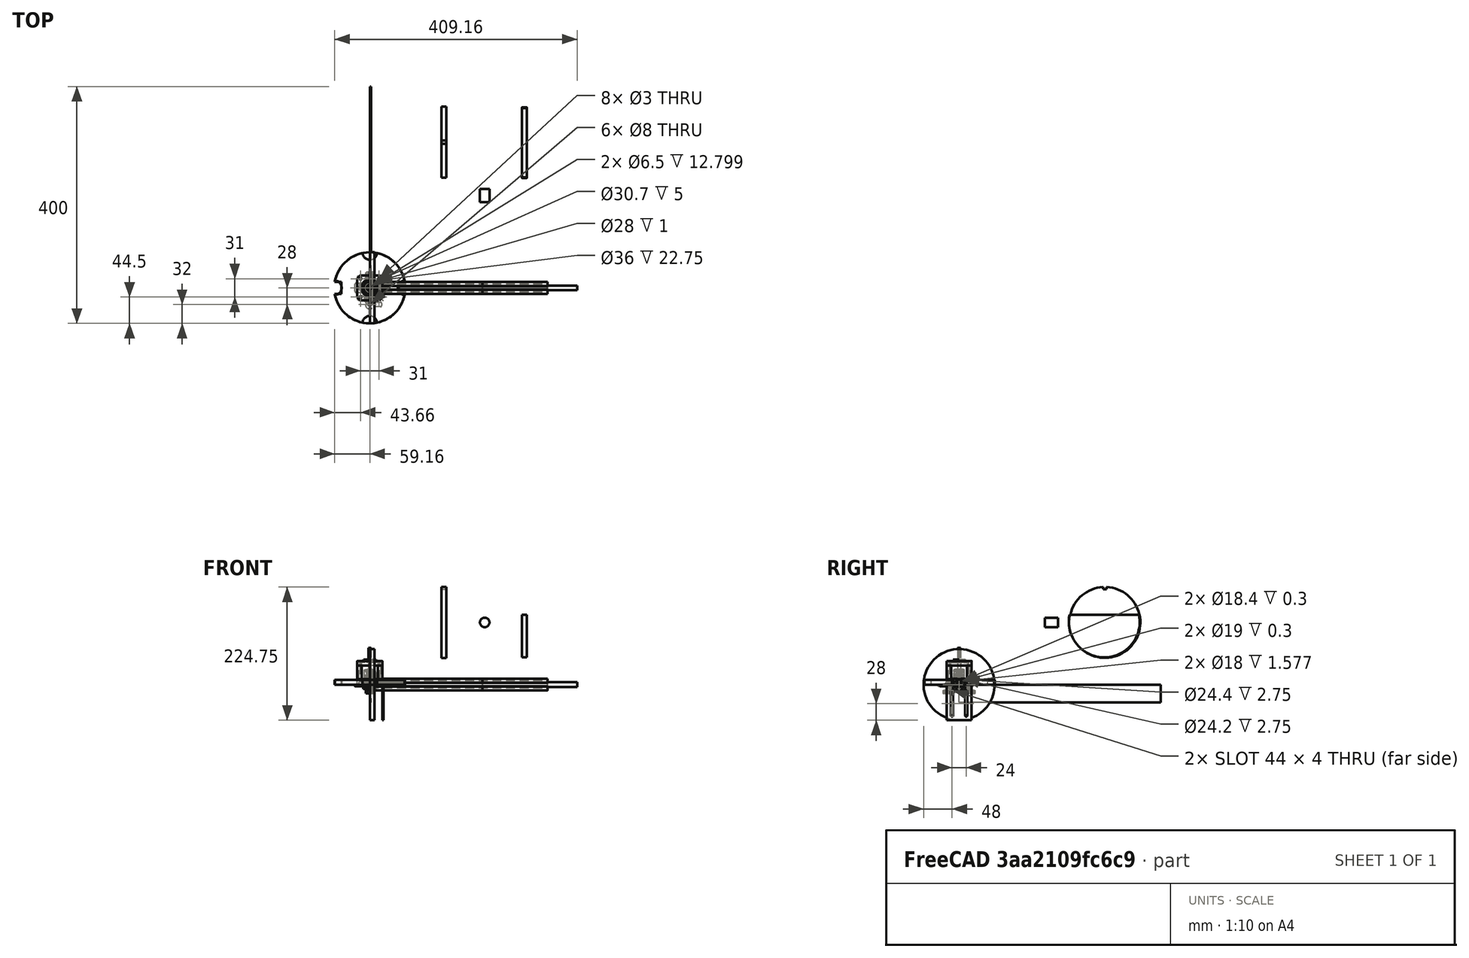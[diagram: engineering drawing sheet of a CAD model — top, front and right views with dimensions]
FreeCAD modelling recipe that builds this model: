
FCSTD DOCUMENT  (FreeCAD 0.19R)
Label: proyectoFinal
License: All rights reserved
LicenseURL: http://en.wikipedia.org/wiki/All_rights_reserved
objects: Sketcher::SketchObject×364, PartDesign::Body×273, PartDesign::Pad×225, PartDesign::Fillet×183, App::Part×132, PartDesign::Pocket×123, PartDesign::FeatureBase×92, PartDesign::Revolution×52, App::DocumentObjectGroup×42, App::LinkGroup×32, PartDesign::PolarPattern×29, PartDesign::Chamfer×21, PartDesign::Groove×8, Part::FeaturePython×8, PartDesign::Mirrored×6, PartDesign::ShapeBinder×5, PartDesign::Hole×2, PartDesign::Draft×2, PartDesign::LinearPattern×2, PartDesign::Plane×2, +5 more types
note: 2026 computed .brp shape members not serialized (recipe doc carries the construction recipe); baked Part::Feature solids carry a one-line shape summary decoded from their .brp

FEATURE [Sketcher::SketchObject] Sketch001
  FullyConstrained = false
  MapMode = 5
  Support = -> [XY_Plane003]
  sketch-geometry (46):
    g0: LineSegment StartX=3.4 StartY=2.65 StartZ=0 EndX=3.4 EndY=-2.6657 EndZ=0
    g1: LineSegment StartX=2.63162 StartY=-3.4 StartZ=0 EndX=-2.65 EndY=-3.4 EndZ=0
    g2: LineSegment StartX=-3.4 StartY=-2.63136 StartZ=0 EndX=-3.4 EndY=2.61487 EndZ=0
    g3: LineSegment StartX=-10 StartY=10 StartZ=0 EndX=-3.125 EndY=10 EndZ=0
    g4: LineSegment StartX=10 StartY=10 StartZ=0 EndX=10 EndY=3.125 EndZ=0
    g5: LineSegment StartX=10 StartY=-10 StartZ=0 EndX=3.125 EndY=-10 EndZ=0
    g6: LineSegment StartX=-10 StartY=-10 StartZ=0 EndX=-10 EndY=-3.125 EndZ=0
    g7: GeomPoint X=3e-16 Y=0 Z=0
    g8: Circle CenterX=3e-16 CenterY=0 CenterZ=0 NormalX=0 NormalY=0 NormalZ=1 AngleXU=0 Radius=2.1
    g9: LineSegment StartX=-4.76483 StartY=8.08721 StartZ=0 EndX=-3.55 EndY=8.08721 EndZ=0
    g10: LineSegment StartX=8.24722 StartY=4.75 StartZ=0 EndX=8.24722 EndY=3.55 EndZ=0
    g11: LineSegment StartX=-8.2 StartY=-4.73729 StartZ=0 EndX=-8.2 EndY=-3.55 EndZ=0
    g12: LineSegment StartX=5.5 StartY=4.75 StartZ=0 EndX=8.24722 EndY=4.75 EndZ=0
    g13: LineSegment StartX=4.75 StartY=5.50457 StartZ=0 EndX=2.65 EndY=3.4 EndZ=0
    g14: LineSegment StartX=4.75 StartY=5.50457 StartZ=0 EndX=4.75 EndY=8.08721 EndZ=0
    g15: LineSegment StartX=3.4 StartY=2.65 StartZ=0 EndX=5.5 EndY=4.75 EndZ=0
    g16: LineSegment StartX=-4.76483 StartY=5.50457 StartZ=0 EndX=-2.66166 EndY=3.4 EndZ=0
    g17: LineSegment StartX=-5.5 StartY=4.70904 StartZ=0 EndX=-3.4 EndY=2.61487 EndZ=0
    g18: LineSegment StartX=-4.76483 StartY=5.50457 StartZ=0 EndX=-4.76483 EndY=8.08721 EndZ=0
    g19: LineSegment StartX=-5.5 StartY=4.70904 StartZ=0 EndX=-8.2 EndY=4.70904 EndZ=0
    g20: LineSegment StartX=-10 StartY=3.125 StartZ=0 EndX=-10 EndY=10 EndZ=0
    g21: LineSegment StartX=-8.2 StartY=3.55 StartZ=0 EndX=-8.2 EndY=4.70904 EndZ=0
    g22: LineSegment StartX=3.55 StartY=8.08721 StartZ=0 EndX=4.75 EndY=8.08721 EndZ=0
    g23: LineSegment StartX=3.125 StartY=10 StartZ=0 EndX=10 EndY=10 EndZ=0
    g24: LineSegment StartX=-5.5 StartY=-4.73729 StartZ=0 EndX=-8.2 EndY=-4.73729 EndZ=0
    g25: LineSegment StartX=-4.75 StartY=-5.5 StartZ=0 EndX=-2.65 EndY=-3.4 EndZ=0
    g26: LineSegment StartX=-4.75 StartY=-5.5 StartZ=0 EndX=-4.75 EndY=-8.2 EndZ=0
    g27: LineSegment StartX=4.73747 StartY=-5.5 StartZ=0 EndX=4.73747 EndY=-8.2 EndZ=0
    g28: LineSegment StartX=5.5 StartY=-4.7671 StartZ=0 EndX=8.24722 EndY=-4.7671 EndZ=0
    g29: LineSegment StartX=-3.125 StartY=-10 StartZ=0 EndX=-10 EndY=-10 EndZ=0
    g30: LineSegment StartX=-3.55 StartY=-8.2 StartZ=0 EndX=-4.75 EndY=-8.2 EndZ=0
    g31: LineSegment StartX=4.73747 StartY=-8.2 StartZ=0 EndX=3.55 EndY=-8.2 EndZ=0
    g32: LineSegment StartX=10 StartY=-3.125 StartZ=0 EndX=10 EndY=-10 EndZ=0
    g33: LineSegment StartX=8.24722 StartY=-3.55 StartZ=0 EndX=8.24722 EndY=-4.7671 EndZ=0
    g34: LineSegment StartX=-2.66166 StartY=3.4 StartZ=0 EndX=2.65 EndY=3.4 EndZ=0
    g35: LineSegment StartX=-3.4 StartY=-2.63136 StartZ=0 EndX=-5.5 EndY=-4.73729 EndZ=0
    g36: LineSegment StartX=3.4 StartY=-2.6657 StartZ=0 EndX=5.5 EndY=-4.7671 EndZ=0
    g37: LineSegment StartX=2.63162 StartY=-3.4 StartZ=0 EndX=4.73747 EndY=-5.5 EndZ=0
    g38: LineSegment StartX=-3.55 StartY=-8.2 StartZ=0 EndX=-3.125 EndY=-10 EndZ=0
    g39: LineSegment StartX=3.55 StartY=-8.2 StartZ=0 EndX=3.125 EndY=-10 EndZ=0
    g40: LineSegment StartX=-3.125 StartY=10 StartZ=0 EndX=-3.55 EndY=8.08721 EndZ=0
    g41: LineSegment StartX=3.125 StartY=10 StartZ=0 EndX=3.55 EndY=8.08721 EndZ=0
    g42: LineSegment StartX=8.24722 StartY=3.55 StartZ=0 EndX=10 EndY=3.125 EndZ=0
    g43: LineSegment StartX=10 StartY=-3.125 StartZ=0 EndX=8.24722 EndY=-3.55 EndZ=0
    g44: LineSegment StartX=-10 StartY=-3.125 StartZ=0 EndX=-8.2 EndY=-3.55 EndZ=0
    g45: LineSegment StartX=-10 StartY=3.125 StartZ=0 EndX=-8.2 EndY=3.55 EndZ=0
  constraints (61):
    c: Horizontal(g1)
    c: Vertical(g0)
    c: Vertical(g2)
    c: Coincident(g23,g4)
    c: Coincident(g32,g5)
    c: Coincident(g29,g6)
    c: Coincident(g20,g3)
    c: Horizontal(g3)
    c: Horizontal(g5)
    c: Vertical(g4)
    c: Vertical(g6)
    c: PointOnObject(g7,g-1)
    c: DistanceX(g3,g7) = 10
    c: DistanceX(g-1,g23) = 10
    c: DistanceY(g7,g3) = 10
    c: DistanceX(g3,g-1) = 10
    c: DistanceY(g32,g7) = 10
    c: Coincident(g8,g7)
    c: Radius(g8) = 2.1
    c: Horizontal(g9)
    c: Vertical(g10)
    c: Vertical(g11)
    c: Coincident(g12,g15)
    c: Horizontal(g12)
    c: Coincident(g14,g13)
    c: Vertical(g14)
    c: Coincident(g15,g0)
    c: Coincident(g13,g34)
    c: Coincident(g14,g22)
    c: Coincident(g18,g16)
    c: Vertical(g18)
    c: Coincident(g19,g17)
    c: Horizontal(g19)
    c: Coincident(g9,g18)
    c: Coincident(g21,g19)
    c: Coincident(g24,g35)
    c: Horizontal(g24)
    c: Coincident(g26,g25)
    c: Vertical(g26)
    c: Coincident(g27,g37)
    c: Vertical(g27)
    c: Coincident(g28,g36)
    c: Horizontal(g28)
    c: Coincident(g11,g24)
    c: Coincident(g26,g30)
    c: Coincident(g31,g27)
    c: Coincident(g12,g10)
    c: Coincident(g28,g33)
    c: Coincident(g25,g1)
    c: Coincident(g35,g2)
    c: Coincident(g17,g2)
    c: Coincident(g16,g34)
    c: Coincident(g1,g37)
    c: Coincident(g0,g36)
    c: Coincident(g39,g5)
    c: Coincident(g40,g3)
    c: Coincident(g42,g4)
    c: Coincident(g44,g6)
    c: Coincident(g21,g45)
    c: Coincident(g33,g43)
    c: Coincident(g10,g42)
FEATURE [PartDesign::Pad] Pad001
  Direction = (0,0,1)
  Length = 300
  Length2 = 10
  Profile = -> Sketch001
  Type = 0
FEATURE [PartDesign::Fillet] Fillet011
  Base = -> Pad001 [Edge53]
  BaseFeature = -> Pad001
  Radius = 1
  SupportTransform = false
FEATURE [PartDesign::Fillet] Fillet012
  Base = -> Fillet011 [Edge114]
  BaseFeature = -> Fillet011
  Radius = 1
  SupportTransform = false
FEATURE [PartDesign::Fillet] Fillet013
  Base = -> Fillet012 [Edge137,Edge95]
  BaseFeature = -> Fillet012
  Radius = 0.5
  SupportTransform = false
FEATURE [PartDesign::Fillet] Fillet014
  Base = -> Fillet013 [Edge103]
  BaseFeature = -> Fillet013
  Radius = 0.5
  SupportTransform = false
FEATURE [PartDesign::Fillet] Fillet015
  Base = -> Fillet014 [Edge96]
  BaseFeature = -> Fillet014
  Radius = 0.5
  SupportTransform = false
FEATURE [PartDesign::Fillet] Fillet016
  Base = -> Fillet015 [Edge77]
  BaseFeature = -> Fillet015
  Radius = 0.5
  SupportTransform = false
FEATURE [PartDesign::Fillet] Fillet017
  Base = -> Fillet016 [Edge102]
  BaseFeature = -> Fillet016
  Radius = 0.5
  SupportTransform = false
FEATURE [PartDesign::Fillet] Fillet018
  Base = -> Fillet017 [Edge85]
  BaseFeature = -> Fillet017
  Radius = 0.5
  SupportTransform = false
FEATURE [PartDesign::Fillet] Fillet019
  Base = -> Fillet018 [Edge78]
  BaseFeature = -> Fillet018
  Radius = 0.5
  SupportTransform = false
FEATURE [PartDesign::Fillet] Fillet020
  Base = -> Fillet019 [Edge107]
  BaseFeature = -> Fillet019
  Radius = 0.5
  SupportTransform = false
FEATURE [PartDesign::Fillet] Fillet021
  Base = -> Fillet020 [Edge74]
  BaseFeature = -> Fillet020
  Radius = 0.5
  SupportTransform = false
FEATURE [PartDesign::Body] Body001
  Group = -> [Sketch001,Pad001,Fillet011,Fillet012,Fillet013,Fillet014,Fillet015,Fillet016,Fillet017,Fillet018,Fillet019,Fillet020,Fillet021]
  Origin = -> Origin003
  Placement = pos=(0,0,0) rot=(0,1,0;1.5708rad)
  Tip = -> Fillet021
FEATURE [App::Part] Part001  label="2020-300-002"
  Group = -> [Body001]
  Origin = -> Origin002
  Placement = pos=(20,330,10) rot=(0,0,1;0rad)
FEATURE [Sketcher::SketchObject] Sketch002
  FullyConstrained = false
  MapMode = 5
  Support = -> [XY_Plane005]
  sketch-geometry (46):
    g0: LineSegment StartX=3.4 StartY=2.65 StartZ=0 EndX=3.4 EndY=-2.6657 EndZ=0
    g1: LineSegment StartX=2.63162 StartY=-3.4 StartZ=0 EndX=-2.65 EndY=-3.4 EndZ=0
    g2: LineSegment StartX=-3.4 StartY=-2.63136 StartZ=0 EndX=-3.4 EndY=2.61487 EndZ=0
    g3: LineSegment StartX=-10 StartY=10 StartZ=0 EndX=-3.125 EndY=10 EndZ=0
    g4: LineSegment StartX=10 StartY=10 StartZ=0 EndX=10 EndY=3.125 EndZ=0
    g5: LineSegment StartX=10 StartY=-10 StartZ=0 EndX=3.125 EndY=-10 EndZ=0
    g6: LineSegment StartX=-10 StartY=-10 StartZ=0 EndX=-10 EndY=-3.125 EndZ=0
    g7: GeomPoint X=3e-16 Y=0 Z=0
    g8: Circle CenterX=3e-16 CenterY=0 CenterZ=0 NormalX=0 NormalY=0 NormalZ=1 AngleXU=0 Radius=2.1
    g9: LineSegment StartX=-4.76483 StartY=8.08721 StartZ=0 EndX=-3.55 EndY=8.08721 EndZ=0
    g10: LineSegment StartX=8.24722 StartY=4.75 StartZ=0 EndX=8.24722 EndY=3.55 EndZ=0
    g11: LineSegment StartX=-8.2 StartY=-4.73729 StartZ=0 EndX=-8.2 EndY=-3.55 EndZ=0
    g12: LineSegment StartX=5.5 StartY=4.75 StartZ=0 EndX=8.24722 EndY=4.75 EndZ=0
    g13: LineSegment StartX=4.75 StartY=5.50457 StartZ=0 EndX=2.65 EndY=3.4 EndZ=0
    g14: LineSegment StartX=4.75 StartY=5.50457 StartZ=0 EndX=4.75 EndY=8.08721 EndZ=0
    g15: LineSegment StartX=3.4 StartY=2.65 StartZ=0 EndX=5.5 EndY=4.75 EndZ=0
    g16: LineSegment StartX=-4.76483 StartY=5.50457 StartZ=0 EndX=-2.66166 EndY=3.4 EndZ=0
    g17: LineSegment StartX=-5.5 StartY=4.70904 StartZ=0 EndX=-3.4 EndY=2.61487 EndZ=0
    g18: LineSegment StartX=-4.76483 StartY=5.50457 StartZ=0 EndX=-4.76483 EndY=8.08721 EndZ=0
    g19: LineSegment StartX=-5.5 StartY=4.70904 StartZ=0 EndX=-8.2 EndY=4.70904 EndZ=0
    g20: LineSegment StartX=-10 StartY=3.125 StartZ=0 EndX=-10 EndY=10 EndZ=0
    g21: LineSegment StartX=-8.2 StartY=3.55 StartZ=0 EndX=-8.2 EndY=4.70904 EndZ=0
    g22: LineSegment StartX=3.55 StartY=8.08721 StartZ=0 EndX=4.75 EndY=8.08721 EndZ=0
    g23: LineSegment StartX=3.125 StartY=10 StartZ=0 EndX=10 EndY=10 EndZ=0
    g24: LineSegment StartX=-5.5 StartY=-4.73729 StartZ=0 EndX=-8.2 EndY=-4.73729 EndZ=0
    g25: LineSegment StartX=-4.75 StartY=-5.5 StartZ=0 EndX=-2.65 EndY=-3.4 EndZ=0
    g26: LineSegment StartX=-4.75 StartY=-5.5 StartZ=0 EndX=-4.75 EndY=-8.2 EndZ=0
    g27: LineSegment StartX=4.73747 StartY=-5.5 StartZ=0 EndX=4.73747 EndY=-8.2 EndZ=0
    g28: LineSegment StartX=5.5 StartY=-4.7671 StartZ=0 EndX=8.24722 EndY=-4.7671 EndZ=0
    g29: LineSegment StartX=-3.125 StartY=-10 StartZ=0 EndX=-10 EndY=-10 EndZ=0
    g30: LineSegment StartX=-3.55 StartY=-8.2 StartZ=0 EndX=-4.75 EndY=-8.2 EndZ=0
    g31: LineSegment StartX=4.73747 StartY=-8.2 StartZ=0 EndX=3.55 EndY=-8.2 EndZ=0
    g32: LineSegment StartX=10 StartY=-3.125 StartZ=0 EndX=10 EndY=-10 EndZ=0
    g33: LineSegment StartX=8.24722 StartY=-3.55 StartZ=0 EndX=8.24722 EndY=-4.7671 EndZ=0
    g34: LineSegment StartX=-2.66166 StartY=3.4 StartZ=0 EndX=2.65 EndY=3.4 EndZ=0
    g35: LineSegment StartX=-3.4 StartY=-2.63136 StartZ=0 EndX=-5.5 EndY=-4.73729 EndZ=0
    g36: LineSegment StartX=3.4 StartY=-2.6657 StartZ=0 EndX=5.5 EndY=-4.7671 EndZ=0
    g37: LineSegment StartX=2.63162 StartY=-3.4 StartZ=0 EndX=4.73747 EndY=-5.5 EndZ=0
    g38: LineSegment StartX=-3.55 StartY=-8.2 StartZ=0 EndX=-3.125 EndY=-10 EndZ=0
    g39: LineSegment StartX=3.55 StartY=-8.2 StartZ=0 EndX=3.125 EndY=-10 EndZ=0
    g40: LineSegment StartX=-3.125 StartY=10 StartZ=0 EndX=-3.55 EndY=8.08721 EndZ=0
    g41: LineSegment StartX=3.125 StartY=10 StartZ=0 EndX=3.55 EndY=8.08721 EndZ=0
    g42: LineSegment StartX=8.24722 StartY=3.55 StartZ=0 EndX=10 EndY=3.125 EndZ=0
    g43: LineSegment StartX=10 StartY=-3.125 StartZ=0 EndX=8.24722 EndY=-3.55 EndZ=0
    g44: LineSegment StartX=-10 StartY=-3.125 StartZ=0 EndX=-8.2 EndY=-3.55 EndZ=0
    g45: LineSegment StartX=-10 StartY=3.125 StartZ=0 EndX=-8.2 EndY=3.55 EndZ=0
  constraints (61):
    c: Horizontal(g1)
    c: Vertical(g0)
    c: Vertical(g2)
    c: Coincident(g23,g4)
    c: Coincident(g32,g5)
    c: Coincident(g29,g6)
    c: Coincident(g20,g3)
    c: Horizontal(g3)
    c: Horizontal(g5)
    c: Vertical(g4)
    c: Vertical(g6)
    c: PointOnObject(g7,g-1)
    c: DistanceX(g3,g7) = 10
    c: DistanceX(g-1,g23) = 10
    c: DistanceY(g7,g3) = 10
    c: DistanceX(g3,g-1) = 10
    c: DistanceY(g32,g7) = 10
    c: Coincident(g8,g7)
    c: Radius(g8) = 2.1
    c: Horizontal(g9)
    c: Vertical(g10)
    c: Vertical(g11)
    c: Coincident(g12,g15)
    c: Horizontal(g12)
    c: Coincident(g14,g13)
    c: Vertical(g14)
    c: Coincident(g15,g0)
    c: Coincident(g13,g34)
    c: Coincident(g14,g22)
    c: Coincident(g18,g16)
    c: Vertical(g18)
    c: Coincident(g19,g17)
    c: Horizontal(g19)
    c: Coincident(g9,g18)
    c: Coincident(g21,g19)
    c: Coincident(g24,g35)
    c: Horizontal(g24)
    c: Coincident(g26,g25)
    c: Vertical(g26)
    c: Coincident(g27,g37)
    c: Vertical(g27)
    c: Coincident(g28,g36)
    c: Horizontal(g28)
    c: Coincident(g11,g24)
    c: Coincident(g26,g30)
    c: Coincident(g31,g27)
    c: Coincident(g12,g10)
    c: Coincident(g28,g33)
    c: Coincident(g25,g1)
    c: Coincident(g35,g2)
    c: Coincident(g17,g2)
    c: Coincident(g16,g34)
    c: Coincident(g1,g37)
    c: Coincident(g0,g36)
    c: Coincident(g39,g5)
    c: Coincident(g40,g3)
    c: Coincident(g42,g4)
    c: Coincident(g44,g6)
    c: Coincident(g21,g45)
    c: Coincident(g33,g43)
    c: Coincident(g10,g42)
FEATURE [PartDesign::Pad] Pad002
  Direction = (0,0,1)
  Length = 300
  Length2 = 10
  Profile = -> Sketch002
  Type = 0
FEATURE [PartDesign::Fillet] Fillet022
  Base = -> Pad002 [Edge53]
  BaseFeature = -> Pad002
  Radius = 1
  SupportTransform = false
FEATURE [PartDesign::Fillet] Fillet023
  Base = -> Fillet022 [Edge114]
  BaseFeature = -> Fillet022
  Radius = 1
  SupportTransform = false
FEATURE [PartDesign::Fillet] Fillet024
  Base = -> Fillet023 [Edge137,Edge95]
  BaseFeature = -> Fillet023
  Radius = 0.5
  SupportTransform = false
FEATURE [PartDesign::Fillet] Fillet025
  Base = -> Fillet024 [Edge103]
  BaseFeature = -> Fillet024
  Radius = 0.5
  SupportTransform = false
FEATURE [PartDesign::Fillet] Fillet026
  Base = -> Fillet025 [Edge96]
  BaseFeature = -> Fillet025
  Radius = 0.5
  SupportTransform = false
FEATURE [PartDesign::Fillet] Fillet027
  Base = -> Fillet026 [Edge77]
  BaseFeature = -> Fillet026
  Radius = 0.5
  SupportTransform = false
FEATURE [PartDesign::Fillet] Fillet028
  Base = -> Fillet027 [Edge102]
  BaseFeature = -> Fillet027
  Radius = 0.5
  SupportTransform = false
FEATURE [PartDesign::Fillet] Fillet029
  Base = -> Fillet028 [Edge85]
  BaseFeature = -> Fillet028
  Radius = 0.5
  SupportTransform = false
FEATURE [PartDesign::Fillet] Fillet030
  Base = -> Fillet029 [Edge78]
  BaseFeature = -> Fillet029
  Radius = 0.5
  SupportTransform = false
FEATURE [PartDesign::Fillet] Fillet031
  Base = -> Fillet030 [Edge107]
  BaseFeature = -> Fillet030
  Radius = 0.5
  SupportTransform = false
FEATURE [PartDesign::Fillet] Fillet032
  Base = -> Fillet031 [Edge74]
  BaseFeature = -> Fillet031
  Radius = 0.5
  SupportTransform = false
FEATURE [PartDesign::Body] Body002
  Group = -> [Sketch002,Pad002,Fillet022,Fillet023,Fillet024,Fillet025,Fillet026,Fillet027,Fillet028,Fillet029,Fillet030,Fillet031,Fillet032]
  Origin = -> Origin005
  Placement = pos=(0,0,0) rot=(0,1,0;1.5708rad)
  Tip = -> Fillet032
FEATURE [App::Part] Part002  label="2020-300-003"
  Group = -> [Body002]
  Origin = -> Origin004
  Placement = pos=(10,20,10) rot=(0,0,1;1.5708rad)
FEATURE [Sketcher::SketchObject] Sketch003
  FullyConstrained = false
  MapMode = 5
  Support = -> [XY_Plane007]
  sketch-geometry (46):
    g0: LineSegment StartX=3.4 StartY=2.65 StartZ=0 EndX=3.4 EndY=-2.6657 EndZ=0
    g1: LineSegment StartX=2.63162 StartY=-3.4 StartZ=0 EndX=-2.65 EndY=-3.4 EndZ=0
    g2: LineSegment StartX=-3.4 StartY=-2.63136 StartZ=0 EndX=-3.4 EndY=2.61487 EndZ=0
    g3: LineSegment StartX=-10 StartY=10 StartZ=0 EndX=-3.125 EndY=10 EndZ=0
    g4: LineSegment StartX=10 StartY=10 StartZ=0 EndX=10 EndY=3.125 EndZ=0
    g5: LineSegment StartX=10 StartY=-10 StartZ=0 EndX=3.125 EndY=-10 EndZ=0
    g6: LineSegment StartX=-10 StartY=-10 StartZ=0 EndX=-10 EndY=-3.125 EndZ=0
    g7: GeomPoint X=3e-16 Y=0 Z=0
    g8: Circle CenterX=3e-16 CenterY=0 CenterZ=0 NormalX=0 NormalY=0 NormalZ=1 AngleXU=0 Radius=2.1
    g9: LineSegment StartX=-4.76483 StartY=8.08721 StartZ=0 EndX=-3.55 EndY=8.08721 EndZ=0
    g10: LineSegment StartX=8.24722 StartY=4.75 StartZ=0 EndX=8.24722 EndY=3.55 EndZ=0
    g11: LineSegment StartX=-8.2 StartY=-4.73729 StartZ=0 EndX=-8.2 EndY=-3.55 EndZ=0
    g12: LineSegment StartX=5.5 StartY=4.75 StartZ=0 EndX=8.24722 EndY=4.75 EndZ=0
    g13: LineSegment StartX=4.75 StartY=5.50457 StartZ=0 EndX=2.65 EndY=3.4 EndZ=0
    g14: LineSegment StartX=4.75 StartY=5.50457 StartZ=0 EndX=4.75 EndY=8.08721 EndZ=0
    g15: LineSegment StartX=3.4 StartY=2.65 StartZ=0 EndX=5.5 EndY=4.75 EndZ=0
    g16: LineSegment StartX=-4.76483 StartY=5.50457 StartZ=0 EndX=-2.66166 EndY=3.4 EndZ=0
    g17: LineSegment StartX=-5.5 StartY=4.70904 StartZ=0 EndX=-3.4 EndY=2.61487 EndZ=0
    g18: LineSegment StartX=-4.76483 StartY=5.50457 StartZ=0 EndX=-4.76483 EndY=8.08721 EndZ=0
    g19: LineSegment StartX=-5.5 StartY=4.70904 StartZ=0 EndX=-8.2 EndY=4.70904 EndZ=0
    g20: LineSegment StartX=-10 StartY=3.125 StartZ=0 EndX=-10 EndY=10 EndZ=0
    g21: LineSegment StartX=-8.2 StartY=3.55 StartZ=0 EndX=-8.2 EndY=4.70904 EndZ=0
    g22: LineSegment StartX=3.55 StartY=8.08721 StartZ=0 EndX=4.75 EndY=8.08721 EndZ=0
    g23: LineSegment StartX=3.125 StartY=10 StartZ=0 EndX=10 EndY=10 EndZ=0
    g24: LineSegment StartX=-5.5 StartY=-4.73729 StartZ=0 EndX=-8.2 EndY=-4.73729 EndZ=0
    g25: LineSegment StartX=-4.75 StartY=-5.5 StartZ=0 EndX=-2.65 EndY=-3.4 EndZ=0
    g26: LineSegment StartX=-4.75 StartY=-5.5 StartZ=0 EndX=-4.75 EndY=-8.2 EndZ=0
    g27: LineSegment StartX=4.73747 StartY=-5.5 StartZ=0 EndX=4.73747 EndY=-8.2 EndZ=0
    g28: LineSegment StartX=5.5 StartY=-4.7671 StartZ=0 EndX=8.24722 EndY=-4.7671 EndZ=0
    g29: LineSegment StartX=-3.125 StartY=-10 StartZ=0 EndX=-10 EndY=-10 EndZ=0
    g30: LineSegment StartX=-3.55 StartY=-8.2 StartZ=0 EndX=-4.75 EndY=-8.2 EndZ=0
    g31: LineSegment StartX=4.73747 StartY=-8.2 StartZ=0 EndX=3.55 EndY=-8.2 EndZ=0
    g32: LineSegment StartX=10 StartY=-3.125 StartZ=0 EndX=10 EndY=-10 EndZ=0
    g33: LineSegment StartX=8.24722 StartY=-3.55 StartZ=0 EndX=8.24722 EndY=-4.7671 EndZ=0
    g34: LineSegment StartX=-2.66166 StartY=3.4 StartZ=0 EndX=2.65 EndY=3.4 EndZ=0
    g35: LineSegment StartX=-3.4 StartY=-2.63136 StartZ=0 EndX=-5.5 EndY=-4.73729 EndZ=0
    g36: LineSegment StartX=3.4 StartY=-2.6657 StartZ=0 EndX=5.5 EndY=-4.7671 EndZ=0
    g37: LineSegment StartX=2.63162 StartY=-3.4 StartZ=0 EndX=4.73747 EndY=-5.5 EndZ=0
    g38: LineSegment StartX=-3.55 StartY=-8.2 StartZ=0 EndX=-3.125 EndY=-10 EndZ=0
    g39: LineSegment StartX=3.55 StartY=-8.2 StartZ=0 EndX=3.125 EndY=-10 EndZ=0
    g40: LineSegment StartX=-3.125 StartY=10 StartZ=0 EndX=-3.55 EndY=8.08721 EndZ=0
    g41: LineSegment StartX=3.125 StartY=10 StartZ=0 EndX=3.55 EndY=8.08721 EndZ=0
    g42: LineSegment StartX=8.24722 StartY=3.55 StartZ=0 EndX=10 EndY=3.125 EndZ=0
    g43: LineSegment StartX=10 StartY=-3.125 StartZ=0 EndX=8.24722 EndY=-3.55 EndZ=0
    g44: LineSegment StartX=-10 StartY=-3.125 StartZ=0 EndX=-8.2 EndY=-3.55 EndZ=0
    g45: LineSegment StartX=-10 StartY=3.125 StartZ=0 EndX=-8.2 EndY=3.55 EndZ=0
  constraints (61):
    c: Horizontal(g1)
    c: Vertical(g0)
    c: Vertical(g2)
    c: Coincident(g23,g4)
    c: Coincident(g32,g5)
    c: Coincident(g29,g6)
    c: Coincident(g20,g3)
    c: Horizontal(g3)
    c: Horizontal(g5)
    c: Vertical(g4)
    c: Vertical(g6)
    c: PointOnObject(g7,g-1)
    c: DistanceX(g3,g7) = 10
    c: DistanceX(g-1,g23) = 10
    c: DistanceY(g7,g3) = 10
    c: DistanceX(g3,g-1) = 10
    c: DistanceY(g32,g7) = 10
    c: Coincident(g8,g7)
    c: Radius(g8) = 2.1
    c: Horizontal(g9)
    c: Vertical(g10)
    c: Vertical(g11)
    c: Coincident(g12,g15)
    c: Horizontal(g12)
    c: Coincident(g14,g13)
    c: Vertical(g14)
    c: Coincident(g15,g0)
    c: Coincident(g13,g34)
    c: Coincident(g14,g22)
    c: Coincident(g18,g16)
    c: Vertical(g18)
    c: Coincident(g19,g17)
    c: Horizontal(g19)
    c: Coincident(g9,g18)
    c: Coincident(g21,g19)
    c: Coincident(g24,g35)
    c: Horizontal(g24)
    c: Coincident(g26,g25)
    c: Vertical(g26)
    c: Coincident(g27,g37)
    c: Vertical(g27)
    c: Coincident(g28,g36)
    c: Horizontal(g28)
    c: Coincident(g11,g24)
    c: Coincident(g26,g30)
    c: Coincident(g31,g27)
    c: Coincident(g12,g10)
    c: Coincident(g28,g33)
    c: Coincident(g25,g1)
    c: Coincident(g35,g2)
    c: Coincident(g17,g2)
    c: Coincident(g16,g34)
    c: Coincident(g1,g37)
    c: Coincident(g0,g36)
    c: Coincident(g39,g5)
    c: Coincident(g40,g3)
    c: Coincident(g42,g4)
    c: Coincident(g44,g6)
    c: Coincident(g21,g45)
    c: Coincident(g33,g43)
    c: Coincident(g10,g42)
FEATURE [PartDesign::Pad] Pad003
  Direction = (0,0,1)
  Length = 300
  Length2 = 10
  Profile = -> Sketch003
  Type = 0
FEATURE [PartDesign::Fillet] Fillet033
  Base = -> Pad003 [Edge53]
  BaseFeature = -> Pad003
  Radius = 1
  SupportTransform = false
FEATURE [PartDesign::Fillet] Fillet034
  Base = -> Fillet033 [Edge114]
  BaseFeature = -> Fillet033
  Radius = 1
  SupportTransform = false
FEATURE [PartDesign::Fillet] Fillet035
  Base = -> Fillet034 [Edge137,Edge95]
  BaseFeature = -> Fillet034
  Radius = 0.5
  SupportTransform = false
FEATURE [PartDesign::Fillet] Fillet036
  Base = -> Fillet035 [Edge103]
  BaseFeature = -> Fillet035
  Radius = 0.5
  SupportTransform = false
FEATURE [PartDesign::Fillet] Fillet037
  Base = -> Fillet036 [Edge96]
  BaseFeature = -> Fillet036
  Radius = 0.5
  SupportTransform = false
FEATURE [PartDesign::Fillet] Fillet038
  Base = -> Fillet037 [Edge77]
  BaseFeature = -> Fillet037
  Radius = 0.5
  SupportTransform = false
FEATURE [PartDesign::Fillet] Fillet039
  Base = -> Fillet038 [Edge102]
  BaseFeature = -> Fillet038
  Radius = 0.5
  SupportTransform = false
FEATURE [PartDesign::Fillet] Fillet040
  Base = -> Fillet039 [Edge85]
  BaseFeature = -> Fillet039
  Radius = 0.5
  SupportTransform = false
FEATURE [PartDesign::Fillet] Fillet041
  Base = -> Fillet040 [Edge78]
  BaseFeature = -> Fillet040
  Radius = 0.5
  SupportTransform = false
FEATURE [PartDesign::Fillet] Fillet042
  Base = -> Fillet041 [Edge107]
  BaseFeature = -> Fillet041
  Radius = 0.5
  SupportTransform = false
FEATURE [PartDesign::Fillet] Fillet043
  Base = -> Fillet042 [Edge74]
  BaseFeature = -> Fillet042
  Radius = 0.5
  SupportTransform = false
FEATURE [PartDesign::Body] Body003
  Group = -> [Sketch003,Pad003,Fillet033,Fillet034,Fillet035,Fillet036,Fillet037,Fillet038,Fillet039,Fillet040,Fillet041,Fillet042,Fillet043]
  Origin = -> Origin007
  Placement = pos=(0,0,0) rot=(0,1,0;1.5708rad)
  Tip = -> Fillet043
FEATURE [App::Part] Part003  label="2020-300-004"
  Group = -> [Body003]
  Origin = -> Origin006
  Placement = pos=(330,20,10) rot=(0,0,1;1.5708rad)
FEATURE [Sketcher::SketchObject] Sketch004
  FullyConstrained = false
  MapMode = 5
  Support = -> [XY_Plane009]
  sketch-geometry (46):
    g0: LineSegment StartX=3.4 StartY=2.65 StartZ=0 EndX=3.4 EndY=-2.6657 EndZ=0
    g1: LineSegment StartX=2.63162 StartY=-3.4 StartZ=0 EndX=-2.65 EndY=-3.4 EndZ=0
    g2: LineSegment StartX=-3.4 StartY=-2.63136 StartZ=0 EndX=-3.4 EndY=2.61487 EndZ=0
    g3: LineSegment StartX=-10 StartY=10 StartZ=0 EndX=-3.125 EndY=10 EndZ=0
    g4: LineSegment StartX=10 StartY=10 StartZ=0 EndX=10 EndY=3.125 EndZ=0
    g5: LineSegment StartX=10 StartY=-10 StartZ=0 EndX=3.125 EndY=-10 EndZ=0
    g6: LineSegment StartX=-10 StartY=-10 StartZ=0 EndX=-10 EndY=-3.125 EndZ=0
    g7: GeomPoint X=3e-16 Y=0 Z=0
    g8: Circle CenterX=3e-16 CenterY=0 CenterZ=0 NormalX=0 NormalY=0 NormalZ=1 AngleXU=0 Radius=2.1
    g9: LineSegment StartX=-4.76483 StartY=8.08721 StartZ=0 EndX=-3.55 EndY=8.08721 EndZ=0
    g10: LineSegment StartX=8.24722 StartY=4.75 StartZ=0 EndX=8.24722 EndY=3.55 EndZ=0
    g11: LineSegment StartX=-8.2 StartY=-4.73729 StartZ=0 EndX=-8.2 EndY=-3.55 EndZ=0
    g12: LineSegment StartX=5.5 StartY=4.75 StartZ=0 EndX=8.24722 EndY=4.75 EndZ=0
    g13: LineSegment StartX=4.75 StartY=5.50457 StartZ=0 EndX=2.65 EndY=3.4 EndZ=0
    g14: LineSegment StartX=4.75 StartY=5.50457 StartZ=0 EndX=4.75 EndY=8.08721 EndZ=0
    g15: LineSegment StartX=3.4 StartY=2.65 StartZ=0 EndX=5.5 EndY=4.75 EndZ=0
    g16: LineSegment StartX=-4.76483 StartY=5.50457 StartZ=0 EndX=-2.66166 EndY=3.4 EndZ=0
    g17: LineSegment StartX=-5.5 StartY=4.70904 StartZ=0 EndX=-3.4 EndY=2.61487 EndZ=0
    g18: LineSegment StartX=-4.76483 StartY=5.50457 StartZ=0 EndX=-4.76483 EndY=8.08721 EndZ=0
    g19: LineSegment StartX=-5.5 StartY=4.70904 StartZ=0 EndX=-8.2 EndY=4.70904 EndZ=0
    g20: LineSegment StartX=-10 StartY=3.125 StartZ=0 EndX=-10 EndY=10 EndZ=0
    g21: LineSegment StartX=-8.2 StartY=3.55 StartZ=0 EndX=-8.2 EndY=4.70904 EndZ=0
    g22: LineSegment StartX=3.55 StartY=8.08721 StartZ=0 EndX=4.75 EndY=8.08721 EndZ=0
    g23: LineSegment StartX=3.125 StartY=10 StartZ=0 EndX=10 EndY=10 EndZ=0
    g24: LineSegment StartX=-5.5 StartY=-4.73729 StartZ=0 EndX=-8.2 EndY=-4.73729 EndZ=0
    g25: LineSegment StartX=-4.75 StartY=-5.5 StartZ=0 EndX=-2.65 EndY=-3.4 EndZ=0
    g26: LineSegment StartX=-4.75 StartY=-5.5 StartZ=0 EndX=-4.75 EndY=-8.2 EndZ=0
    g27: LineSegment StartX=4.73747 StartY=-5.5 StartZ=0 EndX=4.73747 EndY=-8.2 EndZ=0
    g28: LineSegment StartX=5.5 StartY=-4.7671 StartZ=0 EndX=8.24722 EndY=-4.7671 EndZ=0
    g29: LineSegment StartX=-3.125 StartY=-10 StartZ=0 EndX=-10 EndY=-10 EndZ=0
    g30: LineSegment StartX=-3.55 StartY=-8.2 StartZ=0 EndX=-4.75 EndY=-8.2 EndZ=0
    g31: LineSegment StartX=4.73747 StartY=-8.2 StartZ=0 EndX=3.55 EndY=-8.2 EndZ=0
    g32: LineSegment StartX=10 StartY=-3.125 StartZ=0 EndX=10 EndY=-10 EndZ=0
    g33: LineSegment StartX=8.24722 StartY=-3.55 StartZ=0 EndX=8.24722 EndY=-4.7671 EndZ=0
    g34: LineSegment StartX=-2.66166 StartY=3.4 StartZ=0 EndX=2.65 EndY=3.4 EndZ=0
    g35: LineSegment StartX=-3.4 StartY=-2.63136 StartZ=0 EndX=-5.5 EndY=-4.73729 EndZ=0
    g36: LineSegment StartX=3.4 StartY=-2.6657 StartZ=0 EndX=5.5 EndY=-4.7671 EndZ=0
    g37: LineSegment StartX=2.63162 StartY=-3.4 StartZ=0 EndX=4.73747 EndY=-5.5 EndZ=0
    g38: LineSegment StartX=-3.55 StartY=-8.2 StartZ=0 EndX=-3.125 EndY=-10 EndZ=0
    g39: LineSegment StartX=3.55 StartY=-8.2 StartZ=0 EndX=3.125 EndY=-10 EndZ=0
    g40: LineSegment StartX=-3.125 StartY=10 StartZ=0 EndX=-3.55 EndY=8.08721 EndZ=0
    g41: LineSegment StartX=3.125 StartY=10 StartZ=0 EndX=3.55 EndY=8.08721 EndZ=0
    g42: LineSegment StartX=8.24722 StartY=3.55 StartZ=0 EndX=10 EndY=3.125 EndZ=0
    g43: LineSegment StartX=10 StartY=-3.125 StartZ=0 EndX=8.24722 EndY=-3.55 EndZ=0
    g44: LineSegment StartX=-10 StartY=-3.125 StartZ=0 EndX=-8.2 EndY=-3.55 EndZ=0
    g45: LineSegment StartX=-10 StartY=3.125 StartZ=0 EndX=-8.2 EndY=3.55 EndZ=0
  constraints (61):
    c: Horizontal(g1)
    c: Vertical(g0)
    c: Vertical(g2)
    c: Coincident(g23,g4)
    c: Coincident(g32,g5)
    c: Coincident(g29,g6)
    c: Coincident(g20,g3)
    c: Horizontal(g3)
    c: Horizontal(g5)
    c: Vertical(g4)
    c: Vertical(g6)
    c: PointOnObject(g7,g-1)
    c: DistanceX(g3,g7) = 10
    c: DistanceX(g-1,g23) = 10
    c: DistanceY(g7,g3) = 10
    c: DistanceX(g3,g-1) = 10
    c: DistanceY(g32,g7) = 10
    c: Coincident(g8,g7)
    c: Radius(g8) = 2.1
    c: Horizontal(g9)
    c: Vertical(g10)
    c: Vertical(g11)
    c: Coincident(g12,g15)
    c: Horizontal(g12)
    c: Coincident(g14,g13)
    c: Vertical(g14)
    c: Coincident(g15,g0)
    c: Coincident(g13,g34)
    c: Coincident(g14,g22)
    c: Coincident(g18,g16)
    c: Vertical(g18)
    c: Coincident(g19,g17)
    c: Horizontal(g19)
    c: Coincident(g9,g18)
    c: Coincident(g21,g19)
    c: Coincident(g24,g35)
    c: Horizontal(g24)
    c: Coincident(g26,g25)
    c: Vertical(g26)
    c: Coincident(g27,g37)
    c: Vertical(g27)
    c: Coincident(g28,g36)
    c: Horizontal(g28)
    c: Coincident(g11,g24)
    c: Coincident(g26,g30)
    c: Coincident(g31,g27)
    c: Coincident(g12,g10)
    c: Coincident(g28,g33)
    c: Coincident(g25,g1)
    c: Coincident(g35,g2)
    c: Coincident(g17,g2)
    c: Coincident(g16,g34)
    c: Coincident(g1,g37)
    c: Coincident(g0,g36)
    c: Coincident(g39,g5)
    c: Coincident(g40,g3)
    c: Coincident(g42,g4)
    c: Coincident(g44,g6)
    c: Coincident(g21,g45)
    c: Coincident(g33,g43)
    c: Coincident(g10,g42)
FEATURE [PartDesign::Pad] Pad004
  Direction = (0,0,1)
  Length = 190
  Length2 = 10
  Profile = -> Sketch004
  Type = 0
FEATURE [PartDesign::Fillet] Fillet044
  Base = -> Pad004 [Edge53]
  BaseFeature = -> Pad004
  Radius = 1
  SupportTransform = false
FEATURE [PartDesign::Fillet] Fillet045
  Base = -> Fillet044 [Edge114]
  BaseFeature = -> Fillet044
  Radius = 1
  SupportTransform = false
FEATURE [PartDesign::Fillet] Fillet046
  Base = -> Fillet045 [Edge137,Edge95]
  BaseFeature = -> Fillet045
  Radius = 0.5
  SupportTransform = false
FEATURE [PartDesign::Fillet] Fillet047
  Base = -> Fillet046 [Edge103]
  BaseFeature = -> Fillet046
  Radius = 0.5
  SupportTransform = false
FEATURE [PartDesign::Fillet] Fillet048
  Base = -> Fillet047 [Edge96]
  BaseFeature = -> Fillet047
  Radius = 0.5
  SupportTransform = false
FEATURE [PartDesign::Fillet] Fillet049
  Base = -> Fillet048 [Edge77]
  BaseFeature = -> Fillet048
  Radius = 0.5
  SupportTransform = false
FEATURE [PartDesign::Fillet] Fillet050
  Base = -> Fillet049 [Edge102]
  BaseFeature = -> Fillet049
  Radius = 0.5
  SupportTransform = false
FEATURE [PartDesign::Fillet] Fillet051
  Base = -> Fillet050 [Edge85]
  BaseFeature = -> Fillet050
  Radius = 0.5
  SupportTransform = false
FEATURE [PartDesign::Fillet] Fillet052
  Base = -> Fillet051 [Edge78]
  BaseFeature = -> Fillet051
  Radius = 0.5
  SupportTransform = false
FEATURE [PartDesign::Fillet] Fillet053
  Base = -> Fillet052 [Edge107]
  BaseFeature = -> Fillet052
  Radius = 0.5
  SupportTransform = false
FEATURE [PartDesign::Fillet] Fillet054
  Base = -> Fillet053 [Edge74]
  BaseFeature = -> Fillet053
  Radius = 0.5
  SupportTransform = false
FEATURE [PartDesign::Body] Body004
  Group = -> [Sketch004,Pad004,Fillet044,Fillet045,Fillet046,Fillet047,Fillet048,Fillet049,Fillet050,Fillet051,Fillet052,Fillet053,Fillet054]
  Origin = -> Origin009
  Placement = pos=(0,0,0) rot=(0,1,0;1.5708rad)
  Tip = -> Fillet054
FEATURE [Sketcher::SketchObject] Sketch
  FullyConstrained = false
  MapMode = 4
  Placement = pos=(0,0,0) rot=(0.707107,0.707107,0;3.14159rad)
  Support = -> [Body004]
  sketch-geometry (46):
    g0: LineSegment StartX=3.4 StartY=2.65 StartZ=0 EndX=3.4 EndY=-2.6657 EndZ=0
    g1: LineSegment StartX=2.63162 StartY=-3.4 StartZ=0 EndX=-2.65 EndY=-3.4 EndZ=0
    g2: LineSegment StartX=-3.4 StartY=-2.63136 StartZ=0 EndX=-3.4 EndY=2.61487 EndZ=0
    g3: LineSegment StartX=-10 StartY=10 StartZ=0 EndX=-3.125 EndY=10 EndZ=0
    g4: LineSegment StartX=10 StartY=10 StartZ=0 EndX=10 EndY=3.125 EndZ=0
    g5: LineSegment StartX=10 StartY=-10 StartZ=0 EndX=3.125 EndY=-10 EndZ=0
    g6: LineSegment StartX=-10 StartY=-10 StartZ=0 EndX=-10 EndY=-3.125 EndZ=0
    g7: GeomPoint X=3e-16 Y=0 Z=0
    g8: Circle CenterX=3e-16 CenterY=0 CenterZ=0 NormalX=0 NormalY=0 NormalZ=1 AngleXU=0 Radius=2.1
    g9: LineSegment StartX=-4.76483 StartY=8.08721 StartZ=0 EndX=-3.55 EndY=8.08721 EndZ=0
    g10: LineSegment StartX=8.24722 StartY=4.75 StartZ=0 EndX=8.24722 EndY=3.55 EndZ=0
    g11: LineSegment StartX=-8.2 StartY=-4.73729 StartZ=0 EndX=-8.2 EndY=-3.55 EndZ=0
    g12: LineSegment StartX=5.5 StartY=4.75 StartZ=0 EndX=8.24722 EndY=4.75 EndZ=0
    g13: LineSegment StartX=4.75 StartY=5.50457 StartZ=0 EndX=2.65 EndY=3.4 EndZ=0
    g14: LineSegment StartX=4.75 StartY=5.50457 StartZ=0 EndX=4.75 EndY=8.08721 EndZ=0
    g15: LineSegment StartX=3.4 StartY=2.65 StartZ=0 EndX=5.5 EndY=4.75 EndZ=0
    g16: LineSegment StartX=-4.76483 StartY=5.50457 StartZ=0 EndX=-2.66166 EndY=3.4 EndZ=0
    g17: LineSegment StartX=-5.5 StartY=4.70904 StartZ=0 EndX=-3.4 EndY=2.61487 EndZ=0
    g18: LineSegment StartX=-4.76483 StartY=5.50457 StartZ=0 EndX=-4.76483 EndY=8.08721 EndZ=0
    g19: LineSegment StartX=-5.5 StartY=4.70904 StartZ=0 EndX=-8.2 EndY=4.70904 EndZ=0
    g20: LineSegment StartX=-10 StartY=3.125 StartZ=0 EndX=-10 EndY=10 EndZ=0
    g21: LineSegment StartX=-8.2 StartY=3.55 StartZ=0 EndX=-8.2 EndY=4.70904 EndZ=0
    g22: LineSegment StartX=3.55 StartY=8.08721 StartZ=0 EndX=4.75 EndY=8.08721 EndZ=0
    g23: LineSegment StartX=3.125 StartY=10 StartZ=0 EndX=10 EndY=10 EndZ=0
    g24: LineSegment StartX=-5.5 StartY=-4.73729 StartZ=0 EndX=-8.2 EndY=-4.73729 EndZ=0
    g25: LineSegment StartX=-4.75 StartY=-5.5 StartZ=0 EndX=-2.65 EndY=-3.4 EndZ=0
    g26: LineSegment StartX=-4.75 StartY=-5.5 StartZ=0 EndX=-4.75 EndY=-8.2 EndZ=0
    g27: LineSegment StartX=4.73747 StartY=-5.5 StartZ=0 EndX=4.73747 EndY=-8.2 EndZ=0
    g28: LineSegment StartX=5.5 StartY=-4.7671 StartZ=0 EndX=8.24722 EndY=-4.7671 EndZ=0
    g29: LineSegment StartX=-3.125 StartY=-10 StartZ=0 EndX=-10 EndY=-10 EndZ=0
    g30: LineSegment StartX=-3.55 StartY=-8.2 StartZ=0 EndX=-4.75 EndY=-8.2 EndZ=0
    g31: LineSegment StartX=4.73747 StartY=-8.2 StartZ=0 EndX=3.55 EndY=-8.2 EndZ=0
    g32: LineSegment StartX=10 StartY=-3.125 StartZ=0 EndX=10 EndY=-10 EndZ=0
    g33: LineSegment StartX=8.24722 StartY=-3.55 StartZ=0 EndX=8.24722 EndY=-4.7671 EndZ=0
    g34: LineSegment StartX=-2.66166 StartY=3.4 StartZ=0 EndX=2.65 EndY=3.4 EndZ=0
    g35: LineSegment StartX=-3.4 StartY=-2.63136 StartZ=0 EndX=-5.5 EndY=-4.73729 EndZ=0
    g36: LineSegment StartX=3.4 StartY=-2.6657 StartZ=0 EndX=5.5 EndY=-4.7671 EndZ=0
    g37: LineSegment StartX=2.63162 StartY=-3.4 StartZ=0 EndX=4.73747 EndY=-5.5 EndZ=0
    g38: LineSegment StartX=-3.55 StartY=-8.2 StartZ=0 EndX=-3.125 EndY=-10 EndZ=0
    g39: LineSegment StartX=3.55 StartY=-8.2 StartZ=0 EndX=3.125 EndY=-10 EndZ=0
    g40: LineSegment StartX=-3.125 StartY=10 StartZ=0 EndX=-3.55 EndY=8.08721 EndZ=0
    g41: LineSegment StartX=3.125 StartY=10 StartZ=0 EndX=3.55 EndY=8.08721 EndZ=0
    g42: LineSegment StartX=8.24722 StartY=3.55 StartZ=0 EndX=10 EndY=3.125 EndZ=0
    g43: LineSegment StartX=10 StartY=-3.125 StartZ=0 EndX=8.24722 EndY=-3.55 EndZ=0
    g44: LineSegment StartX=-10 StartY=-3.125 StartZ=0 EndX=-8.2 EndY=-3.55 EndZ=0
    g45: LineSegment StartX=-10 StartY=3.125 StartZ=0 EndX=-8.2 EndY=3.55 EndZ=0
  constraints (61):
    c: Horizontal(g1)
    c: Vertical(g0)
    c: Vertical(g2)
    c: Coincident(g23,g4)
    c: Coincident(g32,g5)
    c: Coincident(g29,g6)
    c: Coincident(g20,g3)
    c: Horizontal(g3)
    c: Horizontal(g5)
    c: Vertical(g4)
    c: Vertical(g6)
    c: PointOnObject(g7,g-1)
    c: DistanceX(g3,g7) = 10
    c: DistanceX(g-1,g23) = 10
    c: DistanceY(g7,g3) = 10
    c: DistanceX(g3,g-1) = 10
    c: DistanceY(g32,g7) = 10
    c: Coincident(g8,g7)
    c: Radius(g8) = 2.1
    c: Horizontal(g9)
    c: Vertical(g10)
    c: Vertical(g11)
    c: Coincident(g12,g15)
    c: Horizontal(g12)
    c: Coincident(g14,g13)
    c: Vertical(g14)
    c: Coincident(g15,g0)
    c: Coincident(g13,g34)
    c: Coincident(g14,g22)
    c: Coincident(g18,g16)
    c: Vertical(g18)
    c: Coincident(g19,g17)
    c: Horizontal(g19)
    c: Coincident(g9,g18)
    c: Coincident(g21,g19)
    c: Coincident(g24,g35)
    c: Horizontal(g24)
    c: Coincident(g26,g25)
    c: Vertical(g26)
    c: Coincident(g27,g37)
    c: Vertical(g27)
    c: Coincident(g28,g36)
    c: Horizontal(g28)
    c: Coincident(g11,g24)
    c: Coincident(g26,g30)
    c: Coincident(g31,g27)
    c: Coincident(g12,g10)
    c: Coincident(g28,g33)
    c: Coincident(g25,g1)
    c: Coincident(g35,g2)
    c: Coincident(g17,g2)
    c: Coincident(g16,g34)
    c: Coincident(g1,g37)
    c: Coincident(g0,g36)
    c: Coincident(g39,g5)
    c: Coincident(g40,g3)
    c: Coincident(g42,g4)
    c: Coincident(g44,g6)
    c: Coincident(g21,g45)
    c: Coincident(g33,g43)
    c: Coincident(g10,g42)
FEATURE [PartDesign::Pad] Pad
  Direction = (2e-16,0,-1)
  Length = 300
  Length2 = 10
  Placement = pos=(0,0,0) rot=(0,1,0;1.5708rad)
  Profile = -> Sketch
  Type = 0
FEATURE [PartDesign::Fillet] Fillet
  Base = -> Pad [Edge53]
  BaseFeature = -> Pad
  Placement = pos=(0,0,0) rot=(0,1,0;1.5708rad)
  Radius = 1
  SupportTransform = false
FEATURE [PartDesign::Fillet] Fillet001
  Base = -> Fillet [Edge114]
  BaseFeature = -> Fillet
  Placement = pos=(0,0,0) rot=(0,1,0;1.5708rad)
  Radius = 1
  SupportTransform = false
FEATURE [PartDesign::Fillet] Fillet002
  Base = -> Fillet001 [Edge137,Edge95]
  BaseFeature = -> Fillet001
  Placement = pos=(0,0,0) rot=(0,1,0;1.5708rad)
  Radius = 0.5
  SupportTransform = false
FEATURE [PartDesign::Fillet] Fillet003
  Base = -> Fillet002 [Edge103]
  BaseFeature = -> Fillet002
  Placement = pos=(0,0,0) rot=(0.57735,0.57735,0.57735;2.0944rad)
  Radius = 0.5
  SupportTransform = false
FEATURE [PartDesign::Fillet] Fillet004
  Base = -> Fillet003 [Edge96]
  BaseFeature = -> Fillet003
  Placement = pos=(0,0,0) rot=(0.57735,0.57735,0.57735;2.0944rad)
  Radius = 0.5
  SupportTransform = false
FEATURE [PartDesign::Fillet] Fillet005
  Base = -> Fillet004 [Edge77]
  BaseFeature = -> Fillet004
  Placement = pos=(0,0,0) rot=(0.57735,0.57735,0.57735;2.0944rad)
  Radius = 0.5
  SupportTransform = false
FEATURE [PartDesign::Fillet] Fillet006
  Base = -> Fillet005 [Edge102]
  BaseFeature = -> Fillet005
  Placement = pos=(0,0,0) rot=(0.57735,0.57735,0.57735;2.0944rad)
  Radius = 0.5
  SupportTransform = false
FEATURE [PartDesign::Fillet] Fillet007
  Base = -> Fillet006 [Edge85]
  BaseFeature = -> Fillet006
  Placement = pos=(0,0,0) rot=(0.57735,0.57735,0.57735;2.0944rad)
  Radius = 0.5
  SupportTransform = false
FEATURE [PartDesign::Fillet] Fillet008
  Base = -> Fillet007 [Edge78]
  BaseFeature = -> Fillet007
  Placement = pos=(0,0,0) rot=(0.57735,0.57735,0.57735;2.0944rad)
  Radius = 0.5
  SupportTransform = false
FEATURE [PartDesign::Fillet] Fillet009
  Base = -> Fillet008 [Edge107]
  BaseFeature = -> Fillet008
  Placement = pos=(0,0,0) rot=(0.57735,0.57735,0.57735;2.0944rad)
  Radius = 0.5
  SupportTransform = false
FEATURE [PartDesign::Fillet] Fillet010
  Base = -> Fillet009 [Edge74]
  BaseFeature = -> Fillet009
  Radius = 0.5
  SupportTransform = false
FEATURE [PartDesign::Body] Body
  Group = -> [Sketch,Pad,Fillet,Fillet001,Fillet002,Fillet003,Fillet004,Fillet005,Fillet006,Fillet007,Fillet008,Fillet009,Fillet010]
  Origin = -> Origin001
  Placement = pos=(0,0,0) rot=(0,1,0;1.5708rad)
  Tip = -> Fillet010
FEATURE [App::Part] Part  label="2020-300-001"
  Group = -> [Body]
  Origin = -> Origin
  Placement = pos=(20,10,10) rot=(0,0,1;0rad)
FEATURE [App::Part] Part004  label="2020-300-005"
  Group = -> [Body004]
  Origin = -> Origin008
  Placement = pos=(10,10,0) rot=(0,1,0;4.71239rad)
FEATURE [Sketcher::SketchObject] Sketch005
  FullyConstrained = false
  MapMode = 5
  Support = -> [XY_Plane011]
  sketch-geometry (46):
    g0: LineSegment StartX=3.4 StartY=2.65 StartZ=0 EndX=3.4 EndY=-2.6657 EndZ=0
    g1: LineSegment StartX=2.63162 StartY=-3.4 StartZ=0 EndX=-2.65 EndY=-3.4 EndZ=0
    g2: LineSegment StartX=-3.4 StartY=-2.63136 StartZ=0 EndX=-3.4 EndY=2.61487 EndZ=0
    g3: LineSegment StartX=-10 StartY=10 StartZ=0 EndX=-3.125 EndY=10 EndZ=0
    g4: LineSegment StartX=10 StartY=10 StartZ=0 EndX=10 EndY=3.125 EndZ=0
    g5: LineSegment StartX=10 StartY=-10 StartZ=0 EndX=3.125 EndY=-10 EndZ=0
    g6: LineSegment StartX=-10 StartY=-10 StartZ=0 EndX=-10 EndY=-3.125 EndZ=0
    g7: GeomPoint X=3e-16 Y=0 Z=0
    g8: Circle CenterX=3e-16 CenterY=0 CenterZ=0 NormalX=0 NormalY=0 NormalZ=1 AngleXU=0 Radius=2.1
    g9: LineSegment StartX=-4.76483 StartY=8.08721 StartZ=0 EndX=-3.55 EndY=8.08721 EndZ=0
    g10: LineSegment StartX=8.24722 StartY=4.75 StartZ=0 EndX=8.24722 EndY=3.55 EndZ=0
    g11: LineSegment StartX=-8.2 StartY=-4.73729 StartZ=0 EndX=-8.2 EndY=-3.55 EndZ=0
    g12: LineSegment StartX=5.5 StartY=4.75 StartZ=0 EndX=8.24722 EndY=4.75 EndZ=0
    g13: LineSegment StartX=4.75 StartY=5.50457 StartZ=0 EndX=2.65 EndY=3.4 EndZ=0
    g14: LineSegment StartX=4.75 StartY=5.50457 StartZ=0 EndX=4.75 EndY=8.08721 EndZ=0
    g15: LineSegment StartX=3.4 StartY=2.65 StartZ=0 EndX=5.5 EndY=4.75 EndZ=0
    g16: LineSegment StartX=-4.76483 StartY=5.50457 StartZ=0 EndX=-2.66166 EndY=3.4 EndZ=0
    g17: LineSegment StartX=-5.5 StartY=4.70904 StartZ=0 EndX=-3.4 EndY=2.61487 EndZ=0
    g18: LineSegment StartX=-4.76483 StartY=5.50457 StartZ=0 EndX=-4.76483 EndY=8.08721 EndZ=0
    g19: LineSegment StartX=-5.5 StartY=4.70904 StartZ=0 EndX=-8.2 EndY=4.70904 EndZ=0
    g20: LineSegment StartX=-10 StartY=3.125 StartZ=0 EndX=-10 EndY=10 EndZ=0
    g21: LineSegment StartX=-8.2 StartY=3.55 StartZ=0 EndX=-8.2 EndY=4.70904 EndZ=0
    g22: LineSegment StartX=3.55 StartY=8.08721 StartZ=0 EndX=4.75 EndY=8.08721 EndZ=0
    g23: LineSegment StartX=3.125 StartY=10 StartZ=0 EndX=10 EndY=10 EndZ=0
    g24: LineSegment StartX=-5.5 StartY=-4.73729 StartZ=0 EndX=-8.2 EndY=-4.73729 EndZ=0
    g25: LineSegment StartX=-4.75 StartY=-5.5 StartZ=0 EndX=-2.65 EndY=-3.4 EndZ=0
    g26: LineSegment StartX=-4.75 StartY=-5.5 StartZ=0 EndX=-4.75 EndY=-8.2 EndZ=0
    g27: LineSegment StartX=4.73747 StartY=-5.5 StartZ=0 EndX=4.73747 EndY=-8.2 EndZ=0
    g28: LineSegment StartX=5.5 StartY=-4.7671 StartZ=0 EndX=8.24722 EndY=-4.7671 EndZ=0
    g29: LineSegment StartX=-3.125 StartY=-10 StartZ=0 EndX=-10 EndY=-10 EndZ=0
    g30: LineSegment StartX=-3.55 StartY=-8.2 StartZ=0 EndX=-4.75 EndY=-8.2 EndZ=0
    g31: LineSegment StartX=4.73747 StartY=-8.2 StartZ=0 EndX=3.55 EndY=-8.2 EndZ=0
    g32: LineSegment StartX=10 StartY=-3.125 StartZ=0 EndX=10 EndY=-10 EndZ=0
    g33: LineSegment StartX=8.24722 StartY=-3.55 StartZ=0 EndX=8.24722 EndY=-4.7671 EndZ=0
    g34: LineSegment StartX=-2.66166 StartY=3.4 StartZ=0 EndX=2.65 EndY=3.4 EndZ=0
    g35: LineSegment StartX=-3.4 StartY=-2.63136 StartZ=0 EndX=-5.5 EndY=-4.73729 EndZ=0
    g36: LineSegment StartX=3.4 StartY=-2.6657 StartZ=0 EndX=5.5 EndY=-4.7671 EndZ=0
    g37: LineSegment StartX=2.63162 StartY=-3.4 StartZ=0 EndX=4.73747 EndY=-5.5 EndZ=0
    g38: LineSegment StartX=-3.55 StartY=-8.2 StartZ=0 EndX=-3.125 EndY=-10 EndZ=0
    g39: LineSegment StartX=3.55 StartY=-8.2 StartZ=0 EndX=3.125 EndY=-10 EndZ=0
    g40: LineSegment StartX=-3.125 StartY=10 StartZ=0 EndX=-3.55 EndY=8.08721 EndZ=0
    g41: LineSegment StartX=3.125 StartY=10 StartZ=0 EndX=3.55 EndY=8.08721 EndZ=0
    g42: LineSegment StartX=8.24722 StartY=3.55 StartZ=0 EndX=10 EndY=3.125 EndZ=0
    g43: LineSegment StartX=10 StartY=-3.125 StartZ=0 EndX=8.24722 EndY=-3.55 EndZ=0
    g44: LineSegment StartX=-10 StartY=-3.125 StartZ=0 EndX=-8.2 EndY=-3.55 EndZ=0
    g45: LineSegment StartX=-10 StartY=3.125 StartZ=0 EndX=-8.2 EndY=3.55 EndZ=0
  constraints (61):
    c: Horizontal(g1)
    c: Vertical(g0)
    c: Vertical(g2)
    c: Coincident(g23,g4)
    c: Coincident(g32,g5)
    c: Coincident(g29,g6)
    c: Coincident(g20,g3)
    c: Horizontal(g3)
    c: Horizontal(g5)
    c: Vertical(g4)
    c: Vertical(g6)
    c: PointOnObject(g7,g-1)
    c: DistanceX(g3,g7) = 10
    c: DistanceX(g-1,g23) = 10
    c: DistanceY(g7,g3) = 10
    c: DistanceX(g3,g-1) = 10
    c: DistanceY(g32,g7) = 10
    c: Coincident(g8,g7)
    c: Radius(g8) = 2.1
    c: Horizontal(g9)
    c: Vertical(g10)
    c: Vertical(g11)
    c: Coincident(g12,g15)
    c: Horizontal(g12)
    c: Coincident(g14,g13)
    c: Vertical(g14)
    c: Coincident(g15,g0)
    c: Coincident(g13,g34)
    c: Coincident(g14,g22)
    c: Coincident(g18,g16)
    c: Vertical(g18)
    c: Coincident(g19,g17)
    c: Horizontal(g19)
    c: Coincident(g9,g18)
    c: Coincident(g21,g19)
    c: Coincident(g24,g35)
    c: Horizontal(g24)
    c: Coincident(g26,g25)
    c: Vertical(g26)
    c: Coincident(g27,g37)
    c: Vertical(g27)
    c: Coincident(g28,g36)
    c: Horizontal(g28)
    c: Coincident(g11,g24)
    c: Coincident(g26,g30)
    c: Coincident(g31,g27)
    c: Coincident(g12,g10)
    c: Coincident(g28,g33)
    c: Coincident(g25,g1)
    c: Coincident(g35,g2)
    c: Coincident(g17,g2)
    c: Coincident(g16,g34)
    c: Coincident(g1,g37)
    c: Coincident(g0,g36)
    c: Coincident(g39,g5)
    c: Coincident(g40,g3)
    c: Coincident(g42,g4)
    c: Coincident(g44,g6)
    c: Coincident(g21,g45)
    c: Coincident(g33,g43)
    c: Coincident(g10,g42)
FEATURE [PartDesign::Pad] Pad005
  Direction = (0,0,1)
  Length = 190
  Length2 = 10
  Profile = -> Sketch005
  Type = 0
FEATURE [PartDesign::Fillet] Fillet055
  Base = -> Pad005 [Edge53]
  BaseFeature = -> Pad005
  Radius = 1
  SupportTransform = false
FEATURE [PartDesign::Fillet] Fillet056
  Base = -> Fillet055 [Edge114]
  BaseFeature = -> Fillet055
  Radius = 1
  SupportTransform = false
FEATURE [PartDesign::Fillet] Fillet057
  Base = -> Fillet056 [Edge137,Edge95]
  BaseFeature = -> Fillet056
  Radius = 0.5
  SupportTransform = false
FEATURE [PartDesign::Fillet] Fillet058
  Base = -> Fillet057 [Edge103]
  BaseFeature = -> Fillet057
  Radius = 0.5
  SupportTransform = false
FEATURE [PartDesign::Fillet] Fillet059
  Base = -> Fillet058 [Edge96]
  BaseFeature = -> Fillet058
  Radius = 0.5
  SupportTransform = false
FEATURE [PartDesign::Fillet] Fillet060
  Base = -> Fillet059 [Edge77]
  BaseFeature = -> Fillet059
  Radius = 0.5
  SupportTransform = false
FEATURE [PartDesign::Fillet] Fillet061
  Base = -> Fillet060 [Edge102]
  BaseFeature = -> Fillet060
  Radius = 0.5
  SupportTransform = false
FEATURE [PartDesign::Fillet] Fillet062
  Base = -> Fillet061 [Edge85]
  BaseFeature = -> Fillet061
  Radius = 0.5
  SupportTransform = false
FEATURE [PartDesign::Fillet] Fillet063
  Base = -> Fillet062 [Edge78]
  BaseFeature = -> Fillet062
  Radius = 0.5
  SupportTransform = false
FEATURE [PartDesign::Fillet] Fillet064
  Base = -> Fillet063 [Edge107]
  BaseFeature = -> Fillet063
  Radius = 0.5
  SupportTransform = false
FEATURE [PartDesign::Fillet] Fillet065
  Base = -> Fillet064 [Edge74]
  BaseFeature = -> Fillet064
  Radius = 0.5
  SupportTransform = false
FEATURE [PartDesign::Body] Body005
  Group = -> [Sketch005,Pad005,Fillet055,Fillet056,Fillet057,Fillet058,Fillet059,Fillet060,Fillet061,Fillet062,Fillet063,Fillet064,Fillet065]
  Origin = -> Origin011
  Placement = pos=(0,0,0) rot=(0,1,0;1.5708rad)
  Tip = -> Fillet065
FEATURE [App::Part] Part005  label="2020-300-006"
  Group = -> [Body005]
  Origin = -> Origin010
  Placement = pos=(10,330,0) rot=(0,1,0;4.71239rad)
FEATURE [Sketcher::SketchObject] Sketch006
  FullyConstrained = false
  MapMode = 5
  Support = -> [XY_Plane013]
  sketch-geometry (46):
    g0: LineSegment StartX=3.4 StartY=2.65 StartZ=0 EndX=3.4 EndY=-2.6657 EndZ=0
    g1: LineSegment StartX=2.63162 StartY=-3.4 StartZ=0 EndX=-2.65 EndY=-3.4 EndZ=0
    g2: LineSegment StartX=-3.4 StartY=-2.63136 StartZ=0 EndX=-3.4 EndY=2.61487 EndZ=0
    g3: LineSegment StartX=-10 StartY=10 StartZ=0 EndX=-3.125 EndY=10 EndZ=0
    g4: LineSegment StartX=10 StartY=10 StartZ=0 EndX=10 EndY=3.125 EndZ=0
    g5: LineSegment StartX=10 StartY=-10 StartZ=0 EndX=3.125 EndY=-10 EndZ=0
    g6: LineSegment StartX=-10 StartY=-10 StartZ=0 EndX=-10 EndY=-3.125 EndZ=0
    g7: GeomPoint X=3e-16 Y=0 Z=0
    g8: Circle CenterX=3e-16 CenterY=0 CenterZ=0 NormalX=0 NormalY=0 NormalZ=1 AngleXU=0 Radius=2.1
    g9: LineSegment StartX=-4.76483 StartY=8.08721 StartZ=0 EndX=-3.55 EndY=8.08721 EndZ=0
    g10: LineSegment StartX=8.24722 StartY=4.75 StartZ=0 EndX=8.24722 EndY=3.55 EndZ=0
    g11: LineSegment StartX=-8.2 StartY=-4.73729 StartZ=0 EndX=-8.2 EndY=-3.55 EndZ=0
    g12: LineSegment StartX=5.5 StartY=4.75 StartZ=0 EndX=8.24722 EndY=4.75 EndZ=0
    g13: LineSegment StartX=4.75 StartY=5.50457 StartZ=0 EndX=2.65 EndY=3.4 EndZ=0
    g14: LineSegment StartX=4.75 StartY=5.50457 StartZ=0 EndX=4.75 EndY=8.08721 EndZ=0
    g15: LineSegment StartX=3.4 StartY=2.65 StartZ=0 EndX=5.5 EndY=4.75 EndZ=0
    g16: LineSegment StartX=-4.76483 StartY=5.50457 StartZ=0 EndX=-2.66166 EndY=3.4 EndZ=0
    g17: LineSegment StartX=-5.5 StartY=4.70904 StartZ=0 EndX=-3.4 EndY=2.61487 EndZ=0
    g18: LineSegment StartX=-4.76483 StartY=5.50457 StartZ=0 EndX=-4.76483 EndY=8.08721 EndZ=0
    g19: LineSegment StartX=-5.5 StartY=4.70904 StartZ=0 EndX=-8.2 EndY=4.70904 EndZ=0
    g20: LineSegment StartX=-10 StartY=3.125 StartZ=0 EndX=-10 EndY=10 EndZ=0
    g21: LineSegment StartX=-8.2 StartY=3.55 StartZ=0 EndX=-8.2 EndY=4.70904 EndZ=0
    g22: LineSegment StartX=3.55 StartY=8.08721 StartZ=0 EndX=4.75 EndY=8.08721 EndZ=0
    g23: LineSegment StartX=3.125 StartY=10 StartZ=0 EndX=10 EndY=10 EndZ=0
    g24: LineSegment StartX=-5.5 StartY=-4.73729 StartZ=0 EndX=-8.2 EndY=-4.73729 EndZ=0
    g25: LineSegment StartX=-4.75 StartY=-5.5 StartZ=0 EndX=-2.65 EndY=-3.4 EndZ=0
    g26: LineSegment StartX=-4.75 StartY=-5.5 StartZ=0 EndX=-4.75 EndY=-8.2 EndZ=0
    g27: LineSegment StartX=4.73747 StartY=-5.5 StartZ=0 EndX=4.73747 EndY=-8.2 EndZ=0
    g28: LineSegment StartX=5.5 StartY=-4.7671 StartZ=0 EndX=8.24722 EndY=-4.7671 EndZ=0
    g29: LineSegment StartX=-3.125 StartY=-10 StartZ=0 EndX=-10 EndY=-10 EndZ=0
    g30: LineSegment StartX=-3.55 StartY=-8.2 StartZ=0 EndX=-4.75 EndY=-8.2 EndZ=0
    g31: LineSegment StartX=4.73747 StartY=-8.2 StartZ=0 EndX=3.55 EndY=-8.2 EndZ=0
    g32: LineSegment StartX=10 StartY=-3.125 StartZ=0 EndX=10 EndY=-10 EndZ=0
    g33: LineSegment StartX=8.24722 StartY=-3.55 StartZ=0 EndX=8.24722 EndY=-4.7671 EndZ=0
    g34: LineSegment StartX=-2.66166 StartY=3.4 StartZ=0 EndX=2.65 EndY=3.4 EndZ=0
    g35: LineSegment StartX=-3.4 StartY=-2.63136 StartZ=0 EndX=-5.5 EndY=-4.73729 EndZ=0
    g36: LineSegment StartX=3.4 StartY=-2.6657 StartZ=0 EndX=5.5 EndY=-4.7671 EndZ=0
    g37: LineSegment StartX=2.63162 StartY=-3.4 StartZ=0 EndX=4.73747 EndY=-5.5 EndZ=0
    g38: LineSegment StartX=-3.55 StartY=-8.2 StartZ=0 EndX=-3.125 EndY=-10 EndZ=0
    g39: LineSegment StartX=3.55 StartY=-8.2 StartZ=0 EndX=3.125 EndY=-10 EndZ=0
    g40: LineSegment StartX=-3.125 StartY=10 StartZ=0 EndX=-3.55 EndY=8.08721 EndZ=0
    g41: LineSegment StartX=3.125 StartY=10 StartZ=0 EndX=3.55 EndY=8.08721 EndZ=0
    g42: LineSegment StartX=8.24722 StartY=3.55 StartZ=0 EndX=10 EndY=3.125 EndZ=0
    g43: LineSegment StartX=10 StartY=-3.125 StartZ=0 EndX=8.24722 EndY=-3.55 EndZ=0
    g44: LineSegment StartX=-10 StartY=-3.125 StartZ=0 EndX=-8.2 EndY=-3.55 EndZ=0
    g45: LineSegment StartX=-10 StartY=3.125 StartZ=0 EndX=-8.2 EndY=3.55 EndZ=0
  constraints (61):
    c: Horizontal(g1)
    c: Vertical(g0)
    c: Vertical(g2)
    c: Coincident(g23,g4)
    c: Coincident(g32,g5)
    c: Coincident(g29,g6)
    c: Coincident(g20,g3)
    c: Horizontal(g3)
    c: Horizontal(g5)
    c: Vertical(g4)
    c: Vertical(g6)
    c: PointOnObject(g7,g-1)
    c: DistanceX(g3,g7) = 10
    c: DistanceX(g-1,g23) = 10
    c: DistanceY(g7,g3) = 10
    c: DistanceX(g3,g-1) = 10
    c: DistanceY(g32,g7) = 10
    c: Coincident(g8,g7)
    c: Radius(g8) = 2.1
    c: Horizontal(g9)
    c: Vertical(g10)
    c: Vertical(g11)
    c: Coincident(g12,g15)
    c: Horizontal(g12)
    c: Coincident(g14,g13)
    c: Vertical(g14)
    c: Coincident(g15,g0)
    c: Coincident(g13,g34)
    c: Coincident(g14,g22)
    c: Coincident(g18,g16)
    c: Vertical(g18)
    c: Coincident(g19,g17)
    c: Horizontal(g19)
    c: Coincident(g9,g18)
    c: Coincident(g21,g19)
    c: Coincident(g24,g35)
    c: Horizontal(g24)
    c: Coincident(g26,g25)
    c: Vertical(g26)
    c: Coincident(g27,g37)
    c: Vertical(g27)
    c: Coincident(g28,g36)
    c: Horizontal(g28)
    c: Coincident(g11,g24)
    c: Coincident(g26,g30)
    c: Coincident(g31,g27)
    c: Coincident(g12,g10)
    c: Coincident(g28,g33)
    c: Coincident(g25,g1)
    c: Coincident(g35,g2)
    c: Coincident(g17,g2)
    c: Coincident(g16,g34)
    c: Coincident(g1,g37)
    c: Coincident(g0,g36)
    c: Coincident(g39,g5)
    c: Coincident(g40,g3)
    c: Coincident(g42,g4)
    c: Coincident(g44,g6)
    c: Coincident(g21,g45)
    c: Coincident(g33,g43)
    c: Coincident(g10,g42)
FEATURE [PartDesign::Pad] Pad006
  Direction = (0,0,1)
  Length = 190
  Length2 = 10
  Profile = -> Sketch006
  Type = 0
FEATURE [PartDesign::Fillet] Fillet066
  Base = -> Pad006 [Edge53]
  BaseFeature = -> Pad006
  Radius = 1
  SupportTransform = false
FEATURE [PartDesign::Fillet] Fillet067
  Base = -> Fillet066 [Edge114]
  BaseFeature = -> Fillet066
  Radius = 1
  SupportTransform = false
FEATURE [PartDesign::Fillet] Fillet068
  Base = -> Fillet067 [Edge137,Edge95]
  BaseFeature = -> Fillet067
  Radius = 0.5
  SupportTransform = false
FEATURE [PartDesign::Fillet] Fillet069
  Base = -> Fillet068 [Edge103]
  BaseFeature = -> Fillet068
  Radius = 0.5
  SupportTransform = false
FEATURE [PartDesign::Fillet] Fillet070
  Base = -> Fillet069 [Edge96]
  BaseFeature = -> Fillet069
  Radius = 0.5
  SupportTransform = false
FEATURE [PartDesign::Fillet] Fillet071
  Base = -> Fillet070 [Edge77]
  BaseFeature = -> Fillet070
  Radius = 0.5
  SupportTransform = false
FEATURE [PartDesign::Fillet] Fillet072
  Base = -> Fillet071 [Edge102]
  BaseFeature = -> Fillet071
  Radius = 0.5
  SupportTransform = false
FEATURE [PartDesign::Fillet] Fillet073
  Base = -> Fillet072 [Edge85]
  BaseFeature = -> Fillet072
  Radius = 0.5
  SupportTransform = false
FEATURE [PartDesign::Fillet] Fillet074
  Base = -> Fillet073 [Edge78]
  BaseFeature = -> Fillet073
  Radius = 0.5
  SupportTransform = false
FEATURE [PartDesign::Fillet] Fillet075
  Base = -> Fillet074 [Edge107]
  BaseFeature = -> Fillet074
  Radius = 0.5
  SupportTransform = false
FEATURE [PartDesign::Fillet] Fillet076
  Base = -> Fillet075 [Edge74]
  BaseFeature = -> Fillet075
  Radius = 0.5
  SupportTransform = false
FEATURE [PartDesign::Body] Body006
  Group = -> [Sketch006,Pad006,Fillet066,Fillet067,Fillet068,Fillet069,Fillet070,Fillet071,Fillet072,Fillet073,Fillet074,Fillet075,Fillet076]
  Origin = -> Origin013
  Placement = pos=(0,0,0) rot=(0,1,0;1.5708rad)
  Tip = -> Fillet076
FEATURE [App::Part] Part006  label="2020-300-007"
  Group = -> [Body006]
  Origin = -> Origin012
  Placement = pos=(330,10,0) rot=(0,1,0;4.71239rad)
FEATURE [Sketcher::SketchObject] Sketch007
  FullyConstrained = false
  MapMode = 5
  Support = -> [XY_Plane015]
  sketch-geometry (46):
    g0: LineSegment StartX=3.4 StartY=2.65 StartZ=0 EndX=3.4 EndY=-2.6657 EndZ=0
    g1: LineSegment StartX=2.63162 StartY=-3.4 StartZ=0 EndX=-2.65 EndY=-3.4 EndZ=0
    g2: LineSegment StartX=-3.4 StartY=-2.63136 StartZ=0 EndX=-3.4 EndY=2.61487 EndZ=0
    g3: LineSegment StartX=-10 StartY=10 StartZ=0 EndX=-3.125 EndY=10 EndZ=0
    g4: LineSegment StartX=10 StartY=10 StartZ=0 EndX=10 EndY=3.125 EndZ=0
    g5: LineSegment StartX=10 StartY=-10 StartZ=0 EndX=3.125 EndY=-10 EndZ=0
    g6: LineSegment StartX=-10 StartY=-10 StartZ=0 EndX=-10 EndY=-3.125 EndZ=0
    g7: GeomPoint X=3e-16 Y=0 Z=0
    g8: Circle CenterX=3e-16 CenterY=0 CenterZ=0 NormalX=0 NormalY=0 NormalZ=1 AngleXU=0 Radius=2.1
    g9: LineSegment StartX=-4.76483 StartY=8.08721 StartZ=0 EndX=-3.55 EndY=8.08721 EndZ=0
    g10: LineSegment StartX=8.24722 StartY=4.75 StartZ=0 EndX=8.24722 EndY=3.55 EndZ=0
    g11: LineSegment StartX=-8.2 StartY=-4.73729 StartZ=0 EndX=-8.2 EndY=-3.55 EndZ=0
    g12: LineSegment StartX=5.5 StartY=4.75 StartZ=0 EndX=8.24722 EndY=4.75 EndZ=0
    g13: LineSegment StartX=4.75 StartY=5.50457 StartZ=0 EndX=2.65 EndY=3.4 EndZ=0
    g14: LineSegment StartX=4.75 StartY=5.50457 StartZ=0 EndX=4.75 EndY=8.08721 EndZ=0
    g15: LineSegment StartX=3.4 StartY=2.65 StartZ=0 EndX=5.5 EndY=4.75 EndZ=0
    g16: LineSegment StartX=-4.76483 StartY=5.50457 StartZ=0 EndX=-2.66166 EndY=3.4 EndZ=0
    g17: LineSegment StartX=-5.5 StartY=4.70904 StartZ=0 EndX=-3.4 EndY=2.61487 EndZ=0
    g18: LineSegment StartX=-4.76483 StartY=5.50457 StartZ=0 EndX=-4.76483 EndY=8.08721 EndZ=0
    g19: LineSegment StartX=-5.5 StartY=4.70904 StartZ=0 EndX=-8.2 EndY=4.70904 EndZ=0
    g20: LineSegment StartX=-10 StartY=3.125 StartZ=0 EndX=-10 EndY=10 EndZ=0
    g21: LineSegment StartX=-8.2 StartY=3.55 StartZ=0 EndX=-8.2 EndY=4.70904 EndZ=0
    g22: LineSegment StartX=3.55 StartY=8.08721 StartZ=0 EndX=4.75 EndY=8.08721 EndZ=0
    g23: LineSegment StartX=3.125 StartY=10 StartZ=0 EndX=10 EndY=10 EndZ=0
    g24: LineSegment StartX=-5.5 StartY=-4.73729 StartZ=0 EndX=-8.2 EndY=-4.73729 EndZ=0
    g25: LineSegment StartX=-4.75 StartY=-5.5 StartZ=0 EndX=-2.65 EndY=-3.4 EndZ=0
    g26: LineSegment StartX=-4.75 StartY=-5.5 StartZ=0 EndX=-4.75 EndY=-8.2 EndZ=0
    g27: LineSegment StartX=4.73747 StartY=-5.5 StartZ=0 EndX=4.73747 EndY=-8.2 EndZ=0
    g28: LineSegment StartX=5.5 StartY=-4.7671 StartZ=0 EndX=8.24722 EndY=-4.7671 EndZ=0
    g29: LineSegment StartX=-3.125 StartY=-10 StartZ=0 EndX=-10 EndY=-10 EndZ=0
    g30: LineSegment StartX=-3.55 StartY=-8.2 StartZ=0 EndX=-4.75 EndY=-8.2 EndZ=0
    g31: LineSegment StartX=4.73747 StartY=-8.2 StartZ=0 EndX=3.55 EndY=-8.2 EndZ=0
    g32: LineSegment StartX=10 StartY=-3.125 StartZ=0 EndX=10 EndY=-10 EndZ=0
    g33: LineSegment StartX=8.24722 StartY=-3.55 StartZ=0 EndX=8.24722 EndY=-4.7671 EndZ=0
    g34: LineSegment StartX=-2.66166 StartY=3.4 StartZ=0 EndX=2.65 EndY=3.4 EndZ=0
    g35: LineSegment StartX=-3.4 StartY=-2.63136 StartZ=0 EndX=-5.5 EndY=-4.73729 EndZ=0
    g36: LineSegment StartX=3.4 StartY=-2.6657 StartZ=0 EndX=5.5 EndY=-4.7671 EndZ=0
    g37: LineSegment StartX=2.63162 StartY=-3.4 StartZ=0 EndX=4.73747 EndY=-5.5 EndZ=0
    g38: LineSegment StartX=-3.55 StartY=-8.2 StartZ=0 EndX=-3.125 EndY=-10 EndZ=0
    g39: LineSegment StartX=3.55 StartY=-8.2 StartZ=0 EndX=3.125 EndY=-10 EndZ=0
    g40: LineSegment StartX=-3.125 StartY=10 StartZ=0 EndX=-3.55 EndY=8.08721 EndZ=0
    g41: LineSegment StartX=3.125 StartY=10 StartZ=0 EndX=3.55 EndY=8.08721 EndZ=0
    g42: LineSegment StartX=8.24722 StartY=3.55 StartZ=0 EndX=10 EndY=3.125 EndZ=0
    g43: LineSegment StartX=10 StartY=-3.125 StartZ=0 EndX=8.24722 EndY=-3.55 EndZ=0
    g44: LineSegment StartX=-10 StartY=-3.125 StartZ=0 EndX=-8.2 EndY=-3.55 EndZ=0
    g45: LineSegment StartX=-10 StartY=3.125 StartZ=0 EndX=-8.2 EndY=3.55 EndZ=0
  constraints (61):
    c: Horizontal(g1)
    c: Vertical(g0)
    c: Vertical(g2)
    c: Coincident(g23,g4)
    c: Coincident(g32,g5)
    c: Coincident(g29,g6)
    c: Coincident(g20,g3)
    c: Horizontal(g3)
    c: Horizontal(g5)
    c: Vertical(g4)
    c: Vertical(g6)
    c: PointOnObject(g7,g-1)
    c: DistanceX(g3,g7) = 10
    c: DistanceX(g-1,g23) = 10
    c: DistanceY(g7,g3) = 10
    c: DistanceX(g3,g-1) = 10
    c: DistanceY(g32,g7) = 10
    c: Coincident(g8,g7)
    c: Radius(g8) = 2.1
    c: Horizontal(g9)
    c: Vertical(g10)
    c: Vertical(g11)
    c: Coincident(g12,g15)
    c: Horizontal(g12)
    c: Coincident(g14,g13)
    c: Vertical(g14)
    c: Coincident(g15,g0)
    c: Coincident(g13,g34)
    c: Coincident(g14,g22)
    c: Coincident(g18,g16)
    c: Vertical(g18)
    c: Coincident(g19,g17)
    c: Horizontal(g19)
    c: Coincident(g9,g18)
    c: Coincident(g21,g19)
    c: Coincident(g24,g35)
    c: Horizontal(g24)
    c: Coincident(g26,g25)
    c: Vertical(g26)
    c: Coincident(g27,g37)
    c: Vertical(g27)
    c: Coincident(g28,g36)
    c: Horizontal(g28)
    c: Coincident(g11,g24)
    c: Coincident(g26,g30)
    c: Coincident(g31,g27)
    c: Coincident(g12,g10)
    c: Coincident(g28,g33)
    c: Coincident(g25,g1)
    c: Coincident(g35,g2)
    c: Coincident(g17,g2)
    c: Coincident(g16,g34)
    c: Coincident(g1,g37)
    c: Coincident(g0,g36)
    c: Coincident(g39,g5)
    c: Coincident(g40,g3)
    c: Coincident(g42,g4)
    c: Coincident(g44,g6)
    c: Coincident(g21,g45)
    c: Coincident(g33,g43)
    c: Coincident(g10,g42)
FEATURE [PartDesign::Pad] Pad007
  Direction = (0,0,1)
  Length = 190
  Length2 = 10
  Profile = -> Sketch007
  Type = 0
FEATURE [PartDesign::Fillet] Fillet077
  Base = -> Pad007 [Edge53]
  BaseFeature = -> Pad007
  Radius = 1
  SupportTransform = false
FEATURE [PartDesign::Fillet] Fillet078
  Base = -> Fillet077 [Edge114]
  BaseFeature = -> Fillet077
  Radius = 1
  SupportTransform = false
FEATURE [PartDesign::Fillet] Fillet079
  Base = -> Fillet078 [Edge137,Edge95]
  BaseFeature = -> Fillet078
  Radius = 0.5
  SupportTransform = false
FEATURE [PartDesign::Fillet] Fillet080
  Base = -> Fillet079 [Edge103]
  BaseFeature = -> Fillet079
  Radius = 0.5
  SupportTransform = false
FEATURE [PartDesign::Fillet] Fillet081
  Base = -> Fillet080 [Edge96]
  BaseFeature = -> Fillet080
  Radius = 0.5
  SupportTransform = false
FEATURE [PartDesign::Fillet] Fillet082
  Base = -> Fillet081 [Edge77]
  BaseFeature = -> Fillet081
  Radius = 0.5
  SupportTransform = false
FEATURE [PartDesign::Fillet] Fillet083
  Base = -> Fillet082 [Edge102]
  BaseFeature = -> Fillet082
  Radius = 0.5
  SupportTransform = false
FEATURE [PartDesign::Fillet] Fillet084
  Base = -> Fillet083 [Edge85]
  BaseFeature = -> Fillet083
  Radius = 0.5
  SupportTransform = false
FEATURE [PartDesign::Fillet] Fillet085
  Base = -> Fillet084 [Edge78]
  BaseFeature = -> Fillet084
  Radius = 0.5
  SupportTransform = false
FEATURE [PartDesign::Fillet] Fillet086
  Base = -> Fillet085 [Edge107]
  BaseFeature = -> Fillet085
  Radius = 0.5
  SupportTransform = false
FEATURE [PartDesign::Fillet] Fillet087
  Base = -> Fillet086 [Edge74]
  BaseFeature = -> Fillet086
  Radius = 0.5
  SupportTransform = false
FEATURE [PartDesign::Body] Body007
  Group = -> [Sketch007,Pad007,Fillet077,Fillet078,Fillet079,Fillet080,Fillet081,Fillet082,Fillet083,Fillet084,Fillet085,Fillet086,Fillet087]
  Origin = -> Origin015
  Placement = pos=(0,0,0) rot=(0,1,0;1.5708rad)
  Tip = -> Fillet087
FEATURE [App::Part] Part007  label="2020-300-008"
  Group = -> [Body007]
  Origin = -> Origin014
  Placement = pos=(330,330,0) rot=(0,1,0;4.71239rad)
FEATURE [Sketcher::SketchObject] Sketch008
  FullyConstrained = false
  MapMode = 5
  Support = -> [XY_Plane017]
  sketch-geometry (46):
    g0: LineSegment StartX=3.4 StartY=2.65 StartZ=0 EndX=3.4 EndY=-2.6657 EndZ=0
    g1: LineSegment StartX=2.63162 StartY=-3.4 StartZ=0 EndX=-2.65 EndY=-3.4 EndZ=0
    g2: LineSegment StartX=-3.4 StartY=-2.63136 StartZ=0 EndX=-3.4 EndY=2.61487 EndZ=0
    g3: LineSegment StartX=-10 StartY=10 StartZ=0 EndX=-3.125 EndY=10 EndZ=0
    g4: LineSegment StartX=10 StartY=10 StartZ=0 EndX=10 EndY=3.125 EndZ=0
    g5: LineSegment StartX=10 StartY=-10 StartZ=0 EndX=3.125 EndY=-10 EndZ=0
    g6: LineSegment StartX=-10 StartY=-10 StartZ=0 EndX=-10 EndY=-3.125 EndZ=0
    g7: GeomPoint X=3e-16 Y=0 Z=0
    g8: Circle CenterX=3e-16 CenterY=0 CenterZ=0 NormalX=0 NormalY=0 NormalZ=1 AngleXU=0 Radius=2.1
    g9: LineSegment StartX=-4.76483 StartY=8.08721 StartZ=0 EndX=-3.55 EndY=8.08721 EndZ=0
    g10: LineSegment StartX=8.24722 StartY=4.75 StartZ=0 EndX=8.24722 EndY=3.55 EndZ=0
    g11: LineSegment StartX=-8.2 StartY=-4.73729 StartZ=0 EndX=-8.2 EndY=-3.55 EndZ=0
    g12: LineSegment StartX=5.5 StartY=4.75 StartZ=0 EndX=8.24722 EndY=4.75 EndZ=0
    g13: LineSegment StartX=4.75 StartY=5.50457 StartZ=0 EndX=2.65 EndY=3.4 EndZ=0
    g14: LineSegment StartX=4.75 StartY=5.50457 StartZ=0 EndX=4.75 EndY=8.08721 EndZ=0
    g15: LineSegment StartX=3.4 StartY=2.65 StartZ=0 EndX=5.5 EndY=4.75 EndZ=0
    g16: LineSegment StartX=-4.76483 StartY=5.50457 StartZ=0 EndX=-2.66166 EndY=3.4 EndZ=0
    g17: LineSegment StartX=-5.5 StartY=4.70904 StartZ=0 EndX=-3.4 EndY=2.61487 EndZ=0
    g18: LineSegment StartX=-4.76483 StartY=5.50457 StartZ=0 EndX=-4.76483 EndY=8.08721 EndZ=0
    g19: LineSegment StartX=-5.5 StartY=4.70904 StartZ=0 EndX=-8.2 EndY=4.70904 EndZ=0
    g20: LineSegment StartX=-10 StartY=3.125 StartZ=0 EndX=-10 EndY=10 EndZ=0
    g21: LineSegment StartX=-8.2 StartY=3.55 StartZ=0 EndX=-8.2 EndY=4.70904 EndZ=0
    g22: LineSegment StartX=3.55 StartY=8.08721 StartZ=0 EndX=4.75 EndY=8.08721 EndZ=0
    g23: LineSegment StartX=3.125 StartY=10 StartZ=0 EndX=10 EndY=10 EndZ=0
    g24: LineSegment StartX=-5.5 StartY=-4.73729 StartZ=0 EndX=-8.2 EndY=-4.73729 EndZ=0
    g25: LineSegment StartX=-4.75 StartY=-5.5 StartZ=0 EndX=-2.65 EndY=-3.4 EndZ=0
    g26: LineSegment StartX=-4.75 StartY=-5.5 StartZ=0 EndX=-4.75 EndY=-8.2 EndZ=0
    g27: LineSegment StartX=4.73747 StartY=-5.5 StartZ=0 EndX=4.73747 EndY=-8.2 EndZ=0
    g28: LineSegment StartX=5.5 StartY=-4.7671 StartZ=0 EndX=8.24722 EndY=-4.7671 EndZ=0
    g29: LineSegment StartX=-3.125 StartY=-10 StartZ=0 EndX=-10 EndY=-10 EndZ=0
    g30: LineSegment StartX=-3.55 StartY=-8.2 StartZ=0 EndX=-4.75 EndY=-8.2 EndZ=0
    g31: LineSegment StartX=4.73747 StartY=-8.2 StartZ=0 EndX=3.55 EndY=-8.2 EndZ=0
    g32: LineSegment StartX=10 StartY=-3.125 StartZ=0 EndX=10 EndY=-10 EndZ=0
    g33: LineSegment StartX=8.24722 StartY=-3.55 StartZ=0 EndX=8.24722 EndY=-4.7671 EndZ=0
    g34: LineSegment StartX=-2.66166 StartY=3.4 StartZ=0 EndX=2.65 EndY=3.4 EndZ=0
    g35: LineSegment StartX=-3.4 StartY=-2.63136 StartZ=0 EndX=-5.5 EndY=-4.73729 EndZ=0
    g36: LineSegment StartX=3.4 StartY=-2.6657 StartZ=0 EndX=5.5 EndY=-4.7671 EndZ=0
    g37: LineSegment StartX=2.63162 StartY=-3.4 StartZ=0 EndX=4.73747 EndY=-5.5 EndZ=0
    g38: LineSegment StartX=-3.55 StartY=-8.2 StartZ=0 EndX=-3.125 EndY=-10 EndZ=0
    g39: LineSegment StartX=3.55 StartY=-8.2 StartZ=0 EndX=3.125 EndY=-10 EndZ=0
    g40: LineSegment StartX=-3.125 StartY=10 StartZ=0 EndX=-3.55 EndY=8.08721 EndZ=0
    g41: LineSegment StartX=3.125 StartY=10 StartZ=0 EndX=3.55 EndY=8.08721 EndZ=0
    g42: LineSegment StartX=8.24722 StartY=3.55 StartZ=0 EndX=10 EndY=3.125 EndZ=0
    g43: LineSegment StartX=10 StartY=-3.125 StartZ=0 EndX=8.24722 EndY=-3.55 EndZ=0
    g44: LineSegment StartX=-10 StartY=-3.125 StartZ=0 EndX=-8.2 EndY=-3.55 EndZ=0
    g45: LineSegment StartX=-10 StartY=3.125 StartZ=0 EndX=-8.2 EndY=3.55 EndZ=0
  constraints (61):
    c: Horizontal(g1)
    c: Vertical(g0)
    c: Vertical(g2)
    c: Coincident(g23,g4)
    c: Coincident(g32,g5)
    c: Coincident(g29,g6)
    c: Coincident(g20,g3)
    c: Horizontal(g3)
    c: Horizontal(g5)
    c: Vertical(g4)
    c: Vertical(g6)
    c: PointOnObject(g7,g-1)
    c: DistanceX(g3,g7) = 10
    c: DistanceX(g-1,g23) = 10
    c: DistanceY(g7,g3) = 10
    c: DistanceX(g3,g-1) = 10
    c: DistanceY(g32,g7) = 10
    c: Coincident(g8,g7)
    c: Radius(g8) = 2.1
    c: Horizontal(g9)
    c: Vertical(g10)
    c: Vertical(g11)
    c: Coincident(g12,g15)
    c: Horizontal(g12)
    c: Coincident(g14,g13)
    c: Vertical(g14)
    c: Coincident(g15,g0)
    c: Coincident(g13,g34)
    c: Coincident(g14,g22)
    c: Coincident(g18,g16)
    c: Vertical(g18)
    c: Coincident(g19,g17)
    c: Horizontal(g19)
    c: Coincident(g9,g18)
    c: Coincident(g21,g19)
    c: Coincident(g24,g35)
    c: Horizontal(g24)
    c: Coincident(g26,g25)
    c: Vertical(g26)
    c: Coincident(g27,g37)
    c: Vertical(g27)
    c: Coincident(g28,g36)
    c: Horizontal(g28)
    c: Coincident(g11,g24)
    c: Coincident(g26,g30)
    c: Coincident(g31,g27)
    c: Coincident(g12,g10)
    c: Coincident(g28,g33)
    c: Coincident(g25,g1)
    c: Coincident(g35,g2)
    c: Coincident(g17,g2)
    c: Coincident(g16,g34)
    c: Coincident(g1,g37)
    c: Coincident(g0,g36)
    c: Coincident(g39,g5)
    c: Coincident(g40,g3)
    c: Coincident(g42,g4)
    c: Coincident(g44,g6)
    c: Coincident(g21,g45)
    c: Coincident(g33,g43)
    c: Coincident(g10,g42)
FEATURE [PartDesign::Pad] Pad008
  Direction = (0,0,1)
  Length = 300
  Length2 = 10
  Profile = -> Sketch008
  Type = 0
FEATURE [PartDesign::Fillet] Fillet088
  Base = -> Pad008 [Edge53]
  BaseFeature = -> Pad008
  Radius = 1
  SupportTransform = false
FEATURE [PartDesign::Fillet] Fillet089
  Base = -> Fillet088 [Edge114]
  BaseFeature = -> Fillet088
  Radius = 1
  SupportTransform = false
FEATURE [PartDesign::Fillet] Fillet090
  Base = -> Fillet089 [Edge137,Edge95]
  BaseFeature = -> Fillet089
  Radius = 0.5
  SupportTransform = false
FEATURE [PartDesign::Fillet] Fillet091
  Base = -> Fillet090 [Edge103]
  BaseFeature = -> Fillet090
  Radius = 0.5
  SupportTransform = false
FEATURE [PartDesign::Fillet] Fillet092
  Base = -> Fillet091 [Edge96]
  BaseFeature = -> Fillet091
  Radius = 0.5
  SupportTransform = false
FEATURE [PartDesign::Fillet] Fillet093
  Base = -> Fillet092 [Edge77]
  BaseFeature = -> Fillet092
  Radius = 0.5
  SupportTransform = false
FEATURE [PartDesign::Fillet] Fillet094
  Base = -> Fillet093 [Edge102]
  BaseFeature = -> Fillet093
  Radius = 0.5
  SupportTransform = false
FEATURE [PartDesign::Fillet] Fillet095
  Base = -> Fillet094 [Edge85]
  BaseFeature = -> Fillet094
  Radius = 0.5
  SupportTransform = false
FEATURE [PartDesign::Fillet] Fillet096
  Base = -> Fillet095 [Edge78]
  BaseFeature = -> Fillet095
  Radius = 0.5
  SupportTransform = false
FEATURE [PartDesign::Fillet] Fillet097
  Base = -> Fillet096 [Edge107]
  BaseFeature = -> Fillet096
  Radius = 0.5
  SupportTransform = false
FEATURE [PartDesign::Fillet] Fillet098
  Base = -> Fillet097 [Edge74]
  BaseFeature = -> Fillet097
  Radius = 0.5
  SupportTransform = false
FEATURE [PartDesign::Body] Body008
  Group = -> [Sketch008,Pad008,Fillet088,Fillet089,Fillet090,Fillet091,Fillet092,Fillet093,Fillet094,Fillet095,Fillet096,Fillet097,Fillet098]
  Origin = -> Origin017
  Placement = pos=(0,0,0) rot=(0,1,0;1.5708rad)
  Tip = -> Fillet098
FEATURE [App::Part] Part008  label="2020-300-009"
  Group = -> [Body008]
  Origin = -> Origin016
  Placement = pos=(20,330,180) rot=(0,0,1;0rad)
FEATURE [Sketcher::SketchObject] Sketch009
  FullyConstrained = false
  MapMode = 5
  Support = -> [XY_Plane019]
  sketch-geometry (46):
    g0: LineSegment StartX=3.4 StartY=2.65 StartZ=0 EndX=3.4 EndY=-2.6657 EndZ=0
    g1: LineSegment StartX=2.63162 StartY=-3.4 StartZ=0 EndX=-2.65 EndY=-3.4 EndZ=0
    g2: LineSegment StartX=-3.4 StartY=-2.63136 StartZ=0 EndX=-3.4 EndY=2.61487 EndZ=0
    g3: LineSegment StartX=-10 StartY=10 StartZ=0 EndX=-3.125 EndY=10 EndZ=0
    g4: LineSegment StartX=10 StartY=10 StartZ=0 EndX=10 EndY=3.125 EndZ=0
    g5: LineSegment StartX=10 StartY=-10 StartZ=0 EndX=3.125 EndY=-10 EndZ=0
    g6: LineSegment StartX=-10 StartY=-10 StartZ=0 EndX=-10 EndY=-3.125 EndZ=0
    g7: GeomPoint X=3e-16 Y=0 Z=0
    g8: Circle CenterX=3e-16 CenterY=0 CenterZ=0 NormalX=0 NormalY=0 NormalZ=1 AngleXU=0 Radius=2.1
    g9: LineSegment StartX=-4.76483 StartY=8.08721 StartZ=0 EndX=-3.55 EndY=8.08721 EndZ=0
    g10: LineSegment StartX=8.24722 StartY=4.75 StartZ=0 EndX=8.24722 EndY=3.55 EndZ=0
    g11: LineSegment StartX=-8.2 StartY=-4.73729 StartZ=0 EndX=-8.2 EndY=-3.55 EndZ=0
    g12: LineSegment StartX=5.5 StartY=4.75 StartZ=0 EndX=8.24722 EndY=4.75 EndZ=0
    g13: LineSegment StartX=4.75 StartY=5.50457 StartZ=0 EndX=2.65 EndY=3.4 EndZ=0
    g14: LineSegment StartX=4.75 StartY=5.50457 StartZ=0 EndX=4.75 EndY=8.08721 EndZ=0
    g15: LineSegment StartX=3.4 StartY=2.65 StartZ=0 EndX=5.5 EndY=4.75 EndZ=0
    g16: LineSegment StartX=-4.76483 StartY=5.50457 StartZ=0 EndX=-2.66166 EndY=3.4 EndZ=0
    g17: LineSegment StartX=-5.5 StartY=4.70904 StartZ=0 EndX=-3.4 EndY=2.61487 EndZ=0
    g18: LineSegment StartX=-4.76483 StartY=5.50457 StartZ=0 EndX=-4.76483 EndY=8.08721 EndZ=0
    g19: LineSegment StartX=-5.5 StartY=4.70904 StartZ=0 EndX=-8.2 EndY=4.70904 EndZ=0
    g20: LineSegment StartX=-10 StartY=3.125 StartZ=0 EndX=-10 EndY=10 EndZ=0
    g21: LineSegment StartX=-8.2 StartY=3.55 StartZ=0 EndX=-8.2 EndY=4.70904 EndZ=0
    g22: LineSegment StartX=3.55 StartY=8.08721 StartZ=0 EndX=4.75 EndY=8.08721 EndZ=0
    g23: LineSegment StartX=3.125 StartY=10 StartZ=0 EndX=10 EndY=10 EndZ=0
    g24: LineSegment StartX=-5.5 StartY=-4.73729 StartZ=0 EndX=-8.2 EndY=-4.73729 EndZ=0
    g25: LineSegment StartX=-4.75 StartY=-5.5 StartZ=0 EndX=-2.65 EndY=-3.4 EndZ=0
    g26: LineSegment StartX=-4.75 StartY=-5.5 StartZ=0 EndX=-4.75 EndY=-8.2 EndZ=0
    g27: LineSegment StartX=4.73747 StartY=-5.5 StartZ=0 EndX=4.73747 EndY=-8.2 EndZ=0
    g28: LineSegment StartX=5.5 StartY=-4.7671 StartZ=0 EndX=8.24722 EndY=-4.7671 EndZ=0
    g29: LineSegment StartX=-3.125 StartY=-10 StartZ=0 EndX=-10 EndY=-10 EndZ=0
    g30: LineSegment StartX=-3.55 StartY=-8.2 StartZ=0 EndX=-4.75 EndY=-8.2 EndZ=0
    g31: LineSegment StartX=4.73747 StartY=-8.2 StartZ=0 EndX=3.55 EndY=-8.2 EndZ=0
    g32: LineSegment StartX=10 StartY=-3.125 StartZ=0 EndX=10 EndY=-10 EndZ=0
    g33: LineSegment StartX=8.24722 StartY=-3.55 StartZ=0 EndX=8.24722 EndY=-4.7671 EndZ=0
    g34: LineSegment StartX=-2.66166 StartY=3.4 StartZ=0 EndX=2.65 EndY=3.4 EndZ=0
    g35: LineSegment StartX=-3.4 StartY=-2.63136 StartZ=0 EndX=-5.5 EndY=-4.73729 EndZ=0
    g36: LineSegment StartX=3.4 StartY=-2.6657 StartZ=0 EndX=5.5 EndY=-4.7671 EndZ=0
    g37: LineSegment StartX=2.63162 StartY=-3.4 StartZ=0 EndX=4.73747 EndY=-5.5 EndZ=0
    g38: LineSegment StartX=-3.55 StartY=-8.2 StartZ=0 EndX=-3.125 EndY=-10 EndZ=0
    g39: LineSegment StartX=3.55 StartY=-8.2 StartZ=0 EndX=3.125 EndY=-10 EndZ=0
    g40: LineSegment StartX=-3.125 StartY=10 StartZ=0 EndX=-3.55 EndY=8.08721 EndZ=0
    g41: LineSegment StartX=3.125 StartY=10 StartZ=0 EndX=3.55 EndY=8.08721 EndZ=0
    g42: LineSegment StartX=8.24722 StartY=3.55 StartZ=0 EndX=10 EndY=3.125 EndZ=0
    g43: LineSegment StartX=10 StartY=-3.125 StartZ=0 EndX=8.24722 EndY=-3.55 EndZ=0
    g44: LineSegment StartX=-10 StartY=-3.125 StartZ=0 EndX=-8.2 EndY=-3.55 EndZ=0
    g45: LineSegment StartX=-10 StartY=3.125 StartZ=0 EndX=-8.2 EndY=3.55 EndZ=0
  constraints (61):
    c: Horizontal(g1)
    c: Vertical(g0)
    c: Vertical(g2)
    c: Coincident(g23,g4)
    c: Coincident(g32,g5)
    c: Coincident(g29,g6)
    c: Coincident(g20,g3)
    c: Horizontal(g3)
    c: Horizontal(g5)
    c: Vertical(g4)
    c: Vertical(g6)
    c: PointOnObject(g7,g-1)
    c: DistanceX(g3,g7) = 10
    c: DistanceX(g-1,g23) = 10
    c: DistanceY(g7,g3) = 10
    c: DistanceX(g3,g-1) = 10
    c: DistanceY(g32,g7) = 10
    c: Coincident(g8,g7)
    c: Radius(g8) = 2.1
    c: Horizontal(g9)
    c: Vertical(g10)
    c: Vertical(g11)
    c: Coincident(g12,g15)
    c: Horizontal(g12)
    c: Coincident(g14,g13)
    c: Vertical(g14)
    c: Coincident(g15,g0)
    c: Coincident(g13,g34)
    c: Coincident(g14,g22)
    c: Coincident(g18,g16)
    c: Vertical(g18)
    c: Coincident(g19,g17)
    c: Horizontal(g19)
    c: Coincident(g9,g18)
    c: Coincident(g21,g19)
    c: Coincident(g24,g35)
    c: Horizontal(g24)
    c: Coincident(g26,g25)
    c: Vertical(g26)
    c: Coincident(g27,g37)
    c: Vertical(g27)
    c: Coincident(g28,g36)
    c: Horizontal(g28)
    c: Coincident(g11,g24)
    c: Coincident(g26,g30)
    c: Coincident(g31,g27)
    c: Coincident(g12,g10)
    c: Coincident(g28,g33)
    c: Coincident(g25,g1)
    c: Coincident(g35,g2)
    c: Coincident(g17,g2)
    c: Coincident(g16,g34)
    c: Coincident(g1,g37)
    c: Coincident(g0,g36)
    c: Coincident(g39,g5)
    c: Coincident(g40,g3)
    c: Coincident(g42,g4)
    c: Coincident(g44,g6)
    c: Coincident(g21,g45)
    c: Coincident(g33,g43)
    c: Coincident(g10,g42)
FEATURE [PartDesign::Pad] Pad009
  Direction = (0,0,1)
  Length = 300
  Length2 = 10
  Profile = -> Sketch009
  Type = 0
FEATURE [PartDesign::Fillet] Fillet099
  Base = -> Pad009 [Edge53]
  BaseFeature = -> Pad009
  Radius = 1
  SupportTransform = false
FEATURE [PartDesign::Fillet] Fillet100
  Base = -> Fillet099 [Edge114]
  BaseFeature = -> Fillet099
  Radius = 1
  SupportTransform = false
FEATURE [PartDesign::Fillet] Fillet101
  Base = -> Fillet100 [Edge137,Edge95]
  BaseFeature = -> Fillet100
  Radius = 0.5
  SupportTransform = false
FEATURE [PartDesign::Fillet] Fillet102
  Base = -> Fillet101 [Edge103]
  BaseFeature = -> Fillet101
  Radius = 0.5
  SupportTransform = false
FEATURE [PartDesign::Fillet] Fillet103
  Base = -> Fillet102 [Edge96]
  BaseFeature = -> Fillet102
  Radius = 0.5
  SupportTransform = false
FEATURE [PartDesign::Fillet] Fillet104
  Base = -> Fillet103 [Edge77]
  BaseFeature = -> Fillet103
  Radius = 0.5
  SupportTransform = false
FEATURE [PartDesign::Fillet] Fillet105
  Base = -> Fillet104 [Edge102]
  BaseFeature = -> Fillet104
  Radius = 0.5
  SupportTransform = false
FEATURE [PartDesign::Fillet] Fillet106
  Base = -> Fillet105 [Edge85]
  BaseFeature = -> Fillet105
  Radius = 0.5
  SupportTransform = false
FEATURE [PartDesign::Fillet] Fillet107
  Base = -> Fillet106 [Edge78]
  BaseFeature = -> Fillet106
  Radius = 0.5
  SupportTransform = false
FEATURE [PartDesign::Fillet] Fillet108
  Base = -> Fillet107 [Edge107]
  BaseFeature = -> Fillet107
  Radius = 0.5
  SupportTransform = false
FEATURE [PartDesign::Fillet] Fillet109
  Base = -> Fillet108 [Edge74]
  BaseFeature = -> Fillet108
  Radius = 0.5
  SupportTransform = false
FEATURE [PartDesign::Body] Body009
  Group = -> [Sketch009,Pad009,Fillet099,Fillet100,Fillet101,Fillet102,Fillet103,Fillet104,Fillet105,Fillet106,Fillet107,Fillet108,Fillet109]
  Origin = -> Origin019
  Placement = pos=(0,0,0) rot=(0,1,0;1.5708rad)
  Tip = -> Fillet109
FEATURE [App::Part] Part009  label="2020-300-010"
  Group = -> [Body009]
  Origin = -> Origin018
  Placement = pos=(20,10,180) rot=(0,0,1;0rad)
FEATURE [Sketcher::SketchObject] Sketch010
  FullyConstrained = false
  MapMode = 5
  Support = -> [XY_Plane021]
  sketch-geometry (46):
    g0: LineSegment StartX=3.4 StartY=2.65 StartZ=0 EndX=3.4 EndY=-2.6657 EndZ=0
    g1: LineSegment StartX=2.63162 StartY=-3.4 StartZ=0 EndX=-2.65 EndY=-3.4 EndZ=0
    g2: LineSegment StartX=-3.4 StartY=-2.63136 StartZ=0 EndX=-3.4 EndY=2.61487 EndZ=0
    g3: LineSegment StartX=-10 StartY=10 StartZ=0 EndX=-3.125 EndY=10 EndZ=0
    g4: LineSegment StartX=10 StartY=10 StartZ=0 EndX=10 EndY=3.125 EndZ=0
    g5: LineSegment StartX=10 StartY=-10 StartZ=0 EndX=3.125 EndY=-10 EndZ=0
    g6: LineSegment StartX=-10 StartY=-10 StartZ=0 EndX=-10 EndY=-3.125 EndZ=0
    g7: GeomPoint X=3e-16 Y=0 Z=0
    g8: Circle CenterX=3e-16 CenterY=0 CenterZ=0 NormalX=0 NormalY=0 NormalZ=1 AngleXU=0 Radius=2.1
    g9: LineSegment StartX=-4.76483 StartY=8.08721 StartZ=0 EndX=-3.55 EndY=8.08721 EndZ=0
    g10: LineSegment StartX=8.24722 StartY=4.75 StartZ=0 EndX=8.24722 EndY=3.55 EndZ=0
    g11: LineSegment StartX=-8.2 StartY=-4.73729 StartZ=0 EndX=-8.2 EndY=-3.55 EndZ=0
    g12: LineSegment StartX=5.5 StartY=4.75 StartZ=0 EndX=8.24722 EndY=4.75 EndZ=0
    g13: LineSegment StartX=4.75 StartY=5.50457 StartZ=0 EndX=2.65 EndY=3.4 EndZ=0
    g14: LineSegment StartX=4.75 StartY=5.50457 StartZ=0 EndX=4.75 EndY=8.08721 EndZ=0
    g15: LineSegment StartX=3.4 StartY=2.65 StartZ=0 EndX=5.5 EndY=4.75 EndZ=0
    g16: LineSegment StartX=-4.76483 StartY=5.50457 StartZ=0 EndX=-2.66166 EndY=3.4 EndZ=0
    g17: LineSegment StartX=-5.5 StartY=4.70904 StartZ=0 EndX=-3.4 EndY=2.61487 EndZ=0
    g18: LineSegment StartX=-4.76483 StartY=5.50457 StartZ=0 EndX=-4.76483 EndY=8.08721 EndZ=0
    g19: LineSegment StartX=-5.5 StartY=4.70904 StartZ=0 EndX=-8.2 EndY=4.70904 EndZ=0
    g20: LineSegment StartX=-10 StartY=3.125 StartZ=0 EndX=-10 EndY=10 EndZ=0
    g21: LineSegment StartX=-8.2 StartY=3.55 StartZ=0 EndX=-8.2 EndY=4.70904 EndZ=0
    g22: LineSegment StartX=3.55 StartY=8.08721 StartZ=0 EndX=4.75 EndY=8.08721 EndZ=0
    g23: LineSegment StartX=3.125 StartY=10 StartZ=0 EndX=10 EndY=10 EndZ=0
    g24: LineSegment StartX=-5.5 StartY=-4.73729 StartZ=0 EndX=-8.2 EndY=-4.73729 EndZ=0
    g25: LineSegment StartX=-4.75 StartY=-5.5 StartZ=0 EndX=-2.65 EndY=-3.4 EndZ=0
    g26: LineSegment StartX=-4.75 StartY=-5.5 StartZ=0 EndX=-4.75 EndY=-8.2 EndZ=0
    g27: LineSegment StartX=4.73747 StartY=-5.5 StartZ=0 EndX=4.73747 EndY=-8.2 EndZ=0
    g28: LineSegment StartX=5.5 StartY=-4.7671 StartZ=0 EndX=8.24722 EndY=-4.7671 EndZ=0
    g29: LineSegment StartX=-3.125 StartY=-10 StartZ=0 EndX=-10 EndY=-10 EndZ=0
    g30: LineSegment StartX=-3.55 StartY=-8.2 StartZ=0 EndX=-4.75 EndY=-8.2 EndZ=0
    g31: LineSegment StartX=4.73747 StartY=-8.2 StartZ=0 EndX=3.55 EndY=-8.2 EndZ=0
    g32: LineSegment StartX=10 StartY=-3.125 StartZ=0 EndX=10 EndY=-10 EndZ=0
    g33: LineSegment StartX=8.24722 StartY=-3.55 StartZ=0 EndX=8.24722 EndY=-4.7671 EndZ=0
    g34: LineSegment StartX=-2.66166 StartY=3.4 StartZ=0 EndX=2.65 EndY=3.4 EndZ=0
    g35: LineSegment StartX=-3.4 StartY=-2.63136 StartZ=0 EndX=-5.5 EndY=-4.73729 EndZ=0
    g36: LineSegment StartX=3.4 StartY=-2.6657 StartZ=0 EndX=5.5 EndY=-4.7671 EndZ=0
    g37: LineSegment StartX=2.63162 StartY=-3.4 StartZ=0 EndX=4.73747 EndY=-5.5 EndZ=0
    g38: LineSegment StartX=-3.55 StartY=-8.2 StartZ=0 EndX=-3.125 EndY=-10 EndZ=0
    g39: LineSegment StartX=3.55 StartY=-8.2 StartZ=0 EndX=3.125 EndY=-10 EndZ=0
    g40: LineSegment StartX=-3.125 StartY=10 StartZ=0 EndX=-3.55 EndY=8.08721 EndZ=0
    g41: LineSegment StartX=3.125 StartY=10 StartZ=0 EndX=3.55 EndY=8.08721 EndZ=0
    g42: LineSegment StartX=8.24722 StartY=3.55 StartZ=0 EndX=10 EndY=3.125 EndZ=0
    g43: LineSegment StartX=10 StartY=-3.125 StartZ=0 EndX=8.24722 EndY=-3.55 EndZ=0
    g44: LineSegment StartX=-10 StartY=-3.125 StartZ=0 EndX=-8.2 EndY=-3.55 EndZ=0
    g45: LineSegment StartX=-10 StartY=3.125 StartZ=0 EndX=-8.2 EndY=3.55 EndZ=0
  constraints (61):
    c: Horizontal(g1)
    c: Vertical(g0)
    c: Vertical(g2)
    c: Coincident(g23,g4)
    c: Coincident(g32,g5)
    c: Coincident(g29,g6)
    c: Coincident(g20,g3)
    c: Horizontal(g3)
    c: Horizontal(g5)
    c: Vertical(g4)
    c: Vertical(g6)
    c: PointOnObject(g7,g-1)
    c: DistanceX(g3,g7) = 10
    c: DistanceX(g-1,g23) = 10
    c: DistanceY(g7,g3) = 10
    c: DistanceX(g3,g-1) = 10
    c: DistanceY(g32,g7) = 10
    c: Coincident(g8,g7)
    c: Radius(g8) = 2.1
    c: Horizontal(g9)
    c: Vertical(g10)
    c: Vertical(g11)
    c: Coincident(g12,g15)
    c: Horizontal(g12)
    c: Coincident(g14,g13)
    c: Vertical(g14)
    c: Coincident(g15,g0)
    c: Coincident(g13,g34)
    c: Coincident(g14,g22)
    c: Coincident(g18,g16)
    c: Vertical(g18)
    c: Coincident(g19,g17)
    c: Horizontal(g19)
    c: Coincident(g9,g18)
    c: Coincident(g21,g19)
    c: Coincident(g24,g35)
    c: Horizontal(g24)
    c: Coincident(g26,g25)
    c: Vertical(g26)
    c: Coincident(g27,g37)
    c: Vertical(g27)
    c: Coincident(g28,g36)
    c: Horizontal(g28)
    c: Coincident(g11,g24)
    c: Coincident(g26,g30)
    c: Coincident(g31,g27)
    c: Coincident(g12,g10)
    c: Coincident(g28,g33)
    c: Coincident(g25,g1)
    c: Coincident(g35,g2)
    c: Coincident(g17,g2)
    c: Coincident(g16,g34)
    c: Coincident(g1,g37)
    c: Coincident(g0,g36)
    c: Coincident(g39,g5)
    c: Coincident(g40,g3)
    c: Coincident(g42,g4)
    c: Coincident(g44,g6)
    c: Coincident(g21,g45)
    c: Coincident(g33,g43)
    c: Coincident(g10,g42)
FEATURE [PartDesign::Pad] Pad010
  Direction = (0,0,1)
  Length = 300
  Length2 = 10
  Profile = -> Sketch010
  Type = 0
FEATURE [PartDesign::Fillet] Fillet110
  Base = -> Pad010 [Edge53]
  BaseFeature = -> Pad010
  Radius = 1
  SupportTransform = false
FEATURE [PartDesign::Fillet] Fillet111
  Base = -> Fillet110 [Edge114]
  BaseFeature = -> Fillet110
  Radius = 1
  SupportTransform = false
FEATURE [PartDesign::Fillet] Fillet112
  Base = -> Fillet111 [Edge137,Edge95]
  BaseFeature = -> Fillet111
  Radius = 0.5
  SupportTransform = false
FEATURE [PartDesign::Fillet] Fillet113
  Base = -> Fillet112 [Edge103]
  BaseFeature = -> Fillet112
  Radius = 0.5
  SupportTransform = false
FEATURE [PartDesign::Fillet] Fillet114
  Base = -> Fillet113 [Edge96]
  BaseFeature = -> Fillet113
  Radius = 0.5
  SupportTransform = false
FEATURE [PartDesign::Fillet] Fillet115
  Base = -> Fillet114 [Edge77]
  BaseFeature = -> Fillet114
  Radius = 0.5
  SupportTransform = false
FEATURE [PartDesign::Fillet] Fillet116
  Base = -> Fillet115 [Edge102]
  BaseFeature = -> Fillet115
  Radius = 0.5
  SupportTransform = false
FEATURE [PartDesign::Fillet] Fillet117
  Base = -> Fillet116 [Edge85]
  BaseFeature = -> Fillet116
  Radius = 0.5
  SupportTransform = false
FEATURE [PartDesign::Fillet] Fillet118
  Base = -> Fillet117 [Edge78]
  BaseFeature = -> Fillet117
  Radius = 0.5
  SupportTransform = false
FEATURE [PartDesign::Fillet] Fillet119
  Base = -> Fillet118 [Edge107]
  BaseFeature = -> Fillet118
  Radius = 0.5
  SupportTransform = false
FEATURE [PartDesign::Fillet] Fillet120
  Base = -> Fillet119 [Edge74]
  BaseFeature = -> Fillet119
  Radius = 0.5
  SupportTransform = false
FEATURE [PartDesign::Body] Body010
  Group = -> [Sketch010,Pad010,Fillet110,Fillet111,Fillet112,Fillet113,Fillet114,Fillet115,Fillet116,Fillet117,Fillet118,Fillet119,Fillet120]
  Origin = -> Origin021
  Placement = pos=(0,0,0) rot=(0,1,0;1.5708rad)
  Tip = -> Fillet120
FEATURE [App::Part] Part010  label="2020-300-011"
  Group = -> [Body010]
  Origin = -> Origin020
  Placement = pos=(10,20,179) rot=(0,0,1;1.5708rad)
FEATURE [Sketcher::SketchObject] Sketch011
  FullyConstrained = false
  MapMode = 5
  Support = -> [XY_Plane023]
  sketch-geometry (46):
    g0: LineSegment StartX=3.4 StartY=2.65 StartZ=0 EndX=3.4 EndY=-2.6657 EndZ=0
    g1: LineSegment StartX=2.63162 StartY=-3.4 StartZ=0 EndX=-2.65 EndY=-3.4 EndZ=0
    g2: LineSegment StartX=-3.4 StartY=-2.63136 StartZ=0 EndX=-3.4 EndY=2.61487 EndZ=0
    g3: LineSegment StartX=-10 StartY=10 StartZ=0 EndX=-3.125 EndY=10 EndZ=0
    g4: LineSegment StartX=10 StartY=10 StartZ=0 EndX=10 EndY=3.125 EndZ=0
    g5: LineSegment StartX=10 StartY=-10 StartZ=0 EndX=3.125 EndY=-10 EndZ=0
    g6: LineSegment StartX=-10 StartY=-10 StartZ=0 EndX=-10 EndY=-3.125 EndZ=0
    g7: GeomPoint X=3e-16 Y=0 Z=0
    g8: Circle CenterX=3e-16 CenterY=0 CenterZ=0 NormalX=0 NormalY=0 NormalZ=1 AngleXU=0 Radius=2.1
    g9: LineSegment StartX=-4.76483 StartY=8.08721 StartZ=0 EndX=-3.55 EndY=8.08721 EndZ=0
    g10: LineSegment StartX=8.24722 StartY=4.75 StartZ=0 EndX=8.24722 EndY=3.55 EndZ=0
    g11: LineSegment StartX=-8.2 StartY=-4.73729 StartZ=0 EndX=-8.2 EndY=-3.55 EndZ=0
    g12: LineSegment StartX=5.5 StartY=4.75 StartZ=0 EndX=8.24722 EndY=4.75 EndZ=0
    g13: LineSegment StartX=4.75 StartY=5.50457 StartZ=0 EndX=2.65 EndY=3.4 EndZ=0
    g14: LineSegment StartX=4.75 StartY=5.50457 StartZ=0 EndX=4.75 EndY=8.08721 EndZ=0
    g15: LineSegment StartX=3.4 StartY=2.65 StartZ=0 EndX=5.5 EndY=4.75 EndZ=0
    g16: LineSegment StartX=-4.76483 StartY=5.50457 StartZ=0 EndX=-2.66166 EndY=3.4 EndZ=0
    g17: LineSegment StartX=-5.5 StartY=4.70904 StartZ=0 EndX=-3.4 EndY=2.61487 EndZ=0
    g18: LineSegment StartX=-4.76483 StartY=5.50457 StartZ=0 EndX=-4.76483 EndY=8.08721 EndZ=0
    g19: LineSegment StartX=-5.5 StartY=4.70904 StartZ=0 EndX=-8.2 EndY=4.70904 EndZ=0
    g20: LineSegment StartX=-10 StartY=3.125 StartZ=0 EndX=-10 EndY=10 EndZ=0
    g21: LineSegment StartX=-8.2 StartY=3.55 StartZ=0 EndX=-8.2 EndY=4.70904 EndZ=0
    g22: LineSegment StartX=3.55 StartY=8.08721 StartZ=0 EndX=4.75 EndY=8.08721 EndZ=0
    g23: LineSegment StartX=3.125 StartY=10 StartZ=0 EndX=10 EndY=10 EndZ=0
    g24: LineSegment StartX=-5.5 StartY=-4.73729 StartZ=0 EndX=-8.2 EndY=-4.73729 EndZ=0
    g25: LineSegment StartX=-4.75 StartY=-5.5 StartZ=0 EndX=-2.65 EndY=-3.4 EndZ=0
    g26: LineSegment StartX=-4.75 StartY=-5.5 StartZ=0 EndX=-4.75 EndY=-8.2 EndZ=0
    g27: LineSegment StartX=4.73747 StartY=-5.5 StartZ=0 EndX=4.73747 EndY=-8.2 EndZ=0
    g28: LineSegment StartX=5.5 StartY=-4.7671 StartZ=0 EndX=8.24722 EndY=-4.7671 EndZ=0
    g29: LineSegment StartX=-3.125 StartY=-10 StartZ=0 EndX=-10 EndY=-10 EndZ=0
    g30: LineSegment StartX=-3.55 StartY=-8.2 StartZ=0 EndX=-4.75 EndY=-8.2 EndZ=0
    g31: LineSegment StartX=4.73747 StartY=-8.2 StartZ=0 EndX=3.55 EndY=-8.2 EndZ=0
    g32: LineSegment StartX=10 StartY=-3.125 StartZ=0 EndX=10 EndY=-10 EndZ=0
    g33: LineSegment StartX=8.24722 StartY=-3.55 StartZ=0 EndX=8.24722 EndY=-4.7671 EndZ=0
    g34: LineSegment StartX=-2.66166 StartY=3.4 StartZ=0 EndX=2.65 EndY=3.4 EndZ=0
    g35: LineSegment StartX=-3.4 StartY=-2.63136 StartZ=0 EndX=-5.5 EndY=-4.73729 EndZ=0
    g36: LineSegment StartX=3.4 StartY=-2.6657 StartZ=0 EndX=5.5 EndY=-4.7671 EndZ=0
    g37: LineSegment StartX=2.63162 StartY=-3.4 StartZ=0 EndX=4.73747 EndY=-5.5 EndZ=0
    g38: LineSegment StartX=-3.55 StartY=-8.2 StartZ=0 EndX=-3.125 EndY=-10 EndZ=0
    g39: LineSegment StartX=3.55 StartY=-8.2 StartZ=0 EndX=3.125 EndY=-10 EndZ=0
    g40: LineSegment StartX=-3.125 StartY=10 StartZ=0 EndX=-3.55 EndY=8.08721 EndZ=0
    g41: LineSegment StartX=3.125 StartY=10 StartZ=0 EndX=3.55 EndY=8.08721 EndZ=0
    g42: LineSegment StartX=8.24722 StartY=3.55 StartZ=0 EndX=10 EndY=3.125 EndZ=0
    g43: LineSegment StartX=10 StartY=-3.125 StartZ=0 EndX=8.24722 EndY=-3.55 EndZ=0
    g44: LineSegment StartX=-10 StartY=-3.125 StartZ=0 EndX=-8.2 EndY=-3.55 EndZ=0
    g45: LineSegment StartX=-10 StartY=3.125 StartZ=0 EndX=-8.2 EndY=3.55 EndZ=0
  constraints (61):
    c: Horizontal(g1)
    c: Vertical(g0)
    c: Vertical(g2)
    c: Coincident(g23,g4)
    c: Coincident(g32,g5)
    c: Coincident(g29,g6)
    c: Coincident(g20,g3)
    c: Horizontal(g3)
    c: Horizontal(g5)
    c: Vertical(g4)
    c: Vertical(g6)
    c: PointOnObject(g7,g-1)
    c: DistanceX(g3,g7) = 10
    c: DistanceX(g-1,g23) = 10
    c: DistanceY(g7,g3) = 10
    c: DistanceX(g3,g-1) = 10
    c: DistanceY(g32,g7) = 10
    c: Coincident(g8,g7)
    c: Radius(g8) = 2.1
    c: Horizontal(g9)
    c: Vertical(g10)
    c: Vertical(g11)
    c: Coincident(g12,g15)
    c: Horizontal(g12)
    c: Coincident(g14,g13)
    c: Vertical(g14)
    c: Coincident(g15,g0)
    c: Coincident(g13,g34)
    c: Coincident(g14,g22)
    c: Coincident(g18,g16)
    c: Vertical(g18)
    c: Coincident(g19,g17)
    c: Horizontal(g19)
    c: Coincident(g9,g18)
    c: Coincident(g21,g19)
    c: Coincident(g24,g35)
    c: Horizontal(g24)
    c: Coincident(g26,g25)
    c: Vertical(g26)
    c: Coincident(g27,g37)
    c: Vertical(g27)
    c: Coincident(g28,g36)
    c: Horizontal(g28)
    c: Coincident(g11,g24)
    c: Coincident(g26,g30)
    c: Coincident(g31,g27)
    c: Coincident(g12,g10)
    c: Coincident(g28,g33)
    c: Coincident(g25,g1)
    c: Coincident(g35,g2)
    c: Coincident(g17,g2)
    c: Coincident(g16,g34)
    c: Coincident(g1,g37)
    c: Coincident(g0,g36)
    c: Coincident(g39,g5)
    c: Coincident(g40,g3)
    c: Coincident(g42,g4)
    c: Coincident(g44,g6)
    c: Coincident(g21,g45)
    c: Coincident(g33,g43)
    c: Coincident(g10,g42)
FEATURE [PartDesign::Pad] Pad011
  Direction = (0,0,1)
  Length = 300
  Length2 = 10
  Profile = -> Sketch011
  Type = 0
FEATURE [PartDesign::Fillet] Fillet121
  Base = -> Pad011 [Edge53]
  BaseFeature = -> Pad011
  Radius = 1
  SupportTransform = false
FEATURE [PartDesign::Fillet] Fillet122
  Base = -> Fillet121 [Edge114]
  BaseFeature = -> Fillet121
  Radius = 1
  SupportTransform = false
FEATURE [PartDesign::Fillet] Fillet123
  Base = -> Fillet122 [Edge137,Edge95]
  BaseFeature = -> Fillet122
  Radius = 0.5
  SupportTransform = false
FEATURE [PartDesign::Fillet] Fillet124
  Base = -> Fillet123 [Edge103]
  BaseFeature = -> Fillet123
  Radius = 0.5
  SupportTransform = false
FEATURE [PartDesign::Fillet] Fillet125
  Base = -> Fillet124 [Edge96]
  BaseFeature = -> Fillet124
  Radius = 0.5
  SupportTransform = false
FEATURE [PartDesign::Fillet] Fillet126
  Base = -> Fillet125 [Edge77]
  BaseFeature = -> Fillet125
  Radius = 0.5
  SupportTransform = false
FEATURE [PartDesign::Fillet] Fillet127
  Base = -> Fillet126 [Edge102]
  BaseFeature = -> Fillet126
  Radius = 0.5
  SupportTransform = false
FEATURE [PartDesign::Fillet] Fillet128
  Base = -> Fillet127 [Edge85]
  BaseFeature = -> Fillet127
  Radius = 0.5
  SupportTransform = false
FEATURE [PartDesign::Fillet] Fillet129
  Base = -> Fillet128 [Edge78]
  BaseFeature = -> Fillet128
  Radius = 0.5
  SupportTransform = false
FEATURE [PartDesign::Fillet] Fillet130
  Base = -> Fillet129 [Edge107]
  BaseFeature = -> Fillet129
  Radius = 0.5
  SupportTransform = false
FEATURE [PartDesign::Fillet] Fillet131
  Base = -> Fillet130 [Edge74]
  BaseFeature = -> Fillet130
  Radius = 0.5
  SupportTransform = false
FEATURE [PartDesign::Body] Body011
  Group = -> [Sketch011,Pad011,Fillet121,Fillet122,Fillet123,Fillet124,Fillet125,Fillet126,Fillet127,Fillet128,Fillet129,Fillet130,Fillet131]
  Origin = -> Origin023
  Placement = pos=(0,0,0) rot=(0,1,0;1.5708rad)
  Tip = -> Fillet131
FEATURE [App::Part] Part011  label="2020-300-012"
  Group = -> [Body011]
  Origin = -> Origin022
  Placement = pos=(330,20,180) rot=(0,0,1;1.5708rad)
FEATURE [Sketcher::SketchObject] Sketch012
  FullyConstrained = false
  MapMode = 5
  Support = -> [XY_Plane025]
  sketch-geometry (46):
    g0: LineSegment StartX=3.4 StartY=2.65 StartZ=0 EndX=3.4 EndY=-2.6657 EndZ=0
    g1: LineSegment StartX=2.63162 StartY=-3.4 StartZ=0 EndX=-2.65 EndY=-3.4 EndZ=0
    g2: LineSegment StartX=-3.4 StartY=-2.63136 StartZ=0 EndX=-3.4 EndY=2.61487 EndZ=0
    g3: LineSegment StartX=-10 StartY=10 StartZ=0 EndX=-3.125 EndY=10 EndZ=0
    g4: LineSegment StartX=10 StartY=10 StartZ=0 EndX=10 EndY=3.125 EndZ=0
    g5: LineSegment StartX=10 StartY=-10 StartZ=0 EndX=3.125 EndY=-10 EndZ=0
    g6: LineSegment StartX=-10 StartY=-10 StartZ=0 EndX=-10 EndY=-3.125 EndZ=0
    g7: GeomPoint X=3e-16 Y=0 Z=0
    g8: Circle CenterX=3e-16 CenterY=0 CenterZ=0 NormalX=0 NormalY=0 NormalZ=1 AngleXU=0 Radius=2.1
    g9: LineSegment StartX=-4.76483 StartY=8.08721 StartZ=0 EndX=-3.55 EndY=8.08721 EndZ=0
    g10: LineSegment StartX=8.24722 StartY=4.75 StartZ=0 EndX=8.24722 EndY=3.55 EndZ=0
    g11: LineSegment StartX=-8.2 StartY=-4.73729 StartZ=0 EndX=-8.2 EndY=-3.55 EndZ=0
    g12: LineSegment StartX=5.5 StartY=4.75 StartZ=0 EndX=8.24722 EndY=4.75 EndZ=0
    g13: LineSegment StartX=4.75 StartY=5.50457 StartZ=0 EndX=2.65 EndY=3.4 EndZ=0
    g14: LineSegment StartX=4.75 StartY=5.50457 StartZ=0 EndX=4.75 EndY=8.08721 EndZ=0
    g15: LineSegment StartX=3.4 StartY=2.65 StartZ=0 EndX=5.5 EndY=4.75 EndZ=0
    g16: LineSegment StartX=-4.76483 StartY=5.50457 StartZ=0 EndX=-2.66166 EndY=3.4 EndZ=0
    g17: LineSegment StartX=-5.5 StartY=4.70904 StartZ=0 EndX=-3.4 EndY=2.61487 EndZ=0
    g18: LineSegment StartX=-4.76483 StartY=5.50457 StartZ=0 EndX=-4.76483 EndY=8.08721 EndZ=0
    g19: LineSegment StartX=-5.5 StartY=4.70904 StartZ=0 EndX=-8.2 EndY=4.70904 EndZ=0
    g20: LineSegment StartX=-10 StartY=3.125 StartZ=0 EndX=-10 EndY=10 EndZ=0
    g21: LineSegment StartX=-8.2 StartY=3.55 StartZ=0 EndX=-8.2 EndY=4.70904 EndZ=0
    g22: LineSegment StartX=3.55 StartY=8.08721 StartZ=0 EndX=4.75 EndY=8.08721 EndZ=0
    g23: LineSegment StartX=3.125 StartY=10 StartZ=0 EndX=10 EndY=10 EndZ=0
    g24: LineSegment StartX=-5.5 StartY=-4.73729 StartZ=0 EndX=-8.2 EndY=-4.73729 EndZ=0
    g25: LineSegment StartX=-4.75 StartY=-5.5 StartZ=0 EndX=-2.65 EndY=-3.4 EndZ=0
    g26: LineSegment StartX=-4.75 StartY=-5.5 StartZ=0 EndX=-4.75 EndY=-8.2 EndZ=0
    g27: LineSegment StartX=4.73747 StartY=-5.5 StartZ=0 EndX=4.73747 EndY=-8.2 EndZ=0
    g28: LineSegment StartX=5.5 StartY=-4.7671 StartZ=0 EndX=8.24722 EndY=-4.7671 EndZ=0
    g29: LineSegment StartX=-3.125 StartY=-10 StartZ=0 EndX=-10 EndY=-10 EndZ=0
    g30: LineSegment StartX=-3.55 StartY=-8.2 StartZ=0 EndX=-4.75 EndY=-8.2 EndZ=0
    g31: LineSegment StartX=4.73747 StartY=-8.2 StartZ=0 EndX=3.55 EndY=-8.2 EndZ=0
    g32: LineSegment StartX=10 StartY=-3.125 StartZ=0 EndX=10 EndY=-10 EndZ=0
    g33: LineSegment StartX=8.24722 StartY=-3.55 StartZ=0 EndX=8.24722 EndY=-4.7671 EndZ=0
    g34: LineSegment StartX=-2.66166 StartY=3.4 StartZ=0 EndX=2.65 EndY=3.4 EndZ=0
    g35: LineSegment StartX=-3.4 StartY=-2.63136 StartZ=0 EndX=-5.5 EndY=-4.73729 EndZ=0
    g36: LineSegment StartX=3.4 StartY=-2.6657 StartZ=0 EndX=5.5 EndY=-4.7671 EndZ=0
    g37: LineSegment StartX=2.63162 StartY=-3.4 StartZ=0 EndX=4.73747 EndY=-5.5 EndZ=0
    g38: LineSegment StartX=-3.55 StartY=-8.2 StartZ=0 EndX=-3.125 EndY=-10 EndZ=0
    g39: LineSegment StartX=3.55 StartY=-8.2 StartZ=0 EndX=3.125 EndY=-10 EndZ=0
    g40: LineSegment StartX=-3.125 StartY=10 StartZ=0 EndX=-3.55 EndY=8.08721 EndZ=0
    g41: LineSegment StartX=3.125 StartY=10 StartZ=0 EndX=3.55 EndY=8.08721 EndZ=0
    g42: LineSegment StartX=8.24722 StartY=3.55 StartZ=0 EndX=10 EndY=3.125 EndZ=0
    g43: LineSegment StartX=10 StartY=-3.125 StartZ=0 EndX=8.24722 EndY=-3.55 EndZ=0
    g44: LineSegment StartX=-10 StartY=-3.125 StartZ=0 EndX=-8.2 EndY=-3.55 EndZ=0
    g45: LineSegment StartX=-10 StartY=3.125 StartZ=0 EndX=-8.2 EndY=3.55 EndZ=0
  constraints (61):
    c: Horizontal(g1)
    c: Vertical(g0)
    c: Vertical(g2)
    c: Coincident(g23,g4)
    c: Coincident(g32,g5)
    c: Coincident(g29,g6)
    c: Coincident(g20,g3)
    c: Horizontal(g3)
    c: Horizontal(g5)
    c: Vertical(g4)
    c: Vertical(g6)
    c: PointOnObject(g7,g-1)
    c: DistanceX(g3,g7) = 10
    c: DistanceX(g-1,g23) = 10
    c: DistanceY(g7,g3) = 10
    c: DistanceX(g3,g-1) = 10
    c: DistanceY(g32,g7) = 10
    c: Coincident(g8,g7)
    c: Radius(g8) = 2.1
    c: Horizontal(g9)
    c: Vertical(g10)
    c: Vertical(g11)
    c: Coincident(g12,g15)
    c: Horizontal(g12)
    c: Coincident(g14,g13)
    c: Vertical(g14)
    c: Coincident(g15,g0)
    c: Coincident(g13,g34)
    c: Coincident(g14,g22)
    c: Coincident(g18,g16)
    c: Vertical(g18)
    c: Coincident(g19,g17)
    c: Horizontal(g19)
    c: Coincident(g9,g18)
    c: Coincident(g21,g19)
    c: Coincident(g24,g35)
    c: Horizontal(g24)
    c: Coincident(g26,g25)
    c: Vertical(g26)
    c: Coincident(g27,g37)
    c: Vertical(g27)
    c: Coincident(g28,g36)
    c: Horizontal(g28)
    c: Coincident(g11,g24)
    c: Coincident(g26,g30)
    c: Coincident(g31,g27)
    c: Coincident(g12,g10)
    c: Coincident(g28,g33)
    c: Coincident(g25,g1)
    c: Coincident(g35,g2)
    c: Coincident(g17,g2)
    c: Coincident(g16,g34)
    c: Coincident(g1,g37)
    c: Coincident(g0,g36)
    c: Coincident(g39,g5)
    c: Coincident(g40,g3)
    c: Coincident(g42,g4)
    c: Coincident(g44,g6)
    c: Coincident(g21,g45)
    c: Coincident(g33,g43)
    c: Coincident(g10,g42)
FEATURE [PartDesign::Pad] Pad012
  Direction = (0,0,1)
  Length = 300
  Length2 = 10
  Profile = -> Sketch012
  Type = 0
FEATURE [PartDesign::Fillet] Fillet132
  Base = -> Pad012 [Edge53]
  BaseFeature = -> Pad012
  Radius = 1
  SupportTransform = false
FEATURE [PartDesign::Fillet] Fillet133
  Base = -> Fillet132 [Edge114]
  BaseFeature = -> Fillet132
  Radius = 1
  SupportTransform = false
FEATURE [PartDesign::Fillet] Fillet134
  Base = -> Fillet133 [Edge137,Edge95]
  BaseFeature = -> Fillet133
  Radius = 0.5
  SupportTransform = false
FEATURE [PartDesign::Fillet] Fillet135
  Base = -> Fillet134 [Edge103]
  BaseFeature = -> Fillet134
  Radius = 0.5
  SupportTransform = false
FEATURE [PartDesign::Fillet] Fillet136
  Base = -> Fillet135 [Edge96]
  BaseFeature = -> Fillet135
  Radius = 0.5
  SupportTransform = false
FEATURE [PartDesign::Fillet] Fillet137
  Base = -> Fillet136 [Edge77]
  BaseFeature = -> Fillet136
  Radius = 0.5
  SupportTransform = false
FEATURE [PartDesign::Fillet] Fillet138
  Base = -> Fillet137 [Edge102]
  BaseFeature = -> Fillet137
  Radius = 0.5
  SupportTransform = false
FEATURE [PartDesign::Fillet] Fillet139
  Base = -> Fillet138 [Edge85]
  BaseFeature = -> Fillet138
  Radius = 0.5
  SupportTransform = false
FEATURE [PartDesign::Fillet] Fillet140
  Base = -> Fillet139 [Edge78]
  BaseFeature = -> Fillet139
  Radius = 0.5
  SupportTransform = false
FEATURE [PartDesign::Fillet] Fillet141
  Base = -> Fillet140 [Edge107]
  BaseFeature = -> Fillet140
  Radius = 0.5
  SupportTransform = false
FEATURE [PartDesign::Fillet] Fillet142
  Base = -> Fillet141 [Edge74]
  BaseFeature = -> Fillet141
  Radius = 0.5
  SupportTransform = false
FEATURE [PartDesign::Body] Body012
  Group = -> [Sketch012,Pad012,Fillet132,Fillet133,Fillet134,Fillet135,Fillet136,Fillet137,Fillet138,Fillet139,Fillet140,Fillet141,Fillet142]
  Origin = -> Origin025
  Placement = pos=(0,0,0) rot=(0,1,0;1.5708rad)
  Tip = -> Fillet142
FEATURE [App::Part] Part012  label="2020-300-013"
  Group = -> [Body012]
  Origin = -> Origin024
  Placement = pos=(10,20,80) rot=(0,0,1;1.5708rad)
FEATURE [Sketcher::SketchObject] Sketch013
  FullyConstrained = false
  MapMode = 5
  Support = -> [XY_Plane027]
  sketch-geometry (46):
    g0: LineSegment StartX=3.4 StartY=2.65 StartZ=0 EndX=3.4 EndY=-2.6657 EndZ=0
    g1: LineSegment StartX=2.63162 StartY=-3.4 StartZ=0 EndX=-2.65 EndY=-3.4 EndZ=0
    g2: LineSegment StartX=-3.4 StartY=-2.63136 StartZ=0 EndX=-3.4 EndY=2.61487 EndZ=0
    g3: LineSegment StartX=-10 StartY=10 StartZ=0 EndX=-3.125 EndY=10 EndZ=0
    g4: LineSegment StartX=10 StartY=10 StartZ=0 EndX=10 EndY=3.125 EndZ=0
    g5: LineSegment StartX=10 StartY=-10 StartZ=0 EndX=3.125 EndY=-10 EndZ=0
    g6: LineSegment StartX=-10 StartY=-10 StartZ=0 EndX=-10 EndY=-3.125 EndZ=0
    g7: GeomPoint X=3e-16 Y=0 Z=0
    g8: Circle CenterX=3e-16 CenterY=0 CenterZ=0 NormalX=0 NormalY=0 NormalZ=1 AngleXU=0 Radius=2.1
    g9: LineSegment StartX=-4.76483 StartY=8.08721 StartZ=0 EndX=-3.55 EndY=8.08721 EndZ=0
    g10: LineSegment StartX=8.24722 StartY=4.75 StartZ=0 EndX=8.24722 EndY=3.55 EndZ=0
    g11: LineSegment StartX=-8.2 StartY=-4.73729 StartZ=0 EndX=-8.2 EndY=-3.55 EndZ=0
    g12: LineSegment StartX=5.5 StartY=4.75 StartZ=0 EndX=8.24722 EndY=4.75 EndZ=0
    g13: LineSegment StartX=4.75 StartY=5.50457 StartZ=0 EndX=2.65 EndY=3.4 EndZ=0
    g14: LineSegment StartX=4.75 StartY=5.50457 StartZ=0 EndX=4.75 EndY=8.08721 EndZ=0
    g15: LineSegment StartX=3.4 StartY=2.65 StartZ=0 EndX=5.5 EndY=4.75 EndZ=0
    g16: LineSegment StartX=-4.76483 StartY=5.50457 StartZ=0 EndX=-2.66166 EndY=3.4 EndZ=0
    g17: LineSegment StartX=-5.5 StartY=4.70904 StartZ=0 EndX=-3.4 EndY=2.61487 EndZ=0
    g18: LineSegment StartX=-4.76483 StartY=5.50457 StartZ=0 EndX=-4.76483 EndY=8.08721 EndZ=0
    g19: LineSegment StartX=-5.5 StartY=4.70904 StartZ=0 EndX=-8.2 EndY=4.70904 EndZ=0
    g20: LineSegment StartX=-10 StartY=3.125 StartZ=0 EndX=-10 EndY=10 EndZ=0
    g21: LineSegment StartX=-8.2 StartY=3.55 StartZ=0 EndX=-8.2 EndY=4.70904 EndZ=0
    g22: LineSegment StartX=3.55 StartY=8.08721 StartZ=0 EndX=4.75 EndY=8.08721 EndZ=0
    g23: LineSegment StartX=3.125 StartY=10 StartZ=0 EndX=10 EndY=10 EndZ=0
    g24: LineSegment StartX=-5.5 StartY=-4.73729 StartZ=0 EndX=-8.2 EndY=-4.73729 EndZ=0
    g25: LineSegment StartX=-4.75 StartY=-5.5 StartZ=0 EndX=-2.65 EndY=-3.4 EndZ=0
    g26: LineSegment StartX=-4.75 StartY=-5.5 StartZ=0 EndX=-4.75 EndY=-8.2 EndZ=0
    g27: LineSegment StartX=4.73747 StartY=-5.5 StartZ=0 EndX=4.73747 EndY=-8.2 EndZ=0
    g28: LineSegment StartX=5.5 StartY=-4.7671 StartZ=0 EndX=8.24722 EndY=-4.7671 EndZ=0
    g29: LineSegment StartX=-3.125 StartY=-10 StartZ=0 EndX=-10 EndY=-10 EndZ=0
    g30: LineSegment StartX=-3.55 StartY=-8.2 StartZ=0 EndX=-4.75 EndY=-8.2 EndZ=0
    g31: LineSegment StartX=4.73747 StartY=-8.2 StartZ=0 EndX=3.55 EndY=-8.2 EndZ=0
    g32: LineSegment StartX=10 StartY=-3.125 StartZ=0 EndX=10 EndY=-10 EndZ=0
    g33: LineSegment StartX=8.24722 StartY=-3.55 StartZ=0 EndX=8.24722 EndY=-4.7671 EndZ=0
    g34: LineSegment StartX=-2.66166 StartY=3.4 StartZ=0 EndX=2.65 EndY=3.4 EndZ=0
    g35: LineSegment StartX=-3.4 StartY=-2.63136 StartZ=0 EndX=-5.5 EndY=-4.73729 EndZ=0
    g36: LineSegment StartX=3.4 StartY=-2.6657 StartZ=0 EndX=5.5 EndY=-4.7671 EndZ=0
    g37: LineSegment StartX=2.63162 StartY=-3.4 StartZ=0 EndX=4.73747 EndY=-5.5 EndZ=0
    g38: LineSegment StartX=-3.55 StartY=-8.2 StartZ=0 EndX=-3.125 EndY=-10 EndZ=0
    g39: LineSegment StartX=3.55 StartY=-8.2 StartZ=0 EndX=3.125 EndY=-10 EndZ=0
    g40: LineSegment StartX=-3.125 StartY=10 StartZ=0 EndX=-3.55 EndY=8.08721 EndZ=0
    g41: LineSegment StartX=3.125 StartY=10 StartZ=0 EndX=3.55 EndY=8.08721 EndZ=0
    g42: LineSegment StartX=8.24722 StartY=3.55 StartZ=0 EndX=10 EndY=3.125 EndZ=0
    g43: LineSegment StartX=10 StartY=-3.125 StartZ=0 EndX=8.24722 EndY=-3.55 EndZ=0
    g44: LineSegment StartX=-10 StartY=-3.125 StartZ=0 EndX=-8.2 EndY=-3.55 EndZ=0
    g45: LineSegment StartX=-10 StartY=3.125 StartZ=0 EndX=-8.2 EndY=3.55 EndZ=0
  constraints (61):
    c: Horizontal(g1)
    c: Vertical(g0)
    c: Vertical(g2)
    c: Coincident(g23,g4)
    c: Coincident(g32,g5)
    c: Coincident(g29,g6)
    c: Coincident(g20,g3)
    c: Horizontal(g3)
    c: Horizontal(g5)
    c: Vertical(g4)
    c: Vertical(g6)
    c: PointOnObject(g7,g-1)
    c: DistanceX(g3,g7) = 10
    c: DistanceX(g-1,g23) = 10
    c: DistanceY(g7,g3) = 10
    c: DistanceX(g3,g-1) = 10
    c: DistanceY(g32,g7) = 10
    c: Coincident(g8,g7)
    c: Radius(g8) = 2.1
    c: Horizontal(g9)
    c: Vertical(g10)
    c: Vertical(g11)
    c: Coincident(g12,g15)
    c: Horizontal(g12)
    c: Coincident(g14,g13)
    c: Vertical(g14)
    c: Coincident(g15,g0)
    c: Coincident(g13,g34)
    c: Coincident(g14,g22)
    c: Coincident(g18,g16)
    c: Vertical(g18)
    c: Coincident(g19,g17)
    c: Horizontal(g19)
    c: Coincident(g9,g18)
    c: Coincident(g21,g19)
    c: Coincident(g24,g35)
    c: Horizontal(g24)
    c: Coincident(g26,g25)
    c: Vertical(g26)
    c: Coincident(g27,g37)
    c: Vertical(g27)
    c: Coincident(g28,g36)
    c: Horizontal(g28)
    c: Coincident(g11,g24)
    c: Coincident(g26,g30)
    c: Coincident(g31,g27)
    c: Coincident(g12,g10)
    c: Coincident(g28,g33)
    c: Coincident(g25,g1)
    c: Coincident(g35,g2)
    c: Coincident(g17,g2)
    c: Coincident(g16,g34)
    c: Coincident(g1,g37)
    c: Coincident(g0,g36)
    c: Coincident(g39,g5)
    c: Coincident(g40,g3)
    c: Coincident(g42,g4)
    c: Coincident(g44,g6)
    c: Coincident(g21,g45)
    c: Coincident(g33,g43)
    c: Coincident(g10,g42)
FEATURE [PartDesign::Pad] Pad013
  Direction = (0,0,1)
  Length = 300
  Length2 = 10
  Profile = -> Sketch013
  Type = 0
FEATURE [PartDesign::Fillet] Fillet143
  Base = -> Pad013 [Edge53]
  BaseFeature = -> Pad013
  Radius = 1
  SupportTransform = false
FEATURE [PartDesign::Fillet] Fillet144
  Base = -> Fillet143 [Edge114]
  BaseFeature = -> Fillet143
  Radius = 1
  SupportTransform = false
FEATURE [PartDesign::Fillet] Fillet145
  Base = -> Fillet144 [Edge137,Edge95]
  BaseFeature = -> Fillet144
  Radius = 0.5
  SupportTransform = false
FEATURE [PartDesign::Fillet] Fillet146
  Base = -> Fillet145 [Edge103]
  BaseFeature = -> Fillet145
  Radius = 0.5
  SupportTransform = false
FEATURE [PartDesign::Fillet] Fillet147
  Base = -> Fillet146 [Edge96]
  BaseFeature = -> Fillet146
  Radius = 0.5
  SupportTransform = false
FEATURE [PartDesign::Fillet] Fillet148
  Base = -> Fillet147 [Edge77]
  BaseFeature = -> Fillet147
  Radius = 0.5
  SupportTransform = false
FEATURE [PartDesign::Fillet] Fillet149
  Base = -> Fillet148 [Edge102]
  BaseFeature = -> Fillet148
  Radius = 0.5
  SupportTransform = false
FEATURE [PartDesign::Fillet] Fillet150
  Base = -> Fillet149 [Edge85]
  BaseFeature = -> Fillet149
  Radius = 0.5
  SupportTransform = false
FEATURE [PartDesign::Fillet] Fillet151
  Base = -> Fillet150 [Edge78]
  BaseFeature = -> Fillet150
  Radius = 0.5
  SupportTransform = false
FEATURE [PartDesign::Fillet] Fillet152
  Base = -> Fillet151 [Edge107]
  BaseFeature = -> Fillet151
  Radius = 0.5
  SupportTransform = false
FEATURE [PartDesign::Fillet] Fillet153
  Base = -> Fillet152 [Edge74]
  BaseFeature = -> Fillet152
  Radius = 0.5
  SupportTransform = false
FEATURE [PartDesign::Body] Body013
  Group = -> [Sketch013,Pad013,Fillet143,Fillet144,Fillet145,Fillet146,Fillet147,Fillet148,Fillet149,Fillet150,Fillet151,Fillet152,Fillet153]
  Origin = -> Origin027
  Placement = pos=(0,0,0) rot=(0,1,0;1.5708rad)
  Tip = -> Fillet153
FEATURE [App::Part] Part013  label="2020-300-014"
  Group = -> [Body013]
  Origin = -> Origin026
  Placement = pos=(330,20,80) rot=(0,0,1;1.5708rad)
FEATURE [Sketcher::SketchObject] Sketch014
  FullyConstrained = true
  MapMode = 5
  Placement = pos=(0,0,0) rot=(-0.57735,0.57735,0.57735;4.18879rad)
  Support = -> [YZ_Plane036]
  sketch-geometry (1):
    g0: Circle CenterX=0 CenterY=-7.5 CenterZ=0 NormalX=0 NormalY=0 NormalZ=1 AngleXU=0 Radius=0.25
  constraints (3):
    c: PointOnObject(g0,g-2)
    c: DistanceY(g0) = -7.5
    c: Diameter(g0) = 0.5
FEATURE [Sketcher::SketchObject] Sketch015
  FullyConstrained = true
  MapMode = 5
  Support = -> [XY_Plane029]
  sketch-geometry (2):
    g0: LineSegment StartX=0 StartY=5.5 StartZ=0 EndX=6e-16 EndY=9.5 EndZ=0
    g1: ArcOfCircle CenterX=0 CenterY=7.5 CenterZ=0 NormalX=0 NormalY=0 NormalZ=1 AngleXU=0 Radius=2 StartAngle=4.71239 EndAngle=7.85398
  constraints (7):
    c: PointOnObject(g0,g-2)
    c: PointOnObject(g0,g-2)
    c: PointOnObject(g1,g0)
    c: Coincident(g1,g0)
    c: Coincident(g1,g0)
    c: Radius(g1) = 2
    c: DistanceY(g1) = 7.5
FEATURE [PartDesign::Revolution] Revolution
  Angle = 360
  Axis = (0,1,0)
  Base = (0,0,0)
  Profile = -> Sketch015
  ReferenceAxis = -> Sketch015 [V_Axis]
  Reversed = true
FEATURE [PartDesign::Body] Body015  label="Ball 001"
  Group = -> [Sketch015,Revolution]
  Origin = -> Origin029
  Tip = -> Revolution
FEATURE [PartDesign::FeatureBase] Clone
  BaseFeature = -> Body015
FEATURE [PartDesign::Body] Body016  label="Ball 002"
  BaseFeature = -> Body015
  Group = -> [Clone]
  Origin = -> Origin030
  Placement = pos=(0,0,0) rot=(-1,0,0;0.897598rad)
  Tip = -> Clone
FEATURE [PartDesign::FeatureBase] Clone001
  BaseFeature = -> Body015
FEATURE [PartDesign::Body] Body017  label="Ball 003"
  BaseFeature = -> Body015
  Group = -> [Clone001]
  Origin = -> Origin031
  Placement = pos=(0,0,0) rot=(-1,0,0;1.7952rad)
  Tip = -> Clone001
FEATURE [PartDesign::FeatureBase] Clone002
  BaseFeature = -> Body015
FEATURE [PartDesign::Body] Body018  label="Ball 004"
  BaseFeature = -> Body015
  Group = -> [Clone002]
  Origin = -> Origin032
  Placement = pos=(0,0,0) rot=(1,0,0;3.59039rad)
  Tip = -> Clone002
FEATURE [PartDesign::FeatureBase] Clone003
  BaseFeature = -> Body015
FEATURE [PartDesign::Body] Body019  label="Ball 005"
  BaseFeature = -> Body015
  Group = -> [Clone003]
  Origin = -> Origin033
  Placement = pos=(0,0,0) rot=(1,0,0;2.69279rad)
  Tip = -> Clone003
FEATURE [PartDesign::FeatureBase] Clone004
  BaseFeature = -> Body015
FEATURE [PartDesign::Body] Body020  label="Ball 006"
  BaseFeature = -> Body015
  Group = -> [Clone004]
  Origin = -> Origin034
  Placement = pos=(0,0,0) rot=(1,0,0;1.7952rad)
  Tip = -> Clone004
FEATURE [PartDesign::FeatureBase] Clone005
  BaseFeature = -> Body015
FEATURE [PartDesign::Body] Body021  label="Ball 007"
  BaseFeature = -> Body015
  Group = -> [Clone005]
  Origin = -> Origin035
  Placement = pos=(0,0,0) rot=(1,0,0;0.897598rad)
  Tip = -> Clone005
FEATURE [App::DocumentObjectGroup] Group  label="Balls"
  Group = -> [Body015,Body016,Body017,Body018,Body019,Body020,Body021]
FEATURE [Sketcher::SketchObject] Sketch019
  FullyConstrained = true
  MapMode = 5
  Support = -> [XY_Plane038]
  sketch-geometry (7):
    g0: LineSegment StartX=-5 StartY=7.5 StartZ=0 EndX=5 EndY=7.5 EndZ=0
    g1: LineSegment StartX=-0.210977 StartY=7.5 StartZ=0 EndX=0.210977 EndY=7.5 EndZ=0
    g2: ArcOfCircle CenterX=0.25 CenterY=7.5 CenterZ=0 NormalX=0 NormalY=0 NormalZ=1 AngleXU=0 Radius=0.460977 StartAngle=2.43297 EndAngle=3.14159
    g3: ArcOfCircle CenterX=-0.25 CenterY=7.5 CenterZ=0 NormalX=0 NormalY=0 NormalZ=1 AngleXU=0 Radius=0.460977 StartAngle=9.792e-13 EndAngle=0.708626
    g4: LineSegment StartX=-0.1 StartY=7.8 StartZ=0 EndX=-0.1 EndY=7.75 EndZ=0
    g5: LineSegment StartX=-0.1 StartY=7.75 StartZ=0 EndX=0.1 EndY=7.75 EndZ=0
    g6: LineSegment StartX=0.1 StartY=7.75 StartZ=0 EndX=0.1 EndY=7.8 EndZ=0
  constraints (22):
    c: DistanceY(g-1,g0) = 7.5
    c: Symmetric(g0,g0,g-2)
    c: DistanceX(g0,g0) = 10
    c: PointOnObject(g1,g0)
    c: PointOnObject(g1,g0)
    c: Coincident(g3,g1)
    c: Coincident(g2,g1)
    c: Coincident(g2,g4)
    c: Coincident(g4,g5)
    c: Horizontal(g5)
    c: Coincident(g5,g6)
    c: Coincident(g6,g3)
    c: Vertical(g6)
    c: Equal(g3,g2)
    c: Vertical(g4)
    c: Symmetric(g2,g3,g-2)
    c: DistanceX(g5,g5) = 0.2
    c: Distance(g5,g1) = 0.25
    c: DistanceX(g3,g-1) = 0.25
    c: PointOnObject(g3,g1)
    c: PointOnObject(g2,g1)
    c: Distance(g3,g1) = 0.3
FEATURE [PartDesign::Revolution] Revolution005
  Angle = 360
  Axis = (10,0,0)
  Base = (-5,7.5,0)
  Profile = -> Sketch019
  ReferenceAxis = -> Sketch019 [Axis]
FEATURE [PartDesign::Body] Body024  label="Rivet 001"
  Group = -> [Sketch019,Revolution005]
  Origin = -> Origin038
  Placement = pos=(0,0,0) rot=(1,0,0;0.448799rad)
  Tip = -> Revolution005
FEATURE [PartDesign::FeatureBase] Clone007
  BaseFeature = -> Body024
  Placement = pos=(0,0,0) rot=(1,0,0;0.448799rad)
FEATURE [PartDesign::Body] Body025  label="Rivet 002"
  BaseFeature = -> Body024
  Group = -> [Clone007]
  Origin = -> Origin039
  Placement = pos=(0,0,0) rot=(1,0,0;0.897598rad)
  Tip = -> Clone007
FEATURE [PartDesign::FeatureBase] Clone008
  BaseFeature = -> Body024
  Placement = pos=(0,0,0) rot=(1,0,0;0.448799rad)
FEATURE [PartDesign::Body] Body026  label="Rivet 003"
  BaseFeature = -> Body024
  Group = -> [Clone008]
  Origin = -> Origin040
  Placement = pos=(0,0,0) rot=(1,0,0;1.7952rad)
  Tip = -> Clone008
FEATURE [PartDesign::FeatureBase] Clone009
  BaseFeature = -> Body024
  Placement = pos=(0,0,0) rot=(1,0,0;0.448799rad)
FEATURE [PartDesign::Body] Body027  label="Rivet 004"
  BaseFeature = -> Body024
  Group = -> [Clone009]
  Origin = -> Origin041
  Placement = pos=(0,0,0) rot=(1,0,0;2.69279rad)
  Tip = -> Clone009
FEATURE [PartDesign::FeatureBase] Clone010
  BaseFeature = -> Body024
  Placement = pos=(0,0,0) rot=(1,0,0;0.448799rad)
FEATURE [PartDesign::Body] Body028  label="Rivet 005"
  BaseFeature = -> Body024
  Group = -> [Clone010]
  Origin = -> Origin042
  Placement = pos=(0,0,0) rot=(1,0,0;3.59039rad)
  Tip = -> Clone010
FEATURE [PartDesign::FeatureBase] Clone011
  BaseFeature = -> Body024
  Placement = pos=(0,0,0) rot=(1,0,0;0.448799rad)
FEATURE [PartDesign::Body] Body029  label="Rivet 006"
  BaseFeature = -> Body024
  Group = -> [Clone011]
  Origin = -> Origin043
  Placement = pos=(0,0,0) rot=(-1,0,0;1.7952rad)
  Tip = -> Clone011
FEATURE [PartDesign::FeatureBase] Clone012
  BaseFeature = -> Body024
  Placement = pos=(0,0,0) rot=(1,0,0;0.448799rad)
FEATURE [PartDesign::Body] Body030  label="Rivet 007"
  BaseFeature = -> Body024
  Group = -> [Clone012]
  Origin = -> Origin044
  Placement = pos=(0,0,0) rot=(-1,0,0;0.897598rad)
  Tip = -> Clone012
FEATURE [App::DocumentObjectGroup] Group002  label="Rivets"
  Group = -> [Body024,Body025,Body026,Body027,Body028,Body029,Body030]
FEATURE [Sketcher::SketchObject] Sketch023
  FullyConstrained = true
  MapMode = 5
  Placement = pos=(0,0,0) rot=(1,0,0;1.5708rad)
  Support = -> [XZ_Plane036]
  sketch-geometry (4):
    g0: LineSegment StartX=0 StartY=8.5 StartZ=0 EndX=0.1 EndY=8.5 EndZ=0
    g1: LineSegment StartX=0.1 StartY=8.5 StartZ=0 EndX=0.1 EndY=6.5 EndZ=0
    g2: LineSegment StartX=0.1 StartY=6.5 StartZ=0 EndX=0 EndY=6.5 EndZ=0
    g3: LineSegment StartX=0 StartY=6.5 StartZ=0 EndX=0 EndY=8.5 EndZ=0
  constraints (12):
    c: Coincident(g0,g1)
    c: Coincident(g1,g2)
    c: Coincident(g2,g3)
    c: Coincident(g3,g0)
    c: Horizontal(g0)
    c: Horizontal(g2)
    c: Vertical(g1)
    c: Vertical(g3)
    c: PointOnObject(g0,g-2)
    c: DistanceX(g0,g0) = 0.1
    c: DistanceY(g0) = 8.5
    c: DistanceY(g1) = 6.5
FEATURE [PartDesign::Revolution] Revolution006
  Angle = 360
  Axis = (1,0,0)
  Base = (0,0,0)
  Placement = pos=(0,0,0) rot=(1,0,0;1.5708rad)
  Profile = -> Sketch023
  ReferenceAxis = -> Sketch023 [H_Axis]
FEATURE [Sketcher::SketchObject] Sketch025
  FullyConstrained = true
  MapMode = 5
  Placement = pos=(0,0,0) rot=(0.57735,0.57735,0.57735;2.0944rad)
  Support = -> [YZ_Plane036]
  sketch-geometry (5):
    g0: ArcOfCircle CenterX=0 CenterY=7.5 CenterZ=0 NormalX=0 NormalY=0 NormalZ=1 AngleXU=0 Radius=2.11 StartAngle=5.66076 EndAngle=6.65667
    g1: LineSegment StartX=5e-16 StartY=8.5 StartZ=0 EndX=0 EndY=6.26986 EndZ=0
    g2: ArcOfCircle CenterX=0 CenterY=0 CenterZ=0 NormalX=0 NormalY=0 NormalZ=1 AngleXU=0 Radius=6.5 StartAngle=1.3039 EndAngle=1.5708
    g3: LineSegment StartX=1.71431 StartY=6.26986 StartZ=0 EndX=0 EndY=6.26986 EndZ=0
    g4: ArcOfCircle CenterX=0 CenterY=0 CenterZ=0 NormalX=0 NormalY=0 NormalZ=1 AngleXU=0 Radius=8.5 StartAngle=1.33757 EndAngle=1.5708
  constraints (16):
    c: PointOnObject(g0,g-2)
    c: DistanceY(g0) = 7.5
    c: Radius(g0) = 2.11
    c: PointOnObject(g2,g1)
    c: DistanceY(g2) = 6.5
    c: Coincident(g2,g-1)
    c: Coincident(g3,g2)
    c: Horizontal(g3)
    c: Coincident(g0,g2)
    c: Coincident(g1,g3)
    c: PointOnObject(g1,g-2)
    c: PointOnObject(g1,g-2)
    c: Coincident(g4,g-1)
    c: Coincident(g4,g1)
    c: DistanceY(g1) = 8.5
    c: Coincident(g0,g4)
FEATURE [PartDesign::Revolution] Revolution007
  Angle = 180
  Axis = (-2e-16,3e-16,1)
  Base = (0,0,0)
  BaseFeature = -> Revolution006
  Placement = pos=(0,0,0) rot=(1,0,0;1.5708rad)
  Profile = -> Sketch025
  ReferenceAxis = -> Sketch025 [V_Axis]
  Reversed = true
FEATURE [PartDesign::PolarPattern] PolarPattern
  Angle = 360
  Axis = -> Sketch025 [N_Axis]
  BaseFeature = -> Revolution007
  Occurrences = 3
  Originals = -> [Revolution007]
  Placement = pos=(0,0,0) rot=(1,0,0;1.5708rad)
  Refine = true
FEATURE [Sketcher::SketchObject] Sketch026
  FullyConstrained = true
  MapMode = 5
  Placement = pos=(0,0,0) rot=(0.57735,0.57735,0.57735;2.0944rad)
  Support = -> [YZ_Plane036]
  sketch-geometry (4):
    g0: ArcOfCircle CenterX=0 CenterY=7.5 CenterZ=0 NormalX=0 NormalY=0 NormalZ=1 AngleXU=0 Radius=2.01 StartAngle=5.57985 EndAngle=6.86228
    g1: LineSegment StartX=0 StartY=6.2 StartZ=0 EndX=1.533 EndY=6.2 EndZ=0
    g2: LineSegment StartX=0 StartY=8.6 StartZ=0 EndX=0 EndY=6.2 EndZ=0
    g3: LineSegment StartX=0 StartY=8.6 StartZ=0 EndX=1.68229 EndY=8.6 EndZ=0
  constraints (13):
    c: PointOnObject(g0,g-2)
    c: DistanceY(g0) = 7.5
    c: Radius(g0) = 2.01
    c: PointOnObject(g1,g-2)
    c: Horizontal(g1)
    c: Coincident(g0,g1)
    c: DistanceY(g1) = 6.2
    c: DistanceY(g2) = 8.6
    c: Coincident(g2,g1)
    c: PointOnObject(g2,g-2)
    c: Coincident(g3,g2)
    c: Horizontal(g3)
    c: Coincident(g0,g3)
FEATURE [PartDesign::Groove] Groove
  Angle = 360
  Axis = (-2e-16,3e-16,1)
  Base = (0,0,0)
  BaseFeature = -> PolarPattern
  Placement = pos=(0,0,0) rot=(1,0,0;1.5708rad)
  Profile = -> Sketch026
  ReferenceAxis = -> Sketch026 [V_Axis]
FEATURE [PartDesign::PolarPattern] PolarPattern001
  Angle = 360
  Axis = -> Sketch026 [N_Axis]
  BaseFeature = -> Groove
  Occurrences = 3
  Originals = -> [Groove]
  Placement = pos=(0,0,0) rot=(1,0,0;1.5708rad)
FEATURE [PartDesign::Pocket] Pocket
  BaseFeature = -> PolarPattern001
  Length = 5
  Length2 = 100
  Placement = pos=(0,0,0) rot=(1,0,0;1.5708rad)
  Profile = -> Sketch014
  Type = 1
FEATURE [PartDesign::PolarPattern] PolarPattern002
  Angle = 360
  Axis = -> Sketch014 [N_Axis]
  BaseFeature = -> Pocket
  Occurrences = 3
  Originals = -> [Pocket]
  Placement = pos=(0,0,0) rot=(1,0,0;1.5708rad)
FEATURE [PartDesign::Body] Body022  label="Cage 001"
  Group = -> [Sketch023,Revolution006,Sketch025,Revolution007,PolarPattern,Sketch026,Groove,PolarPattern001,Sketch014,Pocket,PolarPattern002]
  Origin = -> Origin036
  Placement = pos=(0,0,0) rot=(-1,0,0;1.5708rad)
  Tip = -> PolarPattern002
FEATURE [PartDesign::FeatureBase] Clone006
  BaseFeature = -> Body022
  Placement = pos=(0,0,0) rot=(-1,0,0;1.5708rad)
FEATURE [PartDesign::Body] Body023  label="Cage 002"
  BaseFeature = -> Body022
  Group = -> [Clone006]
  Origin = -> Origin037
  Placement = pos=(0,0,0) rot=(0,1,0;3.14159rad)
  Tip = -> Clone006
FEATURE [App::DocumentObjectGroup] Group001  label="Cages"
  Group = -> [Body022,Body023]
FEATURE [Sketcher::SketchObject] Sketch027
  FullyConstrained = true
  MapMode = 5
  Support = -> [XY_Plane045]
  sketch-geometry (14):
    g0: ArcOfCircle CenterX=-1e-16 CenterY=7.5 CenterZ=0 NormalX=0 NormalY=0 NormalZ=1 AngleXU=0 Radius=2 StartAngle=0.848062 EndAngle=2.29353
    g1: LineSegment StartX=-3.5 StartY=11 StartZ=0 EndX=3.5 EndY=11 EndZ=0
    g2: LineSegment StartX=3.5 StartY=11 StartZ=0 EndX=3.5 EndY=9.2 EndZ=0
    g3: LineSegment StartX=2.9 StartY=9 StartZ=0 EndX=1.32288 EndY=9 EndZ=0
    g4: LineSegment StartX=-3.5 StartY=9.2 StartZ=0 EndX=-3.5 EndY=11 EndZ=0
    g5: LineSegment StartX=-1.32288 StartY=9 StartZ=0 EndX=-2.9 EndY=9 EndZ=0
    g6: LineSegment StartX=2.9 StartY=9 StartZ=0 EndX=2.9 EndY=9.5 EndZ=0
    g7: LineSegment StartX=2.9 StartY=9.5 StartZ=0 EndX=3.2 EndY=9.5 EndZ=0
    g8: LineSegment StartX=3.2 StartY=9.5 StartZ=0 EndX=3.2 EndY=9.2 EndZ=0
    g9: LineSegment StartX=3.2 StartY=9.2 StartZ=0 EndX=3.5 EndY=9.2 EndZ=0
    g10: LineSegment StartX=-3.5 StartY=9.2 StartZ=0 EndX=-3.2 EndY=9.2 EndZ=0
    g11: LineSegment StartX=-3.2 StartY=9.2 StartZ=0 EndX=-3.2 EndY=9.5 EndZ=0
    g12: LineSegment StartX=-3.2 StartY=9.5 StartZ=0 EndX=-2.9 EndY=9.5 EndZ=0
    g13: LineSegment StartX=-2.9 StartY=9.5 StartZ=0 EndX=-2.9 EndY=9 EndZ=0
  constraints (41):
    c: Coincident(g1,g2)
    c: Coincident(g4,g1)
    c: Horizontal(g3)
    c: Vertical(g2)
    c: Vertical(g4)
    c: Coincident(g0,g5)
    c: Coincident(g0,g3)
    c: DistanceY(g-1,g0) = 7.5
    c: Radius(g0) = 2
    c: Symmetric(g1,g1,g-2)
    c: Symmetric(g0,g0,g-2)
    c: DistanceY(g1) = 11
    c: DistanceX(g1,g1) = 7
    c: Vertical(g6)
    c: Coincident(g6,g7)
    c: Horizontal(g7)
    c: Coincident(g7,g8)
    c: Vertical(g8)
    c: Coincident(g8,g9)
    c: Coincident(g3,g6)
    c: Coincident(g2,g9)
    c: Horizontal(g10)
    c: Coincident(g10,g11)
    c: Coincident(g11,g12)
    c: Horizontal(g12)
    c: Coincident(g12,g13)
    c: Vertical(g13)
    c: Vertical(g11)
    c: Coincident(g4,g10)
    c: Coincident(g5,g13)
    c: DistanceY(g13,g13) = 0.5
    c: DistanceX(g12,g12) = 0.3
    c: DistanceY(g5,g10) = 0.2
    c: Symmetric(g5,g3,g-2)
    c: DistanceY(g3) = 9
    c: DistanceY(g6) = 9.5
    c: Equal(g7,g12)
    c: Equal(g13,g6)
    c: Horizontal(g9)
    c: Horizontal(g8,g10)
    c: Equal(g12,g10)
FEATURE [PartDesign::Revolution] Revolution008
  Angle = 360
  Axis = (1,0,0)
  Base = (0,0,0)
  Profile = -> Sketch027
  ReferenceAxis = -> X_Axis045
FEATURE [PartDesign::Fillet] Fillet154
  Base = -> Revolution008 [Edge14,Edge15]
  BaseFeature = -> Revolution008
  Radius = 0.3
  SupportTransform = false
FEATURE [PartDesign::Body] Body031  label="Outer Ring001"
  Group = -> [Sketch027,Revolution008,Fillet154]
  Origin = -> Origin045
  Tip = -> Fillet154
FEATURE [Sketcher::SketchObject] Sketch028
  FullyConstrained = true
  MapMode = 5
  Support = -> [XY_Plane046]
  sketch-geometry (14):
    g0: LineSegment StartX=-2.9 StartY=6 StartZ=0 EndX=-1.32288 EndY=6 EndZ=0
    g1: LineSegment StartX=-3.5 StartY=4 StartZ=0 EndX=-3.5 EndY=5.7 EndZ=0
    g2: ArcOfCircle CenterX=-1e-16 CenterY=7.5 CenterZ=0 NormalX=0 NormalY=0 NormalZ=1 AngleXU=0 Radius=2 StartAngle=3.98965 EndAngle=5.43512
    g3: LineSegment StartX=1.32288 StartY=6 StartZ=0 EndX=2.9 EndY=6 EndZ=0
    g4: LineSegment StartX=-3.5 StartY=5.7 StartZ=0 EndX=-3.2 EndY=5.7 EndZ=0
    g5: LineSegment StartX=-3.2 StartY=5.7 StartZ=0 EndX=-3.2 EndY=5.5 EndZ=0
    g6: LineSegment StartX=-3.2 StartY=5.5 StartZ=0 EndX=-2.9 EndY=5.5 EndZ=0
    g7: LineSegment StartX=-2.9 StartY=5.5 StartZ=0 EndX=-2.9 EndY=6 EndZ=0
    g8: LineSegment StartX=8.5 StartY=6 StartZ=0 EndX=3.2 EndY=6 EndZ=0
    g9: LineSegment StartX=3.2 StartY=6 StartZ=0 EndX=3.2 EndY=5.5 EndZ=0
    g10: LineSegment StartX=3.2 StartY=5.5 StartZ=0 EndX=2.9 EndY=5.5 EndZ=0
    g11: LineSegment StartX=2.9 StartY=5.5 StartZ=0 EndX=2.9 EndY=6 EndZ=0
    g12: LineSegment StartX=8.5 StartY=4 StartZ=0 EndX=8.5 EndY=6 EndZ=0
    g13: LineSegment StartX=-3.5 StartY=4 StartZ=0 EndX=8.5 EndY=4 EndZ=0
  constraints (43):
    c: Horizontal(g0)
    c: Vertical(g1)
    c: DistanceY(g1) = 4
    c: Coincident(g2,g0)
    c: Coincident(g2,g3)
    c: Horizontal(g3)
    c: Radius(g2) = 2
    c: DistanceY(g2) = 7.5
    c: Symmetric(g0,g2,g-2)
    c: Horizontal(g4)
    c: Coincident(g4,g5)
    c: Vertical(g5)
    c: Coincident(g5,g6)
    c: Horizontal(g6)
    c: Coincident(g6,g7)
    c: Vertical(g7)
    c: Horizontal(g8)
    c: Coincident(g8,g9)
    c: Vertical(g9)
    c: Coincident(g9,g10)
    c: Horizontal(g10)
    c: Coincident(g10,g11)
    c: Vertical(g11)
    c: Coincident(g3,g11)
    c: Coincident(g0,g7)
    c: Coincident(g1,g4)
    c: DistanceY(g3) = 6
    c: DistanceY(g6,g0) = 0.5
    c: DistanceX(g4,g4) = 0.3
    c: DistanceX(g6,g6) = 0.3
    c: DistanceY(g5,g4) = 0.2
    c: Vertical(g12)
    c: Equal(g11,g7)
    c: DistanceY(g1,g0) = 2
    c: DistanceX(g8,g8) = 5.3
    c: Coincident(g13,g1)
    c: Coincident(g13,g12)
    c: Horizontal(g13)
    c: DistanceX(g13,g13) = 12
    c: DistanceX(g1,g2) = 3.5
    c: Coincident(g8,g12)
    c: Equal(g7,g9)
    c: Equal(g6,g10)
FEATURE [PartDesign::Revolution] Revolution009
  Angle = 360
  Axis = (1,0,0)
  Base = (0,0,0)
  Profile = -> Sketch028
  ReferenceAxis = -> X_Axis046
FEATURE [PartDesign::Fillet] Fillet155
  Base = -> Revolution009 [Edge13,Edge11]
  BaseFeature = -> Revolution009
  Radius = 0.2
  SupportTransform = false
FEATURE [PartDesign::Body] Body032  label="Inner Ring001"
  Group = -> [Sketch028,Revolution009,Fillet155]
  Origin = -> Origin046
  Tip = -> Fillet155
FEATURE [App::DocumentObjectGroup] Group004  label="Rings"
  Group = -> [Body031,Body032]
FEATURE [Sketcher::SketchObject] Sketch029
  FullyConstrained = true
  MapMode = 5
  Placement = pos=(0,0,0) rot=(1,0,0;1.5708rad)
  Support = -> [XZ_Plane047]
  sketch-geometry (12):
    g0: LineSegment StartX=2.9 StartY=9.5 StartZ=0 EndX=2.9 EndY=8.5 EndZ=0
    g1: LineSegment StartX=2.9 StartY=8.5 StartZ=0 EndX=3.2 EndY=8.5 EndZ=0
    g2: LineSegment StartX=3.2 StartY=8.5 StartZ=0 EndX=3.2 EndY=6.5 EndZ=0
    g3: LineSegment StartX=3.2 StartY=6.5 StartZ=0 EndX=2.9 EndY=6.5 EndZ=0
    g4: LineSegment StartX=2.9 StartY=6.5 StartZ=0 EndX=2.9 EndY=5.5 EndZ=0
    g5: LineSegment StartX=2.9 StartY=5.5 StartZ=0 EndX=3.2 EndY=5.5 EndZ=0
    g6: LineSegment StartX=3.2 StartY=5.5 StartZ=0 EndX=3.2 EndY=6 EndZ=0
    g7: LineSegment StartX=3.2 StartY=6 StartZ=0 EndX=3.5 EndY=6 EndZ=0
    g8: LineSegment StartX=3.5 StartY=6 StartZ=0 EndX=3.5 EndY=9 EndZ=0
    g9: LineSegment StartX=3.5 StartY=9 StartZ=0 EndX=3.2 EndY=9 EndZ=0
    g10: LineSegment StartX=3.2 StartY=9 StartZ=0 EndX=3.2 EndY=9.5 EndZ=0
    g11: LineSegment StartX=3.2 StartY=9.5 StartZ=0 EndX=2.9 EndY=9.5 EndZ=0
  constraints (36):
    c: Vertical(g0)
    c: Coincident(g0,g1)
    c: Horizontal(g1)
    c: Coincident(g1,g2)
    c: Vertical(g2)
    c: Coincident(g2,g3)
    c: Horizontal(g3)
    c: Coincident(g3,g4)
    c: Vertical(g4)
    c: Coincident(g4,g5)
    c: Horizontal(g5)
    c: Coincident(g5,g6)
    c: Vertical(g6)
    c: Coincident(g6,g7)
    c: Horizontal(g7)
    c: Coincident(g7,g8)
    c: Vertical(g8)
    c: Coincident(g8,g9)
    c: Horizontal(g9)
    c: Coincident(g9,g10)
    c: Vertical(g10)
    c: Coincident(g10,g11)
    c: Coincident(g11,g0)
    c: Horizontal(g11)
    c: DistanceY(g4) = 5.5
    c: DistanceX(g4) = 2.9
    c: DistanceY(g5,g6) = 0.5
    c: DistanceY(g6,g2) = 0.5
    c: DistanceX(g5,g5) = 0.3
    c: Equal(g5,g7)
    c: Equal(g7,g3)
    c: Equal(g3,g1)
    c: Equal(g1,g9)
    c: Equal(g4,g0)
    c: Equal(g6,g10)
    c: DistanceY(g4,g0) = 4
FEATURE [PartDesign::Revolution] Revolution010
  Angle = 360
  Axis = (1,0,0)
  Base = (0,0,0)
  Placement = pos=(0,0,0) rot=(1,0,0;1.5708rad)
  Profile = -> Sketch029
  ReferenceAxis = -> Sketch029 [H_Axis]
FEATURE [PartDesign::Fillet] Fillet156
  Base = -> Revolution010 [Edge14,Edge12]
  BaseFeature = -> Revolution010
  Placement = pos=(0,0,0) rot=(1,0,0;1.5708rad)
  Radius = 0.2
  SupportTransform = false
FEATURE [PartDesign::Body] Body033  label="Seal 001"
  Group = -> [Sketch029,Revolution010,Fillet156]
  Origin = -> Origin047
  Tip = -> Fillet156
FEATURE [PartDesign::FeatureBase] Clone013
  BaseFeature = -> Body033
FEATURE [PartDesign::Body] Body034  label="Seal 002"
  BaseFeature = -> Body033
  Group = -> [Clone013]
  Origin = -> Origin048
  Placement = pos=(0,0,0) rot=(0,1,0;3.14159rad)
  Tip = -> Clone013
FEATURE [App::DocumentObjectGroup] Group003  label="Seals"
  Group = -> [Body033,Body034]
FEATURE [Sketcher::SketchObject] Sketch030
  AttachmentOffset = pos=(0,0,4) rot=(0,0,1;0rad)
  FullyConstrained = true
  MapMode = 5
  Placement = pos=(0,0,4) rot=(0,0,1;0rad)
  Support = -> [XY_Plane028]
  sketch-geometry (1):
    g0: Circle CenterX=6 CenterY=0 CenterZ=0 NormalX=0 NormalY=0 NormalZ=1 AngleXU=0 Radius=1.5
  constraints (3):
    c: PointOnObject(g0,g-1)
    c: Diameter(g0) = 3
    c: DistanceX(g-1,g0) = 6
FEATURE [PartDesign::Pad] Pad014
  Direction = (0,0,1)
  Length = 3
  Length2 = 100
  Profile = -> Sketch030
  Type = 0
FEATURE [Sketcher::SketchObject] Sketch031
  ExternalGeometry = -> [Pad014]
  FullyConstrained = true
  MapMode = 5
  Placement = pos=(0,0,7) rot=(0,0,1;0rad)
  Support = -> [Pad014]
  sketch-geometry (7):
    g0: LineSegment StartX=6.43301 StartY=-0.75 StartZ=0 EndX=6.86603 EndY=0 EndZ=0
    g1: LineSegment StartX=6.86603 StartY=0 StartZ=0 EndX=6.43301 EndY=0.75 EndZ=0
    g2: LineSegment StartX=6.43301 StartY=0.75 StartZ=0 EndX=5.56699 EndY=0.75 EndZ=0
    g3: LineSegment StartX=5.56699 StartY=0.75 StartZ=0 EndX=5.13397 EndY=-1e-16 EndZ=0
    g4: LineSegment StartX=5.13397 StartY=-1e-16 StartZ=0 EndX=5.56699 EndY=-0.75 EndZ=0
    g5: LineSegment StartX=5.56699 StartY=-0.75 StartZ=0 EndX=6.43301 EndY=-0.75 EndZ=0
    g6: Circle CenterX=6 CenterY=0 CenterZ=0 NormalX=0 NormalY=0 NormalZ=1 AngleXU=0 Radius=0.866025
  constraints (16):
    c: Coincident(g0,g1)
    c: Coincident(g1,g2)
    c: Coincident(g2,g3)
    c: Coincident(g3,g4)
    c: Coincident(g4,g5)
    c: Coincident(g5,g0)
    c: Equal(g0, g1-g5) x5
    c: PointOnObject(g0,g6)
    c: PointOnObject(g1,g6)
    c: PointOnObject(g2,g6)
    c: PointOnObject(g3,g6)
    c: PointOnObject(g4,g6)
    c: PointOnObject(g5,g6)
    c: Coincident(g6,g-3)
    c: Horizontal(g5)
    c: DistanceY(g4,g2) = 1.5
FEATURE [PartDesign::Pocket] Pocket001
  BaseFeature = -> Pad014
  Length = 0.9
  Length2 = 100
  Profile = -> Sketch031
  Type = 0
FEATURE [PartDesign::PolarPattern] PolarPattern003
  Angle = 120
  Axis = -> X_Axis028
  BaseFeature = -> Pocket001
  Occurrences = 3
  Originals = -> [Pad014,Pocket001]
FEATURE [PartDesign::Body] Body014
  Group = -> [Sketch030,Pad014,Sketch031,Pocket001,PolarPattern003]
  Origin = -> Origin028
  Tip = -> PolarPattern003
FEATURE [App::DocumentObjectGroup] Group005  label="Set screws"
  Group = -> [Body014]
FEATURE [Sketcher::SketchObject] Sketch032
  AttachmentOffset = pos=(0,0,-6.5) rot=(0,0,1;0rad)
  FullyConstrained = true
  MapMode = 5
  Placement = pos=(-6.5,1.4e-15,-1.4e-15) rot=(0.57735,0.57735,0.57735;2.0944rad)
  Support = -> [YZ_Plane049]
  sketch-geometry (14):
    g0: Circle CenterX=0 CenterY=0 CenterZ=0 NormalX=0 NormalY=0 NormalZ=1 AngleXU=0 Radius=11
    g1: ArcOfCircle CenterX=0 CenterY=0 CenterZ=0 NormalX=0 NormalY=0 NormalZ=1 AngleXU=0 Radius=13.5 StartAngle=0.0668757 EndAngle=3.07472
    g2: LineSegment StartX=-13.4698 StartY=0.902148 StartZ=0 EndX=-14.2 EndY=-10 EndZ=0
    g3: LineSegment StartX=-14.2 StartY=-10 StartZ=0 EndX=-27.5 EndY=-10 EndZ=0
    g4: LineSegment StartX=-27.5 StartY=-10 StartZ=0 EndX=-27.5 EndY=-15 EndZ=0
    g5: LineSegment StartX=-27.5 StartY=-15 StartZ=0 EndX=-12.3 EndY=-15 EndZ=0
    g6: LineSegment StartX=27.5 StartY=-15 StartZ=0 EndX=27.5 EndY=-10 EndZ=0
    g7: LineSegment StartX=27.5 StartY=-10 StartZ=0 EndX=14.2 EndY=-10 EndZ=0
    g8: LineSegment StartX=14.2 StartY=-10 StartZ=0 EndX=13.4698 EndY=0.902148 EndZ=0
    g9: LineSegment StartX=12.3 StartY=-15 StartZ=0 EndX=12.1995 EndY=-13.5 EndZ=0
    g10: LineSegment StartX=12.1995 StartY=-13.5 StartZ=0 EndX=-12.1995 EndY=-13.5 EndZ=0
    g11: LineSegment StartX=-12.1995 StartY=-13.5 StartZ=0 EndX=-12.3 EndY=-15 EndZ=0
    g12: LineSegment StartX=12.3 StartY=-15 StartZ=0 EndX=27.5 EndY=-15 EndZ=0
    g13: GeomPoint X=0 Y=13.5 Z=0
  constraints (39):
    c: Coincident(g0,g-1)
    c: Radius(g0) = 11
    c: Coincident(g1,g0)
    c: Coincident(g2,g3)
    c: Coincident(g3,g4)
    c: Coincident(g4,g5)
    c: Horizontal(g5)
    c: Coincident(g12,g6)
    c: Coincident(g6,g7)
    c: Horizontal(g7)
    c: Coincident(g7,g8)
    c: Coincident(g9,g10)
    c: Horizontal(g10)
    c: Coincident(g10,g11)
    c: Coincident(g5,g11)
    c: Coincident(g12,g9)
    c: Horizontal(g3)
    c: Vertical(g6)
    c: Vertical(g4)
    c: Equal(g9,g11)
    c: Horizontal(g12)
    c: Horizontal(g5,g9)
    c: Equal(g6,g4)
    c: Equal(g12,g5)
    c: Equal(g7,g3)
    c: DistanceX(g4,g6) = 55
    c: DistanceY(g6,g0) = 15
    c: Equal(g8,g2)
    c: DistanceY(g6,g6) = 5
    c: Parallel(g9,g8)
    c: DistanceY(g9,g9) = 1.5
    c: DistanceX(g5,g5) = 15.2
    c: Diameter(g1) = 27
    c: PointOnObject(g13,g1)
    c: PointOnObject(g13,g-2)
    c: DistanceY(g6,g13) = 28.5
    c: Tangent(g1,g2) = -1.5708
    c: Tangent(g1,g8) = -1.5708
    c: DistanceX(g3,g3) = 13.3
FEATURE [PartDesign::Pad] Pad015
  Direction = (1,-2e-16,3e-16)
  Length = 13
  Length2 = 100
  Placement = pos=(0,0,0) rot=(0.57735,0.57735,0.57735;2.0944rad)
  Profile = -> Sketch032
  Type = 0
FEATURE [Sketcher::SketchObject] Sketch033
  ExternalGeometry = -> [Pad015]
  FullyConstrained = true
  MapMode = 5
  Placement = pos=(4.2e-15,-6.6e-15,-15) rot=(0.707107,0.707107,0;3.14159rad)
  Support = -> [Pad015]
  sketch-geometry (7):
    g0: LineSegment StartX=-24.9 StartY=4.15 StartZ=0 EndX=-14.9 EndY=4.15 EndZ=0
    g1: LineSegment StartX=-14.9 StartY=4.15 StartZ=0 EndX=-14.9 EndY=-4.15 EndZ=0
    g2: LineSegment StartX=-14.9 StartY=-4.15 StartZ=0 EndX=-24.9 EndY=-4.15 EndZ=0
    g3: LineSegment StartX=-24.9 StartY=-4.15 StartZ=0 EndX=-24.9 EndY=4.15 EndZ=0
    g4: LineSegment StartX=-27.5 StartY=6.5 StartZ=0 EndX=-12.3 EndY=-6.5 EndZ=0
    g5: LineSegment StartX=-27.5 StartY=-6.5 StartZ=0 EndX=-12.3 EndY=6.5 EndZ=0
    g6: GeomPoint X=-19.9 Y=2.6e-15 Z=0
  constraints (17):
    c: Coincident(g0,g1)
    c: Coincident(g1,g2)
    c: Coincident(g2,g3)
    c: Coincident(g3,g0)
    c: Horizontal(g0)
    c: Horizontal(g2)
    c: Vertical(g1)
    c: Vertical(g3)
    c: DistanceX(g0,g0) = 10
    c: DistanceY(g1,g1) = 8.3
    c: Coincident(g4,g-3)
    c: Coincident(g4,g-4)
    c: Coincident(g5,g-4)
    c: Coincident(g5,g-3)
    c: PointOnObject(g6,g4)
    c: PointOnObject(g6,g5)
    c: Symmetric(g0,g1,g6)
FEATURE [PartDesign::Pocket] Pocket002
  BaseFeature = -> Pad015
  Length = 2.3
  Length2 = 100
  Placement = pos=(0,0,0) rot=(0.57735,0.57735,0.57735;2.0944rad)
  Profile = -> Sketch033
  Type = 0
FEATURE [Sketcher::SketchObject] Sketch034
  ExternalGeometry = -> [Pocket002]
  FullyConstrained = true
  MapMode = 5
  Placement = pos=(2.8e-15,-4.4e-15,-10) rot=(0,0,-1;1.5708rad)
  Support = -> [Pocket002]
  sketch-geometry (2):
    g0: Circle CenterX=21.2 CenterY=2.1e-15 CenterZ=0 NormalX=0 NormalY=0 NormalZ=1 AngleXU=0 Radius=2.5
    g1: LineSegment StartX=21.2 StartY=2.1e-15 StartZ=0 EndX=27.5 EndY=2.1e-15 EndZ=0
  constraints (5):
    c: Diameter(g0) = 5
    c: DistanceX(g0,g-3) = 6.3
    c: Coincident(g1,g0)
    c: Horizontal(g1)
    c: Symmetric(g-5,g-5,g1)
FEATURE [PartDesign::Pocket] Pocket003
  BaseFeature = -> Pocket002
  Length = 5
  Length2 = 100
  Placement = pos=(0,0,0) rot=(0.57735,0.57735,0.57735;2.0944rad)
  Profile = -> Sketch034
  Type = 2
FEATURE [Sketcher::SketchObject] Sketch035
  ExternalGeometry = -> [Pocket003]
  FullyConstrained = true
  MapMode = 5
  Placement = pos=(6.5,-1.4e-15,1.5e-15) rot=(0.57735,0.57735,0.57735;2.0944rad)
  Support = -> [Pocket003]
  sketch-geometry (6):
    g0: LineSegment StartX=-24.6 StartY=-13.7 StartZ=0 EndX=-24.6 EndY=-11.3 EndZ=0
    g1: LineSegment StartX=-24.6 StartY=-11.3 StartZ=0 EndX=-14.2 EndY=-11.3 EndZ=0
    g2: LineSegment StartX=-14.2 StartY=-11.3 StartZ=0 EndX=-14.2 EndY=-13.7 EndZ=0
    g3: LineSegment StartX=-14.2 StartY=-13.7 StartZ=0 EndX=-24.6 EndY=-13.7 EndZ=0
    g4: GeomPoint X=-19.4 Y=-12.5 Z=0
    g5: LineSegment StartX=-19.4 StartY=-12.5 StartZ=0 EndX=-27.5 EndY=-12.5 EndZ=0
  constraints (15):
    c: Coincident(g0,g1)
    c: Coincident(g1,g2)
    c: Coincident(g2,g3)
    c: Coincident(g3,g0)
    c: Horizontal(g1)
    c: Horizontal(g3)
    c: Vertical(g0)
    c: Vertical(g2)
    c: Symmetric(g1,g0,g4)
    c: DistanceX(g1,g1) = 10.4
    c: DistanceY(g2,g2) = 2.4
    c: DistanceX(g2,g-4) = 1.9
    c: Coincident(g5,g4)
    c: Horizontal(g5)
    c: Symmetric(g-5,g-5,g5)
FEATURE [PartDesign::Pocket] Pocket004
  BaseFeature = -> Pocket003
  Length = 0.4
  Length2 = 100
  Placement = pos=(0,0,0) rot=(0.57735,0.57735,0.57735;2.0944rad)
  Profile = -> Sketch035
  Type = 0
FEATURE [PartDesign::Mirrored] Mirrored
  BaseFeature = -> Pocket004
  MirrorPlane = -> Sketch033 [V_Axis]
  Originals = -> [Pocket002,Pocket003,Pocket004]
  Placement = pos=(0,0,0) rot=(0.57735,0.57735,0.57735;2.0944rad)
FEATURE [Sketcher::SketchObject] Sketch036
  ExternalGeometry = -> [Mirrored]
  FullyConstrained = true
  MapMode = 5
  Placement = pos=(0,0,0) rot=(1,0,0;1.5708rad)
  Support = -> [XZ_Plane049]
  sketch-geometry (9):
    g0: GeomPoint X=-6.5 Y=13.5 Z=0
    g1: LineSegment StartX=6.5 StartY=-10 StartZ=0 EndX=6.5 EndY=13.5 EndZ=0
    g2: LineSegment StartX=6.5 StartY=13.5 StartZ=0 EndX=4.75 EndY=13.5 EndZ=0
    g3: LineSegment StartX=-6.5 StartY=13.5 StartZ=0 EndX=-4.75 EndY=13.5 EndZ=0
    g4: LineSegment StartX=-6.5 StartY=-10 StartZ=0 EndX=-6.5 EndY=13.5 EndZ=0
    g5: LineSegment StartX=6.5 StartY=-10 StartZ=0 EndX=4.75 EndY=-1 EndZ=0
    g6: LineSegment StartX=4.75 StartY=-1 StartZ=0 EndX=4.75 EndY=13.5 EndZ=0
    g7: LineSegment StartX=-4.75 StartY=13.5 StartZ=0 EndX=-4.75 EndY=-1 EndZ=0
    g8: LineSegment StartX=-4.75 StartY=-1 StartZ=0 EndX=-6.5 EndY=-10 EndZ=0
  constraints (24):
    c: Vertical(g0,g-4)
    c: Horizontal(g-3,g0)
    c: Coincident(g1,g-3)
    c: Coincident(g1,g2)
    c: Horizontal(g2)
    c: Coincident(g3,g0)
    c: Horizontal(g3)
    c: Coincident(g4,g3)
    c: Vertical(g4,g-4)
    c: DistanceX(g3,g2) = 9.5
    c: Equal(g2,g3)
    c: Horizontal(g1,g4)
    c: Coincident(g1,g-5)
    c: Coincident(g1,g5)
    c: Coincident(g5,g6)
    c: Coincident(g6,g2)
    c: Vertical(g6)
    c: DistanceY(g1,g5) = 9
    c: Coincident(g3,g7)
    c: Vertical(g7)
    c: Coincident(g7,g8)
    c: Coincident(g8,g4)
    c: Horizontal(g7,g5)
    c: DistanceX(g2,g2) = 1.75
FEATURE [PartDesign::Pocket] Pocket005
  BaseFeature = -> Mirrored
  Length = 15
  Length2 = 15
  Placement = pos=(0,0,0) rot=(0.57735,0.57735,0.57735;2.0944rad)
  Profile = -> Sketch036
  Type = 4
FEATURE [Sketcher::SketchObject] Sketch037
  FullyConstrained = true
  MapMode = 5
  Placement = pos=(-6.5,1.4e-15,-1.5e-15) rot=(0.57735,0.57735,-0.57735;4.18879rad)
  Support = -> [Pocket005]
  sketch-geometry (1):
    g0: Circle CenterX=0 CenterY=0 CenterZ=0 NormalX=0 NormalY=0 NormalZ=1 AngleXU=0 Radius=12.2
  constraints (2):
    c: Coincident(g0,g-1)
    c: Diameter(g0) = 24.4
FEATURE [PartDesign::Pocket] Pocket006
  BaseFeature = -> Pocket005
  Length = 2.75
  Length2 = 100
  Placement = pos=(0,0,0) rot=(0.57735,0.57735,0.57735;2.0944rad)
  Profile = -> Sketch037
  Type = 0
FEATURE [Sketcher::SketchObject] Sketch038
  FullyConstrained = true
  MapMode = 5
  Placement = pos=(6.5,-1.4e-15,1.5e-15) rot=(0.57735,0.57735,0.57735;2.0944rad)
  Support = -> [Pocket006]
  sketch-geometry (1):
    g0: Circle CenterX=0 CenterY=0 CenterZ=0 NormalX=0 NormalY=0 NormalZ=1 AngleXU=0 Radius=12.1
  constraints (2):
    c: Coincident(g0,g-1)
    c: Diameter(g0) = 24.2
FEATURE [PartDesign::Pocket] Pocket007
  BaseFeature = -> Pocket006
  Length = 2.75
  Length2 = 100
  Placement = pos=(0,0,0) rot=(0.57735,0.57735,0.57735;2.0944rad)
  Profile = -> Sketch038
  Type = 0
FEATURE [Sketcher::SketchObject] Sketch039
  ExternalGeometry = -> [Pocket007]
  FullyConstrained = true
  MapMode = 5
  Placement = pos=(6.5,-1.4e-15,1.5e-15) rot=(0.57735,0.57735,0.57735;2.0944rad)
  Support = -> [Pocket007]
  sketch-geometry (6):
    g0: ArcOfCircle CenterX=0 CenterY=0 CenterZ=0 NormalX=0 NormalY=0 NormalZ=1 AngleXU=0 Radius=13.5 StartAngle=3.79664 EndAngle=5.62814
    g1: LineSegment StartX=-11.8698 StartY=-8.57666 StartZ=0 EndX=-12.3 EndY=-15 EndZ=0
    g2: LineSegment StartX=-12.3 StartY=-15 StartZ=0 EndX=12.3 EndY=-15 EndZ=0
    g3: LineSegment StartX=12.3 StartY=-15 StartZ=0 EndX=11.8698 EndY=-8.57666 EndZ=0
    g4: ArcOfCircle CenterX=11.2212 CenterY=-8.6201 CenterZ=0 NormalX=0 NormalY=0 NormalZ=1 AngleXU=0 Radius=0.65 StartAngle=0.0668757 EndAngle=2.48655
    g5: ArcOfCircle CenterX=-11.2212 CenterY=-8.6201 CenterZ=0 NormalX=0 NormalY=0 NormalZ=1 AngleXU=0 Radius=0.65 StartAngle=0.655044 EndAngle=3.07472
  constraints (14):
    c: Coincident(g0,g-1)
    c: Diameter(g0) = 27
    c: Coincident(g1,g2)
    c: Coincident(g2,g3)
    c: Coincident(g1,g-3)
    c: Coincident(g2,g-4)
    c: Tangent(g3,g4) = -1.5708
    c: Tangent(g0,g4) = 1.5708
    c: Tangent(g0,g5) = 1.5708
    c: Tangent(g1,g5) = -1.5708
    c: Equal(g4,g5)
    c: Horizontal(g4,g5)
    c: Parallel(g-4,g3)
    c: Radius(g4) = 0.65
FEATURE [PartDesign::Pocket] Pocket008
  BaseFeature = -> Pocket007
  Length = 5.25
  Length2 = 100
  Placement = pos=(0,0,0) rot=(0.57735,0.57735,0.57735;2.0944rad)
  Profile = -> Sketch039
  Type = 0
FEATURE [Sketcher::SketchObject] Sketch040
  ExternalGeometry = -> [Pocket008]
  FullyConstrained = true
  MapMode = 5
  Placement = pos=(-6.5,1.4e-15,-1.5e-15) rot=(0.57735,0.57735,-0.57735;4.18879rad)
  Support = -> [Pocket008]
  sketch-geometry (6):
    g0: ArcOfCircle CenterX=0 CenterY=0 CenterZ=0 NormalX=0 NormalY=0 NormalZ=1 AngleXU=0 Radius=13.5 StartAngle=0.655044 EndAngle=2.48655
    g1: LineSegment StartX=11.8698 StartY=8.57666 StartZ=0 EndX=12.3 EndY=15 EndZ=0
    g2: LineSegment StartX=12.3 StartY=15 StartZ=0 EndX=-12.3 EndY=15 EndZ=0
    g3: LineSegment StartX=-12.3 StartY=15 StartZ=0 EndX=-11.8698 EndY=8.57666 EndZ=0
    g4: ArcOfCircle CenterX=-11.2212 CenterY=8.6201 CenterZ=0 NormalX=0 NormalY=0 NormalZ=1 AngleXU=0 Radius=0.65 StartAngle=3.20847 EndAngle=5.62814
    g5: ArcOfCircle CenterX=11.2212 CenterY=8.6201 CenterZ=0 NormalX=0 NormalY=0 NormalZ=1 AngleXU=0 Radius=0.65 StartAngle=3.79664 EndAngle=6.21631
  constraints (14):
    c: Coincident(g0,g-1)
    c: Radius(g0) = 13.5
    c: Coincident(g1,g2)
    c: Coincident(g2,g-3)
    c: Coincident(g2,g3)
    c: Coincident(g-4,g1)
    c: Tangent(g3,g4) = -1.5708
    c: Tangent(g0,g4) = 1.5708
    c: Tangent(g0,g5) = 1.5708
    c: Tangent(g1,g5) = -1.5708
    c: Equal(g4,g5)
    c: Radius(g4) = 0.65
    c: Parallel(g-4,g1)
    c: Parallel(g3,g-3)
FEATURE [PartDesign::Pocket] Pocket009
  BaseFeature = -> Pocket008
  Length = 5.25
  Length2 = 100
  Placement = pos=(0,0,0) rot=(0.57735,0.57735,0.57735;2.0944rad)
  Profile = -> Sketch040
  Type = 0
FEATURE [PartDesign::Chamfer] Chamfer
  Angle = 45
  Base = -> Pocket009 [Edge159,Edge155,Edge22,Edge27]
  BaseFeature = -> Pocket009
  ChamferType = 0
  FlipDirection = false
  Placement = pos=(0,0,0) rot=(0.57735,0.57735,0.57735;2.0944rad)
  Size = 2
  Size2 = 1
  SupportTransform = false
FEATURE [Sketcher::SketchObject] Sketch041
  ExternalGeometry = -> [Chamfer]
  FullyConstrained = true
  MapMode = 5
  Placement = pos=(-3.75,5e-15,-2.7e-15) rot=(-0.57735,-0.57735,0.57735;2.0944rad)
  Support = -> [Chamfer]
  sketch-geometry (13):
    g0: ArcOfCircle CenterX=-6.9e-15 CenterY=-3.7e-15 CenterZ=0 NormalX=0 NormalY=0 NormalZ=1 AngleXU=0 Radius=11 StartAngle=5.75419 EndAngle=6.81218
    g1: ArcOfCircle CenterX=-6.9e-15 CenterY=-3.7e-15 CenterZ=0 NormalX=0 NormalY=0 NormalZ=1 AngleXU=0 Radius=12.2 StartAngle=5.94045 EndAngle=6.62592
    g2: ArcOfCircle CenterX=-6.9e-15 CenterY=-3.7e-15 CenterZ=0 NormalX=0 NormalY=0 NormalZ=1 AngleXU=0 Radius=11 StartAngle=2.6126 EndAngle=3.67059
    g3: ArcOfCircle CenterX=-6.9e-15 CenterY=-3.7e-15 CenterZ=0 NormalX=0 NormalY=0 NormalZ=1 AngleXU=0 Radius=12.2 StartAngle=2.79886 EndAngle=3.48433
    g4: Ellipse CenterX=-6.9e-15 CenterY=-3.7e-15 CenterZ=0 NormalX=0 NormalY=0 NormalZ=1 MajorRadius=13.5 MinorRadius=7.81051 AngleXU=-3e-16
    g5: LineSegment StartX=13.5 StartY=-7.4e-15 StartZ=0 EndX=-13.5 EndY=0 EndZ=0
    g6: LineSegment StartX=-4.8e-15 StartY=7.81051 StartZ=0 EndX=-9.1e-15 EndY=-7.81051 EndZ=0
    g7: GeomPoint X=11.0112 Y=-6.8e-15 Z=0
    g8: GeomPoint X=-11.0112 Y=-7e-16 Z=0
    g9: LineSegment StartX=-11.4904 StartY=4.1 StartZ=0 EndX=-9.49645 EndY=5.55135 EndZ=0
    g10: LineSegment StartX=-11.4904 StartY=-4.1 StartZ=0 EndX=-9.49645 EndY=-5.55135 EndZ=0
    g11: LineSegment StartX=9.49645 StartY=-5.55135 StartZ=0 EndX=11.4904 EndY=-4.1 EndZ=0
    g12: LineSegment StartX=11.4904 StartY=4.1 StartZ=0 EndX=9.49645 EndY=5.55135 EndZ=0
  constraints (29):
    c: Coincident(g0,g-4)
    c: PointOnObject(g0,g-4)
    c: Coincident(g1,g0)
    c: PointOnObject(g1,g-3)
    c: Coincident(g2,g0)
    c: PointOnObject(g2,g-4)
    c: Coincident(g3,g0)
    c: PointOnObject(g3,g-3)
    c: InternalAlignment(g5-g8 -> g4) x4
    c: Coincident(g4,g0)
    c: PointOnObject(g3,g4)
    c: PointOnObject(g2,g4)
    c: PointOnObject(g3,g4)
    c: PointOnObject(g2,g4)
    c: PointOnObject(g0,g4)
    c: PointOnObject(g1,g4)
    c: PointOnObject(g1,g4)
    c: PointOnObject(g0,g4)
    c: PointOnObject(g5,g-1)
    c: DistanceX(g5,g5) = 27
    c: DistanceY(g3,g3) = 8.2
    c: Coincident(g9,g3)
    c: Coincident(g9,g2)
    c: Coincident(g10,g3)
    c: Coincident(g10,g2)
    c: Coincident(g11,g0)
    c: Coincident(g11,g1)
    c: Coincident(g12,g1)
    c: Coincident(g12,g0)
FEATURE [PartDesign::Pocket] Pocket010
  BaseFeature = -> Chamfer
  Length = 5
  Length2 = 100
  Placement = pos=(0,0,0) rot=(0.57735,0.57735,0.57735;2.0944rad)
  Profile = -> Sketch041
  Type = 0
FEATURE [PartDesign::Body] Body035  label="Metal case"
  Group = -> [Sketch032,Pad015,Sketch033,Pocket002,Sketch034,Pocket003,Sketch035,Pocket004,Mirrored,Sketch036,Pocket005,Sketch037,Pocket006,Sketch038,Pocket007,Sketch039,Pocket008,Sketch040,Pocket009,Chamfer,Sketch041,Pocket010]
  Origin = -> Origin049
  Tip = -> Pocket010
FEATURE [App::DocumentObjectGroup] Group006  label="Case"
  Group = -> [Body035]
FEATURE [App::Part] Part014  label="KP08-001"
  Group = -> [Group,Body016,Body015,Body020,Body017,Body021,Body019,Body018,Group001,Body023,Body022,Group002,Body028,Body027,Body030,Body026,Body029,Body025,Body024,Group003,Body034,Body033,Group004,Body031,Body032,Group005,Body014,Group006,Body035]
  Origin = -> Origin050
  Placement = pos=(10,246,105) rot=(0,0,1;0rad)
FEATURE [Sketcher::SketchObject] Sketch042
  FullyConstrained = true
  MapMode = 5
  Placement = pos=(0,0,0) rot=(-0.57735,0.57735,0.57735;4.18879rad)
  Support = -> [YZ_Plane058]
  sketch-geometry (1):
    g0: Circle CenterX=0 CenterY=-7.5 CenterZ=0 NormalX=0 NormalY=0 NormalZ=1 AngleXU=0 Radius=0.25
  constraints (3):
    c: PointOnObject(g0,g-2)
    c: DistanceY(g0) = -7.5
    c: Diameter(g0) = 0.5
FEATURE [Sketcher::SketchObject] Sketch043
  FullyConstrained = true
  MapMode = 5
  Support = -> [XY_Plane051]
  sketch-geometry (2):
    g0: LineSegment StartX=0 StartY=5.5 StartZ=0 EndX=6e-16 EndY=9.5 EndZ=0
    g1: ArcOfCircle CenterX=0 CenterY=7.5 CenterZ=0 NormalX=0 NormalY=0 NormalZ=1 AngleXU=0 Radius=2 StartAngle=4.71239 EndAngle=7.85398
  constraints (7):
    c: PointOnObject(g0,g-2)
    c: PointOnObject(g0,g-2)
    c: PointOnObject(g1,g0)
    c: Coincident(g1,g0)
    c: Coincident(g1,g0)
    c: Radius(g1) = 2
    c: DistanceY(g1) = 7.5
FEATURE [PartDesign::Revolution] Revolution011
  Angle = 360
  Axis = (0,1,0)
  Base = (0,0,0)
  Profile = -> Sketch043
  ReferenceAxis = -> Sketch043 [V_Axis]
  Reversed = true
FEATURE [PartDesign::Body] Body037  label="Ball 008"
  Group = -> [Sketch043,Revolution011]
  Origin = -> Origin052
  Tip = -> Revolution011
FEATURE [PartDesign::FeatureBase] Clone014
  BaseFeature = -> Body037
FEATURE [PartDesign::Body] Body038  label="Ball 009"
  BaseFeature = -> Body037
  Group = -> [Clone014]
  Origin = -> Origin053
  Placement = pos=(0,0,0) rot=(-1,0,0;0.897598rad)
  Tip = -> Clone014
FEATURE [PartDesign::FeatureBase] Clone015
  BaseFeature = -> Body037
FEATURE [PartDesign::Body] Body039  label="Ball 010"
  BaseFeature = -> Body037
  Group = -> [Clone015]
  Origin = -> Origin054
  Placement = pos=(0,0,0) rot=(-1,0,0;1.7952rad)
  Tip = -> Clone015
FEATURE [PartDesign::FeatureBase] Clone016
  BaseFeature = -> Body037
FEATURE [PartDesign::Body] Body040  label="Ball 011"
  BaseFeature = -> Body037
  Group = -> [Clone016]
  Origin = -> Origin055
  Placement = pos=(0,0,0) rot=(1,0,0;3.59039rad)
  Tip = -> Clone016
FEATURE [PartDesign::FeatureBase] Clone017
  BaseFeature = -> Body037
FEATURE [PartDesign::Body] Body041  label="Ball 012"
  BaseFeature = -> Body037
  Group = -> [Clone017]
  Origin = -> Origin056
  Placement = pos=(0,0,0) rot=(1,0,0;2.69279rad)
  Tip = -> Clone017
FEATURE [PartDesign::FeatureBase] Clone018
  BaseFeature = -> Body037
FEATURE [PartDesign::Body] Body042  label="Ball 013"
  BaseFeature = -> Body037
  Group = -> [Clone018]
  Origin = -> Origin057
  Placement = pos=(0,0,0) rot=(1,0,0;1.7952rad)
  Tip = -> Clone018
FEATURE [PartDesign::FeatureBase] Clone019
  BaseFeature = -> Body037
FEATURE [PartDesign::Body] Body043  label="Ball 014"
  BaseFeature = -> Body037
  Group = -> [Clone019]
  Origin = -> Origin058
  Placement = pos=(0,0,0) rot=(1,0,0;0.897598rad)
  Tip = -> Clone019
FEATURE [App::DocumentObjectGroup] Group007  label="Balls001"
  Group = -> [Body037,Body038,Body039,Body040,Body041,Body042,Body043]
FEATURE [Sketcher::SketchObject] Sketch044
  FullyConstrained = true
  MapMode = 5
  Support = -> [XY_Plane060]
  sketch-geometry (7):
    g0: LineSegment StartX=-5 StartY=7.5 StartZ=0 EndX=5 EndY=7.5 EndZ=0
    g1: LineSegment StartX=-0.210977 StartY=7.5 StartZ=0 EndX=0.210977 EndY=7.5 EndZ=0
    g2: ArcOfCircle CenterX=0.25 CenterY=7.5 CenterZ=0 NormalX=0 NormalY=0 NormalZ=1 AngleXU=0 Radius=0.460977 StartAngle=2.43297 EndAngle=3.14159
    g3: ArcOfCircle CenterX=-0.25 CenterY=7.5 CenterZ=0 NormalX=0 NormalY=0 NormalZ=1 AngleXU=0 Radius=0.460977 StartAngle=9.792e-13 EndAngle=0.708626
    g4: LineSegment StartX=-0.1 StartY=7.8 StartZ=0 EndX=-0.1 EndY=7.75 EndZ=0
    g5: LineSegment StartX=-0.1 StartY=7.75 StartZ=0 EndX=0.1 EndY=7.75 EndZ=0
    g6: LineSegment StartX=0.1 StartY=7.75 StartZ=0 EndX=0.1 EndY=7.8 EndZ=0
  constraints (22):
    c: DistanceY(g-1,g0) = 7.5
    c: Symmetric(g0,g0,g-2)
    c: DistanceX(g0,g0) = 10
    c: PointOnObject(g1,g0)
    c: PointOnObject(g1,g0)
    c: Coincident(g3,g1)
    c: Coincident(g2,g1)
    c: Coincident(g2,g4)
    c: Coincident(g4,g5)
    c: Horizontal(g5)
    c: Coincident(g5,g6)
    c: Coincident(g6,g3)
    c: Vertical(g6)
    c: Equal(g3,g2)
    c: Vertical(g4)
    c: Symmetric(g2,g3,g-2)
    c: DistanceX(g5,g5) = 0.2
    c: Distance(g5,g1) = 0.25
    c: DistanceX(g3,g-1) = 0.25
    c: PointOnObject(g3,g1)
    c: PointOnObject(g2,g1)
    c: Distance(g3,g1) = 0.3
FEATURE [PartDesign::Revolution] Revolution012
  Angle = 360
  Axis = (10,0,0)
  Base = (-5,7.5,0)
  Profile = -> Sketch044
  ReferenceAxis = -> Sketch044 [Axis]
FEATURE [PartDesign::Body] Body046  label="Rivet 008"
  Group = -> [Sketch044,Revolution012]
  Origin = -> Origin061
  Placement = pos=(0,0,0) rot=(1,0,0;0.448799rad)
  Tip = -> Revolution012
FEATURE [PartDesign::FeatureBase] Clone021
  BaseFeature = -> Body046
  Placement = pos=(0,0,0) rot=(1,0,0;0.448799rad)
FEATURE [PartDesign::Body] Body047  label="Rivet 009"
  BaseFeature = -> Body046
  Group = -> [Clone021]
  Origin = -> Origin062
  Placement = pos=(0,0,0) rot=(1,0,0;0.897598rad)
  Tip = -> Clone021
FEATURE [PartDesign::FeatureBase] Clone022
  BaseFeature = -> Body046
  Placement = pos=(0,0,0) rot=(1,0,0;0.448799rad)
FEATURE [PartDesign::Body] Body048  label="Rivet 010"
  BaseFeature = -> Body046
  Group = -> [Clone022]
  Origin = -> Origin063
  Placement = pos=(0,0,0) rot=(1,0,0;1.7952rad)
  Tip = -> Clone022
FEATURE [PartDesign::FeatureBase] Clone023
  BaseFeature = -> Body046
  Placement = pos=(0,0,0) rot=(1,0,0;0.448799rad)
FEATURE [PartDesign::Body] Body049  label="Rivet 011"
  BaseFeature = -> Body046
  Group = -> [Clone023]
  Origin = -> Origin064
  Placement = pos=(0,0,0) rot=(1,0,0;2.69279rad)
  Tip = -> Clone023
FEATURE [PartDesign::FeatureBase] Clone024
  BaseFeature = -> Body046
  Placement = pos=(0,0,0) rot=(1,0,0;0.448799rad)
FEATURE [PartDesign::Body] Body050  label="Rivet 012"
  BaseFeature = -> Body046
  Group = -> [Clone024]
  Origin = -> Origin065
  Placement = pos=(0,0,0) rot=(1,0,0;3.59039rad)
  Tip = -> Clone024
FEATURE [PartDesign::FeatureBase] Clone025
  BaseFeature = -> Body046
  Placement = pos=(0,0,0) rot=(1,0,0;0.448799rad)
FEATURE [PartDesign::Body] Body051  label="Rivet 013"
  BaseFeature = -> Body046
  Group = -> [Clone025]
  Origin = -> Origin066
  Placement = pos=(0,0,0) rot=(-1,0,0;1.7952rad)
  Tip = -> Clone025
FEATURE [PartDesign::FeatureBase] Clone026
  BaseFeature = -> Body046
  Placement = pos=(0,0,0) rot=(1,0,0;0.448799rad)
FEATURE [PartDesign::Body] Body052  label="Rivet 014"
  BaseFeature = -> Body046
  Group = -> [Clone026]
  Origin = -> Origin067
  Placement = pos=(0,0,0) rot=(-1,0,0;0.897598rad)
  Tip = -> Clone026
FEATURE [App::DocumentObjectGroup] Group009  label="Rivets001"
  Group = -> [Body046,Body047,Body048,Body049,Body050,Body051,Body052]
FEATURE [Sketcher::SketchObject] Sketch045
  FullyConstrained = true
  MapMode = 5
  Placement = pos=(0,0,0) rot=(1,0,0;1.5708rad)
  Support = -> [XZ_Plane058]
  sketch-geometry (4):
    g0: LineSegment StartX=0 StartY=8.5 StartZ=0 EndX=0.1 EndY=8.5 EndZ=0
    g1: LineSegment StartX=0.1 StartY=8.5 StartZ=0 EndX=0.1 EndY=6.5 EndZ=0
    g2: LineSegment StartX=0.1 StartY=6.5 StartZ=0 EndX=0 EndY=6.5 EndZ=0
    g3: LineSegment StartX=0 StartY=6.5 StartZ=0 EndX=0 EndY=8.5 EndZ=0
  constraints (12):
    c: Coincident(g0,g1)
    c: Coincident(g1,g2)
    c: Coincident(g2,g3)
    c: Coincident(g3,g0)
    c: Horizontal(g0)
    c: Horizontal(g2)
    c: Vertical(g1)
    c: Vertical(g3)
    c: PointOnObject(g0,g-2)
    c: DistanceX(g0,g0) = 0.1
    c: DistanceY(g0) = 8.5
    c: DistanceY(g1) = 6.5
FEATURE [PartDesign::Revolution] Revolution013
  Angle = 360
  Axis = (1,0,0)
  Base = (0,0,0)
  Placement = pos=(0,0,0) rot=(1,0,0;1.5708rad)
  Profile = -> Sketch045
  ReferenceAxis = -> Sketch045 [H_Axis]
FEATURE [Sketcher::SketchObject] Sketch046
  FullyConstrained = true
  MapMode = 5
  Placement = pos=(0,0,0) rot=(0.57735,0.57735,0.57735;2.0944rad)
  Support = -> [YZ_Plane058]
  sketch-geometry (5):
    g0: ArcOfCircle CenterX=0 CenterY=7.5 CenterZ=0 NormalX=0 NormalY=0 NormalZ=1 AngleXU=0 Radius=2.11 StartAngle=5.66076 EndAngle=6.65667
    g1: LineSegment StartX=5e-16 StartY=8.5 StartZ=0 EndX=0 EndY=6.26986 EndZ=0
    g2: ArcOfCircle CenterX=0 CenterY=0 CenterZ=0 NormalX=0 NormalY=0 NormalZ=1 AngleXU=0 Radius=6.5 StartAngle=1.3039 EndAngle=1.5708
    g3: LineSegment StartX=1.71431 StartY=6.26986 StartZ=0 EndX=0 EndY=6.26986 EndZ=0
    g4: ArcOfCircle CenterX=0 CenterY=0 CenterZ=0 NormalX=0 NormalY=0 NormalZ=1 AngleXU=0 Radius=8.5 StartAngle=1.33757 EndAngle=1.5708
  constraints (16):
    c: PointOnObject(g0,g-2)
    c: DistanceY(g0) = 7.5
    c: Radius(g0) = 2.11
    c: PointOnObject(g2,g1)
    c: DistanceY(g2) = 6.5
    c: Coincident(g2,g-1)
    c: Coincident(g3,g2)
    c: Horizontal(g3)
    c: Coincident(g0,g2)
    c: Coincident(g1,g3)
    c: PointOnObject(g1,g-2)
    c: PointOnObject(g1,g-2)
    c: Coincident(g4,g-1)
    c: Coincident(g4,g1)
    c: DistanceY(g1) = 8.5
    c: Coincident(g0,g4)
FEATURE [PartDesign::Revolution] Revolution014
  Angle = 180
  Axis = (-2e-16,3e-16,1)
  Base = (0,0,0)
  BaseFeature = -> Revolution013
  Placement = pos=(0,0,0) rot=(1,0,0;1.5708rad)
  Profile = -> Sketch046
  ReferenceAxis = -> Sketch046 [V_Axis]
  Reversed = true
FEATURE [PartDesign::PolarPattern] PolarPattern004
  Angle = 360
  Axis = -> Sketch046 [N_Axis]
  BaseFeature = -> Revolution014
  Occurrences = 3
  Originals = -> [Revolution014]
  Placement = pos=(0,0,0) rot=(1,0,0;1.5708rad)
  Refine = true
FEATURE [Sketcher::SketchObject] Sketch047
  FullyConstrained = true
  MapMode = 5
  Placement = pos=(0,0,0) rot=(0.57735,0.57735,0.57735;2.0944rad)
  Support = -> [YZ_Plane058]
  sketch-geometry (4):
    g0: ArcOfCircle CenterX=0 CenterY=7.5 CenterZ=0 NormalX=0 NormalY=0 NormalZ=1 AngleXU=0 Radius=2.01 StartAngle=5.57985 EndAngle=6.86228
    g1: LineSegment StartX=0 StartY=6.2 StartZ=0 EndX=1.533 EndY=6.2 EndZ=0
    g2: LineSegment StartX=0 StartY=8.6 StartZ=0 EndX=0 EndY=6.2 EndZ=0
    g3: LineSegment StartX=0 StartY=8.6 StartZ=0 EndX=1.68229 EndY=8.6 EndZ=0
  constraints (13):
    c: PointOnObject(g0,g-2)
    c: DistanceY(g0) = 7.5
    c: Radius(g0) = 2.01
    c: PointOnObject(g1,g-2)
    c: Horizontal(g1)
    c: Coincident(g0,g1)
    c: DistanceY(g1) = 6.2
    c: DistanceY(g2) = 8.6
    c: Coincident(g2,g1)
    c: PointOnObject(g2,g-2)
    c: Coincident(g3,g2)
    c: Horizontal(g3)
    c: Coincident(g0,g3)
FEATURE [PartDesign::Groove] Groove001
  Angle = 360
  Axis = (-2e-16,3e-16,1)
  Base = (0,0,0)
  BaseFeature = -> PolarPattern004
  Placement = pos=(0,0,0) rot=(1,0,0;1.5708rad)
  Profile = -> Sketch047
  ReferenceAxis = -> Sketch047 [V_Axis]
FEATURE [PartDesign::PolarPattern] PolarPattern005
  Angle = 360
  Axis = -> Sketch047 [N_Axis]
  BaseFeature = -> Groove001
  Occurrences = 3
  Originals = -> [Groove001]
  Placement = pos=(0,0,0) rot=(1,0,0;1.5708rad)
FEATURE [PartDesign::Pocket] Pocket011
  BaseFeature = -> PolarPattern005
  Length = 5
  Length2 = 100
  Placement = pos=(0,0,0) rot=(1,0,0;1.5708rad)
  Profile = -> Sketch042
  Type = 1
FEATURE [PartDesign::PolarPattern] PolarPattern006
  Angle = 360
  Axis = -> Sketch042 [N_Axis]
  BaseFeature = -> Pocket011
  Occurrences = 3
  Originals = -> [Pocket011]
  Placement = pos=(0,0,0) rot=(1,0,0;1.5708rad)
FEATURE [PartDesign::Body] Body044  label="Cage 003"
  Group = -> [Sketch045,Revolution013,Sketch046,Revolution014,PolarPattern004,Sketch047,Groove001,PolarPattern005,Sketch042,Pocket011,PolarPattern006]
  Origin = -> Origin059
  Placement = pos=(0,0,0) rot=(-1,0,0;1.5708rad)
  Tip = -> PolarPattern006
FEATURE [PartDesign::FeatureBase] Clone020
  BaseFeature = -> Body044
  Placement = pos=(0,0,0) rot=(-1,0,0;1.5708rad)
FEATURE [PartDesign::Body] Body045  label="Cage 004"
  BaseFeature = -> Body044
  Group = -> [Clone020]
  Origin = -> Origin060
  Placement = pos=(0,0,0) rot=(0,1,0;3.14159rad)
  Tip = -> Clone020
FEATURE [App::DocumentObjectGroup] Group008  label="Cages001"
  Group = -> [Body044,Body045]
FEATURE [Sketcher::SketchObject] Sketch048
  FullyConstrained = true
  MapMode = 5
  Support = -> [XY_Plane067]
  sketch-geometry (14):
    g0: ArcOfCircle CenterX=-1e-16 CenterY=7.5 CenterZ=0 NormalX=0 NormalY=0 NormalZ=1 AngleXU=0 Radius=2 StartAngle=0.848062 EndAngle=2.29353
    g1: LineSegment StartX=-3.5 StartY=11 StartZ=0 EndX=3.5 EndY=11 EndZ=0
    g2: LineSegment StartX=3.5 StartY=11 StartZ=0 EndX=3.5 EndY=9.2 EndZ=0
    g3: LineSegment StartX=2.9 StartY=9 StartZ=0 EndX=1.32288 EndY=9 EndZ=0
    g4: LineSegment StartX=-3.5 StartY=9.2 StartZ=0 EndX=-3.5 EndY=11 EndZ=0
    g5: LineSegment StartX=-1.32288 StartY=9 StartZ=0 EndX=-2.9 EndY=9 EndZ=0
    g6: LineSegment StartX=2.9 StartY=9 StartZ=0 EndX=2.9 EndY=9.5 EndZ=0
    g7: LineSegment StartX=2.9 StartY=9.5 StartZ=0 EndX=3.2 EndY=9.5 EndZ=0
    g8: LineSegment StartX=3.2 StartY=9.5 StartZ=0 EndX=3.2 EndY=9.2 EndZ=0
    g9: LineSegment StartX=3.2 StartY=9.2 StartZ=0 EndX=3.5 EndY=9.2 EndZ=0
    g10: LineSegment StartX=-3.5 StartY=9.2 StartZ=0 EndX=-3.2 EndY=9.2 EndZ=0
    g11: LineSegment StartX=-3.2 StartY=9.2 StartZ=0 EndX=-3.2 EndY=9.5 EndZ=0
    g12: LineSegment StartX=-3.2 StartY=9.5 StartZ=0 EndX=-2.9 EndY=9.5 EndZ=0
    g13: LineSegment StartX=-2.9 StartY=9.5 StartZ=0 EndX=-2.9 EndY=9 EndZ=0
  constraints (41):
    c: Coincident(g1,g2)
    c: Coincident(g4,g1)
    c: Horizontal(g3)
    c: Vertical(g2)
    c: Vertical(g4)
    c: Coincident(g0,g5)
    c: Coincident(g0,g3)
    c: DistanceY(g-1,g0) = 7.5
    c: Radius(g0) = 2
    c: Symmetric(g1,g1,g-2)
    c: Symmetric(g0,g0,g-2)
    c: DistanceY(g1) = 11
    c: DistanceX(g1,g1) = 7
    c: Vertical(g6)
    c: Coincident(g6,g7)
    c: Horizontal(g7)
    c: Coincident(g7,g8)
    c: Vertical(g8)
    c: Coincident(g8,g9)
    c: Coincident(g3,g6)
    c: Coincident(g2,g9)
    c: Horizontal(g10)
    c: Coincident(g10,g11)
    c: Coincident(g11,g12)
    c: Horizontal(g12)
    c: Coincident(g12,g13)
    c: Vertical(g13)
    c: Vertical(g11)
    c: Coincident(g4,g10)
    c: Coincident(g5,g13)
    c: DistanceY(g13,g13) = 0.5
    c: DistanceX(g12,g12) = 0.3
    c: DistanceY(g5,g10) = 0.2
    c: Symmetric(g5,g3,g-2)
    c: DistanceY(g3) = 9
    c: DistanceY(g6) = 9.5
    c: Equal(g7,g12)
    c: Equal(g13,g6)
    c: Horizontal(g9)
    c: Horizontal(g8,g10)
    c: Equal(g12,g10)
FEATURE [PartDesign::Revolution] Revolution015
  Angle = 360
  Axis = (1,0,0)
  Base = (0,0,0)
  Profile = -> Sketch048
  ReferenceAxis = -> X_Axis067
FEATURE [PartDesign::Fillet] Fillet157
  Base = -> Revolution015 [Edge14,Edge15]
  BaseFeature = -> Revolution015
  Radius = 0.3
  SupportTransform = false
FEATURE [PartDesign::Body] Body053  label="Outer Ring002"
  Group = -> [Sketch048,Revolution015,Fillet157]
  Origin = -> Origin068
  Tip = -> Fillet157
FEATURE [Sketcher::SketchObject] Sketch049
  FullyConstrained = true
  MapMode = 5
  Support = -> [XY_Plane068]
  sketch-geometry (14):
    g0: LineSegment StartX=-2.9 StartY=6 StartZ=0 EndX=-1.32288 EndY=6 EndZ=0
    g1: LineSegment StartX=-3.5 StartY=4 StartZ=0 EndX=-3.5 EndY=5.7 EndZ=0
    g2: ArcOfCircle CenterX=-1e-16 CenterY=7.5 CenterZ=0 NormalX=0 NormalY=0 NormalZ=1 AngleXU=0 Radius=2 StartAngle=3.98965 EndAngle=5.43512
    g3: LineSegment StartX=1.32288 StartY=6 StartZ=0 EndX=2.9 EndY=6 EndZ=0
    g4: LineSegment StartX=-3.5 StartY=5.7 StartZ=0 EndX=-3.2 EndY=5.7 EndZ=0
    g5: LineSegment StartX=-3.2 StartY=5.7 StartZ=0 EndX=-3.2 EndY=5.5 EndZ=0
    g6: LineSegment StartX=-3.2 StartY=5.5 StartZ=0 EndX=-2.9 EndY=5.5 EndZ=0
    g7: LineSegment StartX=-2.9 StartY=5.5 StartZ=0 EndX=-2.9 EndY=6 EndZ=0
    g8: LineSegment StartX=8.5 StartY=6 StartZ=0 EndX=3.2 EndY=6 EndZ=0
    g9: LineSegment StartX=3.2 StartY=6 StartZ=0 EndX=3.2 EndY=5.5 EndZ=0
    g10: LineSegment StartX=3.2 StartY=5.5 StartZ=0 EndX=2.9 EndY=5.5 EndZ=0
    g11: LineSegment StartX=2.9 StartY=5.5 StartZ=0 EndX=2.9 EndY=6 EndZ=0
    g12: LineSegment StartX=8.5 StartY=4 StartZ=0 EndX=8.5 EndY=6 EndZ=0
    g13: LineSegment StartX=-3.5 StartY=4 StartZ=0 EndX=8.5 EndY=4 EndZ=0
  constraints (43):
    c: Horizontal(g0)
    c: Vertical(g1)
    c: DistanceY(g1) = 4
    c: Coincident(g2,g0)
    c: Coincident(g2,g3)
    c: Horizontal(g3)
    c: Radius(g2) = 2
    c: DistanceY(g2) = 7.5
    c: Symmetric(g0,g2,g-2)
    c: Horizontal(g4)
    c: Coincident(g4,g5)
    c: Vertical(g5)
    c: Coincident(g5,g6)
    c: Horizontal(g6)
    c: Coincident(g6,g7)
    c: Vertical(g7)
    c: Horizontal(g8)
    c: Coincident(g8,g9)
    c: Vertical(g9)
    c: Coincident(g9,g10)
    c: Horizontal(g10)
    c: Coincident(g10,g11)
    c: Vertical(g11)
    c: Coincident(g3,g11)
    c: Coincident(g0,g7)
    c: Coincident(g1,g4)
    c: DistanceY(g3) = 6
    c: DistanceY(g6,g0) = 0.5
    c: DistanceX(g4,g4) = 0.3
    c: DistanceX(g6,g6) = 0.3
    c: DistanceY(g5,g4) = 0.2
    c: Vertical(g12)
    c: Equal(g11,g7)
    c: DistanceY(g1,g0) = 2
    c: DistanceX(g8,g8) = 5.3
    c: Coincident(g13,g1)
    c: Coincident(g13,g12)
    c: Horizontal(g13)
    c: DistanceX(g13,g13) = 12
    c: DistanceX(g1,g2) = 3.5
    c: Coincident(g8,g12)
    c: Equal(g7,g9)
    c: Equal(g6,g10)
FEATURE [PartDesign::Revolution] Revolution016
  Angle = 360
  Axis = (1,0,0)
  Base = (0,0,0)
  Profile = -> Sketch049
  ReferenceAxis = -> X_Axis068
FEATURE [PartDesign::Fillet] Fillet158
  Base = -> Revolution016 [Edge13,Edge11]
  BaseFeature = -> Revolution016
  Radius = 0.2
  SupportTransform = false
FEATURE [PartDesign::Body] Body054  label="Inner Ring002"
  Group = -> [Sketch049,Revolution016,Fillet158]
  Origin = -> Origin069
  Tip = -> Fillet158
FEATURE [App::DocumentObjectGroup] Group011  label="Rings001"
  Group = -> [Body053,Body054]
FEATURE [Sketcher::SketchObject] Sketch050
  FullyConstrained = true
  MapMode = 5
  Placement = pos=(0,0,0) rot=(1,0,0;1.5708rad)
  Support = -> [XZ_Plane069]
  sketch-geometry (12):
    g0: LineSegment StartX=2.9 StartY=9.5 StartZ=0 EndX=2.9 EndY=8.5 EndZ=0
    g1: LineSegment StartX=2.9 StartY=8.5 StartZ=0 EndX=3.2 EndY=8.5 EndZ=0
    g2: LineSegment StartX=3.2 StartY=8.5 StartZ=0 EndX=3.2 EndY=6.5 EndZ=0
    g3: LineSegment StartX=3.2 StartY=6.5 StartZ=0 EndX=2.9 EndY=6.5 EndZ=0
    g4: LineSegment StartX=2.9 StartY=6.5 StartZ=0 EndX=2.9 EndY=5.5 EndZ=0
    g5: LineSegment StartX=2.9 StartY=5.5 StartZ=0 EndX=3.2 EndY=5.5 EndZ=0
    g6: LineSegment StartX=3.2 StartY=5.5 StartZ=0 EndX=3.2 EndY=6 EndZ=0
    g7: LineSegment StartX=3.2 StartY=6 StartZ=0 EndX=3.5 EndY=6 EndZ=0
    g8: LineSegment StartX=3.5 StartY=6 StartZ=0 EndX=3.5 EndY=9 EndZ=0
    g9: LineSegment StartX=3.5 StartY=9 StartZ=0 EndX=3.2 EndY=9 EndZ=0
    g10: LineSegment StartX=3.2 StartY=9 StartZ=0 EndX=3.2 EndY=9.5 EndZ=0
    g11: LineSegment StartX=3.2 StartY=9.5 StartZ=0 EndX=2.9 EndY=9.5 EndZ=0
  constraints (36):
    c: Vertical(g0)
    c: Coincident(g0,g1)
    c: Horizontal(g1)
    c: Coincident(g1,g2)
    c: Vertical(g2)
    c: Coincident(g2,g3)
    c: Horizontal(g3)
    c: Coincident(g3,g4)
    c: Vertical(g4)
    c: Coincident(g4,g5)
    c: Horizontal(g5)
    c: Coincident(g5,g6)
    c: Vertical(g6)
    c: Coincident(g6,g7)
    c: Horizontal(g7)
    c: Coincident(g7,g8)
    c: Vertical(g8)
    c: Coincident(g8,g9)
    c: Horizontal(g9)
    c: Coincident(g9,g10)
    c: Vertical(g10)
    c: Coincident(g10,g11)
    c: Coincident(g11,g0)
    c: Horizontal(g11)
    c: DistanceY(g4) = 5.5
    c: DistanceX(g4) = 2.9
    c: DistanceY(g5,g6) = 0.5
    c: DistanceY(g6,g2) = 0.5
    c: DistanceX(g5,g5) = 0.3
    c: Equal(g5,g7)
    c: Equal(g7,g3)
    c: Equal(g3,g1)
    c: Equal(g1,g9)
    c: Equal(g4,g0)
    c: Equal(g6,g10)
    c: DistanceY(g4,g0) = 4
FEATURE [PartDesign::Revolution] Revolution017
  Angle = 360
  Axis = (1,0,0)
  Base = (0,0,0)
  Placement = pos=(0,0,0) rot=(1,0,0;1.5708rad)
  Profile = -> Sketch050
  ReferenceAxis = -> Sketch050 [H_Axis]
FEATURE [PartDesign::Fillet] Fillet159
  Base = -> Revolution017 [Edge14,Edge12]
  BaseFeature = -> Revolution017
  Placement = pos=(0,0,0) rot=(1,0,0;1.5708rad)
  Radius = 0.2
  SupportTransform = false
FEATURE [PartDesign::Body] Body055  label="Seal 003"
  Group = -> [Sketch050,Revolution017,Fillet159]
  Origin = -> Origin070
  Tip = -> Fillet159
FEATURE [PartDesign::FeatureBase] Clone027
  BaseFeature = -> Body055
FEATURE [PartDesign::Body] Body056  label="Seal 004"
  BaseFeature = -> Body055
  Group = -> [Clone027]
  Origin = -> Origin071
  Placement = pos=(0,0,0) rot=(0,1,0;3.14159rad)
  Tip = -> Clone027
FEATURE [App::DocumentObjectGroup] Group010  label="Seals001"
  Group = -> [Body055,Body056]
FEATURE [Sketcher::SketchObject] Sketch051
  AttachmentOffset = pos=(0,0,4) rot=(0,0,1;0rad)
  FullyConstrained = true
  MapMode = 5
  Placement = pos=(0,0,4) rot=(0,0,1;0rad)
  Support = -> [XY_Plane050]
  sketch-geometry (1):
    g0: Circle CenterX=6 CenterY=0 CenterZ=0 NormalX=0 NormalY=0 NormalZ=1 AngleXU=0 Radius=1.5
  constraints (3):
    c: PointOnObject(g0,g-1)
    c: Diameter(g0) = 3
    c: DistanceX(g-1,g0) = 6
FEATURE [PartDesign::Pad] Pad016
  Direction = (0,0,1)
  Length = 3
  Length2 = 100
  Profile = -> Sketch051
  Type = 0
FEATURE [Sketcher::SketchObject] Sketch052
  ExternalGeometry = -> [Pad016]
  FullyConstrained = true
  MapMode = 5
  Placement = pos=(0,0,7) rot=(0,0,1;0rad)
  Support = -> [Pad016]
  sketch-geometry (7):
    g0: LineSegment StartX=6.43301 StartY=-0.75 StartZ=0 EndX=6.86603 EndY=0 EndZ=0
    g1: LineSegment StartX=6.86603 StartY=0 StartZ=0 EndX=6.43301 EndY=0.75 EndZ=0
    g2: LineSegment StartX=6.43301 StartY=0.75 StartZ=0 EndX=5.56699 EndY=0.75 EndZ=0
    g3: LineSegment StartX=5.56699 StartY=0.75 StartZ=0 EndX=5.13397 EndY=-1e-16 EndZ=0
    g4: LineSegment StartX=5.13397 StartY=-1e-16 StartZ=0 EndX=5.56699 EndY=-0.75 EndZ=0
    g5: LineSegment StartX=5.56699 StartY=-0.75 StartZ=0 EndX=6.43301 EndY=-0.75 EndZ=0
    g6: Circle CenterX=6 CenterY=0 CenterZ=0 NormalX=0 NormalY=0 NormalZ=1 AngleXU=0 Radius=0.866025
  constraints (16):
    c: Coincident(g0,g1)
    c: Coincident(g1,g2)
    c: Coincident(g2,g3)
    c: Coincident(g3,g4)
    c: Coincident(g4,g5)
    c: Coincident(g5,g0)
    c: Equal(g0, g1-g5) x5
    c: PointOnObject(g0,g6)
    c: PointOnObject(g1,g6)
    c: PointOnObject(g2,g6)
    c: PointOnObject(g3,g6)
    c: PointOnObject(g4,g6)
    c: PointOnObject(g5,g6)
    c: Coincident(g6,g-3)
    c: Horizontal(g5)
    c: DistanceY(g4,g2) = 1.5
FEATURE [PartDesign::Pocket] Pocket012
  BaseFeature = -> Pad016
  Length = 0.9
  Length2 = 100
  Profile = -> Sketch052
  Type = 0
FEATURE [PartDesign::PolarPattern] PolarPattern007
  Angle = 120
  Axis = -> X_Axis050
  BaseFeature = -> Pocket012
  Occurrences = 3
  Originals = -> [Pad016,Pocket012]
FEATURE [PartDesign::Body] Body036
  Group = -> [Sketch051,Pad016,Sketch052,Pocket012,PolarPattern007]
  Origin = -> Origin051
  Tip = -> PolarPattern007
FEATURE [App::DocumentObjectGroup] Group012  label="Set screws001"
  Group = -> [Body036]
FEATURE [Sketcher::SketchObject] Sketch053
  AttachmentOffset = pos=(0,0,-6.5) rot=(0,0,1;0rad)
  FullyConstrained = true
  MapMode = 5
  Placement = pos=(-6.5,1.4e-15,-1.4e-15) rot=(0.57735,0.57735,0.57735;2.0944rad)
  Support = -> [YZ_Plane071]
  sketch-geometry (14):
    g0: Circle CenterX=0 CenterY=0 CenterZ=0 NormalX=0 NormalY=0 NormalZ=1 AngleXU=0 Radius=11
    g1: ArcOfCircle CenterX=0 CenterY=0 CenterZ=0 NormalX=0 NormalY=0 NormalZ=1 AngleXU=0 Radius=13.5 StartAngle=0.0668757 EndAngle=3.07472
    g2: LineSegment StartX=-13.4698 StartY=0.902148 StartZ=0 EndX=-14.2 EndY=-10 EndZ=0
    g3: LineSegment StartX=-14.2 StartY=-10 StartZ=0 EndX=-27.5 EndY=-10 EndZ=0
    g4: LineSegment StartX=-27.5 StartY=-10 StartZ=0 EndX=-27.5 EndY=-15 EndZ=0
    g5: LineSegment StartX=-27.5 StartY=-15 StartZ=0 EndX=-12.3 EndY=-15 EndZ=0
    g6: LineSegment StartX=27.5 StartY=-15 StartZ=0 EndX=27.5 EndY=-10 EndZ=0
    g7: LineSegment StartX=27.5 StartY=-10 StartZ=0 EndX=14.2 EndY=-10 EndZ=0
    g8: LineSegment StartX=14.2 StartY=-10 StartZ=0 EndX=13.4698 EndY=0.902148 EndZ=0
    g9: LineSegment StartX=12.3 StartY=-15 StartZ=0 EndX=12.1995 EndY=-13.5 EndZ=0
    g10: LineSegment StartX=12.1995 StartY=-13.5 StartZ=0 EndX=-12.1995 EndY=-13.5 EndZ=0
    g11: LineSegment StartX=-12.1995 StartY=-13.5 StartZ=0 EndX=-12.3 EndY=-15 EndZ=0
    g12: LineSegment StartX=12.3 StartY=-15 StartZ=0 EndX=27.5 EndY=-15 EndZ=0
    g13: GeomPoint X=0 Y=13.5 Z=0
  constraints (39):
    c: Coincident(g0,g-1)
    c: Radius(g0) = 11
    c: Coincident(g1,g0)
    c: Coincident(g2,g3)
    c: Coincident(g3,g4)
    c: Coincident(g4,g5)
    c: Horizontal(g5)
    c: Coincident(g12,g6)
    c: Coincident(g6,g7)
    c: Horizontal(g7)
    c: Coincident(g7,g8)
    c: Coincident(g9,g10)
    c: Horizontal(g10)
    c: Coincident(g10,g11)
    c: Coincident(g5,g11)
    c: Coincident(g12,g9)
    c: Horizontal(g3)
    c: Vertical(g6)
    c: Vertical(g4)
    c: Equal(g9,g11)
    c: Horizontal(g12)
    c: Horizontal(g5,g9)
    c: Equal(g6,g4)
    c: Equal(g12,g5)
    c: Equal(g7,g3)
    c: DistanceX(g4,g6) = 55
    c: DistanceY(g6,g0) = 15
    c: Equal(g8,g2)
    c: DistanceY(g6,g6) = 5
    c: Parallel(g9,g8)
    c: DistanceY(g9,g9) = 1.5
    c: DistanceX(g5,g5) = 15.2
    c: Diameter(g1) = 27
    c: PointOnObject(g13,g1)
    c: PointOnObject(g13,g-2)
    c: DistanceY(g6,g13) = 28.5
    c: Tangent(g1,g2) = -1.5708
    c: Tangent(g1,g8) = -1.5708
    c: DistanceX(g3,g3) = 13.3
FEATURE [PartDesign::Pad] Pad017
  Direction = (1,-2e-16,3e-16)
  Length = 13
  Length2 = 100
  Placement = pos=(0,0,0) rot=(0.57735,0.57735,0.57735;2.0944rad)
  Profile = -> Sketch053
  Type = 0
FEATURE [Sketcher::SketchObject] Sketch054
  ExternalGeometry = -> [Pad017]
  FullyConstrained = true
  MapMode = 5
  Placement = pos=(4.2e-15,-6.6e-15,-15) rot=(0.707107,0.707107,0;3.14159rad)
  Support = -> [Pad017]
  sketch-geometry (7):
    g0: LineSegment StartX=-24.9 StartY=4.15 StartZ=0 EndX=-14.9 EndY=4.15 EndZ=0
    g1: LineSegment StartX=-14.9 StartY=4.15 StartZ=0 EndX=-14.9 EndY=-4.15 EndZ=0
    g2: LineSegment StartX=-14.9 StartY=-4.15 StartZ=0 EndX=-24.9 EndY=-4.15 EndZ=0
    g3: LineSegment StartX=-24.9 StartY=-4.15 StartZ=0 EndX=-24.9 EndY=4.15 EndZ=0
    g4: LineSegment StartX=-27.5 StartY=6.5 StartZ=0 EndX=-12.3 EndY=-6.5 EndZ=0
    g5: LineSegment StartX=-27.5 StartY=-6.5 StartZ=0 EndX=-12.3 EndY=6.5 EndZ=0
    g6: GeomPoint X=-19.9 Y=2.6e-15 Z=0
  constraints (17):
    c: Coincident(g0,g1)
    c: Coincident(g1,g2)
    c: Coincident(g2,g3)
    c: Coincident(g3,g0)
    c: Horizontal(g0)
    c: Horizontal(g2)
    c: Vertical(g1)
    c: Vertical(g3)
    c: DistanceX(g0,g0) = 10
    c: DistanceY(g1,g1) = 8.3
    c: Coincident(g4,g-3)
    c: Coincident(g4,g-4)
    c: Coincident(g5,g-4)
    c: Coincident(g5,g-3)
    c: PointOnObject(g6,g4)
    c: PointOnObject(g6,g5)
    c: Symmetric(g0,g1,g6)
FEATURE [PartDesign::Pocket] Pocket013
  BaseFeature = -> Pad017
  Length = 2.3
  Length2 = 100
  Placement = pos=(0,0,0) rot=(0.57735,0.57735,0.57735;2.0944rad)
  Profile = -> Sketch054
  Type = 0
FEATURE [Sketcher::SketchObject] Sketch055
  ExternalGeometry = -> [Pocket013]
  FullyConstrained = true
  MapMode = 5
  Placement = pos=(2.8e-15,-4.4e-15,-10) rot=(0,0,-1;1.5708rad)
  Support = -> [Pocket013]
  sketch-geometry (2):
    g0: Circle CenterX=21.2 CenterY=2.1e-15 CenterZ=0 NormalX=0 NormalY=0 NormalZ=1 AngleXU=0 Radius=2.5
    g1: LineSegment StartX=21.2 StartY=2.1e-15 StartZ=0 EndX=27.5 EndY=2.1e-15 EndZ=0
  constraints (5):
    c: Diameter(g0) = 5
    c: DistanceX(g0,g-3) = 6.3
    c: Coincident(g1,g0)
    c: Horizontal(g1)
    c: Symmetric(g-5,g-5,g1)
FEATURE [PartDesign::Pocket] Pocket014
  BaseFeature = -> Pocket013
  Length = 5
  Length2 = 100
  Placement = pos=(0,0,0) rot=(0.57735,0.57735,0.57735;2.0944rad)
  Profile = -> Sketch055
  Type = 2
FEATURE [Sketcher::SketchObject] Sketch056
  ExternalGeometry = -> [Pocket014]
  FullyConstrained = true
  MapMode = 5
  Placement = pos=(6.5,-1.4e-15,1.5e-15) rot=(0.57735,0.57735,0.57735;2.0944rad)
  Support = -> [Pocket014]
  sketch-geometry (6):
    g0: LineSegment StartX=-24.6 StartY=-13.7 StartZ=0 EndX=-24.6 EndY=-11.3 EndZ=0
    g1: LineSegment StartX=-24.6 StartY=-11.3 StartZ=0 EndX=-14.2 EndY=-11.3 EndZ=0
    g2: LineSegment StartX=-14.2 StartY=-11.3 StartZ=0 EndX=-14.2 EndY=-13.7 EndZ=0
    g3: LineSegment StartX=-14.2 StartY=-13.7 StartZ=0 EndX=-24.6 EndY=-13.7 EndZ=0
    g4: GeomPoint X=-19.4 Y=-12.5 Z=0
    g5: LineSegment StartX=-19.4 StartY=-12.5 StartZ=0 EndX=-27.5 EndY=-12.5 EndZ=0
  constraints (15):
    c: Coincident(g0,g1)
    c: Coincident(g1,g2)
    c: Coincident(g2,g3)
    c: Coincident(g3,g0)
    c: Horizontal(g1)
    c: Horizontal(g3)
    c: Vertical(g0)
    c: Vertical(g2)
    c: Symmetric(g1,g0,g4)
    c: DistanceX(g1,g1) = 10.4
    c: DistanceY(g2,g2) = 2.4
    c: DistanceX(g2,g-4) = 1.9
    c: Coincident(g5,g4)
    c: Horizontal(g5)
    c: Symmetric(g-5,g-5,g5)
FEATURE [PartDesign::Pocket] Pocket015
  BaseFeature = -> Pocket014
  Length = 0.4
  Length2 = 100
  Placement = pos=(0,0,0) rot=(0.57735,0.57735,0.57735;2.0944rad)
  Profile = -> Sketch056
  Type = 0
FEATURE [PartDesign::Mirrored] Mirrored001
  BaseFeature = -> Pocket015
  MirrorPlane = -> Sketch054 [V_Axis]
  Originals = -> [Pocket013,Pocket014,Pocket015]
  Placement = pos=(0,0,0) rot=(0.57735,0.57735,0.57735;2.0944rad)
FEATURE [Sketcher::SketchObject] Sketch057
  ExternalGeometry = -> [Mirrored001]
  FullyConstrained = true
  MapMode = 5
  Placement = pos=(0,0,0) rot=(1,0,0;1.5708rad)
  Support = -> [XZ_Plane071]
  sketch-geometry (9):
    g0: GeomPoint X=-6.5 Y=13.5 Z=0
    g1: LineSegment StartX=6.5 StartY=-10 StartZ=0 EndX=6.5 EndY=13.5 EndZ=0
    g2: LineSegment StartX=6.5 StartY=13.5 StartZ=0 EndX=4.75 EndY=13.5 EndZ=0
    g3: LineSegment StartX=-6.5 StartY=13.5 StartZ=0 EndX=-4.75 EndY=13.5 EndZ=0
    g4: LineSegment StartX=-6.5 StartY=-10 StartZ=0 EndX=-6.5 EndY=13.5 EndZ=0
    g5: LineSegment StartX=6.5 StartY=-10 StartZ=0 EndX=4.75 EndY=-1 EndZ=0
    g6: LineSegment StartX=4.75 StartY=-1 StartZ=0 EndX=4.75 EndY=13.5 EndZ=0
    g7: LineSegment StartX=-4.75 StartY=13.5 StartZ=0 EndX=-4.75 EndY=-1 EndZ=0
    g8: LineSegment StartX=-4.75 StartY=-1 StartZ=0 EndX=-6.5 EndY=-10 EndZ=0
  constraints (24):
    c: Vertical(g0,g-4)
    c: Horizontal(g-3,g0)
    c: Coincident(g1,g-3)
    c: Coincident(g1,g2)
    c: Horizontal(g2)
    c: Coincident(g3,g0)
    c: Horizontal(g3)
    c: Coincident(g4,g3)
    c: Vertical(g4,g-4)
    c: DistanceX(g3,g2) = 9.5
    c: Equal(g2,g3)
    c: Horizontal(g1,g4)
    c: Coincident(g1,g-5)
    c: Coincident(g1,g5)
    c: Coincident(g5,g6)
    c: Coincident(g6,g2)
    c: Vertical(g6)
    c: DistanceY(g1,g5) = 9
    c: Coincident(g3,g7)
    c: Vertical(g7)
    c: Coincident(g7,g8)
    c: Coincident(g8,g4)
    c: Horizontal(g7,g5)
    c: DistanceX(g2,g2) = 1.75
FEATURE [PartDesign::Pocket] Pocket016
  BaseFeature = -> Mirrored001
  Length = 15
  Length2 = 15
  Placement = pos=(0,0,0) rot=(0.57735,0.57735,0.57735;2.0944rad)
  Profile = -> Sketch057
  Type = 4
FEATURE [Sketcher::SketchObject] Sketch058
  FullyConstrained = true
  MapMode = 5
  Placement = pos=(-6.5,1.4e-15,-1.5e-15) rot=(0.57735,0.57735,-0.57735;4.18879rad)
  Support = -> [Pocket016]
  sketch-geometry (1):
    g0: Circle CenterX=0 CenterY=0 CenterZ=0 NormalX=0 NormalY=0 NormalZ=1 AngleXU=0 Radius=12.2
  constraints (2):
    c: Coincident(g0,g-1)
    c: Diameter(g0) = 24.4
FEATURE [PartDesign::Pocket] Pocket017
  BaseFeature = -> Pocket016
  Length = 2.75
  Length2 = 100
  Placement = pos=(0,0,0) rot=(0.57735,0.57735,0.57735;2.0944rad)
  Profile = -> Sketch058
  Type = 0
FEATURE [Sketcher::SketchObject] Sketch059
  FullyConstrained = true
  MapMode = 5
  Placement = pos=(6.5,-1.4e-15,1.5e-15) rot=(0.57735,0.57735,0.57735;2.0944rad)
  Support = -> [Pocket017]
  sketch-geometry (1):
    g0: Circle CenterX=0 CenterY=0 CenterZ=0 NormalX=0 NormalY=0 NormalZ=1 AngleXU=0 Radius=12.1
  constraints (2):
    c: Coincident(g0,g-1)
    c: Diameter(g0) = 24.2
FEATURE [PartDesign::Pocket] Pocket018
  BaseFeature = -> Pocket017
  Length = 2.75
  Length2 = 100
  Placement = pos=(0,0,0) rot=(0.57735,0.57735,0.57735;2.0944rad)
  Profile = -> Sketch059
  Type = 0
FEATURE [Sketcher::SketchObject] Sketch060
  ExternalGeometry = -> [Pocket018]
  FullyConstrained = true
  MapMode = 5
  Placement = pos=(6.5,-1.4e-15,1.5e-15) rot=(0.57735,0.57735,0.57735;2.0944rad)
  Support = -> [Pocket018]
  sketch-geometry (6):
    g0: ArcOfCircle CenterX=0 CenterY=0 CenterZ=0 NormalX=0 NormalY=0 NormalZ=1 AngleXU=0 Radius=13.5 StartAngle=3.79664 EndAngle=5.62814
    g1: LineSegment StartX=-11.8698 StartY=-8.57666 StartZ=0 EndX=-12.3 EndY=-15 EndZ=0
    g2: LineSegment StartX=-12.3 StartY=-15 StartZ=0 EndX=12.3 EndY=-15 EndZ=0
    g3: LineSegment StartX=12.3 StartY=-15 StartZ=0 EndX=11.8698 EndY=-8.57666 EndZ=0
    g4: ArcOfCircle CenterX=11.2212 CenterY=-8.6201 CenterZ=0 NormalX=0 NormalY=0 NormalZ=1 AngleXU=0 Radius=0.65 StartAngle=0.0668757 EndAngle=2.48655
    g5: ArcOfCircle CenterX=-11.2212 CenterY=-8.6201 CenterZ=0 NormalX=0 NormalY=0 NormalZ=1 AngleXU=0 Radius=0.65 StartAngle=0.655044 EndAngle=3.07472
  constraints (14):
    c: Coincident(g0,g-1)
    c: Diameter(g0) = 27
    c: Coincident(g1,g2)
    c: Coincident(g2,g3)
    c: Coincident(g1,g-3)
    c: Coincident(g2,g-4)
    c: Tangent(g3,g4) = -1.5708
    c: Tangent(g0,g4) = 1.5708
    c: Tangent(g0,g5) = 1.5708
    c: Tangent(g1,g5) = -1.5708
    c: Equal(g4,g5)
    c: Horizontal(g4,g5)
    c: Parallel(g-4,g3)
    c: Radius(g4) = 0.65
FEATURE [PartDesign::Pocket] Pocket019
  BaseFeature = -> Pocket018
  Length = 5.25
  Length2 = 100
  Placement = pos=(0,0,0) rot=(0.57735,0.57735,0.57735;2.0944rad)
  Profile = -> Sketch060
  Type = 0
FEATURE [Sketcher::SketchObject] Sketch061
  ExternalGeometry = -> [Pocket019]
  FullyConstrained = true
  MapMode = 5
  Placement = pos=(-6.5,1.4e-15,-1.5e-15) rot=(0.57735,0.57735,-0.57735;4.18879rad)
  Support = -> [Pocket019]
  sketch-geometry (6):
    g0: ArcOfCircle CenterX=0 CenterY=0 CenterZ=0 NormalX=0 NormalY=0 NormalZ=1 AngleXU=0 Radius=13.5 StartAngle=0.655044 EndAngle=2.48655
    g1: LineSegment StartX=11.8698 StartY=8.57666 StartZ=0 EndX=12.3 EndY=15 EndZ=0
    g2: LineSegment StartX=12.3 StartY=15 StartZ=0 EndX=-12.3 EndY=15 EndZ=0
    g3: LineSegment StartX=-12.3 StartY=15 StartZ=0 EndX=-11.8698 EndY=8.57666 EndZ=0
    g4: ArcOfCircle CenterX=-11.2212 CenterY=8.6201 CenterZ=0 NormalX=0 NormalY=0 NormalZ=1 AngleXU=0 Radius=0.65 StartAngle=3.20847 EndAngle=5.62814
    g5: ArcOfCircle CenterX=11.2212 CenterY=8.6201 CenterZ=0 NormalX=0 NormalY=0 NormalZ=1 AngleXU=0 Radius=0.65 StartAngle=3.79664 EndAngle=6.21631
  constraints (14):
    c: Coincident(g0,g-1)
    c: Radius(g0) = 13.5
    c: Coincident(g1,g2)
    c: Coincident(g2,g-3)
    c: Coincident(g2,g3)
    c: Coincident(g-4,g1)
    c: Tangent(g3,g4) = -1.5708
    c: Tangent(g0,g4) = 1.5708
    c: Tangent(g0,g5) = 1.5708
    c: Tangent(g1,g5) = -1.5708
    c: Equal(g4,g5)
    c: Radius(g4) = 0.65
    c: Parallel(g-4,g1)
    c: Parallel(g3,g-3)
FEATURE [PartDesign::Pocket] Pocket020
  BaseFeature = -> Pocket019
  Length = 5.25
  Length2 = 100
  Placement = pos=(0,0,0) rot=(0.57735,0.57735,0.57735;2.0944rad)
  Profile = -> Sketch061
  Type = 0
FEATURE [PartDesign::Chamfer] Chamfer001
  Angle = 45
  Base = -> Pocket020 [Edge159,Edge155,Edge22,Edge27]
  BaseFeature = -> Pocket020
  ChamferType = 0
  FlipDirection = false
  Placement = pos=(0,0,0) rot=(0.57735,0.57735,0.57735;2.0944rad)
  Size = 2
  Size2 = 1
  SupportTransform = false
FEATURE [Sketcher::SketchObject] Sketch062
  ExternalGeometry = -> [Chamfer001]
  FullyConstrained = true
  MapMode = 5
  Placement = pos=(-3.75,5e-15,-2.7e-15) rot=(-0.57735,-0.57735,0.57735;2.0944rad)
  Support = -> [Chamfer001]
  sketch-geometry (13):
    g0: ArcOfCircle CenterX=-6.9e-15 CenterY=-3.7e-15 CenterZ=0 NormalX=0 NormalY=0 NormalZ=1 AngleXU=0 Radius=11 StartAngle=5.75419 EndAngle=6.81218
    g1: ArcOfCircle CenterX=-6.9e-15 CenterY=-3.7e-15 CenterZ=0 NormalX=0 NormalY=0 NormalZ=1 AngleXU=0 Radius=12.2 StartAngle=5.94045 EndAngle=6.62592
    g2: ArcOfCircle CenterX=-6.9e-15 CenterY=-3.7e-15 CenterZ=0 NormalX=0 NormalY=0 NormalZ=1 AngleXU=0 Radius=11 StartAngle=2.6126 EndAngle=3.67059
    g3: ArcOfCircle CenterX=-6.9e-15 CenterY=-3.7e-15 CenterZ=0 NormalX=0 NormalY=0 NormalZ=1 AngleXU=0 Radius=12.2 StartAngle=2.79886 EndAngle=3.48433
    g4: Ellipse CenterX=-6.9e-15 CenterY=-3.7e-15 CenterZ=0 NormalX=0 NormalY=0 NormalZ=1 MajorRadius=13.5 MinorRadius=7.81051 AngleXU=-3e-16
    g5: LineSegment StartX=13.5 StartY=-7.4e-15 StartZ=0 EndX=-13.5 EndY=0 EndZ=0
    g6: LineSegment StartX=-4.8e-15 StartY=7.81051 StartZ=0 EndX=-9.1e-15 EndY=-7.81051 EndZ=0
    g7: GeomPoint X=11.0112 Y=-6.8e-15 Z=0
    g8: GeomPoint X=-11.0112 Y=-7e-16 Z=0
    g9: LineSegment StartX=-11.4904 StartY=4.1 StartZ=0 EndX=-9.49645 EndY=5.55135 EndZ=0
    g10: LineSegment StartX=-11.4904 StartY=-4.1 StartZ=0 EndX=-9.49645 EndY=-5.55135 EndZ=0
    g11: LineSegment StartX=9.49645 StartY=-5.55135 StartZ=0 EndX=11.4904 EndY=-4.1 EndZ=0
    g12: LineSegment StartX=11.4904 StartY=4.1 StartZ=0 EndX=9.49645 EndY=5.55135 EndZ=0
  constraints (29):
    c: Coincident(g0,g-4)
    c: PointOnObject(g0,g-4)
    c: Coincident(g1,g0)
    c: PointOnObject(g1,g-3)
    c: Coincident(g2,g0)
    c: PointOnObject(g2,g-4)
    c: Coincident(g3,g0)
    c: PointOnObject(g3,g-3)
    c: InternalAlignment(g5-g8 -> g4) x4
    c: Coincident(g4,g0)
    c: PointOnObject(g3,g4)
    c: PointOnObject(g2,g4)
    c: PointOnObject(g3,g4)
    c: PointOnObject(g2,g4)
    c: PointOnObject(g0,g4)
    c: PointOnObject(g1,g4)
    c: PointOnObject(g1,g4)
    c: PointOnObject(g0,g4)
    c: PointOnObject(g5,g-1)
    c: DistanceX(g5,g5) = 27
    c: DistanceY(g3,g3) = 8.2
    c: Coincident(g9,g3)
    c: Coincident(g9,g2)
    c: Coincident(g10,g3)
    c: Coincident(g10,g2)
    c: Coincident(g11,g0)
    c: Coincident(g11,g1)
    c: Coincident(g12,g1)
    c: Coincident(g12,g0)
FEATURE [PartDesign::Pocket] Pocket021
  BaseFeature = -> Chamfer001
  Length = 5
  Length2 = 100
  Placement = pos=(0,0,0) rot=(0.57735,0.57735,0.57735;2.0944rad)
  Profile = -> Sketch062
  Type = 0
FEATURE [PartDesign::Body] Body057  label="Metal case001"
  Group = -> [Sketch053,Pad017,Sketch054,Pocket013,Sketch055,Pocket014,Sketch056,Pocket015,Mirrored001,Sketch057,Pocket016,Sketch058,Pocket017,Sketch059,Pocket018,Sketch060,Pocket019,Sketch061,Pocket020,Chamfer001,Sketch062,Pocket021]
  Origin = -> Origin072
  Tip = -> Pocket021
FEATURE [App::DocumentObjectGroup] Group013  label="Case001"
  Group = -> [Body057]
FEATURE [App::Part] Part015  label="KP08-002"
  Group = -> [Group007,Body038,Body037,Body042,Body039,Body043,Body041,Body040,Group008,Body045,Body044,Group009,Body050,Body049,Body052,Body048,Body051,Body047,Body046,Group010,Body056,Body055,Group011,Body053,Body054,Group012,Body036,Group013,Body057]
  Origin = -> Origin073
  Placement = pos=(10,120,105) rot=(0,0,1;0rad)
FEATURE [Sketcher::SketchObject] Sketch063
  FullyConstrained = true
  MapMode = 5
  Placement = pos=(0,0,0) rot=(-0.57735,0.57735,0.57735;4.18879rad)
  Support = -> [YZ_Plane080]
  sketch-geometry (1):
    g0: Circle CenterX=0 CenterY=-7.5 CenterZ=0 NormalX=0 NormalY=0 NormalZ=1 AngleXU=0 Radius=0.25
  constraints (3):
    c: PointOnObject(g0,g-2)
    c: DistanceY(g0) = -7.5
    c: Diameter(g0) = 0.5
FEATURE [Sketcher::SketchObject] Sketch064
  FullyConstrained = true
  MapMode = 5
  Support = -> [XY_Plane073]
  sketch-geometry (2):
    g0: LineSegment StartX=0 StartY=5.5 StartZ=0 EndX=6e-16 EndY=9.5 EndZ=0
    g1: ArcOfCircle CenterX=0 CenterY=7.5 CenterZ=0 NormalX=0 NormalY=0 NormalZ=1 AngleXU=0 Radius=2 StartAngle=4.71239 EndAngle=7.85398
  constraints (7):
    c: PointOnObject(g0,g-2)
    c: PointOnObject(g0,g-2)
    c: PointOnObject(g1,g0)
    c: Coincident(g1,g0)
    c: Coincident(g1,g0)
    c: Radius(g1) = 2
    c: DistanceY(g1) = 7.5
FEATURE [PartDesign::Revolution] Revolution018
  Angle = 360
  Axis = (0,1,0)
  Base = (0,0,0)
  Profile = -> Sketch064
  ReferenceAxis = -> Sketch064 [V_Axis]
  Reversed = true
FEATURE [PartDesign::Body] Body059  label="Ball 015"
  Group = -> [Sketch064,Revolution018]
  Origin = -> Origin075
  Tip = -> Revolution018
FEATURE [PartDesign::FeatureBase] Clone028
  BaseFeature = -> Body059
FEATURE [PartDesign::Body] Body060  label="Ball 016"
  BaseFeature = -> Body059
  Group = -> [Clone028]
  Origin = -> Origin076
  Placement = pos=(0,0,0) rot=(-1,0,0;0.897598rad)
  Tip = -> Clone028
FEATURE [PartDesign::FeatureBase] Clone029
  BaseFeature = -> Body059
FEATURE [PartDesign::Body] Body061  label="Ball 017"
  BaseFeature = -> Body059
  Group = -> [Clone029]
  Origin = -> Origin077
  Placement = pos=(0,0,0) rot=(-1,0,0;1.7952rad)
  Tip = -> Clone029
FEATURE [PartDesign::FeatureBase] Clone030
  BaseFeature = -> Body059
FEATURE [PartDesign::Body] Body062  label="Ball 018"
  BaseFeature = -> Body059
  Group = -> [Clone030]
  Origin = -> Origin078
  Placement = pos=(0,0,0) rot=(1,0,0;3.59039rad)
  Tip = -> Clone030
FEATURE [PartDesign::FeatureBase] Clone031
  BaseFeature = -> Body059
FEATURE [PartDesign::Body] Body063  label="Ball 019"
  BaseFeature = -> Body059
  Group = -> [Clone031]
  Origin = -> Origin079
  Placement = pos=(0,0,0) rot=(1,0,0;2.69279rad)
  Tip = -> Clone031
FEATURE [PartDesign::FeatureBase] Clone032
  BaseFeature = -> Body059
FEATURE [PartDesign::Body] Body064  label="Ball 020"
  BaseFeature = -> Body059
  Group = -> [Clone032]
  Origin = -> Origin080
  Placement = pos=(0,0,0) rot=(1,0,0;1.7952rad)
  Tip = -> Clone032
FEATURE [PartDesign::FeatureBase] Clone033
  BaseFeature = -> Body059
FEATURE [PartDesign::Body] Body065  label="Ball 021"
  BaseFeature = -> Body059
  Group = -> [Clone033]
  Origin = -> Origin081
  Placement = pos=(0,0,0) rot=(1,0,0;0.897598rad)
  Tip = -> Clone033
FEATURE [App::DocumentObjectGroup] Group014  label="Balls002"
  Group = -> [Body059,Body060,Body061,Body062,Body063,Body064,Body065]
FEATURE [Sketcher::SketchObject] Sketch065
  FullyConstrained = true
  MapMode = 5
  Support = -> [XY_Plane082]
  sketch-geometry (7):
    g0: LineSegment StartX=-5 StartY=7.5 StartZ=0 EndX=5 EndY=7.5 EndZ=0
    g1: LineSegment StartX=-0.210977 StartY=7.5 StartZ=0 EndX=0.210977 EndY=7.5 EndZ=0
    g2: ArcOfCircle CenterX=0.25 CenterY=7.5 CenterZ=0 NormalX=0 NormalY=0 NormalZ=1 AngleXU=0 Radius=0.460977 StartAngle=2.43297 EndAngle=3.14159
    g3: ArcOfCircle CenterX=-0.25 CenterY=7.5 CenterZ=0 NormalX=0 NormalY=0 NormalZ=1 AngleXU=0 Radius=0.460977 StartAngle=9.792e-13 EndAngle=0.708626
    g4: LineSegment StartX=-0.1 StartY=7.8 StartZ=0 EndX=-0.1 EndY=7.75 EndZ=0
    g5: LineSegment StartX=-0.1 StartY=7.75 StartZ=0 EndX=0.1 EndY=7.75 EndZ=0
    g6: LineSegment StartX=0.1 StartY=7.75 StartZ=0 EndX=0.1 EndY=7.8 EndZ=0
  constraints (22):
    c: DistanceY(g-1,g0) = 7.5
    c: Symmetric(g0,g0,g-2)
    c: DistanceX(g0,g0) = 10
    c: PointOnObject(g1,g0)
    c: PointOnObject(g1,g0)
    c: Coincident(g3,g1)
    c: Coincident(g2,g1)
    c: Coincident(g2,g4)
    c: Coincident(g4,g5)
    c: Horizontal(g5)
    c: Coincident(g5,g6)
    c: Coincident(g6,g3)
    c: Vertical(g6)
    c: Equal(g3,g2)
    c: Vertical(g4)
    c: Symmetric(g2,g3,g-2)
    c: DistanceX(g5,g5) = 0.2
    c: Distance(g5,g1) = 0.25
    c: DistanceX(g3,g-1) = 0.25
    c: PointOnObject(g3,g1)
    c: PointOnObject(g2,g1)
    c: Distance(g3,g1) = 0.3
FEATURE [PartDesign::Revolution] Revolution019
  Angle = 360
  Axis = (10,0,0)
  Base = (-5,7.5,0)
  Profile = -> Sketch065
  ReferenceAxis = -> Sketch065 [Axis]
FEATURE [PartDesign::Body] Body068  label="Rivet 015"
  Group = -> [Sketch065,Revolution019]
  Origin = -> Origin084
  Placement = pos=(0,0,0) rot=(1,0,0;0.448799rad)
  Tip = -> Revolution019
FEATURE [PartDesign::FeatureBase] Clone035
  BaseFeature = -> Body068
  Placement = pos=(0,0,0) rot=(1,0,0;0.448799rad)
FEATURE [PartDesign::Body] Body069  label="Rivet 016"
  BaseFeature = -> Body068
  Group = -> [Clone035]
  Origin = -> Origin085
  Placement = pos=(0,0,0) rot=(1,0,0;0.897598rad)
  Tip = -> Clone035
FEATURE [PartDesign::FeatureBase] Clone036
  BaseFeature = -> Body068
  Placement = pos=(0,0,0) rot=(1,0,0;0.448799rad)
FEATURE [PartDesign::Body] Body070  label="Rivet 017"
  BaseFeature = -> Body068
  Group = -> [Clone036]
  Origin = -> Origin086
  Placement = pos=(0,0,0) rot=(1,0,0;1.7952rad)
  Tip = -> Clone036
FEATURE [PartDesign::FeatureBase] Clone037
  BaseFeature = -> Body068
  Placement = pos=(0,0,0) rot=(1,0,0;0.448799rad)
FEATURE [PartDesign::Body] Body071  label="Rivet 018"
  BaseFeature = -> Body068
  Group = -> [Clone037]
  Origin = -> Origin087
  Placement = pos=(0,0,0) rot=(1,0,0;2.69279rad)
  Tip = -> Clone037
FEATURE [PartDesign::FeatureBase] Clone038
  BaseFeature = -> Body068
  Placement = pos=(0,0,0) rot=(1,0,0;0.448799rad)
FEATURE [PartDesign::Body] Body072  label="Rivet 019"
  BaseFeature = -> Body068
  Group = -> [Clone038]
  Origin = -> Origin088
  Placement = pos=(0,0,0) rot=(1,0,0;3.59039rad)
  Tip = -> Clone038
FEATURE [PartDesign::FeatureBase] Clone039
  BaseFeature = -> Body068
  Placement = pos=(0,0,0) rot=(1,0,0;0.448799rad)
FEATURE [PartDesign::Body] Body073  label="Rivet 020"
  BaseFeature = -> Body068
  Group = -> [Clone039]
  Origin = -> Origin089
  Placement = pos=(0,0,0) rot=(-1,0,0;1.7952rad)
  Tip = -> Clone039
FEATURE [PartDesign::FeatureBase] Clone040
  BaseFeature = -> Body068
  Placement = pos=(0,0,0) rot=(1,0,0;0.448799rad)
FEATURE [PartDesign::Body] Body074  label="Rivet 021"
  BaseFeature = -> Body068
  Group = -> [Clone040]
  Origin = -> Origin090
  Placement = pos=(0,0,0) rot=(-1,0,0;0.897598rad)
  Tip = -> Clone040
FEATURE [App::DocumentObjectGroup] Group016  label="Rivets002"
  Group = -> [Body068,Body069,Body070,Body071,Body072,Body073,Body074]
FEATURE [Sketcher::SketchObject] Sketch066
  FullyConstrained = true
  MapMode = 5
  Placement = pos=(0,0,0) rot=(1,0,0;1.5708rad)
  Support = -> [XZ_Plane080]
  sketch-geometry (4):
    g0: LineSegment StartX=0 StartY=8.5 StartZ=0 EndX=0.1 EndY=8.5 EndZ=0
    g1: LineSegment StartX=0.1 StartY=8.5 StartZ=0 EndX=0.1 EndY=6.5 EndZ=0
    g2: LineSegment StartX=0.1 StartY=6.5 StartZ=0 EndX=0 EndY=6.5 EndZ=0
    g3: LineSegment StartX=0 StartY=6.5 StartZ=0 EndX=0 EndY=8.5 EndZ=0
  constraints (12):
    c: Coincident(g0,g1)
    c: Coincident(g1,g2)
    c: Coincident(g2,g3)
    c: Coincident(g3,g0)
    c: Horizontal(g0)
    c: Horizontal(g2)
    c: Vertical(g1)
    c: Vertical(g3)
    c: PointOnObject(g0,g-2)
    c: DistanceX(g0,g0) = 0.1
    c: DistanceY(g0) = 8.5
    c: DistanceY(g1) = 6.5
FEATURE [PartDesign::Revolution] Revolution020
  Angle = 360
  Axis = (1,0,0)
  Base = (0,0,0)
  Placement = pos=(0,0,0) rot=(1,0,0;1.5708rad)
  Profile = -> Sketch066
  ReferenceAxis = -> Sketch066 [H_Axis]
FEATURE [Sketcher::SketchObject] Sketch067
  FullyConstrained = true
  MapMode = 5
  Placement = pos=(0,0,0) rot=(0.57735,0.57735,0.57735;2.0944rad)
  Support = -> [YZ_Plane080]
  sketch-geometry (5):
    g0: ArcOfCircle CenterX=0 CenterY=7.5 CenterZ=0 NormalX=0 NormalY=0 NormalZ=1 AngleXU=0 Radius=2.11 StartAngle=5.66076 EndAngle=6.65667
    g1: LineSegment StartX=5e-16 StartY=8.5 StartZ=0 EndX=0 EndY=6.26986 EndZ=0
    g2: ArcOfCircle CenterX=0 CenterY=0 CenterZ=0 NormalX=0 NormalY=0 NormalZ=1 AngleXU=0 Radius=6.5 StartAngle=1.3039 EndAngle=1.5708
    g3: LineSegment StartX=1.71431 StartY=6.26986 StartZ=0 EndX=0 EndY=6.26986 EndZ=0
    g4: ArcOfCircle CenterX=0 CenterY=0 CenterZ=0 NormalX=0 NormalY=0 NormalZ=1 AngleXU=0 Radius=8.5 StartAngle=1.33757 EndAngle=1.5708
  constraints (16):
    c: PointOnObject(g0,g-2)
    c: DistanceY(g0) = 7.5
    c: Radius(g0) = 2.11
    c: PointOnObject(g2,g1)
    c: DistanceY(g2) = 6.5
    c: Coincident(g2,g-1)
    c: Coincident(g3,g2)
    c: Horizontal(g3)
    c: Coincident(g0,g2)
    c: Coincident(g1,g3)
    c: PointOnObject(g1,g-2)
    c: PointOnObject(g1,g-2)
    c: Coincident(g4,g-1)
    c: Coincident(g4,g1)
    c: DistanceY(g1) = 8.5
    c: Coincident(g0,g4)
FEATURE [PartDesign::Revolution] Revolution021
  Angle = 180
  Axis = (-2e-16,3e-16,1)
  Base = (0,0,0)
  BaseFeature = -> Revolution020
  Placement = pos=(0,0,0) rot=(1,0,0;1.5708rad)
  Profile = -> Sketch067
  ReferenceAxis = -> Sketch067 [V_Axis]
  Reversed = true
FEATURE [PartDesign::PolarPattern] PolarPattern008
  Angle = 360
  Axis = -> Sketch067 [N_Axis]
  BaseFeature = -> Revolution021
  Occurrences = 3
  Originals = -> [Revolution021]
  Placement = pos=(0,0,0) rot=(1,0,0;1.5708rad)
  Refine = true
FEATURE [Sketcher::SketchObject] Sketch068
  FullyConstrained = true
  MapMode = 5
  Placement = pos=(0,0,0) rot=(0.57735,0.57735,0.57735;2.0944rad)
  Support = -> [YZ_Plane080]
  sketch-geometry (4):
    g0: ArcOfCircle CenterX=0 CenterY=7.5 CenterZ=0 NormalX=0 NormalY=0 NormalZ=1 AngleXU=0 Radius=2.01 StartAngle=5.57985 EndAngle=6.86228
    g1: LineSegment StartX=0 StartY=6.2 StartZ=0 EndX=1.533 EndY=6.2 EndZ=0
    g2: LineSegment StartX=0 StartY=8.6 StartZ=0 EndX=0 EndY=6.2 EndZ=0
    g3: LineSegment StartX=0 StartY=8.6 StartZ=0 EndX=1.68229 EndY=8.6 EndZ=0
  constraints (13):
    c: PointOnObject(g0,g-2)
    c: DistanceY(g0) = 7.5
    c: Radius(g0) = 2.01
    c: PointOnObject(g1,g-2)
    c: Horizontal(g1)
    c: Coincident(g0,g1)
    c: DistanceY(g1) = 6.2
    c: DistanceY(g2) = 8.6
    c: Coincident(g2,g1)
    c: PointOnObject(g2,g-2)
    c: Coincident(g3,g2)
    c: Horizontal(g3)
    c: Coincident(g0,g3)
FEATURE [PartDesign::Groove] Groove002
  Angle = 360
  Axis = (-2e-16,3e-16,1)
  Base = (0,0,0)
  BaseFeature = -> PolarPattern008
  Placement = pos=(0,0,0) rot=(1,0,0;1.5708rad)
  Profile = -> Sketch068
  ReferenceAxis = -> Sketch068 [V_Axis]
FEATURE [PartDesign::PolarPattern] PolarPattern009
  Angle = 360
  Axis = -> Sketch068 [N_Axis]
  BaseFeature = -> Groove002
  Occurrences = 3
  Originals = -> [Groove002]
  Placement = pos=(0,0,0) rot=(1,0,0;1.5708rad)
FEATURE [PartDesign::Pocket] Pocket022
  BaseFeature = -> PolarPattern009
  Length = 5
  Length2 = 100
  Placement = pos=(0,0,0) rot=(1,0,0;1.5708rad)
  Profile = -> Sketch063
  Type = 1
FEATURE [PartDesign::PolarPattern] PolarPattern010
  Angle = 360
  Axis = -> Sketch063 [N_Axis]
  BaseFeature = -> Pocket022
  Occurrences = 3
  Originals = -> [Pocket022]
  Placement = pos=(0,0,0) rot=(1,0,0;1.5708rad)
FEATURE [PartDesign::Body] Body066  label="Cage 005"
  Group = -> [Sketch066,Revolution020,Sketch067,Revolution021,PolarPattern008,Sketch068,Groove002,PolarPattern009,Sketch063,Pocket022,PolarPattern010]
  Origin = -> Origin082
  Placement = pos=(0,0,0) rot=(-1,0,0;1.5708rad)
  Tip = -> PolarPattern010
FEATURE [PartDesign::FeatureBase] Clone034
  BaseFeature = -> Body066
  Placement = pos=(0,0,0) rot=(-1,0,0;1.5708rad)
FEATURE [PartDesign::Body] Body067  label="Cage 006"
  BaseFeature = -> Body066
  Group = -> [Clone034]
  Origin = -> Origin083
  Placement = pos=(0,0,0) rot=(0,1,0;3.14159rad)
  Tip = -> Clone034
FEATURE [App::DocumentObjectGroup] Group015  label="Cages002"
  Group = -> [Body066,Body067]
FEATURE [Sketcher::SketchObject] Sketch069
  FullyConstrained = true
  MapMode = 5
  Support = -> [XY_Plane089]
  sketch-geometry (14):
    g0: ArcOfCircle CenterX=-1e-16 CenterY=7.5 CenterZ=0 NormalX=0 NormalY=0 NormalZ=1 AngleXU=0 Radius=2 StartAngle=0.848062 EndAngle=2.29353
    g1: LineSegment StartX=-3.5 StartY=11 StartZ=0 EndX=3.5 EndY=11 EndZ=0
    g2: LineSegment StartX=3.5 StartY=11 StartZ=0 EndX=3.5 EndY=9.2 EndZ=0
    g3: LineSegment StartX=2.9 StartY=9 StartZ=0 EndX=1.32288 EndY=9 EndZ=0
    g4: LineSegment StartX=-3.5 StartY=9.2 StartZ=0 EndX=-3.5 EndY=11 EndZ=0
    g5: LineSegment StartX=-1.32288 StartY=9 StartZ=0 EndX=-2.9 EndY=9 EndZ=0
    g6: LineSegment StartX=2.9 StartY=9 StartZ=0 EndX=2.9 EndY=9.5 EndZ=0
    g7: LineSegment StartX=2.9 StartY=9.5 StartZ=0 EndX=3.2 EndY=9.5 EndZ=0
    g8: LineSegment StartX=3.2 StartY=9.5 StartZ=0 EndX=3.2 EndY=9.2 EndZ=0
    g9: LineSegment StartX=3.2 StartY=9.2 StartZ=0 EndX=3.5 EndY=9.2 EndZ=0
    g10: LineSegment StartX=-3.5 StartY=9.2 StartZ=0 EndX=-3.2 EndY=9.2 EndZ=0
    g11: LineSegment StartX=-3.2 StartY=9.2 StartZ=0 EndX=-3.2 EndY=9.5 EndZ=0
    g12: LineSegment StartX=-3.2 StartY=9.5 StartZ=0 EndX=-2.9 EndY=9.5 EndZ=0
    g13: LineSegment StartX=-2.9 StartY=9.5 StartZ=0 EndX=-2.9 EndY=9 EndZ=0
  constraints (41):
    c: Coincident(g1,g2)
    c: Coincident(g4,g1)
    c: Horizontal(g3)
    c: Vertical(g2)
    c: Vertical(g4)
    c: Coincident(g0,g5)
    c: Coincident(g0,g3)
    c: DistanceY(g-1,g0) = 7.5
    c: Radius(g0) = 2
    c: Symmetric(g1,g1,g-2)
    c: Symmetric(g0,g0,g-2)
    c: DistanceY(g1) = 11
    c: DistanceX(g1,g1) = 7
    c: Vertical(g6)
    c: Coincident(g6,g7)
    c: Horizontal(g7)
    c: Coincident(g7,g8)
    c: Vertical(g8)
    c: Coincident(g8,g9)
    c: Coincident(g3,g6)
    c: Coincident(g2,g9)
    c: Horizontal(g10)
    c: Coincident(g10,g11)
    c: Coincident(g11,g12)
    c: Horizontal(g12)
    c: Coincident(g12,g13)
    c: Vertical(g13)
    c: Vertical(g11)
    c: Coincident(g4,g10)
    c: Coincident(g5,g13)
    c: DistanceY(g13,g13) = 0.5
    c: DistanceX(g12,g12) = 0.3
    c: DistanceY(g5,g10) = 0.2
    c: Symmetric(g5,g3,g-2)
    c: DistanceY(g3) = 9
    c: DistanceY(g6) = 9.5
    c: Equal(g7,g12)
    c: Equal(g13,g6)
    c: Horizontal(g9)
    c: Horizontal(g8,g10)
    c: Equal(g12,g10)
FEATURE [PartDesign::Revolution] Revolution022
  Angle = 360
  Axis = (1,0,0)
  Base = (0,0,0)
  Profile = -> Sketch069
  ReferenceAxis = -> X_Axis089
FEATURE [PartDesign::Fillet] Fillet160
  Base = -> Revolution022 [Edge14,Edge15]
  BaseFeature = -> Revolution022
  Radius = 0.3
  SupportTransform = false
FEATURE [PartDesign::Body] Body075  label="Outer Ring003"
  Group = -> [Sketch069,Revolution022,Fillet160]
  Origin = -> Origin091
  Tip = -> Fillet160
FEATURE [Sketcher::SketchObject] Sketch070
  FullyConstrained = true
  MapMode = 5
  Support = -> [XY_Plane090]
  sketch-geometry (14):
    g0: LineSegment StartX=-2.9 StartY=6 StartZ=0 EndX=-1.32288 EndY=6 EndZ=0
    g1: LineSegment StartX=-3.5 StartY=4 StartZ=0 EndX=-3.5 EndY=5.7 EndZ=0
    g2: ArcOfCircle CenterX=-1e-16 CenterY=7.5 CenterZ=0 NormalX=0 NormalY=0 NormalZ=1 AngleXU=0 Radius=2 StartAngle=3.98965 EndAngle=5.43512
    g3: LineSegment StartX=1.32288 StartY=6 StartZ=0 EndX=2.9 EndY=6 EndZ=0
    g4: LineSegment StartX=-3.5 StartY=5.7 StartZ=0 EndX=-3.2 EndY=5.7 EndZ=0
    g5: LineSegment StartX=-3.2 StartY=5.7 StartZ=0 EndX=-3.2 EndY=5.5 EndZ=0
    g6: LineSegment StartX=-3.2 StartY=5.5 StartZ=0 EndX=-2.9 EndY=5.5 EndZ=0
    g7: LineSegment StartX=-2.9 StartY=5.5 StartZ=0 EndX=-2.9 EndY=6 EndZ=0
    g8: LineSegment StartX=8.5 StartY=6 StartZ=0 EndX=3.2 EndY=6 EndZ=0
    g9: LineSegment StartX=3.2 StartY=6 StartZ=0 EndX=3.2 EndY=5.5 EndZ=0
    g10: LineSegment StartX=3.2 StartY=5.5 StartZ=0 EndX=2.9 EndY=5.5 EndZ=0
    g11: LineSegment StartX=2.9 StartY=5.5 StartZ=0 EndX=2.9 EndY=6 EndZ=0
    g12: LineSegment StartX=8.5 StartY=4 StartZ=0 EndX=8.5 EndY=6 EndZ=0
    g13: LineSegment StartX=-3.5 StartY=4 StartZ=0 EndX=8.5 EndY=4 EndZ=0
  constraints (43):
    c: Horizontal(g0)
    c: Vertical(g1)
    c: DistanceY(g1) = 4
    c: Coincident(g2,g0)
    c: Coincident(g2,g3)
    c: Horizontal(g3)
    c: Radius(g2) = 2
    c: DistanceY(g2) = 7.5
    c: Symmetric(g0,g2,g-2)
    c: Horizontal(g4)
    c: Coincident(g4,g5)
    c: Vertical(g5)
    c: Coincident(g5,g6)
    c: Horizontal(g6)
    c: Coincident(g6,g7)
    c: Vertical(g7)
    c: Horizontal(g8)
    c: Coincident(g8,g9)
    c: Vertical(g9)
    c: Coincident(g9,g10)
    c: Horizontal(g10)
    c: Coincident(g10,g11)
    c: Vertical(g11)
    c: Coincident(g3,g11)
    c: Coincident(g0,g7)
    c: Coincident(g1,g4)
    c: DistanceY(g3) = 6
    c: DistanceY(g6,g0) = 0.5
    c: DistanceX(g4,g4) = 0.3
    c: DistanceX(g6,g6) = 0.3
    c: DistanceY(g5,g4) = 0.2
    c: Vertical(g12)
    c: Equal(g11,g7)
    c: DistanceY(g1,g0) = 2
    c: DistanceX(g8,g8) = 5.3
    c: Coincident(g13,g1)
    c: Coincident(g13,g12)
    c: Horizontal(g13)
    c: DistanceX(g13,g13) = 12
    c: DistanceX(g1,g2) = 3.5
    c: Coincident(g8,g12)
    c: Equal(g7,g9)
    c: Equal(g6,g10)
FEATURE [PartDesign::Revolution] Revolution023
  Angle = 360
  Axis = (1,0,0)
  Base = (0,0,0)
  Profile = -> Sketch070
  ReferenceAxis = -> X_Axis090
FEATURE [PartDesign::Fillet] Fillet161
  Base = -> Revolution023 [Edge13,Edge11]
  BaseFeature = -> Revolution023
  Radius = 0.2
  SupportTransform = false
FEATURE [PartDesign::Body] Body076  label="Inner Ring003"
  Group = -> [Sketch070,Revolution023,Fillet161]
  Origin = -> Origin092
  Tip = -> Fillet161
FEATURE [App::DocumentObjectGroup] Group018  label="Rings002"
  Group = -> [Body075,Body076]
FEATURE [Sketcher::SketchObject] Sketch071
  FullyConstrained = true
  MapMode = 5
  Placement = pos=(0,0,0) rot=(1,0,0;1.5708rad)
  Support = -> [XZ_Plane091]
  sketch-geometry (12):
    g0: LineSegment StartX=2.9 StartY=9.5 StartZ=0 EndX=2.9 EndY=8.5 EndZ=0
    g1: LineSegment StartX=2.9 StartY=8.5 StartZ=0 EndX=3.2 EndY=8.5 EndZ=0
    g2: LineSegment StartX=3.2 StartY=8.5 StartZ=0 EndX=3.2 EndY=6.5 EndZ=0
    g3: LineSegment StartX=3.2 StartY=6.5 StartZ=0 EndX=2.9 EndY=6.5 EndZ=0
    g4: LineSegment StartX=2.9 StartY=6.5 StartZ=0 EndX=2.9 EndY=5.5 EndZ=0
    g5: LineSegment StartX=2.9 StartY=5.5 StartZ=0 EndX=3.2 EndY=5.5 EndZ=0
    g6: LineSegment StartX=3.2 StartY=5.5 StartZ=0 EndX=3.2 EndY=6 EndZ=0
    g7: LineSegment StartX=3.2 StartY=6 StartZ=0 EndX=3.5 EndY=6 EndZ=0
    g8: LineSegment StartX=3.5 StartY=6 StartZ=0 EndX=3.5 EndY=9 EndZ=0
    g9: LineSegment StartX=3.5 StartY=9 StartZ=0 EndX=3.2 EndY=9 EndZ=0
    g10: LineSegment StartX=3.2 StartY=9 StartZ=0 EndX=3.2 EndY=9.5 EndZ=0
    g11: LineSegment StartX=3.2 StartY=9.5 StartZ=0 EndX=2.9 EndY=9.5 EndZ=0
  constraints (36):
    c: Vertical(g0)
    c: Coincident(g0,g1)
    c: Horizontal(g1)
    c: Coincident(g1,g2)
    c: Vertical(g2)
    c: Coincident(g2,g3)
    c: Horizontal(g3)
    c: Coincident(g3,g4)
    c: Vertical(g4)
    c: Coincident(g4,g5)
    c: Horizontal(g5)
    c: Coincident(g5,g6)
    c: Vertical(g6)
    c: Coincident(g6,g7)
    c: Horizontal(g7)
    c: Coincident(g7,g8)
    c: Vertical(g8)
    c: Coincident(g8,g9)
    c: Horizontal(g9)
    c: Coincident(g9,g10)
    c: Vertical(g10)
    c: Coincident(g10,g11)
    c: Coincident(g11,g0)
    c: Horizontal(g11)
    c: DistanceY(g4) = 5.5
    c: DistanceX(g4) = 2.9
    c: DistanceY(g5,g6) = 0.5
    c: DistanceY(g6,g2) = 0.5
    c: DistanceX(g5,g5) = 0.3
    c: Equal(g5,g7)
    c: Equal(g7,g3)
    c: Equal(g3,g1)
    c: Equal(g1,g9)
    c: Equal(g4,g0)
    c: Equal(g6,g10)
    c: DistanceY(g4,g0) = 4
FEATURE [PartDesign::Revolution] Revolution024
  Angle = 360
  Axis = (1,0,0)
  Base = (0,0,0)
  Placement = pos=(0,0,0) rot=(1,0,0;1.5708rad)
  Profile = -> Sketch071
  ReferenceAxis = -> Sketch071 [H_Axis]
FEATURE [PartDesign::Fillet] Fillet162
  Base = -> Revolution024 [Edge14,Edge12]
  BaseFeature = -> Revolution024
  Placement = pos=(0,0,0) rot=(1,0,0;1.5708rad)
  Radius = 0.2
  SupportTransform = false
FEATURE [PartDesign::Body] Body077  label="Seal 005"
  Group = -> [Sketch071,Revolution024,Fillet162]
  Origin = -> Origin093
  Tip = -> Fillet162
FEATURE [PartDesign::FeatureBase] Clone041
  BaseFeature = -> Body077
FEATURE [PartDesign::Body] Body078  label="Seal 006"
  BaseFeature = -> Body077
  Group = -> [Clone041]
  Origin = -> Origin094
  Placement = pos=(0,0,0) rot=(0,1,0;3.14159rad)
  Tip = -> Clone041
FEATURE [App::DocumentObjectGroup] Group017  label="Seals002"
  Group = -> [Body077,Body078]
FEATURE [Sketcher::SketchObject] Sketch072
  AttachmentOffset = pos=(0,0,4) rot=(0,0,1;0rad)
  FullyConstrained = true
  MapMode = 5
  Placement = pos=(0,0,4) rot=(0,0,1;0rad)
  Support = -> [XY_Plane072]
  sketch-geometry (1):
    g0: Circle CenterX=6 CenterY=0 CenterZ=0 NormalX=0 NormalY=0 NormalZ=1 AngleXU=0 Radius=1.5
  constraints (3):
    c: PointOnObject(g0,g-1)
    c: Diameter(g0) = 3
    c: DistanceX(g-1,g0) = 6
FEATURE [PartDesign::Pad] Pad018
  Direction = (0,0,1)
  Length = 3
  Length2 = 100
  Profile = -> Sketch072
  Type = 0
FEATURE [Sketcher::SketchObject] Sketch073
  ExternalGeometry = -> [Pad018]
  FullyConstrained = true
  MapMode = 5
  Placement = pos=(0,0,7) rot=(0,0,1;0rad)
  Support = -> [Pad018]
  sketch-geometry (7):
    g0: LineSegment StartX=6.43301 StartY=-0.75 StartZ=0 EndX=6.86603 EndY=0 EndZ=0
    g1: LineSegment StartX=6.86603 StartY=0 StartZ=0 EndX=6.43301 EndY=0.75 EndZ=0
    g2: LineSegment StartX=6.43301 StartY=0.75 StartZ=0 EndX=5.56699 EndY=0.75 EndZ=0
    g3: LineSegment StartX=5.56699 StartY=0.75 StartZ=0 EndX=5.13397 EndY=-1e-16 EndZ=0
    g4: LineSegment StartX=5.13397 StartY=-1e-16 StartZ=0 EndX=5.56699 EndY=-0.75 EndZ=0
    g5: LineSegment StartX=5.56699 StartY=-0.75 StartZ=0 EndX=6.43301 EndY=-0.75 EndZ=0
    g6: Circle CenterX=6 CenterY=0 CenterZ=0 NormalX=0 NormalY=0 NormalZ=1 AngleXU=0 Radius=0.866025
  constraints (16):
    c: Coincident(g0,g1)
    c: Coincident(g1,g2)
    c: Coincident(g2,g3)
    c: Coincident(g3,g4)
    c: Coincident(g4,g5)
    c: Coincident(g5,g0)
    c: Equal(g0, g1-g5) x5
    c: PointOnObject(g0,g6)
    c: PointOnObject(g1,g6)
    c: PointOnObject(g2,g6)
    c: PointOnObject(g3,g6)
    c: PointOnObject(g4,g6)
    c: PointOnObject(g5,g6)
    c: Coincident(g6,g-3)
    c: Horizontal(g5)
    c: DistanceY(g4,g2) = 1.5
FEATURE [PartDesign::Pocket] Pocket023
  BaseFeature = -> Pad018
  Length = 0.9
  Length2 = 100
  Profile = -> Sketch073
  Type = 0
FEATURE [PartDesign::PolarPattern] PolarPattern011
  Angle = 120
  Axis = -> X_Axis072
  BaseFeature = -> Pocket023
  Occurrences = 3
  Originals = -> [Pad018,Pocket023]
FEATURE [PartDesign::Body] Body058
  Group = -> [Sketch072,Pad018,Sketch073,Pocket023,PolarPattern011]
  Origin = -> Origin074
  Tip = -> PolarPattern011
FEATURE [App::DocumentObjectGroup] Group019  label="Set screws002"
  Group = -> [Body058]
FEATURE [Sketcher::SketchObject] Sketch074
  AttachmentOffset = pos=(0,0,-6.5) rot=(0,0,1;0rad)
  FullyConstrained = true
  MapMode = 5
  Placement = pos=(-6.5,1.4e-15,-1.4e-15) rot=(0.57735,0.57735,0.57735;2.0944rad)
  Support = -> [YZ_Plane093]
  sketch-geometry (14):
    g0: Circle CenterX=0 CenterY=0 CenterZ=0 NormalX=0 NormalY=0 NormalZ=1 AngleXU=0 Radius=11
    g1: ArcOfCircle CenterX=0 CenterY=0 CenterZ=0 NormalX=0 NormalY=0 NormalZ=1 AngleXU=0 Radius=13.5 StartAngle=0.0668757 EndAngle=3.07472
    g2: LineSegment StartX=-13.4698 StartY=0.902148 StartZ=0 EndX=-14.2 EndY=-10 EndZ=0
    g3: LineSegment StartX=-14.2 StartY=-10 StartZ=0 EndX=-27.5 EndY=-10 EndZ=0
    g4: LineSegment StartX=-27.5 StartY=-10 StartZ=0 EndX=-27.5 EndY=-15 EndZ=0
    g5: LineSegment StartX=-27.5 StartY=-15 StartZ=0 EndX=-12.3 EndY=-15 EndZ=0
    g6: LineSegment StartX=27.5 StartY=-15 StartZ=0 EndX=27.5 EndY=-10 EndZ=0
    g7: LineSegment StartX=27.5 StartY=-10 StartZ=0 EndX=14.2 EndY=-10 EndZ=0
    g8: LineSegment StartX=14.2 StartY=-10 StartZ=0 EndX=13.4698 EndY=0.902148 EndZ=0
    g9: LineSegment StartX=12.3 StartY=-15 StartZ=0 EndX=12.1995 EndY=-13.5 EndZ=0
    g10: LineSegment StartX=12.1995 StartY=-13.5 StartZ=0 EndX=-12.1995 EndY=-13.5 EndZ=0
    g11: LineSegment StartX=-12.1995 StartY=-13.5 StartZ=0 EndX=-12.3 EndY=-15 EndZ=0
    g12: LineSegment StartX=12.3 StartY=-15 StartZ=0 EndX=27.5 EndY=-15 EndZ=0
    g13: GeomPoint X=0 Y=13.5 Z=0
  constraints (39):
    c: Coincident(g0,g-1)
    c: Radius(g0) = 11
    c: Coincident(g1,g0)
    c: Coincident(g2,g3)
    c: Coincident(g3,g4)
    c: Coincident(g4,g5)
    c: Horizontal(g5)
    c: Coincident(g12,g6)
    c: Coincident(g6,g7)
    c: Horizontal(g7)
    c: Coincident(g7,g8)
    c: Coincident(g9,g10)
    c: Horizontal(g10)
    c: Coincident(g10,g11)
    c: Coincident(g5,g11)
    c: Coincident(g12,g9)
    c: Horizontal(g3)
    c: Vertical(g6)
    c: Vertical(g4)
    c: Equal(g9,g11)
    c: Horizontal(g12)
    c: Horizontal(g5,g9)
    c: Equal(g6,g4)
    c: Equal(g12,g5)
    c: Equal(g7,g3)
    c: DistanceX(g4,g6) = 55
    c: DistanceY(g6,g0) = 15
    c: Equal(g8,g2)
    c: DistanceY(g6,g6) = 5
    c: Parallel(g9,g8)
    c: DistanceY(g9,g9) = 1.5
    c: DistanceX(g5,g5) = 15.2
    c: Diameter(g1) = 27
    c: PointOnObject(g13,g1)
    c: PointOnObject(g13,g-2)
    c: DistanceY(g6,g13) = 28.5
    c: Tangent(g1,g2) = -1.5708
    c: Tangent(g1,g8) = -1.5708
    c: DistanceX(g3,g3) = 13.3
FEATURE [PartDesign::Pad] Pad019
  Direction = (1,-2e-16,3e-16)
  Length = 13
  Length2 = 100
  Placement = pos=(0,0,0) rot=(0.57735,0.57735,0.57735;2.0944rad)
  Profile = -> Sketch074
  Type = 0
FEATURE [Sketcher::SketchObject] Sketch075
  ExternalGeometry = -> [Pad019]
  FullyConstrained = true
  MapMode = 5
  Placement = pos=(4.2e-15,-6.6e-15,-15) rot=(0.707107,0.707107,0;3.14159rad)
  Support = -> [Pad019]
  sketch-geometry (7):
    g0: LineSegment StartX=-24.9 StartY=4.15 StartZ=0 EndX=-14.9 EndY=4.15 EndZ=0
    g1: LineSegment StartX=-14.9 StartY=4.15 StartZ=0 EndX=-14.9 EndY=-4.15 EndZ=0
    g2: LineSegment StartX=-14.9 StartY=-4.15 StartZ=0 EndX=-24.9 EndY=-4.15 EndZ=0
    g3: LineSegment StartX=-24.9 StartY=-4.15 StartZ=0 EndX=-24.9 EndY=4.15 EndZ=0
    g4: LineSegment StartX=-27.5 StartY=6.5 StartZ=0 EndX=-12.3 EndY=-6.5 EndZ=0
    g5: LineSegment StartX=-27.5 StartY=-6.5 StartZ=0 EndX=-12.3 EndY=6.5 EndZ=0
    g6: GeomPoint X=-19.9 Y=2.6e-15 Z=0
  constraints (17):
    c: Coincident(g0,g1)
    c: Coincident(g1,g2)
    c: Coincident(g2,g3)
    c: Coincident(g3,g0)
    c: Horizontal(g0)
    c: Horizontal(g2)
    c: Vertical(g1)
    c: Vertical(g3)
    c: DistanceX(g0,g0) = 10
    c: DistanceY(g1,g1) = 8.3
    c: Coincident(g4,g-3)
    c: Coincident(g4,g-4)
    c: Coincident(g5,g-4)
    c: Coincident(g5,g-3)
    c: PointOnObject(g6,g4)
    c: PointOnObject(g6,g5)
    c: Symmetric(g0,g1,g6)
FEATURE [PartDesign::Pocket] Pocket024
  BaseFeature = -> Pad019
  Length = 2.3
  Length2 = 100
  Placement = pos=(0,0,0) rot=(0.57735,0.57735,0.57735;2.0944rad)
  Profile = -> Sketch075
  Type = 0
FEATURE [Sketcher::SketchObject] Sketch076
  ExternalGeometry = -> [Pocket024]
  FullyConstrained = true
  MapMode = 5
  Placement = pos=(2.8e-15,-4.4e-15,-10) rot=(0,0,-1;1.5708rad)
  Support = -> [Pocket024]
  sketch-geometry (2):
    g0: Circle CenterX=21.2 CenterY=2.1e-15 CenterZ=0 NormalX=0 NormalY=0 NormalZ=1 AngleXU=0 Radius=2.5
    g1: LineSegment StartX=21.2 StartY=2.1e-15 StartZ=0 EndX=27.5 EndY=2.1e-15 EndZ=0
  constraints (5):
    c: Diameter(g0) = 5
    c: DistanceX(g0,g-3) = 6.3
    c: Coincident(g1,g0)
    c: Horizontal(g1)
    c: Symmetric(g-5,g-5,g1)
FEATURE [PartDesign::Pocket] Pocket025
  BaseFeature = -> Pocket024
  Length = 5
  Length2 = 100
  Placement = pos=(0,0,0) rot=(0.57735,0.57735,0.57735;2.0944rad)
  Profile = -> Sketch076
  Type = 2
FEATURE [Sketcher::SketchObject] Sketch077
  ExternalGeometry = -> [Pocket025]
  FullyConstrained = true
  MapMode = 5
  Placement = pos=(6.5,-1.4e-15,1.5e-15) rot=(0.57735,0.57735,0.57735;2.0944rad)
  Support = -> [Pocket025]
  sketch-geometry (6):
    g0: LineSegment StartX=-24.6 StartY=-13.7 StartZ=0 EndX=-24.6 EndY=-11.3 EndZ=0
    g1: LineSegment StartX=-24.6 StartY=-11.3 StartZ=0 EndX=-14.2 EndY=-11.3 EndZ=0
    g2: LineSegment StartX=-14.2 StartY=-11.3 StartZ=0 EndX=-14.2 EndY=-13.7 EndZ=0
    g3: LineSegment StartX=-14.2 StartY=-13.7 StartZ=0 EndX=-24.6 EndY=-13.7 EndZ=0
    g4: GeomPoint X=-19.4 Y=-12.5 Z=0
    g5: LineSegment StartX=-19.4 StartY=-12.5 StartZ=0 EndX=-27.5 EndY=-12.5 EndZ=0
  constraints (15):
    c: Coincident(g0,g1)
    c: Coincident(g1,g2)
    c: Coincident(g2,g3)
    c: Coincident(g3,g0)
    c: Horizontal(g1)
    c: Horizontal(g3)
    c: Vertical(g0)
    c: Vertical(g2)
    c: Symmetric(g1,g0,g4)
    c: DistanceX(g1,g1) = 10.4
    c: DistanceY(g2,g2) = 2.4
    c: DistanceX(g2,g-4) = 1.9
    c: Coincident(g5,g4)
    c: Horizontal(g5)
    c: Symmetric(g-5,g-5,g5)
FEATURE [PartDesign::Pocket] Pocket026
  BaseFeature = -> Pocket025
  Length = 0.4
  Length2 = 100
  Placement = pos=(0,0,0) rot=(0.57735,0.57735,0.57735;2.0944rad)
  Profile = -> Sketch077
  Type = 0
FEATURE [PartDesign::Mirrored] Mirrored002
  BaseFeature = -> Pocket026
  MirrorPlane = -> Sketch075 [V_Axis]
  Originals = -> [Pocket024,Pocket025,Pocket026]
  Placement = pos=(0,0,0) rot=(0.57735,0.57735,0.57735;2.0944rad)
FEATURE [Sketcher::SketchObject] Sketch078
  ExternalGeometry = -> [Mirrored002]
  FullyConstrained = true
  MapMode = 5
  Placement = pos=(0,0,0) rot=(1,0,0;1.5708rad)
  Support = -> [XZ_Plane093]
  sketch-geometry (9):
    g0: GeomPoint X=-6.5 Y=13.5 Z=0
    g1: LineSegment StartX=6.5 StartY=-10 StartZ=0 EndX=6.5 EndY=13.5 EndZ=0
    g2: LineSegment StartX=6.5 StartY=13.5 StartZ=0 EndX=4.75 EndY=13.5 EndZ=0
    g3: LineSegment StartX=-6.5 StartY=13.5 StartZ=0 EndX=-4.75 EndY=13.5 EndZ=0
    g4: LineSegment StartX=-6.5 StartY=-10 StartZ=0 EndX=-6.5 EndY=13.5 EndZ=0
    g5: LineSegment StartX=6.5 StartY=-10 StartZ=0 EndX=4.75 EndY=-1 EndZ=0
    g6: LineSegment StartX=4.75 StartY=-1 StartZ=0 EndX=4.75 EndY=13.5 EndZ=0
    g7: LineSegment StartX=-4.75 StartY=13.5 StartZ=0 EndX=-4.75 EndY=-1 EndZ=0
    g8: LineSegment StartX=-4.75 StartY=-1 StartZ=0 EndX=-6.5 EndY=-10 EndZ=0
  constraints (24):
    c: Vertical(g0,g-4)
    c: Horizontal(g-3,g0)
    c: Coincident(g1,g-3)
    c: Coincident(g1,g2)
    c: Horizontal(g2)
    c: Coincident(g3,g0)
    c: Horizontal(g3)
    c: Coincident(g4,g3)
    c: Vertical(g4,g-4)
    c: DistanceX(g3,g2) = 9.5
    c: Equal(g2,g3)
    c: Horizontal(g1,g4)
    c: Coincident(g1,g-5)
    c: Coincident(g1,g5)
    c: Coincident(g5,g6)
    c: Coincident(g6,g2)
    c: Vertical(g6)
    c: DistanceY(g1,g5) = 9
    c: Coincident(g3,g7)
    c: Vertical(g7)
    c: Coincident(g7,g8)
    c: Coincident(g8,g4)
    c: Horizontal(g7,g5)
    c: DistanceX(g2,g2) = 1.75
FEATURE [PartDesign::Pocket] Pocket027
  BaseFeature = -> Mirrored002
  Length = 15
  Length2 = 15
  Placement = pos=(0,0,0) rot=(0.57735,0.57735,0.57735;2.0944rad)
  Profile = -> Sketch078
  Type = 4
FEATURE [Sketcher::SketchObject] Sketch079
  FullyConstrained = true
  MapMode = 5
  Placement = pos=(-6.5,1.4e-15,-1.5e-15) rot=(0.57735,0.57735,-0.57735;4.18879rad)
  Support = -> [Pocket027]
  sketch-geometry (1):
    g0: Circle CenterX=0 CenterY=0 CenterZ=0 NormalX=0 NormalY=0 NormalZ=1 AngleXU=0 Radius=12.2
  constraints (2):
    c: Coincident(g0,g-1)
    c: Diameter(g0) = 24.4
FEATURE [PartDesign::Pocket] Pocket028
  BaseFeature = -> Pocket027
  Length = 2.75
  Length2 = 100
  Placement = pos=(0,0,0) rot=(0.57735,0.57735,0.57735;2.0944rad)
  Profile = -> Sketch079
  Type = 0
FEATURE [Sketcher::SketchObject] Sketch080
  FullyConstrained = true
  MapMode = 5
  Placement = pos=(6.5,-1.4e-15,1.5e-15) rot=(0.57735,0.57735,0.57735;2.0944rad)
  Support = -> [Pocket028]
  sketch-geometry (1):
    g0: Circle CenterX=0 CenterY=0 CenterZ=0 NormalX=0 NormalY=0 NormalZ=1 AngleXU=0 Radius=12.1
  constraints (2):
    c: Coincident(g0,g-1)
    c: Diameter(g0) = 24.2
FEATURE [PartDesign::Pocket] Pocket029
  BaseFeature = -> Pocket028
  Length = 2.75
  Length2 = 100
  Placement = pos=(0,0,0) rot=(0.57735,0.57735,0.57735;2.0944rad)
  Profile = -> Sketch080
  Type = 0
FEATURE [Sketcher::SketchObject] Sketch081
  ExternalGeometry = -> [Pocket029]
  FullyConstrained = true
  MapMode = 5
  Placement = pos=(6.5,-1.4e-15,1.5e-15) rot=(0.57735,0.57735,0.57735;2.0944rad)
  Support = -> [Pocket029]
  sketch-geometry (6):
    g0: ArcOfCircle CenterX=0 CenterY=0 CenterZ=0 NormalX=0 NormalY=0 NormalZ=1 AngleXU=0 Radius=13.5 StartAngle=3.79664 EndAngle=5.62814
    g1: LineSegment StartX=-11.8698 StartY=-8.57666 StartZ=0 EndX=-12.3 EndY=-15 EndZ=0
    g2: LineSegment StartX=-12.3 StartY=-15 StartZ=0 EndX=12.3 EndY=-15 EndZ=0
    g3: LineSegment StartX=12.3 StartY=-15 StartZ=0 EndX=11.8698 EndY=-8.57666 EndZ=0
    g4: ArcOfCircle CenterX=11.2212 CenterY=-8.6201 CenterZ=0 NormalX=0 NormalY=0 NormalZ=1 AngleXU=0 Radius=0.65 StartAngle=0.0668757 EndAngle=2.48655
    g5: ArcOfCircle CenterX=-11.2212 CenterY=-8.6201 CenterZ=0 NormalX=0 NormalY=0 NormalZ=1 AngleXU=0 Radius=0.65 StartAngle=0.655044 EndAngle=3.07472
  constraints (14):
    c: Coincident(g0,g-1)
    c: Diameter(g0) = 27
    c: Coincident(g1,g2)
    c: Coincident(g2,g3)
    c: Coincident(g1,g-3)
    c: Coincident(g2,g-4)
    c: Tangent(g3,g4) = -1.5708
    c: Tangent(g0,g4) = 1.5708
    c: Tangent(g0,g5) = 1.5708
    c: Tangent(g1,g5) = -1.5708
    c: Equal(g4,g5)
    c: Horizontal(g4,g5)
    c: Parallel(g-4,g3)
    c: Radius(g4) = 0.65
FEATURE [PartDesign::Pocket] Pocket030
  BaseFeature = -> Pocket029
  Length = 5.25
  Length2 = 100
  Placement = pos=(0,0,0) rot=(0.57735,0.57735,0.57735;2.0944rad)
  Profile = -> Sketch081
  Type = 0
FEATURE [Sketcher::SketchObject] Sketch082
  ExternalGeometry = -> [Pocket030]
  FullyConstrained = true
  MapMode = 5
  Placement = pos=(-6.5,1.4e-15,-1.5e-15) rot=(0.57735,0.57735,-0.57735;4.18879rad)
  Support = -> [Pocket030]
  sketch-geometry (6):
    g0: ArcOfCircle CenterX=0 CenterY=0 CenterZ=0 NormalX=0 NormalY=0 NormalZ=1 AngleXU=0 Radius=13.5 StartAngle=0.655044 EndAngle=2.48655
    g1: LineSegment StartX=11.8698 StartY=8.57666 StartZ=0 EndX=12.3 EndY=15 EndZ=0
    g2: LineSegment StartX=12.3 StartY=15 StartZ=0 EndX=-12.3 EndY=15 EndZ=0
    g3: LineSegment StartX=-12.3 StartY=15 StartZ=0 EndX=-11.8698 EndY=8.57666 EndZ=0
    g4: ArcOfCircle CenterX=-11.2212 CenterY=8.6201 CenterZ=0 NormalX=0 NormalY=0 NormalZ=1 AngleXU=0 Radius=0.65 StartAngle=3.20847 EndAngle=5.62814
    g5: ArcOfCircle CenterX=11.2212 CenterY=8.6201 CenterZ=0 NormalX=0 NormalY=0 NormalZ=1 AngleXU=0 Radius=0.65 StartAngle=3.79664 EndAngle=6.21631
  constraints (14):
    c: Coincident(g0,g-1)
    c: Radius(g0) = 13.5
    c: Coincident(g1,g2)
    c: Coincident(g2,g-3)
    c: Coincident(g2,g3)
    c: Coincident(g-4,g1)
    c: Tangent(g3,g4) = -1.5708
    c: Tangent(g0,g4) = 1.5708
    c: Tangent(g0,g5) = 1.5708
    c: Tangent(g1,g5) = -1.5708
    c: Equal(g4,g5)
    c: Radius(g4) = 0.65
    c: Parallel(g-4,g1)
    c: Parallel(g3,g-3)
FEATURE [PartDesign::Pocket] Pocket031
  BaseFeature = -> Pocket030
  Length = 5.25
  Length2 = 100
  Placement = pos=(0,0,0) rot=(0.57735,0.57735,0.57735;2.0944rad)
  Profile = -> Sketch082
  Type = 0
FEATURE [PartDesign::Chamfer] Chamfer002
  Angle = 45
  Base = -> Pocket031 [Edge159,Edge155,Edge22,Edge27]
  BaseFeature = -> Pocket031
  ChamferType = 0
  FlipDirection = false
  Placement = pos=(0,0,0) rot=(0.57735,0.57735,0.57735;2.0944rad)
  Size = 2
  Size2 = 1
  SupportTransform = false
FEATURE [Sketcher::SketchObject] Sketch083
  ExternalGeometry = -> [Chamfer002]
  FullyConstrained = true
  MapMode = 5
  Placement = pos=(-3.75,5e-15,-2.7e-15) rot=(-0.57735,-0.57735,0.57735;2.0944rad)
  Support = -> [Chamfer002]
  sketch-geometry (13):
    g0: ArcOfCircle CenterX=-6.9e-15 CenterY=-3.7e-15 CenterZ=0 NormalX=0 NormalY=0 NormalZ=1 AngleXU=0 Radius=11 StartAngle=5.75419 EndAngle=6.81218
    g1: ArcOfCircle CenterX=-6.9e-15 CenterY=-3.7e-15 CenterZ=0 NormalX=0 NormalY=0 NormalZ=1 AngleXU=0 Radius=12.2 StartAngle=5.94045 EndAngle=6.62592
    g2: ArcOfCircle CenterX=-6.9e-15 CenterY=-3.7e-15 CenterZ=0 NormalX=0 NormalY=0 NormalZ=1 AngleXU=0 Radius=11 StartAngle=2.6126 EndAngle=3.67059
    g3: ArcOfCircle CenterX=-6.9e-15 CenterY=-3.7e-15 CenterZ=0 NormalX=0 NormalY=0 NormalZ=1 AngleXU=0 Radius=12.2 StartAngle=2.79886 EndAngle=3.48433
    g4: Ellipse CenterX=-6.9e-15 CenterY=-3.7e-15 CenterZ=0 NormalX=0 NormalY=0 NormalZ=1 MajorRadius=13.5 MinorRadius=7.81051 AngleXU=-3e-16
    g5: LineSegment StartX=13.5 StartY=-7.4e-15 StartZ=0 EndX=-13.5 EndY=0 EndZ=0
    g6: LineSegment StartX=-4.8e-15 StartY=7.81051 StartZ=0 EndX=-9.1e-15 EndY=-7.81051 EndZ=0
    g7: GeomPoint X=11.0112 Y=-6.8e-15 Z=0
    g8: GeomPoint X=-11.0112 Y=-7e-16 Z=0
    g9: LineSegment StartX=-11.4904 StartY=4.1 StartZ=0 EndX=-9.49645 EndY=5.55135 EndZ=0
    g10: LineSegment StartX=-11.4904 StartY=-4.1 StartZ=0 EndX=-9.49645 EndY=-5.55135 EndZ=0
    g11: LineSegment StartX=9.49645 StartY=-5.55135 StartZ=0 EndX=11.4904 EndY=-4.1 EndZ=0
    g12: LineSegment StartX=11.4904 StartY=4.1 StartZ=0 EndX=9.49645 EndY=5.55135 EndZ=0
  constraints (29):
    c: Coincident(g0,g-4)
    c: PointOnObject(g0,g-4)
    c: Coincident(g1,g0)
    c: PointOnObject(g1,g-3)
    c: Coincident(g2,g0)
    c: PointOnObject(g2,g-4)
    c: Coincident(g3,g0)
    c: PointOnObject(g3,g-3)
    c: InternalAlignment(g5-g8 -> g4) x4
    c: Coincident(g4,g0)
    c: PointOnObject(g3,g4)
    c: PointOnObject(g2,g4)
    c: PointOnObject(g3,g4)
    c: PointOnObject(g2,g4)
    c: PointOnObject(g0,g4)
    c: PointOnObject(g1,g4)
    c: PointOnObject(g1,g4)
    c: PointOnObject(g0,g4)
    c: PointOnObject(g5,g-1)
    c: DistanceX(g5,g5) = 27
    c: DistanceY(g3,g3) = 8.2
    c: Coincident(g9,g3)
    c: Coincident(g9,g2)
    c: Coincident(g10,g3)
    c: Coincident(g10,g2)
    c: Coincident(g11,g0)
    c: Coincident(g11,g1)
    c: Coincident(g12,g1)
    c: Coincident(g12,g0)
FEATURE [PartDesign::Pocket] Pocket032
  BaseFeature = -> Chamfer002
  Length = 5
  Length2 = 100
  Placement = pos=(0,0,0) rot=(0.57735,0.57735,0.57735;2.0944rad)
  Profile = -> Sketch083
  Type = 0
FEATURE [PartDesign::Body] Body079  label="Metal case002"
  Group = -> [Sketch074,Pad019,Sketch075,Pocket024,Sketch076,Pocket025,Sketch077,Pocket026,Mirrored002,Sketch078,Pocket027,Sketch079,Pocket028,Sketch080,Pocket029,Sketch081,Pocket030,Sketch082,Pocket031,Chamfer002,Sketch083,Pocket032]
  Origin = -> Origin095
  Tip = -> Pocket032
FEATURE [App::DocumentObjectGroup] Group020  label="Case002"
  Group = -> [Body079]
FEATURE [App::Part] Part016  label="KP08-003"
  Group = -> [Group014,Body060,Body059,Body064,Body061,Body065,Body063,Body062,Group015,Body067,Body066,Group016,Body072,Body071,Body074,Body070,Body073,Body069,Body068,Group017,Body078,Body077,Group018,Body075,Body076,Group019,Body058,Group020,Body079]
  Origin = -> Origin096
  Placement = pos=(332,120,105) rot=(0,0,1;3.14159rad)
FEATURE [Sketcher::SketchObject] Sketch084
  FullyConstrained = true
  MapMode = 5
  Placement = pos=(0,0,0) rot=(-0.57735,0.57735,0.57735;4.18879rad)
  Support = -> [YZ_Plane102]
  sketch-geometry (1):
    g0: Circle CenterX=0 CenterY=-7.5 CenterZ=0 NormalX=0 NormalY=0 NormalZ=1 AngleXU=0 Radius=0.25
  constraints (3):
    c: PointOnObject(g0,g-2)
    c: DistanceY(g0) = -7.5
    c: Diameter(g0) = 0.5
FEATURE [Sketcher::SketchObject] Sketch085
  FullyConstrained = true
  MapMode = 5
  Support = -> [XY_Plane095]
  sketch-geometry (2):
    g0: LineSegment StartX=0 StartY=5.5 StartZ=0 EndX=6e-16 EndY=9.5 EndZ=0
    g1: ArcOfCircle CenterX=0 CenterY=7.5 CenterZ=0 NormalX=0 NormalY=0 NormalZ=1 AngleXU=0 Radius=2 StartAngle=4.71239 EndAngle=7.85398
  constraints (7):
    c: PointOnObject(g0,g-2)
    c: PointOnObject(g0,g-2)
    c: PointOnObject(g1,g0)
    c: Coincident(g1,g0)
    c: Coincident(g1,g0)
    c: Radius(g1) = 2
    c: DistanceY(g1) = 7.5
FEATURE [PartDesign::Revolution] Revolution025
  Angle = 360
  Axis = (0,1,0)
  Base = (0,0,0)
  Profile = -> Sketch085
  ReferenceAxis = -> Sketch085 [V_Axis]
  Reversed = true
FEATURE [PartDesign::Body] Body081  label="Ball 022"
  Group = -> [Sketch085,Revolution025]
  Origin = -> Origin098
  Tip = -> Revolution025
FEATURE [PartDesign::FeatureBase] Clone042
  BaseFeature = -> Body081
FEATURE [PartDesign::Body] Body082  label="Ball 023"
  BaseFeature = -> Body081
  Group = -> [Clone042]
  Origin = -> Origin099
  Placement = pos=(0,0,0) rot=(-1,0,0;0.897598rad)
  Tip = -> Clone042
FEATURE [PartDesign::FeatureBase] Clone043
  BaseFeature = -> Body081
FEATURE [PartDesign::Body] Body083  label="Ball 024"
  BaseFeature = -> Body081
  Group = -> [Clone043]
  Origin = -> Origin100
  Placement = pos=(0,0,0) rot=(-1,0,0;1.7952rad)
  Tip = -> Clone043
FEATURE [PartDesign::FeatureBase] Clone044
  BaseFeature = -> Body081
FEATURE [PartDesign::Body] Body084  label="Ball 025"
  BaseFeature = -> Body081
  Group = -> [Clone044]
  Origin = -> Origin101
  Placement = pos=(0,0,0) rot=(1,0,0;3.59039rad)
  Tip = -> Clone044
FEATURE [PartDesign::FeatureBase] Clone045
  BaseFeature = -> Body081
FEATURE [PartDesign::Body] Body085  label="Ball 026"
  BaseFeature = -> Body081
  Group = -> [Clone045]
  Origin = -> Origin102
  Placement = pos=(0,0,0) rot=(1,0,0;2.69279rad)
  Tip = -> Clone045
FEATURE [PartDesign::FeatureBase] Clone046
  BaseFeature = -> Body081
FEATURE [PartDesign::Body] Body086  label="Ball 027"
  BaseFeature = -> Body081
  Group = -> [Clone046]
  Origin = -> Origin103
  Placement = pos=(0,0,0) rot=(1,0,0;1.7952rad)
  Tip = -> Clone046
FEATURE [PartDesign::FeatureBase] Clone047
  BaseFeature = -> Body081
FEATURE [PartDesign::Body] Body087  label="Ball 028"
  BaseFeature = -> Body081
  Group = -> [Clone047]
  Origin = -> Origin104
  Placement = pos=(0,0,0) rot=(1,0,0;0.897598rad)
  Tip = -> Clone047
FEATURE [App::DocumentObjectGroup] Group021  label="Balls003"
  Group = -> [Body081,Body082,Body083,Body084,Body085,Body086,Body087]
FEATURE [Sketcher::SketchObject] Sketch086
  FullyConstrained = true
  MapMode = 5
  Support = -> [XY_Plane104]
  sketch-geometry (7):
    g0: LineSegment StartX=-5 StartY=7.5 StartZ=0 EndX=5 EndY=7.5 EndZ=0
    g1: LineSegment StartX=-0.210977 StartY=7.5 StartZ=0 EndX=0.210977 EndY=7.5 EndZ=0
    g2: ArcOfCircle CenterX=0.25 CenterY=7.5 CenterZ=0 NormalX=0 NormalY=0 NormalZ=1 AngleXU=0 Radius=0.460977 StartAngle=2.43297 EndAngle=3.14159
    g3: ArcOfCircle CenterX=-0.25 CenterY=7.5 CenterZ=0 NormalX=0 NormalY=0 NormalZ=1 AngleXU=0 Radius=0.460977 StartAngle=9.792e-13 EndAngle=0.708626
    g4: LineSegment StartX=-0.1 StartY=7.8 StartZ=0 EndX=-0.1 EndY=7.75 EndZ=0
    g5: LineSegment StartX=-0.1 StartY=7.75 StartZ=0 EndX=0.1 EndY=7.75 EndZ=0
    g6: LineSegment StartX=0.1 StartY=7.75 StartZ=0 EndX=0.1 EndY=7.8 EndZ=0
  constraints (22):
    c: DistanceY(g-1,g0) = 7.5
    c: Symmetric(g0,g0,g-2)
    c: DistanceX(g0,g0) = 10
    c: PointOnObject(g1,g0)
    c: PointOnObject(g1,g0)
    c: Coincident(g3,g1)
    c: Coincident(g2,g1)
    c: Coincident(g2,g4)
    c: Coincident(g4,g5)
    c: Horizontal(g5)
    c: Coincident(g5,g6)
    c: Coincident(g6,g3)
    c: Vertical(g6)
    c: Equal(g3,g2)
    c: Vertical(g4)
    c: Symmetric(g2,g3,g-2)
    c: DistanceX(g5,g5) = 0.2
    c: Distance(g5,g1) = 0.25
    c: DistanceX(g3,g-1) = 0.25
    c: PointOnObject(g3,g1)
    c: PointOnObject(g2,g1)
    c: Distance(g3,g1) = 0.3
FEATURE [PartDesign::Revolution] Revolution026
  Angle = 360
  Axis = (10,0,0)
  Base = (-5,7.5,0)
  Profile = -> Sketch086
  ReferenceAxis = -> Sketch086 [Axis]
FEATURE [PartDesign::Body] Body090  label="Rivet 022"
  Group = -> [Sketch086,Revolution026]
  Origin = -> Origin107
  Placement = pos=(0,0,0) rot=(1,0,0;0.448799rad)
  Tip = -> Revolution026
FEATURE [PartDesign::FeatureBase] Clone049
  BaseFeature = -> Body090
  Placement = pos=(0,0,0) rot=(1,0,0;0.448799rad)
FEATURE [PartDesign::Body] Body091  label="Rivet 023"
  BaseFeature = -> Body090
  Group = -> [Clone049]
  Origin = -> Origin108
  Placement = pos=(0,0,0) rot=(1,0,0;0.897598rad)
  Tip = -> Clone049
FEATURE [PartDesign::FeatureBase] Clone050
  BaseFeature = -> Body090
  Placement = pos=(0,0,0) rot=(1,0,0;0.448799rad)
FEATURE [PartDesign::Body] Body092  label="Rivet 024"
  BaseFeature = -> Body090
  Group = -> [Clone050]
  Origin = -> Origin109
  Placement = pos=(0,0,0) rot=(1,0,0;1.7952rad)
  Tip = -> Clone050
FEATURE [PartDesign::FeatureBase] Clone051
  BaseFeature = -> Body090
  Placement = pos=(0,0,0) rot=(1,0,0;0.448799rad)
FEATURE [PartDesign::Body] Body093  label="Rivet 025"
  BaseFeature = -> Body090
  Group = -> [Clone051]
  Origin = -> Origin110
  Placement = pos=(0,0,0) rot=(1,0,0;2.69279rad)
  Tip = -> Clone051
FEATURE [PartDesign::FeatureBase] Clone052
  BaseFeature = -> Body090
  Placement = pos=(0,0,0) rot=(1,0,0;0.448799rad)
FEATURE [PartDesign::Body] Body094  label="Rivet 026"
  BaseFeature = -> Body090
  Group = -> [Clone052]
  Origin = -> Origin111
  Placement = pos=(0,0,0) rot=(1,0,0;3.59039rad)
  Tip = -> Clone052
FEATURE [PartDesign::FeatureBase] Clone053
  BaseFeature = -> Body090
  Placement = pos=(0,0,0) rot=(1,0,0;0.448799rad)
FEATURE [PartDesign::Body] Body095  label="Rivet 027"
  BaseFeature = -> Body090
  Group = -> [Clone053]
  Origin = -> Origin112
  Placement = pos=(0,0,0) rot=(-1,0,0;1.7952rad)
  Tip = -> Clone053
FEATURE [PartDesign::FeatureBase] Clone054
  BaseFeature = -> Body090
  Placement = pos=(0,0,0) rot=(1,0,0;0.448799rad)
FEATURE [PartDesign::Body] Body096  label="Rivet 028"
  BaseFeature = -> Body090
  Group = -> [Clone054]
  Origin = -> Origin113
  Placement = pos=(0,0,0) rot=(-1,0,0;0.897598rad)
  Tip = -> Clone054
FEATURE [App::DocumentObjectGroup] Group023  label="Rivets003"
  Group = -> [Body090,Body091,Body092,Body093,Body094,Body095,Body096]
FEATURE [Sketcher::SketchObject] Sketch087
  FullyConstrained = true
  MapMode = 5
  Placement = pos=(0,0,0) rot=(1,0,0;1.5708rad)
  Support = -> [XZ_Plane102]
  sketch-geometry (4):
    g0: LineSegment StartX=0 StartY=8.5 StartZ=0 EndX=0.1 EndY=8.5 EndZ=0
    g1: LineSegment StartX=0.1 StartY=8.5 StartZ=0 EndX=0.1 EndY=6.5 EndZ=0
    g2: LineSegment StartX=0.1 StartY=6.5 StartZ=0 EndX=0 EndY=6.5 EndZ=0
    g3: LineSegment StartX=0 StartY=6.5 StartZ=0 EndX=0 EndY=8.5 EndZ=0
  constraints (12):
    c: Coincident(g0,g1)
    c: Coincident(g1,g2)
    c: Coincident(g2,g3)
    c: Coincident(g3,g0)
    c: Horizontal(g0)
    c: Horizontal(g2)
    c: Vertical(g1)
    c: Vertical(g3)
    c: PointOnObject(g0,g-2)
    c: DistanceX(g0,g0) = 0.1
    c: DistanceY(g0) = 8.5
    c: DistanceY(g1) = 6.5
FEATURE [PartDesign::Revolution] Revolution027
  Angle = 360
  Axis = (1,0,0)
  Base = (0,0,0)
  Placement = pos=(0,0,0) rot=(1,0,0;1.5708rad)
  Profile = -> Sketch087
  ReferenceAxis = -> Sketch087 [H_Axis]
FEATURE [Sketcher::SketchObject] Sketch088
  FullyConstrained = true
  MapMode = 5
  Placement = pos=(0,0,0) rot=(0.57735,0.57735,0.57735;2.0944rad)
  Support = -> [YZ_Plane102]
  sketch-geometry (5):
    g0: ArcOfCircle CenterX=0 CenterY=7.5 CenterZ=0 NormalX=0 NormalY=0 NormalZ=1 AngleXU=0 Radius=2.11 StartAngle=5.66076 EndAngle=6.65667
    g1: LineSegment StartX=5e-16 StartY=8.5 StartZ=0 EndX=0 EndY=6.26986 EndZ=0
    g2: ArcOfCircle CenterX=0 CenterY=0 CenterZ=0 NormalX=0 NormalY=0 NormalZ=1 AngleXU=0 Radius=6.5 StartAngle=1.3039 EndAngle=1.5708
    g3: LineSegment StartX=1.71431 StartY=6.26986 StartZ=0 EndX=0 EndY=6.26986 EndZ=0
    g4: ArcOfCircle CenterX=0 CenterY=0 CenterZ=0 NormalX=0 NormalY=0 NormalZ=1 AngleXU=0 Radius=8.5 StartAngle=1.33757 EndAngle=1.5708
  constraints (16):
    c: PointOnObject(g0,g-2)
    c: DistanceY(g0) = 7.5
    c: Radius(g0) = 2.11
    c: PointOnObject(g2,g1)
    c: DistanceY(g2) = 6.5
    c: Coincident(g2,g-1)
    c: Coincident(g3,g2)
    c: Horizontal(g3)
    c: Coincident(g0,g2)
    c: Coincident(g1,g3)
    c: PointOnObject(g1,g-2)
    c: PointOnObject(g1,g-2)
    c: Coincident(g4,g-1)
    c: Coincident(g4,g1)
    c: DistanceY(g1) = 8.5
    c: Coincident(g0,g4)
FEATURE [PartDesign::Revolution] Revolution028
  Angle = 180
  Axis = (-2e-16,3e-16,1)
  Base = (0,0,0)
  BaseFeature = -> Revolution027
  Placement = pos=(0,0,0) rot=(1,0,0;1.5708rad)
  Profile = -> Sketch088
  ReferenceAxis = -> Sketch088 [V_Axis]
  Reversed = true
FEATURE [PartDesign::PolarPattern] PolarPattern012
  Angle = 360
  Axis = -> Sketch088 [N_Axis]
  BaseFeature = -> Revolution028
  Occurrences = 3
  Originals = -> [Revolution028]
  Placement = pos=(0,0,0) rot=(1,0,0;1.5708rad)
  Refine = true
FEATURE [Sketcher::SketchObject] Sketch089
  FullyConstrained = true
  MapMode = 5
  Placement = pos=(0,0,0) rot=(0.57735,0.57735,0.57735;2.0944rad)
  Support = -> [YZ_Plane102]
  sketch-geometry (4):
    g0: ArcOfCircle CenterX=0 CenterY=7.5 CenterZ=0 NormalX=0 NormalY=0 NormalZ=1 AngleXU=0 Radius=2.01 StartAngle=5.57985 EndAngle=6.86228
    g1: LineSegment StartX=0 StartY=6.2 StartZ=0 EndX=1.533 EndY=6.2 EndZ=0
    g2: LineSegment StartX=0 StartY=8.6 StartZ=0 EndX=0 EndY=6.2 EndZ=0
    g3: LineSegment StartX=0 StartY=8.6 StartZ=0 EndX=1.68229 EndY=8.6 EndZ=0
  constraints (13):
    c: PointOnObject(g0,g-2)
    c: DistanceY(g0) = 7.5
    c: Radius(g0) = 2.01
    c: PointOnObject(g1,g-2)
    c: Horizontal(g1)
    c: Coincident(g0,g1)
    c: DistanceY(g1) = 6.2
    c: DistanceY(g2) = 8.6
    c: Coincident(g2,g1)
    c: PointOnObject(g2,g-2)
    c: Coincident(g3,g2)
    c: Horizontal(g3)
    c: Coincident(g0,g3)
FEATURE [PartDesign::Groove] Groove003
  Angle = 360
  Axis = (-2e-16,3e-16,1)
  Base = (0,0,0)
  BaseFeature = -> PolarPattern012
  Placement = pos=(0,0,0) rot=(1,0,0;1.5708rad)
  Profile = -> Sketch089
  ReferenceAxis = -> Sketch089 [V_Axis]
FEATURE [PartDesign::PolarPattern] PolarPattern013
  Angle = 360
  Axis = -> Sketch089 [N_Axis]
  BaseFeature = -> Groove003
  Occurrences = 3
  Originals = -> [Groove003]
  Placement = pos=(0,0,0) rot=(1,0,0;1.5708rad)
FEATURE [PartDesign::Pocket] Pocket033
  BaseFeature = -> PolarPattern013
  Length = 5
  Length2 = 100
  Placement = pos=(0,0,0) rot=(1,0,0;1.5708rad)
  Profile = -> Sketch084
  Type = 1
FEATURE [PartDesign::PolarPattern] PolarPattern014
  Angle = 360
  Axis = -> Sketch084 [N_Axis]
  BaseFeature = -> Pocket033
  Occurrences = 3
  Originals = -> [Pocket033]
  Placement = pos=(0,0,0) rot=(1,0,0;1.5708rad)
FEATURE [PartDesign::Body] Body088  label="Cage 007"
  Group = -> [Sketch087,Revolution027,Sketch088,Revolution028,PolarPattern012,Sketch089,Groove003,PolarPattern013,Sketch084,Pocket033,PolarPattern014]
  Origin = -> Origin105
  Placement = pos=(0,0,0) rot=(-1,0,0;1.5708rad)
  Tip = -> PolarPattern014
FEATURE [PartDesign::FeatureBase] Clone048
  BaseFeature = -> Body088
  Placement = pos=(0,0,0) rot=(-1,0,0;1.5708rad)
FEATURE [PartDesign::Body] Body089  label="Cage 008"
  BaseFeature = -> Body088
  Group = -> [Clone048]
  Origin = -> Origin106
  Placement = pos=(0,0,0) rot=(0,1,0;3.14159rad)
  Tip = -> Clone048
FEATURE [App::DocumentObjectGroup] Group022  label="Cages003"
  Group = -> [Body088,Body089]
FEATURE [Sketcher::SketchObject] Sketch090
  FullyConstrained = true
  MapMode = 5
  Support = -> [XY_Plane111]
  sketch-geometry (14):
    g0: ArcOfCircle CenterX=-1e-16 CenterY=7.5 CenterZ=0 NormalX=0 NormalY=0 NormalZ=1 AngleXU=0 Radius=2 StartAngle=0.848062 EndAngle=2.29353
    g1: LineSegment StartX=-3.5 StartY=11 StartZ=0 EndX=3.5 EndY=11 EndZ=0
    g2: LineSegment StartX=3.5 StartY=11 StartZ=0 EndX=3.5 EndY=9.2 EndZ=0
    g3: LineSegment StartX=2.9 StartY=9 StartZ=0 EndX=1.32288 EndY=9 EndZ=0
    g4: LineSegment StartX=-3.5 StartY=9.2 StartZ=0 EndX=-3.5 EndY=11 EndZ=0
    g5: LineSegment StartX=-1.32288 StartY=9 StartZ=0 EndX=-2.9 EndY=9 EndZ=0
    g6: LineSegment StartX=2.9 StartY=9 StartZ=0 EndX=2.9 EndY=9.5 EndZ=0
    g7: LineSegment StartX=2.9 StartY=9.5 StartZ=0 EndX=3.2 EndY=9.5 EndZ=0
    g8: LineSegment StartX=3.2 StartY=9.5 StartZ=0 EndX=3.2 EndY=9.2 EndZ=0
    g9: LineSegment StartX=3.2 StartY=9.2 StartZ=0 EndX=3.5 EndY=9.2 EndZ=0
    g10: LineSegment StartX=-3.5 StartY=9.2 StartZ=0 EndX=-3.2 EndY=9.2 EndZ=0
    g11: LineSegment StartX=-3.2 StartY=9.2 StartZ=0 EndX=-3.2 EndY=9.5 EndZ=0
    g12: LineSegment StartX=-3.2 StartY=9.5 StartZ=0 EndX=-2.9 EndY=9.5 EndZ=0
    g13: LineSegment StartX=-2.9 StartY=9.5 StartZ=0 EndX=-2.9 EndY=9 EndZ=0
  constraints (41):
    c: Coincident(g1,g2)
    c: Coincident(g4,g1)
    c: Horizontal(g3)
    c: Vertical(g2)
    c: Vertical(g4)
    c: Coincident(g0,g5)
    c: Coincident(g0,g3)
    c: DistanceY(g-1,g0) = 7.5
    c: Radius(g0) = 2
    c: Symmetric(g1,g1,g-2)
    c: Symmetric(g0,g0,g-2)
    c: DistanceY(g1) = 11
    c: DistanceX(g1,g1) = 7
    c: Vertical(g6)
    c: Coincident(g6,g7)
    c: Horizontal(g7)
    c: Coincident(g7,g8)
    c: Vertical(g8)
    c: Coincident(g8,g9)
    c: Coincident(g3,g6)
    c: Coincident(g2,g9)
    c: Horizontal(g10)
    c: Coincident(g10,g11)
    c: Coincident(g11,g12)
    c: Horizontal(g12)
    c: Coincident(g12,g13)
    c: Vertical(g13)
    c: Vertical(g11)
    c: Coincident(g4,g10)
    c: Coincident(g5,g13)
    c: DistanceY(g13,g13) = 0.5
    c: DistanceX(g12,g12) = 0.3
    c: DistanceY(g5,g10) = 0.2
    c: Symmetric(g5,g3,g-2)
    c: DistanceY(g3) = 9
    c: DistanceY(g6) = 9.5
    c: Equal(g7,g12)
    c: Equal(g13,g6)
    c: Horizontal(g9)
    c: Horizontal(g8,g10)
    c: Equal(g12,g10)
FEATURE [PartDesign::Revolution] Revolution029
  Angle = 360
  Axis = (1,0,0)
  Base = (0,0,0)
  Profile = -> Sketch090
  ReferenceAxis = -> X_Axis111
FEATURE [PartDesign::Fillet] Fillet163
  Base = -> Revolution029 [Edge14,Edge15]
  BaseFeature = -> Revolution029
  Radius = 0.3
  SupportTransform = false
FEATURE [PartDesign::Body] Body097  label="Outer Ring004"
  Group = -> [Sketch090,Revolution029,Fillet163]
  Origin = -> Origin114
  Tip = -> Fillet163
FEATURE [Sketcher::SketchObject] Sketch091
  FullyConstrained = true
  MapMode = 5
  Support = -> [XY_Plane112]
  sketch-geometry (14):
    g0: LineSegment StartX=-2.9 StartY=6 StartZ=0 EndX=-1.32288 EndY=6 EndZ=0
    g1: LineSegment StartX=-3.5 StartY=4 StartZ=0 EndX=-3.5 EndY=5.7 EndZ=0
    g2: ArcOfCircle CenterX=-1e-16 CenterY=7.5 CenterZ=0 NormalX=0 NormalY=0 NormalZ=1 AngleXU=0 Radius=2 StartAngle=3.98965 EndAngle=5.43512
    g3: LineSegment StartX=1.32288 StartY=6 StartZ=0 EndX=2.9 EndY=6 EndZ=0
    g4: LineSegment StartX=-3.5 StartY=5.7 StartZ=0 EndX=-3.2 EndY=5.7 EndZ=0
    g5: LineSegment StartX=-3.2 StartY=5.7 StartZ=0 EndX=-3.2 EndY=5.5 EndZ=0
    g6: LineSegment StartX=-3.2 StartY=5.5 StartZ=0 EndX=-2.9 EndY=5.5 EndZ=0
    g7: LineSegment StartX=-2.9 StartY=5.5 StartZ=0 EndX=-2.9 EndY=6 EndZ=0
    g8: LineSegment StartX=8.5 StartY=6 StartZ=0 EndX=3.2 EndY=6 EndZ=0
    g9: LineSegment StartX=3.2 StartY=6 StartZ=0 EndX=3.2 EndY=5.5 EndZ=0
    g10: LineSegment StartX=3.2 StartY=5.5 StartZ=0 EndX=2.9 EndY=5.5 EndZ=0
    g11: LineSegment StartX=2.9 StartY=5.5 StartZ=0 EndX=2.9 EndY=6 EndZ=0
    g12: LineSegment StartX=8.5 StartY=4 StartZ=0 EndX=8.5 EndY=6 EndZ=0
    g13: LineSegment StartX=-3.5 StartY=4 StartZ=0 EndX=8.5 EndY=4 EndZ=0
  constraints (43):
    c: Horizontal(g0)
    c: Vertical(g1)
    c: DistanceY(g1) = 4
    c: Coincident(g2,g0)
    c: Coincident(g2,g3)
    c: Horizontal(g3)
    c: Radius(g2) = 2
    c: DistanceY(g2) = 7.5
    c: Symmetric(g0,g2,g-2)
    c: Horizontal(g4)
    c: Coincident(g4,g5)
    c: Vertical(g5)
    c: Coincident(g5,g6)
    c: Horizontal(g6)
    c: Coincident(g6,g7)
    c: Vertical(g7)
    c: Horizontal(g8)
    c: Coincident(g8,g9)
    c: Vertical(g9)
    c: Coincident(g9,g10)
    c: Horizontal(g10)
    c: Coincident(g10,g11)
    c: Vertical(g11)
    c: Coincident(g3,g11)
    c: Coincident(g0,g7)
    c: Coincident(g1,g4)
    c: DistanceY(g3) = 6
    c: DistanceY(g6,g0) = 0.5
    c: DistanceX(g4,g4) = 0.3
    c: DistanceX(g6,g6) = 0.3
    c: DistanceY(g5,g4) = 0.2
    c: Vertical(g12)
    c: Equal(g11,g7)
    c: DistanceY(g1,g0) = 2
    c: DistanceX(g8,g8) = 5.3
    c: Coincident(g13,g1)
    c: Coincident(g13,g12)
    c: Horizontal(g13)
    c: DistanceX(g13,g13) = 12
    c: DistanceX(g1,g2) = 3.5
    c: Coincident(g8,g12)
    c: Equal(g7,g9)
    c: Equal(g6,g10)
FEATURE [PartDesign::Revolution] Revolution030
  Angle = 360
  Axis = (1,0,0)
  Base = (0,0,0)
  Profile = -> Sketch091
  ReferenceAxis = -> X_Axis112
FEATURE [PartDesign::Fillet] Fillet164
  Base = -> Revolution030 [Edge13,Edge11]
  BaseFeature = -> Revolution030
  Radius = 0.2
  SupportTransform = false
FEATURE [PartDesign::Body] Body098  label="Inner Ring004"
  Group = -> [Sketch091,Revolution030,Fillet164]
  Origin = -> Origin115
  Tip = -> Fillet164
FEATURE [App::DocumentObjectGroup] Group025  label="Rings003"
  Group = -> [Body097,Body098]
FEATURE [Sketcher::SketchObject] Sketch092
  FullyConstrained = true
  MapMode = 5
  Placement = pos=(0,0,0) rot=(1,0,0;1.5708rad)
  Support = -> [XZ_Plane113]
  sketch-geometry (12):
    g0: LineSegment StartX=2.9 StartY=9.5 StartZ=0 EndX=2.9 EndY=8.5 EndZ=0
    g1: LineSegment StartX=2.9 StartY=8.5 StartZ=0 EndX=3.2 EndY=8.5 EndZ=0
    g2: LineSegment StartX=3.2 StartY=8.5 StartZ=0 EndX=3.2 EndY=6.5 EndZ=0
    g3: LineSegment StartX=3.2 StartY=6.5 StartZ=0 EndX=2.9 EndY=6.5 EndZ=0
    g4: LineSegment StartX=2.9 StartY=6.5 StartZ=0 EndX=2.9 EndY=5.5 EndZ=0
    g5: LineSegment StartX=2.9 StartY=5.5 StartZ=0 EndX=3.2 EndY=5.5 EndZ=0
    g6: LineSegment StartX=3.2 StartY=5.5 StartZ=0 EndX=3.2 EndY=6 EndZ=0
    g7: LineSegment StartX=3.2 StartY=6 StartZ=0 EndX=3.5 EndY=6 EndZ=0
    g8: LineSegment StartX=3.5 StartY=6 StartZ=0 EndX=3.5 EndY=9 EndZ=0
    g9: LineSegment StartX=3.5 StartY=9 StartZ=0 EndX=3.2 EndY=9 EndZ=0
    g10: LineSegment StartX=3.2 StartY=9 StartZ=0 EndX=3.2 EndY=9.5 EndZ=0
    g11: LineSegment StartX=3.2 StartY=9.5 StartZ=0 EndX=2.9 EndY=9.5 EndZ=0
  constraints (36):
    c: Vertical(g0)
    c: Coincident(g0,g1)
    c: Horizontal(g1)
    c: Coincident(g1,g2)
    c: Vertical(g2)
    c: Coincident(g2,g3)
    c: Horizontal(g3)
    c: Coincident(g3,g4)
    c: Vertical(g4)
    c: Coincident(g4,g5)
    c: Horizontal(g5)
    c: Coincident(g5,g6)
    c: Vertical(g6)
    c: Coincident(g6,g7)
    c: Horizontal(g7)
    c: Coincident(g7,g8)
    c: Vertical(g8)
    c: Coincident(g8,g9)
    c: Horizontal(g9)
    c: Coincident(g9,g10)
    c: Vertical(g10)
    c: Coincident(g10,g11)
    c: Coincident(g11,g0)
    c: Horizontal(g11)
    c: DistanceY(g4) = 5.5
    c: DistanceX(g4) = 2.9
    c: DistanceY(g5,g6) = 0.5
    c: DistanceY(g6,g2) = 0.5
    c: DistanceX(g5,g5) = 0.3
    c: Equal(g5,g7)
    c: Equal(g7,g3)
    c: Equal(g3,g1)
    c: Equal(g1,g9)
    c: Equal(g4,g0)
    c: Equal(g6,g10)
    c: DistanceY(g4,g0) = 4
FEATURE [PartDesign::Revolution] Revolution031
  Angle = 360
  Axis = (1,0,0)
  Base = (0,0,0)
  Placement = pos=(0,0,0) rot=(1,0,0;1.5708rad)
  Profile = -> Sketch092
  ReferenceAxis = -> Sketch092 [H_Axis]
FEATURE [PartDesign::Fillet] Fillet165
  Base = -> Revolution031 [Edge14,Edge12]
  BaseFeature = -> Revolution031
  Placement = pos=(0,0,0) rot=(1,0,0;1.5708rad)
  Radius = 0.2
  SupportTransform = false
FEATURE [PartDesign::Body] Body099  label="Seal 007"
  Group = -> [Sketch092,Revolution031,Fillet165]
  Origin = -> Origin116
  Tip = -> Fillet165
FEATURE [PartDesign::FeatureBase] Clone055
  BaseFeature = -> Body099
FEATURE [PartDesign::Body] Body100  label="Seal 008"
  BaseFeature = -> Body099
  Group = -> [Clone055]
  Origin = -> Origin117
  Placement = pos=(0,0,0) rot=(0,1,0;3.14159rad)
  Tip = -> Clone055
FEATURE [App::DocumentObjectGroup] Group024  label="Seals003"
  Group = -> [Body099,Body100]
FEATURE [Sketcher::SketchObject] Sketch093
  AttachmentOffset = pos=(0,0,4) rot=(0,0,1;0rad)
  FullyConstrained = true
  MapMode = 5
  Placement = pos=(0,0,4) rot=(0,0,1;0rad)
  Support = -> [XY_Plane094]
  sketch-geometry (1):
    g0: Circle CenterX=6 CenterY=0 CenterZ=0 NormalX=0 NormalY=0 NormalZ=1 AngleXU=0 Radius=1.5
  constraints (3):
    c: PointOnObject(g0,g-1)
    c: Diameter(g0) = 3
    c: DistanceX(g-1,g0) = 6
FEATURE [PartDesign::Pad] Pad020
  Direction = (0,0,1)
  Length = 3
  Length2 = 100
  Profile = -> Sketch093
  Type = 0
FEATURE [Sketcher::SketchObject] Sketch094
  ExternalGeometry = -> [Pad020]
  FullyConstrained = true
  MapMode = 5
  Placement = pos=(0,0,7) rot=(0,0,1;0rad)
  Support = -> [Pad020]
  sketch-geometry (7):
    g0: LineSegment StartX=6.43301 StartY=-0.75 StartZ=0 EndX=6.86603 EndY=0 EndZ=0
    g1: LineSegment StartX=6.86603 StartY=0 StartZ=0 EndX=6.43301 EndY=0.75 EndZ=0
    g2: LineSegment StartX=6.43301 StartY=0.75 StartZ=0 EndX=5.56699 EndY=0.75 EndZ=0
    g3: LineSegment StartX=5.56699 StartY=0.75 StartZ=0 EndX=5.13397 EndY=-1e-16 EndZ=0
    g4: LineSegment StartX=5.13397 StartY=-1e-16 StartZ=0 EndX=5.56699 EndY=-0.75 EndZ=0
    g5: LineSegment StartX=5.56699 StartY=-0.75 StartZ=0 EndX=6.43301 EndY=-0.75 EndZ=0
    g6: Circle CenterX=6 CenterY=0 CenterZ=0 NormalX=0 NormalY=0 NormalZ=1 AngleXU=0 Radius=0.866025
  constraints (16):
    c: Coincident(g0,g1)
    c: Coincident(g1,g2)
    c: Coincident(g2,g3)
    c: Coincident(g3,g4)
    c: Coincident(g4,g5)
    c: Coincident(g5,g0)
    c: Equal(g0, g1-g5) x5
    c: PointOnObject(g0,g6)
    c: PointOnObject(g1,g6)
    c: PointOnObject(g2,g6)
    c: PointOnObject(g3,g6)
    c: PointOnObject(g4,g6)
    c: PointOnObject(g5,g6)
    c: Coincident(g6,g-3)
    c: Horizontal(g5)
    c: DistanceY(g4,g2) = 1.5
FEATURE [PartDesign::Pocket] Pocket034
  BaseFeature = -> Pad020
  Length = 0.9
  Length2 = 100
  Profile = -> Sketch094
  Type = 0
FEATURE [PartDesign::PolarPattern] PolarPattern015
  Angle = 120
  Axis = -> X_Axis094
  BaseFeature = -> Pocket034
  Occurrences = 3
  Originals = -> [Pad020,Pocket034]
FEATURE [PartDesign::Body] Body080
  Group = -> [Sketch093,Pad020,Sketch094,Pocket034,PolarPattern015]
  Origin = -> Origin097
  Tip = -> PolarPattern015
FEATURE [App::DocumentObjectGroup] Group026  label="Set screws003"
  Group = -> [Body080]
FEATURE [Sketcher::SketchObject] Sketch095
  AttachmentOffset = pos=(0,0,-6.5) rot=(0,0,1;0rad)
  FullyConstrained = true
  MapMode = 5
  Placement = pos=(-6.5,1.4e-15,-1.4e-15) rot=(0.57735,0.57735,0.57735;2.0944rad)
  Support = -> [YZ_Plane115]
  sketch-geometry (14):
    g0: Circle CenterX=0 CenterY=0 CenterZ=0 NormalX=0 NormalY=0 NormalZ=1 AngleXU=0 Radius=11
    g1: ArcOfCircle CenterX=0 CenterY=0 CenterZ=0 NormalX=0 NormalY=0 NormalZ=1 AngleXU=0 Radius=13.5 StartAngle=0.0668757 EndAngle=3.07472
    g2: LineSegment StartX=-13.4698 StartY=0.902148 StartZ=0 EndX=-14.2 EndY=-10 EndZ=0
    g3: LineSegment StartX=-14.2 StartY=-10 StartZ=0 EndX=-27.5 EndY=-10 EndZ=0
    g4: LineSegment StartX=-27.5 StartY=-10 StartZ=0 EndX=-27.5 EndY=-15 EndZ=0
    g5: LineSegment StartX=-27.5 StartY=-15 StartZ=0 EndX=-12.3 EndY=-15 EndZ=0
    g6: LineSegment StartX=27.5 StartY=-15 StartZ=0 EndX=27.5 EndY=-10 EndZ=0
    g7: LineSegment StartX=27.5 StartY=-10 StartZ=0 EndX=14.2 EndY=-10 EndZ=0
    g8: LineSegment StartX=14.2 StartY=-10 StartZ=0 EndX=13.4698 EndY=0.902148 EndZ=0
    g9: LineSegment StartX=12.3 StartY=-15 StartZ=0 EndX=12.1995 EndY=-13.5 EndZ=0
    g10: LineSegment StartX=12.1995 StartY=-13.5 StartZ=0 EndX=-12.1995 EndY=-13.5 EndZ=0
    g11: LineSegment StartX=-12.1995 StartY=-13.5 StartZ=0 EndX=-12.3 EndY=-15 EndZ=0
    g12: LineSegment StartX=12.3 StartY=-15 StartZ=0 EndX=27.5 EndY=-15 EndZ=0
    g13: GeomPoint X=0 Y=13.5 Z=0
  constraints (39):
    c: Coincident(g0,g-1)
    c: Radius(g0) = 11
    c: Coincident(g1,g0)
    c: Coincident(g2,g3)
    c: Coincident(g3,g4)
    c: Coincident(g4,g5)
    c: Horizontal(g5)
    c: Coincident(g12,g6)
    c: Coincident(g6,g7)
    c: Horizontal(g7)
    c: Coincident(g7,g8)
    c: Coincident(g9,g10)
    c: Horizontal(g10)
    c: Coincident(g10,g11)
    c: Coincident(g5,g11)
    c: Coincident(g12,g9)
    c: Horizontal(g3)
    c: Vertical(g6)
    c: Vertical(g4)
    c: Equal(g9,g11)
    c: Horizontal(g12)
    c: Horizontal(g5,g9)
    c: Equal(g6,g4)
    c: Equal(g12,g5)
    c: Equal(g7,g3)
    c: DistanceX(g4,g6) = 55
    c: DistanceY(g6,g0) = 15
    c: Equal(g8,g2)
    c: DistanceY(g6,g6) = 5
    c: Parallel(g9,g8)
    c: DistanceY(g9,g9) = 1.5
    c: DistanceX(g5,g5) = 15.2
    c: Diameter(g1) = 27
    c: PointOnObject(g13,g1)
    c: PointOnObject(g13,g-2)
    c: DistanceY(g6,g13) = 28.5
    c: Tangent(g1,g2) = -1.5708
    c: Tangent(g1,g8) = -1.5708
    c: DistanceX(g3,g3) = 13.3
FEATURE [PartDesign::Pad] Pad021
  Direction = (1,-2e-16,3e-16)
  Length = 13
  Length2 = 100
  Placement = pos=(0,0,0) rot=(0.57735,0.57735,0.57735;2.0944rad)
  Profile = -> Sketch095
  Type = 0
FEATURE [Sketcher::SketchObject] Sketch096
  ExternalGeometry = -> [Pad021]
  FullyConstrained = true
  MapMode = 5
  Placement = pos=(4.2e-15,-6.6e-15,-15) rot=(0.707107,0.707107,0;3.14159rad)
  Support = -> [Pad021]
  sketch-geometry (7):
    g0: LineSegment StartX=-24.9 StartY=4.15 StartZ=0 EndX=-14.9 EndY=4.15 EndZ=0
    g1: LineSegment StartX=-14.9 StartY=4.15 StartZ=0 EndX=-14.9 EndY=-4.15 EndZ=0
    g2: LineSegment StartX=-14.9 StartY=-4.15 StartZ=0 EndX=-24.9 EndY=-4.15 EndZ=0
    g3: LineSegment StartX=-24.9 StartY=-4.15 StartZ=0 EndX=-24.9 EndY=4.15 EndZ=0
    g4: LineSegment StartX=-27.5 StartY=6.5 StartZ=0 EndX=-12.3 EndY=-6.5 EndZ=0
    g5: LineSegment StartX=-27.5 StartY=-6.5 StartZ=0 EndX=-12.3 EndY=6.5 EndZ=0
    g6: GeomPoint X=-19.9 Y=2.6e-15 Z=0
  constraints (17):
    c: Coincident(g0,g1)
    c: Coincident(g1,g2)
    c: Coincident(g2,g3)
    c: Coincident(g3,g0)
    c: Horizontal(g0)
    c: Horizontal(g2)
    c: Vertical(g1)
    c: Vertical(g3)
    c: DistanceX(g0,g0) = 10
    c: DistanceY(g1,g1) = 8.3
    c: Coincident(g4,g-3)
    c: Coincident(g4,g-4)
    c: Coincident(g5,g-4)
    c: Coincident(g5,g-3)
    c: PointOnObject(g6,g4)
    c: PointOnObject(g6,g5)
    c: Symmetric(g0,g1,g6)
FEATURE [PartDesign::Pocket] Pocket035
  BaseFeature = -> Pad021
  Length = 2.3
  Length2 = 100
  Placement = pos=(0,0,0) rot=(0.57735,0.57735,0.57735;2.0944rad)
  Profile = -> Sketch096
  Type = 0
FEATURE [Sketcher::SketchObject] Sketch097
  ExternalGeometry = -> [Pocket035]
  FullyConstrained = true
  MapMode = 5
  Placement = pos=(2.8e-15,-4.4e-15,-10) rot=(0,0,-1;1.5708rad)
  Support = -> [Pocket035]
  sketch-geometry (2):
    g0: Circle CenterX=21.2 CenterY=2.1e-15 CenterZ=0 NormalX=0 NormalY=0 NormalZ=1 AngleXU=0 Radius=2.5
    g1: LineSegment StartX=21.2 StartY=2.1e-15 StartZ=0 EndX=27.5 EndY=2.1e-15 EndZ=0
  constraints (5):
    c: Diameter(g0) = 5
    c: DistanceX(g0,g-3) = 6.3
    c: Coincident(g1,g0)
    c: Horizontal(g1)
    c: Symmetric(g-5,g-5,g1)
FEATURE [PartDesign::Pocket] Pocket036
  BaseFeature = -> Pocket035
  Length = 5
  Length2 = 100
  Placement = pos=(0,0,0) rot=(0.57735,0.57735,0.57735;2.0944rad)
  Profile = -> Sketch097
  Type = 2
FEATURE [Sketcher::SketchObject] Sketch098
  ExternalGeometry = -> [Pocket036]
  FullyConstrained = true
  MapMode = 5
  Placement = pos=(6.5,-1.4e-15,1.5e-15) rot=(0.57735,0.57735,0.57735;2.0944rad)
  Support = -> [Pocket036]
  sketch-geometry (6):
    g0: LineSegment StartX=-24.6 StartY=-13.7 StartZ=0 EndX=-24.6 EndY=-11.3 EndZ=0
    g1: LineSegment StartX=-24.6 StartY=-11.3 StartZ=0 EndX=-14.2 EndY=-11.3 EndZ=0
    g2: LineSegment StartX=-14.2 StartY=-11.3 StartZ=0 EndX=-14.2 EndY=-13.7 EndZ=0
    g3: LineSegment StartX=-14.2 StartY=-13.7 StartZ=0 EndX=-24.6 EndY=-13.7 EndZ=0
    g4: GeomPoint X=-19.4 Y=-12.5 Z=0
    g5: LineSegment StartX=-19.4 StartY=-12.5 StartZ=0 EndX=-27.5 EndY=-12.5 EndZ=0
  constraints (15):
    c: Coincident(g0,g1)
    c: Coincident(g1,g2)
    c: Coincident(g2,g3)
    c: Coincident(g3,g0)
    c: Horizontal(g1)
    c: Horizontal(g3)
    c: Vertical(g0)
    c: Vertical(g2)
    c: Symmetric(g1,g0,g4)
    c: DistanceX(g1,g1) = 10.4
    c: DistanceY(g2,g2) = 2.4
    c: DistanceX(g2,g-4) = 1.9
    c: Coincident(g5,g4)
    c: Horizontal(g5)
    c: Symmetric(g-5,g-5,g5)
FEATURE [PartDesign::Pocket] Pocket037
  BaseFeature = -> Pocket036
  Length = 0.4
  Length2 = 100
  Placement = pos=(0,0,0) rot=(0.57735,0.57735,0.57735;2.0944rad)
  Profile = -> Sketch098
  Type = 0
FEATURE [PartDesign::Mirrored] Mirrored003
  BaseFeature = -> Pocket037
  MirrorPlane = -> Sketch096 [V_Axis]
  Originals = -> [Pocket035,Pocket036,Pocket037]
  Placement = pos=(0,0,0) rot=(0.57735,0.57735,0.57735;2.0944rad)
FEATURE [Sketcher::SketchObject] Sketch099
  ExternalGeometry = -> [Mirrored003]
  FullyConstrained = true
  MapMode = 5
  Placement = pos=(0,0,0) rot=(1,0,0;1.5708rad)
  Support = -> [XZ_Plane115]
  sketch-geometry (9):
    g0: GeomPoint X=-6.5 Y=13.5 Z=0
    g1: LineSegment StartX=6.5 StartY=-10 StartZ=0 EndX=6.5 EndY=13.5 EndZ=0
    g2: LineSegment StartX=6.5 StartY=13.5 StartZ=0 EndX=4.75 EndY=13.5 EndZ=0
    g3: LineSegment StartX=-6.5 StartY=13.5 StartZ=0 EndX=-4.75 EndY=13.5 EndZ=0
    g4: LineSegment StartX=-6.5 StartY=-10 StartZ=0 EndX=-6.5 EndY=13.5 EndZ=0
    g5: LineSegment StartX=6.5 StartY=-10 StartZ=0 EndX=4.75 EndY=-1 EndZ=0
    g6: LineSegment StartX=4.75 StartY=-1 StartZ=0 EndX=4.75 EndY=13.5 EndZ=0
    g7: LineSegment StartX=-4.75 StartY=13.5 StartZ=0 EndX=-4.75 EndY=-1 EndZ=0
    g8: LineSegment StartX=-4.75 StartY=-1 StartZ=0 EndX=-6.5 EndY=-10 EndZ=0
  constraints (24):
    c: Vertical(g0,g-4)
    c: Horizontal(g-3,g0)
    c: Coincident(g1,g-3)
    c: Coincident(g1,g2)
    c: Horizontal(g2)
    c: Coincident(g3,g0)
    c: Horizontal(g3)
    c: Coincident(g4,g3)
    c: Vertical(g4,g-4)
    c: DistanceX(g3,g2) = 9.5
    c: Equal(g2,g3)
    c: Horizontal(g1,g4)
    c: Coincident(g1,g-5)
    c: Coincident(g1,g5)
    c: Coincident(g5,g6)
    c: Coincident(g6,g2)
    c: Vertical(g6)
    c: DistanceY(g1,g5) = 9
    c: Coincident(g3,g7)
    c: Vertical(g7)
    c: Coincident(g7,g8)
    c: Coincident(g8,g4)
    c: Horizontal(g7,g5)
    c: DistanceX(g2,g2) = 1.75
FEATURE [PartDesign::Pocket] Pocket038
  BaseFeature = -> Mirrored003
  Length = 15
  Length2 = 15
  Placement = pos=(0,0,0) rot=(0.57735,0.57735,0.57735;2.0944rad)
  Profile = -> Sketch099
  Type = 4
FEATURE [Sketcher::SketchObject] Sketch100
  FullyConstrained = true
  MapMode = 5
  Placement = pos=(-6.5,1.4e-15,-1.5e-15) rot=(0.57735,0.57735,-0.57735;4.18879rad)
  Support = -> [Pocket038]
  sketch-geometry (1):
    g0: Circle CenterX=0 CenterY=0 CenterZ=0 NormalX=0 NormalY=0 NormalZ=1 AngleXU=0 Radius=12.2
  constraints (2):
    c: Coincident(g0,g-1)
    c: Diameter(g0) = 24.4
FEATURE [PartDesign::Pocket] Pocket039
  BaseFeature = -> Pocket038
  Length = 2.75
  Length2 = 100
  Placement = pos=(0,0,0) rot=(0.57735,0.57735,0.57735;2.0944rad)
  Profile = -> Sketch100
  Type = 0
FEATURE [Sketcher::SketchObject] Sketch101
  FullyConstrained = true
  MapMode = 5
  Placement = pos=(6.5,-1.4e-15,1.5e-15) rot=(0.57735,0.57735,0.57735;2.0944rad)
  Support = -> [Pocket039]
  sketch-geometry (1):
    g0: Circle CenterX=0 CenterY=0 CenterZ=0 NormalX=0 NormalY=0 NormalZ=1 AngleXU=0 Radius=12.1
  constraints (2):
    c: Coincident(g0,g-1)
    c: Diameter(g0) = 24.2
FEATURE [PartDesign::Pocket] Pocket040
  BaseFeature = -> Pocket039
  Length = 2.75
  Length2 = 100
  Placement = pos=(0,0,0) rot=(0.57735,0.57735,0.57735;2.0944rad)
  Profile = -> Sketch101
  Type = 0
FEATURE [Sketcher::SketchObject] Sketch102
  ExternalGeometry = -> [Pocket040]
  FullyConstrained = true
  MapMode = 5
  Placement = pos=(6.5,-1.4e-15,1.5e-15) rot=(0.57735,0.57735,0.57735;2.0944rad)
  Support = -> [Pocket040]
  sketch-geometry (6):
    g0: ArcOfCircle CenterX=0 CenterY=0 CenterZ=0 NormalX=0 NormalY=0 NormalZ=1 AngleXU=0 Radius=13.5 StartAngle=3.79664 EndAngle=5.62814
    g1: LineSegment StartX=-11.8698 StartY=-8.57666 StartZ=0 EndX=-12.3 EndY=-15 EndZ=0
    g2: LineSegment StartX=-12.3 StartY=-15 StartZ=0 EndX=12.3 EndY=-15 EndZ=0
    g3: LineSegment StartX=12.3 StartY=-15 StartZ=0 EndX=11.8698 EndY=-8.57666 EndZ=0
    g4: ArcOfCircle CenterX=11.2212 CenterY=-8.6201 CenterZ=0 NormalX=0 NormalY=0 NormalZ=1 AngleXU=0 Radius=0.65 StartAngle=0.0668757 EndAngle=2.48655
    g5: ArcOfCircle CenterX=-11.2212 CenterY=-8.6201 CenterZ=0 NormalX=0 NormalY=0 NormalZ=1 AngleXU=0 Radius=0.65 StartAngle=0.655044 EndAngle=3.07472
  constraints (14):
    c: Coincident(g0,g-1)
    c: Diameter(g0) = 27
    c: Coincident(g1,g2)
    c: Coincident(g2,g3)
    c: Coincident(g1,g-3)
    c: Coincident(g2,g-4)
    c: Tangent(g3,g4) = -1.5708
    c: Tangent(g0,g4) = 1.5708
    c: Tangent(g0,g5) = 1.5708
    c: Tangent(g1,g5) = -1.5708
    c: Equal(g4,g5)
    c: Horizontal(g4,g5)
    c: Parallel(g-4,g3)
    c: Radius(g4) = 0.65
FEATURE [PartDesign::Pocket] Pocket041
  BaseFeature = -> Pocket040
  Length = 5.25
  Length2 = 100
  Placement = pos=(0,0,0) rot=(0.57735,0.57735,0.57735;2.0944rad)
  Profile = -> Sketch102
  Type = 0
FEATURE [Sketcher::SketchObject] Sketch103
  ExternalGeometry = -> [Pocket041]
  FullyConstrained = true
  MapMode = 5
  Placement = pos=(-6.5,1.4e-15,-1.5e-15) rot=(0.57735,0.57735,-0.57735;4.18879rad)
  Support = -> [Pocket041]
  sketch-geometry (6):
    g0: ArcOfCircle CenterX=0 CenterY=0 CenterZ=0 NormalX=0 NormalY=0 NormalZ=1 AngleXU=0 Radius=13.5 StartAngle=0.655044 EndAngle=2.48655
    g1: LineSegment StartX=11.8698 StartY=8.57666 StartZ=0 EndX=12.3 EndY=15 EndZ=0
    g2: LineSegment StartX=12.3 StartY=15 StartZ=0 EndX=-12.3 EndY=15 EndZ=0
    g3: LineSegment StartX=-12.3 StartY=15 StartZ=0 EndX=-11.8698 EndY=8.57666 EndZ=0
    g4: ArcOfCircle CenterX=-11.2212 CenterY=8.6201 CenterZ=0 NormalX=0 NormalY=0 NormalZ=1 AngleXU=0 Radius=0.65 StartAngle=3.20847 EndAngle=5.62814
    g5: ArcOfCircle CenterX=11.2212 CenterY=8.6201 CenterZ=0 NormalX=0 NormalY=0 NormalZ=1 AngleXU=0 Radius=0.65 StartAngle=3.79664 EndAngle=6.21631
  constraints (14):
    c: Coincident(g0,g-1)
    c: Radius(g0) = 13.5
    c: Coincident(g1,g2)
    c: Coincident(g2,g-3)
    c: Coincident(g2,g3)
    c: Coincident(g-4,g1)
    c: Tangent(g3,g4) = -1.5708
    c: Tangent(g0,g4) = 1.5708
    c: Tangent(g0,g5) = 1.5708
    c: Tangent(g1,g5) = -1.5708
    c: Equal(g4,g5)
    c: Radius(g4) = 0.65
    c: Parallel(g-4,g1)
    c: Parallel(g3,g-3)
FEATURE [PartDesign::Pocket] Pocket042
  BaseFeature = -> Pocket041
  Length = 5.25
  Length2 = 100
  Placement = pos=(0,0,0) rot=(0.57735,0.57735,0.57735;2.0944rad)
  Profile = -> Sketch103
  Type = 0
FEATURE [PartDesign::Chamfer] Chamfer003
  Angle = 45
  Base = -> Pocket042 [Edge159,Edge155,Edge22,Edge27]
  BaseFeature = -> Pocket042
  ChamferType = 0
  FlipDirection = false
  Placement = pos=(0,0,0) rot=(0.57735,0.57735,0.57735;2.0944rad)
  Size = 2
  Size2 = 1
  SupportTransform = false
FEATURE [Sketcher::SketchObject] Sketch104
  ExternalGeometry = -> [Chamfer003]
  FullyConstrained = true
  MapMode = 5
  Placement = pos=(-3.75,5e-15,-2.7e-15) rot=(-0.57735,-0.57735,0.57735;2.0944rad)
  Support = -> [Chamfer003]
  sketch-geometry (13):
    g0: ArcOfCircle CenterX=-6.9e-15 CenterY=-3.7e-15 CenterZ=0 NormalX=0 NormalY=0 NormalZ=1 AngleXU=0 Radius=11 StartAngle=5.75419 EndAngle=6.81218
    g1: ArcOfCircle CenterX=-6.9e-15 CenterY=-3.7e-15 CenterZ=0 NormalX=0 NormalY=0 NormalZ=1 AngleXU=0 Radius=12.2 StartAngle=5.94045 EndAngle=6.62592
    g2: ArcOfCircle CenterX=-6.9e-15 CenterY=-3.7e-15 CenterZ=0 NormalX=0 NormalY=0 NormalZ=1 AngleXU=0 Radius=11 StartAngle=2.6126 EndAngle=3.67059
    g3: ArcOfCircle CenterX=-6.9e-15 CenterY=-3.7e-15 CenterZ=0 NormalX=0 NormalY=0 NormalZ=1 AngleXU=0 Radius=12.2 StartAngle=2.79886 EndAngle=3.48433
    g4: Ellipse CenterX=-6.9e-15 CenterY=-3.7e-15 CenterZ=0 NormalX=0 NormalY=0 NormalZ=1 MajorRadius=13.5 MinorRadius=7.81051 AngleXU=-3e-16
    g5: LineSegment StartX=13.5 StartY=-7.4e-15 StartZ=0 EndX=-13.5 EndY=0 EndZ=0
    g6: LineSegment StartX=-4.8e-15 StartY=7.81051 StartZ=0 EndX=-9.1e-15 EndY=-7.81051 EndZ=0
    g7: GeomPoint X=11.0112 Y=-6.8e-15 Z=0
    g8: GeomPoint X=-11.0112 Y=-7e-16 Z=0
    g9: LineSegment StartX=-11.4904 StartY=4.1 StartZ=0 EndX=-9.49645 EndY=5.55135 EndZ=0
    g10: LineSegment StartX=-11.4904 StartY=-4.1 StartZ=0 EndX=-9.49645 EndY=-5.55135 EndZ=0
    g11: LineSegment StartX=9.49645 StartY=-5.55135 StartZ=0 EndX=11.4904 EndY=-4.1 EndZ=0
    g12: LineSegment StartX=11.4904 StartY=4.1 StartZ=0 EndX=9.49645 EndY=5.55135 EndZ=0
  constraints (29):
    c: Coincident(g0,g-4)
    c: PointOnObject(g0,g-4)
    c: Coincident(g1,g0)
    c: PointOnObject(g1,g-3)
    c: Coincident(g2,g0)
    c: PointOnObject(g2,g-4)
    c: Coincident(g3,g0)
    c: PointOnObject(g3,g-3)
    c: InternalAlignment(g5-g8 -> g4) x4
    c: Coincident(g4,g0)
    c: PointOnObject(g3,g4)
    c: PointOnObject(g2,g4)
    c: PointOnObject(g3,g4)
    c: PointOnObject(g2,g4)
    c: PointOnObject(g0,g4)
    c: PointOnObject(g1,g4)
    c: PointOnObject(g1,g4)
    c: PointOnObject(g0,g4)
    c: PointOnObject(g5,g-1)
    c: DistanceX(g5,g5) = 27
    c: DistanceY(g3,g3) = 8.2
    c: Coincident(g9,g3)
    c: Coincident(g9,g2)
    c: Coincident(g10,g3)
    c: Coincident(g10,g2)
    c: Coincident(g11,g0)
    c: Coincident(g11,g1)
    c: Coincident(g12,g1)
    c: Coincident(g12,g0)
FEATURE [PartDesign::Pocket] Pocket043
  BaseFeature = -> Chamfer003
  Length = 5
  Length2 = 100
  Placement = pos=(0,0,0) rot=(0.57735,0.57735,0.57735;2.0944rad)
  Profile = -> Sketch104
  Type = 0
FEATURE [PartDesign::Body] Body101  label="Metal case003"
  Group = -> [Sketch095,Pad021,Sketch096,Pocket035,Sketch097,Pocket036,Sketch098,Pocket037,Mirrored003,Sketch099,Pocket038,Sketch100,Pocket039,Sketch101,Pocket040,Sketch102,Pocket041,Sketch103,Pocket042,Chamfer003,Sketch104,Pocket043]
  Origin = -> Origin118
  Tip = -> Pocket043
FEATURE [App::DocumentObjectGroup] Group027  label="Case003"
  Group = -> [Body101]
FEATURE [App::Part] Part017  label="KP08-004"
  Group = -> [Group021,Body082,Body081,Body086,Body083,Body087,Body085,Body084,Group022,Body089,Body088,Group023,Body094,Body093,Body096,Body092,Body095,Body091,Body090,Group024,Body100,Body099,Group025,Body097,Body098,Group026,Body080,Group027,Body101]
  Origin = -> Origin119
  Placement = pos=(332,246,105) rot=(0,0,1;3.14159rad)
FEATURE [Sketcher::SketchObject] Sketch105
  FullyConstrained = true
  MapMode = 5
  Placement = pos=(0,0,0) rot=(-0.57735,0.57735,0.57735;4.18879rad)
  Support = -> [YZ_Plane124]
  sketch-geometry (1):
    g0: Circle CenterX=0 CenterY=-7.5 CenterZ=0 NormalX=0 NormalY=0 NormalZ=1 AngleXU=0 Radius=0.25
  constraints (3):
    c: PointOnObject(g0,g-2)
    c: DistanceY(g0) = -7.5
    c: Diameter(g0) = 0.5
FEATURE [Sketcher::SketchObject] Sketch106
  FullyConstrained = true
  MapMode = 5
  Support = -> [XY_Plane117]
  sketch-geometry (2):
    g0: LineSegment StartX=0 StartY=5.5 StartZ=0 EndX=6e-16 EndY=9.5 EndZ=0
    g1: ArcOfCircle CenterX=0 CenterY=7.5 CenterZ=0 NormalX=0 NormalY=0 NormalZ=1 AngleXU=0 Radius=2 StartAngle=4.71239 EndAngle=7.85398
  constraints (7):
    c: PointOnObject(g0,g-2)
    c: PointOnObject(g0,g-2)
    c: PointOnObject(g1,g0)
    c: Coincident(g1,g0)
    c: Coincident(g1,g0)
    c: Radius(g1) = 2
    c: DistanceY(g1) = 7.5
FEATURE [PartDesign::Revolution] Revolution032
  Angle = 360
  Axis = (0,1,0)
  Base = (0,0,0)
  Profile = -> Sketch106
  ReferenceAxis = -> Sketch106 [V_Axis]
  Reversed = true
FEATURE [PartDesign::Body] Body103  label="Ball 029"
  Group = -> [Sketch106,Revolution032]
  Origin = -> Origin121
  Tip = -> Revolution032
FEATURE [PartDesign::FeatureBase] Clone056
  BaseFeature = -> Body103
FEATURE [PartDesign::Body] Body104  label="Ball 030"
  BaseFeature = -> Body103
  Group = -> [Clone056]
  Origin = -> Origin122
  Placement = pos=(0,0,0) rot=(-1,0,0;0.897598rad)
  Tip = -> Clone056
FEATURE [PartDesign::FeatureBase] Clone057
  BaseFeature = -> Body103
FEATURE [PartDesign::Body] Body105  label="Ball 031"
  BaseFeature = -> Body103
  Group = -> [Clone057]
  Origin = -> Origin123
  Placement = pos=(0,0,0) rot=(-1,0,0;1.7952rad)
  Tip = -> Clone057
FEATURE [PartDesign::FeatureBase] Clone058
  BaseFeature = -> Body103
FEATURE [PartDesign::Body] Body106  label="Ball 032"
  BaseFeature = -> Body103
  Group = -> [Clone058]
  Origin = -> Origin124
  Placement = pos=(0,0,0) rot=(1,0,0;3.59039rad)
  Tip = -> Clone058
FEATURE [PartDesign::FeatureBase] Clone059
  BaseFeature = -> Body103
FEATURE [PartDesign::Body] Body107  label="Ball 033"
  BaseFeature = -> Body103
  Group = -> [Clone059]
  Origin = -> Origin125
  Placement = pos=(0,0,0) rot=(1,0,0;2.69279rad)
  Tip = -> Clone059
FEATURE [PartDesign::FeatureBase] Clone060
  BaseFeature = -> Body103
FEATURE [PartDesign::Body] Body108  label="Ball 034"
  BaseFeature = -> Body103
  Group = -> [Clone060]
  Origin = -> Origin126
  Placement = pos=(0,0,0) rot=(1,0,0;1.7952rad)
  Tip = -> Clone060
FEATURE [PartDesign::FeatureBase] Clone061
  BaseFeature = -> Body103
FEATURE [PartDesign::Body] Body109  label="Ball 035"
  BaseFeature = -> Body103
  Group = -> [Clone061]
  Origin = -> Origin127
  Placement = pos=(0,0,0) rot=(1,0,0;0.897598rad)
  Tip = -> Clone061
FEATURE [App::DocumentObjectGroup] Group028  label="Balls004"
  Group = -> [Body103,Body104,Body105,Body106,Body107,Body108,Body109]
FEATURE [Sketcher::SketchObject] Sketch107
  FullyConstrained = true
  MapMode = 5
  Support = -> [XY_Plane126]
  sketch-geometry (7):
    g0: LineSegment StartX=-5 StartY=7.5 StartZ=0 EndX=5 EndY=7.5 EndZ=0
    g1: LineSegment StartX=-0.210977 StartY=7.5 StartZ=0 EndX=0.210977 EndY=7.5 EndZ=0
    g2: ArcOfCircle CenterX=0.25 CenterY=7.5 CenterZ=0 NormalX=0 NormalY=0 NormalZ=1 AngleXU=0 Radius=0.460977 StartAngle=2.43297 EndAngle=3.14159
    g3: ArcOfCircle CenterX=-0.25 CenterY=7.5 CenterZ=0 NormalX=0 NormalY=0 NormalZ=1 AngleXU=0 Radius=0.460977 StartAngle=9.792e-13 EndAngle=0.708626
    g4: LineSegment StartX=-0.1 StartY=7.8 StartZ=0 EndX=-0.1 EndY=7.75 EndZ=0
    g5: LineSegment StartX=-0.1 StartY=7.75 StartZ=0 EndX=0.1 EndY=7.75 EndZ=0
    g6: LineSegment StartX=0.1 StartY=7.75 StartZ=0 EndX=0.1 EndY=7.8 EndZ=0
  constraints (22):
    c: DistanceY(g-1,g0) = 7.5
    c: Symmetric(g0,g0,g-2)
    c: DistanceX(g0,g0) = 10
    c: PointOnObject(g1,g0)
    c: PointOnObject(g1,g0)
    c: Coincident(g3,g1)
    c: Coincident(g2,g1)
    c: Coincident(g2,g4)
    c: Coincident(g4,g5)
    c: Horizontal(g5)
    c: Coincident(g5,g6)
    c: Coincident(g6,g3)
    c: Vertical(g6)
    c: Equal(g3,g2)
    c: Vertical(g4)
    c: Symmetric(g2,g3,g-2)
    c: DistanceX(g5,g5) = 0.2
    c: Distance(g5,g1) = 0.25
    c: DistanceX(g3,g-1) = 0.25
    c: PointOnObject(g3,g1)
    c: PointOnObject(g2,g1)
    c: Distance(g3,g1) = 0.3
FEATURE [PartDesign::Revolution] Revolution033
  Angle = 360
  Axis = (10,0,0)
  Base = (-5,7.5,0)
  Profile = -> Sketch107
  ReferenceAxis = -> Sketch107 [Axis]
FEATURE [PartDesign::Body] Body112  label="Rivet 029"
  Group = -> [Sketch107,Revolution033]
  Origin = -> Origin130
  Placement = pos=(0,0,0) rot=(1,0,0;0.448799rad)
  Tip = -> Revolution033
FEATURE [PartDesign::FeatureBase] Clone063
  BaseFeature = -> Body112
  Placement = pos=(0,0,0) rot=(1,0,0;0.448799rad)
FEATURE [PartDesign::Body] Body113  label="Rivet 030"
  BaseFeature = -> Body112
  Group = -> [Clone063]
  Origin = -> Origin131
  Placement = pos=(0,0,0) rot=(1,0,0;0.897598rad)
  Tip = -> Clone063
FEATURE [PartDesign::FeatureBase] Clone064
  BaseFeature = -> Body112
  Placement = pos=(0,0,0) rot=(1,0,0;0.448799rad)
FEATURE [PartDesign::Body] Body114  label="Rivet 031"
  BaseFeature = -> Body112
  Group = -> [Clone064]
  Origin = -> Origin132
  Placement = pos=(0,0,0) rot=(1,0,0;1.7952rad)
  Tip = -> Clone064
FEATURE [PartDesign::FeatureBase] Clone065
  BaseFeature = -> Body112
  Placement = pos=(0,0,0) rot=(1,0,0;0.448799rad)
FEATURE [PartDesign::Body] Body115  label="Rivet 032"
  BaseFeature = -> Body112
  Group = -> [Clone065]
  Origin = -> Origin133
  Placement = pos=(0,0,0) rot=(1,0,0;2.69279rad)
  Tip = -> Clone065
FEATURE [PartDesign::FeatureBase] Clone066
  BaseFeature = -> Body112
  Placement = pos=(0,0,0) rot=(1,0,0;0.448799rad)
FEATURE [PartDesign::Body] Body116  label="Rivet 033"
  BaseFeature = -> Body112
  Group = -> [Clone066]
  Origin = -> Origin134
  Placement = pos=(0,0,0) rot=(1,0,0;3.59039rad)
  Tip = -> Clone066
FEATURE [PartDesign::FeatureBase] Clone067
  BaseFeature = -> Body112
  Placement = pos=(0,0,0) rot=(1,0,0;0.448799rad)
FEATURE [PartDesign::Body] Body117  label="Rivet 034"
  BaseFeature = -> Body112
  Group = -> [Clone067]
  Origin = -> Origin135
  Placement = pos=(0,0,0) rot=(-1,0,0;1.7952rad)
  Tip = -> Clone067
FEATURE [PartDesign::FeatureBase] Clone068
  BaseFeature = -> Body112
  Placement = pos=(0,0,0) rot=(1,0,0;0.448799rad)
FEATURE [PartDesign::Body] Body118  label="Rivet 035"
  BaseFeature = -> Body112
  Group = -> [Clone068]
  Origin = -> Origin136
  Placement = pos=(0,0,0) rot=(-1,0,0;0.897598rad)
  Tip = -> Clone068
FEATURE [App::DocumentObjectGroup] Group030  label="Rivets004"
  Group = -> [Body112,Body113,Body114,Body115,Body116,Body117,Body118]
FEATURE [Sketcher::SketchObject] Sketch108
  FullyConstrained = true
  MapMode = 5
  Placement = pos=(0,0,0) rot=(1,0,0;1.5708rad)
  Support = -> [XZ_Plane124]
  sketch-geometry (4):
    g0: LineSegment StartX=0 StartY=8.5 StartZ=0 EndX=0.1 EndY=8.5 EndZ=0
    g1: LineSegment StartX=0.1 StartY=8.5 StartZ=0 EndX=0.1 EndY=6.5 EndZ=0
    g2: LineSegment StartX=0.1 StartY=6.5 StartZ=0 EndX=0 EndY=6.5 EndZ=0
    g3: LineSegment StartX=0 StartY=6.5 StartZ=0 EndX=0 EndY=8.5 EndZ=0
  constraints (12):
    c: Coincident(g0,g1)
    c: Coincident(g1,g2)
    c: Coincident(g2,g3)
    c: Coincident(g3,g0)
    c: Horizontal(g0)
    c: Horizontal(g2)
    c: Vertical(g1)
    c: Vertical(g3)
    c: PointOnObject(g0,g-2)
    c: DistanceX(g0,g0) = 0.1
    c: DistanceY(g0) = 8.5
    c: DistanceY(g1) = 6.5
FEATURE [PartDesign::Revolution] Revolution034
  Angle = 360
  Axis = (1,0,0)
  Base = (0,0,0)
  Placement = pos=(0,0,0) rot=(1,0,0;1.5708rad)
  Profile = -> Sketch108
  ReferenceAxis = -> Sketch108 [H_Axis]
FEATURE [Sketcher::SketchObject] Sketch109
  FullyConstrained = true
  MapMode = 5
  Placement = pos=(0,0,0) rot=(0.57735,0.57735,0.57735;2.0944rad)
  Support = -> [YZ_Plane124]
  sketch-geometry (5):
    g0: ArcOfCircle CenterX=0 CenterY=7.5 CenterZ=0 NormalX=0 NormalY=0 NormalZ=1 AngleXU=0 Radius=2.11 StartAngle=5.66076 EndAngle=6.65667
    g1: LineSegment StartX=5e-16 StartY=8.5 StartZ=0 EndX=0 EndY=6.26986 EndZ=0
    g2: ArcOfCircle CenterX=0 CenterY=0 CenterZ=0 NormalX=0 NormalY=0 NormalZ=1 AngleXU=0 Radius=6.5 StartAngle=1.3039 EndAngle=1.5708
    g3: LineSegment StartX=1.71431 StartY=6.26986 StartZ=0 EndX=0 EndY=6.26986 EndZ=0
    g4: ArcOfCircle CenterX=0 CenterY=0 CenterZ=0 NormalX=0 NormalY=0 NormalZ=1 AngleXU=0 Radius=8.5 StartAngle=1.33757 EndAngle=1.5708
  constraints (16):
    c: PointOnObject(g0,g-2)
    c: DistanceY(g0) = 7.5
    c: Radius(g0) = 2.11
    c: PointOnObject(g2,g1)
    c: DistanceY(g2) = 6.5
    c: Coincident(g2,g-1)
    c: Coincident(g3,g2)
    c: Horizontal(g3)
    c: Coincident(g0,g2)
    c: Coincident(g1,g3)
    c: PointOnObject(g1,g-2)
    c: PointOnObject(g1,g-2)
    c: Coincident(g4,g-1)
    c: Coincident(g4,g1)
    c: DistanceY(g1) = 8.5
    c: Coincident(g0,g4)
FEATURE [PartDesign::Revolution] Revolution035
  Angle = 180
  Axis = (-2e-16,3e-16,1)
  Base = (0,0,0)
  BaseFeature = -> Revolution034
  Placement = pos=(0,0,0) rot=(1,0,0;1.5708rad)
  Profile = -> Sketch109
  ReferenceAxis = -> Sketch109 [V_Axis]
  Reversed = true
FEATURE [PartDesign::PolarPattern] PolarPattern016
  Angle = 360
  Axis = -> Sketch109 [N_Axis]
  BaseFeature = -> Revolution035
  Occurrences = 3
  Originals = -> [Revolution035]
  Placement = pos=(0,0,0) rot=(1,0,0;1.5708rad)
  Refine = true
FEATURE [Sketcher::SketchObject] Sketch110
  FullyConstrained = true
  MapMode = 5
  Placement = pos=(0,0,0) rot=(0.57735,0.57735,0.57735;2.0944rad)
  Support = -> [YZ_Plane124]
  sketch-geometry (4):
    g0: ArcOfCircle CenterX=0 CenterY=7.5 CenterZ=0 NormalX=0 NormalY=0 NormalZ=1 AngleXU=0 Radius=2.01 StartAngle=5.57985 EndAngle=6.86228
    g1: LineSegment StartX=0 StartY=6.2 StartZ=0 EndX=1.533 EndY=6.2 EndZ=0
    g2: LineSegment StartX=0 StartY=8.6 StartZ=0 EndX=0 EndY=6.2 EndZ=0
    g3: LineSegment StartX=0 StartY=8.6 StartZ=0 EndX=1.68229 EndY=8.6 EndZ=0
  constraints (13):
    c: PointOnObject(g0,g-2)
    c: DistanceY(g0) = 7.5
    c: Radius(g0) = 2.01
    c: PointOnObject(g1,g-2)
    c: Horizontal(g1)
    c: Coincident(g0,g1)
    c: DistanceY(g1) = 6.2
    c: DistanceY(g2) = 8.6
    c: Coincident(g2,g1)
    c: PointOnObject(g2,g-2)
    c: Coincident(g3,g2)
    c: Horizontal(g3)
    c: Coincident(g0,g3)
FEATURE [PartDesign::Groove] Groove004
  Angle = 360
  Axis = (-2e-16,3e-16,1)
  Base = (0,0,0)
  BaseFeature = -> PolarPattern016
  Placement = pos=(0,0,0) rot=(1,0,0;1.5708rad)
  Profile = -> Sketch110
  ReferenceAxis = -> Sketch110 [V_Axis]
FEATURE [PartDesign::PolarPattern] PolarPattern017
  Angle = 360
  Axis = -> Sketch110 [N_Axis]
  BaseFeature = -> Groove004
  Occurrences = 3
  Originals = -> [Groove004]
  Placement = pos=(0,0,0) rot=(1,0,0;1.5708rad)
FEATURE [PartDesign::Pocket] Pocket044
  BaseFeature = -> PolarPattern017
  Length = 5
  Length2 = 100
  Placement = pos=(0,0,0) rot=(1,0,0;1.5708rad)
  Profile = -> Sketch105
  Type = 1
FEATURE [PartDesign::PolarPattern] PolarPattern018
  Angle = 360
  Axis = -> Sketch105 [N_Axis]
  BaseFeature = -> Pocket044
  Occurrences = 3
  Originals = -> [Pocket044]
  Placement = pos=(0,0,0) rot=(1,0,0;1.5708rad)
FEATURE [PartDesign::Body] Body110  label="Cage 009"
  Group = -> [Sketch108,Revolution034,Sketch109,Revolution035,PolarPattern016,Sketch110,Groove004,PolarPattern017,Sketch105,Pocket044,PolarPattern018]
  Origin = -> Origin128
  Placement = pos=(0,0,0) rot=(-1,0,0;1.5708rad)
  Tip = -> PolarPattern018
FEATURE [PartDesign::FeatureBase] Clone062
  BaseFeature = -> Body110
  Placement = pos=(0,0,0) rot=(-1,0,0;1.5708rad)
FEATURE [PartDesign::Body] Body111  label="Cage 010"
  BaseFeature = -> Body110
  Group = -> [Clone062]
  Origin = -> Origin129
  Placement = pos=(0,0,0) rot=(0,1,0;3.14159rad)
  Tip = -> Clone062
FEATURE [App::DocumentObjectGroup] Group029  label="Cages004"
  Group = -> [Body110,Body111]
FEATURE [Sketcher::SketchObject] Sketch111
  FullyConstrained = true
  MapMode = 5
  Support = -> [XY_Plane133]
  sketch-geometry (14):
    g0: ArcOfCircle CenterX=-1e-16 CenterY=7.5 CenterZ=0 NormalX=0 NormalY=0 NormalZ=1 AngleXU=0 Radius=2 StartAngle=0.848062 EndAngle=2.29353
    g1: LineSegment StartX=-3.5 StartY=11 StartZ=0 EndX=3.5 EndY=11 EndZ=0
    g2: LineSegment StartX=3.5 StartY=11 StartZ=0 EndX=3.5 EndY=9.2 EndZ=0
    g3: LineSegment StartX=2.9 StartY=9 StartZ=0 EndX=1.32288 EndY=9 EndZ=0
    g4: LineSegment StartX=-3.5 StartY=9.2 StartZ=0 EndX=-3.5 EndY=11 EndZ=0
    g5: LineSegment StartX=-1.32288 StartY=9 StartZ=0 EndX=-2.9 EndY=9 EndZ=0
    g6: LineSegment StartX=2.9 StartY=9 StartZ=0 EndX=2.9 EndY=9.5 EndZ=0
    g7: LineSegment StartX=2.9 StartY=9.5 StartZ=0 EndX=3.2 EndY=9.5 EndZ=0
    g8: LineSegment StartX=3.2 StartY=9.5 StartZ=0 EndX=3.2 EndY=9.2 EndZ=0
    g9: LineSegment StartX=3.2 StartY=9.2 StartZ=0 EndX=3.5 EndY=9.2 EndZ=0
    g10: LineSegment StartX=-3.5 StartY=9.2 StartZ=0 EndX=-3.2 EndY=9.2 EndZ=0
    g11: LineSegment StartX=-3.2 StartY=9.2 StartZ=0 EndX=-3.2 EndY=9.5 EndZ=0
    g12: LineSegment StartX=-3.2 StartY=9.5 StartZ=0 EndX=-2.9 EndY=9.5 EndZ=0
    g13: LineSegment StartX=-2.9 StartY=9.5 StartZ=0 EndX=-2.9 EndY=9 EndZ=0
  constraints (41):
    c: Coincident(g1,g2)
    c: Coincident(g4,g1)
    c: Horizontal(g3)
    c: Vertical(g2)
    c: Vertical(g4)
    c: Coincident(g0,g5)
    c: Coincident(g0,g3)
    c: DistanceY(g-1,g0) = 7.5
    c: Radius(g0) = 2
    c: Symmetric(g1,g1,g-2)
    c: Symmetric(g0,g0,g-2)
    c: DistanceY(g1) = 11
    c: DistanceX(g1,g1) = 7
    c: Vertical(g6)
    c: Coincident(g6,g7)
    c: Horizontal(g7)
    c: Coincident(g7,g8)
    c: Vertical(g8)
    c: Coincident(g8,g9)
    c: Coincident(g3,g6)
    c: Coincident(g2,g9)
    c: Horizontal(g10)
    c: Coincident(g10,g11)
    c: Coincident(g11,g12)
    c: Horizontal(g12)
    c: Coincident(g12,g13)
    c: Vertical(g13)
    c: Vertical(g11)
    c: Coincident(g4,g10)
    c: Coincident(g5,g13)
    c: DistanceY(g13,g13) = 0.5
    c: DistanceX(g12,g12) = 0.3
    c: DistanceY(g5,g10) = 0.2
    c: Symmetric(g5,g3,g-2)
    c: DistanceY(g3) = 9
    c: DistanceY(g6) = 9.5
    c: Equal(g7,g12)
    c: Equal(g13,g6)
    c: Horizontal(g9)
    c: Horizontal(g8,g10)
    c: Equal(g12,g10)
FEATURE [PartDesign::Revolution] Revolution036
  Angle = 360
  Axis = (1,0,0)
  Base = (0,0,0)
  Profile = -> Sketch111
  ReferenceAxis = -> X_Axis133
FEATURE [PartDesign::Fillet] Fillet167
  Base = -> Revolution036 [Edge14,Edge15]
  BaseFeature = -> Revolution036
  Radius = 0.3
  SupportTransform = false
FEATURE [PartDesign::Body] Body119  label="Outer Ring005"
  Group = -> [Sketch111,Revolution036,Fillet167]
  Origin = -> Origin137
  Tip = -> Fillet167
FEATURE [Sketcher::SketchObject] Sketch112
  FullyConstrained = true
  MapMode = 5
  Support = -> [XY_Plane134]
  sketch-geometry (14):
    g0: LineSegment StartX=-2.9 StartY=6 StartZ=0 EndX=-1.32288 EndY=6 EndZ=0
    g1: LineSegment StartX=-3.5 StartY=4 StartZ=0 EndX=-3.5 EndY=5.7 EndZ=0
    g2: ArcOfCircle CenterX=1e-16 CenterY=7.5 CenterZ=0 NormalX=0 NormalY=0 NormalZ=1 AngleXU=0 Radius=2 StartAngle=3.98965 EndAngle=5.43512
    g3: LineSegment StartX=1.32288 StartY=6 StartZ=0 EndX=2.9 EndY=6 EndZ=0
    g4: LineSegment StartX=-3.5 StartY=5.7 StartZ=0 EndX=-3.2 EndY=5.7 EndZ=0
    g5: LineSegment StartX=-3.2 StartY=5.7 StartZ=0 EndX=-3.2 EndY=5.5 EndZ=0
    g6: LineSegment StartX=-3.2 StartY=5.5 StartZ=0 EndX=-2.9 EndY=5.5 EndZ=0
    g7: LineSegment StartX=-2.9 StartY=5.5 StartZ=0 EndX=-2.9 EndY=6 EndZ=0
    g8: LineSegment StartX=8.5 StartY=5.7 StartZ=0 EndX=3.2 EndY=5.7 EndZ=0
    g9: LineSegment StartX=3.2 StartY=5.7 StartZ=0 EndX=3.2 EndY=5.5 EndZ=0
    g10: LineSegment StartX=3.2 StartY=5.5 StartZ=0 EndX=2.9 EndY=5.5 EndZ=0
    g11: LineSegment StartX=2.9 StartY=5.5 StartZ=0 EndX=2.9 EndY=6 EndZ=0
    g12: LineSegment StartX=8.5 StartY=4 StartZ=0 EndX=8.5 EndY=5.7 EndZ=0
    g13: LineSegment StartX=-3.5 StartY=4 StartZ=0 EndX=8.5 EndY=4 EndZ=0
  constraints (43):
    c: Horizontal(g0)
    c: Vertical(g1)
    c: DistanceY(g1) = 4
    c: Coincident(g2,g0)
    c: Coincident(g2,g3)
    c: Horizontal(g3)
    c: Radius(g2) = 2
    c: DistanceY(g2) = 7.5
    c: Symmetric(g0,g2,g-2)
    c: Horizontal(g4)
    c: Coincident(g4,g5)
    c: Vertical(g5)
    c: Coincident(g5,g6)
    c: Horizontal(g6)
    c: Coincident(g6,g7)
    c: Vertical(g7)
    c: Horizontal(g8)
    c: Coincident(g8,g9)
    c: Vertical(g9)
    c: Coincident(g9,g10)
    c: Horizontal(g10)
    c: Coincident(g10,g11)
    c: Vertical(g11)
    c: Coincident(g3,g11)
    c: Coincident(g0,g7)
    c: Coincident(g1,g4)
    c: DistanceY(g3) = 6
    c: DistanceY(g6,g0) = 0.5
    c: DistanceX(g4,g4) = 0.3
    c: DistanceX(g6,g6) = 0.3
    c: DistanceY(g5,g4) = 0.2
    c: Vertical(g12)
    c: Equal(g11,g7)
    c: Equal(g5,g9)
    c: DistanceY(g1,g0) = 2
    c: Coincident(g13,g1)
    c: Coincident(g13,g12)
    c: Horizontal(g13)
    c: DistanceX(g13,g13) = 12
    c: DistanceX(g1,g2) = 3.5
    c: Coincident(g8,g12)
    c: DistanceX(g8,g8) = 5.3
    c: Equal(g6,g10)
FEATURE [PartDesign::Revolution] Revolution037
  Angle = 360
  Axis = (1,0,0)
  Base = (0,0,0)
  Profile = -> Sketch112
  ReferenceAxis = -> X_Axis134
FEATURE [PartDesign::Fillet] Fillet168
  Base = -> Revolution037 [Edge13,Edge11]
  BaseFeature = -> Revolution037
  Radius = 0.2
  SupportTransform = false
FEATURE [PartDesign::Body] Body120  label="Inner Ring005"
  Group = -> [Sketch112,Revolution037,Fillet168]
  Origin = -> Origin138
  Tip = -> Fillet168
FEATURE [App::DocumentObjectGroup] Group032  label="Rings004"
  Group = -> [Body119,Body120]
FEATURE [Sketcher::SketchObject] Sketch113
  FullyConstrained = true
  MapMode = 5
  Placement = pos=(0,0,0) rot=(1,0,0;1.5708rad)
  Support = -> [XZ_Plane135]
  sketch-geometry (12):
    g0: LineSegment StartX=2.9 StartY=9.5 StartZ=0 EndX=2.9 EndY=8.5 EndZ=0
    g1: LineSegment StartX=2.9 StartY=8.5 StartZ=0 EndX=3.2 EndY=8.5 EndZ=0
    g2: LineSegment StartX=3.2 StartY=8.5 StartZ=0 EndX=3.2 EndY=6.5 EndZ=0
    g3: LineSegment StartX=3.2 StartY=6.5 StartZ=0 EndX=2.9 EndY=6.5 EndZ=0
    g4: LineSegment StartX=2.9 StartY=6.5 StartZ=0 EndX=2.9 EndY=5.5 EndZ=0
    g5: LineSegment StartX=2.9 StartY=5.5 StartZ=0 EndX=3.2 EndY=5.5 EndZ=0
    g6: LineSegment StartX=3.2 StartY=5.5 StartZ=0 EndX=3.2 EndY=6 EndZ=0
    g7: LineSegment StartX=3.2 StartY=6 StartZ=0 EndX=3.5 EndY=6 EndZ=0
    g8: LineSegment StartX=3.5 StartY=6 StartZ=0 EndX=3.5 EndY=9 EndZ=0
    g9: LineSegment StartX=3.5 StartY=9 StartZ=0 EndX=3.2 EndY=9 EndZ=0
    g10: LineSegment StartX=3.2 StartY=9 StartZ=0 EndX=3.2 EndY=9.5 EndZ=0
    g11: LineSegment StartX=3.2 StartY=9.5 StartZ=0 EndX=2.9 EndY=9.5 EndZ=0
  constraints (36):
    c: Vertical(g0)
    c: Coincident(g0,g1)
    c: Horizontal(g1)
    c: Coincident(g1,g2)
    c: Vertical(g2)
    c: Coincident(g2,g3)
    c: Horizontal(g3)
    c: Coincident(g3,g4)
    c: Vertical(g4)
    c: Coincident(g4,g5)
    c: Horizontal(g5)
    c: Coincident(g5,g6)
    c: Vertical(g6)
    c: Coincident(g6,g7)
    c: Horizontal(g7)
    c: Coincident(g7,g8)
    c: Vertical(g8)
    c: Coincident(g8,g9)
    c: Horizontal(g9)
    c: Coincident(g9,g10)
    c: Vertical(g10)
    c: Coincident(g10,g11)
    c: Coincident(g11,g0)
    c: Horizontal(g11)
    c: DistanceY(g4) = 5.5
    c: DistanceX(g4) = 2.9
    c: DistanceY(g5,g6) = 0.5
    c: DistanceY(g6,g2) = 0.5
    c: DistanceX(g5,g5) = 0.3
    c: Equal(g5,g7)
    c: Equal(g7,g3)
    c: Equal(g3,g1)
    c: Equal(g1,g9)
    c: Equal(g4,g0)
    c: Equal(g6,g10)
    c: DistanceY(g4,g0) = 4
FEATURE [PartDesign::Revolution] Revolution038
  Angle = 360
  Axis = (1,0,0)
  Base = (0,0,0)
  Placement = pos=(0,0,0) rot=(1,0,0;1.5708rad)
  Profile = -> Sketch113
  ReferenceAxis = -> Sketch113 [H_Axis]
FEATURE [PartDesign::Fillet] Fillet169
  Base = -> Revolution038 [Edge14,Edge12]
  BaseFeature = -> Revolution038
  Placement = pos=(0,0,0) rot=(1,0,0;1.5708rad)
  Radius = 0.2
  SupportTransform = false
FEATURE [PartDesign::Body] Body121  label="Seal 009"
  Group = -> [Sketch113,Revolution038,Fillet169]
  Origin = -> Origin139
  Tip = -> Fillet169
FEATURE [PartDesign::FeatureBase] Clone069
  BaseFeature = -> Body121
FEATURE [PartDesign::Body] Body122  label="Seal 010"
  BaseFeature = -> Body121
  Group = -> [Clone069]
  Origin = -> Origin140
  Placement = pos=(0,0,0) rot=(0,1,0;3.14159rad)
  Tip = -> Clone069
FEATURE [App::DocumentObjectGroup] Group031  label="Seals004"
  Group = -> [Body121,Body122]
FEATURE [Sketcher::SketchObject] Sketch114
  AttachmentOffset = pos=(0,0,4) rot=(0,0,1;0rad)
  FullyConstrained = true
  MapMode = 5
  Placement = pos=(0,0,4) rot=(0,0,1;0rad)
  Support = -> [XY_Plane116]
  sketch-geometry (1):
    g0: Circle CenterX=6 CenterY=0 CenterZ=0 NormalX=0 NormalY=0 NormalZ=1 AngleXU=0 Radius=1.5
  constraints (3):
    c: PointOnObject(g0,g-1)
    c: Diameter(g0) = 3
    c: DistanceX(g0,g-3) = 2.5
FEATURE [PartDesign::Pad] Pad022
  Direction = (0,0,1)
  Length = 3
  Length2 = 100
  Profile = -> Sketch114
  Type = 0
FEATURE [Sketcher::SketchObject] Sketch115
  ExternalGeometry = -> [Pad022]
  FullyConstrained = true
  MapMode = 5
  Placement = pos=(0,0,7) rot=(0,0,1;0rad)
  Support = -> [Pad022]
  sketch-geometry (7):
    g0: LineSegment StartX=6.43301 StartY=-0.75 StartZ=0 EndX=6.86603 EndY=-5.43e-14 EndZ=0
    g1: LineSegment StartX=6.86603 StartY=-5.43e-14 StartZ=0 EndX=6.43301 EndY=0.75 EndZ=0
    g2: LineSegment StartX=6.43301 StartY=0.75 StartZ=0 EndX=5.56699 EndY=0.75 EndZ=0
    g3: LineSegment StartX=5.56699 StartY=0.75 StartZ=0 EndX=5.13397 EndY=1.086e-13 EndZ=0
    g4: LineSegment StartX=5.13397 StartY=1.086e-13 StartZ=0 EndX=5.56699 EndY=-0.75 EndZ=0
    g5: LineSegment StartX=5.56699 StartY=-0.75 StartZ=0 EndX=6.43301 EndY=-0.75 EndZ=0
    g6: Circle CenterX=6 CenterY=0 CenterZ=0 NormalX=0 NormalY=0 NormalZ=1 AngleXU=0 Radius=0.866025
  constraints (16):
    c: Coincident(g0,g1)
    c: Coincident(g1,g2)
    c: Coincident(g2,g3)
    c: Coincident(g3,g4)
    c: Coincident(g4,g5)
    c: Coincident(g5,g0)
    c: Equal(g0, g1-g5) x5
    c: PointOnObject(g0,g6)
    c: PointOnObject(g1,g6)
    c: PointOnObject(g2,g6)
    c: PointOnObject(g3,g6)
    c: PointOnObject(g4,g6)
    c: PointOnObject(g5,g6)
    c: Coincident(g6,g-3)
    c: Horizontal(g5)
    c: DistanceY(g4,g2) = 1.5
FEATURE [PartDesign::Pocket] Pocket045
  BaseFeature = -> Pad022
  Length = 1
  Length2 = 100
  Profile = -> Sketch115
  Type = 0
FEATURE [PartDesign::PolarPattern] PolarPattern019
  Angle = 120
  Axis = -> X_Axis116
  BaseFeature = -> Pocket045
  Occurrences = 3
  Originals = -> [Pad022,Pocket045]
FEATURE [PartDesign::Body] Body102
  Group = -> [Sketch114,Pad022,Sketch115,Pocket045,PolarPattern019]
  Origin = -> Origin120
  Tip = -> PolarPattern019
FEATURE [App::DocumentObjectGroup] Group033  label="Set screws004"
  Group = -> [Body102]
FEATURE [Sketcher::SketchObject] Sketch116
  AttachmentOffset = pos=(0,0,-4.1) rot=(0,0,1;0rad)
  FullyConstrained = true
  MapMode = 5
  Placement = pos=(-4.1,9e-16,-9e-16) rot=(0.57735,0.57735,0.57735;2.0944rad)
  Support = -> [YZ_Plane137]
  sketch-geometry (13):
    g0: ArcOfCircle CenterX=0 CenterY=0 CenterZ=0 NormalX=0 NormalY=0 NormalZ=1 AngleXU=0 Radius=13.5 StartAngle=1.12361 EndAngle=2.01799
    g1: ArcOfCircle CenterX=-18.5 CenterY=0 CenterZ=0 NormalX=0 NormalY=0 NormalZ=1 AngleXU=0 Radius=5.5 StartAngle=2.01799 EndAngle=4.2652
    g2: Circle CenterX=-18.5 CenterY=0 CenterZ=0 NormalX=0 NormalY=0 NormalZ=1 AngleXU=0 Radius=2.75
    g3: ArcOfCircle CenterX=18.5 CenterY=0 CenterZ=0 NormalX=0 NormalY=0 NormalZ=1 AngleXU=0 Radius=5.5 StartAngle=5.15958 EndAngle=7.40679
    g4: Circle CenterX=18.5 CenterY=0 CenterZ=0 NormalX=0 NormalY=0 NormalZ=1 AngleXU=0 Radius=2.75
    g5: Circle CenterX=0 CenterY=0 CenterZ=0 NormalX=0 NormalY=0 NormalZ=1 AngleXU=0 Radius=11
    g6: GeomPoint X=-24 Y=0 Z=0
    g7: GeomPoint X=24 Y=0 Z=0
    g8: LineSegment StartX=-20.8784 StartY=4.95916 StartZ=0 EndX=-5.83784 EndY=12.1725 EndZ=0
    g9: LineSegment StartX=-20.8784 StartY=-4.95916 StartZ=0 EndX=-5.83784 EndY=-12.1725 EndZ=0
    g10: LineSegment StartX=5.83784 StartY=-12.1725 StartZ=0 EndX=20.8784 EndY=-4.95916 EndZ=0
    g11: LineSegment StartX=20.8784 StartY=4.95916 StartZ=0 EndX=5.83784 EndY=12.1725 EndZ=0
    g12: ArcOfCircle CenterX=0 CenterY=0 CenterZ=0 NormalX=0 NormalY=0 NormalZ=1 AngleXU=0 Radius=13.5 StartAngle=4.2652 EndAngle=5.15958
  constraints (27):
    c: Coincident(g0,g-1)
    c: PointOnObject(g1,g-1)
    c: Coincident(g2,g1)
    c: Coincident(g4,g3)
    c: Equal(g2,g4)
    c: Equal(g1,g3)
    c: Coincident(g5,g0)
    c: Diameter(g0) = 27
    c: Diameter(g5) = 22
    c: Diameter(g4) = 5.5
    c: Symmetric(g3,g1,g0)
    c: DistanceX(g1,g3) = 37
    c: PointOnObject(g6,g1)
    c: PointOnObject(g7,g3)
    c: PointOnObject(g7,g-1)
    c: PointOnObject(g6,g-1)
    c: DistanceX(g6,g7) = 48
    c: Tangent(g3,g11) = -1.5708
    c: Tangent(g0,g11) = -1.5708
    c: Tangent(g3,g10) = -1.5708
    c: Tangent(g1,g9) = -1.5708
    c: Equal(g0,g12)
    c: Tangent(g12,g9) = -1.5708
    c: Coincident(g0,g12)
    c: Tangent(g0,g8) = 1.5708
    c: Tangent(g1,g8) = 1.5708
    c: Tangent(g12,g10) = -1.5708
FEATURE [PartDesign::Pad] Pad023
  Direction = (1,-2e-16,3e-16)
  Length = 3.3
  Length2 = 100
  Placement = pos=(0,0,0) rot=(0.57735,0.57735,0.57735;2.0944rad)
  Profile = -> Sketch116
  Type = 0
FEATURE [Sketcher::SketchObject] Sketch117
  ExternalGeometry = -> [Pad023]
  FullyConstrained = true
  MapMode = 5
  Placement = pos=(-4.1,9e-16,-1e-15) rot=(0.57735,0.57735,-0.57735;4.18879rad)
  Support = -> [Pad023]
  sketch-geometry (12):
    g0: ArcOfCircle CenterX=0 CenterY=0 CenterZ=0 NormalX=0 NormalY=0 NormalZ=1 AngleXU=0 Radius=12.3 StartAngle=4.2652 EndAngle=5.15958
    g1: ArcOfCircle CenterX=-18.5 CenterY=-1.04e-14 CenterZ=0 NormalX=0 NormalY=0 NormalZ=1 AngleXU=0 Radius=4.55 StartAngle=4.98418 EndAngle=7.58219
    g2: ArcOfCircle CenterX=18.5 CenterY=1.02e-14 CenterZ=0 NormalX=0 NormalY=0 NormalZ=1 AngleXU=0 Radius=4.55 StartAngle=1.84259 EndAngle=4.44059
    g3: LineSegment StartX=-17.3605 StartY=5.31545 StartZ=0 EndX=-5.31892 EndY=11.0905 EndZ=0
    g4: LineSegment StartX=-17.3605 StartY=-5.31545 StartZ=0 EndX=-5.31892 EndY=-11.0905 EndZ=0
    g5: LineSegment StartX=5.31892 StartY=-11.0905 StartZ=0 EndX=17.3605 EndY=-5.31545 EndZ=0
    g6: LineSegment StartX=17.3605 StartY=5.31545 StartZ=0 EndX=5.31892 EndY=11.0905 EndZ=0
    g7: ArcOfCircle CenterX=0 CenterY=0 CenterZ=0 NormalX=0 NormalY=0 NormalZ=1 AngleXU=0 Radius=12.3 StartAngle=1.12361 EndAngle=2.01799
    g8: ArcOfCircle CenterX=-17.1443 CenterY=4.86462 CenterZ=0 NormalX=0 NormalY=0 NormalZ=1 AngleXU=0 Radius=0.5 StartAngle=2.01799 EndAngle=4.44059
    g9: ArcOfCircle CenterX=-17.1443 CenterY=-4.86462 CenterZ=0 NormalX=0 NormalY=0 NormalZ=1 AngleXU=0 Radius=0.5 StartAngle=1.84259 EndAngle=4.2652
    g10: ArcOfCircle CenterX=17.1443 CenterY=-4.86462 CenterZ=0 NormalX=0 NormalY=0 NormalZ=1 AngleXU=0 Radius=0.5 StartAngle=5.15958 EndAngle=7.58219
    g11: ArcOfCircle CenterX=17.1443 CenterY=4.86462 CenterZ=0 NormalX=0 NormalY=0 NormalZ=1 AngleXU=0 Radius=0.5 StartAngle=4.98418 EndAngle=7.40679
  constraints (30):
    c: Coincident(g0,g-1)
    c: Coincident(g1,g-3)
    c: Coincident(g2,g-4)
    c: Equal(g2,g1)
    c: Parallel(g3,g-5)
    c: Distance(g3,g-5) = 1.2
    c: Coincident(g7,g3) = 1.5708
    c: Tangent(g0,g4) = -1.5708
    c: Equal(g0,g7)
    c: Tangent(g0,g5) = -1.5708
    c: Tangent(g7,g6) = -1.5708
    c: Coincident(g0,g7)
    c: Vertical(g0,g3)
    c: Tangent(g1,g8) = 1.5708
    c: Tangent(g3,g8) = 1.5708
    c: Tangent(g4,g9) = -1.5708
    c: Tangent(g1,g9) = 1.5708
    c: Tangent(g2,g10) = 1.5708
    c: Tangent(g5,g10) = -1.5708
    c: Tangent(g6,g11) = -1.5708
    c: Tangent(g2,g11) = 1.5708
    c: Equal(g8,g9)
    c: Equal(g9,g10)
    c: Equal(g10,g11)
    c: Parallel(g-6,g6)
    c: Parallel(g5,g3)
    c: Parallel(g4,g6)
    c: Radius(g-4) = 2.75
    c: Radius(g2) = 4.55
    c: Radius(g11) = 0.5
FEATURE [PartDesign::Pocket] Pocket046
  BaseFeature = -> Pad023
  Length = 0.6
  Length2 = 100
  Placement = pos=(0,0,0) rot=(0.57735,0.57735,0.57735;2.0944rad)
  Profile = -> Sketch117
  Type = 0
FEATURE [Sketcher::SketchObject] Sketch118
  ExternalGeometry = -> [Pocket046]
  FullyConstrained = true
  MapMode = 5
  Placement = pos=(-0.8,2e-16,-2e-16) rot=(0.57735,0.57735,0.57735;2.0944rad)
  Support = -> [Pocket046]
  sketch-geometry (7):
    g0: Circle CenterX=-18.5 CenterY=1.66e-14 CenterZ=0 NormalX=0 NormalY=0 NormalZ=1 AngleXU=0 Radius=2.75
    g1: LineSegment StartX=-20.8784 StartY=4.95916 StartZ=0 EndX=-14.8432 EndY=7.85358 EndZ=0
    g2: LineSegment StartX=-20.8784 StartY=-4.95916 StartZ=0 EndX=-14.8432 EndY=-7.85358 EndZ=0
    g3: ArcOfCircle CenterX=-18.5 CenterY=1.66e-14 CenterZ=0 NormalX=0 NormalY=0 NormalZ=1 AngleXU=0 Radius=5.5 StartAngle=2.01799 EndAngle=4.2652
    g4: ArcOfCircle CenterX=0 CenterY=0 CenterZ=0 NormalX=0 NormalY=0 NormalZ=1 AngleXU=0 Radius=15 StartAngle=2.69212 EndAngle=3.59107
    g5: ArcOfCircle CenterX=-14.4108 CenterY=6.95191 CenterZ=0 NormalX=0 NormalY=0 NormalZ=1 AngleXU=0 Radius=1 StartAngle=5.83371 EndAngle=8.30117
    g6: ArcOfCircle CenterX=-14.4108 CenterY=-6.95191 CenterZ=0 NormalX=0 NormalY=0 NormalZ=1 AngleXU=0 Radius=1 StartAngle=4.2652 EndAngle=6.73266
  constraints (17):
    c: Coincident(g0,g-6)
    c: Equal(g-5,g0)
    c: Coincident(g1,g-6)
    c: Coincident(g2,g-6)
    c: Coincident(g3,g0)
    c: Coincident(g3,g1)
    c: Coincident(g3,g2)
    c: Coincident(g4,g-1)
    c: Radius(g4) = 15
    c: Tangent(g1,g5) = 1.5708
    c: Tangent(g4,g5) = 1.5708
    c: Tangent(g2,g6) = -1.5708
    c: Tangent(g4,g6) = 1.5708
    c: Radius(g6) = 1
    c: PointOnObject(g2,g-4)
    c: Equal(g5,g6)
    c: PointOnObject(g1,g-3)
FEATURE [PartDesign::Pad] Pad024
  BaseFeature = -> Pocket046
  Direction = (1,-9e-16,6e-16)
  Length = 0.7
  Length2 = 100
  Placement = pos=(0,0,0) rot=(0.57735,0.57735,0.57735;2.0944rad)
  Profile = -> Sketch118
  Type = 0
FEATURE [PartDesign::Mirrored] Mirrored004
  BaseFeature = -> Pad024
  MirrorPlane = -> Sketch118 [V_Axis]
  Originals = -> [Pad024,XZ_Plane137]
  Placement = pos=(0,0,0) rot=(0.57735,0.57735,0.57735;2.0944rad)
FEATURE [Sketcher::SketchObject] Sketch119
  FullyConstrained = true
  MapMode = 5
  Placement = pos=(-0.8,2e-16,-2e-16) rot=(0.57735,0.57735,0.57735;2.0944rad)
  Support = -> [Mirrored004]
  sketch-geometry (2):
    g0: Circle CenterX=0 CenterY=0 CenterZ=0 NormalX=0 NormalY=0 NormalZ=1 AngleXU=0 Radius=11
    g1: Circle CenterX=0 CenterY=0 CenterZ=0 NormalX=0 NormalY=0 NormalZ=1 AngleXU=0 Radius=13.5
  constraints (4):
    c: Coincident(g0,g-1)
    c: Coincident(g1,g0)
    c: Diameter(g1) = 27
    c: Diameter(g0) = 22
FEATURE [PartDesign::Pad] Pad025
  BaseFeature = -> Mirrored004
  Direction = (1,-8e-16,6e-16)
  Length = 4.2
  Length2 = 100
  Placement = pos=(0,0,0) rot=(0.57735,0.57735,0.57735;2.0944rad)
  Profile = -> Sketch119
  Type = 0
FEATURE [Sketcher::SketchObject] Sketch120
  FullyConstrained = true
  MapMode = 5
  Placement = pos=(-3.5,1.5e-15,-1.5e-15) rot=(0.57735,0.57735,-0.57735;4.18879rad)
  Support = -> [Pad025]
  sketch-geometry (13):
    g0: Ellipse CenterX=0 CenterY=0 CenterZ=0 NormalX=0 NormalY=0 NormalZ=1 MajorRadius=15 MinorRadius=6.38796 AngleXU=0
    g1: LineSegment StartX=15 StartY=0 StartZ=0 EndX=-15 EndY=0 EndZ=0
    g2: LineSegment StartX=0 StartY=6.38796 StartZ=0 EndX=0 EndY=-6.38796 EndZ=0
    g3: GeomPoint X=13.5718 Y=0 Z=0
    g4: GeomPoint X=-13.5718 Y=0 Z=0
    g5: ArcOfCircle CenterX=0 CenterY=0 CenterZ=0 NormalX=0 NormalY=0 NormalZ=1 AngleXU=0 Radius=11 StartAngle=2.69004 EndAngle=3.59315
    g6: ArcOfCircle CenterX=0 CenterY=0 CenterZ=0 NormalX=0 NormalY=0 NormalZ=1 AngleXU=0 Radius=11.5 StartAngle=2.73643 EndAngle=3.54676
    g7: ArcOfCircle CenterX=0 CenterY=0 CenterZ=0 NormalX=0 NormalY=0 NormalZ=1 AngleXU=0 Radius=11 StartAngle=5.83163 EndAngle=6.73474
    g8: ArcOfCircle CenterX=0 CenterY=0 CenterZ=0 NormalX=0 NormalY=0 NormalZ=1 AngleXU=0 Radius=11.5 StartAngle=5.87802 EndAngle=6.68835
    g9: LineSegment StartX=10.5689 StartY=4.53296 StartZ=0 EndX=9.89747 EndY=4.8 EndZ=0
    g10: LineSegment StartX=9.89747 StartY=-4.8 StartZ=0 EndX=10.5689 EndY=-4.53296 EndZ=0
    g11: LineSegment StartX=-10.5689 StartY=4.53296 StartZ=0 EndX=-9.89747 EndY=4.8 EndZ=0
    g12: LineSegment StartX=-9.89747 StartY=-4.8 StartZ=0 EndX=-10.5689 EndY=-4.53296 EndZ=0
  constraints (29):
    c: InternalAlignment(g1-g4 -> g0) x4
    c: Coincident(g0,g-1)
    c: Coincident(g5,g0)
    c: PointOnObject(g5,g0)
    c: PointOnObject(g5,g0)
    c: Coincident(g6,g5)
    c: PointOnObject(g6,g0)
    c: PointOnObject(g6,g0)
    c: Coincident(g7,g5)
    c: PointOnObject(g7,g0)
    c: PointOnObject(g7,g0)
    c: Coincident(g8,g5)
    c: PointOnObject(g8,g0)
    c: PointOnObject(g8,g0)
    c: Radius(g7) = 11
    c: Radius(g8) = 11.5
    c: PointOnObject(g1,g-1)
    c: Radius(g5) = 11
    c: Radius(g6) = 11.5
    c: DistanceY(g5,g5) = 9.6
    c: DistanceX(g1) = 15
    c: Coincident(g9,g8)
    c: Coincident(g9,g7)
    c: Coincident(g10,g7)
    c: Coincident(g10,g8)
    c: Coincident(g11,g6)
    c: Coincident(g5,g11)
    c: Coincident(g12,g5)
    c: Coincident(g12,g6)
FEATURE [PartDesign::Pocket] Pocket047
  BaseFeature = -> Pad025
  Length = 3.3
  Length2 = 100
  Placement = pos=(0,0,0) rot=(0.57735,0.57735,0.57735;2.0944rad)
  Profile = -> Sketch120
  Type = 0
FEATURE [PartDesign::Fillet] Fillet166
  Base = -> Pocket047 [Edge13,Edge14,Edge10,Edge6,Edge3,Edge15,Edge17,Edge16,Edge37,Edge104,Edge94]
  BaseFeature = -> Pocket047
  Placement = pos=(0,0,0) rot=(0.57735,0.57735,0.57735;2.0944rad)
  Radius = 0.2
  SupportTransform = false
FEATURE [PartDesign::Body] Body123  label="Case004"
  Group = -> [Sketch116,Pad023,Sketch117,Pocket046,Sketch118,Pad024,Mirrored004,Sketch119,Pad025,Sketch120,Pocket047,Fillet166]
  Origin = -> Origin141
  Tip = -> Fillet166
FEATURE [App::DocumentObjectGroup] Group034  label="Case005"
  Group = -> [Body123]
FEATURE [App::Part] Part018  label="KFL08-001"
  Group = -> [Group028,Body103,Body104,Body105,Body106,Body107,Body108,Body109,Group029,Body110,Body111,Group030,Body112,Body113,Body114,Body115,Body116,Body117,Body118,Group031,Body121,Body122,Group032,Body119,Body120,Group033,Body102,Group034,Body123]
  Origin = -> Origin142
  Placement = pos=(316,120,80) rot=(0,0,1;3.14159rad)
FEATURE [Sketcher::SketchObject] Sketch121
  FullyConstrained = true
  MapMode = 5
  Placement = pos=(0,0,0) rot=(-0.57735,0.57735,0.57735;4.18879rad)
  Support = -> [YZ_Plane146]
  sketch-geometry (1):
    g0: Circle CenterX=0 CenterY=-7.5 CenterZ=0 NormalX=0 NormalY=0 NormalZ=1 AngleXU=0 Radius=0.25
  constraints (3):
    c: PointOnObject(g0,g-2)
    c: DistanceY(g0) = -7.5
    c: Diameter(g0) = 0.5
FEATURE [Sketcher::SketchObject] Sketch122
  FullyConstrained = true
  MapMode = 5
  Support = -> [XY_Plane139]
  sketch-geometry (2):
    g0: LineSegment StartX=0 StartY=5.5 StartZ=0 EndX=6e-16 EndY=9.5 EndZ=0
    g1: ArcOfCircle CenterX=0 CenterY=7.5 CenterZ=0 NormalX=0 NormalY=0 NormalZ=1 AngleXU=0 Radius=2 StartAngle=4.71239 EndAngle=7.85398
  constraints (7):
    c: PointOnObject(g0,g-2)
    c: PointOnObject(g0,g-2)
    c: PointOnObject(g1,g0)
    c: Coincident(g1,g0)
    c: Coincident(g1,g0)
    c: Radius(g1) = 2
    c: DistanceY(g1) = 7.5
FEATURE [PartDesign::Revolution] Revolution039
  Angle = 360
  Axis = (0,1,0)
  Base = (0,0,0)
  Profile = -> Sketch122
  ReferenceAxis = -> Sketch122 [V_Axis]
  Reversed = true
FEATURE [PartDesign::Body] Body125  label="Ball 036"
  Group = -> [Sketch122,Revolution039]
  Origin = -> Origin144
  Tip = -> Revolution039
FEATURE [PartDesign::FeatureBase] Clone070
  BaseFeature = -> Body125
FEATURE [PartDesign::Body] Body126  label="Ball 037"
  BaseFeature = -> Body125
  Group = -> [Clone070]
  Origin = -> Origin145
  Placement = pos=(0,0,0) rot=(-1,0,0;0.897598rad)
  Tip = -> Clone070
FEATURE [PartDesign::FeatureBase] Clone071
  BaseFeature = -> Body125
FEATURE [PartDesign::Body] Body127  label="Ball 038"
  BaseFeature = -> Body125
  Group = -> [Clone071]
  Origin = -> Origin146
  Placement = pos=(0,0,0) rot=(-1,0,0;1.7952rad)
  Tip = -> Clone071
FEATURE [PartDesign::FeatureBase] Clone072
  BaseFeature = -> Body125
FEATURE [PartDesign::Body] Body128  label="Ball 039"
  BaseFeature = -> Body125
  Group = -> [Clone072]
  Origin = -> Origin147
  Placement = pos=(0,0,0) rot=(1,0,0;3.59039rad)
  Tip = -> Clone072
FEATURE [PartDesign::FeatureBase] Clone073
  BaseFeature = -> Body125
FEATURE [PartDesign::Body] Body129  label="Ball 040"
  BaseFeature = -> Body125
  Group = -> [Clone073]
  Origin = -> Origin148
  Placement = pos=(0,0,0) rot=(1,0,0;2.69279rad)
  Tip = -> Clone073
FEATURE [PartDesign::FeatureBase] Clone074
  BaseFeature = -> Body125
FEATURE [PartDesign::Body] Body130  label="Ball 041"
  BaseFeature = -> Body125
  Group = -> [Clone074]
  Origin = -> Origin149
  Placement = pos=(0,0,0) rot=(1,0,0;1.7952rad)
  Tip = -> Clone074
FEATURE [PartDesign::FeatureBase] Clone075
  BaseFeature = -> Body125
FEATURE [PartDesign::Body] Body131  label="Ball 042"
  BaseFeature = -> Body125
  Group = -> [Clone075]
  Origin = -> Origin150
  Placement = pos=(0,0,0) rot=(1,0,0;0.897598rad)
  Tip = -> Clone075
FEATURE [App::DocumentObjectGroup] Group035  label="Balls005"
  Group = -> [Body125,Body126,Body127,Body128,Body129,Body130,Body131]
FEATURE [Sketcher::SketchObject] Sketch123
  FullyConstrained = true
  MapMode = 5
  Support = -> [XY_Plane148]
  sketch-geometry (7):
    g0: LineSegment StartX=-5 StartY=7.5 StartZ=0 EndX=5 EndY=7.5 EndZ=0
    g1: LineSegment StartX=-0.210977 StartY=7.5 StartZ=0 EndX=0.210977 EndY=7.5 EndZ=0
    g2: ArcOfCircle CenterX=0.25 CenterY=7.5 CenterZ=0 NormalX=0 NormalY=0 NormalZ=1 AngleXU=0 Radius=0.460977 StartAngle=2.43297 EndAngle=3.14159
    g3: ArcOfCircle CenterX=-0.25 CenterY=7.5 CenterZ=0 NormalX=0 NormalY=0 NormalZ=1 AngleXU=0 Radius=0.460977 StartAngle=9.792e-13 EndAngle=0.708626
    g4: LineSegment StartX=-0.1 StartY=7.8 StartZ=0 EndX=-0.1 EndY=7.75 EndZ=0
    g5: LineSegment StartX=-0.1 StartY=7.75 StartZ=0 EndX=0.1 EndY=7.75 EndZ=0
    g6: LineSegment StartX=0.1 StartY=7.75 StartZ=0 EndX=0.1 EndY=7.8 EndZ=0
  constraints (22):
    c: DistanceY(g-1,g0) = 7.5
    c: Symmetric(g0,g0,g-2)
    c: DistanceX(g0,g0) = 10
    c: PointOnObject(g1,g0)
    c: PointOnObject(g1,g0)
    c: Coincident(g3,g1)
    c: Coincident(g2,g1)
    c: Coincident(g2,g4)
    c: Coincident(g4,g5)
    c: Horizontal(g5)
    c: Coincident(g5,g6)
    c: Coincident(g6,g3)
    c: Vertical(g6)
    c: Equal(g3,g2)
    c: Vertical(g4)
    c: Symmetric(g2,g3,g-2)
    c: DistanceX(g5,g5) = 0.2
    c: Distance(g5,g1) = 0.25
    c: DistanceX(g3,g-1) = 0.25
    c: PointOnObject(g3,g1)
    c: PointOnObject(g2,g1)
    c: Distance(g3,g1) = 0.3
FEATURE [PartDesign::Revolution] Revolution040
  Angle = 360
  Axis = (10,0,0)
  Base = (-5,7.5,0)
  Profile = -> Sketch123
  ReferenceAxis = -> Sketch123 [Axis]
FEATURE [PartDesign::Body] Body134  label="Rivet 036"
  Group = -> [Sketch123,Revolution040]
  Origin = -> Origin153
  Placement = pos=(0,0,0) rot=(1,0,0;0.448799rad)
  Tip = -> Revolution040
FEATURE [PartDesign::FeatureBase] Clone077
  BaseFeature = -> Body134
  Placement = pos=(0,0,0) rot=(1,0,0;0.448799rad)
FEATURE [PartDesign::Body] Body135  label="Rivet 037"
  BaseFeature = -> Body134
  Group = -> [Clone077]
  Origin = -> Origin154
  Placement = pos=(0,0,0) rot=(1,0,0;0.897598rad)
  Tip = -> Clone077
FEATURE [PartDesign::FeatureBase] Clone078
  BaseFeature = -> Body134
  Placement = pos=(0,0,0) rot=(1,0,0;0.448799rad)
FEATURE [PartDesign::Body] Body136  label="Rivet 038"
  BaseFeature = -> Body134
  Group = -> [Clone078]
  Origin = -> Origin155
  Placement = pos=(0,0,0) rot=(1,0,0;1.7952rad)
  Tip = -> Clone078
FEATURE [PartDesign::FeatureBase] Clone079
  BaseFeature = -> Body134
  Placement = pos=(0,0,0) rot=(1,0,0;0.448799rad)
FEATURE [PartDesign::Body] Body137  label="Rivet 039"
  BaseFeature = -> Body134
  Group = -> [Clone079]
  Origin = -> Origin156
  Placement = pos=(0,0,0) rot=(1,0,0;2.69279rad)
  Tip = -> Clone079
FEATURE [PartDesign::FeatureBase] Clone080
  BaseFeature = -> Body134
  Placement = pos=(0,0,0) rot=(1,0,0;0.448799rad)
FEATURE [PartDesign::Body] Body138  label="Rivet 040"
  BaseFeature = -> Body134
  Group = -> [Clone080]
  Origin = -> Origin157
  Placement = pos=(0,0,0) rot=(1,0,0;3.59039rad)
  Tip = -> Clone080
FEATURE [PartDesign::FeatureBase] Clone081
  BaseFeature = -> Body134
  Placement = pos=(0,0,0) rot=(1,0,0;0.448799rad)
FEATURE [PartDesign::Body] Body139  label="Rivet 041"
  BaseFeature = -> Body134
  Group = -> [Clone081]
  Origin = -> Origin158
  Placement = pos=(0,0,0) rot=(-1,0,0;1.7952rad)
  Tip = -> Clone081
FEATURE [PartDesign::FeatureBase] Clone082
  BaseFeature = -> Body134
  Placement = pos=(0,0,0) rot=(1,0,0;0.448799rad)
FEATURE [PartDesign::Body] Body140  label="Rivet 042"
  BaseFeature = -> Body134
  Group = -> [Clone082]
  Origin = -> Origin159
  Placement = pos=(0,0,0) rot=(-1,0,0;0.897598rad)
  Tip = -> Clone082
FEATURE [App::DocumentObjectGroup] Group037  label="Rivets005"
  Group = -> [Body134,Body135,Body136,Body137,Body138,Body139,Body140]
FEATURE [Sketcher::SketchObject] Sketch124
  FullyConstrained = true
  MapMode = 5
  Placement = pos=(0,0,0) rot=(1,0,0;1.5708rad)
  Support = -> [XZ_Plane146]
  sketch-geometry (4):
    g0: LineSegment StartX=0 StartY=8.5 StartZ=0 EndX=0.1 EndY=8.5 EndZ=0
    g1: LineSegment StartX=0.1 StartY=8.5 StartZ=0 EndX=0.1 EndY=6.5 EndZ=0
    g2: LineSegment StartX=0.1 StartY=6.5 StartZ=0 EndX=0 EndY=6.5 EndZ=0
    g3: LineSegment StartX=0 StartY=6.5 StartZ=0 EndX=0 EndY=8.5 EndZ=0
  constraints (12):
    c: Coincident(g0,g1)
    c: Coincident(g1,g2)
    c: Coincident(g2,g3)
    c: Coincident(g3,g0)
    c: Horizontal(g0)
    c: Horizontal(g2)
    c: Vertical(g1)
    c: Vertical(g3)
    c: PointOnObject(g0,g-2)
    c: DistanceX(g0,g0) = 0.1
    c: DistanceY(g0) = 8.5
    c: DistanceY(g1) = 6.5
FEATURE [PartDesign::Revolution] Revolution041
  Angle = 360
  Axis = (1,0,0)
  Base = (0,0,0)
  Placement = pos=(0,0,0) rot=(1,0,0;1.5708rad)
  Profile = -> Sketch124
  ReferenceAxis = -> Sketch124 [H_Axis]
FEATURE [Sketcher::SketchObject] Sketch125
  FullyConstrained = true
  MapMode = 5
  Placement = pos=(0,0,0) rot=(0.57735,0.57735,0.57735;2.0944rad)
  Support = -> [YZ_Plane146]
  sketch-geometry (5):
    g0: ArcOfCircle CenterX=0 CenterY=7.5 CenterZ=0 NormalX=0 NormalY=0 NormalZ=1 AngleXU=0 Radius=2.11 StartAngle=5.66076 EndAngle=6.65667
    g1: LineSegment StartX=5e-16 StartY=8.5 StartZ=0 EndX=0 EndY=6.26986 EndZ=0
    g2: ArcOfCircle CenterX=0 CenterY=0 CenterZ=0 NormalX=0 NormalY=0 NormalZ=1 AngleXU=0 Radius=6.5 StartAngle=1.3039 EndAngle=1.5708
    g3: LineSegment StartX=1.71431 StartY=6.26986 StartZ=0 EndX=0 EndY=6.26986 EndZ=0
    g4: ArcOfCircle CenterX=0 CenterY=0 CenterZ=0 NormalX=0 NormalY=0 NormalZ=1 AngleXU=0 Radius=8.5 StartAngle=1.33757 EndAngle=1.5708
  constraints (16):
    c: PointOnObject(g0,g-2)
    c: DistanceY(g0) = 7.5
    c: Radius(g0) = 2.11
    c: PointOnObject(g2,g1)
    c: DistanceY(g2) = 6.5
    c: Coincident(g2,g-1)
    c: Coincident(g3,g2)
    c: Horizontal(g3)
    c: Coincident(g0,g2)
    c: Coincident(g1,g3)
    c: PointOnObject(g1,g-2)
    c: PointOnObject(g1,g-2)
    c: Coincident(g4,g-1)
    c: Coincident(g4,g1)
    c: DistanceY(g1) = 8.5
    c: Coincident(g0,g4)
FEATURE [PartDesign::Revolution] Revolution042
  Angle = 180
  Axis = (-2e-16,3e-16,1)
  Base = (0,0,0)
  BaseFeature = -> Revolution041
  Placement = pos=(0,0,0) rot=(1,0,0;1.5708rad)
  Profile = -> Sketch125
  ReferenceAxis = -> Sketch125 [V_Axis]
  Reversed = true
FEATURE [PartDesign::PolarPattern] PolarPattern020
  Angle = 360
  Axis = -> Sketch125 [N_Axis]
  BaseFeature = -> Revolution042
  Occurrences = 3
  Originals = -> [Revolution042]
  Placement = pos=(0,0,0) rot=(1,0,0;1.5708rad)
  Refine = true
FEATURE [Sketcher::SketchObject] Sketch126
  FullyConstrained = true
  MapMode = 5
  Placement = pos=(0,0,0) rot=(0.57735,0.57735,0.57735;2.0944rad)
  Support = -> [YZ_Plane146]
  sketch-geometry (4):
    g0: ArcOfCircle CenterX=0 CenterY=7.5 CenterZ=0 NormalX=0 NormalY=0 NormalZ=1 AngleXU=0 Radius=2.01 StartAngle=5.57985 EndAngle=6.86228
    g1: LineSegment StartX=0 StartY=6.2 StartZ=0 EndX=1.533 EndY=6.2 EndZ=0
    g2: LineSegment StartX=0 StartY=8.6 StartZ=0 EndX=0 EndY=6.2 EndZ=0
    g3: LineSegment StartX=0 StartY=8.6 StartZ=0 EndX=1.68229 EndY=8.6 EndZ=0
  constraints (13):
    c: PointOnObject(g0,g-2)
    c: DistanceY(g0) = 7.5
    c: Radius(g0) = 2.01
    c: PointOnObject(g1,g-2)
    c: Horizontal(g1)
    c: Coincident(g0,g1)
    c: DistanceY(g1) = 6.2
    c: DistanceY(g2) = 8.6
    c: Coincident(g2,g1)
    c: PointOnObject(g2,g-2)
    c: Coincident(g3,g2)
    c: Horizontal(g3)
    c: Coincident(g0,g3)
FEATURE [PartDesign::Groove] Groove005
  Angle = 360
  Axis = (-2e-16,3e-16,1)
  Base = (0,0,0)
  BaseFeature = -> PolarPattern020
  Placement = pos=(0,0,0) rot=(1,0,0;1.5708rad)
  Profile = -> Sketch126
  ReferenceAxis = -> Sketch126 [V_Axis]
FEATURE [PartDesign::PolarPattern] PolarPattern021
  Angle = 360
  Axis = -> Sketch126 [N_Axis]
  BaseFeature = -> Groove005
  Occurrences = 3
  Originals = -> [Groove005]
  Placement = pos=(0,0,0) rot=(1,0,0;1.5708rad)
FEATURE [PartDesign::Pocket] Pocket048
  BaseFeature = -> PolarPattern021
  Length = 5
  Length2 = 100
  Placement = pos=(0,0,0) rot=(1,0,0;1.5708rad)
  Profile = -> Sketch121
  Type = 1
FEATURE [PartDesign::PolarPattern] PolarPattern022
  Angle = 360
  Axis = -> Sketch121 [N_Axis]
  BaseFeature = -> Pocket048
  Occurrences = 3
  Originals = -> [Pocket048]
  Placement = pos=(0,0,0) rot=(1,0,0;1.5708rad)
FEATURE [PartDesign::Body] Body132  label="Cage 011"
  Group = -> [Sketch124,Revolution041,Sketch125,Revolution042,PolarPattern020,Sketch126,Groove005,PolarPattern021,Sketch121,Pocket048,PolarPattern022]
  Origin = -> Origin151
  Placement = pos=(0,0,0) rot=(-1,0,0;1.5708rad)
  Tip = -> PolarPattern022
FEATURE [PartDesign::FeatureBase] Clone076
  BaseFeature = -> Body132
  Placement = pos=(0,0,0) rot=(-1,0,0;1.5708rad)
FEATURE [PartDesign::Body] Body133  label="Cage 012"
  BaseFeature = -> Body132
  Group = -> [Clone076]
  Origin = -> Origin152
  Placement = pos=(0,0,0) rot=(0,1,0;3.14159rad)
  Tip = -> Clone076
FEATURE [App::DocumentObjectGroup] Group036  label="Cages005"
  Group = -> [Body132,Body133]
FEATURE [Sketcher::SketchObject] Sketch127
  FullyConstrained = true
  MapMode = 5
  Support = -> [XY_Plane155]
  sketch-geometry (14):
    g0: ArcOfCircle CenterX=-1e-16 CenterY=7.5 CenterZ=0 NormalX=0 NormalY=0 NormalZ=1 AngleXU=0 Radius=2 StartAngle=0.848062 EndAngle=2.29353
    g1: LineSegment StartX=-3.5 StartY=11 StartZ=0 EndX=3.5 EndY=11 EndZ=0
    g2: LineSegment StartX=3.5 StartY=11 StartZ=0 EndX=3.5 EndY=9.2 EndZ=0
    g3: LineSegment StartX=2.9 StartY=9 StartZ=0 EndX=1.32288 EndY=9 EndZ=0
    g4: LineSegment StartX=-3.5 StartY=9.2 StartZ=0 EndX=-3.5 EndY=11 EndZ=0
    g5: LineSegment StartX=-1.32288 StartY=9 StartZ=0 EndX=-2.9 EndY=9 EndZ=0
    g6: LineSegment StartX=2.9 StartY=9 StartZ=0 EndX=2.9 EndY=9.5 EndZ=0
    g7: LineSegment StartX=2.9 StartY=9.5 StartZ=0 EndX=3.2 EndY=9.5 EndZ=0
    g8: LineSegment StartX=3.2 StartY=9.5 StartZ=0 EndX=3.2 EndY=9.2 EndZ=0
    g9: LineSegment StartX=3.2 StartY=9.2 StartZ=0 EndX=3.5 EndY=9.2 EndZ=0
    g10: LineSegment StartX=-3.5 StartY=9.2 StartZ=0 EndX=-3.2 EndY=9.2 EndZ=0
    g11: LineSegment StartX=-3.2 StartY=9.2 StartZ=0 EndX=-3.2 EndY=9.5 EndZ=0
    g12: LineSegment StartX=-3.2 StartY=9.5 StartZ=0 EndX=-2.9 EndY=9.5 EndZ=0
    g13: LineSegment StartX=-2.9 StartY=9.5 StartZ=0 EndX=-2.9 EndY=9 EndZ=0
  constraints (41):
    c: Coincident(g1,g2)
    c: Coincident(g4,g1)
    c: Horizontal(g3)
    c: Vertical(g2)
    c: Vertical(g4)
    c: Coincident(g0,g5)
    c: Coincident(g0,g3)
    c: DistanceY(g-1,g0) = 7.5
    c: Radius(g0) = 2
    c: Symmetric(g1,g1,g-2)
    c: Symmetric(g0,g0,g-2)
    c: DistanceY(g1) = 11
    c: DistanceX(g1,g1) = 7
    c: Vertical(g6)
    c: Coincident(g6,g7)
    c: Horizontal(g7)
    c: Coincident(g7,g8)
    c: Vertical(g8)
    c: Coincident(g8,g9)
    c: Coincident(g3,g6)
    c: Coincident(g2,g9)
    c: Horizontal(g10)
    c: Coincident(g10,g11)
    c: Coincident(g11,g12)
    c: Horizontal(g12)
    c: Coincident(g12,g13)
    c: Vertical(g13)
    c: Vertical(g11)
    c: Coincident(g4,g10)
    c: Coincident(g5,g13)
    c: DistanceY(g13,g13) = 0.5
    c: DistanceX(g12,g12) = 0.3
    c: DistanceY(g5,g10) = 0.2
    c: Symmetric(g5,g3,g-2)
    c: DistanceY(g3) = 9
    c: DistanceY(g6) = 9.5
    c: Equal(g7,g12)
    c: Equal(g13,g6)
    c: Horizontal(g9)
    c: Horizontal(g8,g10)
    c: Equal(g12,g10)
FEATURE [PartDesign::Revolution] Revolution043
  Angle = 360
  Axis = (1,0,0)
  Base = (0,0,0)
  Profile = -> Sketch127
  ReferenceAxis = -> X_Axis155
FEATURE [PartDesign::Fillet] Fillet171
  Base = -> Revolution043 [Edge14,Edge15]
  BaseFeature = -> Revolution043
  Radius = 0.3
  SupportTransform = false
FEATURE [PartDesign::Body] Body141  label="Outer Ring006"
  Group = -> [Sketch127,Revolution043,Fillet171]
  Origin = -> Origin160
  Tip = -> Fillet171
FEATURE [Sketcher::SketchObject] Sketch128
  FullyConstrained = true
  MapMode = 5
  Support = -> [XY_Plane156]
  sketch-geometry (14):
    g0: LineSegment StartX=-2.9 StartY=6 StartZ=0 EndX=-1.32288 EndY=6 EndZ=0
    g1: LineSegment StartX=-3.5 StartY=4 StartZ=0 EndX=-3.5 EndY=5.7 EndZ=0
    g2: ArcOfCircle CenterX=1e-16 CenterY=7.5 CenterZ=0 NormalX=0 NormalY=0 NormalZ=1 AngleXU=0 Radius=2 StartAngle=3.98965 EndAngle=5.43512
    g3: LineSegment StartX=1.32288 StartY=6 StartZ=0 EndX=2.9 EndY=6 EndZ=0
    g4: LineSegment StartX=-3.5 StartY=5.7 StartZ=0 EndX=-3.2 EndY=5.7 EndZ=0
    g5: LineSegment StartX=-3.2 StartY=5.7 StartZ=0 EndX=-3.2 EndY=5.5 EndZ=0
    g6: LineSegment StartX=-3.2 StartY=5.5 StartZ=0 EndX=-2.9 EndY=5.5 EndZ=0
    g7: LineSegment StartX=-2.9 StartY=5.5 StartZ=0 EndX=-2.9 EndY=6 EndZ=0
    g8: LineSegment StartX=8.5 StartY=5.7 StartZ=0 EndX=3.2 EndY=5.7 EndZ=0
    g9: LineSegment StartX=3.2 StartY=5.7 StartZ=0 EndX=3.2 EndY=5.5 EndZ=0
    g10: LineSegment StartX=3.2 StartY=5.5 StartZ=0 EndX=2.9 EndY=5.5 EndZ=0
    g11: LineSegment StartX=2.9 StartY=5.5 StartZ=0 EndX=2.9 EndY=6 EndZ=0
    g12: LineSegment StartX=8.5 StartY=4 StartZ=0 EndX=8.5 EndY=5.7 EndZ=0
    g13: LineSegment StartX=-3.5 StartY=4 StartZ=0 EndX=8.5 EndY=4 EndZ=0
  constraints (43):
    c: Horizontal(g0)
    c: Vertical(g1)
    c: DistanceY(g1) = 4
    c: Coincident(g2,g0)
    c: Coincident(g2,g3)
    c: Horizontal(g3)
    c: Radius(g2) = 2
    c: DistanceY(g2) = 7.5
    c: Symmetric(g0,g2,g-2)
    c: Horizontal(g4)
    c: Coincident(g4,g5)
    c: Vertical(g5)
    c: Coincident(g5,g6)
    c: Horizontal(g6)
    c: Coincident(g6,g7)
    c: Vertical(g7)
    c: Horizontal(g8)
    c: Coincident(g8,g9)
    c: Vertical(g9)
    c: Coincident(g9,g10)
    c: Horizontal(g10)
    c: Coincident(g10,g11)
    c: Vertical(g11)
    c: Coincident(g3,g11)
    c: Coincident(g0,g7)
    c: Coincident(g1,g4)
    c: DistanceY(g3) = 6
    c: DistanceY(g6,g0) = 0.5
    c: DistanceX(g4,g4) = 0.3
    c: DistanceX(g6,g6) = 0.3
    c: DistanceY(g5,g4) = 0.2
    c: Vertical(g12)
    c: Equal(g11,g7)
    c: Equal(g5,g9)
    c: DistanceY(g1,g0) = 2
    c: Coincident(g13,g1)
    c: Coincident(g13,g12)
    c: Horizontal(g13)
    c: DistanceX(g13,g13) = 12
    c: DistanceX(g1,g2) = 3.5
    c: Coincident(g8,g12)
    c: DistanceX(g8,g8) = 5.3
    c: Equal(g6,g10)
FEATURE [PartDesign::Revolution] Revolution044
  Angle = 360
  Axis = (1,0,0)
  Base = (0,0,0)
  Profile = -> Sketch128
  ReferenceAxis = -> X_Axis156
FEATURE [PartDesign::Fillet] Fillet172
  Base = -> Revolution044 [Edge13,Edge11]
  BaseFeature = -> Revolution044
  Radius = 0.2
  SupportTransform = false
FEATURE [PartDesign::Body] Body142  label="Inner Ring006"
  Group = -> [Sketch128,Revolution044,Fillet172]
  Origin = -> Origin161
  Tip = -> Fillet172
FEATURE [App::DocumentObjectGroup] Group039  label="Rings005"
  Group = -> [Body141,Body142]
FEATURE [Sketcher::SketchObject] Sketch129
  FullyConstrained = true
  MapMode = 5
  Placement = pos=(0,0,0) rot=(1,0,0;1.5708rad)
  Support = -> [XZ_Plane157]
  sketch-geometry (12):
    g0: LineSegment StartX=2.9 StartY=9.5 StartZ=0 EndX=2.9 EndY=8.5 EndZ=0
    g1: LineSegment StartX=2.9 StartY=8.5 StartZ=0 EndX=3.2 EndY=8.5 EndZ=0
    g2: LineSegment StartX=3.2 StartY=8.5 StartZ=0 EndX=3.2 EndY=6.5 EndZ=0
    g3: LineSegment StartX=3.2 StartY=6.5 StartZ=0 EndX=2.9 EndY=6.5 EndZ=0
    g4: LineSegment StartX=2.9 StartY=6.5 StartZ=0 EndX=2.9 EndY=5.5 EndZ=0
    g5: LineSegment StartX=2.9 StartY=5.5 StartZ=0 EndX=3.2 EndY=5.5 EndZ=0
    g6: LineSegment StartX=3.2 StartY=5.5 StartZ=0 EndX=3.2 EndY=6 EndZ=0
    g7: LineSegment StartX=3.2 StartY=6 StartZ=0 EndX=3.5 EndY=6 EndZ=0
    g8: LineSegment StartX=3.5 StartY=6 StartZ=0 EndX=3.5 EndY=9 EndZ=0
    g9: LineSegment StartX=3.5 StartY=9 StartZ=0 EndX=3.2 EndY=9 EndZ=0
    g10: LineSegment StartX=3.2 StartY=9 StartZ=0 EndX=3.2 EndY=9.5 EndZ=0
    g11: LineSegment StartX=3.2 StartY=9.5 StartZ=0 EndX=2.9 EndY=9.5 EndZ=0
  constraints (36):
    c: Vertical(g0)
    c: Coincident(g0,g1)
    c: Horizontal(g1)
    c: Coincident(g1,g2)
    c: Vertical(g2)
    c: Coincident(g2,g3)
    c: Horizontal(g3)
    c: Coincident(g3,g4)
    c: Vertical(g4)
    c: Coincident(g4,g5)
    c: Horizontal(g5)
    c: Coincident(g5,g6)
    c: Vertical(g6)
    c: Coincident(g6,g7)
    c: Horizontal(g7)
    c: Coincident(g7,g8)
    c: Vertical(g8)
    c: Coincident(g8,g9)
    c: Horizontal(g9)
    c: Coincident(g9,g10)
    c: Vertical(g10)
    c: Coincident(g10,g11)
    c: Coincident(g11,g0)
    c: Horizontal(g11)
    c: DistanceY(g4) = 5.5
    c: DistanceX(g4) = 2.9
    c: DistanceY(g5,g6) = 0.5
    c: DistanceY(g6,g2) = 0.5
    c: DistanceX(g5,g5) = 0.3
    c: Equal(g5,g7)
    c: Equal(g7,g3)
    c: Equal(g3,g1)
    c: Equal(g1,g9)
    c: Equal(g4,g0)
    c: Equal(g6,g10)
    c: DistanceY(g4,g0) = 4
FEATURE [PartDesign::Revolution] Revolution045
  Angle = 360
  Axis = (1,0,0)
  Base = (0,0,0)
  Placement = pos=(0,0,0) rot=(1,0,0;1.5708rad)
  Profile = -> Sketch129
  ReferenceAxis = -> Sketch129 [H_Axis]
FEATURE [PartDesign::Fillet] Fillet173
  Base = -> Revolution045 [Edge14,Edge12]
  BaseFeature = -> Revolution045
  Placement = pos=(0,0,0) rot=(1,0,0;1.5708rad)
  Radius = 0.2
  SupportTransform = false
FEATURE [PartDesign::Body] Body143  label="Seal 011"
  Group = -> [Sketch129,Revolution045,Fillet173]
  Origin = -> Origin162
  Tip = -> Fillet173
FEATURE [PartDesign::FeatureBase] Clone083
  BaseFeature = -> Body143
FEATURE [PartDesign::Body] Body144  label="Seal 012"
  BaseFeature = -> Body143
  Group = -> [Clone083]
  Origin = -> Origin163
  Placement = pos=(0,0,0) rot=(0,1,0;3.14159rad)
  Tip = -> Clone083
FEATURE [App::DocumentObjectGroup] Group038  label="Seals005"
  Group = -> [Body143,Body144]
FEATURE [Sketcher::SketchObject] Sketch130
  AttachmentOffset = pos=(0,0,4) rot=(0,0,1;0rad)
  FullyConstrained = true
  MapMode = 5
  Placement = pos=(0,0,4) rot=(0,0,1;0rad)
  Support = -> [XY_Plane138]
  sketch-geometry (1):
    g0: Circle CenterX=6 CenterY=0 CenterZ=0 NormalX=0 NormalY=0 NormalZ=1 AngleXU=0 Radius=1.5
  constraints (3):
    c: PointOnObject(g0,g-1)
    c: Diameter(g0) = 3
    c: DistanceX(g0,g-3) = 2.5
FEATURE [PartDesign::Pad] Pad026
  Direction = (0,0,1)
  Length = 3
  Length2 = 100
  Profile = -> Sketch130
  Type = 0
FEATURE [Sketcher::SketchObject] Sketch131
  ExternalGeometry = -> [Pad026]
  FullyConstrained = true
  MapMode = 5
  Placement = pos=(0,0,7) rot=(0,0,1;0rad)
  Support = -> [Pad026]
  sketch-geometry (7):
    g0: LineSegment StartX=6.43301 StartY=-0.75 StartZ=0 EndX=6.86603 EndY=-5.43e-14 EndZ=0
    g1: LineSegment StartX=6.86603 StartY=-5.43e-14 StartZ=0 EndX=6.43301 EndY=0.75 EndZ=0
    g2: LineSegment StartX=6.43301 StartY=0.75 StartZ=0 EndX=5.56699 EndY=0.75 EndZ=0
    g3: LineSegment StartX=5.56699 StartY=0.75 StartZ=0 EndX=5.13397 EndY=1.086e-13 EndZ=0
    g4: LineSegment StartX=5.13397 StartY=1.086e-13 StartZ=0 EndX=5.56699 EndY=-0.75 EndZ=0
    g5: LineSegment StartX=5.56699 StartY=-0.75 StartZ=0 EndX=6.43301 EndY=-0.75 EndZ=0
    g6: Circle CenterX=6 CenterY=0 CenterZ=0 NormalX=0 NormalY=0 NormalZ=1 AngleXU=0 Radius=0.866025
  constraints (16):
    c: Coincident(g0,g1)
    c: Coincident(g1,g2)
    c: Coincident(g2,g3)
    c: Coincident(g3,g4)
    c: Coincident(g4,g5)
    c: Coincident(g5,g0)
    c: Equal(g0, g1-g5) x5
    c: PointOnObject(g0,g6)
    c: PointOnObject(g1,g6)
    c: PointOnObject(g2,g6)
    c: PointOnObject(g3,g6)
    c: PointOnObject(g4,g6)
    c: PointOnObject(g5,g6)
    c: Coincident(g6,g-3)
    c: Horizontal(g5)
    c: DistanceY(g4,g2) = 1.5
FEATURE [PartDesign::Pocket] Pocket049
  BaseFeature = -> Pad026
  Length = 1
  Length2 = 100
  Profile = -> Sketch131
  Type = 0
FEATURE [PartDesign::PolarPattern] PolarPattern023
  Angle = 120
  Axis = -> X_Axis138
  BaseFeature = -> Pocket049
  Occurrences = 3
  Originals = -> [Pad026,Pocket049]
FEATURE [PartDesign::Body] Body124
  Group = -> [Sketch130,Pad026,Sketch131,Pocket049,PolarPattern023]
  Origin = -> Origin143
  Tip = -> PolarPattern023
FEATURE [App::DocumentObjectGroup] Group040  label="Set screws005"
  Group = -> [Body124]
FEATURE [Sketcher::SketchObject] Sketch132
  AttachmentOffset = pos=(0,0,-4.1) rot=(0,0,1;0rad)
  FullyConstrained = true
  MapMode = 5
  Placement = pos=(-4.1,9e-16,-9e-16) rot=(0.57735,0.57735,0.57735;2.0944rad)
  Support = -> [YZ_Plane159]
  sketch-geometry (13):
    g0: ArcOfCircle CenterX=0 CenterY=0 CenterZ=0 NormalX=0 NormalY=0 NormalZ=1 AngleXU=0 Radius=13.5 StartAngle=1.12361 EndAngle=2.01799
    g1: ArcOfCircle CenterX=-18.5 CenterY=0 CenterZ=0 NormalX=0 NormalY=0 NormalZ=1 AngleXU=0 Radius=5.5 StartAngle=2.01799 EndAngle=4.2652
    g2: Circle CenterX=-18.5 CenterY=0 CenterZ=0 NormalX=0 NormalY=0 NormalZ=1 AngleXU=0 Radius=2.75
    g3: ArcOfCircle CenterX=18.5 CenterY=0 CenterZ=0 NormalX=0 NormalY=0 NormalZ=1 AngleXU=0 Radius=5.5 StartAngle=5.15958 EndAngle=7.40679
    g4: Circle CenterX=18.5 CenterY=0 CenterZ=0 NormalX=0 NormalY=0 NormalZ=1 AngleXU=0 Radius=2.75
    g5: Circle CenterX=0 CenterY=0 CenterZ=0 NormalX=0 NormalY=0 NormalZ=1 AngleXU=0 Radius=11
    g6: GeomPoint X=-24 Y=0 Z=0
    g7: GeomPoint X=24 Y=0 Z=0
    g8: LineSegment StartX=-20.8784 StartY=4.95916 StartZ=0 EndX=-5.83784 EndY=12.1725 EndZ=0
    g9: LineSegment StartX=-20.8784 StartY=-4.95916 StartZ=0 EndX=-5.83784 EndY=-12.1725 EndZ=0
    g10: LineSegment StartX=5.83784 StartY=-12.1725 StartZ=0 EndX=20.8784 EndY=-4.95916 EndZ=0
    g11: LineSegment StartX=20.8784 StartY=4.95916 StartZ=0 EndX=5.83784 EndY=12.1725 EndZ=0
    g12: ArcOfCircle CenterX=0 CenterY=0 CenterZ=0 NormalX=0 NormalY=0 NormalZ=1 AngleXU=0 Radius=13.5 StartAngle=4.2652 EndAngle=5.15958
  constraints (27):
    c: Coincident(g0,g-1)
    c: PointOnObject(g1,g-1)
    c: Coincident(g2,g1)
    c: Coincident(g4,g3)
    c: Equal(g2,g4)
    c: Equal(g1,g3)
    c: Coincident(g5,g0)
    c: Diameter(g0) = 27
    c: Diameter(g5) = 22
    c: Diameter(g4) = 5.5
    c: Symmetric(g3,g1,g0)
    c: DistanceX(g1,g3) = 37
    c: PointOnObject(g6,g1)
    c: PointOnObject(g7,g3)
    c: PointOnObject(g7,g-1)
    c: PointOnObject(g6,g-1)
    c: DistanceX(g6,g7) = 48
    c: Tangent(g3,g11) = -1.5708
    c: Tangent(g0,g11) = -1.5708
    c: Tangent(g3,g10) = -1.5708
    c: Tangent(g1,g9) = -1.5708
    c: Equal(g0,g12)
    c: Tangent(g12,g9) = -1.5708
    c: Coincident(g0,g12)
    c: Tangent(g0,g8) = 1.5708
    c: Tangent(g1,g8) = 1.5708
    c: Tangent(g12,g10) = -1.5708
FEATURE [PartDesign::Pad] Pad027
  Direction = (1,-2e-16,3e-16)
  Length = 3.3
  Length2 = 100
  Placement = pos=(0,0,0) rot=(0.57735,0.57735,0.57735;2.0944rad)
  Profile = -> Sketch132
  Type = 0
FEATURE [Sketcher::SketchObject] Sketch133
  ExternalGeometry = -> [Pad027]
  FullyConstrained = true
  MapMode = 5
  Placement = pos=(-4.1,9e-16,-1e-15) rot=(0.57735,0.57735,-0.57735;4.18879rad)
  Support = -> [Pad027]
  sketch-geometry (12):
    g0: ArcOfCircle CenterX=0 CenterY=0 CenterZ=0 NormalX=0 NormalY=0 NormalZ=1 AngleXU=0 Radius=12.3 StartAngle=4.2652 EndAngle=5.15958
    g1: ArcOfCircle CenterX=-18.5 CenterY=-1.04e-14 CenterZ=0 NormalX=0 NormalY=0 NormalZ=1 AngleXU=0 Radius=4.55 StartAngle=4.98418 EndAngle=7.58219
    g2: ArcOfCircle CenterX=18.5 CenterY=1.02e-14 CenterZ=0 NormalX=0 NormalY=0 NormalZ=1 AngleXU=0 Radius=4.55 StartAngle=1.84259 EndAngle=4.44059
    g3: LineSegment StartX=-17.3605 StartY=5.31545 StartZ=0 EndX=-5.31892 EndY=11.0905 EndZ=0
    g4: LineSegment StartX=-17.3605 StartY=-5.31545 StartZ=0 EndX=-5.31892 EndY=-11.0905 EndZ=0
    g5: LineSegment StartX=5.31892 StartY=-11.0905 StartZ=0 EndX=17.3605 EndY=-5.31545 EndZ=0
    g6: LineSegment StartX=17.3605 StartY=5.31545 StartZ=0 EndX=5.31892 EndY=11.0905 EndZ=0
    g7: ArcOfCircle CenterX=0 CenterY=0 CenterZ=0 NormalX=0 NormalY=0 NormalZ=1 AngleXU=0 Radius=12.3 StartAngle=1.12361 EndAngle=2.01799
    g8: ArcOfCircle CenterX=-17.1443 CenterY=4.86462 CenterZ=0 NormalX=0 NormalY=0 NormalZ=1 AngleXU=0 Radius=0.5 StartAngle=2.01799 EndAngle=4.44059
    g9: ArcOfCircle CenterX=-17.1443 CenterY=-4.86462 CenterZ=0 NormalX=0 NormalY=0 NormalZ=1 AngleXU=0 Radius=0.5 StartAngle=1.84259 EndAngle=4.2652
    g10: ArcOfCircle CenterX=17.1443 CenterY=-4.86462 CenterZ=0 NormalX=0 NormalY=0 NormalZ=1 AngleXU=0 Radius=0.5 StartAngle=5.15958 EndAngle=7.58219
    g11: ArcOfCircle CenterX=17.1443 CenterY=4.86462 CenterZ=0 NormalX=0 NormalY=0 NormalZ=1 AngleXU=0 Radius=0.5 StartAngle=4.98418 EndAngle=7.40679
  constraints (30):
    c: Coincident(g0,g-1)
    c: Coincident(g1,g-3)
    c: Coincident(g2,g-4)
    c: Equal(g2,g1)
    c: Parallel(g3,g-5)
    c: Distance(g3,g-5) = 1.2
    c: Coincident(g7,g3) = 1.5708
    c: Tangent(g0,g4) = -1.5708
    c: Equal(g0,g7)
    c: Tangent(g0,g5) = -1.5708
    c: Tangent(g7,g6) = -1.5708
    c: Coincident(g0,g7)
    c: Vertical(g0,g3)
    c: Tangent(g1,g8) = 1.5708
    c: Tangent(g3,g8) = 1.5708
    c: Tangent(g4,g9) = -1.5708
    c: Tangent(g1,g9) = 1.5708
    c: Tangent(g2,g10) = 1.5708
    c: Tangent(g5,g10) = -1.5708
    c: Tangent(g6,g11) = -1.5708
    c: Tangent(g2,g11) = 1.5708
    c: Equal(g8,g9)
    c: Equal(g9,g10)
    c: Equal(g10,g11)
    c: Parallel(g-6,g6)
    c: Parallel(g5,g3)
    c: Parallel(g4,g6)
    c: Radius(g-4) = 2.75
    c: Radius(g2) = 4.55
    c: Radius(g11) = 0.5
FEATURE [PartDesign::Pocket] Pocket050
  BaseFeature = -> Pad027
  Length = 0.6
  Length2 = 100
  Placement = pos=(0,0,0) rot=(0.57735,0.57735,0.57735;2.0944rad)
  Profile = -> Sketch133
  Type = 0
FEATURE [Sketcher::SketchObject] Sketch134
  ExternalGeometry = -> [Pocket050]
  FullyConstrained = true
  MapMode = 5
  Placement = pos=(-0.8,2e-16,-2e-16) rot=(0.57735,0.57735,0.57735;2.0944rad)
  Support = -> [Pocket050]
  sketch-geometry (7):
    g0: Circle CenterX=-18.5 CenterY=1.66e-14 CenterZ=0 NormalX=0 NormalY=0 NormalZ=1 AngleXU=0 Radius=2.75
    g1: LineSegment StartX=-20.8784 StartY=4.95916 StartZ=0 EndX=-14.8432 EndY=7.85358 EndZ=0
    g2: LineSegment StartX=-20.8784 StartY=-4.95916 StartZ=0 EndX=-14.8432 EndY=-7.85358 EndZ=0
    g3: ArcOfCircle CenterX=-18.5 CenterY=1.66e-14 CenterZ=0 NormalX=0 NormalY=0 NormalZ=1 AngleXU=0 Radius=5.5 StartAngle=2.01799 EndAngle=4.2652
    g4: ArcOfCircle CenterX=0 CenterY=0 CenterZ=0 NormalX=0 NormalY=0 NormalZ=1 AngleXU=0 Radius=15 StartAngle=2.69212 EndAngle=3.59107
    g5: ArcOfCircle CenterX=-14.4108 CenterY=6.95191 CenterZ=0 NormalX=0 NormalY=0 NormalZ=1 AngleXU=0 Radius=1 StartAngle=5.83371 EndAngle=8.30117
    g6: ArcOfCircle CenterX=-14.4108 CenterY=-6.95191 CenterZ=0 NormalX=0 NormalY=0 NormalZ=1 AngleXU=0 Radius=1 StartAngle=4.2652 EndAngle=6.73266
  constraints (17):
    c: Coincident(g0,g-6)
    c: Equal(g-5,g0)
    c: Coincident(g1,g-6)
    c: Coincident(g2,g-6)
    c: Coincident(g3,g0)
    c: Coincident(g3,g1)
    c: Coincident(g3,g2)
    c: Coincident(g4,g-1)
    c: Radius(g4) = 15
    c: Tangent(g1,g5) = 1.5708
    c: Tangent(g4,g5) = 1.5708
    c: Tangent(g2,g6) = -1.5708
    c: Tangent(g4,g6) = 1.5708
    c: Radius(g6) = 1
    c: PointOnObject(g2,g-4)
    c: Equal(g5,g6)
    c: PointOnObject(g1,g-3)
FEATURE [PartDesign::Pad] Pad028
  BaseFeature = -> Pocket050
  Direction = (1,-9e-16,6e-16)
  Length = 0.7
  Length2 = 100
  Placement = pos=(0,0,0) rot=(0.57735,0.57735,0.57735;2.0944rad)
  Profile = -> Sketch134
  Type = 0
FEATURE [PartDesign::Mirrored] Mirrored005
  BaseFeature = -> Pad028
  MirrorPlane = -> Sketch134 [V_Axis]
  Originals = -> [Pad028,XZ_Plane159]
  Placement = pos=(0,0,0) rot=(0.57735,0.57735,0.57735;2.0944rad)
FEATURE [Sketcher::SketchObject] Sketch135
  FullyConstrained = true
  MapMode = 5
  Placement = pos=(-0.8,2e-16,-2e-16) rot=(0.57735,0.57735,0.57735;2.0944rad)
  Support = -> [Mirrored005]
  sketch-geometry (2):
    g0: Circle CenterX=0 CenterY=0 CenterZ=0 NormalX=0 NormalY=0 NormalZ=1 AngleXU=0 Radius=11
    g1: Circle CenterX=0 CenterY=0 CenterZ=0 NormalX=0 NormalY=0 NormalZ=1 AngleXU=0 Radius=13.5
  constraints (4):
    c: Coincident(g0,g-1)
    c: Coincident(g1,g0)
    c: Diameter(g1) = 27
    c: Diameter(g0) = 22
FEATURE [PartDesign::Pad] Pad029
  BaseFeature = -> Mirrored005
  Direction = (1,-8e-16,6e-16)
  Length = 4.2
  Length2 = 100
  Placement = pos=(0,0,0) rot=(0.57735,0.57735,0.57735;2.0944rad)
  Profile = -> Sketch135
  Type = 0
FEATURE [Sketcher::SketchObject] Sketch136
  FullyConstrained = true
  MapMode = 5
  Placement = pos=(-3.5,1.5e-15,-1.5e-15) rot=(0.57735,0.57735,-0.57735;4.18879rad)
  Support = -> [Pad029]
  sketch-geometry (13):
    g0: Ellipse CenterX=0 CenterY=0 CenterZ=0 NormalX=0 NormalY=0 NormalZ=1 MajorRadius=15 MinorRadius=6.38796 AngleXU=0
    g1: LineSegment StartX=15 StartY=0 StartZ=0 EndX=-15 EndY=0 EndZ=0
    g2: LineSegment StartX=0 StartY=6.38796 StartZ=0 EndX=0 EndY=-6.38796 EndZ=0
    g3: GeomPoint X=13.5718 Y=0 Z=0
    g4: GeomPoint X=-13.5718 Y=0 Z=0
    g5: ArcOfCircle CenterX=0 CenterY=0 CenterZ=0 NormalX=0 NormalY=0 NormalZ=1 AngleXU=0 Radius=11 StartAngle=2.69004 EndAngle=3.59315
    g6: ArcOfCircle CenterX=0 CenterY=0 CenterZ=0 NormalX=0 NormalY=0 NormalZ=1 AngleXU=0 Radius=11.5 StartAngle=2.73643 EndAngle=3.54676
    g7: ArcOfCircle CenterX=0 CenterY=0 CenterZ=0 NormalX=0 NormalY=0 NormalZ=1 AngleXU=0 Radius=11 StartAngle=5.83163 EndAngle=6.73474
    g8: ArcOfCircle CenterX=0 CenterY=0 CenterZ=0 NormalX=0 NormalY=0 NormalZ=1 AngleXU=0 Radius=11.5 StartAngle=5.87802 EndAngle=6.68835
    g9: LineSegment StartX=10.5689 StartY=4.53296 StartZ=0 EndX=9.89747 EndY=4.8 EndZ=0
    g10: LineSegment StartX=9.89747 StartY=-4.8 StartZ=0 EndX=10.5689 EndY=-4.53296 EndZ=0
    g11: LineSegment StartX=-10.5689 StartY=4.53296 StartZ=0 EndX=-9.89747 EndY=4.8 EndZ=0
    g12: LineSegment StartX=-9.89747 StartY=-4.8 StartZ=0 EndX=-10.5689 EndY=-4.53296 EndZ=0
  constraints (29):
    c: InternalAlignment(g1-g4 -> g0) x4
    c: Coincident(g0,g-1)
    c: Coincident(g5,g0)
    c: PointOnObject(g5,g0)
    c: PointOnObject(g5,g0)
    c: Coincident(g6,g5)
    c: PointOnObject(g6,g0)
    c: PointOnObject(g6,g0)
    c: Coincident(g7,g5)
    c: PointOnObject(g7,g0)
    c: PointOnObject(g7,g0)
    c: Coincident(g8,g5)
    c: PointOnObject(g8,g0)
    c: PointOnObject(g8,g0)
    c: Radius(g7) = 11
    c: Radius(g8) = 11.5
    c: PointOnObject(g1,g-1)
    c: Radius(g5) = 11
    c: Radius(g6) = 11.5
    c: DistanceY(g5,g5) = 9.6
    c: DistanceX(g1) = 15
    c: Coincident(g9,g8)
    c: Coincident(g9,g7)
    c: Coincident(g10,g7)
    c: Coincident(g10,g8)
    c: Coincident(g11,g6)
    c: Coincident(g5,g11)
    c: Coincident(g12,g5)
    c: Coincident(g12,g6)
FEATURE [PartDesign::Pocket] Pocket051
  BaseFeature = -> Pad029
  Length = 3.3
  Length2 = 100
  Placement = pos=(0,0,0) rot=(0.57735,0.57735,0.57735;2.0944rad)
  Profile = -> Sketch136
  Type = 0
FEATURE [PartDesign::Fillet] Fillet170
  Base = -> Pocket051 [Edge13,Edge14,Edge10,Edge6,Edge3,Edge15,Edge17,Edge16,Edge37,Edge104,Edge94]
  BaseFeature = -> Pocket051
  Placement = pos=(0,0,0) rot=(0.57735,0.57735,0.57735;2.0944rad)
  Radius = 0.2
  SupportTransform = false
FEATURE [PartDesign::Body] Body145  label="Case006"
  Group = -> [Sketch132,Pad027,Sketch133,Pocket050,Sketch134,Pad028,Mirrored005,Sketch135,Pad029,Sketch136,Pocket051,Fillet170]
  Origin = -> Origin164
  Tip = -> Fillet170
FEATURE [App::DocumentObjectGroup] Group041  label="Case007"
  Group = -> [Body145]
FEATURE [App::Part] Part019  label="KFL08-002"
  Group = -> [Group035,Body125,Body126,Body127,Body128,Body129,Body130,Body131,Group036,Body132,Body133,Group037,Body134,Body135,Body136,Body137,Body138,Body139,Body140,Group038,Body143,Body144,Group039,Body141,Body142,Group040,Body124,Group041,Body145]
  Origin = -> Origin165
  Placement = pos=(24,120,80) rot=(0,0,1;0rad)
FEATURE [PartDesign::Body] Body150  label="Stator"
  Origin = -> Origin176
FEATURE [Part::FeaturePython] Screw  label="M2.5x25-Screw"  # Fasteners workbench fastener (typed FeaturePython)
  Placement = pos=(15.5,15.5,4) rot=(0,1,0;3.14159rad)
  diameter = 3
  invert = true
  length = 10
  matchOuter = true
  offset = 1
  thread = true
  type = 16
FEATURE [Part::FeaturePython] Screw001  label="M2.5x25-Screw006"  # Fasteners workbench fastener (typed FeaturePython)
  Placement = pos=(-15.5,-15.5,4) rot=(0,1,0;3.14159rad)
  diameter = 3
  invert = true
  length = 10
  matchOuter = true
  offset = 1
  thread = true
  type = 16
FEATURE [Part::FeaturePython] Screw002  label="M2.5x25-Screw005"  # Fasteners workbench fastener (typed FeaturePython)
  Placement = pos=(15.5,-15.5,4) rot=(0,1,0;3.14159rad)
  diameter = 3
  invert = true
  length = 10
  matchOuter = true
  offset = 1
  thread = true
  type = 16
FEATURE [Part::FeaturePython] Screw003  label="M2.5x25-Screw007"  # Fasteners workbench fastener (typed FeaturePython)
  Placement = pos=(-15.5,15.5,4) rot=(0,1,0;3.14159rad)
  diameter = 3
  invert = true
  length = 10
  matchOuter = true
  offset = 1
  thread = true
  type = 16
FEATURE [App::Part] Part025  label="Screw"
  Group = -> [Screw,Screw001,Screw002,Screw003]
  Origin = -> Origin175
FEATURE [Sketcher::SketchObject] Sketch137
  FullyConstrained = false
  MapMode = 5
  Support = -> [XY_Plane161]
  sketch-geometry (4):
    g0: LineSegment StartX=-21.15 StartY=21.15 StartZ=0 EndX=21.15 EndY=21.15 EndZ=0
    g1: LineSegment StartX=21.15 StartY=21.15 StartZ=0 EndX=21.15 EndY=-21.15 EndZ=0
    g2: LineSegment StartX=21.15 StartY=-21.15 StartZ=0 EndX=-21.15 EndY=-21.15 EndZ=0
    g3: LineSegment StartX=-21.15 StartY=-21.15 StartZ=0 EndX=-21.15 EndY=21.15 EndZ=0
  constraints (11):
    c: Coincident(g0,g1)
    c: Coincident(g1,g2)
    c: Coincident(g2,g3)
    c: Coincident(g3,g0)
    c: Horizontal(g0)
    c: Horizontal(g2)
    c: Vertical(g1)
    c: Vertical(g3)
    c: Symmetric(g0,g1,g-1)
    c: DistanceX(g0,g0) = 42.3
    c: Equal(g0,g3)
FEATURE [PartDesign::Pad] Pad030
  AllowMultiFace = false
  Direction = (1,1,1)
  Length = 9.6
  Length2 = 100
  Profile = -> Sketch137
  Refine = true
  Type = 0
FEATURE [Sketcher::SketchObject] Sketch138
  ExternalGeometry = -> [Pad030]
  FullyConstrained = false
  MapMode = 5
  Support = -> [XY_Plane161]
  sketch-geometry (4):
    g0: LineSegment StartX=21.15 StartY=8.2 StartZ=0 EndX=25.45 EndY=8.2 EndZ=0
    g1: LineSegment StartX=25.45 StartY=8.2 StartZ=0 EndX=25.45 EndY=-8.2 EndZ=0
    g2: LineSegment StartX=25.45 StartY=-8.2 StartZ=0 EndX=21.15 EndY=-8.2 EndZ=0
    g3: LineSegment StartX=21.15 StartY=-8.2 StartZ=0 EndX=21.15 EndY=8.2 EndZ=0
  constraints (11):
    c: Coincident(g0,g1)
    c: Coincident(g1,g2)
    c: Coincident(g2,g3)
    c: Coincident(g3,g0)
    c: Horizontal(g0)
    c: Horizontal(g2)
    c: Vertical(g3)
    c: PointOnObject(g0,g-3)
    c: Symmetric(g1,g0,g-1)
    c: DistanceX(g0,g0) = 4.3
    c: DistanceY(g1,g1) = 16.4
FEATURE [PartDesign::Pad] Pad031
  AllowMultiFace = false
  BaseFeature = -> Pad030
  Direction = (1,1,1)
  Length = 3.6
  Length2 = 100
  Profile = -> Sketch138
  Refine = true
  Type = 0
FEATURE [PartDesign::Chamfer] Chamfer004
  Angle = 45
  Base = -> Pad031 [Edge13,Edge5,Edge1,Edge2]
  BaseFeature = -> Pad031
  ChamferType = 0
  FlipDirection = false
  Size = 5
  Size2 = 1
  SupportTransform = false
FEATURE [PartDesign::Fillet] Fillet174
  Base = -> Chamfer004 [Edge33,Edge28,Edge18,Edge3,Edge2,Edge16,Edge30,Edge25]
  BaseFeature = -> Chamfer004
  Radius = 2
  SupportTransform = false
FEATURE [Sketcher::SketchObject] Sketch139
  FullyConstrained = false
  MapMode = 5
  Support = -> [XY_Plane162]
  sketch-geometry (4):
    g0: LineSegment StartX=-21 StartY=21 StartZ=0 EndX=21 EndY=21 EndZ=0
    g1: LineSegment StartX=21 StartY=21 StartZ=0 EndX=21 EndY=-21 EndZ=0
    g2: LineSegment StartX=21 StartY=-21 StartZ=0 EndX=-21 EndY=-21 EndZ=0
    g3: LineSegment StartX=-21 StartY=-21 StartZ=0 EndX=-21 EndY=21 EndZ=0
  constraints (11):
    c: Coincident(g0,g1)
    c: Coincident(g1,g2)
    c: Coincident(g2,g3)
    c: Coincident(g3,g0)
    c: Horizontal(g0)
    c: Horizontal(g2)
    c: Vertical(g1)
    c: Vertical(g3)
    c: DistanceX(g0,g0) = 42
    c: Symmetric(g0,g1,g-1)
    c: Equal(g0,g3)
FEATURE [PartDesign::Pad] Pad032
  AllowMultiFace = false
  Direction = (1,1,1)
  Length = 22.75
  Length2 = 100
  Profile = -> Sketch139
  Refine = true
  Type = 0
FEATURE [PartDesign::Chamfer] Chamfer005
  Angle = 45
  Base = -> Pad032 [Edge8,Edge1,Edge5,Edge2]
  BaseFeature = -> Pad032
  ChamferType = 0
  FlipDirection = false
  Size = 7.5
  Size2 = 1
  SupportTransform = false
FEATURE [Sketcher::SketchObject] Sketch140
  FullyConstrained = false
  MapMode = 5
  Support = -> [XY_Plane163]
  sketch-geometry (4):
    g0: LineSegment StartX=-21.15 StartY=21.15 StartZ=0 EndX=21.15 EndY=21.15 EndZ=0
    g1: LineSegment StartX=21.15 StartY=21.15 StartZ=0 EndX=21.15 EndY=-21.15 EndZ=0
    g2: LineSegment StartX=21.15 StartY=-21.15 StartZ=0 EndX=-21.15 EndY=-21.15 EndZ=0
    g3: LineSegment StartX=-21.15 StartY=-21.15 StartZ=0 EndX=-21.15 EndY=21.15 EndZ=0
  constraints (11):
    c: Coincident(g0,g1)
    c: Coincident(g1,g2)
    c: Coincident(g2,g3)
    c: Coincident(g3,g0)
    c: Horizontal(g0)
    c: Horizontal(g2)
    c: Vertical(g1)
    c: Vertical(g3)
    c: Symmetric(g0,g1,g-1)
    c: DistanceX(g0,g0) = 42.3
    c: Equal(g0,g3)
FEATURE [PartDesign::Pad] Pad033
  AllowMultiFace = false
  Direction = (1,1,1)
  Length = 7.75
  Length2 = 100
  Profile = -> Sketch140
  Refine = true
  Type = 0
FEATURE [PartDesign::Chamfer] Chamfer006
  Angle = 45
  Base = -> Pad033 [Edge8,Edge5,Edge2,Edge1]
  BaseFeature = -> Pad033
  ChamferType = 0
  FlipDirection = false
  Size = 5
  Size2 = 1
  SupportTransform = false
FEATURE [PartDesign::Fillet] Fillet175
  Base = -> Chamfer006 [Edge22,Edge24,Edge23,Edge21,Edge12,Edge2,Edge3,Edge14]
  BaseFeature = -> Chamfer006
  Radius = 2
  SupportTransform = false
FEATURE [Sketcher::SketchObject] Sketch141
  FullyConstrained = false
  MapMode = 5
  Placement = pos=(0,0,0) rot=(1,0,0;3.14159rad)
  Support = -> [Fillet174]
  sketch-geometry (8):
    g0: LineSegment StartX=-15.5 StartY=15.5 StartZ=0 EndX=15.5 EndY=15.5 EndZ=0
    g1: LineSegment StartX=15.5 StartY=15.5 StartZ=0 EndX=15.5 EndY=-15.5 EndZ=0
    g2: LineSegment StartX=15.5 StartY=-15.5 StartZ=0 EndX=-15.5 EndY=-15.5 EndZ=0
    g3: LineSegment StartX=-15.5 StartY=-15.5 StartZ=0 EndX=-15.5 EndY=15.5 EndZ=0
    g4: Circle CenterX=-15.5 CenterY=15.5 CenterZ=0 NormalX=0 NormalY=0 NormalZ=1 AngleXU=0 Radius=1.225
    g5: Circle CenterX=15.5 CenterY=15.5 CenterZ=0 NormalX=0 NormalY=0 NormalZ=1 AngleXU=0 Radius=1.225
    g6: Circle CenterX=15.5 CenterY=-15.5 CenterZ=0 NormalX=0 NormalY=0 NormalZ=1 AngleXU=0 Radius=1.225
    g7: Circle CenterX=-15.5 CenterY=-15.5 CenterZ=0 NormalX=0 NormalY=0 NormalZ=1 AngleXU=0 Radius=1.225
  constraints (19):
    c: Coincident(g0,g1)
    c: Coincident(g1,g2)
    c: Coincident(g2,g3)
    c: Coincident(g3,g0)
    c: Horizontal(g0)
    c: Horizontal(g2)
    c: Vertical(g1)
    c: Vertical(g3)
    c: Symmetric(g0,g1,g-1)
    c: DistanceX(g0,g0) = 31
    c: Equal(g3,g0)
    c: Coincident(g4,g0)
    c: Coincident(g5,g0)
    c: Coincident(g6,g1)
    c: Coincident(g7,g2)
    c: Equal(g6,g5)
    c: Equal(g5,g4)
    c: Equal(g4,g7)
    c: Radius(g4) = 1.225
FEATURE [PartDesign::Hole] Hole
  AllowMultiFace = false
  BaseFeature = -> Fillet174
  Depth = 25
  DepthType = 0
  Diameter = 3
  DrillForDepth = false
  DrillPoint = 1
  DrillPointAngle = 118
  HoleCutCountersinkAngle = 90
  HoleCutCustomValues = false
  HoleCutDepth = 5
  HoleCutDiameter = 5
  HoleCutType = 1
  ModelActualThread = false
  Profile = -> Sketch141
  Refine = true
  Tapered = false
  TaperedAngle = 90
  ThreadAngle = 0
  ThreadClass = 0
  ThreadCutOffInner = 0
  ThreadCutOffOuter = 0
  ThreadDirection = 0
  ThreadFit = 0
  ThreadPitch = 0
  ThreadSize = 0
  ThreadType = 0
  Threaded = false
FEATURE [Sketcher::SketchObject] Sketch142
  FullyConstrained = false
  MapMode = 5
  Placement = pos=(0,0,0) rot=(1,0,0;3.14159rad)
  Support = -> [Chamfer005]
  sketch-geometry (8):
    g0: LineSegment StartX=-15.5 StartY=15.5 StartZ=0 EndX=15.5 EndY=15.5 EndZ=0
    g1: LineSegment StartX=15.5 StartY=15.5 StartZ=0 EndX=15.5 EndY=-15.5 EndZ=0
    g2: LineSegment StartX=15.5 StartY=-15.5 StartZ=0 EndX=-15.5 EndY=-15.5 EndZ=0
    g3: LineSegment StartX=-15.5 StartY=-15.5 StartZ=0 EndX=-15.5 EndY=15.5 EndZ=0
    g4: Circle CenterX=-15.5 CenterY=15.5 CenterZ=0 NormalX=0 NormalY=0 NormalZ=1 AngleXU=0 Radius=1.22
    g5: Circle CenterX=15.5 CenterY=15.5 CenterZ=0 NormalX=0 NormalY=0 NormalZ=1 AngleXU=0 Radius=1.22
    g6: Circle CenterX=15.5 CenterY=-15.5 CenterZ=0 NormalX=0 NormalY=0 NormalZ=1 AngleXU=0 Radius=1.22
    g7: Circle CenterX=-15.5 CenterY=-15.5 CenterZ=0 NormalX=0 NormalY=0 NormalZ=1 AngleXU=0 Radius=1.22
  constraints (19):
    c: Coincident(g0,g1)
    c: Coincident(g1,g2)
    c: Coincident(g2,g3)
    c: Coincident(g3,g0)
    c: Horizontal(g0)
    c: Horizontal(g2)
    c: Vertical(g1)
    c: Vertical(g3)
    c: Equal(g0,g3)
    c: Symmetric(g0,g1,g-1)
    c: DistanceX(g0,g0) = 31
    c: Coincident(g4,g0)
    c: Coincident(g5,g0)
    c: Coincident(g6,g1)
    c: Coincident(g7,g2)
    c: Equal(g6,g5)
    c: Equal(g5,g4)
    c: Equal(g4,g7)
    c: Radius(g4) = 1.22
FEATURE [PartDesign::Pocket] Pocket053
  AllowMultiFace = false
  BaseFeature = -> Chamfer005
  Length = 5
  Length2 = 100
  Profile = -> Sketch142
  Refine = true
  Type = 1
FEATURE [Sketcher::SketchObject] Sketch143
  FullyConstrained = false
  MapMode = 5
  Placement = pos=(0,0,7.75) rot=(0,0,1;0rad)
  Support = -> [Fillet175]
  sketch-geometry (8):
    g0: LineSegment StartX=-15.5 StartY=15.5 StartZ=0 EndX=15.5 EndY=15.5 EndZ=0
    g1: LineSegment StartX=15.5 StartY=15.5 StartZ=0 EndX=15.5 EndY=-15.5 EndZ=0
    g2: LineSegment StartX=15.5 StartY=-15.5 StartZ=0 EndX=-15.5 EndY=-15.5 EndZ=0
    g3: LineSegment StartX=-15.5 StartY=-15.5 StartZ=0 EndX=-15.5 EndY=15.5 EndZ=0
    g4: Circle CenterX=-15.5 CenterY=15.5 CenterZ=0 NormalX=0 NormalY=0 NormalZ=1 AngleXU=0 Radius=1.225
    g5: Circle CenterX=15.5 CenterY=15.5 CenterZ=0 NormalX=0 NormalY=0 NormalZ=1 AngleXU=0 Radius=1.225
    g6: Circle CenterX=15.5 CenterY=-15.5 CenterZ=0 NormalX=0 NormalY=0 NormalZ=1 AngleXU=0 Radius=1.225
    g7: Circle CenterX=-15.5 CenterY=-15.5 CenterZ=0 NormalX=0 NormalY=0 NormalZ=1 AngleXU=0 Radius=1.225
  constraints (19):
    c: Coincident(g0,g1)
    c: Coincident(g1,g2)
    c: Coincident(g2,g3)
    c: Coincident(g3,g0)
    c: Horizontal(g0)
    c: Horizontal(g2)
    c: Vertical(g1)
    c: Vertical(g3)
    c: Equal(g0,g3)
    c: Symmetric(g0,g1,g-1)
    c: DistanceX(g0,g0) = 31
    c: Coincident(g4,g0)
    c: Coincident(g7,g2)
    c: Coincident(g0,g5)
    c: Coincident(g1,g6)
    c: Equal(g7,g4)
    c: Equal(g4,g5)
    c: Equal(g5,g6)
    c: Radius(g4) = 1.225
FEATURE [PartDesign::Pocket] Pocket054
  AllowMultiFace = false
  BaseFeature = -> Fillet175
  Length = 5
  Length2 = 100
  Profile = -> Sketch143
  Refine = true
  Type = 1
FEATURE [Sketcher::SketchObject] Sketch144
  FullyConstrained = false
  MapMode = 5
  Placement = pos=(0,0,7.75) rot=(0,0,1;0rad)
  Support = -> [Pocket054]
  sketch-geometry (1):
    g0: Circle CenterX=0 CenterY=0 CenterZ=0 NormalX=0 NormalY=0 NormalZ=1 AngleXU=0 Radius=14
  constraints (2):
    c: Coincident(g0,g-1)
    c: Radius(g0) = 14
FEATURE [PartDesign::Pocket] Pocket055
  AllowMultiFace = false
  BaseFeature = -> Pocket054
  Length = 1
  Length2 = 100
  Profile = -> Sketch144
  Refine = true
  Type = 0
FEATURE [Sketcher::SketchObject] Sketch145
  FullyConstrained = false
  MapMode = 5
  Placement = pos=(0,0,6.75) rot=(0,0,1;0rad)
  Support = -> [Pocket055]
  sketch-geometry (1):
    g0: Circle CenterX=0 CenterY=0 CenterZ=0 NormalX=0 NormalY=0 NormalZ=1 AngleXU=0 Radius=11
  constraints (2):
    c: Coincident(g0,g-1)
    c: Radius(g0) = 11
FEATURE [PartDesign::Pad] Pad034
  AllowMultiFace = false
  BaseFeature = -> Pocket055
  Direction = (1,1,1)
  Length = 3
  Length2 = 100
  Profile = -> Sketch145
  Refine = true
  Type = 0
FEATURE [PartDesign::Draft] Draft
  Angle = 10
  Base = -> Pad034 [Face25]
  BaseFeature = -> Pad034
  NeutralPlane = -> Pad034 [Face24]
  SupportTransform = false
FEATURE [Sketcher::SketchObject] Sketch146
  FullyConstrained = false
  MapMode = 5
  Placement = pos=(0,0,9.75) rot=(0,0,1;0rad)
  Support = -> [Draft]
  sketch-geometry (1):
    g0: Circle CenterX=0 CenterY=0 CenterZ=0 NormalX=0 NormalY=0 NormalZ=1 AngleXU=0 Radius=5
  constraints (2):
    c: Coincident(g0,g-1)
    c: Radius(g0) = 5
FEATURE [PartDesign::Pocket] Pocket056
  AllowMultiFace = false
  BaseFeature = -> Draft
  Length = 8
  Length2 = 100
  Profile = -> Sketch146
  Refine = true
  Type = 1
FEATURE [Sketcher::SketchObject] Sketch147
  FullyConstrained = false
  MapMode = 5
  Support = -> [XY_Plane164]
  sketch-geometry (1):
    g0: Circle CenterX=0 CenterY=0 CenterZ=0 NormalX=0 NormalY=0 NormalZ=1 AngleXU=0 Radius=2.5
  constraints (2):
    c: Coincident(g0,g-1)
    c: Radius(g0) = 2.5
FEATURE [PartDesign::Pad] Pad035
  AllowMultiFace = false
  Direction = (1,1,1)
  Length = 60
  Length2 = 100
  Profile = -> Sketch147
  Refine = true
  Type = 0
FEATURE [Sketcher::SketchObject] Sketch148
  FullyConstrained = false
  MapMode = 5
  Placement = pos=(0,0,60) rot=(0,0,1;0rad)
  Support = -> [Pad035]
  sketch-geometry (4):
    g0: LineSegment StartX=2 StartY=2 StartZ=0 EndX=6 EndY=2 EndZ=0
    g1: LineSegment StartX=6 StartY=2 StartZ=0 EndX=6 EndY=-2 EndZ=0
    g2: LineSegment StartX=6 StartY=-2 StartZ=0 EndX=2 EndY=-2 EndZ=0
    g3: LineSegment StartX=2 StartY=-2 StartZ=0 EndX=2 EndY=2 EndZ=0
  constraints (11):
    c: Coincident(g0,g1)
    c: Coincident(g1,g2)
    c: Coincident(g2,g3)
    c: Coincident(g3,g0)
    c: Horizontal(g0)
    c: Horizontal(g2)
    c: Vertical(g1)
    c: Symmetric(g2,g0,g-1)
    c: DistanceX(g-1,g0) = 2
    c: Equal(g0,g3)
    c: DistanceX(g0,g0) = 4
FEATURE [PartDesign::Pocket] Pocket057
  AllowMultiFace = false
  BaseFeature = -> Pad035
  Length = 16
  Length2 = 100
  Profile = -> Sketch148
  Refine = true
  Type = 0
FEATURE [PartDesign::Chamfer] Chamfer007
  Angle = 45
  Base = -> Pocket057 [Edge3,Edge5,Edge9]
  BaseFeature = -> Pocket057
  ChamferType = 0
  FlipDirection = false
  Size = 0.3
  Size2 = 1
  SupportTransform = false
FEATURE [PartDesign::Body] Body149  label="Rotor"
  Group = -> [Sketch147,Pad035,Sketch148,Pocket057,Chamfer007]
  Origin = -> Origin170
  Placement = pos=(0,0,2) rot=(0,0,1;0rad)
  Tip = -> Chamfer007
FEATURE [App::Part] Part024  label="Rotor001"
  Group = -> [Body149]
  Origin = -> Origin174
FEATURE [Sketcher::SketchObject] Sketch149
  FullyConstrained = false
  MapMode = 5
  Placement = pos=(0,0,22.75) rot=(0,0,1;0rad)
  Support = -> [Pocket053]
  sketch-geometry (1):
    g0: Circle CenterX=0 CenterY=0 CenterZ=0 NormalX=0 NormalY=0 NormalZ=1 AngleXU=0 Radius=18
  constraints (2):
    c: Coincident(g0,g-1)
    c: Radius(g0) = 18
FEATURE [PartDesign::Pocket] Pocket052
  AllowMultiFace = false
  BaseFeature = -> Pocket053
  Length = 5
  Length2 = 100
  Profile = -> Sketch149
  Refine = true
  Type = 1
FEATURE [PartDesign::Body] Body147
  Group = -> [Sketch139,Pad032,Chamfer005,Sketch142,Pocket053,Sketch149,Pocket052]
  Origin = -> Origin168
  Placement = pos=(0,0,9.6) rot=(0,0,1;0rad)
  Tip = -> Pocket052
FEATURE [App::Part] Part022  label="Body148"
  Group = -> [Body147,Body150]
  Origin = -> Origin172
FEATURE [Sketcher::SketchObject] Sketch150
  ExternalGeometry = -> [Hole]
  FullyConstrained = false
  MapMode = 5
  Placement = pos=(21.15,0,0) rot=(0.57735,0.57735,0.57735;2.0944rad)
  Support = -> [Hole]
  sketch-geometry (4):
    g0: LineSegment StartX=-8.2 StartY=3.6 StartZ=0 EndX=8.2 EndY=3.6 EndZ=0
    g1: LineSegment StartX=8.2 StartY=3.6 StartZ=0 EndX=8.2 EndY=9.6 EndZ=0
    g2: LineSegment StartX=8.2 StartY=9.6 StartZ=0 EndX=-8.2 EndY=9.6 EndZ=0
    g3: LineSegment StartX=-8.2 StartY=9.6 StartZ=0 EndX=-8.2 EndY=3.6 EndZ=0
  constraints (10):
    c: Coincident(g0,g1)
    c: Coincident(g1,g2)
    c: Coincident(g2,g3)
    c: Coincident(g3,g0)
    c: Horizontal(g0)
    c: Vertical(g1)
    c: Vertical(g3)
    c: Coincident(g0,g-3)
    c: PointOnObject(g1,g-5)
    c: Symmetric(g2,g1,g-2)
FEATURE [PartDesign::Pocket] Pocket058
  AllowMultiFace = false
  BaseFeature = -> Hole
  Length = 4
  Length2 = 100
  Profile = -> Sketch150
  Refine = true
  Type = 0
FEATURE [PartDesign::Body] Body146  label="Aluminium rear001"
  Group = -> [Sketch137,Pad030,Sketch138,Pad031,Chamfer004,Fillet174,Sketch141,Hole,Sketch150,Pocket058]
  Origin = -> Origin167
  Tip = -> Pocket058
FEATURE [App::Part] Part021  label="Aluminium rear"
  Group = -> [Body146]
  Origin = -> Origin171
FEATURE [Sketcher::SketchObject] Sketch151
  FullyConstrained = false
  MapMode = 5
  Placement = pos=(0,0,0) rot=(0.57735,0.57735,0.57735;2.0944rad)
  Support = -> [YZ_Plane172]
  sketch-geometry (4):
    g0: LineSegment StartX=-7.5 StartY=0 StartZ=0 EndX=7.5 EndY=0 EndZ=0
    g1: LineSegment StartX=7.5 StartY=0 StartZ=0 EndX=7.5 EndY=5 EndZ=0
    g2: LineSegment StartX=7.5 StartY=5 StartZ=0 EndX=-7.5 EndY=5 EndZ=0
    g3: LineSegment StartX=-7.5 StartY=5 StartZ=0 EndX=-7.5 EndY=0 EndZ=0
  constraints (11):
    c: Coincident(g0,g1)
    c: Coincident(g1,g2)
    c: Coincident(g2,g3)
    c: Coincident(g3,g0)
    c: Horizontal(g0)
    c: Horizontal(g2)
    c: Vertical(g1)
    c: Vertical(g3)
    c: Symmetric(g0,g0,g-1)
    c: DistanceX(g0,g0) = 15
    c: DistanceY(g3,g3) = 5
FEATURE [PartDesign::Pad] Pad036
  AllowMultiFace = false
  Direction = (1,1,1)
  Length = 10
  Length2 = 100
  Placement = pos=(0,0,0) rot=(0.57735,0.57735,0.57735;2.0944rad)
  Profile = -> Sketch151
  Refine = true
  Type = 0
FEATURE [Sketcher::SketchObject] Sketch152
  ExternalGeometry = -> [Pad036]
  FullyConstrained = false
  MapMode = 5
  Placement = pos=(10,-2.2e-15,2.2e-15) rot=(0.57735,0.57735,0.57735;2.0944rad)
  Support = -> [Pad036]
  sketch-geometry (8):
    g0: LineSegment StartX=-6.5 StartY=4 StartZ=0 EndX=6.5 EndY=4 EndZ=0
    g1: LineSegment StartX=6.5 StartY=4 StartZ=0 EndX=6.5 EndY=1 EndZ=0
    g2: LineSegment StartX=6.5 StartY=1 StartZ=0 EndX=-6.5 EndY=1 EndZ=0
    g3: LineSegment StartX=-6.5 StartY=1 StartZ=0 EndX=-6.5 EndY=4 EndZ=0
    g4: LineSegment StartX=-6.5 StartY=1 StartZ=0 EndX=-7.5 EndY=1 EndZ=0
    g5: LineSegment StartX=-6.5 StartY=1 StartZ=0 EndX=-6.5 EndY=0 EndZ=0
    g6: LineSegment StartX=6.5 StartY=4 StartZ=0 EndX=6.5 EndY=5 EndZ=0
    g7: LineSegment StartX=6.5 StartY=4 StartZ=0 EndX=7.5 EndY=4 EndZ=0
  constraints (23):
    c: Coincident(g0,g1)
    c: Coincident(g1,g2)
    c: Coincident(g2,g3)
    c: Coincident(g3,g0)
    c: Horizontal(g2)
    c: Vertical(g1)
    c: Vertical(g3)
    c: Symmetric(g0,g0,g-2)
    c: Coincident(g4,g2)
    c: PointOnObject(g4,g-4)
    c: Horizontal(g4)
    c: PointOnObject(g5,g-1)
    c: Vertical(g5)
    c: Coincident(g6,g0)
    c: Coincident(g7,g0)
    c: Horizontal(g7)
    c: Vertical(g6)
    c: PointOnObject(g6,g-5)
    c: Equal(g7,g6)
    c: Equal(g6,g4)
    c: Equal(g4,g5)
    c: DistanceX(g4,g4) = 1
    c: Coincident(g5,g2)
FEATURE [PartDesign::Pocket] Pocket059
  AllowMultiFace = false
  BaseFeature = -> Pad036
  Length = 6
  Length2 = 100
  Placement = pos=(0,0,0) rot=(0.57735,0.57735,0.57735;2.0944rad)
  Profile = -> Sketch152
  Refine = true
  Type = 0
FEATURE [Sketcher::SketchObject] Sketch016
  ExternalGeometry = -> [Pocket059]
  FullyConstrained = false
  MapMode = 5
  Placement = pos=(10,-2.2e-15,2.2e-15) rot=(0.57735,0.57735,0.57735;2.0944rad)
  Support = -> [Pocket059]
  sketch-geometry (4):
    g0: LineSegment StartX=-4 StartY=5 StartZ=0 EndX=4 EndY=5 EndZ=0
    g1: LineSegment StartX=4 StartY=5 StartZ=0 EndX=4 EndY=4 EndZ=0
    g2: LineSegment StartX=4 StartY=4 StartZ=0 EndX=-4 EndY=4 EndZ=0
    g3: LineSegment StartX=-4 StartY=4 StartZ=0 EndX=-4 EndY=5 EndZ=0
  constraints (11):
    c: Coincident(g0,g1)
    c: Coincident(g1,g2)
    c: Coincident(g2,g3)
    c: Coincident(g3,g0)
    c: Horizontal(g0)
    c: Vertical(g1)
    c: Vertical(g3)
    c: PointOnObject(g0,g-3)
    c: PointOnObject(g1,g-4)
    c: Symmetric(g1,g2,g-2)
    c: DistanceX(g0,g0) = 8
FEATURE [PartDesign::Pocket] Pocket060
  AllowMultiFace = false
  BaseFeature = -> Pocket059
  Length = 4.5
  Length2 = 100
  Placement = pos=(0,0,0) rot=(0.57735,0.57735,0.57735;2.0944rad)
  Profile = -> Sketch016
  Refine = true
  Type = 0
FEATURE [Sketcher::SketchObject] Sketch017
  ExternalGeometry = -> [Pocket060]
  FullyConstrained = false
  MapMode = 5
  Placement = pos=(-1.4e-15,2.2e-15,5) rot=(0,0,-1;1.5708rad)
  Support = -> [Pocket060]
  sketch-geometry (11):
    g0: LineSegment StartX=-6.49 StartY=8.99 StartZ=0 EndX=-5.01 EndY=8.99 EndZ=0
    g1: LineSegment StartX=-5.01 StartY=8.99 StartZ=0 EndX=-5.01 EndY=4.5 EndZ=0
    g2: LineSegment StartX=-5.01 StartY=4.5 StartZ=0 EndX=-6.49 EndY=4.5 EndZ=0
    g3: LineSegment StartX=-6.49 StartY=4.5 StartZ=0 EndX=-6.49 EndY=8.99 EndZ=0
    g4: LineSegment StartX=5.01 StartY=8.99 StartZ=0 EndX=6.49 EndY=8.99 EndZ=0
    g5: LineSegment StartX=6.49 StartY=8.99 StartZ=0 EndX=6.49 EndY=4.5 EndZ=0
    g6: LineSegment StartX=6.49 StartY=4.5 StartZ=0 EndX=5.01 EndY=4.5 EndZ=0
    g7: LineSegment StartX=5.01 StartY=4.5 StartZ=0 EndX=5.01 EndY=8.99 EndZ=0
    g8: LineSegment StartX=-7.5 StartY=8.99 StartZ=0 EndX=-6.49 EndY=8.99 EndZ=0
    g9: LineSegment StartX=-6.49 StartY=10 StartZ=0 EndX=-6.49 EndY=8.99 EndZ=0
    g10: LineSegment StartX=-5.01 StartY=8.99 StartZ=0 EndX=-4 EndY=8.99 EndZ=0
  constraints (32):
    c: Coincident(g0,g1)
    c: Coincident(g1,g2)
    c: Coincident(g2,g3)
    c: Coincident(g3,g0)
    c: Horizontal(g0)
    c: Horizontal(g2)
    c: Vertical(g1)
    c: Vertical(g3)
    c: Coincident(g4,g5)
    c: Coincident(g5,g6)
    c: Coincident(g6,g7)
    c: Coincident(g7,g4)
    c: Horizontal(g4)
    c: Horizontal(g6)
    c: Vertical(g5)
    c: Vertical(g7)
    c: DistanceX(g4,g4) = 1.48
    c: Equal(g0,g4)
    c: Equal(g7,g1)
    c: PointOnObject(g8,g-4)
    c: Coincident(g8,g0)
    c: Horizontal(g8)
    c: PointOnObject(g9,g-5)
    c: Coincident(g9,g0)
    c: Vertical(g9)
    c: Coincident(g10,g0)
    c: PointOnObject(g10,g-3)
    c: Horizontal(g10)
    c: Symmetric(g4,g0,g-2)
    c: Equal(g10,g9)
    c: Equal(g9,g8)
    c: DistanceY(g3,g3) = 4.49
FEATURE [PartDesign::Pocket] Pocket061
  AllowMultiFace = false
  BaseFeature = -> Pocket060
  Length = 2
  Length2 = 100
  Placement = pos=(0,0,0) rot=(0.57735,0.57735,0.57735;2.0944rad)
  Profile = -> Sketch017
  Refine = true
  Type = 0
FEATURE [PartDesign::Body] Body151  label="conector"
  Group = -> [Sketch151,Pad036,Sketch152,Pocket059,Sketch016,Pocket060,Sketch017,Pocket061]
  Origin = -> Origin178
  Tip = -> Pocket061
FEATURE [Sketcher::SketchObject] Sketch018
  FullyConstrained = false
  MapMode = 5
  Placement = pos=(0,0,0) rot=(0.57735,0.57735,0.57735;2.0944rad)
  Support = -> [YZ_Plane173]
  sketch-geometry (4):
    g0: LineSegment StartX=-5.5 StartY=1 StartZ=0 EndX=5.5 EndY=1 EndZ=0
    g1: LineSegment StartX=5.5 StartY=1 StartZ=0 EndX=5.5 EndY=0 EndZ=0
    g2: LineSegment StartX=5.5 StartY=0 StartZ=0 EndX=-5.5 EndY=0 EndZ=0
    g3: LineSegment StartX=-5.5 StartY=0 StartZ=0 EndX=-5.5 EndY=1 EndZ=0
  constraints (11):
    c: Coincident(g0,g1)
    c: Coincident(g1,g2)
    c: Coincident(g2,g3)
    c: Coincident(g3,g0)
    c: Horizontal(g0)
    c: Vertical(g1)
    c: Vertical(g3)
    c: PointOnObject(g1,g-1)
    c: DistanceY(g3,g3) = 1
    c: DistanceX(g2,g2) = 11
    c: Symmetric(g1,g2,g-2)
FEATURE [PartDesign::Pad] Pad037
  AllowMultiFace = false
  Direction = (1,1,1)
  Length = 1
  Length2 = 100
  Placement = pos=(0,0,0) rot=(0.57735,0.57735,0.57735;2.0944rad)
  Profile = -> Sketch018
  Refine = true
  Type = 0
FEATURE [Sketcher::SketchObject] Sketch153
  ExternalGeometry = -> [Pad037]
  FullyConstrained = false
  MapMode = 5
  Placement = pos=(-3e-16,4e-16,1) rot=(0,0,-1;1.5708rad)
  Support = -> [Pad037]
  sketch-geometry (7):
    g0: LineSegment StartX=-5.5 StartY=1 StartZ=0 EndX=-4.5 EndY=1 EndZ=0
    g1: LineSegment StartX=-4.5 StartY=1 StartZ=0 EndX=-4.5 EndY=8 EndZ=0
    g2: LineSegment StartX=-4.5 StartY=8 StartZ=0 EndX=-5.5 EndY=8 EndZ=0
    g3: LineSegment StartX=-5.5 StartY=8 StartZ=0 EndX=-5.5 EndY=1 EndZ=0
    g4: LineSegment StartX=-5.5 StartY=8 StartZ=0 EndX=-5.25 EndY=8.7 EndZ=0
    g5: LineSegment StartX=-5.25 StartY=8.7 StartZ=0 EndX=-4.75 EndY=8.7 EndZ=0
    g6: LineSegment StartX=-4.75 StartY=8.7 StartZ=0 EndX=-4.5 EndY=8 EndZ=0
  constraints (19):
    c: Coincident(g0,g1)
    c: Coincident(g1,g2)
    c: Coincident(g2,g3)
    c: Coincident(g3,g0)
    c: Horizontal(g0)
    c: Horizontal(g2)
    c: Vertical(g1)
    c: Vertical(g3)
    c: Coincident(g0,g-3)
    c: Coincident(g2,g4)
    c: Coincident(g4,g5)
    c: Horizontal(g5)
    c: Coincident(g5,g6)
    c: Coincident(g6,g1)
    c: DistanceY(g1,g5) = 0.7
    c: DistanceX(g5,g5) = 0.5
    c: Equal(g6,g4)
    c: DistanceX(g0,g0) = 1
    c: DistanceY(g3,g3) = 7
FEATURE [PartDesign::Pad] Pad038
  AllowMultiFace = false
  BaseFeature = -> Pad037
  Direction = (1,1,1)
  Length = 1
  Length2 = 100
  Placement = pos=(0,0,0) rot=(0.57735,0.57735,0.57735;2.0944rad)
  Profile = -> Sketch153
  Refine = true
  Reversed = true
  Type = 0
FEATURE [PartDesign::LinearPattern] LinearPattern
  BaseFeature = -> Pad038
  Direction = -> Pad038 [Edge10]
  Length = 10
  Occurrences = 3
  Originals = -> [Pad038]
  Placement = pos=(0,0,0) rot=(0.57735,0.57735,0.57735;2.0944rad)
  Refine = true
  Reversed = true
FEATURE [PartDesign::Body] Body152  label="pin"
  Group = -> [Sketch018,Pad037,Sketch153,Pad038,LinearPattern]
  Origin = -> Origin179
  Placement = pos=(0,0,2) rot=(0,0,1;0rad)
  Tip = -> LinearPattern
FEATURE [App::Part] Part026  label="Conector"
  Group = -> [Body151,Body152]
  Origin = -> Origin177
  Placement = pos=(17,0,4) rot=(0,0,1;0rad)
FEATURE [Sketcher::SketchObject] Sketch020
  FullyConstrained = false
  MapMode = 5
  Placement = pos=(0,0,0) rot=(1,0,0;3.14159rad)
  Support = -> [Pocket056]
  sketch-geometry (1):
    g0: Circle CenterX=0 CenterY=0 CenterZ=0 NormalX=0 NormalY=0 NormalZ=1 AngleXU=0 Radius=15.35
  constraints (2):
    c: Coincident(g0,g-1)
    c: Radius(g0) = 15.35
FEATURE [PartDesign::Pocket] Pocket062
  AllowMultiFace = false
  BaseFeature = -> Pocket056
  Length = 5
  Length2 = 100
  Profile = -> Sketch020
  Refine = true
  Type = 0
FEATURE [PartDesign::Body] Body148  label="Aluminum front001"
  Group = -> [Sketch140,Pad033,Chamfer006,Fillet175,Sketch143,Pocket054,Sketch144,Pocket055,Sketch145,Pad034,Draft,Sketch146,Pocket056,Sketch020,Pocket062]
  Origin = -> Origin169
  Placement = pos=(0,0,32.35) rot=(0,0,1;0rad)
  Tip = -> Pocket062
FEATURE [App::Part] Part023  label="Aluminum front"
  Group = -> [Body148]
  Origin = -> Origin173
FEATURE [App::Part] Part020  label="Nema 017-001"
  Group = -> [Part021,Part022,Part023,Part024,Part025,Part026]
  Origin = -> Origin166
  Placement = pos=(440,120,104.3) rot=(0,1,0;-1.5708rad)
FEATURE [PartDesign::Body] Body157  label="Stator001"
  Origin = -> Origin190
FEATURE [Part::FeaturePython] Screw004  label="M2.5x25-Screw008"  # Fasteners workbench fastener (typed FeaturePython)
  Placement = pos=(15.5,15.5,4) rot=(0,1,0;3.14159rad)
  diameter = 3
  invert = true
  length = 10
  matchOuter = true
  offset = 1
  thread = true
  type = 16
FEATURE [Part::FeaturePython] Screw005  label="M2.5x25-Screw009"  # Fasteners workbench fastener (typed FeaturePython)
  Placement = pos=(-15.5,-15.5,4) rot=(0,1,0;3.14159rad)
  diameter = 3
  invert = true
  length = 10
  matchOuter = true
  offset = 1
  thread = true
  type = 16
FEATURE [Part::FeaturePython] Screw006  label="M2.5x25-Screw010"  # Fasteners workbench fastener (typed FeaturePython)
  Placement = pos=(15.5,-15.5,4) rot=(0,1,0;3.14159rad)
  diameter = 3
  invert = true
  length = 10
  matchOuter = true
  offset = 1
  thread = true
  type = 16
FEATURE [Part::FeaturePython] Screw007  label="M2.5x25-Screw011"  # Fasteners workbench fastener (typed FeaturePython)
  Placement = pos=(-15.5,15.5,4) rot=(0,1,0;3.14159rad)
  diameter = 3
  invert = true
  length = 10
  matchOuter = true
  offset = 1
  thread = true
  type = 16
FEATURE [App::Part] Part032  label="Screw001"
  Group = -> [Screw004,Screw005,Screw006,Screw007]
  Origin = -> Origin189
FEATURE [Sketcher::SketchObject] Sketch156
  FullyConstrained = false
  MapMode = 5
  Placement = pos=(0,0,0) rot=(0.57735,0.57735,0.57735;2.0944rad)
  Support = -> [YZ_Plane187]
  sketch-geometry (4):
    g0: LineSegment StartX=-5.5 StartY=1 StartZ=0 EndX=5.5 EndY=1 EndZ=0
    g1: LineSegment StartX=5.5 StartY=1 StartZ=0 EndX=5.5 EndY=0 EndZ=0
    g2: LineSegment StartX=5.5 StartY=0 StartZ=0 EndX=-5.5 EndY=0 EndZ=0
    g3: LineSegment StartX=-5.5 StartY=0 StartZ=0 EndX=-5.5 EndY=1 EndZ=0
  constraints (11):
    c: Coincident(g0,g1)
    c: Coincident(g1,g2)
    c: Coincident(g2,g3)
    c: Coincident(g3,g0)
    c: Horizontal(g0)
    c: Vertical(g1)
    c: Vertical(g3)
    c: PointOnObject(g1,g-1)
    c: DistanceY(g3,g3) = 1
    c: DistanceX(g2,g2) = 11
    c: Symmetric(g1,g2,g-2)
FEATURE [PartDesign::Pad] Pad046
  AllowMultiFace = false
  Direction = (1,1,1)
  Length = 1
  Length2 = 100
  Placement = pos=(0,0,0) rot=(0.57735,0.57735,0.57735;2.0944rad)
  Profile = -> Sketch156
  Refine = true
  Type = 0
FEATURE [Sketcher::SketchObject] Sketch158
  FullyConstrained = false
  MapMode = 5
  Support = -> [XY_Plane175]
  sketch-geometry (4):
    g0: LineSegment StartX=-21.15 StartY=21.15 StartZ=0 EndX=21.15 EndY=21.15 EndZ=0
    g1: LineSegment StartX=21.15 StartY=21.15 StartZ=0 EndX=21.15 EndY=-21.15 EndZ=0
    g2: LineSegment StartX=21.15 StartY=-21.15 StartZ=0 EndX=-21.15 EndY=-21.15 EndZ=0
    g3: LineSegment StartX=-21.15 StartY=-21.15 StartZ=0 EndX=-21.15 EndY=21.15 EndZ=0
  constraints (11):
    c: Coincident(g0,g1)
    c: Coincident(g1,g2)
    c: Coincident(g2,g3)
    c: Coincident(g3,g0)
    c: Horizontal(g0)
    c: Horizontal(g2)
    c: Vertical(g1)
    c: Vertical(g3)
    c: Symmetric(g0,g1,g-1)
    c: DistanceX(g0,g0) = 42.3
    c: Equal(g0,g3)
FEATURE [PartDesign::Pad] Pad039
  AllowMultiFace = false
  Direction = (1,1,1)
  Length = 9.6
  Length2 = 100
  Profile = -> Sketch158
  Refine = true
  Type = 0
FEATURE [Sketcher::SketchObject] Sketch159
  ExternalGeometry = -> [Pad039]
  FullyConstrained = false
  MapMode = 5
  Support = -> [XY_Plane175]
  sketch-geometry (4):
    g0: LineSegment StartX=21.15 StartY=8.2 StartZ=0 EndX=25.45 EndY=8.2 EndZ=0
    g1: LineSegment StartX=25.45 StartY=8.2 StartZ=0 EndX=25.45 EndY=-8.2 EndZ=0
    g2: LineSegment StartX=25.45 StartY=-8.2 StartZ=0 EndX=21.15 EndY=-8.2 EndZ=0
    g3: LineSegment StartX=21.15 StartY=-8.2 StartZ=0 EndX=21.15 EndY=8.2 EndZ=0
  constraints (11):
    c: Coincident(g0,g1)
    c: Coincident(g1,g2)
    c: Coincident(g2,g3)
    c: Coincident(g3,g0)
    c: Horizontal(g0)
    c: Horizontal(g2)
    c: Vertical(g3)
    c: PointOnObject(g0,g-3)
    c: Symmetric(g1,g0,g-1)
    c: DistanceX(g0,g0) = 4.3
    c: DistanceY(g1,g1) = 16.4
FEATURE [PartDesign::Pad] Pad040
  AllowMultiFace = false
  BaseFeature = -> Pad039
  Direction = (1,1,1)
  Length = 3.6
  Length2 = 100
  Profile = -> Sketch159
  Refine = true
  Type = 0
FEATURE [PartDesign::Chamfer] Chamfer008
  Angle = 45
  Base = -> Pad040 [Edge13,Edge5,Edge1,Edge2]
  BaseFeature = -> Pad040
  ChamferType = 0
  FlipDirection = false
  Size = 5
  Size2 = 1
  SupportTransform = false
FEATURE [PartDesign::Fillet] Fillet176
  Base = -> Chamfer008 [Edge33,Edge28,Edge18,Edge3,Edge2,Edge16,Edge30,Edge25]
  BaseFeature = -> Chamfer008
  Radius = 2
  SupportTransform = false
FEATURE [Sketcher::SketchObject] Sketch160
  FullyConstrained = false
  MapMode = 5
  Support = -> [XY_Plane176]
  sketch-geometry (4):
    g0: LineSegment StartX=-21 StartY=21 StartZ=0 EndX=21 EndY=21 EndZ=0
    g1: LineSegment StartX=21 StartY=21 StartZ=0 EndX=21 EndY=-21 EndZ=0
    g2: LineSegment StartX=21 StartY=-21 StartZ=0 EndX=-21 EndY=-21 EndZ=0
    g3: LineSegment StartX=-21 StartY=-21 StartZ=0 EndX=-21 EndY=21 EndZ=0
  constraints (11):
    c: Coincident(g0,g1)
    c: Coincident(g1,g2)
    c: Coincident(g2,g3)
    c: Coincident(g3,g0)
    c: Horizontal(g0)
    c: Horizontal(g2)
    c: Vertical(g1)
    c: Vertical(g3)
    c: DistanceX(g0,g0) = 42
    c: Symmetric(g0,g1,g-1)
    c: Equal(g0,g3)
FEATURE [PartDesign::Pad] Pad041
  AllowMultiFace = false
  Direction = (1,1,1)
  Length = 22.75
  Length2 = 100
  Profile = -> Sketch160
  Refine = true
  Type = 0
FEATURE [PartDesign::Chamfer] Chamfer009
  Angle = 45
  Base = -> Pad041 [Edge8,Edge1,Edge5,Edge2]
  BaseFeature = -> Pad041
  ChamferType = 0
  FlipDirection = false
  Size = 7.5
  Size2 = 1
  SupportTransform = false
FEATURE [Sketcher::SketchObject] Sketch161
  FullyConstrained = false
  MapMode = 5
  Support = -> [XY_Plane177]
  sketch-geometry (4):
    g0: LineSegment StartX=-21.15 StartY=21.15 StartZ=0 EndX=21.15 EndY=21.15 EndZ=0
    g1: LineSegment StartX=21.15 StartY=21.15 StartZ=0 EndX=21.15 EndY=-21.15 EndZ=0
    g2: LineSegment StartX=21.15 StartY=-21.15 StartZ=0 EndX=-21.15 EndY=-21.15 EndZ=0
    g3: LineSegment StartX=-21.15 StartY=-21.15 StartZ=0 EndX=-21.15 EndY=21.15 EndZ=0
  constraints (11):
    c: Coincident(g0,g1)
    c: Coincident(g1,g2)
    c: Coincident(g2,g3)
    c: Coincident(g3,g0)
    c: Horizontal(g0)
    c: Horizontal(g2)
    c: Vertical(g1)
    c: Vertical(g3)
    c: Symmetric(g0,g1,g-1)
    c: DistanceX(g0,g0) = 42.3
    c: Equal(g0,g3)
FEATURE [PartDesign::Pad] Pad042
  AllowMultiFace = false
  Direction = (1,1,1)
  Length = 7.75
  Length2 = 100
  Profile = -> Sketch161
  Refine = true
  Type = 0
FEATURE [PartDesign::Chamfer] Chamfer010
  Angle = 45
  Base = -> Pad042 [Edge8,Edge5,Edge2,Edge1]
  BaseFeature = -> Pad042
  ChamferType = 0
  FlipDirection = false
  Size = 5
  Size2 = 1
  SupportTransform = false
FEATURE [PartDesign::Fillet] Fillet177
  Base = -> Chamfer010 [Edge22,Edge24,Edge23,Edge21,Edge12,Edge2,Edge3,Edge14]
  BaseFeature = -> Chamfer010
  Radius = 2
  SupportTransform = false
FEATURE [Sketcher::SketchObject] Sketch162
  FullyConstrained = false
  MapMode = 5
  Placement = pos=(0,0,0) rot=(1,0,0;3.14159rad)
  Support = -> [Fillet176]
  sketch-geometry (8):
    g0: LineSegment StartX=-15.5 StartY=15.5 StartZ=0 EndX=15.5 EndY=15.5 EndZ=0
    g1: LineSegment StartX=15.5 StartY=15.5 StartZ=0 EndX=15.5 EndY=-15.5 EndZ=0
    g2: LineSegment StartX=15.5 StartY=-15.5 StartZ=0 EndX=-15.5 EndY=-15.5 EndZ=0
    g3: LineSegment StartX=-15.5 StartY=-15.5 StartZ=0 EndX=-15.5 EndY=15.5 EndZ=0
    g4: Circle CenterX=-15.5 CenterY=15.5 CenterZ=0 NormalX=0 NormalY=0 NormalZ=1 AngleXU=0 Radius=1.225
    g5: Circle CenterX=15.5 CenterY=15.5 CenterZ=0 NormalX=0 NormalY=0 NormalZ=1 AngleXU=0 Radius=1.225
    g6: Circle CenterX=15.5 CenterY=-15.5 CenterZ=0 NormalX=0 NormalY=0 NormalZ=1 AngleXU=0 Radius=1.225
    g7: Circle CenterX=-15.5 CenterY=-15.5 CenterZ=0 NormalX=0 NormalY=0 NormalZ=1 AngleXU=0 Radius=1.225
  constraints (19):
    c: Coincident(g0,g1)
    c: Coincident(g1,g2)
    c: Coincident(g2,g3)
    c: Coincident(g3,g0)
    c: Horizontal(g0)
    c: Horizontal(g2)
    c: Vertical(g1)
    c: Vertical(g3)
    c: Symmetric(g0,g1,g-1)
    c: DistanceX(g0,g0) = 31
    c: Equal(g3,g0)
    c: Coincident(g4,g0)
    c: Coincident(g5,g0)
    c: Coincident(g6,g1)
    c: Coincident(g7,g2)
    c: Equal(g6,g5)
    c: Equal(g5,g4)
    c: Equal(g4,g7)
    c: Radius(g4) = 1.225
FEATURE [PartDesign::Hole] Hole001
  AllowMultiFace = false
  BaseFeature = -> Fillet176
  Depth = 25
  DepthType = 0
  Diameter = 3
  DrillForDepth = false
  DrillPoint = 1
  DrillPointAngle = 118
  HoleCutCountersinkAngle = 90
  HoleCutCustomValues = false
  HoleCutDepth = 5
  HoleCutDiameter = 5
  HoleCutType = 1
  ModelActualThread = false
  Profile = -> Sketch162
  Refine = true
  Tapered = false
  TaperedAngle = 90
  ThreadAngle = 0
  ThreadClass = 0
  ThreadCutOffInner = 0
  ThreadCutOffOuter = 0
  ThreadDirection = 0
  ThreadFit = 0
  ThreadPitch = 0
  ThreadSize = 0
  ThreadType = 0
  Threaded = false
FEATURE [Sketcher::SketchObject] Sketch163
  FullyConstrained = false
  MapMode = 5
  Placement = pos=(0,0,0) rot=(1,0,0;3.14159rad)
  Support = -> [Chamfer009]
  sketch-geometry (8):
    g0: LineSegment StartX=-15.5 StartY=15.5 StartZ=0 EndX=15.5 EndY=15.5 EndZ=0
    g1: LineSegment StartX=15.5 StartY=15.5 StartZ=0 EndX=15.5 EndY=-15.5 EndZ=0
    g2: LineSegment StartX=15.5 StartY=-15.5 StartZ=0 EndX=-15.5 EndY=-15.5 EndZ=0
    g3: LineSegment StartX=-15.5 StartY=-15.5 StartZ=0 EndX=-15.5 EndY=15.5 EndZ=0
    g4: Circle CenterX=-15.5 CenterY=15.5 CenterZ=0 NormalX=0 NormalY=0 NormalZ=1 AngleXU=0 Radius=1.22
    g5: Circle CenterX=15.5 CenterY=15.5 CenterZ=0 NormalX=0 NormalY=0 NormalZ=1 AngleXU=0 Radius=1.22
    g6: Circle CenterX=15.5 CenterY=-15.5 CenterZ=0 NormalX=0 NormalY=0 NormalZ=1 AngleXU=0 Radius=1.22
    g7: Circle CenterX=-15.5 CenterY=-15.5 CenterZ=0 NormalX=0 NormalY=0 NormalZ=1 AngleXU=0 Radius=1.22
  constraints (19):
    c: Coincident(g0,g1)
    c: Coincident(g1,g2)
    c: Coincident(g2,g3)
    c: Coincident(g3,g0)
    c: Horizontal(g0)
    c: Horizontal(g2)
    c: Vertical(g1)
    c: Vertical(g3)
    c: Equal(g0,g3)
    c: Symmetric(g0,g1,g-1)
    c: DistanceX(g0,g0) = 31
    c: Coincident(g4,g0)
    c: Coincident(g5,g0)
    c: Coincident(g6,g1)
    c: Coincident(g7,g2)
    c: Equal(g6,g5)
    c: Equal(g5,g4)
    c: Equal(g4,g7)
    c: Radius(g4) = 1.22
FEATURE [PartDesign::Pocket] Pocket064
  AllowMultiFace = false
  BaseFeature = -> Chamfer009
  Length = 5
  Length2 = 100
  Profile = -> Sketch163
  Refine = true
  Type = 1
FEATURE [Sketcher::SketchObject] Sketch164
  FullyConstrained = false
  MapMode = 5
  Placement = pos=(0,0,7.75) rot=(0,0,1;0rad)
  Support = -> [Fillet177]
  sketch-geometry (8):
    g0: LineSegment StartX=-15.5 StartY=15.5 StartZ=0 EndX=15.5 EndY=15.5 EndZ=0
    g1: LineSegment StartX=15.5 StartY=15.5 StartZ=0 EndX=15.5 EndY=-15.5 EndZ=0
    g2: LineSegment StartX=15.5 StartY=-15.5 StartZ=0 EndX=-15.5 EndY=-15.5 EndZ=0
    g3: LineSegment StartX=-15.5 StartY=-15.5 StartZ=0 EndX=-15.5 EndY=15.5 EndZ=0
    g4: Circle CenterX=-15.5 CenterY=15.5 CenterZ=0 NormalX=0 NormalY=0 NormalZ=1 AngleXU=0 Radius=1.225
    g5: Circle CenterX=15.5 CenterY=15.5 CenterZ=0 NormalX=0 NormalY=0 NormalZ=1 AngleXU=0 Radius=1.225
    g6: Circle CenterX=15.5 CenterY=-15.5 CenterZ=0 NormalX=0 NormalY=0 NormalZ=1 AngleXU=0 Radius=1.225
    g7: Circle CenterX=-15.5 CenterY=-15.5 CenterZ=0 NormalX=0 NormalY=0 NormalZ=1 AngleXU=0 Radius=1.225
  constraints (19):
    c: Coincident(g0,g1)
    c: Coincident(g1,g2)
    c: Coincident(g2,g3)
    c: Coincident(g3,g0)
    c: Horizontal(g0)
    c: Horizontal(g2)
    c: Vertical(g1)
    c: Vertical(g3)
    c: Equal(g0,g3)
    c: Symmetric(g0,g1,g-1)
    c: DistanceX(g0,g0) = 31
    c: Coincident(g4,g0)
    c: Coincident(g7,g2)
    c: Coincident(g0,g5)
    c: Coincident(g1,g6)
    c: Equal(g7,g4)
    c: Equal(g4,g5)
    c: Equal(g5,g6)
    c: Radius(g4) = 1.225
FEATURE [PartDesign::Pocket] Pocket065
  AllowMultiFace = false
  BaseFeature = -> Fillet177
  Length = 5
  Length2 = 100
  Profile = -> Sketch164
  Refine = true
  Type = 1
FEATURE [Sketcher::SketchObject] Sketch165
  FullyConstrained = false
  MapMode = 5
  Placement = pos=(0,0,7.75) rot=(0,0,1;0rad)
  Support = -> [Pocket065]
  sketch-geometry (1):
    g0: Circle CenterX=0 CenterY=0 CenterZ=0 NormalX=0 NormalY=0 NormalZ=1 AngleXU=0 Radius=14
  constraints (2):
    c: Coincident(g0,g-1)
    c: Radius(g0) = 14
FEATURE [PartDesign::Pocket] Pocket066
  AllowMultiFace = false
  BaseFeature = -> Pocket065
  Length = 1
  Length2 = 100
  Profile = -> Sketch165
  Refine = true
  Type = 0
FEATURE [Sketcher::SketchObject] Sketch166
  FullyConstrained = false
  MapMode = 5
  Placement = pos=(0,0,6.75) rot=(0,0,1;0rad)
  Support = -> [Pocket066]
  sketch-geometry (1):
    g0: Circle CenterX=0 CenterY=0 CenterZ=0 NormalX=0 NormalY=0 NormalZ=1 AngleXU=0 Radius=11
  constraints (2):
    c: Coincident(g0,g-1)
    c: Radius(g0) = 11
FEATURE [PartDesign::Pad] Pad043
  AllowMultiFace = false
  BaseFeature = -> Pocket066
  Direction = (1,1,1)
  Length = 3
  Length2 = 100
  Profile = -> Sketch166
  Refine = true
  Type = 0
FEATURE [PartDesign::Draft] Draft001
  Angle = 10
  Base = -> Pad043 [Face25]
  BaseFeature = -> Pad043
  NeutralPlane = -> Pad043 [Face24]
  SupportTransform = false
FEATURE [Sketcher::SketchObject] Sketch167
  FullyConstrained = false
  MapMode = 5
  Placement = pos=(0,0,9.75) rot=(0,0,1;0rad)
  Support = -> [Draft001]
  sketch-geometry (1):
    g0: Circle CenterX=0 CenterY=0 CenterZ=0 NormalX=0 NormalY=0 NormalZ=1 AngleXU=0 Radius=5
  constraints (2):
    c: Coincident(g0,g-1)
    c: Radius(g0) = 5
FEATURE [PartDesign::Pocket] Pocket067
  AllowMultiFace = false
  BaseFeature = -> Draft001
  Length = 8
  Length2 = 100
  Profile = -> Sketch167
  Refine = true
  Type = 1
FEATURE [Sketcher::SketchObject] Sketch157
  FullyConstrained = false
  MapMode = 5
  Placement = pos=(0,0,0) rot=(1,0,0;3.14159rad)
  Support = -> [Pocket067]
  sketch-geometry (1):
    g0: Circle CenterX=0 CenterY=0 CenterZ=0 NormalX=0 NormalY=0 NormalZ=1 AngleXU=0 Radius=15.35
  constraints (2):
    c: Coincident(g0,g-1)
    c: Radius(g0) = 15.35
FEATURE [PartDesign::Pocket] Pocket073
  AllowMultiFace = false
  BaseFeature = -> Pocket067
  Length = 5
  Length2 = 100
  Profile = -> Sketch157
  Refine = true
  Type = 0
FEATURE [PartDesign::Body] Body155  label="Aluminum front002"
  Group = -> [Sketch161,Pad042,Chamfer010,Fillet177,Sketch164,Pocket065,Sketch165,Pocket066,Sketch166,Pad043,Draft001,Sketch167,Pocket067,Sketch157,Pocket073]
  Origin = -> Origin183
  Placement = pos=(0,0,32.35) rot=(0,0,1;0rad)
  Tip = -> Pocket073
FEATURE [App::Part] Part030  label="Aluminum front003"
  Group = -> [Body155]
  Origin = -> Origin187
FEATURE [Sketcher::SketchObject] Sketch168
  FullyConstrained = false
  MapMode = 5
  Support = -> [XY_Plane178]
  sketch-geometry (1):
    g0: Circle CenterX=0 CenterY=0 CenterZ=0 NormalX=0 NormalY=0 NormalZ=1 AngleXU=0 Radius=2.5
  constraints (2):
    c: Coincident(g0,g-1)
    c: Radius(g0) = 2.5
FEATURE [PartDesign::Pad] Pad044
  AllowMultiFace = false
  Direction = (1,1,1)
  Length = 60
  Length2 = 100
  Profile = -> Sketch168
  Refine = true
  Type = 0
FEATURE [Sketcher::SketchObject] Sketch169
  FullyConstrained = false
  MapMode = 5
  Placement = pos=(0,0,60) rot=(0,0,1;0rad)
  Support = -> [Pad044]
  sketch-geometry (4):
    g0: LineSegment StartX=2 StartY=2 StartZ=0 EndX=6 EndY=2 EndZ=0
    g1: LineSegment StartX=6 StartY=2 StartZ=0 EndX=6 EndY=-2 EndZ=0
    g2: LineSegment StartX=6 StartY=-2 StartZ=0 EndX=2 EndY=-2 EndZ=0
    g3: LineSegment StartX=2 StartY=-2 StartZ=0 EndX=2 EndY=2 EndZ=0
  constraints (11):
    c: Coincident(g0,g1)
    c: Coincident(g1,g2)
    c: Coincident(g2,g3)
    c: Coincident(g3,g0)
    c: Horizontal(g0)
    c: Horizontal(g2)
    c: Vertical(g1)
    c: Symmetric(g2,g0,g-1)
    c: DistanceX(g-1,g0) = 2
    c: Equal(g0,g3)
    c: DistanceX(g0,g0) = 4
FEATURE [PartDesign::Pocket] Pocket068
  AllowMultiFace = false
  BaseFeature = -> Pad044
  Length = 16
  Length2 = 100
  Profile = -> Sketch169
  Refine = true
  Type = 0
FEATURE [PartDesign::Chamfer] Chamfer011
  Angle = 45
  Base = -> Pocket068 [Edge3,Edge5,Edge9]
  BaseFeature = -> Pocket068
  ChamferType = 0
  FlipDirection = false
  Size = 0.3
  Size2 = 1
  SupportTransform = false
FEATURE [PartDesign::Body] Body156  label="Rotor002"
  Group = -> [Sketch168,Pad044,Sketch169,Pocket068,Chamfer011]
  Origin = -> Origin184
  Placement = pos=(0,0,2) rot=(0,0,1;0rad)
  Tip = -> Chamfer011
FEATURE [App::Part] Part031  label="Rotor003"
  Group = -> [Body156]
  Origin = -> Origin188
FEATURE [Sketcher::SketchObject] Sketch170
  FullyConstrained = false
  MapMode = 5
  Placement = pos=(0,0,22.75) rot=(0,0,1;0rad)
  Support = -> [Pocket064]
  sketch-geometry (1):
    g0: Circle CenterX=0 CenterY=0 CenterZ=0 NormalX=0 NormalY=0 NormalZ=1 AngleXU=0 Radius=18
  constraints (2):
    c: Coincident(g0,g-1)
    c: Radius(g0) = 18
FEATURE [PartDesign::Pocket] Pocket063
  AllowMultiFace = false
  BaseFeature = -> Pocket064
  Length = 5
  Length2 = 100
  Profile = -> Sketch170
  Refine = true
  Type = 1
FEATURE [PartDesign::Body] Body154
  Group = -> [Sketch160,Pad041,Chamfer009,Sketch163,Pocket064,Sketch170,Pocket063]
  Origin = -> Origin182
  Placement = pos=(0,0,9.6) rot=(0,0,1;0rad)
  Tip = -> Pocket063
FEATURE [App::Part] Part029  label="Body155"
  Group = -> [Body154,Body157]
  Origin = -> Origin186
FEATURE [Sketcher::SketchObject] Sketch171
  ExternalGeometry = -> [Hole001]
  FullyConstrained = false
  MapMode = 5
  Placement = pos=(21.15,0,0) rot=(0.57735,0.57735,0.57735;2.0944rad)
  Support = -> [Hole001]
  sketch-geometry (4):
    g0: LineSegment StartX=-8.2 StartY=3.6 StartZ=0 EndX=8.2 EndY=3.6 EndZ=0
    g1: LineSegment StartX=8.2 StartY=3.6 StartZ=0 EndX=8.2 EndY=9.6 EndZ=0
    g2: LineSegment StartX=8.2 StartY=9.6 StartZ=0 EndX=-8.2 EndY=9.6 EndZ=0
    g3: LineSegment StartX=-8.2 StartY=9.6 StartZ=0 EndX=-8.2 EndY=3.6 EndZ=0
  constraints (10):
    c: Coincident(g0,g1)
    c: Coincident(g1,g2)
    c: Coincident(g2,g3)
    c: Coincident(g3,g0)
    c: Horizontal(g0)
    c: Vertical(g1)
    c: Vertical(g3)
    c: Coincident(g0,g-3)
    c: PointOnObject(g1,g-5)
    c: Symmetric(g2,g1,g-2)
FEATURE [PartDesign::Pocket] Pocket069
  AllowMultiFace = false
  BaseFeature = -> Hole001
  Length = 4
  Length2 = 100
  Profile = -> Sketch171
  Refine = true
  Type = 0
FEATURE [PartDesign::Body] Body153  label="Aluminium rear002"
  Group = -> [Sketch158,Pad039,Sketch159,Pad040,Chamfer008,Fillet176,Sketch162,Hole001,Sketch171,Pocket069]
  Origin = -> Origin181
  Tip = -> Pocket069
FEATURE [App::Part] Part028  label="Aluminium rear003"
  Group = -> [Body153]
  Origin = -> Origin185
FEATURE [Sketcher::SketchObject] Sketch172
  FullyConstrained = false
  MapMode = 5
  Placement = pos=(0,0,0) rot=(0.57735,0.57735,0.57735;2.0944rad)
  Support = -> [YZ_Plane186]
  sketch-geometry (4):
    g0: LineSegment StartX=-7.5 StartY=0 StartZ=0 EndX=7.5 EndY=0 EndZ=0
    g1: LineSegment StartX=7.5 StartY=0 StartZ=0 EndX=7.5 EndY=5 EndZ=0
    g2: LineSegment StartX=7.5 StartY=5 StartZ=0 EndX=-7.5 EndY=5 EndZ=0
    g3: LineSegment StartX=-7.5 StartY=5 StartZ=0 EndX=-7.5 EndY=0 EndZ=0
  constraints (11):
    c: Coincident(g0,g1)
    c: Coincident(g1,g2)
    c: Coincident(g2,g3)
    c: Coincident(g3,g0)
    c: Horizontal(g0)
    c: Horizontal(g2)
    c: Vertical(g1)
    c: Vertical(g3)
    c: Symmetric(g0,g0,g-1)
    c: DistanceX(g0,g0) = 15
    c: DistanceY(g3,g3) = 5
FEATURE [PartDesign::Pad] Pad045
  AllowMultiFace = false
  Direction = (1,1,1)
  Length = 10
  Length2 = 100
  Placement = pos=(0,0,0) rot=(0.57735,0.57735,0.57735;2.0944rad)
  Profile = -> Sketch172
  Refine = true
  Type = 0
FEATURE [Sketcher::SketchObject] Sketch173
  ExternalGeometry = -> [Pad045]
  FullyConstrained = false
  MapMode = 5
  Placement = pos=(10,-2.2e-15,2.2e-15) rot=(0.57735,0.57735,0.57735;2.0944rad)
  Support = -> [Pad045]
  sketch-geometry (8):
    g0: LineSegment StartX=-6.5 StartY=4 StartZ=0 EndX=6.5 EndY=4 EndZ=0
    g1: LineSegment StartX=6.5 StartY=4 StartZ=0 EndX=6.5 EndY=1 EndZ=0
    g2: LineSegment StartX=6.5 StartY=1 StartZ=0 EndX=-6.5 EndY=1 EndZ=0
    g3: LineSegment StartX=-6.5 StartY=1 StartZ=0 EndX=-6.5 EndY=4 EndZ=0
    g4: LineSegment StartX=-6.5 StartY=1 StartZ=0 EndX=-7.5 EndY=1 EndZ=0
    g5: LineSegment StartX=-6.5 StartY=1 StartZ=0 EndX=-6.5 EndY=0 EndZ=0
    g6: LineSegment StartX=6.5 StartY=4 StartZ=0 EndX=6.5 EndY=5 EndZ=0
    g7: LineSegment StartX=6.5 StartY=4 StartZ=0 EndX=7.5 EndY=4 EndZ=0
  constraints (23):
    c: Coincident(g0,g1)
    c: Coincident(g1,g2)
    c: Coincident(g2,g3)
    c: Coincident(g3,g0)
    c: Horizontal(g2)
    c: Vertical(g1)
    c: Vertical(g3)
    c: Symmetric(g0,g0,g-2)
    c: Coincident(g4,g2)
    c: PointOnObject(g4,g-4)
    c: Horizontal(g4)
    c: PointOnObject(g5,g-1)
    c: Vertical(g5)
    c: Coincident(g6,g0)
    c: Coincident(g7,g0)
    c: Horizontal(g7)
    c: Vertical(g6)
    c: PointOnObject(g6,g-5)
    c: Equal(g7,g6)
    c: Equal(g6,g4)
    c: Equal(g4,g5)
    c: DistanceX(g4,g4) = 1
    c: Coincident(g5,g2)
FEATURE [PartDesign::Pocket] Pocket070
  AllowMultiFace = false
  BaseFeature = -> Pad045
  Length = 6
  Length2 = 100
  Placement = pos=(0,0,0) rot=(0.57735,0.57735,0.57735;2.0944rad)
  Profile = -> Sketch173
  Refine = true
  Type = 0
FEATURE [Sketcher::SketchObject] Sketch154
  ExternalGeometry = -> [Pocket070]
  FullyConstrained = false
  MapMode = 5
  Placement = pos=(10,-2.2e-15,2.2e-15) rot=(0.57735,0.57735,0.57735;2.0944rad)
  Support = -> [Pocket070]
  sketch-geometry (4):
    g0: LineSegment StartX=-4 StartY=5 StartZ=0 EndX=4 EndY=5 EndZ=0
    g1: LineSegment StartX=4 StartY=5 StartZ=0 EndX=4 EndY=4 EndZ=0
    g2: LineSegment StartX=4 StartY=4 StartZ=0 EndX=-4 EndY=4 EndZ=0
    g3: LineSegment StartX=-4 StartY=4 StartZ=0 EndX=-4 EndY=5 EndZ=0
  constraints (11):
    c: Coincident(g0,g1)
    c: Coincident(g1,g2)
    c: Coincident(g2,g3)
    c: Coincident(g3,g0)
    c: Horizontal(g0)
    c: Vertical(g1)
    c: Vertical(g3)
    c: PointOnObject(g0,g-3)
    c: PointOnObject(g1,g-4)
    c: Symmetric(g1,g2,g-2)
    c: DistanceX(g0,g0) = 8
FEATURE [PartDesign::Pocket] Pocket071
  AllowMultiFace = false
  BaseFeature = -> Pocket070
  Length = 4.5
  Length2 = 100
  Placement = pos=(0,0,0) rot=(0.57735,0.57735,0.57735;2.0944rad)
  Profile = -> Sketch154
  Refine = true
  Type = 0
FEATURE [Sketcher::SketchObject] Sketch155
  ExternalGeometry = -> [Pocket071]
  FullyConstrained = false
  MapMode = 5
  Placement = pos=(-1.4e-15,2.2e-15,5) rot=(0,0,-1;1.5708rad)
  Support = -> [Pocket071]
  sketch-geometry (11):
    g0: LineSegment StartX=-6.49 StartY=8.99 StartZ=0 EndX=-5.01 EndY=8.99 EndZ=0
    g1: LineSegment StartX=-5.01 StartY=8.99 StartZ=0 EndX=-5.01 EndY=4.5 EndZ=0
    g2: LineSegment StartX=-5.01 StartY=4.5 StartZ=0 EndX=-6.49 EndY=4.5 EndZ=0
    g3: LineSegment StartX=-6.49 StartY=4.5 StartZ=0 EndX=-6.49 EndY=8.99 EndZ=0
    g4: LineSegment StartX=5.01 StartY=8.99 StartZ=0 EndX=6.49 EndY=8.99 EndZ=0
    g5: LineSegment StartX=6.49 StartY=8.99 StartZ=0 EndX=6.49 EndY=4.5 EndZ=0
    g6: LineSegment StartX=6.49 StartY=4.5 StartZ=0 EndX=5.01 EndY=4.5 EndZ=0
    g7: LineSegment StartX=5.01 StartY=4.5 StartZ=0 EndX=5.01 EndY=8.99 EndZ=0
    g8: LineSegment StartX=-7.5 StartY=8.99 StartZ=0 EndX=-6.49 EndY=8.99 EndZ=0
    g9: LineSegment StartX=-6.49 StartY=10 StartZ=0 EndX=-6.49 EndY=8.99 EndZ=0
    g10: LineSegment StartX=-5.01 StartY=8.99 StartZ=0 EndX=-4 EndY=8.99 EndZ=0
  constraints (32):
    c: Coincident(g0,g1)
    c: Coincident(g1,g2)
    c: Coincident(g2,g3)
    c: Coincident(g3,g0)
    c: Horizontal(g0)
    c: Horizontal(g2)
    c: Vertical(g1)
    c: Vertical(g3)
    c: Coincident(g4,g5)
    c: Coincident(g5,g6)
    c: Coincident(g6,g7)
    c: Coincident(g7,g4)
    c: Horizontal(g4)
    c: Horizontal(g6)
    c: Vertical(g5)
    c: Vertical(g7)
    c: DistanceX(g4,g4) = 1.48
    c: Equal(g0,g4)
    c: Equal(g7,g1)
    c: PointOnObject(g8,g-4)
    c: Coincident(g8,g0)
    c: Horizontal(g8)
    c: PointOnObject(g9,g-5)
    c: Coincident(g9,g0)
    c: Vertical(g9)
    c: Coincident(g10,g0)
    c: PointOnObject(g10,g-3)
    c: Horizontal(g10)
    c: Symmetric(g4,g0,g-2)
    c: Equal(g10,g9)
    c: Equal(g9,g8)
    c: DistanceY(g3,g3) = 4.49
FEATURE [PartDesign::Pocket] Pocket072
  AllowMultiFace = false
  BaseFeature = -> Pocket071
  Length = 2
  Length2 = 100
  Placement = pos=(0,0,0) rot=(0.57735,0.57735,0.57735;2.0944rad)
  Profile = -> Sketch155
  Refine = true
  Type = 0
FEATURE [PartDesign::Body] Body158  label="conector001"
  Group = -> [Sketch172,Pad045,Sketch173,Pocket070,Sketch154,Pocket071,Sketch155,Pocket072]
  Origin = -> Origin192
  Tip = -> Pocket072
FEATURE [Sketcher::SketchObject] Sketch174
  ExternalGeometry = -> [Pad046]
  FullyConstrained = false
  MapMode = 5
  Placement = pos=(-3e-16,4e-16,1) rot=(0,0,-1;1.5708rad)
  Support = -> [Pad046]
  sketch-geometry (7):
    g0: LineSegment StartX=-5.5 StartY=1 StartZ=0 EndX=-4.5 EndY=1 EndZ=0
    g1: LineSegment StartX=-4.5 StartY=1 StartZ=0 EndX=-4.5 EndY=8 EndZ=0
    g2: LineSegment StartX=-4.5 StartY=8 StartZ=0 EndX=-5.5 EndY=8 EndZ=0
    g3: LineSegment StartX=-5.5 StartY=8 StartZ=0 EndX=-5.5 EndY=1 EndZ=0
    g4: LineSegment StartX=-5.5 StartY=8 StartZ=0 EndX=-5.25 EndY=8.7 EndZ=0
    g5: LineSegment StartX=-5.25 StartY=8.7 StartZ=0 EndX=-4.75 EndY=8.7 EndZ=0
    g6: LineSegment StartX=-4.75 StartY=8.7 StartZ=0 EndX=-4.5 EndY=8 EndZ=0
  constraints (19):
    c: Coincident(g0,g1)
    c: Coincident(g1,g2)
    c: Coincident(g2,g3)
    c: Coincident(g3,g0)
    c: Horizontal(g0)
    c: Horizontal(g2)
    c: Vertical(g1)
    c: Vertical(g3)
    c: Coincident(g0,g-3)
    c: Coincident(g2,g4)
    c: Coincident(g4,g5)
    c: Horizontal(g5)
    c: Coincident(g5,g6)
    c: Coincident(g6,g1)
    c: DistanceY(g1,g5) = 0.7
    c: DistanceX(g5,g5) = 0.5
    c: Equal(g6,g4)
    c: DistanceX(g0,g0) = 1
    c: DistanceY(g3,g3) = 7
FEATURE [PartDesign::Pad] Pad047
  AllowMultiFace = false
  BaseFeature = -> Pad046
  Direction = (1,1,1)
  Length = 1
  Length2 = 100
  Placement = pos=(0,0,0) rot=(0.57735,0.57735,0.57735;2.0944rad)
  Profile = -> Sketch174
  Refine = true
  Reversed = true
  Type = 0
FEATURE [PartDesign::LinearPattern] LinearPattern001
  BaseFeature = -> Pad047
  Direction = -> Pad047 [Edge10]
  Length = 10
  Occurrences = 3
  Originals = -> [Pad047]
  Placement = pos=(0,0,0) rot=(0.57735,0.57735,0.57735;2.0944rad)
  Refine = true
  Reversed = true
FEATURE [PartDesign::Body] Body159  label="pin001"
  Group = -> [Sketch156,Pad046,Sketch174,Pad047,LinearPattern001]
  Origin = -> Origin193
  Placement = pos=(0,0,2) rot=(0,0,1;0rad)
  Tip = -> LinearPattern001
FEATURE [App::Part] Part033  label="Conector001"
  Group = -> [Body158,Body159]
  Origin = -> Origin191
  Placement = pos=(17,0,4) rot=(0,0,1;0rad)
FEATURE [App::Part] Part027  label="Nema 017-002"
  Group = -> [Part028,Part029,Part030,Part031,Part032,Part033]
  Origin = -> Origin180
  Placement = pos=(440,247,106) rot=(0,1,0;-1.5708rad)
FEATURE [Sketcher::SketchObject] Sketch175
  FullyConstrained = true
  MapMode = 5
  Placement = pos=(0,0,0) rot=(0.57735,0.57735,0.57735;2.0944rad)
  Support = -> [YZ_Plane189]
  sketch-geometry (1):
    g0: Circle CenterX=0 CenterY=0 CenterZ=0 NormalX=0 NormalY=0 NormalZ=1 AngleXU=0 Radius=4
  constraints (2):
    c: Coincident(g0,g-1)
    c: Radius(g0) = 4
FEATURE [PartDesign::Pad] Pad048
  Direction = (1,-2e-16,3e-16)
  Length = 350
  Length2 = 10
  Placement = pos=(0,0,0) rot=(0.57735,0.57735,0.57735;2.0944rad)
  Profile = -> Sketch175
  Type = 0
FEATURE [PartDesign::Body] Body160
  Group = -> [Sketch175,Pad048]
  Origin = -> Origin195
  Tip = -> Pad048
FEATURE [App::Part] Part034  label="eje-001"
  Group = -> [Body160]
  Origin = -> Origin194
  Placement = pos=(-21,120,105) rot=(0,0,1;0rad)
FEATURE [Sketcher::SketchObject] Sketch176
  FullyConstrained = true
  MapMode = 5
  Placement = pos=(0,0,0) rot=(0.57735,0.57735,0.57735;2.0944rad)
  Support = -> [YZ_Plane191]
  sketch-geometry (1):
    g0: Circle CenterX=0 CenterY=0 CenterZ=0 NormalX=0 NormalY=0 NormalZ=1 AngleXU=0 Radius=4
  constraints (2):
    c: Coincident(g0,g-1)
    c: Radius(g0) = 4
FEATURE [PartDesign::Pad] Pad049
  Direction = (1,-2e-16,3e-16)
  Length = 350
  Length2 = 10
  Placement = pos=(0,0,0) rot=(0.57735,0.57735,0.57735;2.0944rad)
  Profile = -> Sketch176
  Type = 0
FEATURE [PartDesign::Body] Body161
  Group = -> [Sketch176,Pad049]
  Origin = -> Origin197
  Tip = -> Pad049
FEATURE [App::Part] Part035  label="eje-002"
  Group = -> [Body161]
  Origin = -> Origin196
  Placement = pos=(-31,120,80) rot=(0,0,1;0rad)
FEATURE [Sketcher::SketchObject] Sketch177
  FullyConstrained = true
  MapMode = 5
  Placement = pos=(0,0,0) rot=(0.57735,0.57735,0.57735;2.0944rad)
  Support = -> [YZ_Plane193]
  sketch-geometry (1):
    g0: Circle CenterX=0 CenterY=0 CenterZ=0 NormalX=0 NormalY=0 NormalZ=1 AngleXU=0 Radius=4
  constraints (2):
    c: Coincident(g0,g-1)
    c: Radius(g0) = 4
FEATURE [PartDesign::Pad] Pad050
  Direction = (1,-2e-16,3e-16)
  Length = 350
  Length2 = 10
  Placement = pos=(0,0,0) rot=(0.57735,0.57735,0.57735;2.0944rad)
  Profile = -> Sketch177
  Type = 0
FEATURE [PartDesign::Body] Body162
  Group = -> [Sketch177,Pad050]
  Origin = -> Origin199
  Tip = -> Pad050
FEATURE [App::Part] Part036  label="eje-003"
  Group = -> [Body162]
  Origin = -> Origin198
  Placement = pos=(-18,246,105) rot=(0,0,1;0rad)
FEATURE [Sketcher::SketchObject] Sketch178
  FullyConstrained = true
  MapMode = 5
  Placement = pos=(0,0,0) rot=(0.57735,0.57735,0.57735;2.0944rad)
  Support = -> [YZ_Plane195]
  sketch-geometry (1):
    g0: Circle CenterX=0 CenterY=0 CenterZ=0 NormalX=0 NormalY=0 NormalZ=1 AngleXU=0 Radius=60
  constraints (2):
    c: Coincident(g0,g-1)
    c: Radius(g0) = 60
FEATURE [PartDesign::Pad] Pad051
  Direction = (1,-2e-16,3e-16)
  Length = 8
  Length2 = 10
  Placement = pos=(0,0,0) rot=(0.57735,0.57735,0.57735;2.0944rad)
  Profile = -> Sketch178
  Type = 0
FEATURE [PartDesign::Body] Body163
  Group = -> [Sketch178,Pad051]
  Origin = -> Origin201
  Tip = -> Pad051
FEATURE [App::Part] Part037  label="rueda-001"
  Group = -> [Body163]
  Origin = -> Origin200
  Placement = pos=(191,246,105) rot=(0,0,1;0rad)
FEATURE [Sketcher::SketchObject] Sketch179
  FullyConstrained = false
  MapMode = 5
  Placement = pos=(0,0,0) rot=(0.57735,0.57735,0.57735;2.0944rad)
  Support = -> [YZ_Plane197]
  sketch-geometry (8):
    g0: LineSegment StartX=3.44519 StartY=-3.62363 StartZ=0 EndX=4.86075 EndY=1.17181 EndZ=0
    g1: LineSegment StartX=4.86075 StartY=1.17181 StartZ=0 EndX=1.41556 EndY=4.79544 EndZ=0
    g2: LineSegment StartX=1.41556 StartY=4.79544 StartZ=0 EndX=-3.44519 EndY=3.62363 EndZ=0
    g3: LineSegment StartX=-3.44519 StartY=3.62363 StartZ=0 EndX=-4.86075 EndY=-1.17181 EndZ=0
    g4: LineSegment StartX=-4.86075 StartY=-1.17181 StartZ=0 EndX=-1.41556 EndY=-4.79544 EndZ=0
    g5: LineSegment StartX=-1.41556 StartY=-4.79544 StartZ=0 EndX=3.44519 EndY=-3.62363 EndZ=0
    g6: Circle CenterX=0 CenterY=0 CenterZ=0 NormalX=0 NormalY=0 NormalZ=1 AngleXU=0 Radius=5
    g7: Circle CenterX=0 CenterY=0 CenterZ=0 NormalX=0 NormalY=0 NormalZ=1 AngleXU=0 Radius=3
  constraints (17):
    c: Coincident(g0,g1)
    c: Coincident(g1,g2)
    c: Coincident(g2,g3)
    c: Coincident(g3,g4)
    c: Coincident(g4,g5)
    c: Coincident(g5,g0)
    c: Equal(g0, g1-g5) x5
    c: PointOnObject(g0,g6)
    c: PointOnObject(g1,g6)
    c: PointOnObject(g2,g6)
    c: PointOnObject(g3,g6)
    c: PointOnObject(g4,g6)
    c: PointOnObject(g5,g6)
    c: Coincident(g6,g-1)
    c: Coincident(g7,g6)
    c: Radius(g7) = 3
    c: Radius(g6) = 5
FEATURE [PartDesign::Pad] Pad052
  Direction = (1,-2e-16,3e-16)
  Length = 3
  Length2 = 10
  Placement = pos=(0,0,0) rot=(0.57735,0.57735,0.57735;2.0944rad)
  Profile = -> Sketch179
  Type = 0
FEATURE [PartDesign::Pad] Pad053
  BaseFeature = -> Pad052
  Direction = (1,-2e-16,6e-16)
  Length = 50
  Length2 = 10
  Placement = pos=(0,0,0) rot=(0.57735,0.57735,0.57735;2.0944rad)
  Profile = -> Pad052 [Edge20]
  Type = 0
FEATURE [PartDesign::Body] Body164
  Group = -> [Sketch179,Pad052,Pad053]
  Origin = -> Origin203
  Tip = -> Pad053
FEATURE [App::Part] Part038  label="tornillo M6-30-001"
  Group = -> [Body164]
  Origin = -> Origin202
  Placement = pos=(10,-4,181) rot=(0,0,1;1.5708rad)
FEATURE [Sketcher::SketchObject] Sketch180
  FullyConstrained = false
  MapMode = 5
  Placement = pos=(0,0,0) rot=(0.57735,0.57735,0.57735;2.0944rad)
  Support = -> [YZ_Plane199]
  sketch-geometry (8):
    g0: LineSegment StartX=3.44519 StartY=-3.62363 StartZ=0 EndX=4.86075 EndY=1.17181 EndZ=0
    g1: LineSegment StartX=4.86075 StartY=1.17181 StartZ=0 EndX=1.41556 EndY=4.79544 EndZ=0
    g2: LineSegment StartX=1.41556 StartY=4.79544 StartZ=0 EndX=-3.44519 EndY=3.62363 EndZ=0
    g3: LineSegment StartX=-3.44519 StartY=3.62363 StartZ=0 EndX=-4.86075 EndY=-1.17181 EndZ=0
    g4: LineSegment StartX=-4.86075 StartY=-1.17181 StartZ=0 EndX=-1.41556 EndY=-4.79544 EndZ=0
    g5: LineSegment StartX=-1.41556 StartY=-4.79544 StartZ=0 EndX=3.44519 EndY=-3.62363 EndZ=0
    g6: Circle CenterX=0 CenterY=0 CenterZ=0 NormalX=0 NormalY=0 NormalZ=1 AngleXU=0 Radius=5
    g7: Circle CenterX=0 CenterY=0 CenterZ=0 NormalX=0 NormalY=0 NormalZ=1 AngleXU=0 Radius=3
  constraints (17):
    c: Coincident(g0,g1)
    c: Coincident(g1,g2)
    c: Coincident(g2,g3)
    c: Coincident(g3,g4)
    c: Coincident(g4,g5)
    c: Coincident(g5,g0)
    c: Equal(g0, g1-g5) x5
    c: PointOnObject(g0,g6)
    c: PointOnObject(g1,g6)
    c: PointOnObject(g2,g6)
    c: PointOnObject(g3,g6)
    c: PointOnObject(g4,g6)
    c: PointOnObject(g5,g6)
    c: Coincident(g6,g-1)
    c: Coincident(g7,g6)
    c: Radius(g7) = 3
    c: Radius(g6) = 5
FEATURE [PartDesign::Pad] Pad054
  Direction = (1,-2e-16,3e-16)
  Length = 3
  Length2 = 10
  Placement = pos=(0,0,0) rot=(0.57735,0.57735,0.57735;2.0944rad)
  Profile = -> Sketch180
  Type = 0
FEATURE [PartDesign::Pad] Pad055
  BaseFeature = -> Pad054
  Direction = (1,-2e-16,6e-16)
  Length = 50
  Length2 = 10
  Placement = pos=(0,0,0) rot=(0.57735,0.57735,0.57735;2.0944rad)
  Profile = -> Pad054 [Edge20]
  Type = 0
FEATURE [PartDesign::Body] Body165
  Group = -> [Sketch180,Pad054,Pad055]
  Origin = -> Origin205
  Tip = -> Pad055
FEATURE [App::Part] Part039  label="tornillo M6-30-002"
  Group = -> [Body165]
  Origin = -> Origin204
  Placement = pos=(10,-4,10) rot=(0,0,1;1.5708rad)
FEATURE [Sketcher::SketchObject] Sketch181
  FullyConstrained = false
  MapMode = 5
  Placement = pos=(0,0,0) rot=(0.57735,0.57735,0.57735;2.0944rad)
  Support = -> [YZ_Plane201]
  sketch-geometry (8):
    g0: LineSegment StartX=3.44519 StartY=-3.62363 StartZ=0 EndX=4.86075 EndY=1.17181 EndZ=0
    g1: LineSegment StartX=4.86075 StartY=1.17181 StartZ=0 EndX=1.41556 EndY=4.79544 EndZ=0
    g2: LineSegment StartX=1.41556 StartY=4.79544 StartZ=0 EndX=-3.44519 EndY=3.62363 EndZ=0
    g3: LineSegment StartX=-3.44519 StartY=3.62363 StartZ=0 EndX=-4.86075 EndY=-1.17181 EndZ=0
    g4: LineSegment StartX=-4.86075 StartY=-1.17181 StartZ=0 EndX=-1.41556 EndY=-4.79544 EndZ=0
    g5: LineSegment StartX=-1.41556 StartY=-4.79544 StartZ=0 EndX=3.44519 EndY=-3.62363 EndZ=0
    g6: Circle CenterX=0 CenterY=0 CenterZ=0 NormalX=0 NormalY=0 NormalZ=1 AngleXU=0 Radius=5
    g7: Circle CenterX=0 CenterY=0 CenterZ=0 NormalX=0 NormalY=0 NormalZ=1 AngleXU=0 Radius=3
  constraints (17):
    c: Coincident(g0,g1)
    c: Coincident(g1,g2)
    c: Coincident(g2,g3)
    c: Coincident(g3,g4)
    c: Coincident(g4,g5)
    c: Coincident(g5,g0)
    c: Equal(g0, g1-g5) x5
    c: PointOnObject(g0,g6)
    c: PointOnObject(g1,g6)
    c: PointOnObject(g2,g6)
    c: PointOnObject(g3,g6)
    c: PointOnObject(g4,g6)
    c: PointOnObject(g5,g6)
    c: Coincident(g6,g-1)
    c: Coincident(g7,g6)
    c: Radius(g7) = 3
    c: Radius(g6) = 5
FEATURE [PartDesign::Pad] Pad056
  Direction = (1,-2e-16,3e-16)
  Length = 3
  Length2 = 10
  Placement = pos=(0,0,0) rot=(0.57735,0.57735,0.57735;2.0944rad)
  Profile = -> Sketch181
  Type = 0
FEATURE [PartDesign::Pad] Pad057
  BaseFeature = -> Pad056
  Direction = (1,-2e-16,6e-16)
  Length = 50
  Length2 = 10
  Placement = pos=(0,0,0) rot=(0.57735,0.57735,0.57735;2.0944rad)
  Profile = -> Pad056 [Edge20]
  Type = 0
FEATURE [PartDesign::Body] Body166
  Group = -> [Sketch181,Pad056,Pad057]
  Origin = -> Origin207
  Tip = -> Pad057
FEATURE [App::Part] Part040  label="tornillo M6-30-003"
  Group = -> [Body166]
  Origin = -> Origin206
  Placement = pos=(330,-4,9) rot=(0,0,1;1.5708rad)
FEATURE [Sketcher::SketchObject] Sketch182
  FullyConstrained = false
  MapMode = 5
  Placement = pos=(0,0,0) rot=(0.57735,0.57735,0.57735;2.0944rad)
  Support = -> [YZ_Plane203]
  sketch-geometry (8):
    g0: LineSegment StartX=3.44519 StartY=-3.62363 StartZ=0 EndX=4.86075 EndY=1.17181 EndZ=0
    g1: LineSegment StartX=4.86075 StartY=1.17181 StartZ=0 EndX=1.41556 EndY=4.79544 EndZ=0
    g2: LineSegment StartX=1.41556 StartY=4.79544 StartZ=0 EndX=-3.44519 EndY=3.62363 EndZ=0
    g3: LineSegment StartX=-3.44519 StartY=3.62363 StartZ=0 EndX=-4.86075 EndY=-1.17181 EndZ=0
    g4: LineSegment StartX=-4.86075 StartY=-1.17181 StartZ=0 EndX=-1.41556 EndY=-4.79544 EndZ=0
    g5: LineSegment StartX=-1.41556 StartY=-4.79544 StartZ=0 EndX=3.44519 EndY=-3.62363 EndZ=0
    g6: Circle CenterX=0 CenterY=0 CenterZ=0 NormalX=0 NormalY=0 NormalZ=1 AngleXU=0 Radius=5
    g7: Circle CenterX=0 CenterY=0 CenterZ=0 NormalX=0 NormalY=0 NormalZ=1 AngleXU=0 Radius=3
  constraints (17):
    c: Coincident(g0,g1)
    c: Coincident(g1,g2)
    c: Coincident(g2,g3)
    c: Coincident(g3,g4)
    c: Coincident(g4,g5)
    c: Coincident(g5,g0)
    c: Equal(g0, g1-g5) x5
    c: PointOnObject(g0,g6)
    c: PointOnObject(g1,g6)
    c: PointOnObject(g2,g6)
    c: PointOnObject(g3,g6)
    c: PointOnObject(g4,g6)
    c: PointOnObject(g5,g6)
    c: Coincident(g6,g-1)
    c: Coincident(g7,g6)
    c: Radius(g7) = 3
    c: Radius(g6) = 5
FEATURE [PartDesign::Pad] Pad058
  Direction = (1,-2e-16,3e-16)
  Length = 3
  Length2 = 10
  Placement = pos=(0,0,0) rot=(0.57735,0.57735,0.57735;2.0944rad)
  Profile = -> Sketch182
  Type = 0
FEATURE [PartDesign::Pad] Pad059
  BaseFeature = -> Pad058
  Direction = (1,-2e-16,6e-16)
  Length = 50
  Length2 = 10
  Placement = pos=(0,0,0) rot=(0.57735,0.57735,0.57735;2.0944rad)
  Profile = -> Pad058 [Edge20]
  Type = 0
FEATURE [PartDesign::Body] Body167
  Group = -> [Sketch182,Pad058,Pad059]
  Origin = -> Origin209
  Tip = -> Pad059
FEATURE [App::Part] Part041  label="tornillo M6-30-004"
  Group = -> [Body167]
  Origin = -> Origin208
  Placement = pos=(330,-4,181) rot=(0,0,1;1.5708rad)
FEATURE [Sketcher::SketchObject] Sketch183
  FullyConstrained = false
  MapMode = 5
  Placement = pos=(0,0,0) rot=(0.57735,0.57735,0.57735;2.0944rad)
  Support = -> [YZ_Plane205]
  sketch-geometry (8):
    g0: LineSegment StartX=3.44519 StartY=-3.62363 StartZ=0 EndX=4.86075 EndY=1.17181 EndZ=0
    g1: LineSegment StartX=4.86075 StartY=1.17181 StartZ=0 EndX=1.41556 EndY=4.79544 EndZ=0
    g2: LineSegment StartX=1.41556 StartY=4.79544 StartZ=0 EndX=-3.44519 EndY=3.62363 EndZ=0
    g3: LineSegment StartX=-3.44519 StartY=3.62363 StartZ=0 EndX=-4.86075 EndY=-1.17181 EndZ=0
    g4: LineSegment StartX=-4.86075 StartY=-1.17181 StartZ=0 EndX=-1.41556 EndY=-4.79544 EndZ=0
    g5: LineSegment StartX=-1.41556 StartY=-4.79544 StartZ=0 EndX=3.44519 EndY=-3.62363 EndZ=0
    g6: Circle CenterX=0 CenterY=0 CenterZ=0 NormalX=0 NormalY=0 NormalZ=1 AngleXU=0 Radius=5
    g7: Circle CenterX=0 CenterY=0 CenterZ=0 NormalX=0 NormalY=0 NormalZ=1 AngleXU=0 Radius=3
  constraints (17):
    c: Coincident(g0,g1)
    c: Coincident(g1,g2)
    c: Coincident(g2,g3)
    c: Coincident(g3,g4)
    c: Coincident(g4,g5)
    c: Coincident(g5,g0)
    c: Equal(g0, g1-g5) x5
    c: PointOnObject(g0,g6)
    c: PointOnObject(g1,g6)
    c: PointOnObject(g2,g6)
    c: PointOnObject(g3,g6)
    c: PointOnObject(g4,g6)
    c: PointOnObject(g5,g6)
    c: Coincident(g6,g-1)
    c: Coincident(g7,g6)
    c: Radius(g7) = 3
    c: Radius(g6) = 5
FEATURE [PartDesign::Pad] Pad060
  Direction = (1,-2e-16,3e-16)
  Length = 3
  Length2 = 10
  Placement = pos=(0,0,0) rot=(0.57735,0.57735,0.57735;2.0944rad)
  Profile = -> Sketch183
  Type = 0
FEATURE [PartDesign::Pad] Pad061
  BaseFeature = -> Pad060
  Direction = (1,-2e-16,6e-16)
  Length = 50
  Length2 = 10
  Placement = pos=(0,0,0) rot=(0.57735,0.57735,0.57735;2.0944rad)
  Profile = -> Pad060 [Edge20]
  Type = 0
FEATURE [PartDesign::Body] Body168
  Group = -> [Sketch183,Pad060,Pad061]
  Origin = -> Origin211
  Tip = -> Pad061
FEATURE [App::Part] Part042  label="tornillo M6-30-005"
  Group = -> [Body168]
  Origin = -> Origin210
  Placement = pos=(330,344,180) rot=(0,0,1;-1.5708rad)
FEATURE [Sketcher::SketchObject] Sketch184
  FullyConstrained = false
  MapMode = 5
  Placement = pos=(0,0,0) rot=(0.57735,0.57735,0.57735;2.0944rad)
  Support = -> [YZ_Plane207]
  sketch-geometry (8):
    g0: LineSegment StartX=3.44519 StartY=-3.62363 StartZ=0 EndX=4.86075 EndY=1.17181 EndZ=0
    g1: LineSegment StartX=4.86075 StartY=1.17181 StartZ=0 EndX=1.41556 EndY=4.79544 EndZ=0
    g2: LineSegment StartX=1.41556 StartY=4.79544 StartZ=0 EndX=-3.44519 EndY=3.62363 EndZ=0
    g3: LineSegment StartX=-3.44519 StartY=3.62363 StartZ=0 EndX=-4.86075 EndY=-1.17181 EndZ=0
    g4: LineSegment StartX=-4.86075 StartY=-1.17181 StartZ=0 EndX=-1.41556 EndY=-4.79544 EndZ=0
    g5: LineSegment StartX=-1.41556 StartY=-4.79544 StartZ=0 EndX=3.44519 EndY=-3.62363 EndZ=0
    g6: Circle CenterX=0 CenterY=0 CenterZ=0 NormalX=0 NormalY=0 NormalZ=1 AngleXU=0 Radius=5
    g7: Circle CenterX=0 CenterY=0 CenterZ=0 NormalX=0 NormalY=0 NormalZ=1 AngleXU=0 Radius=3
  constraints (17):
    c: Coincident(g0,g1)
    c: Coincident(g1,g2)
    c: Coincident(g2,g3)
    c: Coincident(g3,g4)
    c: Coincident(g4,g5)
    c: Coincident(g5,g0)
    c: Equal(g0, g1-g5) x5
    c: PointOnObject(g0,g6)
    c: PointOnObject(g1,g6)
    c: PointOnObject(g2,g6)
    c: PointOnObject(g3,g6)
    c: PointOnObject(g4,g6)
    c: PointOnObject(g5,g6)
    c: Coincident(g6,g-1)
    c: Coincident(g7,g6)
    c: Radius(g7) = 3
    c: Radius(g6) = 5
FEATURE [PartDesign::Pad] Pad062
  Direction = (1,-2e-16,3e-16)
  Length = 3
  Length2 = 10
  Placement = pos=(0,0,0) rot=(0.57735,0.57735,0.57735;2.0944rad)
  Profile = -> Sketch184
  Type = 0
FEATURE [PartDesign::Pad] Pad063
  BaseFeature = -> Pad062
  Direction = (1,-2e-16,6e-16)
  Length = 50
  Length2 = 10
  Placement = pos=(0,0,0) rot=(0.57735,0.57735,0.57735;2.0944rad)
  Profile = -> Pad062 [Edge20]
  Type = 0
FEATURE [PartDesign::Body] Body169
  Group = -> [Sketch184,Pad062,Pad063]
  Origin = -> Origin213
  Tip = -> Pad063
FEATURE [App::Part] Part043  label="tornillo M6-30-006"
  Group = -> [Body169]
  Origin = -> Origin212
  Placement = pos=(330,344,9) rot=(0,0,1;-1.5708rad)
FEATURE [Sketcher::SketchObject] Sketch185
  FullyConstrained = false
  MapMode = 5
  Placement = pos=(0,0,0) rot=(0.57735,0.57735,0.57735;2.0944rad)
  Support = -> [YZ_Plane209]
  sketch-geometry (8):
    g0: LineSegment StartX=3.44519 StartY=-3.62363 StartZ=0 EndX=4.86075 EndY=1.17181 EndZ=0
    g1: LineSegment StartX=4.86075 StartY=1.17181 StartZ=0 EndX=1.41556 EndY=4.79544 EndZ=0
    g2: LineSegment StartX=1.41556 StartY=4.79544 StartZ=0 EndX=-3.44519 EndY=3.62363 EndZ=0
    g3: LineSegment StartX=-3.44519 StartY=3.62363 StartZ=0 EndX=-4.86075 EndY=-1.17181 EndZ=0
    g4: LineSegment StartX=-4.86075 StartY=-1.17181 StartZ=0 EndX=-1.41556 EndY=-4.79544 EndZ=0
    g5: LineSegment StartX=-1.41556 StartY=-4.79544 StartZ=0 EndX=3.44519 EndY=-3.62363 EndZ=0
    g6: Circle CenterX=0 CenterY=0 CenterZ=0 NormalX=0 NormalY=0 NormalZ=1 AngleXU=0 Radius=5
    g7: Circle CenterX=0 CenterY=0 CenterZ=0 NormalX=0 NormalY=0 NormalZ=1 AngleXU=0 Radius=3
  constraints (17):
    c: Coincident(g0,g1)
    c: Coincident(g1,g2)
    c: Coincident(g2,g3)
    c: Coincident(g3,g4)
    c: Coincident(g4,g5)
    c: Coincident(g5,g0)
    c: Equal(g0, g1-g5) x5
    c: PointOnObject(g0,g6)
    c: PointOnObject(g1,g6)
    c: PointOnObject(g2,g6)
    c: PointOnObject(g3,g6)
    c: PointOnObject(g4,g6)
    c: PointOnObject(g5,g6)
    c: Coincident(g6,g-1)
    c: Coincident(g7,g6)
    c: Radius(g7) = 3
    c: Radius(g6) = 5
FEATURE [PartDesign::Pad] Pad064
  Direction = (1,-2e-16,3e-16)
  Length = 3
  Length2 = 10
  Placement = pos=(0,0,0) rot=(0.57735,0.57735,0.57735;2.0944rad)
  Profile = -> Sketch185
  Type = 0
FEATURE [PartDesign::Pad] Pad065
  BaseFeature = -> Pad064
  Direction = (1,-2e-16,6e-16)
  Length = 50
  Length2 = 10
  Placement = pos=(0,0,0) rot=(0.57735,0.57735,0.57735;2.0944rad)
  Profile = -> Pad064 [Edge20]
  Type = 0
FEATURE [PartDesign::Body] Body170
  Group = -> [Sketch185,Pad064,Pad065]
  Origin = -> Origin215
  Tip = -> Pad065
FEATURE [App::Part] Part044  label="tornillo M6-30-007"
  Group = -> [Body170]
  Origin = -> Origin214
  Placement = pos=(10,344,10) rot=(0,0,1;-1.5708rad)
FEATURE [Sketcher::SketchObject] Sketch186
  FullyConstrained = false
  MapMode = 5
  Placement = pos=(0,0,0) rot=(0.57735,0.57735,0.57735;2.0944rad)
  Support = -> [YZ_Plane211]
  sketch-geometry (8):
    g0: LineSegment StartX=3.44519 StartY=-3.62363 StartZ=0 EndX=4.86075 EndY=1.17181 EndZ=0
    g1: LineSegment StartX=4.86075 StartY=1.17181 StartZ=0 EndX=1.41556 EndY=4.79544 EndZ=0
    g2: LineSegment StartX=1.41556 StartY=4.79544 StartZ=0 EndX=-3.44519 EndY=3.62363 EndZ=0
    g3: LineSegment StartX=-3.44519 StartY=3.62363 StartZ=0 EndX=-4.86075 EndY=-1.17181 EndZ=0
    g4: LineSegment StartX=-4.86075 StartY=-1.17181 StartZ=0 EndX=-1.41556 EndY=-4.79544 EndZ=0
    g5: LineSegment StartX=-1.41556 StartY=-4.79544 StartZ=0 EndX=3.44519 EndY=-3.62363 EndZ=0
    g6: Circle CenterX=0 CenterY=0 CenterZ=0 NormalX=0 NormalY=0 NormalZ=1 AngleXU=0 Radius=5
    g7: Circle CenterX=0 CenterY=0 CenterZ=0 NormalX=0 NormalY=0 NormalZ=1 AngleXU=0 Radius=3
  constraints (17):
    c: Coincident(g0,g1)
    c: Coincident(g1,g2)
    c: Coincident(g2,g3)
    c: Coincident(g3,g4)
    c: Coincident(g4,g5)
    c: Coincident(g5,g0)
    c: Equal(g0, g1-g5) x5
    c: PointOnObject(g0,g6)
    c: PointOnObject(g1,g6)
    c: PointOnObject(g2,g6)
    c: PointOnObject(g3,g6)
    c: PointOnObject(g4,g6)
    c: PointOnObject(g5,g6)
    c: Coincident(g6,g-1)
    c: Coincident(g7,g6)
    c: Radius(g7) = 3
    c: Radius(g6) = 5
FEATURE [PartDesign::Pad] Pad066
  Direction = (1,-2e-16,3e-16)
  Length = 3
  Length2 = 10
  Placement = pos=(0,0,0) rot=(0.57735,0.57735,0.57735;2.0944rad)
  Profile = -> Sketch186
  Type = 0
FEATURE [PartDesign::Pad] Pad067
  BaseFeature = -> Pad066
  Direction = (1,-2e-16,6e-16)
  Length = 50
  Length2 = 10
  Placement = pos=(0,0,0) rot=(0.57735,0.57735,0.57735;2.0944rad)
  Profile = -> Pad066 [Edge20]
  Type = 0
FEATURE [PartDesign::Body] Body171
  Group = -> [Sketch186,Pad066,Pad067]
  Origin = -> Origin217
  Tip = -> Pad067
FEATURE [App::Part] Part045  label="tornillo M6-30-008"
  Group = -> [Body171]
  Origin = -> Origin216
  Placement = pos=(10,344,180) rot=(0,0,1;-1.5708rad)
FEATURE [Sketcher::SketchObject] Sketch187
  FullyConstrained = false
  MapMode = 5
  Placement = pos=(0,0,0) rot=(0.57735,0.57735,0.57735;2.0944rad)
  Support = -> [YZ_Plane213]
  sketch-geometry (8):
    g0: LineSegment StartX=2.8963 StartY=-2.75889 StartZ=0 EndX=3.83742 EndY=1.12882 EndZ=0
    g1: LineSegment StartX=3.83742 StartY=1.12882 StartZ=0 EndX=0.941117 EndY=3.88771 EndZ=0
    g2: LineSegment StartX=0.941117 StartY=3.88771 StartZ=0 EndX=-2.8963 EndY=2.75889 EndZ=0
    g3: LineSegment StartX=-2.8963 StartY=2.75889 StartZ=0 EndX=-3.83742 EndY=-1.12882 EndZ=0
    g4: LineSegment StartX=-3.83742 StartY=-1.12882 StartZ=0 EndX=-0.941117 EndY=-3.88771 EndZ=0
    g5: LineSegment StartX=-0.941117 StartY=-3.88771 StartZ=0 EndX=2.8963 EndY=-2.75889 EndZ=0
    g6: Circle CenterX=0 CenterY=0 CenterZ=0 NormalX=0 NormalY=0 NormalZ=1 AngleXU=0 Radius=4
    g7: Circle CenterX=0 CenterY=0 CenterZ=0 NormalX=0 NormalY=0 NormalZ=1 AngleXU=0 Radius=2.5
  constraints (17):
    c: Coincident(g0,g1)
    c: Coincident(g1,g2)
    c: Coincident(g2,g3)
    c: Coincident(g3,g4)
    c: Coincident(g4,g5)
    c: Coincident(g5,g0)
    c: Equal(g0, g1-g5) x5
    c: PointOnObject(g0,g6)
    c: PointOnObject(g1,g6)
    c: PointOnObject(g2,g6)
    c: PointOnObject(g3,g6)
    c: PointOnObject(g4,g6)
    c: PointOnObject(g5,g6)
    c: Coincident(g6,g-1)
    c: Coincident(g7,g6)
    c: Radius(g7) = 2.5
    c: Radius(g6) = 4
FEATURE [PartDesign::Pad] Pad068
  Direction = (1,-2e-16,3e-16)
  Length = 3
  Length2 = 10
  Placement = pos=(0,0,0) rot=(0.57735,0.57735,0.57735;2.0944rad)
  Profile = -> Sketch187
  Type = 0
FEATURE [PartDesign::Pad] Pad069
  BaseFeature = -> Pad068
  Direction = (1,-2e-16,6e-16)
  Length = 15
  Length2 = 10
  Placement = pos=(0,0,0) rot=(0.57735,0.57735,0.57735;2.0944rad)
  Profile = -> Pad068 [Edge20]
  Type = 0
FEATURE [PartDesign::Body] Body172
  Group = -> [Sketch187,Pad068,Pad069]
  Origin = -> Origin219
  Tip = -> Pad069
FEATURE [App::Part] Part046  label="tornillo M5-15-001"
  Group = -> [Body172]
  Origin = -> Origin218
  Placement = pos=(10,267,98) rot=(0,1,0;1.5708rad)
FEATURE [Sketcher::SketchObject] Sketch188
  FullyConstrained = false
  MapMode = 5
  Placement = pos=(0,0,0) rot=(0.57735,0.57735,0.57735;2.0944rad)
  Support = -> [YZ_Plane215]
  sketch-geometry (8):
    g0: LineSegment StartX=2.8963 StartY=-2.75889 StartZ=0 EndX=3.83742 EndY=1.12882 EndZ=0
    g1: LineSegment StartX=3.83742 StartY=1.12882 StartZ=0 EndX=0.941117 EndY=3.88771 EndZ=0
    g2: LineSegment StartX=0.941117 StartY=3.88771 StartZ=0 EndX=-2.8963 EndY=2.75889 EndZ=0
    g3: LineSegment StartX=-2.8963 StartY=2.75889 StartZ=0 EndX=-3.83742 EndY=-1.12882 EndZ=0
    g4: LineSegment StartX=-3.83742 StartY=-1.12882 StartZ=0 EndX=-0.941117 EndY=-3.88771 EndZ=0
    g5: LineSegment StartX=-0.941117 StartY=-3.88771 StartZ=0 EndX=2.8963 EndY=-2.75889 EndZ=0
    g6: Circle CenterX=0 CenterY=0 CenterZ=0 NormalX=0 NormalY=0 NormalZ=1 AngleXU=0 Radius=4
    g7: Circle CenterX=0 CenterY=0 CenterZ=0 NormalX=0 NormalY=0 NormalZ=1 AngleXU=0 Radius=2.5
  constraints (17):
    c: Coincident(g0,g1)
    c: Coincident(g1,g2)
    c: Coincident(g2,g3)
    c: Coincident(g3,g4)
    c: Coincident(g4,g5)
    c: Coincident(g5,g0)
    c: Equal(g0, g1-g5) x5
    c: PointOnObject(g0,g6)
    c: PointOnObject(g1,g6)
    c: PointOnObject(g2,g6)
    c: PointOnObject(g3,g6)
    c: PointOnObject(g4,g6)
    c: PointOnObject(g5,g6)
    c: Coincident(g6,g-1)
    c: Coincident(g7,g6)
    c: Radius(g7) = 2.5
    c: Radius(g6) = 4
FEATURE [PartDesign::Pad] Pad070
  Direction = (1,-2e-16,3e-16)
  Length = 3
  Length2 = 10
  Placement = pos=(0,0,0) rot=(0.57735,0.57735,0.57735;2.0944rad)
  Profile = -> Sketch188
  Type = 0
FEATURE [PartDesign::Pad] Pad071
  BaseFeature = -> Pad070
  Direction = (1,-2e-16,6e-16)
  Length = 15
  Length2 = 10
  Placement = pos=(0,0,0) rot=(0.57735,0.57735,0.57735;2.0944rad)
  Profile = -> Pad070 [Edge20]
  Type = 0
FEATURE [PartDesign::Body] Body173
  Group = -> [Sketch188,Pad070,Pad071]
  Origin = -> Origin221
  Tip = -> Pad071
FEATURE [App::Part] Part047  label="tornillo M5-15-002"
  Group = -> [Body173]
  Origin = -> Origin220
  Placement = pos=(10,99,98) rot=(0,1,0;1.5708rad)
FEATURE [Sketcher::SketchObject] Sketch189
  FullyConstrained = false
  MapMode = 5
  Placement = pos=(0,0,0) rot=(0.57735,0.57735,0.57735;2.0944rad)
  Support = -> [YZ_Plane217]
  sketch-geometry (8):
    g0: LineSegment StartX=2.8963 StartY=-2.75889 StartZ=0 EndX=3.83742 EndY=1.12882 EndZ=0
    g1: LineSegment StartX=3.83742 StartY=1.12882 StartZ=0 EndX=0.941117 EndY=3.88771 EndZ=0
    g2: LineSegment StartX=0.941117 StartY=3.88771 StartZ=0 EndX=-2.8963 EndY=2.75889 EndZ=0
    g3: LineSegment StartX=-2.8963 StartY=2.75889 StartZ=0 EndX=-3.83742 EndY=-1.12882 EndZ=0
    g4: LineSegment StartX=-3.83742 StartY=-1.12882 StartZ=0 EndX=-0.941117 EndY=-3.88771 EndZ=0
    g5: LineSegment StartX=-0.941117 StartY=-3.88771 StartZ=0 EndX=2.8963 EndY=-2.75889 EndZ=0
    g6: Circle CenterX=0 CenterY=0 CenterZ=0 NormalX=0 NormalY=0 NormalZ=1 AngleXU=0 Radius=4
    g7: Circle CenterX=0 CenterY=0 CenterZ=0 NormalX=0 NormalY=0 NormalZ=1 AngleXU=0 Radius=2.5
  constraints (17):
    c: Coincident(g0,g1)
    c: Coincident(g1,g2)
    c: Coincident(g2,g3)
    c: Coincident(g3,g4)
    c: Coincident(g4,g5)
    c: Coincident(g5,g0)
    c: Equal(g0, g1-g5) x5
    c: PointOnObject(g0,g6)
    c: PointOnObject(g1,g6)
    c: PointOnObject(g2,g6)
    c: PointOnObject(g3,g6)
    c: PointOnObject(g4,g6)
    c: PointOnObject(g5,g6)
    c: Coincident(g6,g-1)
    c: Coincident(g7,g6)
    c: Radius(g7) = 2.5
    c: Radius(g6) = 4
FEATURE [PartDesign::Pad] Pad072
  Direction = (1,-2e-16,3e-16)
  Length = 3
  Length2 = 10
  Placement = pos=(0,0,0) rot=(0.57735,0.57735,0.57735;2.0944rad)
  Profile = -> Sketch189
  Type = 0
FEATURE [PartDesign::Pad] Pad073
  BaseFeature = -> Pad072
  Direction = (1,-2e-16,6e-16)
  Length = 15
  Length2 = 10
  Placement = pos=(0,0,0) rot=(0.57735,0.57735,0.57735;2.0944rad)
  Profile = -> Pad072 [Edge20]
  Type = 0
FEATURE [PartDesign::Body] Body174
  Group = -> [Sketch189,Pad072,Pad073]
  Origin = -> Origin223
  Tip = -> Pad073
FEATURE [App::Part] Part048  label="tornillo M5-15-003"
  Group = -> [Body174]
  Origin = -> Origin222
  Placement = pos=(10,225,98) rot=(0,1,0;1.5708rad)
FEATURE [Sketcher::SketchObject] Sketch190
  FullyConstrained = false
  MapMode = 5
  Placement = pos=(0,0,0) rot=(0.57735,0.57735,0.57735;2.0944rad)
  Support = -> [YZ_Plane219]
  sketch-geometry (8):
    g0: LineSegment StartX=2.8963 StartY=-2.75889 StartZ=0 EndX=3.83742 EndY=1.12882 EndZ=0
    g1: LineSegment StartX=3.83742 StartY=1.12882 StartZ=0 EndX=0.941117 EndY=3.88771 EndZ=0
    g2: LineSegment StartX=0.941117 StartY=3.88771 StartZ=0 EndX=-2.8963 EndY=2.75889 EndZ=0
    g3: LineSegment StartX=-2.8963 StartY=2.75889 StartZ=0 EndX=-3.83742 EndY=-1.12882 EndZ=0
    g4: LineSegment StartX=-3.83742 StartY=-1.12882 StartZ=0 EndX=-0.941117 EndY=-3.88771 EndZ=0
    g5: LineSegment StartX=-0.941117 StartY=-3.88771 StartZ=0 EndX=2.8963 EndY=-2.75889 EndZ=0
    g6: Circle CenterX=0 CenterY=0 CenterZ=0 NormalX=0 NormalY=0 NormalZ=1 AngleXU=0 Radius=4
    g7: Circle CenterX=0 CenterY=0 CenterZ=0 NormalX=0 NormalY=0 NormalZ=1 AngleXU=0 Radius=2.5
  constraints (17):
    c: Coincident(g0,g1)
    c: Coincident(g1,g2)
    c: Coincident(g2,g3)
    c: Coincident(g3,g4)
    c: Coincident(g4,g5)
    c: Coincident(g5,g0)
    c: Equal(g0, g1-g5) x5
    c: PointOnObject(g0,g6)
    c: PointOnObject(g1,g6)
    c: PointOnObject(g2,g6)
    c: PointOnObject(g3,g6)
    c: PointOnObject(g4,g6)
    c: PointOnObject(g5,g6)
    c: Coincident(g6,g-1)
    c: Coincident(g7,g6)
    c: Radius(g7) = 2.5
    c: Radius(g6) = 4
FEATURE [PartDesign::Pad] Pad074
  Direction = (1,-2e-16,3e-16)
  Length = 3
  Length2 = 10
  Placement = pos=(0,0,0) rot=(0.57735,0.57735,0.57735;2.0944rad)
  Profile = -> Sketch190
  Type = 0
FEATURE [PartDesign::Pad] Pad075
  BaseFeature = -> Pad074
  Direction = (1,-2e-16,6e-16)
  Length = 15
  Length2 = 10
  Placement = pos=(0,0,0) rot=(0.57735,0.57735,0.57735;2.0944rad)
  Profile = -> Pad074 [Edge20]
  Type = 0
FEATURE [PartDesign::Body] Body175
  Group = -> [Sketch190,Pad074,Pad075]
  Origin = -> Origin225
  Tip = -> Pad075
FEATURE [App::Part] Part049  label="tornillo M5-15-004"
  Group = -> [Body175]
  Origin = -> Origin224
  Placement = pos=(10,141,98) rot=(0,1,0;1.5708rad)
FEATURE [Sketcher::SketchObject] Sketch191
  FullyConstrained = false
  MapMode = 5
  Placement = pos=(0,0,0) rot=(0.57735,0.57735,0.57735;2.0944rad)
  Support = -> [YZ_Plane221]
  sketch-geometry (8):
    g0: LineSegment StartX=2.8963 StartY=-2.75889 StartZ=0 EndX=3.83742 EndY=1.12882 EndZ=0
    g1: LineSegment StartX=3.83742 StartY=1.12882 StartZ=0 EndX=0.941117 EndY=3.88771 EndZ=0
    g2: LineSegment StartX=0.941117 StartY=3.88771 StartZ=0 EndX=-2.8963 EndY=2.75889 EndZ=0
    g3: LineSegment StartX=-2.8963 StartY=2.75889 StartZ=0 EndX=-3.83742 EndY=-1.12882 EndZ=0
    g4: LineSegment StartX=-3.83742 StartY=-1.12882 StartZ=0 EndX=-0.941117 EndY=-3.88771 EndZ=0
    g5: LineSegment StartX=-0.941117 StartY=-3.88771 StartZ=0 EndX=2.8963 EndY=-2.75889 EndZ=0
    g6: Circle CenterX=0 CenterY=0 CenterZ=0 NormalX=0 NormalY=0 NormalZ=1 AngleXU=0 Radius=4
    g7: Circle CenterX=0 CenterY=0 CenterZ=0 NormalX=0 NormalY=0 NormalZ=1 AngleXU=0 Radius=2.5
  constraints (17):
    c: Coincident(g0,g1)
    c: Coincident(g1,g2)
    c: Coincident(g2,g3)
    c: Coincident(g3,g4)
    c: Coincident(g4,g5)
    c: Coincident(g5,g0)
    c: Equal(g0, g1-g5) x5
    c: PointOnObject(g0,g6)
    c: PointOnObject(g1,g6)
    c: PointOnObject(g2,g6)
    c: PointOnObject(g3,g6)
    c: PointOnObject(g4,g6)
    c: PointOnObject(g5,g6)
    c: Coincident(g6,g-1)
    c: Coincident(g7,g6)
    c: Radius(g7) = 2.5
    c: Radius(g6) = 4
FEATURE [PartDesign::Pad] Pad076
  Direction = (1,-2e-16,3e-16)
  Length = 3
  Length2 = 10
  Placement = pos=(0,0,0) rot=(0.57735,0.57735,0.57735;2.0944rad)
  Profile = -> Sketch191
  Type = 0
FEATURE [PartDesign::Pad] Pad077
  BaseFeature = -> Pad076
  Direction = (1,-2e-16,6e-16)
  Length = 15
  Length2 = 10
  Placement = pos=(0,0,0) rot=(0.57735,0.57735,0.57735;2.0944rad)
  Profile = -> Pad076 [Edge20]
  Type = 0
FEATURE [PartDesign::Body] Body176
  Group = -> [Sketch191,Pad076,Pad077]
  Origin = -> Origin227
  Tip = -> Pad077
FEATURE [App::Part] Part050  label="tornillo M5-15-005"
  Group = -> [Body176]
  Origin = -> Origin226
  Placement = pos=(332,267,98) rot=(0,1,0;1.5708rad)
FEATURE [Sketcher::SketchObject] Sketch192
  FullyConstrained = false
  MapMode = 5
  Placement = pos=(0,0,0) rot=(0.57735,0.57735,0.57735;2.0944rad)
  Support = -> [YZ_Plane223]
  sketch-geometry (8):
    g0: LineSegment StartX=2.8963 StartY=-2.75889 StartZ=0 EndX=3.83742 EndY=1.12882 EndZ=0
    g1: LineSegment StartX=3.83742 StartY=1.12882 StartZ=0 EndX=0.941117 EndY=3.88771 EndZ=0
    g2: LineSegment StartX=0.941117 StartY=3.88771 StartZ=0 EndX=-2.8963 EndY=2.75889 EndZ=0
    g3: LineSegment StartX=-2.8963 StartY=2.75889 StartZ=0 EndX=-3.83742 EndY=-1.12882 EndZ=0
    g4: LineSegment StartX=-3.83742 StartY=-1.12882 StartZ=0 EndX=-0.941117 EndY=-3.88771 EndZ=0
    g5: LineSegment StartX=-0.941117 StartY=-3.88771 StartZ=0 EndX=2.8963 EndY=-2.75889 EndZ=0
    g6: Circle CenterX=0 CenterY=0 CenterZ=0 NormalX=0 NormalY=0 NormalZ=1 AngleXU=0 Radius=4
    g7: Circle CenterX=0 CenterY=0 CenterZ=0 NormalX=0 NormalY=0 NormalZ=1 AngleXU=0 Radius=2.5
  constraints (17):
    c: Coincident(g0,g1)
    c: Coincident(g1,g2)
    c: Coincident(g2,g3)
    c: Coincident(g3,g4)
    c: Coincident(g4,g5)
    c: Coincident(g5,g0)
    c: Equal(g0, g1-g5) x5
    c: PointOnObject(g0,g6)
    c: PointOnObject(g1,g6)
    c: PointOnObject(g2,g6)
    c: PointOnObject(g3,g6)
    c: PointOnObject(g4,g6)
    c: PointOnObject(g5,g6)
    c: Coincident(g6,g-1)
    c: Coincident(g7,g6)
    c: Radius(g7) = 2.5
    c: Radius(g6) = 4
FEATURE [PartDesign::Pad] Pad078
  Direction = (1,-2e-16,3e-16)
  Length = 3
  Length2 = 10
  Placement = pos=(0,0,0) rot=(0.57735,0.57735,0.57735;2.0944rad)
  Profile = -> Sketch192
  Type = 0
FEATURE [PartDesign::Pad] Pad079
  BaseFeature = -> Pad078
  Direction = (1,-2e-16,6e-16)
  Length = 15
  Length2 = 10
  Placement = pos=(0,0,0) rot=(0.57735,0.57735,0.57735;2.0944rad)
  Profile = -> Pad078 [Edge20]
  Type = 0
FEATURE [PartDesign::Body] Body177
  Group = -> [Sketch192,Pad078,Pad079]
  Origin = -> Origin229
  Tip = -> Pad079
FEATURE [App::Part] Part051  label="tornillo M5-15-006"
  Group = -> [Body177]
  Origin = -> Origin228
  Placement = pos=(332,225,98) rot=(0,1,0;1.5708rad)
FEATURE [Sketcher::SketchObject] Sketch193
  FullyConstrained = false
  MapMode = 5
  Placement = pos=(0,0,0) rot=(0.57735,0.57735,0.57735;2.0944rad)
  Support = -> [YZ_Plane225]
  sketch-geometry (8):
    g0: LineSegment StartX=2.8963 StartY=-2.75889 StartZ=0 EndX=3.83742 EndY=1.12882 EndZ=0
    g1: LineSegment StartX=3.83742 StartY=1.12882 StartZ=0 EndX=0.941117 EndY=3.88771 EndZ=0
    g2: LineSegment StartX=0.941117 StartY=3.88771 StartZ=0 EndX=-2.8963 EndY=2.75889 EndZ=0
    g3: LineSegment StartX=-2.8963 StartY=2.75889 StartZ=0 EndX=-3.83742 EndY=-1.12882 EndZ=0
    g4: LineSegment StartX=-3.83742 StartY=-1.12882 StartZ=0 EndX=-0.941117 EndY=-3.88771 EndZ=0
    g5: LineSegment StartX=-0.941117 StartY=-3.88771 StartZ=0 EndX=2.8963 EndY=-2.75889 EndZ=0
    g6: Circle CenterX=0 CenterY=0 CenterZ=0 NormalX=0 NormalY=0 NormalZ=1 AngleXU=0 Radius=4
    g7: Circle CenterX=0 CenterY=0 CenterZ=0 NormalX=0 NormalY=0 NormalZ=1 AngleXU=0 Radius=2.5
  constraints (17):
    c: Coincident(g0,g1)
    c: Coincident(g1,g2)
    c: Coincident(g2,g3)
    c: Coincident(g3,g4)
    c: Coincident(g4,g5)
    c: Coincident(g5,g0)
    c: Equal(g0, g1-g5) x5
    c: PointOnObject(g0,g6)
    c: PointOnObject(g1,g6)
    c: PointOnObject(g2,g6)
    c: PointOnObject(g3,g6)
    c: PointOnObject(g4,g6)
    c: PointOnObject(g5,g6)
    c: Coincident(g6,g-1)
    c: Coincident(g7,g6)
    c: Radius(g7) = 2.5
    c: Radius(g6) = 4
FEATURE [PartDesign::Pad] Pad080
  Direction = (1,-2e-16,3e-16)
  Length = 3
  Length2 = 10
  Placement = pos=(0,0,0) rot=(0.57735,0.57735,0.57735;2.0944rad)
  Profile = -> Sketch193
  Type = 0
FEATURE [PartDesign::Pad] Pad081
  BaseFeature = -> Pad080
  Direction = (1,-2e-16,6e-16)
  Length = 15
  Length2 = 10
  Placement = pos=(0,0,0) rot=(0.57735,0.57735,0.57735;2.0944rad)
  Profile = -> Pad080 [Edge20]
  Type = 0
FEATURE [PartDesign::Body] Body178
  Group = -> [Sketch193,Pad080,Pad081]
  Origin = -> Origin231
  Tip = -> Pad081
FEATURE [App::Part] Part052  label="tornillo M5-15-007"
  Group = -> [Body178]
  Origin = -> Origin230
  Placement = pos=(332,99,98) rot=(0,1,0;1.5708rad)
FEATURE [Sketcher::SketchObject] Sketch194
  FullyConstrained = false
  MapMode = 5
  Placement = pos=(0,0,0) rot=(0.57735,0.57735,0.57735;2.0944rad)
  Support = -> [YZ_Plane227]
  sketch-geometry (8):
    g0: LineSegment StartX=2.8963 StartY=-2.75889 StartZ=0 EndX=3.83742 EndY=1.12882 EndZ=0
    g1: LineSegment StartX=3.83742 StartY=1.12882 StartZ=0 EndX=0.941117 EndY=3.88771 EndZ=0
    g2: LineSegment StartX=0.941117 StartY=3.88771 StartZ=0 EndX=-2.8963 EndY=2.75889 EndZ=0
    g3: LineSegment StartX=-2.8963 StartY=2.75889 StartZ=0 EndX=-3.83742 EndY=-1.12882 EndZ=0
    g4: LineSegment StartX=-3.83742 StartY=-1.12882 StartZ=0 EndX=-0.941117 EndY=-3.88771 EndZ=0
    g5: LineSegment StartX=-0.941117 StartY=-3.88771 StartZ=0 EndX=2.8963 EndY=-2.75889 EndZ=0
    g6: Circle CenterX=0 CenterY=0 CenterZ=0 NormalX=0 NormalY=0 NormalZ=1 AngleXU=0 Radius=4
    g7: Circle CenterX=0 CenterY=0 CenterZ=0 NormalX=0 NormalY=0 NormalZ=1 AngleXU=0 Radius=2.5
  constraints (17):
    c: Coincident(g0,g1)
    c: Coincident(g1,g2)
    c: Coincident(g2,g3)
    c: Coincident(g3,g4)
    c: Coincident(g4,g5)
    c: Coincident(g5,g0)
    c: Equal(g0, g1-g5) x5
    c: PointOnObject(g0,g6)
    c: PointOnObject(g1,g6)
    c: PointOnObject(g2,g6)
    c: PointOnObject(g3,g6)
    c: PointOnObject(g4,g6)
    c: PointOnObject(g5,g6)
    c: Coincident(g6,g-1)
    c: Coincident(g7,g6)
    c: Radius(g7) = 2.5
    c: Radius(g6) = 4
FEATURE [PartDesign::Pad] Pad082
  Direction = (1,-2e-16,3e-16)
  Length = 3
  Length2 = 10
  Placement = pos=(0,0,0) rot=(0.57735,0.57735,0.57735;2.0944rad)
  Profile = -> Sketch194
  Type = 0
FEATURE [PartDesign::Pad] Pad083
  BaseFeature = -> Pad082
  Direction = (1,-2e-16,6e-16)
  Length = 15
  Length2 = 10
  Placement = pos=(0,0,0) rot=(0.57735,0.57735,0.57735;2.0944rad)
  Profile = -> Pad082 [Edge20]
  Type = 0
FEATURE [PartDesign::Body] Body179
  Group = -> [Sketch194,Pad082,Pad083]
  Origin = -> Origin233
  Tip = -> Pad083
FEATURE [App::Part] Part053  label="tornillo M5-15-008"
  Group = -> [Body179]
  Origin = -> Origin232
  Placement = pos=(332,141,98) rot=(0,1,0;1.5708rad)
FEATURE [Sketcher::SketchObject] Sketch195
  FullyConstrained = false
  MapMode = 5
  Placement = pos=(0,0,0) rot=(0.57735,0.57735,0.57735;2.0944rad)
  Support = -> [YZ_Plane229]
  sketch-geometry (8):
    g0: LineSegment StartX=2.8963 StartY=-2.75889 StartZ=0 EndX=3.83742 EndY=1.12882 EndZ=0
    g1: LineSegment StartX=3.83742 StartY=1.12882 StartZ=0 EndX=0.941117 EndY=3.88771 EndZ=0
    g2: LineSegment StartX=0.941117 StartY=3.88771 StartZ=0 EndX=-2.8963 EndY=2.75889 EndZ=0
    g3: LineSegment StartX=-2.8963 StartY=2.75889 StartZ=0 EndX=-3.83742 EndY=-1.12882 EndZ=0
    g4: LineSegment StartX=-3.83742 StartY=-1.12882 StartZ=0 EndX=-0.941117 EndY=-3.88771 EndZ=0
    g5: LineSegment StartX=-0.941117 StartY=-3.88771 StartZ=0 EndX=2.8963 EndY=-2.75889 EndZ=0
    g6: Circle CenterX=0 CenterY=0 CenterZ=0 NormalX=0 NormalY=0 NormalZ=1 AngleXU=0 Radius=4
    g7: Circle CenterX=0 CenterY=0 CenterZ=0 NormalX=0 NormalY=0 NormalZ=1 AngleXU=0 Radius=2.5
  constraints (17):
    c: Coincident(g0,g1)
    c: Coincident(g1,g2)
    c: Coincident(g2,g3)
    c: Coincident(g3,g4)
    c: Coincident(g4,g5)
    c: Coincident(g5,g0)
    c: Equal(g0, g1-g5) x5
    c: PointOnObject(g0,g6)
    c: PointOnObject(g1,g6)
    c: PointOnObject(g2,g6)
    c: PointOnObject(g3,g6)
    c: PointOnObject(g4,g6)
    c: PointOnObject(g5,g6)
    c: Coincident(g6,g-1)
    c: Coincident(g7,g6)
    c: Radius(g7) = 2.5
    c: Radius(g6) = 4
FEATURE [PartDesign::Pad] Pad084
  Direction = (1,-2e-16,3e-16)
  Length = 3
  Length2 = 10
  Placement = pos=(0,0,0) rot=(0.57735,0.57735,0.57735;2.0944rad)
  Profile = -> Sketch195
  Type = 0
FEATURE [PartDesign::Pad] Pad085
  BaseFeature = -> Pad084
  Direction = (1,-2e-16,6e-16)
  Length = 15
  Length2 = 10
  Placement = pos=(0,0,0) rot=(0.57735,0.57735,0.57735;2.0944rad)
  Profile = -> Pad084 [Edge20]
  Type = 0
FEATURE [PartDesign::Body] Body180
  Group = -> [Sketch195,Pad084,Pad085]
  Origin = -> Origin235
  Tip = -> Pad085
FEATURE [App::Part] Part054  label="tornillo M5-15-009"
  Group = -> [Body180]
  Origin = -> Origin234
  Placement = pos=(313,101,79) rot=(0,0,1;0rad)
FEATURE [Sketcher::SketchObject] Sketch196
  FullyConstrained = false
  MapMode = 5
  Placement = pos=(0,0,0) rot=(0.57735,0.57735,0.57735;2.0944rad)
  Support = -> [YZ_Plane231]
  sketch-geometry (8):
    g0: LineSegment StartX=2.8963 StartY=-2.75889 StartZ=0 EndX=3.83742 EndY=1.12882 EndZ=0
    g1: LineSegment StartX=3.83742 StartY=1.12882 StartZ=0 EndX=0.941117 EndY=3.88771 EndZ=0
    g2: LineSegment StartX=0.941117 StartY=3.88771 StartZ=0 EndX=-2.8963 EndY=2.75889 EndZ=0
    g3: LineSegment StartX=-2.8963 StartY=2.75889 StartZ=0 EndX=-3.83742 EndY=-1.12882 EndZ=0
    g4: LineSegment StartX=-3.83742 StartY=-1.12882 StartZ=0 EndX=-0.941117 EndY=-3.88771 EndZ=0
    g5: LineSegment StartX=-0.941117 StartY=-3.88771 StartZ=0 EndX=2.8963 EndY=-2.75889 EndZ=0
    g6: Circle CenterX=0 CenterY=0 CenterZ=0 NormalX=0 NormalY=0 NormalZ=1 AngleXU=0 Radius=4
    g7: Circle CenterX=0 CenterY=0 CenterZ=0 NormalX=0 NormalY=0 NormalZ=1 AngleXU=0 Radius=2.5
  constraints (17):
    c: Coincident(g0,g1)
    c: Coincident(g1,g2)
    c: Coincident(g2,g3)
    c: Coincident(g3,g4)
    c: Coincident(g4,g5)
    c: Coincident(g5,g0)
    c: Equal(g0, g1-g5) x5
    c: PointOnObject(g0,g6)
    c: PointOnObject(g1,g6)
    c: PointOnObject(g2,g6)
    c: PointOnObject(g3,g6)
    c: PointOnObject(g4,g6)
    c: PointOnObject(g5,g6)
    c: Coincident(g6,g-1)
    c: Coincident(g7,g6)
    c: Radius(g7) = 2.5
    c: Radius(g6) = 4
FEATURE [PartDesign::Pad] Pad086
  Direction = (1,-2e-16,3e-16)
  Length = 3
  Length2 = 10
  Placement = pos=(0,0,0) rot=(0.57735,0.57735,0.57735;2.0944rad)
  Profile = -> Sketch196
  Type = 0
FEATURE [PartDesign::Pad] Pad087
  BaseFeature = -> Pad086
  Direction = (1,-2e-16,6e-16)
  Length = 15
  Length2 = 10
  Placement = pos=(0,0,0) rot=(0.57735,0.57735,0.57735;2.0944rad)
  Profile = -> Pad086 [Edge20]
  Type = 0
FEATURE [PartDesign::Body] Body181
  Group = -> [Sketch196,Pad086,Pad087]
  Origin = -> Origin237
  Tip = -> Pad087
FEATURE [App::Part] Part055  label="tornillo M5-15-010"
  Group = -> [Body181]
  Origin = -> Origin236
  Placement = pos=(26,101,79) rot=(0,0,1;3.14159rad)
FEATURE [Sketcher::SketchObject] Sketch197
  FullyConstrained = false
  MapMode = 5
  Placement = pos=(0,0,0) rot=(0.57735,0.57735,0.57735;2.0944rad)
  Support = -> [YZ_Plane233]
  sketch-geometry (8):
    g0: LineSegment StartX=2.8963 StartY=-2.75889 StartZ=0 EndX=3.83742 EndY=1.12882 EndZ=0
    g1: LineSegment StartX=3.83742 StartY=1.12882 StartZ=0 EndX=0.941117 EndY=3.88771 EndZ=0
    g2: LineSegment StartX=0.941117 StartY=3.88771 StartZ=0 EndX=-2.8963 EndY=2.75889 EndZ=0
    g3: LineSegment StartX=-2.8963 StartY=2.75889 StartZ=0 EndX=-3.83742 EndY=-1.12882 EndZ=0
    g4: LineSegment StartX=-3.83742 StartY=-1.12882 StartZ=0 EndX=-0.941117 EndY=-3.88771 EndZ=0
    g5: LineSegment StartX=-0.941117 StartY=-3.88771 StartZ=0 EndX=2.8963 EndY=-2.75889 EndZ=0
    g6: Circle CenterX=0 CenterY=0 CenterZ=0 NormalX=0 NormalY=0 NormalZ=1 AngleXU=0 Radius=4
    g7: Circle CenterX=0 CenterY=0 CenterZ=0 NormalX=0 NormalY=0 NormalZ=1 AngleXU=0 Radius=2.5
  constraints (17):
    c: Coincident(g0,g1)
    c: Coincident(g1,g2)
    c: Coincident(g2,g3)
    c: Coincident(g3,g4)
    c: Coincident(g4,g5)
    c: Coincident(g5,g0)
    c: Equal(g0, g1-g5) x5
    c: PointOnObject(g0,g6)
    c: PointOnObject(g1,g6)
    c: PointOnObject(g2,g6)
    c: PointOnObject(g3,g6)
    c: PointOnObject(g4,g6)
    c: PointOnObject(g5,g6)
    c: Coincident(g6,g-1)
    c: Coincident(g7,g6)
    c: Radius(g7) = 2.5
    c: Radius(g6) = 4
FEATURE [PartDesign::Pad] Pad088
  Direction = (1,-2e-16,3e-16)
  Length = 3
  Length2 = 10
  Placement = pos=(0,0,0) rot=(0.57735,0.57735,0.57735;2.0944rad)
  Profile = -> Sketch197
  Type = 0
FEATURE [PartDesign::Pad] Pad089
  BaseFeature = -> Pad088
  Direction = (1,-2e-16,6e-16)
  Length = 15
  Length2 = 10
  Placement = pos=(0,0,0) rot=(0.57735,0.57735,0.57735;2.0944rad)
  Profile = -> Pad088 [Edge20]
  Type = 0
FEATURE [PartDesign::Body] Body182
  Group = -> [Sketch197,Pad088,Pad089]
  Origin = -> Origin239
  Tip = -> Pad089
FEATURE [App::Part] Part056  label="tornillo M5-15-011"
  Group = -> [Body182]
  Origin = -> Origin238
  Placement = pos=(26,139,79) rot=(0,0,1;3.14159rad)
FEATURE [Sketcher::SketchObject] Sketch198
  FullyConstrained = false
  MapMode = 5
  Placement = pos=(0,0,0) rot=(0.57735,0.57735,0.57735;2.0944rad)
  Support = -> [YZ_Plane235]
  sketch-geometry (8):
    g0: LineSegment StartX=2.8963 StartY=-2.75889 StartZ=0 EndX=3.83742 EndY=1.12882 EndZ=0
    g1: LineSegment StartX=3.83742 StartY=1.12882 StartZ=0 EndX=0.941117 EndY=3.88771 EndZ=0
    g2: LineSegment StartX=0.941117 StartY=3.88771 StartZ=0 EndX=-2.8963 EndY=2.75889 EndZ=0
    g3: LineSegment StartX=-2.8963 StartY=2.75889 StartZ=0 EndX=-3.83742 EndY=-1.12882 EndZ=0
    g4: LineSegment StartX=-3.83742 StartY=-1.12882 StartZ=0 EndX=-0.941117 EndY=-3.88771 EndZ=0
    g5: LineSegment StartX=-0.941117 StartY=-3.88771 StartZ=0 EndX=2.8963 EndY=-2.75889 EndZ=0
    g6: Circle CenterX=0 CenterY=0 CenterZ=0 NormalX=0 NormalY=0 NormalZ=1 AngleXU=0 Radius=4
    g7: Circle CenterX=0 CenterY=0 CenterZ=0 NormalX=0 NormalY=0 NormalZ=1 AngleXU=0 Radius=2.5
  constraints (17):
    c: Coincident(g0,g1)
    c: Coincident(g1,g2)
    c: Coincident(g2,g3)
    c: Coincident(g3,g4)
    c: Coincident(g4,g5)
    c: Coincident(g5,g0)
    c: Equal(g0, g1-g5) x5
    c: PointOnObject(g0,g6)
    c: PointOnObject(g1,g6)
    c: PointOnObject(g2,g6)
    c: PointOnObject(g3,g6)
    c: PointOnObject(g4,g6)
    c: PointOnObject(g5,g6)
    c: Coincident(g6,g-1)
    c: Coincident(g7,g6)
    c: Radius(g7) = 2.5
    c: Radius(g6) = 4
FEATURE [PartDesign::Pad] Pad090
  Direction = (1,-2e-16,3e-16)
  Length = 3
  Length2 = 10
  Placement = pos=(0,0,0) rot=(0.57735,0.57735,0.57735;2.0944rad)
  Profile = -> Sketch198
  Type = 0
FEATURE [PartDesign::Pad] Pad091
  BaseFeature = -> Pad090
  Direction = (1,-2e-16,6e-16)
  Length = 15
  Length2 = 10
  Placement = pos=(0,0,0) rot=(0.57735,0.57735,0.57735;2.0944rad)
  Profile = -> Pad090 [Edge20]
  Type = 0
FEATURE [PartDesign::Body] Body183
  Group = -> [Sketch198,Pad090,Pad091]
  Origin = -> Origin241
  Tip = -> Pad091
FEATURE [App::Part] Part057  label="tornillo M5-15-012"
  Group = -> [Body183]
  Origin = -> Origin240
  Placement = pos=(313,139,79) rot=(0,0,1;0rad)
FEATURE [Sketcher::SketchObject] Sketch199
  FullyConstrained = true
  MapMode = 5
  Placement = pos=(0,0,0) rot=(1,0,0;1.5708rad)
  Support = -> [XZ_Plane237]
  sketch-geometry (2):
    g0: Circle CenterX=0 CenterY=0 CenterZ=0 NormalX=0 NormalY=0 NormalZ=1 AngleXU=0 Radius=3
    g1: Circle CenterX=0 CenterY=0 CenterZ=0 NormalX=0 NormalY=0 NormalZ=1 AngleXU=0 Radius=9
  constraints (4):
    c: Coincident(g0,g-1)
    c: Coincident(g1,g0)
    c: Radius(g1) = 9
    c: Diameter(g0) = 6
FEATURE [PartDesign::Pad] Pad092
  Direction = (0,-1,2e-16)
  Length = 1
  Length2 = 10
  Placement = pos=(0,0,0) rot=(1,0,0;1.5708rad)
  Profile = -> Sketch199
  Type = 0
FEATURE [PartDesign::Body] Body184
  Group = -> [Sketch199,Pad092]
  Origin = -> Origin243
  Tip = -> Pad092
FEATURE [App::Part] Part058  label="Arandela M6-001"
  Group = -> [Body184]
  Origin = -> Origin242
  Placement = pos=(10,0,10) rot=(0,0,1;0rad)
FEATURE [Sketcher::SketchObject] Sketch200
  FullyConstrained = true
  MapMode = 5
  Placement = pos=(0,0,0) rot=(1,0,0;1.5708rad)
  Support = -> [XZ_Plane239]
  sketch-geometry (2):
    g0: Circle CenterX=0 CenterY=0 CenterZ=0 NormalX=0 NormalY=0 NormalZ=1 AngleXU=0 Radius=3
    g1: Circle CenterX=0 CenterY=0 CenterZ=0 NormalX=0 NormalY=0 NormalZ=1 AngleXU=0 Radius=9
  constraints (4):
    c: Coincident(g0,g-1)
    c: Coincident(g1,g0)
    c: Radius(g1) = 9
    c: Diameter(g0) = 6
FEATURE [PartDesign::Pad] Pad093
  Direction = (0,-1,2e-16)
  Length = 1
  Length2 = 10
  Placement = pos=(0,0,0) rot=(1,0,0;1.5708rad)
  Profile = -> Sketch200
  Type = 0
FEATURE [PartDesign::Body] Body185
  Group = -> [Sketch200,Pad093]
  Origin = -> Origin245
  Tip = -> Pad093
FEATURE [App::Part] Part059  label="Arandela M6-002"
  Group = -> [Body185]
  Origin = -> Origin244
  Placement = pos=(10,0,181) rot=(0,0,1;0rad)
FEATURE [Sketcher::SketchObject] Sketch201
  FullyConstrained = true
  MapMode = 5
  Placement = pos=(0,0,0) rot=(1,0,0;1.5708rad)
  Support = -> [XZ_Plane241]
  sketch-geometry (2):
    g0: Circle CenterX=0 CenterY=0 CenterZ=0 NormalX=0 NormalY=0 NormalZ=1 AngleXU=0 Radius=3
    g1: Circle CenterX=0 CenterY=0 CenterZ=0 NormalX=0 NormalY=0 NormalZ=1 AngleXU=0 Radius=9
  constraints (4):
    c: Coincident(g0,g-1)
    c: Coincident(g1,g0)
    c: Radius(g1) = 9
    c: Diameter(g0) = 6
FEATURE [PartDesign::Pad] Pad094
  Direction = (0,-1,2e-16)
  Length = 1
  Length2 = 10
  Placement = pos=(0,0,0) rot=(1,0,0;1.5708rad)
  Profile = -> Sketch201
  Type = 0
FEATURE [PartDesign::Body] Body186
  Group = -> [Sketch201,Pad094]
  Origin = -> Origin247
  Tip = -> Pad094
FEATURE [App::Part] Part060  label="Arandela M6-003"
  Group = -> [Body186]
  Origin = -> Origin246
  Placement = pos=(330,0,181) rot=(0,0,1;0rad)
FEATURE [Sketcher::SketchObject] Sketch202
  FullyConstrained = true
  MapMode = 5
  Placement = pos=(0,0,0) rot=(1,0,0;1.5708rad)
  Support = -> [XZ_Plane243]
  sketch-geometry (2):
    g0: Circle CenterX=0 CenterY=0 CenterZ=0 NormalX=0 NormalY=0 NormalZ=1 AngleXU=0 Radius=3
    g1: Circle CenterX=0 CenterY=0 CenterZ=0 NormalX=0 NormalY=0 NormalZ=1 AngleXU=0 Radius=9
  constraints (4):
    c: Coincident(g0,g-1)
    c: Coincident(g1,g0)
    c: Radius(g1) = 9
    c: Diameter(g0) = 6
FEATURE [PartDesign::Pad] Pad095
  Direction = (0,-1,2e-16)
  Length = 1
  Length2 = 10
  Placement = pos=(0,0,0) rot=(1,0,0;1.5708rad)
  Profile = -> Sketch202
  Type = 0
FEATURE [PartDesign::Body] Body187
  Group = -> [Sketch202,Pad095]
  Origin = -> Origin249
  Tip = -> Pad095
FEATURE [App::Part] Part061  label="Arandela M6-004"
  Group = -> [Body187]
  Origin = -> Origin248
  Placement = pos=(330,0,9) rot=(0,0,1;0rad)
FEATURE [Sketcher::SketchObject] Sketch203
  FullyConstrained = true
  MapMode = 5
  Placement = pos=(0,0,0) rot=(1,0,0;1.5708rad)
  Support = -> [XZ_Plane245]
  sketch-geometry (2):
    g0: Circle CenterX=0 CenterY=0 CenterZ=0 NormalX=0 NormalY=0 NormalZ=1 AngleXU=0 Radius=3
    g1: Circle CenterX=0 CenterY=0 CenterZ=0 NormalX=0 NormalY=0 NormalZ=1 AngleXU=0 Radius=9
  constraints (4):
    c: Coincident(g0,g-1)
    c: Coincident(g1,g0)
    c: Radius(g1) = 9
    c: Diameter(g0) = 6
FEATURE [PartDesign::Pad] Pad096
  Direction = (0,-1,2e-16)
  Length = 1
  Length2 = 10
  Placement = pos=(0,0,0) rot=(1,0,0;1.5708rad)
  Profile = -> Sketch203
  Type = 0
FEATURE [PartDesign::Body] Body188
  Group = -> [Sketch203,Pad096]
  Origin = -> Origin251
  Tip = -> Pad096
FEATURE [App::Part] Part062  label="Arandela M6-005"
  Group = -> [Body188]
  Origin = -> Origin250
  Placement = pos=(330,341,9) rot=(0,0,1;0rad)
FEATURE [Sketcher::SketchObject] Sketch204
  FullyConstrained = true
  MapMode = 5
  Placement = pos=(0,0,0) rot=(1,0,0;1.5708rad)
  Support = -> [XZ_Plane247]
  sketch-geometry (2):
    g0: Circle CenterX=0 CenterY=0 CenterZ=0 NormalX=0 NormalY=0 NormalZ=1 AngleXU=0 Radius=3
    g1: Circle CenterX=0 CenterY=0 CenterZ=0 NormalX=0 NormalY=0 NormalZ=1 AngleXU=0 Radius=9
  constraints (4):
    c: Coincident(g0,g-1)
    c: Coincident(g1,g0)
    c: Radius(g1) = 9
    c: Diameter(g0) = 6
FEATURE [PartDesign::Pad] Pad097
  Direction = (0,-1,2e-16)
  Length = 1
  Length2 = 10
  Placement = pos=(0,0,0) rot=(1,0,0;1.5708rad)
  Profile = -> Sketch204
  Type = 0
FEATURE [PartDesign::Body] Body189
  Group = -> [Sketch204,Pad097]
  Origin = -> Origin253
  Tip = -> Pad097
FEATURE [App::Part] Part063  label="Arandela M6-006"
  Group = -> [Body189]
  Origin = -> Origin252
  Placement = pos=(10,341,180) rot=(0,0,1;0rad)
FEATURE [Sketcher::SketchObject] Sketch205
  FullyConstrained = true
  MapMode = 5
  Placement = pos=(0,0,0) rot=(1,0,0;1.5708rad)
  Support = -> [XZ_Plane249]
  sketch-geometry (2):
    g0: Circle CenterX=0 CenterY=0 CenterZ=0 NormalX=0 NormalY=0 NormalZ=1 AngleXU=0 Radius=3
    g1: Circle CenterX=0 CenterY=0 CenterZ=0 NormalX=0 NormalY=0 NormalZ=1 AngleXU=0 Radius=9
  constraints (4):
    c: Coincident(g0,g-1)
    c: Coincident(g1,g0)
    c: Radius(g1) = 9
    c: Diameter(g0) = 6
FEATURE [PartDesign::Pad] Pad098
  Direction = (0,-1,2e-16)
  Length = 1
  Length2 = 10
  Placement = pos=(0,0,0) rot=(1,0,0;1.5708rad)
  Profile = -> Sketch205
  Type = 0
FEATURE [PartDesign::Body] Body190
  Group = -> [Sketch205,Pad098]
  Origin = -> Origin255
  Tip = -> Pad098
FEATURE [App::Part] Part064  label="Arandela M6-007"
  Group = -> [Body190]
  Origin = -> Origin254
  Placement = pos=(330,341,180) rot=(0,0,1;0rad)
FEATURE [Sketcher::SketchObject] Sketch206
  FullyConstrained = true
  MapMode = 5
  Placement = pos=(0,0,0) rot=(1,0,0;1.5708rad)
  Support = -> [XZ_Plane251]
  sketch-geometry (2):
    g0: Circle CenterX=0 CenterY=0 CenterZ=0 NormalX=0 NormalY=0 NormalZ=1 AngleXU=0 Radius=3
    g1: Circle CenterX=0 CenterY=0 CenterZ=0 NormalX=0 NormalY=0 NormalZ=1 AngleXU=0 Radius=9
  constraints (4):
    c: Coincident(g0,g-1)
    c: Coincident(g1,g0)
    c: Radius(g1) = 9
    c: Diameter(g0) = 6
FEATURE [PartDesign::Pad] Pad099
  Direction = (0,-1,2e-16)
  Length = 1
  Length2 = 10
  Placement = pos=(0,0,0) rot=(1,0,0;1.5708rad)
  Profile = -> Sketch206
  Type = 0
FEATURE [PartDesign::Body] Body191
  Group = -> [Sketch206,Pad099]
  Origin = -> Origin257
  Tip = -> Pad099
FEATURE [App::Part] Part065  label="Arandela M6-008"
  Group = -> [Body191]
  Origin = -> Origin256
  Placement = pos=(10,341,10) rot=(0,0,1;0rad)
FEATURE [Sketcher::SketchObject] Sketch207
  FullyConstrained = true
  MapMode = 5
  Placement = pos=(0,0,0) rot=(0.57735,0.57735,0.57735;2.0944rad)
  Support = -> [YZ_Plane253]
  sketch-geometry (4):
    g0: LineSegment StartX=0 StartY=0 StartZ=0 EndX=340 EndY=0 EndZ=0
    g1: LineSegment StartX=340 StartY=0 StartZ=0 EndX=340 EndY=-30 EndZ=0
    g2: LineSegment StartX=340 StartY=-30 StartZ=0 EndX=0 EndY=-30 EndZ=0
    g3: LineSegment StartX=0 StartY=-30 StartZ=0 EndX=0 EndY=0 EndZ=0
  constraints (11):
    c: Coincident(g0,g1)
    c: Coincident(g1,g2)
    c: Coincident(g2,g3)
    c: Coincident(g3,g0)
    c: Horizontal(g0)
    c: Horizontal(g2)
    c: Vertical(g1)
    c: Vertical(g3)
    c: Coincident(g0,g-1)
    c: DistanceY(g2,g0) = 30
    c: DistanceX(g2,g1) = 340
FEATURE [PartDesign::Pad] Pad100
  Direction = (1,-2e-16,3e-16)
  Length = 2
  Length2 = 10
  Placement = pos=(0,0,0) rot=(0.57735,0.57735,0.57735;2.0944rad)
  Profile = -> Sketch207
  Type = 0
FEATURE [PartDesign::Body] Body192
  Group = -> [Sketch207,Pad100]
  Origin = -> Origin259
  Tip = -> Pad100
FEATURE [Sketcher::SketchObject] Sketch208
  FullyConstrained = false
  MapMode = 5
  Support = -> [XY_Plane254]
  sketch-geometry (9):
    g0: LineSegment StartX=-50 StartY=12 StartZ=0 EndX=-50 EndY=328 EndZ=0
    g1: LineSegment StartX=2 StartY=339.974 StartZ=0 EndX=2 EndY=0 EndZ=0
    g2: GeomPoint X=-50 Y=328 Z=0
    g3: LineSegment StartX=-50 StartY=328 StartZ=0 EndX=2 EndY=340 EndZ=0
    g4: GeomPoint X=-50 Y=12 Z=0
    g5: LineSegment StartX=2 StartY=0 StartZ=0 EndX=-50 EndY=12 EndZ=0
    g6: GeomPoint X=2 Y=0 Z=0
    g7: GeomPoint X=2 Y=340 Z=0
    g8: LineSegment StartX=2 StartY=340 StartZ=0 EndX=2 EndY=339.974 EndZ=0
  constraints (18):
    c: Vertical(g0)
    c: Vertical(g1)
    c: PointOnObject(g2,g0)
    c: Coincident(g3,g2)
    c: PointOnObject(g0,g3)
    c: PointOnObject(g4,g0)
    c: Coincident(g5,g4)
    c: PointOnObject(g0,g5)
    c: PointOnObject(g6,g-1)
    c: DistanceX(g-1,g6) = 2
    c: Coincident(g5,g6)
    c: Coincident(g5,g1)
    c: DistanceX(g-1,g7) = 2
    c: DistanceY(g-1,g7) = 340
    c: Coincident(g8,g7)
    c: Coincident(g8,g1)
    c: Vertical(g8)
    c: Coincident(g3,g8)
FEATURE [PartDesign::Pad] Pad101
  Direction = (1,1,1)
  Length = 2
  Length2 = 10
  Profile = -> Sketch208
  Type = 0
FEATURE [PartDesign::Body] Body193
  Group = -> [Sketch208,Pad101]
  Origin = -> Origin260
  Placement = pos=(2,0,0) rot=(0,0,1;0rad)
  Tip = -> Pad101
FEATURE [App::Part] Part066  label="baseMotores"
  Group = -> [Body192,Body193]
  Origin = -> Origin258
  Placement = pos=(342,340,81) rot=(0,0,1;3.14159rad)
FEATURE [Sketcher::SketchObject] Sketch209
  FullyConstrained = false
  MapMode = 5
  Support = -> [XY_Plane256]
  sketch-geometry (8):
    g0: ArcOfCircle CenterX=0 CenterY=0 CenterZ=0 NormalX=0 NormalY=0 NormalZ=1 AngleXU=0 Radius=60 StartAngle=3.30904 EndAngle=6.11574
    g1: LineSegment StartX=-59.1608 StartY=10 StartZ=0 EndX=-48 EndY=10 EndZ=0
    g2: LineSegment StartX=-59.1608 StartY=-10 StartZ=0 EndX=-48 EndY=-10 EndZ=0
    g3: LineSegment StartX=-48 StartY=10 StartZ=0 EndX=-48 EndY=-10 EndZ=0
    g4: LineSegment StartX=48 StartY=10 StartZ=0 EndX=48 EndY=-10 EndZ=0
    g5: ArcOfCircle CenterX=0 CenterY=0 CenterZ=0 NormalX=0 NormalY=0 NormalZ=1 AngleXU=0 Radius=60 StartAngle=0.167448 EndAngle=2.97414
    g6: LineSegment StartX=48 StartY=10 StartZ=0 EndX=59.1608 EndY=10 EndZ=0
    g7: LineSegment StartX=48 StartY=-10 StartZ=0 EndX=59.1608 EndY=-10 EndZ=0
  constraints (16):
    c: Coincident(g0,g-1)
    c: Diameter(g0) = 120
    c: Horizontal(g1)
    c: Horizontal(g2)
    c: Vertical(g3)
    c: Vertical(g4)
    c: Coincident(g1,g5)
    c: Coincident(g2,g0)
    c: Equal(g0,g5)
    c: Coincident(g0,g5)
    c: Coincident(g6,g5)
    c: Coincident(g7,g0)
    c: Coincident(g1,g3)
    c: Coincident(g6,g4)
    c: Coincident(g2,g3)
    c: Coincident(g7,g4)
FEATURE [PartDesign::Pad] Pad102
  Direction = (0,0,1)
  Length = 8
  Length2 = 10
  Profile = -> Sketch209
  Type = 0
FEATURE [PartDesign::Body] Body194
  Group = -> [Sketch209,Pad102]
  Origin = -> Origin262
  Tip = -> Pad102
FEATURE [App::Part] Part067  label="rueda-002"
  Group = -> [Body194]
  Origin = -> Origin261
  Placement = pos=(191,246,105) rot=(0,1,0;1.5708rad)
FEATURE [Sketcher::SketchObject] Sketch211
  FullyConstrained = true
  MapMode = 5
  Support = -> [XY_Plane260]
  sketch-geometry (12):
    g0: ArcOfCircle CenterX=0 CenterY=0 CenterZ=0 NormalX=0 NormalY=0 NormalZ=1 AngleXU=0 Radius=60 StartAngle=1.77951 EndAngle=2.93288
    g1: GeomPoint X=0 Y=60 Z=0
    g2: GeomPoint X=0 Y=-60 Z=0
    g3: GeomPoint X=-60 Y=0 Z=0
    g4: GeomPoint X=60 Y=0 Z=0
    g5: ArcOfCircle CenterX=-60 CenterY=0 CenterZ=0 NormalX=0 NormalY=0 NormalZ=1 AngleXU=0 Radius=12.5 StartAngle=4.81674 EndAngle=7.74963
    g6: ArcOfCircle CenterX=0 CenterY=60 CenterZ=0 NormalX=0 NormalY=0 NormalZ=1 AngleXU=0 Radius=12.5 StartAngle=3.24595 EndAngle=6.17883
    g7: ArcOfCircle CenterX=60 CenterY=0 CenterZ=0 NormalX=0 NormalY=0 NormalZ=1 AngleXU=0 Radius=12.5 StartAngle=1.67515 EndAngle=4.60803
    g8: ArcOfCircle CenterX=0 CenterY=-60 CenterZ=0 NormalX=0 NormalY=0 NormalZ=1 AngleXU=0 Radius=12.5 StartAngle=0.104356 EndAngle=3.03724
    g9: ArcOfCircle CenterX=0 CenterY=0 CenterZ=0 NormalX=0 NormalY=0 NormalZ=1 AngleXU=0 Radius=60 StartAngle=3.3503 EndAngle=4.50368
    g10: ArcOfCircle CenterX=0 CenterY=0 CenterZ=0 NormalX=0 NormalY=0 NormalZ=1 AngleXU=0 Radius=60 StartAngle=4.9211 EndAngle=6.07447
    g11: ArcOfCircle CenterX=0 CenterY=0 CenterZ=0 NormalX=0 NormalY=0 NormalZ=1 AngleXU=0 Radius=60 StartAngle=0.208712 EndAngle=1.36208
  constraints (32):
    c: Coincident(g0,g-1)
    c: PointOnObject(g1,g0)
    c: PointOnObject(g2,g0)
    c: PointOnObject(g3,g0)
    c: PointOnObject(g4,g0)
    c: DistanceY(g-1,g3) = 0
    c: DistanceY(g-1,g4) = 0
    c: DistanceX(g1,g-1) = 0
    c: DistanceX(g2,g-1) = 0
    c: Coincident(g5,g3)
    c: Diameter(g5) = 25
    c: Coincident(g6,g1)
    c: Coincident(g7,g4)
    c: Coincident(g8,g2)
    c: Equal(g7,g6)
    c: Equal(g7,g8)
    c: Diameter(g7) = 25
    c: Coincident(g11,g6)
    c: Coincident(g0,g6)
    c: Equal(g0,g9)
    c: Coincident(g0,g5)
    c: Coincident(g9,g5)
    c: Coincident(g0,g9)
    c: Equal(g9,g10)
    c: Coincident(g9,g10)
    c: Coincident(g8,g9)
    c: Coincident(g8,g10)
    c: Equal(g10,g11)
    c: Coincident(g10,g11)
    c: Coincident(g7,g10)
    c: Coincident(g7,g11)
    c: Diameter(g0) = 120
FEATURE [PartDesign::Pad] Pad104
  Direction = (0,0,1)
  Length = 8
  Length2 = 10
  Profile = -> Sketch211
  Type = 0
FEATURE [PartDesign::Body] Body196
  Group = -> [Sketch211,Pad104]
  Origin = -> Origin266
  Tip = -> Pad104
FEATURE [App::Part] Part069  label="rueda-003"
  Group = -> [Body196]
  Origin = -> Origin265
  Placement = pos=(257,246,105) rot=(0,1,0;1.5708rad)
FEATURE [App::LinkGroup] LinkGroup  label="2020-base"
  ElementList = -> [Part003,Part002,Part001,Part]
  LinkMode = 0
FEATURE [App::LinkGroup] LinkGroup001  label="2020-columnas"
  ElementList = -> [Part004,Part005,Part006,Part007]
  LinkMode = 0
FEATURE [App::LinkGroup] LinkGroup002  label="2020-techo"
  ElementList = -> [Part008,Part009,Part010,Part011]
  LinkMode = 0
FEATURE [App::LinkGroup] LinkGroup003  label="2020-bases de ejes"
  ElementList = -> [Part012,Part013]
  LinkMode = 0
FEATURE [App::LinkGroup] LinkGroup004  label="soportes rulemanes"
  ElementList = -> [Part014,Part015,Part016,Part017,Part018,Part019]
  LinkMode = 0
FEATURE [App::LinkGroup] LinkGroup005  label="Motores"
  ElementList = -> [Part020,Part027]
  LinkMode = 0
FEATURE [App::LinkGroup] LinkGroup006  label="ejes"
  ElementList = -> [Part034,Part035,Part036]
  LinkMode = 0
  Placement = pos=(31,4.57764e-05,0) rot=(0,0,1;0rad)
FEATURE [App::LinkGroup] LinkGroup007  label="tornillos M6 estructura"
  ElementList = -> [Part038,Part039,Part040,Part041,Part042,Part043,Part044,Part045]
  LinkMode = 0
FEATURE [App::LinkGroup] LinkGroup008  label="tornillos M5 rulemanes"
  ElementList = -> [Part046,Part047,Part048,Part049,Part050,Part051,Part052,Part053,Part054,Part055,Part056,Part057]
  LinkMode = 0
FEATURE [App::LinkGroup] LinkGroup009  label="arandelas M6 estructura"
  ElementList = -> [Part046,Part047,Part048,Part049,Part050,Part051,Part052,Part053,Part054,Part055,Part056,Part057,Part058,Part059,Part060,Part061,Part062,Part063,Part064,Part065]
  LinkMode = 0
FEATURE [Sketcher::SketchObject] Sketch212
  FullyConstrained = true
  MapMode = 5
  Placement = pos=(0,0,0) rot=(0.57735,0.57735,0.57735;2.0944rad)
  Support = -> [YZ_Plane261]
  sketch-geometry (5):
    g0: LineSegment StartX=0 StartY=0 StartZ=0 EndX=0 EndY=20 EndZ=0
    g1: LineSegment StartX=0 StartY=20 StartZ=0 EndX=-3 EndY=20 EndZ=0
    g2: LineSegment StartX=-3 StartY=20 StartZ=0 EndX=-20 EndY=3 EndZ=0
    g3: LineSegment StartX=-20 StartY=3 StartZ=0 EndX=-20 EndY=0 EndZ=0
    g4: LineSegment StartX=-20 StartY=0 StartZ=0 EndX=0 EndY=0 EndZ=0
  constraints (14):
    c: Coincident(g-1,g0)
    c: PointOnObject(g0,g-2)
    c: Coincident(g0,g1)
    c: Horizontal(g1)
    c: Coincident(g1,g2)
    c: Coincident(g2,g3)
    c: PointOnObject(g3,g-1)
    c: Vertical(g3)
    c: Coincident(g3,g4)
    c: Coincident(g4,g0)
    c: DistanceY(g0,g0) = 20
    c: DistanceY(g3,g3) = 3
    c: DistanceX(g1,g1) = 3
    c: DistanceX(g4,g4) = 20
FEATURE [PartDesign::Pad] Pad105
  Direction = (1,1,1)
  Length = 17
  Length2 = 100
  Placement = pos=(0,0,0) rot=(0.57735,0.57735,0.57735;2.0944rad)
  Profile = -> Sketch212
  Type = 0
FEATURE [Sketcher::SketchObject] Sketch213
  ExternalGeometry = -> [Pad105]
  FullyConstrained = true
  MapMode = 5
  Placement = pos=(-8.8e-15,-20,4.4e-15) rot=(-0.57735,-0.57735,0.57735;4.18879rad)
  Support = -> [Pad105]
  sketch-geometry (4):
    g0: LineSegment StartX=-3 StartY=2 StartZ=0 EndX=-20 EndY=2 EndZ=0
    g1: LineSegment StartX=-20 StartY=2 StartZ=0 EndX=-20 EndY=15 EndZ=0
    g2: LineSegment StartX=-20 StartY=15 StartZ=0 EndX=-3 EndY=15 EndZ=0
    g3: LineSegment StartX=-3 StartY=15 StartZ=0 EndX=-3 EndY=2 EndZ=0
  constraints (12):
    c: Coincident(g0,g1)
    c: Coincident(g1,g2)
    c: Coincident(g2,g3)
    c: Coincident(g3,g0)
    c: Horizontal(g0)
    c: Horizontal(g2)
    c: Vertical(g1)
    c: Vertical(g3)
    c: PointOnObject(g0,g-3)
    c: DistanceY(g1,g-6) = 2
    c: DistanceY(g-6,g0) = 2
    c: PointOnObject(g1,g-6)
FEATURE [PartDesign::Pocket] Pocket074
  BaseFeature = -> Pad105
  Length = 17
  Length2 = 100
  Placement = pos=(0,0,0) rot=(0.57735,0.57735,0.57735;2.0944rad)
  Profile = -> Sketch213
  Type = 0
FEATURE [Sketcher::SketchObject] Sketch214
  ExternalGeometry = -> [Pocket074]
  FullyConstrained = true
  MapMode = 5
  Placement = pos=(-1.7e-15,-3,6e-16) rot=(-0.57735,-0.57735,0.57735;4.18879rad)
  Support = -> [Pocket074]
  sketch-geometry (5):
    g0: LineSegment StartX=-20 StartY=8.5 StartZ=0 EndX=-3 EndY=8.5 EndZ=0
    g1: ArcOfCircle CenterX=-10 CenterY=8.5 CenterZ=0 NormalX=0 NormalY=0 NormalZ=1 AngleXU=0 Radius=3 StartAngle=4.71239 EndAngle=7.85398
    g2: ArcOfCircle CenterX=-13 CenterY=8.5 CenterZ=0 NormalX=0 NormalY=0 NormalZ=1 AngleXU=0 Radius=3 StartAngle=1.5708 EndAngle=4.71239
    g3: LineSegment StartX=-10 StartY=11.5 StartZ=0 EndX=-13 EndY=11.5 EndZ=0
    g4: LineSegment StartX=-10 StartY=5.5 StartZ=0 EndX=-13 EndY=5.5 EndZ=0
  constraints (14):
    c: PointOnObject(g0,g-6)
    c: PointOnObject(g0,g-4)
    c: Horizontal(g0)
    c: DistanceY(g0,g-4) = 6.5
    c: Tangent(g1,g4) = 1.5708
    c: Tangent(g1,g3) = -1.5708
    c: Tangent(g3,g2) = -1.5708
    c: Tangent(g4,g2) = 1.5708
    c: Horizontal(g3)
    c: Equal(g1,g2)
    c: PointOnObject(g1,g0)
    c: Radius(g1) = 3
    c: DistanceX(g3,g3) = 3
    c: DistanceX(g0,g2) = 7
FEATURE [PartDesign::Pocket] Pocket075
  BaseFeature = -> Pocket074
  Length = 5
  Length2 = 100
  Placement = pos=(0,0,0) rot=(0.57735,0.57735,0.57735;2.0944rad)
  Profile = -> Sketch214
  Type = 2
FEATURE [Sketcher::SketchObject] Sketch215
  ExternalGeometry = -> [Pocket075]
  FullyConstrained = true
  MapMode = 5
  Placement = pos=(-3e-16,1.2e-15,3) rot=(0,0,-1;1.5708rad)
  Support = -> [Pocket075]
  sketch-geometry (5):
    g0: LineSegment StartX=3 StartY=8.5 StartZ=0 EndX=20 EndY=8.5 EndZ=0
    g1: ArcOfCircle CenterX=10 CenterY=8.5 CenterZ=0 NormalX=0 NormalY=0 NormalZ=1 AngleXU=0 Radius=3 StartAngle=1.5708 EndAngle=4.71239
    g2: ArcOfCircle CenterX=13 CenterY=8.5 CenterZ=0 NormalX=0 NormalY=0 NormalZ=1 AngleXU=0 Radius=3 StartAngle=4.71239 EndAngle=7.85398
    g3: LineSegment StartX=10 StartY=5.5 StartZ=0 EndX=13 EndY=5.5 EndZ=0
    g4: LineSegment StartX=10 StartY=11.5 StartZ=0 EndX=13 EndY=11.5 EndZ=0
  constraints (14):
    c: PointOnObject(g0,g-4)
    c: PointOnObject(g0,g-5)
    c: Horizontal(g0)
    c: DistanceY(g0,g-4) = 6.5
    c: Tangent(g1,g4) = 1.5708
    c: Tangent(g1,g3) = -1.5708
    c: Tangent(g3,g2) = -1.5708
    c: Tangent(g4,g2) = 1.5708
    c: Horizontal(g3)
    c: Equal(g1,g2)
    c: PointOnObject(g1,g0)
    c: Radius(g2) = 3
    c: DistanceX(g4,g4) = 3
    c: DistanceX(g2,g0) = 7
FEATURE [PartDesign::Pocket] Pocket076
  BaseFeature = -> Pocket075
  Length = 5
  Length2 = 100
  Placement = pos=(0,0,0) rot=(0.57735,0.57735,0.57735;2.0944rad)
  Profile = -> Sketch215
  Type = 2
FEATURE [Sketcher::SketchObject] Sketch216
  ExternalGeometry = -> [Pocket076]
  FullyConstrained = true
  MapMode = 5
  Placement = pos=(0,0,0) rot=(0.57735,0.57735,0.57735;4.18879rad)
  Support = -> [Pocket076]
  sketch-geometry (9):
    g0: LineSegment StartX=0 StartY=8.5 StartZ=0 EndX=20 EndY=8.5 EndZ=0
    g1: ArcOfCircle CenterX=3 CenterY=9.5 CenterZ=0 NormalX=0 NormalY=0 NormalZ=1 AngleXU=0 Radius=1 StartAngle=0 EndAngle=3.14159
    g2: ArcOfCircle CenterX=3 CenterY=7.5 CenterZ=0 NormalX=0 NormalY=0 NormalZ=1 AngleXU=0 Radius=1 StartAngle=3.14159 EndAngle=6.28319
    g3: LineSegment StartX=2 StartY=9.5 StartZ=0 EndX=2 EndY=7.5 EndZ=0
    g4: LineSegment StartX=4 StartY=9.5 StartZ=0 EndX=4 EndY=7.5 EndZ=0
    g5: ArcOfCircle CenterX=18 CenterY=9.5 CenterZ=0 NormalX=0 NormalY=0 NormalZ=1 AngleXU=0 Radius=1 StartAngle=-9e-16 EndAngle=3.14159
    g6: ArcOfCircle CenterX=18 CenterY=7.5 CenterZ=0 NormalX=0 NormalY=0 NormalZ=1 AngleXU=0 Radius=1 StartAngle=3.14159 EndAngle=6.28319
    g7: LineSegment StartX=17 StartY=9.5 StartZ=0 EndX=17 EndY=7.5 EndZ=0
    g8: LineSegment StartX=19 StartY=9.5 StartZ=0 EndX=19 EndY=7.5 EndZ=0
  constraints (24):
    c: PointOnObject(g0,g-2)
    c: PointOnObject(g0,g-5)
    c: Horizontal(g0)
    c: DistanceY(g0,g-3) = 8.5
    c: Tangent(g1,g4) = 1.5708
    c: Tangent(g1,g3) = -1.5708
    c: Tangent(g3,g2) = -1.5708
    c: Tangent(g4,g2) = 1.5708
    c: Vertical(g3)
    c: Equal(g1,g2)
    c: Tangent(g5,g8) = 1.5708
    c: Tangent(g5,g7) = -1.5708
    c: Tangent(g7,g6) = -1.5708
    c: Tangent(g8,g6) = 1.5708
    c: Vertical(g7)
    c: Equal(g5,g6)
    c: Equal(g1,g5)
    c: Equal(g4,g7)
    c: DistanceY(g4,g4) = 2
    c: Radius(g1) = 1
    c: Horizontal(g5,g1)
    c: DistanceX(g0,g1) = 3
    c: DistanceX(g5,g0) = 2
    c: DistanceY(g0,g1) = 1
FEATURE [PartDesign::Pad] Pad106
  BaseFeature = -> Pocket076
  Direction = (1,1,1)
  Length = 1
  Length2 = 100
  Placement = pos=(0,0,0) rot=(0.57735,0.57735,0.57735;2.0944rad)
  Profile = -> Sketch216
  Type = 0
FEATURE [Sketcher::SketchObject] Sketch217
  ExternalGeometry = -> [Pad106]
  FullyConstrained = true
  MapMode = 5
  Placement = pos=(0,0,1e-16) rot=(0.707107,0.707107,0;3.14159rad)
  Support = -> [Pad106]
  sketch-geometry (9):
    g0: LineSegment StartX=0 StartY=8.5 StartZ=0 EndX=-20 EndY=8.5 EndZ=0
    g1: ArcOfCircle CenterX=-3 CenterY=7.5 CenterZ=0 NormalX=0 NormalY=0 NormalZ=1 AngleXU=0 Radius=1 StartAngle=3.14159 EndAngle=6.28319
    g2: ArcOfCircle CenterX=-3 CenterY=9.5 CenterZ=0 NormalX=0 NormalY=0 NormalZ=1 AngleXU=0 Radius=1 StartAngle=3e-16 EndAngle=3.14159
    g3: LineSegment StartX=-2 StartY=7.5 StartZ=0 EndX=-2 EndY=9.5 EndZ=0
    g4: LineSegment StartX=-4 StartY=7.5 StartZ=0 EndX=-4 EndY=9.5 EndZ=0
    g5: ArcOfCircle CenterX=-18 CenterY=9.5 CenterZ=0 NormalX=0 NormalY=0 NormalZ=1 AngleXU=0 Radius=1 StartAngle=0 EndAngle=3.14159
    g6: ArcOfCircle CenterX=-18 CenterY=7.5 CenterZ=0 NormalX=0 NormalY=0 NormalZ=1 AngleXU=0 Radius=1 StartAngle=3.14159 EndAngle=6.28319
    g7: LineSegment StartX=-19 StartY=9.5 StartZ=0 EndX=-19 EndY=7.5 EndZ=0
    g8: LineSegment StartX=-17 StartY=9.5 StartZ=0 EndX=-17 EndY=7.5 EndZ=0
  constraints (24):
    c: PointOnObject(g0,g-2)
    c: PointOnObject(g0,g-4)
    c: Horizontal(g0)
    c: DistanceY(g0,g-3) = 8.5
    c: Tangent(g1,g4) = 1.5708
    c: Tangent(g1,g3) = -1.5708
    c: Tangent(g3,g2) = -1.5708
    c: Tangent(g4,g2) = 1.5708
    c: Vertical(g3)
    c: Equal(g1,g2)
    c: Radius(g2) = 1
    c: DistanceY(g4,g4) = 2
    c: DistanceY(g0,g2) = 1
    c: DistanceX(g2,g0) = 3
    c: Tangent(g5,g8) = 1.5708
    c: Tangent(g5,g7) = -1.5708
    c: Tangent(g7,g6) = -1.5708
    c: Tangent(g8,g6) = 1.5708
    c: Vertical(g7)
    c: Equal(g5,g6)
    c: Equal(g5,g2)
    c: Equal(g8,g4)
    c: Horizontal(g5,g2)
    c: DistanceX(g0,g5) = 2
FEATURE [PartDesign::Pad] Pad107
  BaseFeature = -> Pad106
  Direction = (1,1,1)
  Length = 1
  Length2 = 100
  Placement = pos=(0,0,0) rot=(0.57735,0.57735,0.57735;2.0944rad)
  Profile = -> Sketch217
  Type = 0
FEATURE [PartDesign::Body] Body197  label="Corner"
  Group = -> [Sketch212,Pad105,Sketch213,Pocket074,Sketch214,Pocket075,Sketch215,Pocket076,Sketch216,Pad106,Sketch217,Pad107]
  Origin = -> Origin267
  Tip = -> Pad107
FEATURE [App::Part] Part070  label="soporte90-001"
  Group = -> [Body197]
  Origin = -> Origin268
  Placement = pos=(20,18,170) rot=(0.707107,-0.707107,0;3.14159rad)
FEATURE [Sketcher::SketchObject] Sketch218
  FullyConstrained = true
  MapMode = 5
  Placement = pos=(0,0,0) rot=(0.57735,0.57735,0.57735;2.0944rad)
  Support = -> [YZ_Plane263]
  sketch-geometry (5):
    g0: LineSegment StartX=0 StartY=0 StartZ=0 EndX=0 EndY=20 EndZ=0
    g1: LineSegment StartX=0 StartY=20 StartZ=0 EndX=-3 EndY=20 EndZ=0
    g2: LineSegment StartX=-3 StartY=20 StartZ=0 EndX=-20 EndY=3 EndZ=0
    g3: LineSegment StartX=-20 StartY=3 StartZ=0 EndX=-20 EndY=0 EndZ=0
    g4: LineSegment StartX=-20 StartY=0 StartZ=0 EndX=0 EndY=0 EndZ=0
  constraints (14):
    c: Coincident(g-1,g0)
    c: PointOnObject(g0,g-2)
    c: Coincident(g0,g1)
    c: Horizontal(g1)
    c: Coincident(g1,g2)
    c: Coincident(g2,g3)
    c: PointOnObject(g3,g-1)
    c: Vertical(g3)
    c: Coincident(g3,g4)
    c: Coincident(g4,g0)
    c: DistanceY(g0,g0) = 20
    c: DistanceY(g3,g3) = 3
    c: DistanceX(g1,g1) = 3
    c: DistanceX(g4,g4) = 20
FEATURE [PartDesign::Pad] Pad108
  Direction = (1,1,1)
  Length = 17
  Length2 = 100
  Placement = pos=(0,0,0) rot=(0.57735,0.57735,0.57735;2.0944rad)
  Profile = -> Sketch218
  Type = 0
FEATURE [Sketcher::SketchObject] Sketch219
  ExternalGeometry = -> [Pad108]
  FullyConstrained = true
  MapMode = 5
  Placement = pos=(-8.8e-15,-20,4.4e-15) rot=(-0.57735,-0.57735,0.57735;4.18879rad)
  Support = -> [Pad108]
  sketch-geometry (4):
    g0: LineSegment StartX=-3 StartY=2 StartZ=0 EndX=-20 EndY=2 EndZ=0
    g1: LineSegment StartX=-20 StartY=2 StartZ=0 EndX=-20 EndY=15 EndZ=0
    g2: LineSegment StartX=-20 StartY=15 StartZ=0 EndX=-3 EndY=15 EndZ=0
    g3: LineSegment StartX=-3 StartY=15 StartZ=0 EndX=-3 EndY=2 EndZ=0
  constraints (12):
    c: Coincident(g0,g1)
    c: Coincident(g1,g2)
    c: Coincident(g2,g3)
    c: Coincident(g3,g0)
    c: Horizontal(g0)
    c: Horizontal(g2)
    c: Vertical(g1)
    c: Vertical(g3)
    c: PointOnObject(g0,g-3)
    c: DistanceY(g1,g-6) = 2
    c: DistanceY(g-6,g0) = 2
    c: PointOnObject(g1,g-6)
FEATURE [PartDesign::Pocket] Pocket077
  BaseFeature = -> Pad108
  Length = 17
  Length2 = 100
  Placement = pos=(0,0,0) rot=(0.57735,0.57735,0.57735;2.0944rad)
  Profile = -> Sketch219
  Type = 0
FEATURE [Sketcher::SketchObject] Sketch220
  ExternalGeometry = -> [Pocket077]
  FullyConstrained = true
  MapMode = 5
  Placement = pos=(-1.7e-15,-3,6e-16) rot=(-0.57735,-0.57735,0.57735;4.18879rad)
  Support = -> [Pocket077]
  sketch-geometry (5):
    g0: LineSegment StartX=-20 StartY=8.5 StartZ=0 EndX=-3 EndY=8.5 EndZ=0
    g1: ArcOfCircle CenterX=-10 CenterY=8.5 CenterZ=0 NormalX=0 NormalY=0 NormalZ=1 AngleXU=0 Radius=3 StartAngle=4.71239 EndAngle=7.85398
    g2: ArcOfCircle CenterX=-13 CenterY=8.5 CenterZ=0 NormalX=0 NormalY=0 NormalZ=1 AngleXU=0 Radius=3 StartAngle=1.5708 EndAngle=4.71239
    g3: LineSegment StartX=-10 StartY=11.5 StartZ=0 EndX=-13 EndY=11.5 EndZ=0
    g4: LineSegment StartX=-10 StartY=5.5 StartZ=0 EndX=-13 EndY=5.5 EndZ=0
  constraints (14):
    c: PointOnObject(g0,g-6)
    c: PointOnObject(g0,g-4)
    c: Horizontal(g0)
    c: DistanceY(g0,g-4) = 6.5
    c: Tangent(g1,g4) = 1.5708
    c: Tangent(g1,g3) = -1.5708
    c: Tangent(g3,g2) = -1.5708
    c: Tangent(g4,g2) = 1.5708
    c: Horizontal(g3)
    c: Equal(g1,g2)
    c: PointOnObject(g1,g0)
    c: Radius(g1) = 3
    c: DistanceX(g3,g3) = 3
    c: DistanceX(g0,g2) = 7
FEATURE [PartDesign::Pocket] Pocket078
  BaseFeature = -> Pocket077
  Length = 5
  Length2 = 100
  Placement = pos=(0,0,0) rot=(0.57735,0.57735,0.57735;2.0944rad)
  Profile = -> Sketch220
  Type = 2
FEATURE [Sketcher::SketchObject] Sketch221
  ExternalGeometry = -> [Pocket078]
  FullyConstrained = true
  MapMode = 5
  Placement = pos=(-3e-16,1.2e-15,3) rot=(0,0,-1;1.5708rad)
  Support = -> [Pocket078]
  sketch-geometry (5):
    g0: LineSegment StartX=3 StartY=8.5 StartZ=0 EndX=20 EndY=8.5 EndZ=0
    g1: ArcOfCircle CenterX=10 CenterY=8.5 CenterZ=0 NormalX=0 NormalY=0 NormalZ=1 AngleXU=0 Radius=3 StartAngle=1.5708 EndAngle=4.71239
    g2: ArcOfCircle CenterX=13 CenterY=8.5 CenterZ=0 NormalX=0 NormalY=0 NormalZ=1 AngleXU=0 Radius=3 StartAngle=4.71239 EndAngle=7.85398
    g3: LineSegment StartX=10 StartY=5.5 StartZ=0 EndX=13 EndY=5.5 EndZ=0
    g4: LineSegment StartX=10 StartY=11.5 StartZ=0 EndX=13 EndY=11.5 EndZ=0
  constraints (14):
    c: PointOnObject(g0,g-4)
    c: PointOnObject(g0,g-5)
    c: Horizontal(g0)
    c: DistanceY(g0,g-4) = 6.5
    c: Tangent(g1,g4) = 1.5708
    c: Tangent(g1,g3) = -1.5708
    c: Tangent(g3,g2) = -1.5708
    c: Tangent(g4,g2) = 1.5708
    c: Horizontal(g3)
    c: Equal(g1,g2)
    c: PointOnObject(g1,g0)
    c: Radius(g2) = 3
    c: DistanceX(g4,g4) = 3
    c: DistanceX(g2,g0) = 7
FEATURE [PartDesign::Pocket] Pocket079
  BaseFeature = -> Pocket078
  Length = 5
  Length2 = 100
  Placement = pos=(0,0,0) rot=(0.57735,0.57735,0.57735;2.0944rad)
  Profile = -> Sketch221
  Type = 2
FEATURE [Sketcher::SketchObject] Sketch222
  ExternalGeometry = -> [Pocket079]
  FullyConstrained = true
  MapMode = 5
  Placement = pos=(0,0,0) rot=(0.57735,0.57735,0.57735;4.18879rad)
  Support = -> [Pocket079]
  sketch-geometry (9):
    g0: LineSegment StartX=0 StartY=8.5 StartZ=0 EndX=20 EndY=8.5 EndZ=0
    g1: ArcOfCircle CenterX=3 CenterY=9.5 CenterZ=0 NormalX=0 NormalY=0 NormalZ=1 AngleXU=0 Radius=1 StartAngle=0 EndAngle=3.14159
    g2: ArcOfCircle CenterX=3 CenterY=7.5 CenterZ=0 NormalX=0 NormalY=0 NormalZ=1 AngleXU=0 Radius=1 StartAngle=3.14159 EndAngle=6.28319
    g3: LineSegment StartX=2 StartY=9.5 StartZ=0 EndX=2 EndY=7.5 EndZ=0
    g4: LineSegment StartX=4 StartY=9.5 StartZ=0 EndX=4 EndY=7.5 EndZ=0
    g5: ArcOfCircle CenterX=18 CenterY=9.5 CenterZ=0 NormalX=0 NormalY=0 NormalZ=1 AngleXU=0 Radius=1 StartAngle=-9e-16 EndAngle=3.14159
    g6: ArcOfCircle CenterX=18 CenterY=7.5 CenterZ=0 NormalX=0 NormalY=0 NormalZ=1 AngleXU=0 Radius=1 StartAngle=3.14159 EndAngle=6.28319
    g7: LineSegment StartX=17 StartY=9.5 StartZ=0 EndX=17 EndY=7.5 EndZ=0
    g8: LineSegment StartX=19 StartY=9.5 StartZ=0 EndX=19 EndY=7.5 EndZ=0
  constraints (24):
    c: PointOnObject(g0,g-2)
    c: PointOnObject(g0,g-5)
    c: Horizontal(g0)
    c: DistanceY(g0,g-3) = 8.5
    c: Tangent(g1,g4) = 1.5708
    c: Tangent(g1,g3) = -1.5708
    c: Tangent(g3,g2) = -1.5708
    c: Tangent(g4,g2) = 1.5708
    c: Vertical(g3)
    c: Equal(g1,g2)
    c: Tangent(g5,g8) = 1.5708
    c: Tangent(g5,g7) = -1.5708
    c: Tangent(g7,g6) = -1.5708
    c: Tangent(g8,g6) = 1.5708
    c: Vertical(g7)
    c: Equal(g5,g6)
    c: Equal(g1,g5)
    c: Equal(g4,g7)
    c: DistanceY(g4,g4) = 2
    c: Radius(g1) = 1
    c: Horizontal(g5,g1)
    c: DistanceX(g0,g1) = 3
    c: DistanceX(g5,g0) = 2
    c: DistanceY(g0,g1) = 1
FEATURE [PartDesign::Pad] Pad109
  BaseFeature = -> Pocket079
  Direction = (1,1,1)
  Length = 1
  Length2 = 100
  Placement = pos=(0,0,0) rot=(0.57735,0.57735,0.57735;2.0944rad)
  Profile = -> Sketch222
  Type = 0
FEATURE [Sketcher::SketchObject] Sketch223
  ExternalGeometry = -> [Pad109]
  FullyConstrained = true
  MapMode = 5
  Placement = pos=(0,0,1e-16) rot=(0.707107,0.707107,0;3.14159rad)
  Support = -> [Pad109]
  sketch-geometry (9):
    g0: LineSegment StartX=0 StartY=8.5 StartZ=0 EndX=-20 EndY=8.5 EndZ=0
    g1: ArcOfCircle CenterX=-3 CenterY=7.5 CenterZ=0 NormalX=0 NormalY=0 NormalZ=1 AngleXU=0 Radius=1 StartAngle=3.14159 EndAngle=6.28319
    g2: ArcOfCircle CenterX=-3 CenterY=9.5 CenterZ=0 NormalX=0 NormalY=0 NormalZ=1 AngleXU=0 Radius=1 StartAngle=3e-16 EndAngle=3.14159
    g3: LineSegment StartX=-2 StartY=7.5 StartZ=0 EndX=-2 EndY=9.5 EndZ=0
    g4: LineSegment StartX=-4 StartY=7.5 StartZ=0 EndX=-4 EndY=9.5 EndZ=0
    g5: ArcOfCircle CenterX=-18 CenterY=9.5 CenterZ=0 NormalX=0 NormalY=0 NormalZ=1 AngleXU=0 Radius=1 StartAngle=0 EndAngle=3.14159
    g6: ArcOfCircle CenterX=-18 CenterY=7.5 CenterZ=0 NormalX=0 NormalY=0 NormalZ=1 AngleXU=0 Radius=1 StartAngle=3.14159 EndAngle=6.28319
    g7: LineSegment StartX=-19 StartY=9.5 StartZ=0 EndX=-19 EndY=7.5 EndZ=0
    g8: LineSegment StartX=-17 StartY=9.5 StartZ=0 EndX=-17 EndY=7.5 EndZ=0
  constraints (24):
    c: PointOnObject(g0,g-2)
    c: PointOnObject(g0,g-4)
    c: Horizontal(g0)
    c: DistanceY(g0,g-3) = 8.5
    c: Tangent(g1,g4) = 1.5708
    c: Tangent(g1,g3) = -1.5708
    c: Tangent(g3,g2) = -1.5708
    c: Tangent(g4,g2) = 1.5708
    c: Vertical(g3)
    c: Equal(g1,g2)
    c: Radius(g2) = 1
    c: DistanceY(g4,g4) = 2
    c: DistanceY(g0,g2) = 1
    c: DistanceX(g2,g0) = 3
    c: Tangent(g5,g8) = 1.5708
    c: Tangent(g5,g7) = -1.5708
    c: Tangent(g7,g6) = -1.5708
    c: Tangent(g8,g6) = 1.5708
    c: Vertical(g7)
    c: Equal(g5,g6)
    c: Equal(g5,g2)
    c: Equal(g8,g4)
    c: Horizontal(g5,g2)
    c: DistanceX(g0,g5) = 2
FEATURE [PartDesign::Pad] Pad110
  BaseFeature = -> Pad109
  Direction = (1,1,1)
  Length = 1
  Length2 = 100
  Placement = pos=(0,0,0) rot=(0.57735,0.57735,0.57735;2.0944rad)
  Profile = -> Sketch223
  Type = 0
FEATURE [PartDesign::Body] Body198  label="Corner001"
  Group = -> [Sketch218,Pad108,Sketch219,Pocket077,Sketch220,Pocket078,Sketch221,Pocket079,Sketch222,Pad109,Sketch223,Pad110]
  Origin = -> Origin269
  Tip = -> Pad110
FEATURE [App::Part] Part071  label="soporte90-002"
  Group = -> [Body198]
  Origin = -> Origin270
  Placement = pos=(20,321,20) rot=(0,0,1;1.5708rad)
FEATURE [Sketcher::SketchObject] Sketch224
  FullyConstrained = true
  MapMode = 5
  Placement = pos=(0,0,0) rot=(0.57735,0.57735,0.57735;2.0944rad)
  Support = -> [YZ_Plane265]
  sketch-geometry (5):
    g0: LineSegment StartX=0 StartY=0 StartZ=0 EndX=0 EndY=20 EndZ=0
    g1: LineSegment StartX=0 StartY=20 StartZ=0 EndX=-3 EndY=20 EndZ=0
    g2: LineSegment StartX=-3 StartY=20 StartZ=0 EndX=-20 EndY=3 EndZ=0
    g3: LineSegment StartX=-20 StartY=3 StartZ=0 EndX=-20 EndY=0 EndZ=0
    g4: LineSegment StartX=-20 StartY=0 StartZ=0 EndX=0 EndY=0 EndZ=0
  constraints (14):
    c: Coincident(g-1,g0)
    c: PointOnObject(g0,g-2)
    c: Coincident(g0,g1)
    c: Horizontal(g1)
    c: Coincident(g1,g2)
    c: Coincident(g2,g3)
    c: PointOnObject(g3,g-1)
    c: Vertical(g3)
    c: Coincident(g3,g4)
    c: Coincident(g4,g0)
    c: DistanceY(g0,g0) = 20
    c: DistanceY(g3,g3) = 3
    c: DistanceX(g1,g1) = 3
    c: DistanceX(g4,g4) = 20
FEATURE [PartDesign::Pad] Pad111
  Direction = (1,1,1)
  Length = 17
  Length2 = 100
  Placement = pos=(0,0,0) rot=(0.57735,0.57735,0.57735;2.0944rad)
  Profile = -> Sketch224
  Type = 0
FEATURE [Sketcher::SketchObject] Sketch225
  ExternalGeometry = -> [Pad111]
  FullyConstrained = true
  MapMode = 5
  Placement = pos=(-8.8e-15,-20,4.4e-15) rot=(-0.57735,-0.57735,0.57735;4.18879rad)
  Support = -> [Pad111]
  sketch-geometry (4):
    g0: LineSegment StartX=-3 StartY=2 StartZ=0 EndX=-20 EndY=2 EndZ=0
    g1: LineSegment StartX=-20 StartY=2 StartZ=0 EndX=-20 EndY=15 EndZ=0
    g2: LineSegment StartX=-20 StartY=15 StartZ=0 EndX=-3 EndY=15 EndZ=0
    g3: LineSegment StartX=-3 StartY=15 StartZ=0 EndX=-3 EndY=2 EndZ=0
  constraints (12):
    c: Coincident(g0,g1)
    c: Coincident(g1,g2)
    c: Coincident(g2,g3)
    c: Coincident(g3,g0)
    c: Horizontal(g0)
    c: Horizontal(g2)
    c: Vertical(g1)
    c: Vertical(g3)
    c: PointOnObject(g0,g-3)
    c: DistanceY(g1,g-6) = 2
    c: DistanceY(g-6,g0) = 2
    c: PointOnObject(g1,g-6)
FEATURE [PartDesign::Pocket] Pocket080
  BaseFeature = -> Pad111
  Length = 17
  Length2 = 100
  Placement = pos=(0,0,0) rot=(0.57735,0.57735,0.57735;2.0944rad)
  Profile = -> Sketch225
  Type = 0
FEATURE [Sketcher::SketchObject] Sketch226
  ExternalGeometry = -> [Pocket080]
  FullyConstrained = true
  MapMode = 5
  Placement = pos=(-1.7e-15,-3,6e-16) rot=(-0.57735,-0.57735,0.57735;4.18879rad)
  Support = -> [Pocket080]
  sketch-geometry (5):
    g0: LineSegment StartX=-20 StartY=8.5 StartZ=0 EndX=-3 EndY=8.5 EndZ=0
    g1: ArcOfCircle CenterX=-10 CenterY=8.5 CenterZ=0 NormalX=0 NormalY=0 NormalZ=1 AngleXU=0 Radius=3 StartAngle=4.71239 EndAngle=7.85398
    g2: ArcOfCircle CenterX=-13 CenterY=8.5 CenterZ=0 NormalX=0 NormalY=0 NormalZ=1 AngleXU=0 Radius=3 StartAngle=1.5708 EndAngle=4.71239
    g3: LineSegment StartX=-10 StartY=11.5 StartZ=0 EndX=-13 EndY=11.5 EndZ=0
    g4: LineSegment StartX=-10 StartY=5.5 StartZ=0 EndX=-13 EndY=5.5 EndZ=0
  constraints (14):
    c: PointOnObject(g0,g-6)
    c: PointOnObject(g0,g-4)
    c: Horizontal(g0)
    c: DistanceY(g0,g-4) = 6.5
    c: Tangent(g1,g4) = 1.5708
    c: Tangent(g1,g3) = -1.5708
    c: Tangent(g3,g2) = -1.5708
    c: Tangent(g4,g2) = 1.5708
    c: Horizontal(g3)
    c: Equal(g1,g2)
    c: PointOnObject(g1,g0)
    c: Radius(g1) = 3
    c: DistanceX(g3,g3) = 3
    c: DistanceX(g0,g2) = 7
FEATURE [PartDesign::Pocket] Pocket081
  BaseFeature = -> Pocket080
  Length = 5
  Length2 = 100
  Placement = pos=(0,0,0) rot=(0.57735,0.57735,0.57735;2.0944rad)
  Profile = -> Sketch226
  Type = 2
FEATURE [Sketcher::SketchObject] Sketch227
  ExternalGeometry = -> [Pocket081]
  FullyConstrained = true
  MapMode = 5
  Placement = pos=(-3e-16,1.2e-15,3) rot=(0,0,-1;1.5708rad)
  Support = -> [Pocket081]
  sketch-geometry (5):
    g0: LineSegment StartX=3 StartY=8.5 StartZ=0 EndX=20 EndY=8.5 EndZ=0
    g1: ArcOfCircle CenterX=10 CenterY=8.5 CenterZ=0 NormalX=0 NormalY=0 NormalZ=1 AngleXU=0 Radius=3 StartAngle=1.5708 EndAngle=4.71239
    g2: ArcOfCircle CenterX=13 CenterY=8.5 CenterZ=0 NormalX=0 NormalY=0 NormalZ=1 AngleXU=0 Radius=3 StartAngle=4.71239 EndAngle=7.85398
    g3: LineSegment StartX=10 StartY=5.5 StartZ=0 EndX=13 EndY=5.5 EndZ=0
    g4: LineSegment StartX=10 StartY=11.5 StartZ=0 EndX=13 EndY=11.5 EndZ=0
  constraints (14):
    c: PointOnObject(g0,g-4)
    c: PointOnObject(g0,g-5)
    c: Horizontal(g0)
    c: DistanceY(g0,g-4) = 6.5
    c: Tangent(g1,g4) = 1.5708
    c: Tangent(g1,g3) = -1.5708
    c: Tangent(g3,g2) = -1.5708
    c: Tangent(g4,g2) = 1.5708
    c: Horizontal(g3)
    c: Equal(g1,g2)
    c: PointOnObject(g1,g0)
    c: Radius(g2) = 3
    c: DistanceX(g4,g4) = 3
    c: DistanceX(g2,g0) = 7
FEATURE [PartDesign::Pocket] Pocket082
  BaseFeature = -> Pocket081
  Length = 5
  Length2 = 100
  Placement = pos=(0,0,0) rot=(0.57735,0.57735,0.57735;2.0944rad)
  Profile = -> Sketch227
  Type = 2
FEATURE [Sketcher::SketchObject] Sketch228
  ExternalGeometry = -> [Pocket082]
  FullyConstrained = true
  MapMode = 5
  Placement = pos=(0,0,0) rot=(0.57735,0.57735,0.57735;4.18879rad)
  Support = -> [Pocket082]
  sketch-geometry (9):
    g0: LineSegment StartX=0 StartY=8.5 StartZ=0 EndX=20 EndY=8.5 EndZ=0
    g1: ArcOfCircle CenterX=3 CenterY=9.5 CenterZ=0 NormalX=0 NormalY=0 NormalZ=1 AngleXU=0 Radius=1 StartAngle=0 EndAngle=3.14159
    g2: ArcOfCircle CenterX=3 CenterY=7.5 CenterZ=0 NormalX=0 NormalY=0 NormalZ=1 AngleXU=0 Radius=1 StartAngle=3.14159 EndAngle=6.28319
    g3: LineSegment StartX=2 StartY=9.5 StartZ=0 EndX=2 EndY=7.5 EndZ=0
    g4: LineSegment StartX=4 StartY=9.5 StartZ=0 EndX=4 EndY=7.5 EndZ=0
    g5: ArcOfCircle CenterX=18 CenterY=9.5 CenterZ=0 NormalX=0 NormalY=0 NormalZ=1 AngleXU=0 Radius=1 StartAngle=-9e-16 EndAngle=3.14159
    g6: ArcOfCircle CenterX=18 CenterY=7.5 CenterZ=0 NormalX=0 NormalY=0 NormalZ=1 AngleXU=0 Radius=1 StartAngle=3.14159 EndAngle=6.28319
    g7: LineSegment StartX=17 StartY=9.5 StartZ=0 EndX=17 EndY=7.5 EndZ=0
    g8: LineSegment StartX=19 StartY=9.5 StartZ=0 EndX=19 EndY=7.5 EndZ=0
  constraints (24):
    c: PointOnObject(g0,g-2)
    c: PointOnObject(g0,g-5)
    c: Horizontal(g0)
    c: DistanceY(g0,g-3) = 8.5
    c: Tangent(g1,g4) = 1.5708
    c: Tangent(g1,g3) = -1.5708
    c: Tangent(g3,g2) = -1.5708
    c: Tangent(g4,g2) = 1.5708
    c: Vertical(g3)
    c: Equal(g1,g2)
    c: Tangent(g5,g8) = 1.5708
    c: Tangent(g5,g7) = -1.5708
    c: Tangent(g7,g6) = -1.5708
    c: Tangent(g8,g6) = 1.5708
    c: Vertical(g7)
    c: Equal(g5,g6)
    c: Equal(g1,g5)
    c: Equal(g4,g7)
    c: DistanceY(g4,g4) = 2
    c: Radius(g1) = 1
    c: Horizontal(g5,g1)
    c: DistanceX(g0,g1) = 3
    c: DistanceX(g5,g0) = 2
    c: DistanceY(g0,g1) = 1
FEATURE [PartDesign::Pad] Pad112
  BaseFeature = -> Pocket082
  Direction = (1,1,1)
  Length = 1
  Length2 = 100
  Placement = pos=(0,0,0) rot=(0.57735,0.57735,0.57735;2.0944rad)
  Profile = -> Sketch228
  Type = 0
FEATURE [Sketcher::SketchObject] Sketch229
  ExternalGeometry = -> [Pad112]
  FullyConstrained = true
  MapMode = 5
  Placement = pos=(0,0,1e-16) rot=(0.707107,0.707107,0;3.14159rad)
  Support = -> [Pad112]
  sketch-geometry (9):
    g0: LineSegment StartX=0 StartY=8.5 StartZ=0 EndX=-20 EndY=8.5 EndZ=0
    g1: ArcOfCircle CenterX=-3 CenterY=7.5 CenterZ=0 NormalX=0 NormalY=0 NormalZ=1 AngleXU=0 Radius=1 StartAngle=3.14159 EndAngle=6.28319
    g2: ArcOfCircle CenterX=-3 CenterY=9.5 CenterZ=0 NormalX=0 NormalY=0 NormalZ=1 AngleXU=0 Radius=1 StartAngle=3e-16 EndAngle=3.14159
    g3: LineSegment StartX=-2 StartY=7.5 StartZ=0 EndX=-2 EndY=9.5 EndZ=0
    g4: LineSegment StartX=-4 StartY=7.5 StartZ=0 EndX=-4 EndY=9.5 EndZ=0
    g5: ArcOfCircle CenterX=-18 CenterY=9.5 CenterZ=0 NormalX=0 NormalY=0 NormalZ=1 AngleXU=0 Radius=1 StartAngle=0 EndAngle=3.14159
    g6: ArcOfCircle CenterX=-18 CenterY=7.5 CenterZ=0 NormalX=0 NormalY=0 NormalZ=1 AngleXU=0 Radius=1 StartAngle=3.14159 EndAngle=6.28319
    g7: LineSegment StartX=-19 StartY=9.5 StartZ=0 EndX=-19 EndY=7.5 EndZ=0
    g8: LineSegment StartX=-17 StartY=9.5 StartZ=0 EndX=-17 EndY=7.5 EndZ=0
  constraints (24):
    c: PointOnObject(g0,g-2)
    c: PointOnObject(g0,g-4)
    c: Horizontal(g0)
    c: DistanceY(g0,g-3) = 8.5
    c: Tangent(g1,g4) = 1.5708
    c: Tangent(g1,g3) = -1.5708
    c: Tangent(g3,g2) = -1.5708
    c: Tangent(g4,g2) = 1.5708
    c: Vertical(g3)
    c: Equal(g1,g2)
    c: Radius(g2) = 1
    c: DistanceY(g4,g4) = 2
    c: DistanceY(g0,g2) = 1
    c: DistanceX(g2,g0) = 3
    c: Tangent(g5,g8) = 1.5708
    c: Tangent(g5,g7) = -1.5708
    c: Tangent(g7,g6) = -1.5708
    c: Tangent(g8,g6) = 1.5708
    c: Vertical(g7)
    c: Equal(g5,g6)
    c: Equal(g5,g2)
    c: Equal(g8,g4)
    c: Horizontal(g5,g2)
    c: DistanceX(g0,g5) = 2
FEATURE [PartDesign::Pad] Pad113
  BaseFeature = -> Pad112
  Direction = (1,1,1)
  Length = 1
  Length2 = 100
  Placement = pos=(0,0,0) rot=(0.57735,0.57735,0.57735;2.0944rad)
  Profile = -> Sketch229
  Type = 0
FEATURE [PartDesign::Body] Body199  label="Corner002"
  Group = -> [Sketch224,Pad111,Sketch225,Pocket080,Sketch226,Pocket081,Sketch227,Pocket082,Sketch228,Pad112,Sketch229,Pad113]
  Origin = -> Origin271
  Tip = -> Pad113
FEATURE [App::Part] Part072  label="soporte90-003"
  Group = -> [Body199]
  Origin = -> Origin272
  Placement = pos=(321,339,20) rot=(0,0,1;-1.5708rad)
FEATURE [Sketcher::SketchObject] Sketch230
  FullyConstrained = true
  MapMode = 5
  Placement = pos=(0,0,0) rot=(0.57735,0.57735,0.57735;2.0944rad)
  Support = -> [YZ_Plane267]
  sketch-geometry (5):
    g0: LineSegment StartX=0 StartY=0 StartZ=0 EndX=0 EndY=20 EndZ=0
    g1: LineSegment StartX=0 StartY=20 StartZ=0 EndX=-3 EndY=20 EndZ=0
    g2: LineSegment StartX=-3 StartY=20 StartZ=0 EndX=-20 EndY=3 EndZ=0
    g3: LineSegment StartX=-20 StartY=3 StartZ=0 EndX=-20 EndY=0 EndZ=0
    g4: LineSegment StartX=-20 StartY=0 StartZ=0 EndX=0 EndY=0 EndZ=0
  constraints (14):
    c: Coincident(g-1,g0)
    c: PointOnObject(g0,g-2)
    c: Coincident(g0,g1)
    c: Horizontal(g1)
    c: Coincident(g1,g2)
    c: Coincident(g2,g3)
    c: PointOnObject(g3,g-1)
    c: Vertical(g3)
    c: Coincident(g3,g4)
    c: Coincident(g4,g0)
    c: DistanceY(g0,g0) = 20
    c: DistanceY(g3,g3) = 3
    c: DistanceX(g1,g1) = 3
    c: DistanceX(g4,g4) = 20
FEATURE [PartDesign::Pad] Pad114
  Direction = (1,1,1)
  Length = 17
  Length2 = 100
  Placement = pos=(0,0,0) rot=(0.57735,0.57735,0.57735;2.0944rad)
  Profile = -> Sketch230
  Type = 0
FEATURE [Sketcher::SketchObject] Sketch231
  ExternalGeometry = -> [Pad114]
  FullyConstrained = true
  MapMode = 5
  Placement = pos=(-8.8e-15,-20,4.4e-15) rot=(-0.57735,-0.57735,0.57735;4.18879rad)
  Support = -> [Pad114]
  sketch-geometry (4):
    g0: LineSegment StartX=-3 StartY=2 StartZ=0 EndX=-20 EndY=2 EndZ=0
    g1: LineSegment StartX=-20 StartY=2 StartZ=0 EndX=-20 EndY=15 EndZ=0
    g2: LineSegment StartX=-20 StartY=15 StartZ=0 EndX=-3 EndY=15 EndZ=0
    g3: LineSegment StartX=-3 StartY=15 StartZ=0 EndX=-3 EndY=2 EndZ=0
  constraints (12):
    c: Coincident(g0,g1)
    c: Coincident(g1,g2)
    c: Coincident(g2,g3)
    c: Coincident(g3,g0)
    c: Horizontal(g0)
    c: Horizontal(g2)
    c: Vertical(g1)
    c: Vertical(g3)
    c: PointOnObject(g0,g-3)
    c: DistanceY(g1,g-6) = 2
    c: DistanceY(g-6,g0) = 2
    c: PointOnObject(g1,g-6)
FEATURE [PartDesign::Pocket] Pocket083
  BaseFeature = -> Pad114
  Length = 17
  Length2 = 100
  Placement = pos=(0,0,0) rot=(0.57735,0.57735,0.57735;2.0944rad)
  Profile = -> Sketch231
  Type = 0
FEATURE [Sketcher::SketchObject] Sketch232
  ExternalGeometry = -> [Pocket083]
  FullyConstrained = true
  MapMode = 5
  Placement = pos=(-1.7e-15,-3,6e-16) rot=(-0.57735,-0.57735,0.57735;4.18879rad)
  Support = -> [Pocket083]
  sketch-geometry (5):
    g0: LineSegment StartX=-20 StartY=8.5 StartZ=0 EndX=-3 EndY=8.5 EndZ=0
    g1: ArcOfCircle CenterX=-10 CenterY=8.5 CenterZ=0 NormalX=0 NormalY=0 NormalZ=1 AngleXU=0 Radius=3 StartAngle=4.71239 EndAngle=7.85398
    g2: ArcOfCircle CenterX=-13 CenterY=8.5 CenterZ=0 NormalX=0 NormalY=0 NormalZ=1 AngleXU=0 Radius=3 StartAngle=1.5708 EndAngle=4.71239
    g3: LineSegment StartX=-10 StartY=11.5 StartZ=0 EndX=-13 EndY=11.5 EndZ=0
    g4: LineSegment StartX=-10 StartY=5.5 StartZ=0 EndX=-13 EndY=5.5 EndZ=0
  constraints (14):
    c: PointOnObject(g0,g-6)
    c: PointOnObject(g0,g-4)
    c: Horizontal(g0)
    c: DistanceY(g0,g-4) = 6.5
    c: Tangent(g1,g4) = 1.5708
    c: Tangent(g1,g3) = -1.5708
    c: Tangent(g3,g2) = -1.5708
    c: Tangent(g4,g2) = 1.5708
    c: Horizontal(g3)
    c: Equal(g1,g2)
    c: PointOnObject(g1,g0)
    c: Radius(g1) = 3
    c: DistanceX(g3,g3) = 3
    c: DistanceX(g0,g2) = 7
FEATURE [PartDesign::Pocket] Pocket084
  BaseFeature = -> Pocket083
  Length = 5
  Length2 = 100
  Placement = pos=(0,0,0) rot=(0.57735,0.57735,0.57735;2.0944rad)
  Profile = -> Sketch232
  Type = 2
FEATURE [Sketcher::SketchObject] Sketch233
  ExternalGeometry = -> [Pocket084]
  FullyConstrained = true
  MapMode = 5
  Placement = pos=(-3e-16,1.2e-15,3) rot=(0,0,-1;1.5708rad)
  Support = -> [Pocket084]
  sketch-geometry (5):
    g0: LineSegment StartX=3 StartY=8.5 StartZ=0 EndX=20 EndY=8.5 EndZ=0
    g1: ArcOfCircle CenterX=10 CenterY=8.5 CenterZ=0 NormalX=0 NormalY=0 NormalZ=1 AngleXU=0 Radius=3 StartAngle=1.5708 EndAngle=4.71239
    g2: ArcOfCircle CenterX=13 CenterY=8.5 CenterZ=0 NormalX=0 NormalY=0 NormalZ=1 AngleXU=0 Radius=3 StartAngle=4.71239 EndAngle=7.85398
    g3: LineSegment StartX=10 StartY=5.5 StartZ=0 EndX=13 EndY=5.5 EndZ=0
    g4: LineSegment StartX=10 StartY=11.5 StartZ=0 EndX=13 EndY=11.5 EndZ=0
  constraints (14):
    c: PointOnObject(g0,g-4)
    c: PointOnObject(g0,g-5)
    c: Horizontal(g0)
    c: DistanceY(g0,g-4) = 6.5
    c: Tangent(g1,g4) = 1.5708
    c: Tangent(g1,g3) = -1.5708
    c: Tangent(g3,g2) = -1.5708
    c: Tangent(g4,g2) = 1.5708
    c: Horizontal(g3)
    c: Equal(g1,g2)
    c: PointOnObject(g1,g0)
    c: Radius(g2) = 3
    c: DistanceX(g4,g4) = 3
    c: DistanceX(g2,g0) = 7
FEATURE [PartDesign::Pocket] Pocket085
  BaseFeature = -> Pocket084
  Length = 5
  Length2 = 100
  Placement = pos=(0,0,0) rot=(0.57735,0.57735,0.57735;2.0944rad)
  Profile = -> Sketch233
  Type = 2
FEATURE [Sketcher::SketchObject] Sketch234
  ExternalGeometry = -> [Pocket085]
  FullyConstrained = true
  MapMode = 5
  Placement = pos=(0,0,0) rot=(0.57735,0.57735,0.57735;4.18879rad)
  Support = -> [Pocket085]
  sketch-geometry (9):
    g0: LineSegment StartX=0 StartY=8.5 StartZ=0 EndX=20 EndY=8.5 EndZ=0
    g1: ArcOfCircle CenterX=3 CenterY=9.5 CenterZ=0 NormalX=0 NormalY=0 NormalZ=1 AngleXU=0 Radius=1 StartAngle=0 EndAngle=3.14159
    g2: ArcOfCircle CenterX=3 CenterY=7.5 CenterZ=0 NormalX=0 NormalY=0 NormalZ=1 AngleXU=0 Radius=1 StartAngle=3.14159 EndAngle=6.28319
    g3: LineSegment StartX=2 StartY=9.5 StartZ=0 EndX=2 EndY=7.5 EndZ=0
    g4: LineSegment StartX=4 StartY=9.5 StartZ=0 EndX=4 EndY=7.5 EndZ=0
    g5: ArcOfCircle CenterX=18 CenterY=9.5 CenterZ=0 NormalX=0 NormalY=0 NormalZ=1 AngleXU=0 Radius=1 StartAngle=-9e-16 EndAngle=3.14159
    g6: ArcOfCircle CenterX=18 CenterY=7.5 CenterZ=0 NormalX=0 NormalY=0 NormalZ=1 AngleXU=0 Radius=1 StartAngle=3.14159 EndAngle=6.28319
    g7: LineSegment StartX=17 StartY=9.5 StartZ=0 EndX=17 EndY=7.5 EndZ=0
    g8: LineSegment StartX=19 StartY=9.5 StartZ=0 EndX=19 EndY=7.5 EndZ=0
  constraints (24):
    c: PointOnObject(g0,g-2)
    c: PointOnObject(g0,g-5)
    c: Horizontal(g0)
    c: DistanceY(g0,g-3) = 8.5
    c: Tangent(g1,g4) = 1.5708
    c: Tangent(g1,g3) = -1.5708
    c: Tangent(g3,g2) = -1.5708
    c: Tangent(g4,g2) = 1.5708
    c: Vertical(g3)
    c: Equal(g1,g2)
    c: Tangent(g5,g8) = 1.5708
    c: Tangent(g5,g7) = -1.5708
    c: Tangent(g7,g6) = -1.5708
    c: Tangent(g8,g6) = 1.5708
    c: Vertical(g7)
    c: Equal(g5,g6)
    c: Equal(g1,g5)
    c: Equal(g4,g7)
    c: DistanceY(g4,g4) = 2
    c: Radius(g1) = 1
    c: Horizontal(g5,g1)
    c: DistanceX(g0,g1) = 3
    c: DistanceX(g5,g0) = 2
    c: DistanceY(g0,g1) = 1
FEATURE [PartDesign::Pad] Pad115
  BaseFeature = -> Pocket085
  Direction = (1,1,1)
  Length = 1
  Length2 = 100
  Placement = pos=(0,0,0) rot=(0.57735,0.57735,0.57735;2.0944rad)
  Profile = -> Sketch234
  Type = 0
FEATURE [Sketcher::SketchObject] Sketch235
  ExternalGeometry = -> [Pad115]
  FullyConstrained = true
  MapMode = 5
  Placement = pos=(0,0,1e-16) rot=(0.707107,0.707107,0;3.14159rad)
  Support = -> [Pad115]
  sketch-geometry (9):
    g0: LineSegment StartX=0 StartY=8.5 StartZ=0 EndX=-20 EndY=8.5 EndZ=0
    g1: ArcOfCircle CenterX=-3 CenterY=7.5 CenterZ=0 NormalX=0 NormalY=0 NormalZ=1 AngleXU=0 Radius=1 StartAngle=3.14159 EndAngle=6.28319
    g2: ArcOfCircle CenterX=-3 CenterY=9.5 CenterZ=0 NormalX=0 NormalY=0 NormalZ=1 AngleXU=0 Radius=1 StartAngle=3e-16 EndAngle=3.14159
    g3: LineSegment StartX=-2 StartY=7.5 StartZ=0 EndX=-2 EndY=9.5 EndZ=0
    g4: LineSegment StartX=-4 StartY=7.5 StartZ=0 EndX=-4 EndY=9.5 EndZ=0
    g5: ArcOfCircle CenterX=-18 CenterY=9.5 CenterZ=0 NormalX=0 NormalY=0 NormalZ=1 AngleXU=0 Radius=1 StartAngle=0 EndAngle=3.14159
    g6: ArcOfCircle CenterX=-18 CenterY=7.5 CenterZ=0 NormalX=0 NormalY=0 NormalZ=1 AngleXU=0 Radius=1 StartAngle=3.14159 EndAngle=6.28319
    g7: LineSegment StartX=-19 StartY=9.5 StartZ=0 EndX=-19 EndY=7.5 EndZ=0
    g8: LineSegment StartX=-17 StartY=9.5 StartZ=0 EndX=-17 EndY=7.5 EndZ=0
  constraints (24):
    c: PointOnObject(g0,g-2)
    c: PointOnObject(g0,g-4)
    c: Horizontal(g0)
    c: DistanceY(g0,g-3) = 8.5
    c: Tangent(g1,g4) = 1.5708
    c: Tangent(g1,g3) = -1.5708
    c: Tangent(g3,g2) = -1.5708
    c: Tangent(g4,g2) = 1.5708
    c: Vertical(g3)
    c: Equal(g1,g2)
    c: Radius(g2) = 1
    c: DistanceY(g4,g4) = 2
    c: DistanceY(g0,g2) = 1
    c: DistanceX(g2,g0) = 3
    c: Tangent(g5,g8) = 1.5708
    c: Tangent(g5,g7) = -1.5708
    c: Tangent(g7,g6) = -1.5708
    c: Tangent(g8,g6) = 1.5708
    c: Vertical(g7)
    c: Equal(g5,g6)
    c: Equal(g5,g2)
    c: Equal(g8,g4)
    c: Horizontal(g5,g2)
    c: DistanceX(g0,g5) = 2
FEATURE [PartDesign::Pad] Pad116
  BaseFeature = -> Pad115
  Direction = (1,1,1)
  Length = 1
  Length2 = 100
  Placement = pos=(0,0,0) rot=(0.57735,0.57735,0.57735;2.0944rad)
  Profile = -> Sketch235
  Type = 0
FEATURE [PartDesign::Body] Body200  label="Corner003"
  Group = -> [Sketch230,Pad114,Sketch231,Pocket083,Sketch232,Pocket084,Sketch233,Pocket085,Sketch234,Pad115,Sketch235,Pad116]
  Origin = -> Origin273
  Tip = -> Pad116
FEATURE [App::Part] Part073  label="soporte90-004"
  Group = -> [Body200]
  Origin = -> Origin274
  Placement = pos=(20,1,20) rot=(0,0,1;1.5708rad)
FEATURE [Sketcher::SketchObject] Sketch236
  FullyConstrained = true
  MapMode = 5
  Placement = pos=(0,0,0) rot=(0.57735,0.57735,0.57735;2.0944rad)
  Support = -> [YZ_Plane269]
  sketch-geometry (5):
    g0: LineSegment StartX=0 StartY=0 StartZ=0 EndX=0 EndY=20 EndZ=0
    g1: LineSegment StartX=0 StartY=20 StartZ=0 EndX=-3 EndY=20 EndZ=0
    g2: LineSegment StartX=-3 StartY=20 StartZ=0 EndX=-20 EndY=3 EndZ=0
    g3: LineSegment StartX=-20 StartY=3 StartZ=0 EndX=-20 EndY=0 EndZ=0
    g4: LineSegment StartX=-20 StartY=0 StartZ=0 EndX=0 EndY=0 EndZ=0
  constraints (14):
    c: Coincident(g-1,g0)
    c: PointOnObject(g0,g-2)
    c: Coincident(g0,g1)
    c: Horizontal(g1)
    c: Coincident(g1,g2)
    c: Coincident(g2,g3)
    c: PointOnObject(g3,g-1)
    c: Vertical(g3)
    c: Coincident(g3,g4)
    c: Coincident(g4,g0)
    c: DistanceY(g0,g0) = 20
    c: DistanceY(g3,g3) = 3
    c: DistanceX(g1,g1) = 3
    c: DistanceX(g4,g4) = 20
FEATURE [PartDesign::Pad] Pad117
  Direction = (1,1,1)
  Length = 17
  Length2 = 100
  Placement = pos=(0,0,0) rot=(0.57735,0.57735,0.57735;2.0944rad)
  Profile = -> Sketch236
  Type = 0
FEATURE [Sketcher::SketchObject] Sketch237
  ExternalGeometry = -> [Pad117]
  FullyConstrained = true
  MapMode = 5
  Placement = pos=(-8.8e-15,-20,4.4e-15) rot=(-0.57735,-0.57735,0.57735;4.18879rad)
  Support = -> [Pad117]
  sketch-geometry (4):
    g0: LineSegment StartX=-3 StartY=2 StartZ=0 EndX=-20 EndY=2 EndZ=0
    g1: LineSegment StartX=-20 StartY=2 StartZ=0 EndX=-20 EndY=15 EndZ=0
    g2: LineSegment StartX=-20 StartY=15 StartZ=0 EndX=-3 EndY=15 EndZ=0
    g3: LineSegment StartX=-3 StartY=15 StartZ=0 EndX=-3 EndY=2 EndZ=0
  constraints (12):
    c: Coincident(g0,g1)
    c: Coincident(g1,g2)
    c: Coincident(g2,g3)
    c: Coincident(g3,g0)
    c: Horizontal(g0)
    c: Horizontal(g2)
    c: Vertical(g1)
    c: Vertical(g3)
    c: PointOnObject(g0,g-3)
    c: DistanceY(g1,g-6) = 2
    c: DistanceY(g-6,g0) = 2
    c: PointOnObject(g1,g-6)
FEATURE [PartDesign::Pocket] Pocket086
  BaseFeature = -> Pad117
  Length = 17
  Length2 = 100
  Placement = pos=(0,0,0) rot=(0.57735,0.57735,0.57735;2.0944rad)
  Profile = -> Sketch237
  Type = 0
FEATURE [Sketcher::SketchObject] Sketch238
  ExternalGeometry = -> [Pocket086]
  FullyConstrained = true
  MapMode = 5
  Placement = pos=(-1.7e-15,-3,6e-16) rot=(-0.57735,-0.57735,0.57735;4.18879rad)
  Support = -> [Pocket086]
  sketch-geometry (5):
    g0: LineSegment StartX=-20 StartY=8.5 StartZ=0 EndX=-3 EndY=8.5 EndZ=0
    g1: ArcOfCircle CenterX=-10 CenterY=8.5 CenterZ=0 NormalX=0 NormalY=0 NormalZ=1 AngleXU=0 Radius=3 StartAngle=4.71239 EndAngle=7.85398
    g2: ArcOfCircle CenterX=-13 CenterY=8.5 CenterZ=0 NormalX=0 NormalY=0 NormalZ=1 AngleXU=0 Radius=3 StartAngle=1.5708 EndAngle=4.71239
    g3: LineSegment StartX=-10 StartY=11.5 StartZ=0 EndX=-13 EndY=11.5 EndZ=0
    g4: LineSegment StartX=-10 StartY=5.5 StartZ=0 EndX=-13 EndY=5.5 EndZ=0
  constraints (14):
    c: PointOnObject(g0,g-6)
    c: PointOnObject(g0,g-4)
    c: Horizontal(g0)
    c: DistanceY(g0,g-4) = 6.5
    c: Tangent(g1,g4) = 1.5708
    c: Tangent(g1,g3) = -1.5708
    c: Tangent(g3,g2) = -1.5708
    c: Tangent(g4,g2) = 1.5708
    c: Horizontal(g3)
    c: Equal(g1,g2)
    c: PointOnObject(g1,g0)
    c: Radius(g1) = 3
    c: DistanceX(g3,g3) = 3
    c: DistanceX(g0,g2) = 7
FEATURE [PartDesign::Pocket] Pocket087
  BaseFeature = -> Pocket086
  Length = 5
  Length2 = 100
  Placement = pos=(0,0,0) rot=(0.57735,0.57735,0.57735;2.0944rad)
  Profile = -> Sketch238
  Type = 2
FEATURE [Sketcher::SketchObject] Sketch239
  ExternalGeometry = -> [Pocket087]
  FullyConstrained = true
  MapMode = 5
  Placement = pos=(-3e-16,1.2e-15,3) rot=(0,0,-1;1.5708rad)
  Support = -> [Pocket087]
  sketch-geometry (5):
    g0: LineSegment StartX=3 StartY=8.5 StartZ=0 EndX=20 EndY=8.5 EndZ=0
    g1: ArcOfCircle CenterX=10 CenterY=8.5 CenterZ=0 NormalX=0 NormalY=0 NormalZ=1 AngleXU=0 Radius=3 StartAngle=1.5708 EndAngle=4.71239
    g2: ArcOfCircle CenterX=13 CenterY=8.5 CenterZ=0 NormalX=0 NormalY=0 NormalZ=1 AngleXU=0 Radius=3 StartAngle=4.71239 EndAngle=7.85398
    g3: LineSegment StartX=10 StartY=5.5 StartZ=0 EndX=13 EndY=5.5 EndZ=0
    g4: LineSegment StartX=10 StartY=11.5 StartZ=0 EndX=13 EndY=11.5 EndZ=0
  constraints (14):
    c: PointOnObject(g0,g-4)
    c: PointOnObject(g0,g-5)
    c: Horizontal(g0)
    c: DistanceY(g0,g-4) = 6.5
    c: Tangent(g1,g4) = 1.5708
    c: Tangent(g1,g3) = -1.5708
    c: Tangent(g3,g2) = -1.5708
    c: Tangent(g4,g2) = 1.5708
    c: Horizontal(g3)
    c: Equal(g1,g2)
    c: PointOnObject(g1,g0)
    c: Radius(g2) = 3
    c: DistanceX(g4,g4) = 3
    c: DistanceX(g2,g0) = 7
FEATURE [PartDesign::Pocket] Pocket088
  BaseFeature = -> Pocket087
  Length = 5
  Length2 = 100
  Placement = pos=(0,0,0) rot=(0.57735,0.57735,0.57735;2.0944rad)
  Profile = -> Sketch239
  Type = 2
FEATURE [Sketcher::SketchObject] Sketch240
  ExternalGeometry = -> [Pocket088]
  FullyConstrained = true
  MapMode = 5
  Placement = pos=(0,0,0) rot=(0.57735,0.57735,0.57735;4.18879rad)
  Support = -> [Pocket088]
  sketch-geometry (9):
    g0: LineSegment StartX=0 StartY=8.5 StartZ=0 EndX=20 EndY=8.5 EndZ=0
    g1: ArcOfCircle CenterX=3 CenterY=9.5 CenterZ=0 NormalX=0 NormalY=0 NormalZ=1 AngleXU=0 Radius=1 StartAngle=0 EndAngle=3.14159
    g2: ArcOfCircle CenterX=3 CenterY=7.5 CenterZ=0 NormalX=0 NormalY=0 NormalZ=1 AngleXU=0 Radius=1 StartAngle=3.14159 EndAngle=6.28319
    g3: LineSegment StartX=2 StartY=9.5 StartZ=0 EndX=2 EndY=7.5 EndZ=0
    g4: LineSegment StartX=4 StartY=9.5 StartZ=0 EndX=4 EndY=7.5 EndZ=0
    g5: ArcOfCircle CenterX=18 CenterY=9.5 CenterZ=0 NormalX=0 NormalY=0 NormalZ=1 AngleXU=0 Radius=1 StartAngle=-9e-16 EndAngle=3.14159
    g6: ArcOfCircle CenterX=18 CenterY=7.5 CenterZ=0 NormalX=0 NormalY=0 NormalZ=1 AngleXU=0 Radius=1 StartAngle=3.14159 EndAngle=6.28319
    g7: LineSegment StartX=17 StartY=9.5 StartZ=0 EndX=17 EndY=7.5 EndZ=0
    g8: LineSegment StartX=19 StartY=9.5 StartZ=0 EndX=19 EndY=7.5 EndZ=0
  constraints (24):
    c: PointOnObject(g0,g-2)
    c: PointOnObject(g0,g-5)
    c: Horizontal(g0)
    c: DistanceY(g0,g-3) = 8.5
    c: Tangent(g1,g4) = 1.5708
    c: Tangent(g1,g3) = -1.5708
    c: Tangent(g3,g2) = -1.5708
    c: Tangent(g4,g2) = 1.5708
    c: Vertical(g3)
    c: Equal(g1,g2)
    c: Tangent(g5,g8) = 1.5708
    c: Tangent(g5,g7) = -1.5708
    c: Tangent(g7,g6) = -1.5708
    c: Tangent(g8,g6) = 1.5708
    c: Vertical(g7)
    c: Equal(g5,g6)
    c: Equal(g1,g5)
    c: Equal(g4,g7)
    c: DistanceY(g4,g4) = 2
    c: Radius(g1) = 1
    c: Horizontal(g5,g1)
    c: DistanceX(g0,g1) = 3
    c: DistanceX(g5,g0) = 2
    c: DistanceY(g0,g1) = 1
FEATURE [PartDesign::Pad] Pad118
  BaseFeature = -> Pocket088
  Direction = (1,1,1)
  Length = 1
  Length2 = 100
  Placement = pos=(0,0,0) rot=(0.57735,0.57735,0.57735;2.0944rad)
  Profile = -> Sketch240
  Type = 0
FEATURE [Sketcher::SketchObject] Sketch241
  ExternalGeometry = -> [Pad118]
  FullyConstrained = true
  MapMode = 5
  Placement = pos=(0,0,1e-16) rot=(0.707107,0.707107,0;3.14159rad)
  Support = -> [Pad118]
  sketch-geometry (9):
    g0: LineSegment StartX=0 StartY=8.5 StartZ=0 EndX=-20 EndY=8.5 EndZ=0
    g1: ArcOfCircle CenterX=-3 CenterY=7.5 CenterZ=0 NormalX=0 NormalY=0 NormalZ=1 AngleXU=0 Radius=1 StartAngle=3.14159 EndAngle=6.28319
    g2: ArcOfCircle CenterX=-3 CenterY=9.5 CenterZ=0 NormalX=0 NormalY=0 NormalZ=1 AngleXU=0 Radius=1 StartAngle=3e-16 EndAngle=3.14159
    g3: LineSegment StartX=-2 StartY=7.5 StartZ=0 EndX=-2 EndY=9.5 EndZ=0
    g4: LineSegment StartX=-4 StartY=7.5 StartZ=0 EndX=-4 EndY=9.5 EndZ=0
    g5: ArcOfCircle CenterX=-18 CenterY=9.5 CenterZ=0 NormalX=0 NormalY=0 NormalZ=1 AngleXU=0 Radius=1 StartAngle=0 EndAngle=3.14159
    g6: ArcOfCircle CenterX=-18 CenterY=7.5 CenterZ=0 NormalX=0 NormalY=0 NormalZ=1 AngleXU=0 Radius=1 StartAngle=3.14159 EndAngle=6.28319
    g7: LineSegment StartX=-19 StartY=9.5 StartZ=0 EndX=-19 EndY=7.5 EndZ=0
    g8: LineSegment StartX=-17 StartY=9.5 StartZ=0 EndX=-17 EndY=7.5 EndZ=0
  constraints (24):
    c: PointOnObject(g0,g-2)
    c: PointOnObject(g0,g-4)
    c: Horizontal(g0)
    c: DistanceY(g0,g-3) = 8.5
    c: Tangent(g1,g4) = 1.5708
    c: Tangent(g1,g3) = -1.5708
    c: Tangent(g3,g2) = -1.5708
    c: Tangent(g4,g2) = 1.5708
    c: Vertical(g3)
    c: Equal(g1,g2)
    c: Radius(g2) = 1
    c: DistanceY(g4,g4) = 2
    c: DistanceY(g0,g2) = 1
    c: DistanceX(g2,g0) = 3
    c: Tangent(g5,g8) = 1.5708
    c: Tangent(g5,g7) = -1.5708
    c: Tangent(g7,g6) = -1.5708
    c: Tangent(g8,g6) = 1.5708
    c: Vertical(g7)
    c: Equal(g5,g6)
    c: Equal(g5,g2)
    c: Equal(g8,g4)
    c: Horizontal(g5,g2)
    c: DistanceX(g0,g5) = 2
FEATURE [PartDesign::Pad] Pad119
  BaseFeature = -> Pad118
  Direction = (1,1,1)
  Length = 1
  Length2 = 100
  Placement = pos=(0,0,0) rot=(0.57735,0.57735,0.57735;2.0944rad)
  Profile = -> Sketch241
  Type = 0
FEATURE [PartDesign::Body] Body201  label="Corner004"
  Group = -> [Sketch236,Pad117,Sketch237,Pocket086,Sketch238,Pocket087,Sketch239,Pocket088,Sketch240,Pad118,Sketch241,Pad119]
  Origin = -> Origin275
  Tip = -> Pad119
FEATURE [App::Part] Part074  label="soporte90-005"
  Group = -> [Body201]
  Origin = -> Origin276
  Placement = pos=(20,340,170) rot=(0.707107,-0.707107,0;3.14159rad)
FEATURE [Sketcher::SketchObject] Sketch242
  FullyConstrained = true
  MapMode = 5
  Placement = pos=(0,0,0) rot=(0.57735,0.57735,0.57735;2.0944rad)
  Support = -> [YZ_Plane271]
  sketch-geometry (5):
    g0: LineSegment StartX=0 StartY=0 StartZ=0 EndX=0 EndY=20 EndZ=0
    g1: LineSegment StartX=0 StartY=20 StartZ=0 EndX=-3 EndY=20 EndZ=0
    g2: LineSegment StartX=-3 StartY=20 StartZ=0 EndX=-20 EndY=3 EndZ=0
    g3: LineSegment StartX=-20 StartY=3 StartZ=0 EndX=-20 EndY=0 EndZ=0
    g4: LineSegment StartX=-20 StartY=0 StartZ=0 EndX=0 EndY=0 EndZ=0
  constraints (14):
    c: Coincident(g-1,g0)
    c: PointOnObject(g0,g-2)
    c: Coincident(g0,g1)
    c: Horizontal(g1)
    c: Coincident(g1,g2)
    c: Coincident(g2,g3)
    c: PointOnObject(g3,g-1)
    c: Vertical(g3)
    c: Coincident(g3,g4)
    c: Coincident(g4,g0)
    c: DistanceY(g0,g0) = 20
    c: DistanceY(g3,g3) = 3
    c: DistanceX(g1,g1) = 3
    c: DistanceX(g4,g4) = 20
FEATURE [PartDesign::Pad] Pad120
  Direction = (1,1,1)
  Length = 17
  Length2 = 100
  Placement = pos=(0,0,0) rot=(0.57735,0.57735,0.57735;2.0944rad)
  Profile = -> Sketch242
  Type = 0
FEATURE [Sketcher::SketchObject] Sketch243
  ExternalGeometry = -> [Pad120]
  FullyConstrained = true
  MapMode = 5
  Placement = pos=(-8.8e-15,-20,4.4e-15) rot=(-0.57735,-0.57735,0.57735;4.18879rad)
  Support = -> [Pad120]
  sketch-geometry (4):
    g0: LineSegment StartX=-3 StartY=2 StartZ=0 EndX=-20 EndY=2 EndZ=0
    g1: LineSegment StartX=-20 StartY=2 StartZ=0 EndX=-20 EndY=15 EndZ=0
    g2: LineSegment StartX=-20 StartY=15 StartZ=0 EndX=-3 EndY=15 EndZ=0
    g3: LineSegment StartX=-3 StartY=15 StartZ=0 EndX=-3 EndY=2 EndZ=0
  constraints (12):
    c: Coincident(g0,g1)
    c: Coincident(g1,g2)
    c: Coincident(g2,g3)
    c: Coincident(g3,g0)
    c: Horizontal(g0)
    c: Horizontal(g2)
    c: Vertical(g1)
    c: Vertical(g3)
    c: PointOnObject(g0,g-3)
    c: DistanceY(g1,g-6) = 2
    c: DistanceY(g-6,g0) = 2
    c: PointOnObject(g1,g-6)
FEATURE [PartDesign::Pocket] Pocket089
  BaseFeature = -> Pad120
  Length = 17
  Length2 = 100
  Placement = pos=(0,0,0) rot=(0.57735,0.57735,0.57735;2.0944rad)
  Profile = -> Sketch243
  Type = 0
FEATURE [Sketcher::SketchObject] Sketch244
  ExternalGeometry = -> [Pocket089]
  FullyConstrained = true
  MapMode = 5
  Placement = pos=(-1.7e-15,-3,6e-16) rot=(-0.57735,-0.57735,0.57735;4.18879rad)
  Support = -> [Pocket089]
  sketch-geometry (5):
    g0: LineSegment StartX=-20 StartY=8.5 StartZ=0 EndX=-3 EndY=8.5 EndZ=0
    g1: ArcOfCircle CenterX=-10 CenterY=8.5 CenterZ=0 NormalX=0 NormalY=0 NormalZ=1 AngleXU=0 Radius=3 StartAngle=4.71239 EndAngle=7.85398
    g2: ArcOfCircle CenterX=-13 CenterY=8.5 CenterZ=0 NormalX=0 NormalY=0 NormalZ=1 AngleXU=0 Radius=3 StartAngle=1.5708 EndAngle=4.71239
    g3: LineSegment StartX=-10 StartY=11.5 StartZ=0 EndX=-13 EndY=11.5 EndZ=0
    g4: LineSegment StartX=-10 StartY=5.5 StartZ=0 EndX=-13 EndY=5.5 EndZ=0
  constraints (14):
    c: PointOnObject(g0,g-6)
    c: PointOnObject(g0,g-4)
    c: Horizontal(g0)
    c: DistanceY(g0,g-4) = 6.5
    c: Tangent(g1,g4) = 1.5708
    c: Tangent(g1,g3) = -1.5708
    c: Tangent(g3,g2) = -1.5708
    c: Tangent(g4,g2) = 1.5708
    c: Horizontal(g3)
    c: Equal(g1,g2)
    c: PointOnObject(g1,g0)
    c: Radius(g1) = 3
    c: DistanceX(g3,g3) = 3
    c: DistanceX(g0,g2) = 7
FEATURE [PartDesign::Pocket] Pocket090
  BaseFeature = -> Pocket089
  Length = 5
  Length2 = 100
  Placement = pos=(0,0,0) rot=(0.57735,0.57735,0.57735;2.0944rad)
  Profile = -> Sketch244
  Type = 2
FEATURE [Sketcher::SketchObject] Sketch245
  ExternalGeometry = -> [Pocket090]
  FullyConstrained = true
  MapMode = 5
  Placement = pos=(-3e-16,1.2e-15,3) rot=(0,0,-1;1.5708rad)
  Support = -> [Pocket090]
  sketch-geometry (5):
    g0: LineSegment StartX=3 StartY=8.5 StartZ=0 EndX=20 EndY=8.5 EndZ=0
    g1: ArcOfCircle CenterX=10 CenterY=8.5 CenterZ=0 NormalX=0 NormalY=0 NormalZ=1 AngleXU=0 Radius=3 StartAngle=1.5708 EndAngle=4.71239
    g2: ArcOfCircle CenterX=13 CenterY=8.5 CenterZ=0 NormalX=0 NormalY=0 NormalZ=1 AngleXU=0 Radius=3 StartAngle=4.71239 EndAngle=7.85398
    g3: LineSegment StartX=10 StartY=5.5 StartZ=0 EndX=13 EndY=5.5 EndZ=0
    g4: LineSegment StartX=10 StartY=11.5 StartZ=0 EndX=13 EndY=11.5 EndZ=0
  constraints (14):
    c: PointOnObject(g0,g-4)
    c: PointOnObject(g0,g-5)
    c: Horizontal(g0)
    c: DistanceY(g0,g-4) = 6.5
    c: Tangent(g1,g4) = 1.5708
    c: Tangent(g1,g3) = -1.5708
    c: Tangent(g3,g2) = -1.5708
    c: Tangent(g4,g2) = 1.5708
    c: Horizontal(g3)
    c: Equal(g1,g2)
    c: PointOnObject(g1,g0)
    c: Radius(g2) = 3
    c: DistanceX(g4,g4) = 3
    c: DistanceX(g2,g0) = 7
FEATURE [PartDesign::Pocket] Pocket091
  BaseFeature = -> Pocket090
  Length = 5
  Length2 = 100
  Placement = pos=(0,0,0) rot=(0.57735,0.57735,0.57735;2.0944rad)
  Profile = -> Sketch245
  Type = 2
FEATURE [Sketcher::SketchObject] Sketch246
  ExternalGeometry = -> [Pocket091]
  FullyConstrained = true
  MapMode = 5
  Placement = pos=(0,0,0) rot=(0.57735,0.57735,0.57735;4.18879rad)
  Support = -> [Pocket091]
  sketch-geometry (9):
    g0: LineSegment StartX=0 StartY=8.5 StartZ=0 EndX=20 EndY=8.5 EndZ=0
    g1: ArcOfCircle CenterX=3 CenterY=9.5 CenterZ=0 NormalX=0 NormalY=0 NormalZ=1 AngleXU=0 Radius=1 StartAngle=0 EndAngle=3.14159
    g2: ArcOfCircle CenterX=3 CenterY=7.5 CenterZ=0 NormalX=0 NormalY=0 NormalZ=1 AngleXU=0 Radius=1 StartAngle=3.14159 EndAngle=6.28319
    g3: LineSegment StartX=2 StartY=9.5 StartZ=0 EndX=2 EndY=7.5 EndZ=0
    g4: LineSegment StartX=4 StartY=9.5 StartZ=0 EndX=4 EndY=7.5 EndZ=0
    g5: ArcOfCircle CenterX=18 CenterY=9.5 CenterZ=0 NormalX=0 NormalY=0 NormalZ=1 AngleXU=0 Radius=1 StartAngle=-9e-16 EndAngle=3.14159
    g6: ArcOfCircle CenterX=18 CenterY=7.5 CenterZ=0 NormalX=0 NormalY=0 NormalZ=1 AngleXU=0 Radius=1 StartAngle=3.14159 EndAngle=6.28319
    g7: LineSegment StartX=17 StartY=9.5 StartZ=0 EndX=17 EndY=7.5 EndZ=0
    g8: LineSegment StartX=19 StartY=9.5 StartZ=0 EndX=19 EndY=7.5 EndZ=0
  constraints (24):
    c: PointOnObject(g0,g-2)
    c: PointOnObject(g0,g-5)
    c: Horizontal(g0)
    c: DistanceY(g0,g-3) = 8.5
    c: Tangent(g1,g4) = 1.5708
    c: Tangent(g1,g3) = -1.5708
    c: Tangent(g3,g2) = -1.5708
    c: Tangent(g4,g2) = 1.5708
    c: Vertical(g3)
    c: Equal(g1,g2)
    c: Tangent(g5,g8) = 1.5708
    c: Tangent(g5,g7) = -1.5708
    c: Tangent(g7,g6) = -1.5708
    c: Tangent(g8,g6) = 1.5708
    c: Vertical(g7)
    c: Equal(g5,g6)
    c: Equal(g1,g5)
    c: Equal(g4,g7)
    c: DistanceY(g4,g4) = 2
    c: Radius(g1) = 1
    c: Horizontal(g5,g1)
    c: DistanceX(g0,g1) = 3
    c: DistanceX(g5,g0) = 2
    c: DistanceY(g0,g1) = 1
FEATURE [PartDesign::Pad] Pad121
  BaseFeature = -> Pocket091
  Direction = (1,1,1)
  Length = 1
  Length2 = 100
  Placement = pos=(0,0,0) rot=(0.57735,0.57735,0.57735;2.0944rad)
  Profile = -> Sketch246
  Type = 0
FEATURE [Sketcher::SketchObject] Sketch247
  ExternalGeometry = -> [Pad121]
  FullyConstrained = true
  MapMode = 5
  Placement = pos=(0,0,1e-16) rot=(0.707107,0.707107,0;3.14159rad)
  Support = -> [Pad121]
  sketch-geometry (9):
    g0: LineSegment StartX=0 StartY=8.5 StartZ=0 EndX=-20 EndY=8.5 EndZ=0
    g1: ArcOfCircle CenterX=-3 CenterY=7.5 CenterZ=0 NormalX=0 NormalY=0 NormalZ=1 AngleXU=0 Radius=1 StartAngle=3.14159 EndAngle=6.28319
    g2: ArcOfCircle CenterX=-3 CenterY=9.5 CenterZ=0 NormalX=0 NormalY=0 NormalZ=1 AngleXU=0 Radius=1 StartAngle=3e-16 EndAngle=3.14159
    g3: LineSegment StartX=-2 StartY=7.5 StartZ=0 EndX=-2 EndY=9.5 EndZ=0
    g4: LineSegment StartX=-4 StartY=7.5 StartZ=0 EndX=-4 EndY=9.5 EndZ=0
    g5: ArcOfCircle CenterX=-18 CenterY=9.5 CenterZ=0 NormalX=0 NormalY=0 NormalZ=1 AngleXU=0 Radius=1 StartAngle=0 EndAngle=3.14159
    g6: ArcOfCircle CenterX=-18 CenterY=7.5 CenterZ=0 NormalX=0 NormalY=0 NormalZ=1 AngleXU=0 Radius=1 StartAngle=3.14159 EndAngle=6.28319
    g7: LineSegment StartX=-19 StartY=9.5 StartZ=0 EndX=-19 EndY=7.5 EndZ=0
    g8: LineSegment StartX=-17 StartY=9.5 StartZ=0 EndX=-17 EndY=7.5 EndZ=0
  constraints (24):
    c: PointOnObject(g0,g-2)
    c: PointOnObject(g0,g-4)
    c: Horizontal(g0)
    c: DistanceY(g0,g-3) = 8.5
    c: Tangent(g1,g4) = 1.5708
    c: Tangent(g1,g3) = -1.5708
    c: Tangent(g3,g2) = -1.5708
    c: Tangent(g4,g2) = 1.5708
    c: Vertical(g3)
    c: Equal(g1,g2)
    c: Radius(g2) = 1
    c: DistanceY(g4,g4) = 2
    c: DistanceY(g0,g2) = 1
    c: DistanceX(g2,g0) = 3
    c: Tangent(g5,g8) = 1.5708
    c: Tangent(g5,g7) = -1.5708
    c: Tangent(g7,g6) = -1.5708
    c: Tangent(g8,g6) = 1.5708
    c: Vertical(g7)
    c: Equal(g5,g6)
    c: Equal(g5,g2)
    c: Equal(g8,g4)
    c: Horizontal(g5,g2)
    c: DistanceX(g0,g5) = 2
FEATURE [PartDesign::Pad] Pad122
  BaseFeature = -> Pad121
  Direction = (1,1,1)
  Length = 1
  Length2 = 100
  Placement = pos=(0,0,0) rot=(0.57735,0.57735,0.57735;2.0944rad)
  Profile = -> Sketch247
  Type = 0
FEATURE [PartDesign::Body] Body202  label="Corner005"
  Group = -> [Sketch242,Pad120,Sketch243,Pocket089,Sketch244,Pocket090,Sketch245,Pocket091,Sketch246,Pad121,Sketch247,Pad122]
  Origin = -> Origin277
  Tip = -> Pad122
FEATURE [App::Part] Part075  label="soporte90-006"
  Group = -> [Body202]
  Origin = -> Origin278
  Placement = pos=(320,1,170) rot=(0.707107,0.707107,0;3.14159rad)
FEATURE [Sketcher::SketchObject] Sketch248
  FullyConstrained = true
  MapMode = 5
  Placement = pos=(0,0,0) rot=(0.57735,0.57735,0.57735;2.0944rad)
  Support = -> [YZ_Plane273]
  sketch-geometry (5):
    g0: LineSegment StartX=0 StartY=0 StartZ=0 EndX=0 EndY=20 EndZ=0
    g1: LineSegment StartX=0 StartY=20 StartZ=0 EndX=-3 EndY=20 EndZ=0
    g2: LineSegment StartX=-3 StartY=20 StartZ=0 EndX=-20 EndY=3 EndZ=0
    g3: LineSegment StartX=-20 StartY=3 StartZ=0 EndX=-20 EndY=0 EndZ=0
    g4: LineSegment StartX=-20 StartY=0 StartZ=0 EndX=0 EndY=0 EndZ=0
  constraints (14):
    c: Coincident(g-1,g0)
    c: PointOnObject(g0,g-2)
    c: Coincident(g0,g1)
    c: Horizontal(g1)
    c: Coincident(g1,g2)
    c: Coincident(g2,g3)
    c: PointOnObject(g3,g-1)
    c: Vertical(g3)
    c: Coincident(g3,g4)
    c: Coincident(g4,g0)
    c: DistanceY(g0,g0) = 20
    c: DistanceY(g3,g3) = 3
    c: DistanceX(g1,g1) = 3
    c: DistanceX(g4,g4) = 20
FEATURE [PartDesign::Pad] Pad123
  Direction = (1,1,1)
  Length = 17
  Length2 = 100
  Placement = pos=(0,0,0) rot=(0.57735,0.57735,0.57735;2.0944rad)
  Profile = -> Sketch248
  Type = 0
FEATURE [Sketcher::SketchObject] Sketch249
  ExternalGeometry = -> [Pad123]
  FullyConstrained = true
  MapMode = 5
  Placement = pos=(-8.8e-15,-20,4.4e-15) rot=(-0.57735,-0.57735,0.57735;4.18879rad)
  Support = -> [Pad123]
  sketch-geometry (4):
    g0: LineSegment StartX=-3 StartY=2 StartZ=0 EndX=-20 EndY=2 EndZ=0
    g1: LineSegment StartX=-20 StartY=2 StartZ=0 EndX=-20 EndY=15 EndZ=0
    g2: LineSegment StartX=-20 StartY=15 StartZ=0 EndX=-3 EndY=15 EndZ=0
    g3: LineSegment StartX=-3 StartY=15 StartZ=0 EndX=-3 EndY=2 EndZ=0
  constraints (12):
    c: Coincident(g0,g1)
    c: Coincident(g1,g2)
    c: Coincident(g2,g3)
    c: Coincident(g3,g0)
    c: Horizontal(g0)
    c: Horizontal(g2)
    c: Vertical(g1)
    c: Vertical(g3)
    c: PointOnObject(g0,g-3)
    c: DistanceY(g1,g-6) = 2
    c: DistanceY(g-6,g0) = 2
    c: PointOnObject(g1,g-6)
FEATURE [PartDesign::Pocket] Pocket092
  BaseFeature = -> Pad123
  Length = 17
  Length2 = 100
  Placement = pos=(0,0,0) rot=(0.57735,0.57735,0.57735;2.0944rad)
  Profile = -> Sketch249
  Type = 0
FEATURE [Sketcher::SketchObject] Sketch250
  ExternalGeometry = -> [Pocket092]
  FullyConstrained = true
  MapMode = 5
  Placement = pos=(-1.7e-15,-3,6e-16) rot=(-0.57735,-0.57735,0.57735;4.18879rad)
  Support = -> [Pocket092]
  sketch-geometry (5):
    g0: LineSegment StartX=-20 StartY=8.5 StartZ=0 EndX=-3 EndY=8.5 EndZ=0
    g1: ArcOfCircle CenterX=-10 CenterY=8.5 CenterZ=0 NormalX=0 NormalY=0 NormalZ=1 AngleXU=0 Radius=3 StartAngle=4.71239 EndAngle=7.85398
    g2: ArcOfCircle CenterX=-13 CenterY=8.5 CenterZ=0 NormalX=0 NormalY=0 NormalZ=1 AngleXU=0 Radius=3 StartAngle=1.5708 EndAngle=4.71239
    g3: LineSegment StartX=-10 StartY=11.5 StartZ=0 EndX=-13 EndY=11.5 EndZ=0
    g4: LineSegment StartX=-10 StartY=5.5 StartZ=0 EndX=-13 EndY=5.5 EndZ=0
  constraints (14):
    c: PointOnObject(g0,g-6)
    c: PointOnObject(g0,g-4)
    c: Horizontal(g0)
    c: DistanceY(g0,g-4) = 6.5
    c: Tangent(g1,g4) = 1.5708
    c: Tangent(g1,g3) = -1.5708
    c: Tangent(g3,g2) = -1.5708
    c: Tangent(g4,g2) = 1.5708
    c: Horizontal(g3)
    c: Equal(g1,g2)
    c: PointOnObject(g1,g0)
    c: Radius(g1) = 3
    c: DistanceX(g3,g3) = 3
    c: DistanceX(g0,g2) = 7
FEATURE [PartDesign::Pocket] Pocket093
  BaseFeature = -> Pocket092
  Length = 5
  Length2 = 100
  Placement = pos=(0,0,0) rot=(0.57735,0.57735,0.57735;2.0944rad)
  Profile = -> Sketch250
  Type = 2
FEATURE [Sketcher::SketchObject] Sketch251
  ExternalGeometry = -> [Pocket093]
  FullyConstrained = true
  MapMode = 5
  Placement = pos=(-3e-16,1.2e-15,3) rot=(0,0,-1;1.5708rad)
  Support = -> [Pocket093]
  sketch-geometry (5):
    g0: LineSegment StartX=3 StartY=8.5 StartZ=0 EndX=20 EndY=8.5 EndZ=0
    g1: ArcOfCircle CenterX=10 CenterY=8.5 CenterZ=0 NormalX=0 NormalY=0 NormalZ=1 AngleXU=0 Radius=3 StartAngle=1.5708 EndAngle=4.71239
    g2: ArcOfCircle CenterX=13 CenterY=8.5 CenterZ=0 NormalX=0 NormalY=0 NormalZ=1 AngleXU=0 Radius=3 StartAngle=4.71239 EndAngle=7.85398
    g3: LineSegment StartX=10 StartY=5.5 StartZ=0 EndX=13 EndY=5.5 EndZ=0
    g4: LineSegment StartX=10 StartY=11.5 StartZ=0 EndX=13 EndY=11.5 EndZ=0
  constraints (14):
    c: PointOnObject(g0,g-4)
    c: PointOnObject(g0,g-5)
    c: Horizontal(g0)
    c: DistanceY(g0,g-4) = 6.5
    c: Tangent(g1,g4) = 1.5708
    c: Tangent(g1,g3) = -1.5708
    c: Tangent(g3,g2) = -1.5708
    c: Tangent(g4,g2) = 1.5708
    c: Horizontal(g3)
    c: Equal(g1,g2)
    c: PointOnObject(g1,g0)
    c: Radius(g2) = 3
    c: DistanceX(g4,g4) = 3
    c: DistanceX(g2,g0) = 7
FEATURE [PartDesign::Pocket] Pocket094
  BaseFeature = -> Pocket093
  Length = 5
  Length2 = 100
  Placement = pos=(0,0,0) rot=(0.57735,0.57735,0.57735;2.0944rad)
  Profile = -> Sketch251
  Type = 2
FEATURE [Sketcher::SketchObject] Sketch252
  ExternalGeometry = -> [Pocket094]
  FullyConstrained = true
  MapMode = 5
  Placement = pos=(0,0,0) rot=(0.57735,0.57735,0.57735;4.18879rad)
  Support = -> [Pocket094]
  sketch-geometry (9):
    g0: LineSegment StartX=0 StartY=8.5 StartZ=0 EndX=20 EndY=8.5 EndZ=0
    g1: ArcOfCircle CenterX=3 CenterY=9.5 CenterZ=0 NormalX=0 NormalY=0 NormalZ=1 AngleXU=0 Radius=1 StartAngle=0 EndAngle=3.14159
    g2: ArcOfCircle CenterX=3 CenterY=7.5 CenterZ=0 NormalX=0 NormalY=0 NormalZ=1 AngleXU=0 Radius=1 StartAngle=3.14159 EndAngle=6.28319
    g3: LineSegment StartX=2 StartY=9.5 StartZ=0 EndX=2 EndY=7.5 EndZ=0
    g4: LineSegment StartX=4 StartY=9.5 StartZ=0 EndX=4 EndY=7.5 EndZ=0
    g5: ArcOfCircle CenterX=18 CenterY=9.5 CenterZ=0 NormalX=0 NormalY=0 NormalZ=1 AngleXU=0 Radius=1 StartAngle=-9e-16 EndAngle=3.14159
    g6: ArcOfCircle CenterX=18 CenterY=7.5 CenterZ=0 NormalX=0 NormalY=0 NormalZ=1 AngleXU=0 Radius=1 StartAngle=3.14159 EndAngle=6.28319
    g7: LineSegment StartX=17 StartY=9.5 StartZ=0 EndX=17 EndY=7.5 EndZ=0
    g8: LineSegment StartX=19 StartY=9.5 StartZ=0 EndX=19 EndY=7.5 EndZ=0
  constraints (24):
    c: PointOnObject(g0,g-2)
    c: PointOnObject(g0,g-5)
    c: Horizontal(g0)
    c: DistanceY(g0,g-3) = 8.5
    c: Tangent(g1,g4) = 1.5708
    c: Tangent(g1,g3) = -1.5708
    c: Tangent(g3,g2) = -1.5708
    c: Tangent(g4,g2) = 1.5708
    c: Vertical(g3)
    c: Equal(g1,g2)
    c: Tangent(g5,g8) = 1.5708
    c: Tangent(g5,g7) = -1.5708
    c: Tangent(g7,g6) = -1.5708
    c: Tangent(g8,g6) = 1.5708
    c: Vertical(g7)
    c: Equal(g5,g6)
    c: Equal(g1,g5)
    c: Equal(g4,g7)
    c: DistanceY(g4,g4) = 2
    c: Radius(g1) = 1
    c: Horizontal(g5,g1)
    c: DistanceX(g0,g1) = 3
    c: DistanceX(g5,g0) = 2
    c: DistanceY(g0,g1) = 1
FEATURE [PartDesign::Pad] Pad124
  BaseFeature = -> Pocket094
  Direction = (1,1,1)
  Length = 1
  Length2 = 100
  Placement = pos=(0,0,0) rot=(0.57735,0.57735,0.57735;2.0944rad)
  Profile = -> Sketch252
  Type = 0
FEATURE [Sketcher::SketchObject] Sketch253
  ExternalGeometry = -> [Pad124]
  FullyConstrained = true
  MapMode = 5
  Placement = pos=(0,0,1e-16) rot=(0.707107,0.707107,0;3.14159rad)
  Support = -> [Pad124]
  sketch-geometry (9):
    g0: LineSegment StartX=0 StartY=8.5 StartZ=0 EndX=-20 EndY=8.5 EndZ=0
    g1: ArcOfCircle CenterX=-3 CenterY=7.5 CenterZ=0 NormalX=0 NormalY=0 NormalZ=1 AngleXU=0 Radius=1 StartAngle=3.14159 EndAngle=6.28319
    g2: ArcOfCircle CenterX=-3 CenterY=9.5 CenterZ=0 NormalX=0 NormalY=0 NormalZ=1 AngleXU=0 Radius=1 StartAngle=3e-16 EndAngle=3.14159
    g3: LineSegment StartX=-2 StartY=7.5 StartZ=0 EndX=-2 EndY=9.5 EndZ=0
    g4: LineSegment StartX=-4 StartY=7.5 StartZ=0 EndX=-4 EndY=9.5 EndZ=0
    g5: ArcOfCircle CenterX=-18 CenterY=9.5 CenterZ=0 NormalX=0 NormalY=0 NormalZ=1 AngleXU=0 Radius=1 StartAngle=0 EndAngle=3.14159
    g6: ArcOfCircle CenterX=-18 CenterY=7.5 CenterZ=0 NormalX=0 NormalY=0 NormalZ=1 AngleXU=0 Radius=1 StartAngle=3.14159 EndAngle=6.28319
    g7: LineSegment StartX=-19 StartY=9.5 StartZ=0 EndX=-19 EndY=7.5 EndZ=0
    g8: LineSegment StartX=-17 StartY=9.5 StartZ=0 EndX=-17 EndY=7.5 EndZ=0
  constraints (24):
    c: PointOnObject(g0,g-2)
    c: PointOnObject(g0,g-4)
    c: Horizontal(g0)
    c: DistanceY(g0,g-3) = 8.5
    c: Tangent(g1,g4) = 1.5708
    c: Tangent(g1,g3) = -1.5708
    c: Tangent(g3,g2) = -1.5708
    c: Tangent(g4,g2) = 1.5708
    c: Vertical(g3)
    c: Equal(g1,g2)
    c: Radius(g2) = 1
    c: DistanceY(g4,g4) = 2
    c: DistanceY(g0,g2) = 1
    c: DistanceX(g2,g0) = 3
    c: Tangent(g5,g8) = 1.5708
    c: Tangent(g5,g7) = -1.5708
    c: Tangent(g7,g6) = -1.5708
    c: Tangent(g8,g6) = 1.5708
    c: Vertical(g7)
    c: Equal(g5,g6)
    c: Equal(g5,g2)
    c: Equal(g8,g4)
    c: Horizontal(g5,g2)
    c: DistanceX(g0,g5) = 2
FEATURE [PartDesign::Pad] Pad125
  BaseFeature = -> Pad124
  Direction = (1,1,1)
  Length = 1
  Length2 = 100
  Placement = pos=(0,0,0) rot=(0.57735,0.57735,0.57735;2.0944rad)
  Profile = -> Sketch253
  Type = 0
FEATURE [PartDesign::Body] Body203  label="Corner006"
  Group = -> [Sketch248,Pad123,Sketch249,Pocket092,Sketch250,Pocket093,Sketch251,Pocket094,Sketch252,Pad124,Sketch253,Pad125]
  Origin = -> Origin279
  Tip = -> Pad125
FEATURE [App::Part] Part076  label="soporte90-007"
  Group = -> [Body203]
  Origin = -> Origin280
  Placement = pos=(320,19,20) rot=(0,0,1;-1.5708rad)
FEATURE [Sketcher::SketchObject] Sketch254
  FullyConstrained = true
  MapMode = 5
  Placement = pos=(0,0,0) rot=(0.57735,0.57735,0.57735;2.0944rad)
  Support = -> [YZ_Plane275]
  sketch-geometry (5):
    g0: LineSegment StartX=0 StartY=0 StartZ=0 EndX=0 EndY=20 EndZ=0
    g1: LineSegment StartX=0 StartY=20 StartZ=0 EndX=-3 EndY=20 EndZ=0
    g2: LineSegment StartX=-3 StartY=20 StartZ=0 EndX=-20 EndY=3 EndZ=0
    g3: LineSegment StartX=-20 StartY=3 StartZ=0 EndX=-20 EndY=0 EndZ=0
    g4: LineSegment StartX=-20 StartY=0 StartZ=0 EndX=0 EndY=0 EndZ=0
  constraints (14):
    c: Coincident(g-1,g0)
    c: PointOnObject(g0,g-2)
    c: Coincident(g0,g1)
    c: Horizontal(g1)
    c: Coincident(g1,g2)
    c: Coincident(g2,g3)
    c: PointOnObject(g3,g-1)
    c: Vertical(g3)
    c: Coincident(g3,g4)
    c: Coincident(g4,g0)
    c: DistanceY(g0,g0) = 20
    c: DistanceY(g3,g3) = 3
    c: DistanceX(g1,g1) = 3
    c: DistanceX(g4,g4) = 20
FEATURE [PartDesign::Pad] Pad126
  Direction = (1,1,1)
  Length = 17
  Length2 = 100
  Placement = pos=(0,0,0) rot=(0.57735,0.57735,0.57735;2.0944rad)
  Profile = -> Sketch254
  Type = 0
FEATURE [Sketcher::SketchObject] Sketch255
  ExternalGeometry = -> [Pad126]
  FullyConstrained = true
  MapMode = 5
  Placement = pos=(-8.8e-15,-20,4.4e-15) rot=(-0.57735,-0.57735,0.57735;4.18879rad)
  Support = -> [Pad126]
  sketch-geometry (4):
    g0: LineSegment StartX=-3 StartY=2 StartZ=0 EndX=-20 EndY=2 EndZ=0
    g1: LineSegment StartX=-20 StartY=2 StartZ=0 EndX=-20 EndY=15 EndZ=0
    g2: LineSegment StartX=-20 StartY=15 StartZ=0 EndX=-3 EndY=15 EndZ=0
    g3: LineSegment StartX=-3 StartY=15 StartZ=0 EndX=-3 EndY=2 EndZ=0
  constraints (12):
    c: Coincident(g0,g1)
    c: Coincident(g1,g2)
    c: Coincident(g2,g3)
    c: Coincident(g3,g0)
    c: Horizontal(g0)
    c: Horizontal(g2)
    c: Vertical(g1)
    c: Vertical(g3)
    c: PointOnObject(g0,g-3)
    c: DistanceY(g1,g-6) = 2
    c: DistanceY(g-6,g0) = 2
    c: PointOnObject(g1,g-6)
FEATURE [PartDesign::Pocket] Pocket095
  BaseFeature = -> Pad126
  Length = 17
  Length2 = 100
  Placement = pos=(0,0,0) rot=(0.57735,0.57735,0.57735;2.0944rad)
  Profile = -> Sketch255
  Type = 0
FEATURE [Sketcher::SketchObject] Sketch256
  ExternalGeometry = -> [Pocket095]
  FullyConstrained = true
  MapMode = 5
  Placement = pos=(-1.7e-15,-3,6e-16) rot=(-0.57735,-0.57735,0.57735;4.18879rad)
  Support = -> [Pocket095]
  sketch-geometry (5):
    g0: LineSegment StartX=-20 StartY=8.5 StartZ=0 EndX=-3 EndY=8.5 EndZ=0
    g1: ArcOfCircle CenterX=-10 CenterY=8.5 CenterZ=0 NormalX=0 NormalY=0 NormalZ=1 AngleXU=0 Radius=3 StartAngle=4.71239 EndAngle=7.85398
    g2: ArcOfCircle CenterX=-13 CenterY=8.5 CenterZ=0 NormalX=0 NormalY=0 NormalZ=1 AngleXU=0 Radius=3 StartAngle=1.5708 EndAngle=4.71239
    g3: LineSegment StartX=-10 StartY=11.5 StartZ=0 EndX=-13 EndY=11.5 EndZ=0
    g4: LineSegment StartX=-10 StartY=5.5 StartZ=0 EndX=-13 EndY=5.5 EndZ=0
  constraints (14):
    c: PointOnObject(g0,g-6)
    c: PointOnObject(g0,g-4)
    c: Horizontal(g0)
    c: DistanceY(g0,g-4) = 6.5
    c: Tangent(g1,g4) = 1.5708
    c: Tangent(g1,g3) = -1.5708
    c: Tangent(g3,g2) = -1.5708
    c: Tangent(g4,g2) = 1.5708
    c: Horizontal(g3)
    c: Equal(g1,g2)
    c: PointOnObject(g1,g0)
    c: Radius(g1) = 3
    c: DistanceX(g3,g3) = 3
    c: DistanceX(g0,g2) = 7
FEATURE [PartDesign::Pocket] Pocket096
  BaseFeature = -> Pocket095
  Length = 5
  Length2 = 100
  Placement = pos=(0,0,0) rot=(0.57735,0.57735,0.57735;2.0944rad)
  Profile = -> Sketch256
  Type = 2
FEATURE [Sketcher::SketchObject] Sketch257
  ExternalGeometry = -> [Pocket096]
  FullyConstrained = true
  MapMode = 5
  Placement = pos=(-3e-16,1.2e-15,3) rot=(0,0,-1;1.5708rad)
  Support = -> [Pocket096]
  sketch-geometry (5):
    g0: LineSegment StartX=3 StartY=8.5 StartZ=0 EndX=20 EndY=8.5 EndZ=0
    g1: ArcOfCircle CenterX=10 CenterY=8.5 CenterZ=0 NormalX=0 NormalY=0 NormalZ=1 AngleXU=0 Radius=3 StartAngle=1.5708 EndAngle=4.71239
    g2: ArcOfCircle CenterX=13 CenterY=8.5 CenterZ=0 NormalX=0 NormalY=0 NormalZ=1 AngleXU=0 Radius=3 StartAngle=4.71239 EndAngle=7.85398
    g3: LineSegment StartX=10 StartY=5.5 StartZ=0 EndX=13 EndY=5.5 EndZ=0
    g4: LineSegment StartX=10 StartY=11.5 StartZ=0 EndX=13 EndY=11.5 EndZ=0
  constraints (14):
    c: PointOnObject(g0,g-4)
    c: PointOnObject(g0,g-5)
    c: Horizontal(g0)
    c: DistanceY(g0,g-4) = 6.5
    c: Tangent(g1,g4) = 1.5708
    c: Tangent(g1,g3) = -1.5708
    c: Tangent(g3,g2) = -1.5708
    c: Tangent(g4,g2) = 1.5708
    c: Horizontal(g3)
    c: Equal(g1,g2)
    c: PointOnObject(g1,g0)
    c: Radius(g2) = 3
    c: DistanceX(g4,g4) = 3
    c: DistanceX(g2,g0) = 7
FEATURE [PartDesign::Pocket] Pocket097
  BaseFeature = -> Pocket096
  Length = 5
  Length2 = 100
  Placement = pos=(0,0,0) rot=(0.57735,0.57735,0.57735;2.0944rad)
  Profile = -> Sketch257
  Type = 2
FEATURE [Sketcher::SketchObject] Sketch258
  ExternalGeometry = -> [Pocket097]
  FullyConstrained = true
  MapMode = 5
  Placement = pos=(0,0,0) rot=(0.57735,0.57735,0.57735;4.18879rad)
  Support = -> [Pocket097]
  sketch-geometry (9):
    g0: LineSegment StartX=0 StartY=8.5 StartZ=0 EndX=20 EndY=8.5 EndZ=0
    g1: ArcOfCircle CenterX=3 CenterY=9.5 CenterZ=0 NormalX=0 NormalY=0 NormalZ=1 AngleXU=0 Radius=1 StartAngle=0 EndAngle=3.14159
    g2: ArcOfCircle CenterX=3 CenterY=7.5 CenterZ=0 NormalX=0 NormalY=0 NormalZ=1 AngleXU=0 Radius=1 StartAngle=3.14159 EndAngle=6.28319
    g3: LineSegment StartX=2 StartY=9.5 StartZ=0 EndX=2 EndY=7.5 EndZ=0
    g4: LineSegment StartX=4 StartY=9.5 StartZ=0 EndX=4 EndY=7.5 EndZ=0
    g5: ArcOfCircle CenterX=18 CenterY=9.5 CenterZ=0 NormalX=0 NormalY=0 NormalZ=1 AngleXU=0 Radius=1 StartAngle=-9e-16 EndAngle=3.14159
    g6: ArcOfCircle CenterX=18 CenterY=7.5 CenterZ=0 NormalX=0 NormalY=0 NormalZ=1 AngleXU=0 Radius=1 StartAngle=3.14159 EndAngle=6.28319
    g7: LineSegment StartX=17 StartY=9.5 StartZ=0 EndX=17 EndY=7.5 EndZ=0
    g8: LineSegment StartX=19 StartY=9.5 StartZ=0 EndX=19 EndY=7.5 EndZ=0
  constraints (24):
    c: PointOnObject(g0,g-2)
    c: PointOnObject(g0,g-5)
    c: Horizontal(g0)
    c: DistanceY(g0,g-3) = 8.5
    c: Tangent(g1,g4) = 1.5708
    c: Tangent(g1,g3) = -1.5708
    c: Tangent(g3,g2) = -1.5708
    c: Tangent(g4,g2) = 1.5708
    c: Vertical(g3)
    c: Equal(g1,g2)
    c: Tangent(g5,g8) = 1.5708
    c: Tangent(g5,g7) = -1.5708
    c: Tangent(g7,g6) = -1.5708
    c: Tangent(g8,g6) = 1.5708
    c: Vertical(g7)
    c: Equal(g5,g6)
    c: Equal(g1,g5)
    c: Equal(g4,g7)
    c: DistanceY(g4,g4) = 2
    c: Radius(g1) = 1
    c: Horizontal(g5,g1)
    c: DistanceX(g0,g1) = 3
    c: DistanceX(g5,g0) = 2
    c: DistanceY(g0,g1) = 1
FEATURE [PartDesign::Pad] Pad127
  BaseFeature = -> Pocket097
  Direction = (1,1,1)
  Length = 1
  Length2 = 100
  Placement = pos=(0,0,0) rot=(0.57735,0.57735,0.57735;2.0944rad)
  Profile = -> Sketch258
  Type = 0
FEATURE [Sketcher::SketchObject] Sketch259
  ExternalGeometry = -> [Pad127]
  FullyConstrained = true
  MapMode = 5
  Placement = pos=(0,0,1e-16) rot=(0.707107,0.707107,0;3.14159rad)
  Support = -> [Pad127]
  sketch-geometry (9):
    g0: LineSegment StartX=0 StartY=8.5 StartZ=0 EndX=-20 EndY=8.5 EndZ=0
    g1: ArcOfCircle CenterX=-3 CenterY=7.5 CenterZ=0 NormalX=0 NormalY=0 NormalZ=1 AngleXU=0 Radius=1 StartAngle=3.14159 EndAngle=6.28319
    g2: ArcOfCircle CenterX=-3 CenterY=9.5 CenterZ=0 NormalX=0 NormalY=0 NormalZ=1 AngleXU=0 Radius=1 StartAngle=3e-16 EndAngle=3.14159
    g3: LineSegment StartX=-2 StartY=7.5 StartZ=0 EndX=-2 EndY=9.5 EndZ=0
    g4: LineSegment StartX=-4 StartY=7.5 StartZ=0 EndX=-4 EndY=9.5 EndZ=0
    g5: ArcOfCircle CenterX=-18 CenterY=9.5 CenterZ=0 NormalX=0 NormalY=0 NormalZ=1 AngleXU=0 Radius=1 StartAngle=0 EndAngle=3.14159
    g6: ArcOfCircle CenterX=-18 CenterY=7.5 CenterZ=0 NormalX=0 NormalY=0 NormalZ=1 AngleXU=0 Radius=1 StartAngle=3.14159 EndAngle=6.28319
    g7: LineSegment StartX=-19 StartY=9.5 StartZ=0 EndX=-19 EndY=7.5 EndZ=0
    g8: LineSegment StartX=-17 StartY=9.5 StartZ=0 EndX=-17 EndY=7.5 EndZ=0
  constraints (24):
    c: PointOnObject(g0,g-2)
    c: PointOnObject(g0,g-4)
    c: Horizontal(g0)
    c: DistanceY(g0,g-3) = 8.5
    c: Tangent(g1,g4) = 1.5708
    c: Tangent(g1,g3) = -1.5708
    c: Tangent(g3,g2) = -1.5708
    c: Tangent(g4,g2) = 1.5708
    c: Vertical(g3)
    c: Equal(g1,g2)
    c: Radius(g2) = 1
    c: DistanceY(g4,g4) = 2
    c: DistanceY(g0,g2) = 1
    c: DistanceX(g2,g0) = 3
    c: Tangent(g5,g8) = 1.5708
    c: Tangent(g5,g7) = -1.5708
    c: Tangent(g7,g6) = -1.5708
    c: Tangent(g8,g6) = 1.5708
    c: Vertical(g7)
    c: Equal(g5,g6)
    c: Equal(g5,g2)
    c: Equal(g8,g4)
    c: Horizontal(g5,g2)
    c: DistanceX(g0,g5) = 2
FEATURE [PartDesign::Pad] Pad128
  BaseFeature = -> Pad127
  Direction = (1,1,1)
  Length = 1
  Length2 = 100
  Placement = pos=(0,0,0) rot=(0.57735,0.57735,0.57735;2.0944rad)
  Profile = -> Sketch259
  Type = 0
FEATURE [PartDesign::Body] Body204  label="Corner007"
  Group = -> [Sketch254,Pad126,Sketch255,Pocket095,Sketch256,Pocket096,Sketch257,Pocket097,Sketch258,Pad127,Sketch259,Pad128]
  Origin = -> Origin281
  Tip = -> Pad128
FEATURE [App::Part] Part077  label="soporte90-008"
  Group = -> [Body204]
  Origin = -> Origin282
  Placement = pos=(320,321,170) rot=(0.707107,0.707107,0;3.14159rad)
FEATURE [Sketcher::SketchObject] Sketch260
  FullyConstrained = true
  MapMode = 5
  Placement = pos=(0,0,0) rot=(0.57735,0.57735,0.57735;2.0944rad)
  Support = -> [YZ_Plane277]
  sketch-geometry (5):
    g0: LineSegment StartX=0 StartY=0 StartZ=0 EndX=0 EndY=20 EndZ=0
    g1: LineSegment StartX=0 StartY=20 StartZ=0 EndX=-3 EndY=20 EndZ=0
    g2: LineSegment StartX=-3 StartY=20 StartZ=0 EndX=-20 EndY=3 EndZ=0
    g3: LineSegment StartX=-20 StartY=3 StartZ=0 EndX=-20 EndY=0 EndZ=0
    g4: LineSegment StartX=-20 StartY=0 StartZ=0 EndX=0 EndY=0 EndZ=0
  constraints (14):
    c: Coincident(g-1,g0)
    c: PointOnObject(g0,g-2)
    c: Coincident(g0,g1)
    c: Horizontal(g1)
    c: Coincident(g1,g2)
    c: Coincident(g2,g3)
    c: PointOnObject(g3,g-1)
    c: Vertical(g3)
    c: Coincident(g3,g4)
    c: Coincident(g4,g0)
    c: DistanceY(g0,g0) = 20
    c: DistanceY(g3,g3) = 3
    c: DistanceX(g1,g1) = 3
    c: DistanceX(g4,g4) = 20
FEATURE [PartDesign::Pad] Pad129
  Direction = (1,1,1)
  Length = 17
  Length2 = 100
  Placement = pos=(0,0,0) rot=(0.57735,0.57735,0.57735;2.0944rad)
  Profile = -> Sketch260
  Type = 0
FEATURE [Sketcher::SketchObject] Sketch261
  ExternalGeometry = -> [Pad129]
  FullyConstrained = true
  MapMode = 5
  Placement = pos=(-8.8e-15,-20,4.4e-15) rot=(-0.57735,-0.57735,0.57735;4.18879rad)
  Support = -> [Pad129]
  sketch-geometry (4):
    g0: LineSegment StartX=-3 StartY=2 StartZ=0 EndX=-20 EndY=2 EndZ=0
    g1: LineSegment StartX=-20 StartY=2 StartZ=0 EndX=-20 EndY=15 EndZ=0
    g2: LineSegment StartX=-20 StartY=15 StartZ=0 EndX=-3 EndY=15 EndZ=0
    g3: LineSegment StartX=-3 StartY=15 StartZ=0 EndX=-3 EndY=2 EndZ=0
  constraints (12):
    c: Coincident(g0,g1)
    c: Coincident(g1,g2)
    c: Coincident(g2,g3)
    c: Coincident(g3,g0)
    c: Horizontal(g0)
    c: Horizontal(g2)
    c: Vertical(g1)
    c: Vertical(g3)
    c: PointOnObject(g0,g-3)
    c: DistanceY(g1,g-6) = 2
    c: DistanceY(g-6,g0) = 2
    c: PointOnObject(g1,g-6)
FEATURE [PartDesign::Pocket] Pocket098
  BaseFeature = -> Pad129
  Length = 17
  Length2 = 100
  Placement = pos=(0,0,0) rot=(0.57735,0.57735,0.57735;2.0944rad)
  Profile = -> Sketch261
  Type = 0
FEATURE [Sketcher::SketchObject] Sketch262
  ExternalGeometry = -> [Pocket098]
  FullyConstrained = true
  MapMode = 5
  Placement = pos=(-1.7e-15,-3,6e-16) rot=(-0.57735,-0.57735,0.57735;4.18879rad)
  Support = -> [Pocket098]
  sketch-geometry (5):
    g0: LineSegment StartX=-20 StartY=8.5 StartZ=0 EndX=-3 EndY=8.5 EndZ=0
    g1: ArcOfCircle CenterX=-10 CenterY=8.5 CenterZ=0 NormalX=0 NormalY=0 NormalZ=1 AngleXU=0 Radius=3 StartAngle=4.71239 EndAngle=7.85398
    g2: ArcOfCircle CenterX=-13 CenterY=8.5 CenterZ=0 NormalX=0 NormalY=0 NormalZ=1 AngleXU=0 Radius=3 StartAngle=1.5708 EndAngle=4.71239
    g3: LineSegment StartX=-10 StartY=11.5 StartZ=0 EndX=-13 EndY=11.5 EndZ=0
    g4: LineSegment StartX=-10 StartY=5.5 StartZ=0 EndX=-13 EndY=5.5 EndZ=0
  constraints (14):
    c: PointOnObject(g0,g-6)
    c: PointOnObject(g0,g-4)
    c: Horizontal(g0)
    c: DistanceY(g0,g-4) = 6.5
    c: Tangent(g1,g4) = 1.5708
    c: Tangent(g1,g3) = -1.5708
    c: Tangent(g3,g2) = -1.5708
    c: Tangent(g4,g2) = 1.5708
    c: Horizontal(g3)
    c: Equal(g1,g2)
    c: PointOnObject(g1,g0)
    c: Radius(g1) = 3
    c: DistanceX(g3,g3) = 3
    c: DistanceX(g0,g2) = 7
FEATURE [PartDesign::Pocket] Pocket099
  BaseFeature = -> Pocket098
  Length = 5
  Length2 = 100
  Placement = pos=(0,0,0) rot=(0.57735,0.57735,0.57735;2.0944rad)
  Profile = -> Sketch262
  Type = 2
FEATURE [Sketcher::SketchObject] Sketch263
  ExternalGeometry = -> [Pocket099]
  FullyConstrained = true
  MapMode = 5
  Placement = pos=(-3e-16,1.2e-15,3) rot=(0,0,-1;1.5708rad)
  Support = -> [Pocket099]
  sketch-geometry (5):
    g0: LineSegment StartX=3 StartY=8.5 StartZ=0 EndX=20 EndY=8.5 EndZ=0
    g1: ArcOfCircle CenterX=10 CenterY=8.5 CenterZ=0 NormalX=0 NormalY=0 NormalZ=1 AngleXU=0 Radius=3 StartAngle=1.5708 EndAngle=4.71239
    g2: ArcOfCircle CenterX=13 CenterY=8.5 CenterZ=0 NormalX=0 NormalY=0 NormalZ=1 AngleXU=0 Radius=3 StartAngle=4.71239 EndAngle=7.85398
    g3: LineSegment StartX=10 StartY=5.5 StartZ=0 EndX=13 EndY=5.5 EndZ=0
    g4: LineSegment StartX=10 StartY=11.5 StartZ=0 EndX=13 EndY=11.5 EndZ=0
  constraints (14):
    c: PointOnObject(g0,g-4)
    c: PointOnObject(g0,g-5)
    c: Horizontal(g0)
    c: DistanceY(g0,g-4) = 6.5
    c: Tangent(g1,g4) = 1.5708
    c: Tangent(g1,g3) = -1.5708
    c: Tangent(g3,g2) = -1.5708
    c: Tangent(g4,g2) = 1.5708
    c: Horizontal(g3)
    c: Equal(g1,g2)
    c: PointOnObject(g1,g0)
    c: Radius(g2) = 3
    c: DistanceX(g4,g4) = 3
    c: DistanceX(g2,g0) = 7
FEATURE [PartDesign::Pocket] Pocket100
  BaseFeature = -> Pocket099
  Length = 5
  Length2 = 100
  Placement = pos=(0,0,0) rot=(0.57735,0.57735,0.57735;2.0944rad)
  Profile = -> Sketch263
  Type = 2
FEATURE [Sketcher::SketchObject] Sketch264
  ExternalGeometry = -> [Pocket100]
  FullyConstrained = true
  MapMode = 5
  Placement = pos=(0,0,0) rot=(0.57735,0.57735,0.57735;4.18879rad)
  Support = -> [Pocket100]
  sketch-geometry (9):
    g0: LineSegment StartX=0 StartY=8.5 StartZ=0 EndX=20 EndY=8.5 EndZ=0
    g1: ArcOfCircle CenterX=3 CenterY=9.5 CenterZ=0 NormalX=0 NormalY=0 NormalZ=1 AngleXU=0 Radius=1 StartAngle=0 EndAngle=3.14159
    g2: ArcOfCircle CenterX=3 CenterY=7.5 CenterZ=0 NormalX=0 NormalY=0 NormalZ=1 AngleXU=0 Radius=1 StartAngle=3.14159 EndAngle=6.28319
    g3: LineSegment StartX=2 StartY=9.5 StartZ=0 EndX=2 EndY=7.5 EndZ=0
    g4: LineSegment StartX=4 StartY=9.5 StartZ=0 EndX=4 EndY=7.5 EndZ=0
    g5: ArcOfCircle CenterX=18 CenterY=9.5 CenterZ=0 NormalX=0 NormalY=0 NormalZ=1 AngleXU=0 Radius=1 StartAngle=-9e-16 EndAngle=3.14159
    g6: ArcOfCircle CenterX=18 CenterY=7.5 CenterZ=0 NormalX=0 NormalY=0 NormalZ=1 AngleXU=0 Radius=1 StartAngle=3.14159 EndAngle=6.28319
    g7: LineSegment StartX=17 StartY=9.5 StartZ=0 EndX=17 EndY=7.5 EndZ=0
    g8: LineSegment StartX=19 StartY=9.5 StartZ=0 EndX=19 EndY=7.5 EndZ=0
  constraints (24):
    c: PointOnObject(g0,g-2)
    c: PointOnObject(g0,g-5)
    c: Horizontal(g0)
    c: DistanceY(g0,g-3) = 8.5
    c: Tangent(g1,g4) = 1.5708
    c: Tangent(g1,g3) = -1.5708
    c: Tangent(g3,g2) = -1.5708
    c: Tangent(g4,g2) = 1.5708
    c: Vertical(g3)
    c: Equal(g1,g2)
    c: Tangent(g5,g8) = 1.5708
    c: Tangent(g5,g7) = -1.5708
    c: Tangent(g7,g6) = -1.5708
    c: Tangent(g8,g6) = 1.5708
    c: Vertical(g7)
    c: Equal(g5,g6)
    c: Equal(g1,g5)
    c: Equal(g4,g7)
    c: DistanceY(g4,g4) = 2
    c: Radius(g1) = 1
    c: Horizontal(g5,g1)
    c: DistanceX(g0,g1) = 3
    c: DistanceX(g5,g0) = 2
    c: DistanceY(g0,g1) = 1
FEATURE [PartDesign::Pad] Pad130
  BaseFeature = -> Pocket100
  Direction = (1,1,1)
  Length = 1
  Length2 = 100
  Placement = pos=(0,0,0) rot=(0.57735,0.57735,0.57735;2.0944rad)
  Profile = -> Sketch264
  Type = 0
FEATURE [Sketcher::SketchObject] Sketch265
  ExternalGeometry = -> [Pad130]
  FullyConstrained = true
  MapMode = 5
  Placement = pos=(0,0,1e-16) rot=(0.707107,0.707107,0;3.14159rad)
  Support = -> [Pad130]
  sketch-geometry (9):
    g0: LineSegment StartX=0 StartY=8.5 StartZ=0 EndX=-20 EndY=8.5 EndZ=0
    g1: ArcOfCircle CenterX=-3 CenterY=7.5 CenterZ=0 NormalX=0 NormalY=0 NormalZ=1 AngleXU=0 Radius=1 StartAngle=3.14159 EndAngle=6.28319
    g2: ArcOfCircle CenterX=-3 CenterY=9.5 CenterZ=0 NormalX=0 NormalY=0 NormalZ=1 AngleXU=0 Radius=1 StartAngle=3e-16 EndAngle=3.14159
    g3: LineSegment StartX=-2 StartY=7.5 StartZ=0 EndX=-2 EndY=9.5 EndZ=0
    g4: LineSegment StartX=-4 StartY=7.5 StartZ=0 EndX=-4 EndY=9.5 EndZ=0
    g5: ArcOfCircle CenterX=-18 CenterY=9.5 CenterZ=0 NormalX=0 NormalY=0 NormalZ=1 AngleXU=0 Radius=1 StartAngle=0 EndAngle=3.14159
    g6: ArcOfCircle CenterX=-18 CenterY=7.5 CenterZ=0 NormalX=0 NormalY=0 NormalZ=1 AngleXU=0 Radius=1 StartAngle=3.14159 EndAngle=6.28319
    g7: LineSegment StartX=-19 StartY=9.5 StartZ=0 EndX=-19 EndY=7.5 EndZ=0
    g8: LineSegment StartX=-17 StartY=9.5 StartZ=0 EndX=-17 EndY=7.5 EndZ=0
  constraints (24):
    c: PointOnObject(g0,g-2)
    c: PointOnObject(g0,g-4)
    c: Horizontal(g0)
    c: DistanceY(g0,g-3) = 8.5
    c: Tangent(g1,g4) = 1.5708
    c: Tangent(g1,g3) = -1.5708
    c: Tangent(g3,g2) = -1.5708
    c: Tangent(g4,g2) = 1.5708
    c: Vertical(g3)
    c: Equal(g1,g2)
    c: Radius(g2) = 1
    c: DistanceY(g4,g4) = 2
    c: DistanceY(g0,g2) = 1
    c: DistanceX(g2,g0) = 3
    c: Tangent(g5,g8) = 1.5708
    c: Tangent(g5,g7) = -1.5708
    c: Tangent(g7,g6) = -1.5708
    c: Tangent(g8,g6) = 1.5708
    c: Vertical(g7)
    c: Equal(g5,g6)
    c: Equal(g5,g2)
    c: Equal(g8,g4)
    c: Horizontal(g5,g2)
    c: DistanceX(g0,g5) = 2
FEATURE [PartDesign::Pad] Pad131
  BaseFeature = -> Pad130
  Direction = (1,1,1)
  Length = 1
  Length2 = 100
  Placement = pos=(0,0,0) rot=(0.57735,0.57735,0.57735;2.0944rad)
  Profile = -> Sketch265
  Type = 0
FEATURE [PartDesign::Body] Body205  label="Corner008"
  Group = -> [Sketch260,Pad129,Sketch261,Pocket098,Sketch262,Pocket099,Sketch263,Pocket100,Sketch264,Pad130,Sketch265,Pad131]
  Origin = -> Origin283
  Tip = -> Pad131
FEATURE [App::Part] Part078  label="soporte90-009"
  Group = -> [Body205]
  Origin = -> Origin284
  Placement = pos=(2,20,70) rot=(1,0,0;3.14159rad)
FEATURE [Sketcher::SketchObject] Sketch266
  FullyConstrained = true
  MapMode = 5
  Placement = pos=(0,0,0) rot=(0.57735,0.57735,0.57735;2.0944rad)
  Support = -> [YZ_Plane279]
  sketch-geometry (5):
    g0: LineSegment StartX=0 StartY=0 StartZ=0 EndX=0 EndY=20 EndZ=0
    g1: LineSegment StartX=0 StartY=20 StartZ=0 EndX=-3 EndY=20 EndZ=0
    g2: LineSegment StartX=-3 StartY=20 StartZ=0 EndX=-20 EndY=3 EndZ=0
    g3: LineSegment StartX=-20 StartY=3 StartZ=0 EndX=-20 EndY=0 EndZ=0
    g4: LineSegment StartX=-20 StartY=0 StartZ=0 EndX=0 EndY=0 EndZ=0
  constraints (14):
    c: Coincident(g-1,g0)
    c: PointOnObject(g0,g-2)
    c: Coincident(g0,g1)
    c: Horizontal(g1)
    c: Coincident(g1,g2)
    c: Coincident(g2,g3)
    c: PointOnObject(g3,g-1)
    c: Vertical(g3)
    c: Coincident(g3,g4)
    c: Coincident(g4,g0)
    c: DistanceY(g0,g0) = 20
    c: DistanceY(g3,g3) = 3
    c: DistanceX(g1,g1) = 3
    c: DistanceX(g4,g4) = 20
FEATURE [PartDesign::Pad] Pad132
  Direction = (1,1,1)
  Length = 17
  Length2 = 100
  Placement = pos=(0,0,0) rot=(0.57735,0.57735,0.57735;2.0944rad)
  Profile = -> Sketch266
  Type = 0
FEATURE [Sketcher::SketchObject] Sketch267
  ExternalGeometry = -> [Pad132]
  FullyConstrained = true
  MapMode = 5
  Placement = pos=(-8.8e-15,-20,4.4e-15) rot=(-0.57735,-0.57735,0.57735;4.18879rad)
  Support = -> [Pad132]
  sketch-geometry (4):
    g0: LineSegment StartX=-3 StartY=2 StartZ=0 EndX=-20 EndY=2 EndZ=0
    g1: LineSegment StartX=-20 StartY=2 StartZ=0 EndX=-20 EndY=15 EndZ=0
    g2: LineSegment StartX=-20 StartY=15 StartZ=0 EndX=-3 EndY=15 EndZ=0
    g3: LineSegment StartX=-3 StartY=15 StartZ=0 EndX=-3 EndY=2 EndZ=0
  constraints (12):
    c: Coincident(g0,g1)
    c: Coincident(g1,g2)
    c: Coincident(g2,g3)
    c: Coincident(g3,g0)
    c: Horizontal(g0)
    c: Horizontal(g2)
    c: Vertical(g1)
    c: Vertical(g3)
    c: PointOnObject(g0,g-3)
    c: DistanceY(g1,g-6) = 2
    c: DistanceY(g-6,g0) = 2
    c: PointOnObject(g1,g-6)
FEATURE [PartDesign::Pocket] Pocket101
  BaseFeature = -> Pad132
  Length = 17
  Length2 = 100
  Placement = pos=(0,0,0) rot=(0.57735,0.57735,0.57735;2.0944rad)
  Profile = -> Sketch267
  Type = 0
FEATURE [Sketcher::SketchObject] Sketch268
  ExternalGeometry = -> [Pocket101]
  FullyConstrained = true
  MapMode = 5
  Placement = pos=(-1.7e-15,-3,6e-16) rot=(-0.57735,-0.57735,0.57735;4.18879rad)
  Support = -> [Pocket101]
  sketch-geometry (5):
    g0: LineSegment StartX=-20 StartY=8.5 StartZ=0 EndX=-3 EndY=8.5 EndZ=0
    g1: ArcOfCircle CenterX=-10 CenterY=8.5 CenterZ=0 NormalX=0 NormalY=0 NormalZ=1 AngleXU=0 Radius=3 StartAngle=4.71239 EndAngle=7.85398
    g2: ArcOfCircle CenterX=-13 CenterY=8.5 CenterZ=0 NormalX=0 NormalY=0 NormalZ=1 AngleXU=0 Radius=3 StartAngle=1.5708 EndAngle=4.71239
    g3: LineSegment StartX=-10 StartY=11.5 StartZ=0 EndX=-13 EndY=11.5 EndZ=0
    g4: LineSegment StartX=-10 StartY=5.5 StartZ=0 EndX=-13 EndY=5.5 EndZ=0
  constraints (14):
    c: PointOnObject(g0,g-6)
    c: PointOnObject(g0,g-4)
    c: Horizontal(g0)
    c: DistanceY(g0,g-4) = 6.5
    c: Tangent(g1,g4) = 1.5708
    c: Tangent(g1,g3) = -1.5708
    c: Tangent(g3,g2) = -1.5708
    c: Tangent(g4,g2) = 1.5708
    c: Horizontal(g3)
    c: Equal(g1,g2)
    c: PointOnObject(g1,g0)
    c: Radius(g1) = 3
    c: DistanceX(g3,g3) = 3
    c: DistanceX(g0,g2) = 7
FEATURE [PartDesign::Pocket] Pocket102
  BaseFeature = -> Pocket101
  Length = 5
  Length2 = 100
  Placement = pos=(0,0,0) rot=(0.57735,0.57735,0.57735;2.0944rad)
  Profile = -> Sketch268
  Type = 2
FEATURE [Sketcher::SketchObject] Sketch269
  ExternalGeometry = -> [Pocket102]
  FullyConstrained = true
  MapMode = 5
  Placement = pos=(-3e-16,1.2e-15,3) rot=(0,0,-1;1.5708rad)
  Support = -> [Pocket102]
  sketch-geometry (5):
    g0: LineSegment StartX=3 StartY=8.5 StartZ=0 EndX=20 EndY=8.5 EndZ=0
    g1: ArcOfCircle CenterX=10 CenterY=8.5 CenterZ=0 NormalX=0 NormalY=0 NormalZ=1 AngleXU=0 Radius=3 StartAngle=1.5708 EndAngle=4.71239
    g2: ArcOfCircle CenterX=13 CenterY=8.5 CenterZ=0 NormalX=0 NormalY=0 NormalZ=1 AngleXU=0 Radius=3 StartAngle=4.71239 EndAngle=7.85398
    g3: LineSegment StartX=10 StartY=5.5 StartZ=0 EndX=13 EndY=5.5 EndZ=0
    g4: LineSegment StartX=10 StartY=11.5 StartZ=0 EndX=13 EndY=11.5 EndZ=0
  constraints (14):
    c: PointOnObject(g0,g-4)
    c: PointOnObject(g0,g-5)
    c: Horizontal(g0)
    c: DistanceY(g0,g-4) = 6.5
    c: Tangent(g1,g4) = 1.5708
    c: Tangent(g1,g3) = -1.5708
    c: Tangent(g3,g2) = -1.5708
    c: Tangent(g4,g2) = 1.5708
    c: Horizontal(g3)
    c: Equal(g1,g2)
    c: PointOnObject(g1,g0)
    c: Radius(g2) = 3
    c: DistanceX(g4,g4) = 3
    c: DistanceX(g2,g0) = 7
FEATURE [PartDesign::Pocket] Pocket103
  BaseFeature = -> Pocket102
  Length = 5
  Length2 = 100
  Placement = pos=(0,0,0) rot=(0.57735,0.57735,0.57735;2.0944rad)
  Profile = -> Sketch269
  Type = 2
FEATURE [Sketcher::SketchObject] Sketch270
  ExternalGeometry = -> [Pocket103]
  FullyConstrained = true
  MapMode = 5
  Placement = pos=(0,0,0) rot=(0.57735,0.57735,0.57735;4.18879rad)
  Support = -> [Pocket103]
  sketch-geometry (9):
    g0: LineSegment StartX=0 StartY=8.5 StartZ=0 EndX=20 EndY=8.5 EndZ=0
    g1: ArcOfCircle CenterX=3 CenterY=9.5 CenterZ=0 NormalX=0 NormalY=0 NormalZ=1 AngleXU=0 Radius=1 StartAngle=0 EndAngle=3.14159
    g2: ArcOfCircle CenterX=3 CenterY=7.5 CenterZ=0 NormalX=0 NormalY=0 NormalZ=1 AngleXU=0 Radius=1 StartAngle=3.14159 EndAngle=6.28319
    g3: LineSegment StartX=2 StartY=9.5 StartZ=0 EndX=2 EndY=7.5 EndZ=0
    g4: LineSegment StartX=4 StartY=9.5 StartZ=0 EndX=4 EndY=7.5 EndZ=0
    g5: ArcOfCircle CenterX=18 CenterY=9.5 CenterZ=0 NormalX=0 NormalY=0 NormalZ=1 AngleXU=0 Radius=1 StartAngle=-9e-16 EndAngle=3.14159
    g6: ArcOfCircle CenterX=18 CenterY=7.5 CenterZ=0 NormalX=0 NormalY=0 NormalZ=1 AngleXU=0 Radius=1 StartAngle=3.14159 EndAngle=6.28319
    g7: LineSegment StartX=17 StartY=9.5 StartZ=0 EndX=17 EndY=7.5 EndZ=0
    g8: LineSegment StartX=19 StartY=9.5 StartZ=0 EndX=19 EndY=7.5 EndZ=0
  constraints (24):
    c: PointOnObject(g0,g-2)
    c: PointOnObject(g0,g-5)
    c: Horizontal(g0)
    c: DistanceY(g0,g-3) = 8.5
    c: Tangent(g1,g4) = 1.5708
    c: Tangent(g1,g3) = -1.5708
    c: Tangent(g3,g2) = -1.5708
    c: Tangent(g4,g2) = 1.5708
    c: Vertical(g3)
    c: Equal(g1,g2)
    c: Tangent(g5,g8) = 1.5708
    c: Tangent(g5,g7) = -1.5708
    c: Tangent(g7,g6) = -1.5708
    c: Tangent(g8,g6) = 1.5708
    c: Vertical(g7)
    c: Equal(g5,g6)
    c: Equal(g1,g5)
    c: Equal(g4,g7)
    c: DistanceY(g4,g4) = 2
    c: Radius(g1) = 1
    c: Horizontal(g5,g1)
    c: DistanceX(g0,g1) = 3
    c: DistanceX(g5,g0) = 2
    c: DistanceY(g0,g1) = 1
FEATURE [PartDesign::Pad] Pad133
  BaseFeature = -> Pocket103
  Direction = (1,1,1)
  Length = 1
  Length2 = 100
  Placement = pos=(0,0,0) rot=(0.57735,0.57735,0.57735;2.0944rad)
  Profile = -> Sketch270
  Type = 0
FEATURE [Sketcher::SketchObject] Sketch271
  ExternalGeometry = -> [Pad133]
  FullyConstrained = true
  MapMode = 5
  Placement = pos=(0,0,1e-16) rot=(0.707107,0.707107,0;3.14159rad)
  Support = -> [Pad133]
  sketch-geometry (9):
    g0: LineSegment StartX=0 StartY=8.5 StartZ=0 EndX=-20 EndY=8.5 EndZ=0
    g1: ArcOfCircle CenterX=-3 CenterY=7.5 CenterZ=0 NormalX=0 NormalY=0 NormalZ=1 AngleXU=0 Radius=1 StartAngle=3.14159 EndAngle=6.28319
    g2: ArcOfCircle CenterX=-3 CenterY=9.5 CenterZ=0 NormalX=0 NormalY=0 NormalZ=1 AngleXU=0 Radius=1 StartAngle=3e-16 EndAngle=3.14159
    g3: LineSegment StartX=-2 StartY=7.5 StartZ=0 EndX=-2 EndY=9.5 EndZ=0
    g4: LineSegment StartX=-4 StartY=7.5 StartZ=0 EndX=-4 EndY=9.5 EndZ=0
    g5: ArcOfCircle CenterX=-18 CenterY=9.5 CenterZ=0 NormalX=0 NormalY=0 NormalZ=1 AngleXU=0 Radius=1 StartAngle=0 EndAngle=3.14159
    g6: ArcOfCircle CenterX=-18 CenterY=7.5 CenterZ=0 NormalX=0 NormalY=0 NormalZ=1 AngleXU=0 Radius=1 StartAngle=3.14159 EndAngle=6.28319
    g7: LineSegment StartX=-19 StartY=9.5 StartZ=0 EndX=-19 EndY=7.5 EndZ=0
    g8: LineSegment StartX=-17 StartY=9.5 StartZ=0 EndX=-17 EndY=7.5 EndZ=0
  constraints (24):
    c: PointOnObject(g0,g-2)
    c: PointOnObject(g0,g-4)
    c: Horizontal(g0)
    c: DistanceY(g0,g-3) = 8.5
    c: Tangent(g1,g4) = 1.5708
    c: Tangent(g1,g3) = -1.5708
    c: Tangent(g3,g2) = -1.5708
    c: Tangent(g4,g2) = 1.5708
    c: Vertical(g3)
    c: Equal(g1,g2)
    c: Radius(g2) = 1
    c: DistanceY(g4,g4) = 2
    c: DistanceY(g0,g2) = 1
    c: DistanceX(g2,g0) = 3
    c: Tangent(g5,g8) = 1.5708
    c: Tangent(g5,g7) = -1.5708
    c: Tangent(g7,g6) = -1.5708
    c: Tangent(g8,g6) = 1.5708
    c: Vertical(g7)
    c: Equal(g5,g6)
    c: Equal(g5,g2)
    c: Equal(g8,g4)
    c: Horizontal(g5,g2)
    c: DistanceX(g0,g5) = 2
FEATURE [PartDesign::Pad] Pad134
  BaseFeature = -> Pad133
  Direction = (1,1,1)
  Length = 1
  Length2 = 100
  Placement = pos=(0,0,0) rot=(0.57735,0.57735,0.57735;2.0944rad)
  Profile = -> Sketch271
  Type = 0
FEATURE [PartDesign::Body] Body206  label="Corner009"
  Group = -> [Sketch266,Pad132,Sketch267,Pocket101,Sketch268,Pocket102,Sketch269,Pocket103,Sketch270,Pad133,Sketch271,Pad134]
  Origin = -> Origin285
  Tip = -> Pad134
FEATURE [App::Part] Part079  label="soporte90-010"
  Group = -> [Body206]
  Origin = -> Origin286
  Placement = pos=(2,320,70) rot=(1,0,0;1.5708rad)
FEATURE [Sketcher::SketchObject] Sketch272
  FullyConstrained = true
  MapMode = 5
  Placement = pos=(0,0,0) rot=(0.57735,0.57735,0.57735;2.0944rad)
  Support = -> [YZ_Plane281]
  sketch-geometry (5):
    g0: LineSegment StartX=0 StartY=0 StartZ=0 EndX=0 EndY=20 EndZ=0
    g1: LineSegment StartX=0 StartY=20 StartZ=0 EndX=-3 EndY=20 EndZ=0
    g2: LineSegment StartX=-3 StartY=20 StartZ=0 EndX=-20 EndY=3 EndZ=0
    g3: LineSegment StartX=-20 StartY=3 StartZ=0 EndX=-20 EndY=0 EndZ=0
    g4: LineSegment StartX=-20 StartY=0 StartZ=0 EndX=0 EndY=0 EndZ=0
  constraints (14):
    c: Coincident(g-1,g0)
    c: PointOnObject(g0,g-2)
    c: Coincident(g0,g1)
    c: Horizontal(g1)
    c: Coincident(g1,g2)
    c: Coincident(g2,g3)
    c: PointOnObject(g3,g-1)
    c: Vertical(g3)
    c: Coincident(g3,g4)
    c: Coincident(g4,g0)
    c: DistanceY(g0,g0) = 20
    c: DistanceY(g3,g3) = 3
    c: DistanceX(g1,g1) = 3
    c: DistanceX(g4,g4) = 20
FEATURE [PartDesign::Pad] Pad135
  Direction = (1,1,1)
  Length = 17
  Length2 = 100
  Placement = pos=(0,0,0) rot=(0.57735,0.57735,0.57735;2.0944rad)
  Profile = -> Sketch272
  Type = 0
FEATURE [Sketcher::SketchObject] Sketch273
  ExternalGeometry = -> [Pad135]
  FullyConstrained = true
  MapMode = 5
  Placement = pos=(-8.8e-15,-20,4.4e-15) rot=(-0.57735,-0.57735,0.57735;4.18879rad)
  Support = -> [Pad135]
  sketch-geometry (4):
    g0: LineSegment StartX=-3 StartY=2 StartZ=0 EndX=-20 EndY=2 EndZ=0
    g1: LineSegment StartX=-20 StartY=2 StartZ=0 EndX=-20 EndY=15 EndZ=0
    g2: LineSegment StartX=-20 StartY=15 StartZ=0 EndX=-3 EndY=15 EndZ=0
    g3: LineSegment StartX=-3 StartY=15 StartZ=0 EndX=-3 EndY=2 EndZ=0
  constraints (12):
    c: Coincident(g0,g1)
    c: Coincident(g1,g2)
    c: Coincident(g2,g3)
    c: Coincident(g3,g0)
    c: Horizontal(g0)
    c: Horizontal(g2)
    c: Vertical(g1)
    c: Vertical(g3)
    c: PointOnObject(g0,g-3)
    c: DistanceY(g1,g-6) = 2
    c: DistanceY(g-6,g0) = 2
    c: PointOnObject(g1,g-6)
FEATURE [PartDesign::Pocket] Pocket104
  BaseFeature = -> Pad135
  Length = 17
  Length2 = 100
  Placement = pos=(0,0,0) rot=(0.57735,0.57735,0.57735;2.0944rad)
  Profile = -> Sketch273
  Type = 0
FEATURE [Sketcher::SketchObject] Sketch274
  ExternalGeometry = -> [Pocket104]
  FullyConstrained = true
  MapMode = 5
  Placement = pos=(-1.7e-15,-3,6e-16) rot=(-0.57735,-0.57735,0.57735;4.18879rad)
  Support = -> [Pocket104]
  sketch-geometry (5):
    g0: LineSegment StartX=-20 StartY=8.5 StartZ=0 EndX=-3 EndY=8.5 EndZ=0
    g1: ArcOfCircle CenterX=-10 CenterY=8.5 CenterZ=0 NormalX=0 NormalY=0 NormalZ=1 AngleXU=0 Radius=3 StartAngle=4.71239 EndAngle=7.85398
    g2: ArcOfCircle CenterX=-13 CenterY=8.5 CenterZ=0 NormalX=0 NormalY=0 NormalZ=1 AngleXU=0 Radius=3 StartAngle=1.5708 EndAngle=4.71239
    g3: LineSegment StartX=-10 StartY=11.5 StartZ=0 EndX=-13 EndY=11.5 EndZ=0
    g4: LineSegment StartX=-10 StartY=5.5 StartZ=0 EndX=-13 EndY=5.5 EndZ=0
  constraints (14):
    c: PointOnObject(g0,g-6)
    c: PointOnObject(g0,g-4)
    c: Horizontal(g0)
    c: DistanceY(g0,g-4) = 6.5
    c: Tangent(g1,g4) = 1.5708
    c: Tangent(g1,g3) = -1.5708
    c: Tangent(g3,g2) = -1.5708
    c: Tangent(g4,g2) = 1.5708
    c: Horizontal(g3)
    c: Equal(g1,g2)
    c: PointOnObject(g1,g0)
    c: Radius(g1) = 3
    c: DistanceX(g3,g3) = 3
    c: DistanceX(g0,g2) = 7
FEATURE [PartDesign::Pocket] Pocket105
  BaseFeature = -> Pocket104
  Length = 5
  Length2 = 100
  Placement = pos=(0,0,0) rot=(0.57735,0.57735,0.57735;2.0944rad)
  Profile = -> Sketch274
  Type = 2
FEATURE [Sketcher::SketchObject] Sketch275
  ExternalGeometry = -> [Pocket105]
  FullyConstrained = true
  MapMode = 5
  Placement = pos=(-3e-16,1.2e-15,3) rot=(0,0,-1;1.5708rad)
  Support = -> [Pocket105]
  sketch-geometry (5):
    g0: LineSegment StartX=3 StartY=8.5 StartZ=0 EndX=20 EndY=8.5 EndZ=0
    g1: ArcOfCircle CenterX=10 CenterY=8.5 CenterZ=0 NormalX=0 NormalY=0 NormalZ=1 AngleXU=0 Radius=3 StartAngle=1.5708 EndAngle=4.71239
    g2: ArcOfCircle CenterX=13 CenterY=8.5 CenterZ=0 NormalX=0 NormalY=0 NormalZ=1 AngleXU=0 Radius=3 StartAngle=4.71239 EndAngle=7.85398
    g3: LineSegment StartX=10 StartY=5.5 StartZ=0 EndX=13 EndY=5.5 EndZ=0
    g4: LineSegment StartX=10 StartY=11.5 StartZ=0 EndX=13 EndY=11.5 EndZ=0
  constraints (14):
    c: PointOnObject(g0,g-4)
    c: PointOnObject(g0,g-5)
    c: Horizontal(g0)
    c: DistanceY(g0,g-4) = 6.5
    c: Tangent(g1,g4) = 1.5708
    c: Tangent(g1,g3) = -1.5708
    c: Tangent(g3,g2) = -1.5708
    c: Tangent(g4,g2) = 1.5708
    c: Horizontal(g3)
    c: Equal(g1,g2)
    c: PointOnObject(g1,g0)
    c: Radius(g2) = 3
    c: DistanceX(g4,g4) = 3
    c: DistanceX(g2,g0) = 7
FEATURE [PartDesign::Pocket] Pocket106
  BaseFeature = -> Pocket105
  Length = 5
  Length2 = 100
  Placement = pos=(0,0,0) rot=(0.57735,0.57735,0.57735;2.0944rad)
  Profile = -> Sketch275
  Type = 2
FEATURE [Sketcher::SketchObject] Sketch276
  ExternalGeometry = -> [Pocket106]
  FullyConstrained = true
  MapMode = 5
  Placement = pos=(0,0,0) rot=(0.57735,0.57735,0.57735;4.18879rad)
  Support = -> [Pocket106]
  sketch-geometry (9):
    g0: LineSegment StartX=0 StartY=8.5 StartZ=0 EndX=20 EndY=8.5 EndZ=0
    g1: ArcOfCircle CenterX=3 CenterY=9.5 CenterZ=0 NormalX=0 NormalY=0 NormalZ=1 AngleXU=0 Radius=1 StartAngle=0 EndAngle=3.14159
    g2: ArcOfCircle CenterX=3 CenterY=7.5 CenterZ=0 NormalX=0 NormalY=0 NormalZ=1 AngleXU=0 Radius=1 StartAngle=3.14159 EndAngle=6.28319
    g3: LineSegment StartX=2 StartY=9.5 StartZ=0 EndX=2 EndY=7.5 EndZ=0
    g4: LineSegment StartX=4 StartY=9.5 StartZ=0 EndX=4 EndY=7.5 EndZ=0
    g5: ArcOfCircle CenterX=18 CenterY=9.5 CenterZ=0 NormalX=0 NormalY=0 NormalZ=1 AngleXU=0 Radius=1 StartAngle=-9e-16 EndAngle=3.14159
    g6: ArcOfCircle CenterX=18 CenterY=7.5 CenterZ=0 NormalX=0 NormalY=0 NormalZ=1 AngleXU=0 Radius=1 StartAngle=3.14159 EndAngle=6.28319
    g7: LineSegment StartX=17 StartY=9.5 StartZ=0 EndX=17 EndY=7.5 EndZ=0
    g8: LineSegment StartX=19 StartY=9.5 StartZ=0 EndX=19 EndY=7.5 EndZ=0
  constraints (24):
    c: PointOnObject(g0,g-2)
    c: PointOnObject(g0,g-5)
    c: Horizontal(g0)
    c: DistanceY(g0,g-3) = 8.5
    c: Tangent(g1,g4) = 1.5708
    c: Tangent(g1,g3) = -1.5708
    c: Tangent(g3,g2) = -1.5708
    c: Tangent(g4,g2) = 1.5708
    c: Vertical(g3)
    c: Equal(g1,g2)
    c: Tangent(g5,g8) = 1.5708
    c: Tangent(g5,g7) = -1.5708
    c: Tangent(g7,g6) = -1.5708
    c: Tangent(g8,g6) = 1.5708
    c: Vertical(g7)
    c: Equal(g5,g6)
    c: Equal(g1,g5)
    c: Equal(g4,g7)
    c: DistanceY(g4,g4) = 2
    c: Radius(g1) = 1
    c: Horizontal(g5,g1)
    c: DistanceX(g0,g1) = 3
    c: DistanceX(g5,g0) = 2
    c: DistanceY(g0,g1) = 1
FEATURE [PartDesign::Pad] Pad136
  BaseFeature = -> Pocket106
  Direction = (1,1,1)
  Length = 1
  Length2 = 100
  Placement = pos=(0,0,0) rot=(0.57735,0.57735,0.57735;2.0944rad)
  Profile = -> Sketch276
  Type = 0
FEATURE [Sketcher::SketchObject] Sketch277
  ExternalGeometry = -> [Pad136]
  FullyConstrained = true
  MapMode = 5
  Placement = pos=(0,0,1e-16) rot=(0.707107,0.707107,0;3.14159rad)
  Support = -> [Pad136]
  sketch-geometry (9):
    g0: LineSegment StartX=0 StartY=8.5 StartZ=0 EndX=-20 EndY=8.5 EndZ=0
    g1: ArcOfCircle CenterX=-3 CenterY=7.5 CenterZ=0 NormalX=0 NormalY=0 NormalZ=1 AngleXU=0 Radius=1 StartAngle=3.14159 EndAngle=6.28319
    g2: ArcOfCircle CenterX=-3 CenterY=9.5 CenterZ=0 NormalX=0 NormalY=0 NormalZ=1 AngleXU=0 Radius=1 StartAngle=3e-16 EndAngle=3.14159
    g3: LineSegment StartX=-2 StartY=7.5 StartZ=0 EndX=-2 EndY=9.5 EndZ=0
    g4: LineSegment StartX=-4 StartY=7.5 StartZ=0 EndX=-4 EndY=9.5 EndZ=0
    g5: ArcOfCircle CenterX=-18 CenterY=9.5 CenterZ=0 NormalX=0 NormalY=0 NormalZ=1 AngleXU=0 Radius=1 StartAngle=0 EndAngle=3.14159
    g6: ArcOfCircle CenterX=-18 CenterY=7.5 CenterZ=0 NormalX=0 NormalY=0 NormalZ=1 AngleXU=0 Radius=1 StartAngle=3.14159 EndAngle=6.28319
    g7: LineSegment StartX=-19 StartY=9.5 StartZ=0 EndX=-19 EndY=7.5 EndZ=0
    g8: LineSegment StartX=-17 StartY=9.5 StartZ=0 EndX=-17 EndY=7.5 EndZ=0
  constraints (24):
    c: PointOnObject(g0,g-2)
    c: PointOnObject(g0,g-4)
    c: Horizontal(g0)
    c: DistanceY(g0,g-3) = 8.5
    c: Tangent(g1,g4) = 1.5708
    c: Tangent(g1,g3) = -1.5708
    c: Tangent(g3,g2) = -1.5708
    c: Tangent(g4,g2) = 1.5708
    c: Vertical(g3)
    c: Equal(g1,g2)
    c: Radius(g2) = 1
    c: DistanceY(g4,g4) = 2
    c: DistanceY(g0,g2) = 1
    c: DistanceX(g2,g0) = 3
    c: Tangent(g5,g8) = 1.5708
    c: Tangent(g5,g7) = -1.5708
    c: Tangent(g7,g6) = -1.5708
    c: Tangent(g8,g6) = 1.5708
    c: Vertical(g7)
    c: Equal(g5,g6)
    c: Equal(g5,g2)
    c: Equal(g8,g4)
    c: Horizontal(g5,g2)
    c: DistanceX(g0,g5) = 2
FEATURE [PartDesign::Pad] Pad137
  BaseFeature = -> Pad136
  Direction = (1,1,1)
  Length = 1
  Length2 = 100
  Placement = pos=(0,0,0) rot=(0.57735,0.57735,0.57735;2.0944rad)
  Profile = -> Sketch277
  Type = 0
FEATURE [PartDesign::Body] Body207  label="Corner010"
  Group = -> [Sketch272,Pad135,Sketch273,Pocket104,Sketch274,Pocket105,Sketch275,Pocket106,Sketch276,Pad136,Sketch277,Pad137]
  Origin = -> Origin287
  Tip = -> Pad137
FEATURE [App::Part] Part080  label="soporte90-011"
  Group = -> [Body207]
  Origin = -> Origin288
  Placement = pos=(322,320,70) rot=(1,0,0;1.5708rad)
FEATURE [Sketcher::SketchObject] Sketch278
  FullyConstrained = true
  MapMode = 5
  Placement = pos=(0,0,0) rot=(0.57735,0.57735,0.57735;2.0944rad)
  Support = -> [YZ_Plane283]
  sketch-geometry (5):
    g0: LineSegment StartX=0 StartY=0 StartZ=0 EndX=0 EndY=20 EndZ=0
    g1: LineSegment StartX=0 StartY=20 StartZ=0 EndX=-3 EndY=20 EndZ=0
    g2: LineSegment StartX=-3 StartY=20 StartZ=0 EndX=-20 EndY=3 EndZ=0
    g3: LineSegment StartX=-20 StartY=3 StartZ=0 EndX=-20 EndY=0 EndZ=0
    g4: LineSegment StartX=-20 StartY=0 StartZ=0 EndX=0 EndY=0 EndZ=0
  constraints (14):
    c: Coincident(g-1,g0)
    c: PointOnObject(g0,g-2)
    c: Coincident(g0,g1)
    c: Horizontal(g1)
    c: Coincident(g1,g2)
    c: Coincident(g2,g3)
    c: PointOnObject(g3,g-1)
    c: Vertical(g3)
    c: Coincident(g3,g4)
    c: Coincident(g4,g0)
    c: DistanceY(g0,g0) = 20
    c: DistanceY(g3,g3) = 3
    c: DistanceX(g1,g1) = 3
    c: DistanceX(g4,g4) = 20
FEATURE [PartDesign::Pad] Pad138
  Direction = (1,1,1)
  Length = 17
  Length2 = 100
  Placement = pos=(0,0,0) rot=(0.57735,0.57735,0.57735;2.0944rad)
  Profile = -> Sketch278
  Type = 0
FEATURE [Sketcher::SketchObject] Sketch279
  ExternalGeometry = -> [Pad138]
  FullyConstrained = true
  MapMode = 5
  Placement = pos=(-8.8e-15,-20,4.4e-15) rot=(-0.57735,-0.57735,0.57735;4.18879rad)
  Support = -> [Pad138]
  sketch-geometry (4):
    g0: LineSegment StartX=-3 StartY=2 StartZ=0 EndX=-20 EndY=2 EndZ=0
    g1: LineSegment StartX=-20 StartY=2 StartZ=0 EndX=-20 EndY=15 EndZ=0
    g2: LineSegment StartX=-20 StartY=15 StartZ=0 EndX=-3 EndY=15 EndZ=0
    g3: LineSegment StartX=-3 StartY=15 StartZ=0 EndX=-3 EndY=2 EndZ=0
  constraints (12):
    c: Coincident(g0,g1)
    c: Coincident(g1,g2)
    c: Coincident(g2,g3)
    c: Coincident(g3,g0)
    c: Horizontal(g0)
    c: Horizontal(g2)
    c: Vertical(g1)
    c: Vertical(g3)
    c: PointOnObject(g0,g-3)
    c: DistanceY(g1,g-6) = 2
    c: DistanceY(g-6,g0) = 2
    c: PointOnObject(g1,g-6)
FEATURE [PartDesign::Pocket] Pocket107
  BaseFeature = -> Pad138
  Length = 17
  Length2 = 100
  Placement = pos=(0,0,0) rot=(0.57735,0.57735,0.57735;2.0944rad)
  Profile = -> Sketch279
  Type = 0
FEATURE [Sketcher::SketchObject] Sketch280
  ExternalGeometry = -> [Pocket107]
  FullyConstrained = true
  MapMode = 5
  Placement = pos=(-1.7e-15,-3,6e-16) rot=(-0.57735,-0.57735,0.57735;4.18879rad)
  Support = -> [Pocket107]
  sketch-geometry (5):
    g0: LineSegment StartX=-20 StartY=8.5 StartZ=0 EndX=-3 EndY=8.5 EndZ=0
    g1: ArcOfCircle CenterX=-10 CenterY=8.5 CenterZ=0 NormalX=0 NormalY=0 NormalZ=1 AngleXU=0 Radius=3 StartAngle=4.71239 EndAngle=7.85398
    g2: ArcOfCircle CenterX=-13 CenterY=8.5 CenterZ=0 NormalX=0 NormalY=0 NormalZ=1 AngleXU=0 Radius=3 StartAngle=1.5708 EndAngle=4.71239
    g3: LineSegment StartX=-10 StartY=11.5 StartZ=0 EndX=-13 EndY=11.5 EndZ=0
    g4: LineSegment StartX=-10 StartY=5.5 StartZ=0 EndX=-13 EndY=5.5 EndZ=0
  constraints (14):
    c: PointOnObject(g0,g-6)
    c: PointOnObject(g0,g-4)
    c: Horizontal(g0)
    c: DistanceY(g0,g-4) = 6.5
    c: Tangent(g1,g4) = 1.5708
    c: Tangent(g1,g3) = -1.5708
    c: Tangent(g3,g2) = -1.5708
    c: Tangent(g4,g2) = 1.5708
    c: Horizontal(g3)
    c: Equal(g1,g2)
    c: PointOnObject(g1,g0)
    c: Radius(g1) = 3
    c: DistanceX(g3,g3) = 3
    c: DistanceX(g0,g2) = 7
FEATURE [PartDesign::Pocket] Pocket108
  BaseFeature = -> Pocket107
  Length = 5
  Length2 = 100
  Placement = pos=(0,0,0) rot=(0.57735,0.57735,0.57735;2.0944rad)
  Profile = -> Sketch280
  Type = 2
FEATURE [Sketcher::SketchObject] Sketch281
  ExternalGeometry = -> [Pocket108]
  FullyConstrained = true
  MapMode = 5
  Placement = pos=(-3e-16,1.2e-15,3) rot=(0,0,-1;1.5708rad)
  Support = -> [Pocket108]
  sketch-geometry (5):
    g0: LineSegment StartX=3 StartY=8.5 StartZ=0 EndX=20 EndY=8.5 EndZ=0
    g1: ArcOfCircle CenterX=10 CenterY=8.5 CenterZ=0 NormalX=0 NormalY=0 NormalZ=1 AngleXU=0 Radius=3 StartAngle=1.5708 EndAngle=4.71239
    g2: ArcOfCircle CenterX=13 CenterY=8.5 CenterZ=0 NormalX=0 NormalY=0 NormalZ=1 AngleXU=0 Radius=3 StartAngle=4.71239 EndAngle=7.85398
    g3: LineSegment StartX=10 StartY=5.5 StartZ=0 EndX=13 EndY=5.5 EndZ=0
    g4: LineSegment StartX=10 StartY=11.5 StartZ=0 EndX=13 EndY=11.5 EndZ=0
  constraints (14):
    c: PointOnObject(g0,g-4)
    c: PointOnObject(g0,g-5)
    c: Horizontal(g0)
    c: DistanceY(g0,g-4) = 6.5
    c: Tangent(g1,g4) = 1.5708
    c: Tangent(g1,g3) = -1.5708
    c: Tangent(g3,g2) = -1.5708
    c: Tangent(g4,g2) = 1.5708
    c: Horizontal(g3)
    c: Equal(g1,g2)
    c: PointOnObject(g1,g0)
    c: Radius(g2) = 3
    c: DistanceX(g4,g4) = 3
    c: DistanceX(g2,g0) = 7
FEATURE [PartDesign::Pocket] Pocket109
  BaseFeature = -> Pocket108
  Length = 5
  Length2 = 100
  Placement = pos=(0,0,0) rot=(0.57735,0.57735,0.57735;2.0944rad)
  Profile = -> Sketch281
  Type = 2
FEATURE [Sketcher::SketchObject] Sketch282
  ExternalGeometry = -> [Pocket109]
  FullyConstrained = true
  MapMode = 5
  Placement = pos=(0,0,0) rot=(0.57735,0.57735,0.57735;4.18879rad)
  Support = -> [Pocket109]
  sketch-geometry (9):
    g0: LineSegment StartX=0 StartY=8.5 StartZ=0 EndX=20 EndY=8.5 EndZ=0
    g1: ArcOfCircle CenterX=3 CenterY=9.5 CenterZ=0 NormalX=0 NormalY=0 NormalZ=1 AngleXU=0 Radius=1 StartAngle=0 EndAngle=3.14159
    g2: ArcOfCircle CenterX=3 CenterY=7.5 CenterZ=0 NormalX=0 NormalY=0 NormalZ=1 AngleXU=0 Radius=1 StartAngle=3.14159 EndAngle=6.28319
    g3: LineSegment StartX=2 StartY=9.5 StartZ=0 EndX=2 EndY=7.5 EndZ=0
    g4: LineSegment StartX=4 StartY=9.5 StartZ=0 EndX=4 EndY=7.5 EndZ=0
    g5: ArcOfCircle CenterX=18 CenterY=9.5 CenterZ=0 NormalX=0 NormalY=0 NormalZ=1 AngleXU=0 Radius=1 StartAngle=-9e-16 EndAngle=3.14159
    g6: ArcOfCircle CenterX=18 CenterY=7.5 CenterZ=0 NormalX=0 NormalY=0 NormalZ=1 AngleXU=0 Radius=1 StartAngle=3.14159 EndAngle=6.28319
    g7: LineSegment StartX=17 StartY=9.5 StartZ=0 EndX=17 EndY=7.5 EndZ=0
    g8: LineSegment StartX=19 StartY=9.5 StartZ=0 EndX=19 EndY=7.5 EndZ=0
  constraints (24):
    c: PointOnObject(g0,g-2)
    c: PointOnObject(g0,g-5)
    c: Horizontal(g0)
    c: DistanceY(g0,g-3) = 8.5
    c: Tangent(g1,g4) = 1.5708
    c: Tangent(g1,g3) = -1.5708
    c: Tangent(g3,g2) = -1.5708
    c: Tangent(g4,g2) = 1.5708
    c: Vertical(g3)
    c: Equal(g1,g2)
    c: Tangent(g5,g8) = 1.5708
    c: Tangent(g5,g7) = -1.5708
    c: Tangent(g7,g6) = -1.5708
    c: Tangent(g8,g6) = 1.5708
    c: Vertical(g7)
    c: Equal(g5,g6)
    c: Equal(g1,g5)
    c: Equal(g4,g7)
    c: DistanceY(g4,g4) = 2
    c: Radius(g1) = 1
    c: Horizontal(g5,g1)
    c: DistanceX(g0,g1) = 3
    c: DistanceX(g5,g0) = 2
    c: DistanceY(g0,g1) = 1
FEATURE [PartDesign::Pad] Pad139
  BaseFeature = -> Pocket109
  Direction = (1,1,1)
  Length = 1
  Length2 = 100
  Placement = pos=(0,0,0) rot=(0.57735,0.57735,0.57735;2.0944rad)
  Profile = -> Sketch282
  Type = 0
FEATURE [Sketcher::SketchObject] Sketch283
  ExternalGeometry = -> [Pad139]
  FullyConstrained = true
  MapMode = 5
  Placement = pos=(0,0,1e-16) rot=(0.707107,0.707107,0;3.14159rad)
  Support = -> [Pad139]
  sketch-geometry (9):
    g0: LineSegment StartX=0 StartY=8.5 StartZ=0 EndX=-20 EndY=8.5 EndZ=0
    g1: ArcOfCircle CenterX=-3 CenterY=7.5 CenterZ=0 NormalX=0 NormalY=0 NormalZ=1 AngleXU=0 Radius=1 StartAngle=3.14159 EndAngle=6.28319
    g2: ArcOfCircle CenterX=-3 CenterY=9.5 CenterZ=0 NormalX=0 NormalY=0 NormalZ=1 AngleXU=0 Radius=1 StartAngle=3e-16 EndAngle=3.14159
    g3: LineSegment StartX=-2 StartY=7.5 StartZ=0 EndX=-2 EndY=9.5 EndZ=0
    g4: LineSegment StartX=-4 StartY=7.5 StartZ=0 EndX=-4 EndY=9.5 EndZ=0
    g5: ArcOfCircle CenterX=-18 CenterY=9.5 CenterZ=0 NormalX=0 NormalY=0 NormalZ=1 AngleXU=0 Radius=1 StartAngle=0 EndAngle=3.14159
    g6: ArcOfCircle CenterX=-18 CenterY=7.5 CenterZ=0 NormalX=0 NormalY=0 NormalZ=1 AngleXU=0 Radius=1 StartAngle=3.14159 EndAngle=6.28319
    g7: LineSegment StartX=-19 StartY=9.5 StartZ=0 EndX=-19 EndY=7.5 EndZ=0
    g8: LineSegment StartX=-17 StartY=9.5 StartZ=0 EndX=-17 EndY=7.5 EndZ=0
  constraints (24):
    c: PointOnObject(g0,g-2)
    c: PointOnObject(g0,g-4)
    c: Horizontal(g0)
    c: DistanceY(g0,g-3) = 8.5
    c: Tangent(g1,g4) = 1.5708
    c: Tangent(g1,g3) = -1.5708
    c: Tangent(g3,g2) = -1.5708
    c: Tangent(g4,g2) = 1.5708
    c: Vertical(g3)
    c: Equal(g1,g2)
    c: Radius(g2) = 1
    c: DistanceY(g4,g4) = 2
    c: DistanceY(g0,g2) = 1
    c: DistanceX(g2,g0) = 3
    c: Tangent(g5,g8) = 1.5708
    c: Tangent(g5,g7) = -1.5708
    c: Tangent(g7,g6) = -1.5708
    c: Tangent(g8,g6) = 1.5708
    c: Vertical(g7)
    c: Equal(g5,g6)
    c: Equal(g5,g2)
    c: Equal(g8,g4)
    c: Horizontal(g5,g2)
    c: DistanceX(g0,g5) = 2
FEATURE [PartDesign::Pad] Pad140
  BaseFeature = -> Pad139
  Direction = (1,1,1)
  Length = 1
  Length2 = 100
  Placement = pos=(0,0,0) rot=(0.57735,0.57735,0.57735;2.0944rad)
  Profile = -> Sketch283
  Type = 0
FEATURE [PartDesign::Body] Body208  label="Corner011"
  Group = -> [Sketch278,Pad138,Sketch279,Pocket107,Sketch280,Pocket108,Sketch281,Pocket109,Sketch282,Pad139,Sketch283,Pad140]
  Origin = -> Origin289
  Tip = -> Pad140
FEATURE [App::Part] Part081  label="soporte90-012"
  Group = -> [Body208]
  Origin = -> Origin290
  Placement = pos=(319,20,70) rot=(1,0,0;3.14159rad)
FEATURE [App::LinkGroup] LinkGroup010  label="esquineros estructura"
  ElementList = -> [Part081,Part074,Part070,Part071,Part072,Part073,Part075,Part076,Part080,Part079,Part078,Part077]
  LinkMode = 0
FEATURE [Sketcher::SketchObject] Sketch284
  FullyConstrained = false
  MapMode = 5
  Support = -> [XY_Plane286]
  sketch-geometry (4):
    g0: ArcOfCircle CenterX=0 CenterY=4e-15 CenterZ=0 NormalX=0 NormalY=0 NormalZ=1 AngleXU=0 Radius=11 StartAngle=2.18335 EndAngle=3.14159
    g1: LineSegment StartX=-11 StartY=4e-15 StartZ=0 EndX=0 EndY=4e-15 EndZ=0
    g2: LineSegment StartX=0 StartY=9 StartZ=0 EndX=0 EndY=3.6e-15 EndZ=0
    g3: LineSegment StartX=0 StartY=9 StartZ=0 EndX=-6.32456 EndY=9 EndZ=0
  constraints (10):
    c: Coincident(g0,g-1)
    c: Diameter(g0) = 22
    c: Coincident(g1,g0)
    c: Horizontal(g1)
    c: Coincident(g0,g1)
    c: Coincident(g2,g0)
    c: Vertical(g2)
    c: Horizontal(g3)
    c: Coincident(g3,g2)
    c: Coincident(g3,g0)
FEATURE [PartDesign::Revolution] Revolution046
  Angle = 360
  Axis = (0,1,0)
  Base = (0,0,0)
  Profile = -> Sketch284
  ReferenceAxis = -> Sketch284 [V_Axis]
FEATURE [PartDesign::Body] Body209
  Group = -> [Sketch284,Revolution046]
  Origin = -> Origin292
  Tip = -> Revolution046
FEATURE [App::Part] Part082  label="tacoGoma-002"
  Group = -> [Body209]
  Origin = -> Origin291
  Placement = pos=(10,9,0) rot=(1,0,0;-1.5708rad)
FEATURE [Sketcher::SketchObject] Sketch285
  FullyConstrained = false
  MapMode = 5
  Support = -> [XY_Plane288]
  sketch-geometry (4):
    g0: ArcOfCircle CenterX=0 CenterY=4e-15 CenterZ=0 NormalX=0 NormalY=0 NormalZ=1 AngleXU=0 Radius=11 StartAngle=2.18335 EndAngle=3.14159
    g1: LineSegment StartX=-11 StartY=4e-15 StartZ=0 EndX=0 EndY=4e-15 EndZ=0
    g2: LineSegment StartX=0 StartY=9 StartZ=0 EndX=0 EndY=3.6e-15 EndZ=0
    g3: LineSegment StartX=0 StartY=9 StartZ=0 EndX=-6.32456 EndY=9 EndZ=0
  constraints (10):
    c: Coincident(g0,g-1)
    c: Diameter(g0) = 22
    c: Coincident(g1,g0)
    c: Horizontal(g1)
    c: Coincident(g0,g1)
    c: Coincident(g2,g0)
    c: Vertical(g2)
    c: Horizontal(g3)
    c: Coincident(g3,g2)
    c: Coincident(g3,g0)
FEATURE [PartDesign::Revolution] Revolution047
  Angle = 360
  Axis = (0,1,0)
  Base = (0,0,0)
  Profile = -> Sketch285
  ReferenceAxis = -> Sketch285 [V_Axis]
FEATURE [PartDesign::Body] Body210
  Group = -> [Sketch285,Revolution047]
  Origin = -> Origin294
  Tip = -> Revolution047
FEATURE [App::Part] Part083  label="tacoGoma001"
  Group = -> [Body210]
  Origin = -> Origin293
  Placement = pos=(10,331,0) rot=(1,0,0;-1.5708rad)
FEATURE [Sketcher::SketchObject] Sketch286
  FullyConstrained = false
  MapMode = 5
  Support = -> [XY_Plane290]
  sketch-geometry (4):
    g0: ArcOfCircle CenterX=0 CenterY=4e-15 CenterZ=0 NormalX=0 NormalY=0 NormalZ=1 AngleXU=0 Radius=11 StartAngle=2.18335 EndAngle=3.14159
    g1: LineSegment StartX=-11 StartY=4e-15 StartZ=0 EndX=0 EndY=4e-15 EndZ=0
    g2: LineSegment StartX=0 StartY=9 StartZ=0 EndX=0 EndY=3.6e-15 EndZ=0
    g3: LineSegment StartX=0 StartY=9 StartZ=0 EndX=-6.32456 EndY=9 EndZ=0
  constraints (10):
    c: Coincident(g0,g-1)
    c: Diameter(g0) = 22
    c: Coincident(g1,g0)
    c: Horizontal(g1)
    c: Coincident(g0,g1)
    c: Coincident(g2,g0)
    c: Vertical(g2)
    c: Horizontal(g3)
    c: Coincident(g3,g2)
    c: Coincident(g3,g0)
FEATURE [PartDesign::Revolution] Revolution048
  Angle = 360
  Axis = (0,1,0)
  Base = (0,0,0)
  Profile = -> Sketch286
  ReferenceAxis = -> Sketch286 [V_Axis]
FEATURE [PartDesign::Body] Body211
  Group = -> [Sketch286,Revolution048]
  Origin = -> Origin296
  Tip = -> Revolution048
FEATURE [App::Part] Part084  label="tacoGoma002"
  Group = -> [Body211]
  Origin = -> Origin295
  Placement = pos=(330,330,2e-16) rot=(1,0,0;-1.5708rad)
FEATURE [Sketcher::SketchObject] Sketch287
  FullyConstrained = false
  MapMode = 5
  Support = -> [XY_Plane292]
  sketch-geometry (4):
    g0: ArcOfCircle CenterX=0 CenterY=4e-15 CenterZ=0 NormalX=0 NormalY=0 NormalZ=1 AngleXU=0 Radius=11 StartAngle=2.18335 EndAngle=3.14159
    g1: LineSegment StartX=-11 StartY=4e-15 StartZ=0 EndX=0 EndY=4e-15 EndZ=0
    g2: LineSegment StartX=0 StartY=9 StartZ=0 EndX=0 EndY=3.6e-15 EndZ=0
    g3: LineSegment StartX=0 StartY=9 StartZ=0 EndX=-6.32456 EndY=9 EndZ=0
  constraints (10):
    c: Coincident(g0,g-1)
    c: Diameter(g0) = 22
    c: Coincident(g1,g0)
    c: Horizontal(g1)
    c: Coincident(g0,g1)
    c: Coincident(g2,g0)
    c: Vertical(g2)
    c: Horizontal(g3)
    c: Coincident(g3,g2)
    c: Coincident(g3,g0)
FEATURE [PartDesign::Revolution] Revolution049
  Angle = 360
  Axis = (0,1,0)
  Base = (0,0,0)
  Profile = -> Sketch287
  ReferenceAxis = -> Sketch287 [V_Axis]
FEATURE [PartDesign::Body] Body212
  Group = -> [Sketch287,Revolution049]
  Origin = -> Origin298
  Tip = -> Revolution049
FEATURE [App::Part] Part085  label="tacoGoma003"
  Group = -> [Body212]
  Origin = -> Origin297
  Placement = pos=(330,9,0) rot=(1,0,0;-1.5708rad)
FEATURE [App::LinkGroup] LinkGroup011  label="tacos de madera"
  ElementList = -> [Part082,Part083,Part084,Part085]
  LinkMode = 0
FEATURE [PartDesign::Plane] DatumPlane
  AttachmentOffset = pos=(0,0,0) rot=(0,1,0;0.174533rad)
  Length = 68.686
  MapMode = 5
  Placement = pos=(0,0,0) rot=(0.992433,0.086827,0.086827;1.57839rad)
  ResizeMode = 0
  Support = -> [XZ_Plane296]
  Width = 60.7632
FEATURE [Part::Helix] Helix001  label="Hélice001"
  Angle = 0
  AttacherType = Attacher::AttachEngine3D
  Height = 9.1
  LocalCoord = 0
  Pitch = 1.5
  Placement = pos=(0,0,7.35) rot=(0,0,1;0rad)
  Radius = 10
  Style = 1
FEATURE [PartDesign::ShapeBinder] ShapeBinder001
  Placement = pos=(0,0,7.35) rot=(0,0,1;0rad)
  Support = -> [Helix001]
  TraceSupport = false
FEATURE [Sketcher::SketchObject] Sketch289
  FullyConstrained = false
  MapMode = 5
  Placement = pos=(0,0,0) rot=(1,0,0;1.5708rad)
  Support = -> [XZ_Plane296]
  sketch-geometry (6):
    g0: LineSegment StartX=-9 StartY=25 StartZ=0 EndX=-4 EndY=25 EndZ=0
    g1: LineSegment StartX=-2.5 StartY=8 StartZ=0 EndX=-2.5 EndY=0 EndZ=0
    g2: LineSegment StartX=-2.5 StartY=0 StartZ=0 EndX=-9 EndY=0 EndZ=0
    g3: LineSegment StartX=-9 StartY=0 StartZ=0 EndX=-9 EndY=25 EndZ=0
    g4: LineSegment StartX=-2.5 StartY=8 StartZ=0 EndX=-4 EndY=8 EndZ=0
    g5: LineSegment StartX=-4 StartY=8 StartZ=0 EndX=-4 EndY=25 EndZ=0
  constraints (18):
    c: Coincident(g1,g2)
    c: Coincident(g2,g3)
    c: Coincident(g3,g0)
    c: Horizontal(g0)
    c: Horizontal(g2)
    c: Vertical(g1)
    c: Vertical(g3)
    c: PointOnObject(g1,g-1)
    c: DistanceX(g1,g-1) = 2.5
    c: DistanceX(g2,g-1) = 9
    c: DistanceY(g3,g3) = 25
    c: Horizontal(g4)
    c: Coincident(g5,g4)
    c: Vertical(g5)
    c: Coincident(g1,g4)
    c: Coincident(g0,g5)
    c: DistanceX(g0,g-1) = 4
    c: DistanceY(g5,g5) = 17
FEATURE [PartDesign::Revolution] Revolution050
  AllowMultiFace = false
  Angle = 360
  Axis = (0,-2e-16,1)
  Base = (0,0,0)
  Placement = pos=(0,0,0) rot=(1,0,0;1.5708rad)
  Profile = -> Sketch289
  ReferenceAxis = -> Sketch289 [V_Axis]
  Refine = true
FEATURE [Sketcher::SketchObject] Sketch290
  FullyConstrained = false
  MapMode = 5
  Placement = pos=(0,0,0) rot=(1,0,0;1.5708rad)
  Support = -> [XZ_Plane296]
  sketch-geometry (4):
    g0: LineSegment StartX=0.227639 StartY=16.7629 StartZ=0 EndX=11.1677 EndY=16.7629 EndZ=0
    g1: LineSegment StartX=11.1677 StartY=16.7629 StartZ=0 EndX=11.1677 EndY=16.2629 EndZ=0
    g2: LineSegment StartX=11.1677 StartY=16.2629 StartZ=0 EndX=0.227639 EndY=16.2629 EndZ=0
    g3: LineSegment StartX=0.227639 StartY=16.2629 StartZ=0 EndX=0.227639 EndY=16.7629 EndZ=0
  constraints (9):
    c: Coincident(g0,g1)
    c: Coincident(g1,g2)
    c: Coincident(g2,g3)
    c: Coincident(g3,g0)
    c: Horizontal(g0)
    c: Horizontal(g2)
    c: Vertical(g1)
    c: Vertical(g3)
    c: DistanceY(g1,g1) = 0.5
FEATURE [Sketcher::SketchObject] Sketch292
  FullyConstrained = false
  MapMode = 5
  Placement = pos=(0,0,0) rot=(1,0,0;1.5708rad)
  Support = -> [XZ_Plane297]
  sketch-geometry (4):
    g0: LineSegment StartX=0 StartY=0 StartZ=0 EndX=-2 EndY=0 EndZ=0
    g1: LineSegment StartX=-2 StartY=0 StartZ=0 EndX=-2 EndY=6 EndZ=0
    g2: LineSegment StartX=-2 StartY=6 StartZ=0 EndX=0 EndY=6 EndZ=0
    g3: LineSegment StartX=0 StartY=6 StartZ=0 EndX=0 EndY=0 EndZ=0
  constraints (11):
    c: Coincident(g0,g1)
    c: Coincident(g1,g2)
    c: Coincident(g2,g3)
    c: Coincident(g3,g0)
    c: Horizontal(g0)
    c: Horizontal(g2)
    c: Vertical(g1)
    c: Vertical(g3)
    c: Coincident(g0,g-1)
    c: DistanceX(g2,g2) = 2
    c: DistanceY(g1,g1) = 6
FEATURE [PartDesign::Revolution] Revolution001
  AllowMultiFace = false
  Angle = 360
  Axis = (0,2e-16,1)
  Base = (0,0,0)
  Placement = pos=(0,0,0) rot=(1,0,0;1.5708rad)
  Profile = -> Sketch292
  ReferenceAxis = -> Sketch292 [V_Axis]
  Refine = true
FEATURE [Sketcher::SketchObject] Sketch293
  FullyConstrained = false
  MapMode = 5
  Placement = pos=(0,2.6e-15,6) rot=(0,0,1;3.14159rad)
  Support = -> [Revolution001]
  sketch-geometry (7):
    g0: LineSegment StartX=-0.625 StartY=-1.08253 StartZ=0 EndX=0.625 EndY=-1.08253 EndZ=0
    g1: LineSegment StartX=0.625 StartY=-1.08253 StartZ=0 EndX=1.25 EndY=-1.44e-14 EndZ=0
    g2: LineSegment StartX=1.25 StartY=-1.44e-14 StartZ=0 EndX=0.625 EndY=1.08253 EndZ=0
    g3: LineSegment StartX=0.625 StartY=1.08253 StartZ=0 EndX=-0.625 EndY=1.08253 EndZ=0
    g4: LineSegment StartX=-0.625 StartY=1.08253 StartZ=0 EndX=-1.25 EndY=-1.44e-14 EndZ=0
    g5: LineSegment StartX=-1.25 StartY=-1.44e-14 StartZ=0 EndX=-0.625 EndY=-1.08253 EndZ=0
    g6: Circle CenterX=0 CenterY=0 CenterZ=0 NormalX=0 NormalY=0 NormalZ=1 AngleXU=0 Radius=1.25
  constraints (16):
    c: Coincident(g0,g1)
    c: Coincident(g1,g2)
    c: Coincident(g2,g3)
    c: Coincident(g3,g4)
    c: Coincident(g4,g5)
    c: Coincident(g5,g0)
    c: Equal(g0, g1-g5) x5
    c: PointOnObject(g0,g6)
    c: PointOnObject(g1,g6)
    c: PointOnObject(g2,g6)
    c: PointOnObject(g3,g6)
    c: PointOnObject(g4,g6)
    c: PointOnObject(g5,g6)
    c: Coincident(g6,g-1)
    c: Horizontal(g0)
    c: DistanceX(g4,g1) = 2.5
FEATURE [PartDesign::Pocket] Pocket112
  AllowMultiFace = false
  BaseFeature = -> Revolution001
  Length = 2
  Length2 = 100
  Placement = pos=(0,0,0) rot=(1,0,0;1.5708rad)
  Profile = -> Sketch293
  Refine = true
  Type = 0
FEATURE [PartDesign::Chamfer] Chamfer012
  Angle = 45
  Base = -> Pocket112 [Edge2]
  BaseFeature = -> Pocket112
  ChamferType = 0
  FlipDirection = false
  Placement = pos=(0,0,0) rot=(1,0,0;1.5708rad)
  Size = 0.35
  Size2 = 1
  SupportTransform = false
FEATURE [PartDesign::Chamfer] Chamfer013
  Angle = 45
  Base = -> Chamfer012 [Edge3]
  BaseFeature = -> Chamfer012
  ChamferType = 0
  FlipDirection = false
  Placement = pos=(0,0,0) rot=(1,0,0;1.5708rad)
  Size = 0.75
  Size2 = 1
  SupportTransform = false
FEATURE [PartDesign::Body] Body213  label="Set Screw"
  Group = -> [Sketch292,Revolution001,Sketch293,Pocket112,Chamfer012,Chamfer013]
  Origin = -> Origin303
  Tip = -> Chamfer013
FEATURE [PartDesign::FeatureBase] Clone084
  BaseFeature = -> Body213
FEATURE [PartDesign::Body] Body215  label="Clon1"
  BaseFeature = -> Body213
  Group = -> [Clone084]
  Origin = -> Origin304
  Placement = pos=(0,-3,4) rot=(1,0,0;1.5708rad)
  Tip = -> Clone084
FEATURE [PartDesign::FeatureBase] Clone085
  BaseFeature = -> Body215
  Placement = pos=(0,-4,4) rot=(1,0,0;1.5708rad)
FEATURE [PartDesign::Body] Body216  label="Clon2"
  BaseFeature = -> Body215
  Group = -> [Clone085]
  Origin = -> Origin305
  Placement = pos=(-0.173648,0.984808,17) rot=(0,0,1;0.174533rad)
  Tip = -> Clone085
FEATURE [PartDesign::FeatureBase] Clone086
  BaseFeature = -> Body215
  Placement = pos=(0,-4,4) rot=(1,0,0;1.5708rad)
FEATURE [PartDesign::Body] Body217  label="Clon3"
  BaseFeature = -> Body215
  Group = -> [Clone086]
  Origin = -> Origin306
  Placement = pos=(-1,0,0) rot=(0,0,1;1.5708rad)
  Tip = -> Clone086
FEATURE [PartDesign::FeatureBase] Clone087
  BaseFeature = -> Body216
  Placement = pos=(0,0,17) rot=(0,0,1;0.174533rad)
FEATURE [PartDesign::Body] Body218  label="Clon4"
  BaseFeature = -> Body216
  Group = -> [Clone087]
  Origin = -> Origin307
  Placement = pos=(-1,2e-16,0) rot=(0,0,1;1.5708rad)
  Tip = -> Clone087
FEATURE [App::Part] Part088  label="fastener"
  Group = -> [Body213,Body215,Body216,Body217,Body218]
  Origin = -> Origin301
FEATURE [PartDesign::SubtractivePipe] SubtractivePipe
  AllowMultiFace = false
  AuxilleryCurvelinear = true
  AuxillerySpineTangent = false
  BaseFeature = -> Revolution050
  Binormal = (0,0,0)
  Mode = 2
  Placement = pos=(0,0,0) rot=(1,0,0;1.5708rad)
  Profile = -> Sketch290
  Refine = true
  Spine = -> ShapeBinder001
  SpineTangent = false
  Transformation = 0
  Transition = 0
FEATURE [Sketcher::SketchObject] Sketch291
  ExternalGeometry = -> [SubtractivePipe]
  FullyConstrained = false
  MapMode = 5
  Placement = pos=(0,0,0) rot=(1,0,0;1.5708rad)
  Support = -> [XZ_Plane296]
  sketch-geometry (4):
    g0: Circle CenterX=0 CenterY=4 CenterZ=0 NormalX=0 NormalY=0 NormalZ=1 AngleXU=0 Radius=2
    g1: Circle CenterX=0 CenterY=21 CenterZ=0 NormalX=0 NormalY=0 NormalZ=1 AngleXU=0 Radius=2
    g2: LineSegment StartX=0 StartY=4 StartZ=0 EndX=0 EndY=0 EndZ=0
    g3: LineSegment StartX=0 StartY=21 StartZ=0 EndX=0 EndY=25 EndZ=0
  constraints (9):
    c: PointOnObject(g0,g-2)
    c: PointOnObject(g1,g-2)
    c: Radius(g1) = 2
    c: Equal(g0,g1)
    c: Coincident(g2,g0)
    c: Coincident(g2,g-1)
    c: Coincident(g3,g1)
    c: Vertical(g3)
    c: Equal(g3,g2)
FEATURE [PartDesign::Pocket] Pocket111
  AllowMultiFace = false
  BaseFeature = -> SubtractivePipe
  Length = 10
  Length2 = 100
  Placement = pos=(0,0,0) rot=(1,0,0;1.5708rad)
  Profile = -> Sketch291
  Refine = true
  Reversed = true
  Type = 0
FEATURE [Sketcher::SketchObject] Sketch288
  ExternalGeometry = -> [Pocket111]
  FullyConstrained = false
  MapMode = 5
  Placement = pos=(0,0,0) rot=(0.992433,0.086827,0.086827;1.57839rad)
  Support = -> [DatumPlane]
  sketch-geometry (1):
    g0: Circle CenterX=0 CenterY=21 CenterZ=0 NormalX=0 NormalY=0 NormalZ=1 AngleXU=0 Radius=2
  constraints (3):
    c: PointOnObject(g0,g-2)
    c: Radius(g0) = 2
    c: DistanceY(g0,g-3) = 4
FEATURE [PartDesign::Pocket] Pocket110
  AllowMultiFace = false
  BaseFeature = -> Pocket111
  Length = 10
  Length2 = 100
  Placement = pos=(0,0,0) rot=(1,0,0;1.5708rad)
  Profile = -> Sketch288
  Refine = true
  Reversed = true
  Type = 0
FEATURE [PartDesign::PolarPattern] PolarPattern024
  Angle = 90
  Axis = -> Sketch291 [V_Axis]
  BaseFeature = -> Pocket110
  Occurrences = 3
  Originals = -> [Pocket111,Pocket110]
  Placement = pos=(0,0,0) rot=(1,0,0;1.5708rad)
  Refine = true
FEATURE [PartDesign::Body] Body214  label="Beam coupling"
  Group = -> [Sketch289,Revolution050,ShapeBinder001,Sketch290,SubtractivePipe,Sketch291,Pocket111,DatumPlane,Sketch288,Pocket110,PolarPattern024]
  Origin = -> Origin302
  Tip = -> PolarPattern024
FEATURE [App::Part] Part087  label="Beam coupling "
  Group = -> [Body214,Helix001]
  Origin = -> Origin300
FEATURE [App::Part] Part086  label="Beam-coupling-8mm-5mm-002"
  Group = -> [Part087,Part088]
  Origin = -> Origin299
  Placement = pos=(385,116,105) rot=(0,1,0;-1.5708rad)
FEATURE [PartDesign::Plane] DatumPlane001
  AttachmentOffset = pos=(0,0,0) rot=(0,1,0;0.174533rad)
  Length = 68.686
  MapMode = 5
  Placement = pos=(0,0,0) rot=(0.992433,0.086827,0.086827;1.57839rad)
  ResizeMode = 0
  Support = -> [XZ_Plane305]
  Width = 60.7632
FEATURE [Part::Helix] Helix002  label="Hélice002"
  Angle = 0
  AttacherType = Attacher::AttachEngine3D
  Height = 9.1
  LocalCoord = 0
  Pitch = 1.5
  Placement = pos=(0,0,7.35) rot=(0,0,1;0rad)
  Radius = 10
  Style = 1
FEATURE [PartDesign::ShapeBinder] ShapeBinder002
  Placement = pos=(0,0,7.35) rot=(0,0,1;0rad)
  Support = -> [Helix002]
  TraceSupport = false
FEATURE [Sketcher::SketchObject] Sketch295
  FullyConstrained = false
  MapMode = 5
  Placement = pos=(0,0,0) rot=(1,0,0;1.5708rad)
  Support = -> [XZ_Plane305]
  sketch-geometry (6):
    g0: LineSegment StartX=-9 StartY=25 StartZ=0 EndX=-4 EndY=25 EndZ=0
    g1: LineSegment StartX=-2.5 StartY=8 StartZ=0 EndX=-2.5 EndY=0 EndZ=0
    g2: LineSegment StartX=-2.5 StartY=0 StartZ=0 EndX=-9 EndY=0 EndZ=0
    g3: LineSegment StartX=-9 StartY=0 StartZ=0 EndX=-9 EndY=25 EndZ=0
    g4: LineSegment StartX=-2.5 StartY=8 StartZ=0 EndX=-4 EndY=8 EndZ=0
    g5: LineSegment StartX=-4 StartY=8 StartZ=0 EndX=-4 EndY=25 EndZ=0
  constraints (18):
    c: Coincident(g1,g2)
    c: Coincident(g2,g3)
    c: Coincident(g3,g0)
    c: Horizontal(g0)
    c: Horizontal(g2)
    c: Vertical(g1)
    c: Vertical(g3)
    c: PointOnObject(g1,g-1)
    c: DistanceX(g1,g-1) = 2.5
    c: DistanceX(g2,g-1) = 9
    c: DistanceY(g3,g3) = 25
    c: Horizontal(g4)
    c: Coincident(g5,g4)
    c: Vertical(g5)
    c: Coincident(g1,g4)
    c: Coincident(g0,g5)
    c: DistanceX(g0,g-1) = 4
    c: DistanceY(g5,g5) = 17
FEATURE [PartDesign::Revolution] Revolution052
  AllowMultiFace = false
  Angle = 360
  Axis = (0,-2e-16,1)
  Base = (0,0,0)
  Placement = pos=(0,0,0) rot=(1,0,0;1.5708rad)
  Profile = -> Sketch295
  ReferenceAxis = -> Sketch295 [V_Axis]
  Refine = true
FEATURE [Sketcher::SketchObject] Sketch296
  FullyConstrained = false
  MapMode = 5
  Placement = pos=(0,0,0) rot=(1,0,0;1.5708rad)
  Support = -> [XZ_Plane305]
  sketch-geometry (4):
    g0: LineSegment StartX=0.227639 StartY=16.7629 StartZ=0 EndX=11.1677 EndY=16.7629 EndZ=0
    g1: LineSegment StartX=11.1677 StartY=16.7629 StartZ=0 EndX=11.1677 EndY=16.2629 EndZ=0
    g2: LineSegment StartX=11.1677 StartY=16.2629 StartZ=0 EndX=0.227639 EndY=16.2629 EndZ=0
    g3: LineSegment StartX=0.227639 StartY=16.2629 StartZ=0 EndX=0.227639 EndY=16.7629 EndZ=0
  constraints (9):
    c: Coincident(g0,g1)
    c: Coincident(g1,g2)
    c: Coincident(g2,g3)
    c: Coincident(g3,g0)
    c: Horizontal(g0)
    c: Horizontal(g2)
    c: Vertical(g1)
    c: Vertical(g3)
    c: DistanceY(g1,g1) = 0.5
FEATURE [Sketcher::SketchObject] Sketch298
  FullyConstrained = false
  MapMode = 5
  Placement = pos=(0,0,0) rot=(1,0,0;1.5708rad)
  Support = -> [XZ_Plane306]
  sketch-geometry (4):
    g0: LineSegment StartX=0 StartY=0 StartZ=0 EndX=-2 EndY=0 EndZ=0
    g1: LineSegment StartX=-2 StartY=0 StartZ=0 EndX=-2 EndY=6 EndZ=0
    g2: LineSegment StartX=-2 StartY=6 StartZ=0 EndX=0 EndY=6 EndZ=0
    g3: LineSegment StartX=0 StartY=6 StartZ=0 EndX=0 EndY=0 EndZ=0
  constraints (11):
    c: Coincident(g0,g1)
    c: Coincident(g1,g2)
    c: Coincident(g2,g3)
    c: Coincident(g3,g0)
    c: Horizontal(g0)
    c: Horizontal(g2)
    c: Vertical(g1)
    c: Vertical(g3)
    c: Coincident(g0,g-1)
    c: DistanceX(g2,g2) = 2
    c: DistanceY(g1,g1) = 6
FEATURE [PartDesign::Revolution] Revolution051
  AllowMultiFace = false
  Angle = 360
  Axis = (0,2e-16,1)
  Base = (0,0,0)
  Placement = pos=(0,0,0) rot=(1,0,0;1.5708rad)
  Profile = -> Sketch298
  ReferenceAxis = -> Sketch298 [V_Axis]
  Refine = true
FEATURE [Sketcher::SketchObject] Sketch299
  FullyConstrained = false
  MapMode = 5
  Placement = pos=(0,2.6e-15,6) rot=(0,0,1;3.14159rad)
  Support = -> [Revolution051]
  sketch-geometry (7):
    g0: LineSegment StartX=-0.625 StartY=-1.08253 StartZ=0 EndX=0.625 EndY=-1.08253 EndZ=0
    g1: LineSegment StartX=0.625 StartY=-1.08253 StartZ=0 EndX=1.25 EndY=-1.44e-14 EndZ=0
    g2: LineSegment StartX=1.25 StartY=-1.44e-14 StartZ=0 EndX=0.625 EndY=1.08253 EndZ=0
    g3: LineSegment StartX=0.625 StartY=1.08253 StartZ=0 EndX=-0.625 EndY=1.08253 EndZ=0
    g4: LineSegment StartX=-0.625 StartY=1.08253 StartZ=0 EndX=-1.25 EndY=-1.44e-14 EndZ=0
    g5: LineSegment StartX=-1.25 StartY=-1.44e-14 StartZ=0 EndX=-0.625 EndY=-1.08253 EndZ=0
    g6: Circle CenterX=0 CenterY=0 CenterZ=0 NormalX=0 NormalY=0 NormalZ=1 AngleXU=0 Radius=1.25
  constraints (16):
    c: Coincident(g0,g1)
    c: Coincident(g1,g2)
    c: Coincident(g2,g3)
    c: Coincident(g3,g4)
    c: Coincident(g4,g5)
    c: Coincident(g5,g0)
    c: Equal(g0, g1-g5) x5
    c: PointOnObject(g0,g6)
    c: PointOnObject(g1,g6)
    c: PointOnObject(g2,g6)
    c: PointOnObject(g3,g6)
    c: PointOnObject(g4,g6)
    c: PointOnObject(g5,g6)
    c: Coincident(g6,g-1)
    c: Horizontal(g0)
    c: DistanceX(g4,g1) = 2.5
FEATURE [PartDesign::Pocket] Pocket115
  AllowMultiFace = false
  BaseFeature = -> Revolution051
  Length = 2
  Length2 = 100
  Placement = pos=(0,0,0) rot=(1,0,0;1.5708rad)
  Profile = -> Sketch299
  Refine = true
  Type = 0
FEATURE [PartDesign::Chamfer] Chamfer014
  Angle = 45
  Base = -> Pocket115 [Edge2]
  BaseFeature = -> Pocket115
  ChamferType = 0
  FlipDirection = false
  Placement = pos=(0,0,0) rot=(1,0,0;1.5708rad)
  Size = 0.35
  Size2 = 1
  SupportTransform = false
FEATURE [PartDesign::Chamfer] Chamfer015
  Angle = 45
  Base = -> Chamfer014 [Edge3]
  BaseFeature = -> Chamfer014
  ChamferType = 0
  FlipDirection = false
  Placement = pos=(0,0,0) rot=(1,0,0;1.5708rad)
  Size = 0.75
  Size2 = 1
  SupportTransform = false
FEATURE [PartDesign::Body] Body219  label="Set Screw001"
  Group = -> [Sketch298,Revolution051,Sketch299,Pocket115,Chamfer014,Chamfer015]
  Origin = -> Origin312
  Tip = -> Chamfer015
FEATURE [PartDesign::FeatureBase] Clone088
  BaseFeature = -> Body219
FEATURE [PartDesign::Body] Body221  label="Clon005"
  BaseFeature = -> Body219
  Group = -> [Clone088]
  Origin = -> Origin313
  Placement = pos=(0,-3,4) rot=(1,0,0;1.5708rad)
  Tip = -> Clone088
FEATURE [PartDesign::FeatureBase] Clone089
  BaseFeature = -> Body221
  Placement = pos=(0,-4,4) rot=(1,0,0;1.5708rad)
FEATURE [PartDesign::Body] Body222  label="Clon006"
  BaseFeature = -> Body221
  Group = -> [Clone089]
  Origin = -> Origin314
  Placement = pos=(-0.173648,0.984808,17) rot=(0,0,1;0.174533rad)
  Tip = -> Clone089
FEATURE [PartDesign::FeatureBase] Clone090
  BaseFeature = -> Body221
  Placement = pos=(0,-4,4) rot=(1,0,0;1.5708rad)
FEATURE [PartDesign::Body] Body223  label="Clon007"
  BaseFeature = -> Body221
  Group = -> [Clone090]
  Origin = -> Origin315
  Placement = pos=(-1,0,0) rot=(0,0,1;1.5708rad)
  Tip = -> Clone090
FEATURE [PartDesign::FeatureBase] Clone091
  BaseFeature = -> Body222
  Placement = pos=(0,0,17) rot=(0,0,1;0.174533rad)
FEATURE [PartDesign::Body] Body224  label="Clon008"
  BaseFeature = -> Body222
  Group = -> [Clone091]
  Origin = -> Origin316
  Placement = pos=(-1,2e-16,0) rot=(0,0,1;1.5708rad)
  Tip = -> Clone091
FEATURE [App::Part] Part091  label="fastener001"
  Group = -> [Body219,Body221,Body222,Body223,Body224]
  Origin = -> Origin310
FEATURE [PartDesign::SubtractivePipe] SubtractivePipe001
  AllowMultiFace = false
  AuxilleryCurvelinear = true
  AuxillerySpineTangent = false
  BaseFeature = -> Revolution052
  Binormal = (0,0,0)
  Mode = 2
  Placement = pos=(0,0,0) rot=(1,0,0;1.5708rad)
  Profile = -> Sketch296
  Refine = true
  Spine = -> ShapeBinder002
  SpineTangent = false
  Transformation = 0
  Transition = 0
FEATURE [Sketcher::SketchObject] Sketch297
  ExternalGeometry = -> [SubtractivePipe001]
  FullyConstrained = false
  MapMode = 5
  Placement = pos=(0,0,0) rot=(1,0,0;1.5708rad)
  Support = -> [XZ_Plane305]
  sketch-geometry (4):
    g0: Circle CenterX=0 CenterY=4 CenterZ=0 NormalX=0 NormalY=0 NormalZ=1 AngleXU=0 Radius=2
    g1: Circle CenterX=0 CenterY=21 CenterZ=0 NormalX=0 NormalY=0 NormalZ=1 AngleXU=0 Radius=2
    g2: LineSegment StartX=0 StartY=4 StartZ=0 EndX=0 EndY=0 EndZ=0
    g3: LineSegment StartX=0 StartY=21 StartZ=0 EndX=0 EndY=25 EndZ=0
  constraints (9):
    c: PointOnObject(g0,g-2)
    c: PointOnObject(g1,g-2)
    c: Radius(g1) = 2
    c: Equal(g0,g1)
    c: Coincident(g2,g0)
    c: Coincident(g2,g-1)
    c: Coincident(g3,g1)
    c: Vertical(g3)
    c: Equal(g3,g2)
FEATURE [PartDesign::Pocket] Pocket114
  AllowMultiFace = false
  BaseFeature = -> SubtractivePipe001
  Length = 10
  Length2 = 100
  Placement = pos=(0,0,0) rot=(1,0,0;1.5708rad)
  Profile = -> Sketch297
  Refine = true
  Reversed = true
  Type = 0
FEATURE [Sketcher::SketchObject] Sketch294
  ExternalGeometry = -> [Pocket114]
  FullyConstrained = false
  MapMode = 5
  Placement = pos=(0,0,0) rot=(0.992433,0.086827,0.086827;1.57839rad)
  Support = -> [DatumPlane001]
  sketch-geometry (1):
    g0: Circle CenterX=0 CenterY=21 CenterZ=0 NormalX=0 NormalY=0 NormalZ=1 AngleXU=0 Radius=2
  constraints (3):
    c: PointOnObject(g0,g-2)
    c: Radius(g0) = 2
    c: DistanceY(g0,g-3) = 4
FEATURE [PartDesign::Pocket] Pocket113
  AllowMultiFace = false
  BaseFeature = -> Pocket114
  Length = 10
  Length2 = 100
  Placement = pos=(0,0,0) rot=(1,0,0;1.5708rad)
  Profile = -> Sketch294
  Refine = true
  Reversed = true
  Type = 0
FEATURE [PartDesign::PolarPattern] PolarPattern025
  Angle = 90
  Axis = -> Sketch297 [V_Axis]
  BaseFeature = -> Pocket113
  Occurrences = 3
  Originals = -> [Pocket114,Pocket113]
  Placement = pos=(0,0,0) rot=(1,0,0;1.5708rad)
  Refine = true
FEATURE [PartDesign::Body] Body220  label="Beam coupling001"
  Group = -> [Sketch295,Revolution052,ShapeBinder002,Sketch296,SubtractivePipe001,Sketch297,Pocket114,DatumPlane001,Sketch294,Pocket113,PolarPattern025]
  Origin = -> Origin311
  Tip = -> PolarPattern025
FEATURE [App::Part] Part090  label="Beam coupling 001"
  Group = -> [Body220,Helix002]
  Origin = -> Origin309
FEATURE [App::Part] Part089  label="Beam-coupling-8mm-5mm-001"
  Group = -> [Part090,Part091]
  Origin = -> Origin308
  Placement = pos=(384.965,242,105) rot=(0,1,0;4.72984rad)
FEATURE [Sketcher::SketchObject] Sketch304
  FullyConstrained = false
  MapMode = 3
  Placement = pos=(0,0,0) rot=(1,0,0;3.14159rad)
  sketch-geometry (9):
    g0: LineSegment StartX=-21.15 StartY=21.25 StartZ=0 EndX=21.15 EndY=21.25 EndZ=0
    g1: LineSegment StartX=21.15 StartY=21.25 StartZ=0 EndX=21.15 EndY=-21.15 EndZ=0
    g2: LineSegment StartX=21.15 StartY=-21.15 StartZ=0 EndX=-21.15 EndY=-21.15 EndZ=0
    g3: LineSegment StartX=-21.15 StartY=-21.15 StartZ=0 EndX=-21.15 EndY=21.25 EndZ=0
    g4: Circle CenterX=0 CenterY=0 CenterZ=0 NormalX=0 NormalY=0 NormalZ=1 AngleXU=0 Radius=11
    g5: Circle CenterX=-15.5 CenterY=15.5 CenterZ=0 NormalX=0 NormalY=0 NormalZ=1 AngleXU=0 Radius=1.5
    g6: Circle CenterX=15.5 CenterY=15.5 CenterZ=0 NormalX=0 NormalY=0 NormalZ=1 AngleXU=0 Radius=1.5
    g7: Circle CenterX=-15.5 CenterY=-15.5 CenterZ=0 NormalX=0 NormalY=0 NormalZ=1 AngleXU=0 Radius=1.5
    g8: Circle CenterX=15.5 CenterY=-15.5 CenterZ=0 NormalX=0 NormalY=0 NormalZ=1 AngleXU=0 Radius=1.5
  constraints (18):
    c: Coincident(g0,g1)
    c: Coincident(g1,g2)
    c: Coincident(g2,g3)
    c: Coincident(g3,g0)
    c: Horizontal(g0)
    c: Horizontal(g2)
    c: Vertical(g1)
    c: Vertical(g3)
    c: Coincident(g4,g-1)
    c: DistanceX(g0,g4) = 21.15
    c: DistanceX(g4,g0) = 21.15
    c: DistanceY(g4,g0) = 21.25
    c: DistanceY(g2,g4) = 21.15
    c: Equal(g5,g6)
    c: Equal(g5,g8)
    c: Equal(g5,g7)
    c: Diameter(g5) = 3
    c: Diameter(g4) = 22
FEATURE [PartDesign::Pad] Pad144
  Direction = (0,2e-16,-1)
  Length = 2
  Length2 = 10
  Placement = pos=(0,0,0) rot=(1,0,0;3.14159rad)
  Profile = -> Sketch304
  Type = 0
FEATURE [Sketcher::SketchObject] Sketch305
  FullyConstrained = false
  MapMode = 5
  Placement = pos=(21.15,0,0) rot=(0.57735,-0.57735,0.57735;4.18879rad)
  sketch-geometry (4):
    g0: LineSegment StartX=-21.15 StartY=0 StartZ=0 EndX=21.25 EndY=1.8e-15 EndZ=0
    g1: LineSegment StartX=21.25 StartY=1.8e-15 StartZ=0 EndX=21.25 EndY=60 EndZ=0
    g2: LineSegment StartX=21.25 StartY=60 StartZ=0 EndX=-21.15 EndY=60 EndZ=0
    g3: LineSegment StartX=-21.15 StartY=60 StartZ=0 EndX=-21.15 EndY=0 EndZ=0
  constraints (8):
    c: Coincident(g0,g1)
    c: Coincident(g1,g2)
    c: Coincident(g2,g3)
    c: Coincident(g3,g0)
    c: Horizontal(g2)
    c: Vertical(g1)
    c: Vertical(g3)
    c: DistanceY(g0,g2) = 60
FEATURE [PartDesign::Pad] Pad145
  BaseFeature = -> Pad144
  Direction = (1,-1e-16,-1e-16)
  Length = 2
  Length2 = 10
  Placement = pos=(0,0,0) rot=(1,0,0;3.14159rad)
  Profile = -> Sketch305
  Type = 0
FEATURE [Sketcher::SketchObject] Sketch303
  ExternalGeometry = -> [Pad145]
  FullyConstrained = false
  Placement = pos=(21.15,-4e-15,-3e-15) rot=(0.57735,0.57735,-0.57735;4.18879rad)
  sketch-geometry (8):
    g0: ArcOfCircle CenterX=-12 CenterY=52 CenterZ=0 NormalX=0 NormalY=0 NormalZ=1 AngleXU=0 Radius=2 StartAngle=0 EndAngle=3.14159
    g1: ArcOfCircle CenterX=-12 CenterY=12 CenterZ=0 NormalX=0 NormalY=0 NormalZ=1 AngleXU=0 Radius=2 StartAngle=3.14159 EndAngle=6.28319
    g2: LineSegment StartX=-10 StartY=52 StartZ=0 EndX=-10 EndY=12 EndZ=0
    g3: LineSegment StartX=-14 StartY=12 StartZ=0 EndX=-14 EndY=52 EndZ=0
    g4: ArcOfCircle CenterX=12 CenterY=52 CenterZ=0 NormalX=0 NormalY=0 NormalZ=1 AngleXU=0 Radius=2 StartAngle=0 EndAngle=3.14159
    g5: ArcOfCircle CenterX=12 CenterY=12 CenterZ=0 NormalX=0 NormalY=0 NormalZ=1 AngleXU=0 Radius=2 StartAngle=3.14159 EndAngle=6.28319
    g6: LineSegment StartX=10 StartY=52 StartZ=0 EndX=10 EndY=12 EndZ=0
    g7: LineSegment StartX=14 StartY=12 StartZ=0 EndX=14 EndY=52 EndZ=0
  constraints (16):
    c: Equal(g0,g1)
    c: Diameter(g1) = 4
    c: DistanceY(g0,g-3) = 8
    c: DistanceY(g1,g0) = 40
    c: DistanceX(g0,g-1) = 12
    c: DistanceX(g1,g-1) = 12
    c: Tangent(g1,g2) = 1.5708
    c: Tangent(g1,g3) = 1.5708
    c: Tangent(g0,g3) = 1.5708
    c: Tangent(g0,g2) = 1.5708
    c: Equal(g4,g5)
    c: Diameter(g5) = 4
    c: Tangent(g5,g6) = -1.5708
    c: Tangent(g5,g7) = -1.5708
    c: Tangent(g4,g7) = -1.5708
    c: Tangent(g4,g6) = -1.5708
FEATURE [PartDesign::Pocket] Pocket117
  BaseFeature = -> Pad145
  Length = 5
  Length2 = 5
  Placement = pos=(0,0,0) rot=(1,0,0;3.14159rad)
  Profile = -> Sketch303
  Type = 0
FEATURE [Sketcher::SketchObject] Sketch306
  FullyConstrained = true
  MapMode = 5
  Support = -> [XY_Plane316]
  sketch-geometry (3):
    g0: LineSegment StartX=0 StartY=0 StartZ=0 EndX=6 EndY=0 EndZ=0
    g1: LineSegment StartX=0 StartY=0 StartZ=0 EndX=0 EndY=6 EndZ=0
    g2: LineSegment StartX=0 StartY=6 StartZ=0 EndX=6 EndY=0 EndZ=0
  constraints (8):
    c: Coincident(g0,g-1)
    c: PointOnObject(g0,g-1)
    c: Coincident(g1,g0)
    c: PointOnObject(g1,g-2)
    c: Coincident(g2,g1)
    c: Coincident(g2,g0)
    c: DistanceX(g0,g0) = 6
    c: DistanceY(g0,g1) = 6
FEATURE [PartDesign::Pad] Pad143
  Direction = (0,0,1)
  Length = 2
  Length2 = 10
  Profile = -> Sketch306
  Type = 0
FEATURE [PartDesign::Body] Body226
  Group = -> [Sketch306,Pad143]
  Origin = -> Origin322
  Tip = -> Pad143
FEATURE [App::Part] Part093
  Group = -> [Body226]
  Origin = -> Origin319
  Placement = pos=(-2,21.15,-21.13) rot=(0.57735,-0.57735,0.57735;2.0944rad)
FEATURE [Sketcher::SketchObject] Sketch307
  FullyConstrained = true
  MapMode = 5
  Support = -> [XY_Plane318]
  sketch-geometry (3):
    g0: LineSegment StartX=0 StartY=0 StartZ=0 EndX=6 EndY=0 EndZ=0
    g1: LineSegment StartX=0 StartY=0 StartZ=0 EndX=0 EndY=6 EndZ=0
    g2: LineSegment StartX=0 StartY=6 StartZ=0 EndX=6 EndY=0 EndZ=0
  constraints (8):
    c: Coincident(g0,g-1)
    c: PointOnObject(g0,g-1)
    c: Coincident(g1,g0)
    c: PointOnObject(g1,g-2)
    c: Coincident(g2,g1)
    c: Coincident(g2,g0)
    c: DistanceX(g0,g0) = 6
    c: DistanceY(g0,g1) = 6
FEATURE [PartDesign::Pad] Pad146
  Direction = (0,0,1)
  Length = 2
  Length2 = 10
  Profile = -> Sketch307
  Type = 0
FEATURE [PartDesign::Body] Body228
  Group = -> [Sketch307,Pad146]
  Origin = -> Origin324
  Tip = -> Pad146
FEATURE [App::Part] Part095
  Group = -> [Body228]
  Origin = -> Origin323
  Placement = pos=(-2,-19.24,-21.13) rot=(0.57735,-0.57735,0.57735;2.0944rad)
FEATURE [PartDesign::Chamfer] Chamfer016
  Angle = 45
  Base = -> Pocket117 [Edge1]
  BaseFeature = -> Pocket117
  ChamferType = 0
  FlipDirection = false
  Placement = pos=(0,0,0) rot=(1,0,0;3.14159rad)
  Size = 2
  Size2 = 1
  SupportTransform = false
FEATURE [PartDesign::Chamfer] Chamfer017
  Angle = 45
  Base = -> Chamfer016 [Edge30]
  BaseFeature = -> Chamfer016
  ChamferType = 0
  FlipDirection = false
  Placement = pos=(0,0,0) rot=(1,0,0;3.14159rad)
  Size = 2
  Size2 = 1
  SupportTransform = false
FEATURE [Sketcher::SketchObject] Sketch309
  FullyConstrained = false
  MapMode = 3
  Placement = pos=(0,0,0) rot=(1,0,0;3.14159rad)
  sketch-geometry (9):
    g0: LineSegment StartX=-21.15 StartY=21.25 StartZ=0 EndX=21.15 EndY=21.25 EndZ=0
    g1: LineSegment StartX=21.15 StartY=21.25 StartZ=0 EndX=21.15 EndY=-21.15 EndZ=0
    g2: LineSegment StartX=21.15 StartY=-21.15 StartZ=0 EndX=-21.15 EndY=-21.15 EndZ=0
    g3: LineSegment StartX=-21.15 StartY=-21.15 StartZ=0 EndX=-21.15 EndY=21.25 EndZ=0
    g4: Circle CenterX=0 CenterY=0 CenterZ=0 NormalX=0 NormalY=0 NormalZ=1 AngleXU=0 Radius=11
    g5: Circle CenterX=-15.5 CenterY=15.5 CenterZ=0 NormalX=0 NormalY=0 NormalZ=1 AngleXU=0 Radius=1.5
    g6: Circle CenterX=15.5 CenterY=15.5 CenterZ=0 NormalX=0 NormalY=0 NormalZ=1 AngleXU=0 Radius=1.5
    g7: Circle CenterX=-15.5 CenterY=-15.5 CenterZ=0 NormalX=0 NormalY=0 NormalZ=1 AngleXU=0 Radius=1.5
    g8: Circle CenterX=15.5 CenterY=-15.5 CenterZ=0 NormalX=0 NormalY=0 NormalZ=1 AngleXU=0 Radius=1.5
  constraints (18):
    c: Coincident(g0,g1)
    c: Coincident(g1,g2)
    c: Coincident(g2,g3)
    c: Coincident(g3,g0)
    c: Horizontal(g0)
    c: Horizontal(g2)
    c: Vertical(g1)
    c: Vertical(g3)
    c: Coincident(g4,g-1)
    c: DistanceX(g0,g4) = 21.15
    c: DistanceX(g4,g0) = 21.15
    c: DistanceY(g4,g0) = 21.25
    c: DistanceY(g2,g4) = 21.15
    c: Equal(g5,g6)
    c: Equal(g5,g8)
    c: Equal(g5,g7)
    c: Diameter(g5) = 3
    c: Diameter(g4) = 22
FEATURE [PartDesign::Pad] Pad148
  Direction = (0,2e-16,-1)
  Length = 2
  Length2 = 10
  Placement = pos=(0,0,0) rot=(1,0,0;3.14159rad)
  Profile = -> Sketch309
  Type = 0
FEATURE [Sketcher::SketchObject] Sketch310
  FullyConstrained = false
  MapMode = 5
  Placement = pos=(21.15,0,0) rot=(0.57735,-0.57735,0.57735;4.18879rad)
  sketch-geometry (4):
    g0: LineSegment StartX=-21.15 StartY=0 StartZ=0 EndX=21.25 EndY=1.8e-15 EndZ=0
    g1: LineSegment StartX=21.25 StartY=1.8e-15 StartZ=0 EndX=21.25 EndY=60 EndZ=0
    g2: LineSegment StartX=21.25 StartY=60 StartZ=0 EndX=-21.15 EndY=60 EndZ=0
    g3: LineSegment StartX=-21.15 StartY=60 StartZ=0 EndX=-21.15 EndY=0 EndZ=0
  constraints (8):
    c: Coincident(g0,g1)
    c: Coincident(g1,g2)
    c: Coincident(g2,g3)
    c: Coincident(g3,g0)
    c: Horizontal(g2)
    c: Vertical(g1)
    c: Vertical(g3)
    c: DistanceY(g0,g2) = 60
FEATURE [PartDesign::Pad] Pad149
  BaseFeature = -> Pad148
  Direction = (1,-1e-16,-1e-16)
  Length = 2
  Length2 = 10
  Placement = pos=(0,0,0) rot=(1,0,0;3.14159rad)
  Profile = -> Sketch310
  Type = 0
FEATURE [Sketcher::SketchObject] Sketch308
  ExternalGeometry = -> [Pad149]
  FullyConstrained = false
  Placement = pos=(21.15,-4e-15,-3e-15) rot=(0.57735,0.57735,-0.57735;4.18879rad)
  sketch-geometry (8):
    g0: ArcOfCircle CenterX=-12 CenterY=52 CenterZ=0 NormalX=0 NormalY=0 NormalZ=1 AngleXU=0 Radius=2 StartAngle=0 EndAngle=3.14159
    g1: ArcOfCircle CenterX=-12 CenterY=12 CenterZ=0 NormalX=0 NormalY=0 NormalZ=1 AngleXU=0 Radius=2 StartAngle=3.14159 EndAngle=6.28319
    g2: LineSegment StartX=-10 StartY=52 StartZ=0 EndX=-10 EndY=12 EndZ=0
    g3: LineSegment StartX=-14 StartY=12 StartZ=0 EndX=-14 EndY=52 EndZ=0
    g4: ArcOfCircle CenterX=12 CenterY=52 CenterZ=0 NormalX=0 NormalY=0 NormalZ=1 AngleXU=0 Radius=2 StartAngle=0 EndAngle=3.14159
    g5: ArcOfCircle CenterX=12 CenterY=12 CenterZ=0 NormalX=0 NormalY=0 NormalZ=1 AngleXU=0 Radius=2 StartAngle=3.14159 EndAngle=6.28319
    g6: LineSegment StartX=10 StartY=52 StartZ=0 EndX=10 EndY=12 EndZ=0
    g7: LineSegment StartX=14 StartY=12 StartZ=0 EndX=14 EndY=52 EndZ=0
  constraints (16):
    c: Equal(g0,g1)
    c: Diameter(g1) = 4
    c: DistanceY(g0,g-3) = 8
    c: DistanceY(g1,g0) = 40
    c: DistanceX(g0,g-1) = 12
    c: DistanceX(g1,g-1) = 12
    c: Tangent(g1,g2) = 1.5708
    c: Tangent(g1,g3) = 1.5708
    c: Tangent(g0,g3) = 1.5708
    c: Tangent(g0,g2) = 1.5708
    c: Equal(g4,g5)
    c: Diameter(g5) = 4
    c: Tangent(g5,g6) = -1.5708
    c: Tangent(g5,g7) = -1.5708
    c: Tangent(g4,g7) = -1.5708
    c: Tangent(g4,g6) = -1.5708
FEATURE [PartDesign::Pocket] Pocket118
  BaseFeature = -> Pad149
  Length = 5
  Length2 = 5
  Placement = pos=(0,0,0) rot=(1,0,0;3.14159rad)
  Profile = -> Sketch308
  Type = 0
FEATURE [PartDesign::Chamfer] Chamfer018
  Angle = 45
  Base = -> Pocket118 [Edge1]
  BaseFeature = -> Pocket118
  ChamferType = 0
  FlipDirection = false
  Placement = pos=(0,0,0) rot=(1,0,0;3.14159rad)
  Size = 2
  Size2 = 1
  SupportTransform = false
FEATURE [PartDesign::Chamfer] Chamfer019
  Angle = 45
  Base = -> Chamfer018 [Edge30]
  BaseFeature = -> Chamfer018
  ChamferType = 0
  FlipDirection = false
  Placement = pos=(0,0,0) rot=(1,0,0;3.14159rad)
  Size = 2
  Size2 = 1
  SupportTransform = false
FEATURE [PartDesign::Body] Body230
  Group = -> [Sketch309,Pad148,Sketch310,Pad149,Sketch308,Pocket118,Chamfer018,Chamfer019]
  Origin = -> Origin327
  Tip = -> Chamfer019
FEATURE [App::Part] Part097  label="soporteNEMA019"
  Group = -> [Body230]
  Origin = -> Origin326
  Placement = pos=(0,0,0) rot=(0,1,0;1.5708rad)
  expr: .Placement.Rotation.Angle = 90°
FEATURE [Sketcher::SketchObject] Sketch311
  FullyConstrained = true
  MapMode = 5
  Support = -> [XY_Plane322]
  sketch-geometry (3):
    g0: LineSegment StartX=0 StartY=0 StartZ=0 EndX=6 EndY=0 EndZ=0
    g1: LineSegment StartX=0 StartY=0 StartZ=0 EndX=0 EndY=6 EndZ=0
    g2: LineSegment StartX=0 StartY=6 StartZ=0 EndX=6 EndY=0 EndZ=0
  constraints (8):
    c: Coincident(g0,g-1)
    c: PointOnObject(g0,g-1)
    c: Coincident(g1,g0)
    c: PointOnObject(g1,g-2)
    c: Coincident(g2,g1)
    c: Coincident(g2,g0)
    c: DistanceX(g0,g0) = 6
    c: DistanceY(g0,g1) = 6
FEATURE [PartDesign::Pad] Pad147
  Direction = (0,0,1)
  Length = 2
  Length2 = 10
  Profile = -> Sketch311
  Type = 0
FEATURE [PartDesign::Body] Body229
  Group = -> [Sketch311,Pad147]
  Origin = -> Origin328
  Tip = -> Pad147
FEATURE [App::Part] Part096
  Group = -> [Body229]
  Origin = -> Origin325
  Placement = pos=(-2,21.15,-21.13) rot=(0.57735,-0.57735,0.57735;2.0944rad)
FEATURE [Sketcher::SketchObject] Sketch312
  FullyConstrained = true
  MapMode = 5
  Support = -> [XY_Plane324]
  sketch-geometry (3):
    g0: LineSegment StartX=0 StartY=0 StartZ=0 EndX=6 EndY=0 EndZ=0
    g1: LineSegment StartX=0 StartY=0 StartZ=0 EndX=0 EndY=6 EndZ=0
    g2: LineSegment StartX=0 StartY=6 StartZ=0 EndX=6 EndY=0 EndZ=0
  constraints (8):
    c: Coincident(g0,g-1)
    c: PointOnObject(g0,g-1)
    c: Coincident(g1,g0)
    c: PointOnObject(g1,g-2)
    c: Coincident(g2,g1)
    c: Coincident(g2,g0)
    c: DistanceX(g0,g0) = 6
    c: DistanceY(g0,g1) = 6
FEATURE [PartDesign::Pad] Pad150
  Direction = (0,0,1)
  Length = 2
  Length2 = 10
  Profile = -> Sketch312
  Type = 0
FEATURE [PartDesign::Body] Body231
  Group = -> [Sketch312,Pad150]
  Origin = -> Origin330
  Tip = -> Pad150
FEATURE [App::Part] Part098
  Group = -> [Body231]
  Origin = -> Origin329
  Placement = pos=(-2,-19.24,-21.13) rot=(0.57735,-0.57735,0.57735;2.0944rad)
FEATURE [App::LinkGroup] LinkGroup013  label="SoporteNEMA018-002"
  ElementList = -> [Part097,Part096,Part098]
  LinkMode = 0
  Placement = pos=(400,247,106) rot=(0,0,1;0rad)
FEATURE [App::LinkGroup] LinkGroup014  label="ruedas"
  ElementList = -> [Part037,Part067,Part069]
  LinkMode = 0
FEATURE [App::LinkGroup] LinkGroup016  label="acoples-ejes-motores"
  ElementList = -> [Part086,Part089]
  LinkMode = 0
  Placement = pos=(-1.52588e-05,4.00001,3.8147e-06) rot=(0,0,1;0rad)
FEATURE [PartDesign::ShapeBinder] CopyFillet054
  TraceSupport = false
FEATURE [Sketcher::SketchObject] Sketch313
  FullyConstrained = true
  MapMode = 5
  Placement = pos=(0,-3.4,0) rot=(1,0,0;1.5708rad)
  Support = -> [CopyFillet054]
FEATURE [Sketcher::SketchObject] Sketch314
  FullyConstrained = true
  MapMode = 5
  Placement = pos=(0,0,0) rot=(1,0,0;1.5708rad)
  Support = -> [XZ_Plane315]
FEATURE [PartDesign::ShapeBinder] ReferencePad053
  Placement = pos=(0,0,0) rot=(0.57735,0.57735,0.57735;2.0944rad)
  Support = -> [Pad053]
  TraceSupport = false
FEATURE [Sketcher::SketchObject] Sketch315
  FullyConstrained = true
  MapMode = 5
  Placement = pos=(0,0,0) rot=(0.57735,0.57735,-0.57735;4.18879rad)
  Support = -> [ReferencePad053]
FEATURE [Sketcher::SketchObject] Sketch316
  FullyConstrained = true
  MapMode = 5
  Placement = pos=(0,0,0) rot=(0.57735,0.57735,0.57735;2.0944rad)
  Support = -> [YZ_Plane315]
FEATURE [PartDesign::Body] Body227
  Group = -> [Sketch304,Pad144,Sketch305,Pad145,Sketch303,Pocket117,Chamfer016,Chamfer017,CopyFillet054,Sketch313,Sketch314,ReferencePad053,Sketch315,Sketch316]
  Origin = -> Origin321
  Tip = -> Chamfer017
FEATURE [App::Part] Part094  label="soporteNEMA018"
  Group = -> [Body227]
  Origin = -> Origin320
  Placement = pos=(0,0,0) rot=(0,1,0;1.5708rad)
  expr: .Placement.Rotation.Angle = 90°
FEATURE [App::LinkGroup] LinkGroup012  label="SoporteNEMA017-001"
  ElementList = -> [Part094,Part093,Part095]
  LinkMode = 0
  Placement = pos=(400,121,106) rot=(0,0,1;0rad)
FEATURE [App::LinkGroup] LinkGroup015  label="bases"
  ElementList = -> [Part066,LinkGroup012,LinkGroup013]
  LinkMode = 0
FEATURE [Sketcher::SketchObject] Sketch317
  FullyConstrained = true
  MapMode = 5
  Placement = pos=(0,0,0) rot=(1,0,0;1.5708rad)
  Support = -> [XZ_Plane328]
  sketch-geometry (1):
    g0: Circle CenterX=5.4 CenterY=4.4 CenterZ=0 NormalX=0 NormalY=0 NormalZ=1 AngleXU=0 Radius=0.4
  constraints (3):
    c: Diameter(g0) = 0.8
    c: DistanceY(g0) = 4.4
    c: DistanceX(g0) = 5.4
FEATURE [PartDesign::AdditiveHelix] AdditiveHelix
  Angle = 0
  Axis = (0,-2e-16,1)
  Base = (0,0,0)
  HasBeenEdited = true
  Height = 17.3
  LeftHanded = false
  Mode = 2
  Outside = false
  Pitch = 2.1625
  Placement = pos=(0,0,0) rot=(1,0,0;1.5708rad)
  Profile = -> Sketch317
  ReferenceAxis = -> Sketch317 [V_Axis]
  Turns = 3
FEATURE [PartDesign::Body] Body234  label="Spring"
  Group = -> [Sketch317,AdditiveHelix]
  Origin = -> Origin334
  Tip = -> AdditiveHelix
FEATURE [Sketcher::SketchObject] Sketch318
  FullyConstrained = true
  MapMode = 5
  Placement = pos=(0,0,0) rot=(1,0,0;1.5708rad)
  Support = -> [XZ_Plane326]
  sketch-geometry (6):
    g0: LineSegment StartX=0 StartY=0 StartZ=0 EndX=0 EndY=15 EndZ=0
    g1: LineSegment StartX=0 StartY=15 StartZ=0 EndX=-5 EndY=15 EndZ=0
    g2: LineSegment StartX=-5 StartY=15 StartZ=0 EndX=-5 EndY=4 EndZ=0
    g3: LineSegment StartX=-5 StartY=4 StartZ=0 EndX=-11 EndY=4 EndZ=0
    g4: LineSegment StartX=-11 StartY=4 StartZ=0 EndX=-11 EndY=0 EndZ=0
    g5: LineSegment StartX=-11 StartY=0 StartZ=0 EndX=0 EndY=0 EndZ=0
  constraints (17):
    c: Coincident(g-1,g0)
    c: Coincident(g0,g1)
    c: Coincident(g1,g2)
    c: Coincident(g2,g3)
    c: Horizontal(g3)
    c: Coincident(g3,g4)
    c: Vertical(g4)
    c: Coincident(g4,g5)
    c: Coincident(g5,g0)
    c: Horizontal(g5)
    c: Horizontal(g1)
    c: Vertical(g2)
    c: Vertical(g0)
    c: DistanceY(g0,g0) = 15
    c: DistanceY(g4,g4) = 4
    c: DistanceX(g1,g1) = 5
    c: DistanceX(g5,g5) = 11
FEATURE [PartDesign::Revolution] Revolution053
  Angle = 360
  Axis = (0,2e-16,1)
  Base = (0,0,0)
  Placement = pos=(0,0,0) rot=(1,0,0;1.5708rad)
  Profile = -> Sketch318
  ReferenceAxis = -> Sketch318 [V_Axis]
FEATURE [Sketcher::SketchObject] Sketch319
  FullyConstrained = true
  MapMode = 5
  Placement = pos=(0,1.8e-15,4) rot=(0,0,1;3.14159rad)
  Support = -> [Revolution053]
  sketch-geometry (1):
    g0: Circle CenterX=8 CenterY=0 CenterZ=0 NormalX=0 NormalY=0 NormalZ=1 AngleXU=0 Radius=1.7
  constraints (3):
    c: PointOnObject(g0,g-1)
    c: Diameter(g0) = 3.4
    c: DistanceX(g0) = 8
FEATURE [PartDesign::Pocket] Pocket119
  BaseFeature = -> Revolution053
  Length = 5
  Length2 = 5
  Placement = pos=(0,0,0) rot=(1,0,0;1.5708rad)
  Profile = -> Sketch319
  Type = 2
FEATURE [PartDesign::Chamfer] Chamfer020
  Angle = 45
  Base = -> Pocket119 [Edge5]
  BaseFeature = -> Pocket119
  ChamferType = 0
  FlipDirection = false
  Placement = pos=(0,0,0) rot=(1,0,0;1.5708rad)
  Size = 0.25
  Size2 = 1
  SupportTransform = false
FEATURE [PartDesign::PolarPattern] PolarPattern026
  Angle = 360
  Axis = -> Sketch319 [N_Axis]
  BaseFeature = -> Chamfer020
  Occurrences = 3
  Originals = -> [Pocket119,Chamfer020]
  Placement = pos=(0,0,0) rot=(1,0,0;1.5708rad)
FEATURE [Sketcher::SketchObject] Sketch320
  FullyConstrained = true
  MapMode = 5
  Placement = pos=(0,6.6e-15,15) rot=(0,0,1;3.14159rad)
  Support = -> [PolarPattern026]
  sketch-geometry (1):
    g0: Circle CenterX=0 CenterY=0 CenterZ=0 NormalX=0 NormalY=0 NormalZ=1 AngleXU=0 Radius=3.25
  constraints (2):
    c: Coincident(g0,g-1)
    c: Diameter(g0) = 6.5
FEATURE [PartDesign::Pocket] Pocket120
  BaseFeature = -> PolarPattern026
  Length = 5
  Length2 = 5
  Placement = pos=(0,0,0) rot=(1,0,0;1.5708rad)
  Profile = -> Sketch320
  Type = 2
FEATURE [Sketcher::SketchObject] Sketch321
  ExternalGeometry = -> [Pocket120]
  FullyConstrained = true
  MapMode = 5
  Placement = pos=(0,0,0) rot=(0.57735,0.57735,0.57735;2.0944rad)
  Support = -> [YZ_Plane326]
  sketch-geometry (5):
    g0: LineSegment StartX=-1.7 StartY=11 StartZ=0 EndX=-1.7 EndY=15 EndZ=0
    g1: LineSegment StartX=-1.7 StartY=15 StartZ=0 EndX=1.7 EndY=15 EndZ=0
    g2: LineSegment StartX=1.7 StartY=15 StartZ=0 EndX=1.7 EndY=11 EndZ=0
    g3: LineSegment StartX=1.7 StartY=11 StartZ=0 EndX=-1.7 EndY=11 EndZ=0
    g4: GeomPoint X=0 Y=13 Z=0
  constraints (13):
    c: Coincident(g0,g1)
    c: Coincident(g1,g2)
    c: Coincident(g2,g3)
    c: Coincident(g3,g0)
    c: Horizontal(g1)
    c: Horizontal(g3)
    c: Vertical(g0)
    c: Vertical(g2)
    c: Symmetric(g1,g0,g4)
    c: PointOnObject(g4,g-2)
    c: PointOnObject(g1,g-3)
    c: DistanceX(g3,g3) = 3.4
    c: DistanceY(g2,g2) = 4
FEATURE [PartDesign::Pocket] Pocket121
  BaseFeature = -> Pocket120
  Length = 5
  Length2 = 5
  Midplane = true
  Placement = pos=(0,0,0) rot=(1,0,0;1.5708rad)
  Profile = -> Sketch321
  Type = 1
FEATURE [Sketcher::SketchObject] Sketch322
  FullyConstrained = true
  MapMode = 5
  Placement = pos=(0,0,0) rot=(1,0,0;1.5708rad)
  Support = -> [XZ_Plane327]
  sketch-geometry (6):
    g0: LineSegment StartX=0 StartY=11 StartZ=0 EndX=0 EndY=26 EndZ=0
    g1: LineSegment StartX=0 StartY=26 StartZ=0 EndX=-7 EndY=26 EndZ=0
    g2: LineSegment StartX=-7 StartY=26 StartZ=0 EndX=-7 EndY=22 EndZ=0
    g3: LineSegment StartX=-7 StartY=22 StartZ=0 EndX=-5 EndY=22 EndZ=0
    g4: LineSegment StartX=-5 StartY=22 StartZ=0 EndX=-5 EndY=11 EndZ=0
    g5: LineSegment StartX=-5 StartY=11 StartZ=0 EndX=0 EndY=11 EndZ=0
  constraints (18):
    c: PointOnObject(g0,g-2)
    c: Vertical(g0)
    c: Coincident(g0,g1)
    c: Horizontal(g1)
    c: Coincident(g1,g2)
    c: Vertical(g2)
    c: Coincident(g2,g3)
    c: Horizontal(g3)
    c: Coincident(g3,g4)
    c: Vertical(g4)
    c: Coincident(g4,g5)
    c: Coincident(g5,g0)
    c: Horizontal(g5)
    c: DistanceX(g1,g1) = 7
    c: DistanceX(g5,g5) = 5
    c: DistanceY(g2,g2) = 4
    c: DistanceY(g0,g0) = 15
    c: DistanceY(g0) = 11
FEATURE [PartDesign::Revolution] Revolution054
  Angle = 360
  Axis = (0,2e-16,1)
  Base = (0,0,0)
  Placement = pos=(0,0,0) rot=(1,0,0;1.5708rad)
  Profile = -> Sketch322
  ReferenceAxis = -> Sketch322 [V_Axis]
FEATURE [Sketcher::SketchObject] Sketch323
  FullyConstrained = true
  MapMode = 5
  Placement = pos=(0,1.14e-14,26) rot=(0,0,1;3.14159rad)
  Support = -> [Revolution054]
  sketch-geometry (1):
    g0: Circle CenterX=0 CenterY=0 CenterZ=0 NormalX=0 NormalY=0 NormalZ=1 AngleXU=0 Radius=3.25
  constraints (2):
    c: Coincident(g0,g-1)
    c: Diameter(g0) = 6.5
FEATURE [PartDesign::Pocket] Pocket122
  BaseFeature = -> Revolution054
  Length = 5
  Length2 = 5
  Placement = pos=(0,0,0) rot=(1,0,0;1.5708rad)
  Profile = -> Sketch323
  Type = 2
FEATURE [Sketcher::SketchObject] Sketch324
  ExternalGeometry = -> [Pocket122]
  FullyConstrained = true
  MapMode = 5
  Placement = pos=(0,0,0) rot=(1,0,0;1.5708rad)
  Support = -> [XZ_Plane327]
  sketch-geometry (5):
    g0: LineSegment StartX=-4.75 StartY=15 StartZ=0 EndX=-4.75 EndY=11 EndZ=0
    g1: LineSegment StartX=-4.75 StartY=11 StartZ=0 EndX=4.75 EndY=11 EndZ=0
    g2: LineSegment StartX=4.75 StartY=11 StartZ=0 EndX=4.75 EndY=15 EndZ=0
    g3: LineSegment StartX=4.75 StartY=15 StartZ=0 EndX=-4.75 EndY=15 EndZ=0
    g4: GeomPoint X=0 Y=13 Z=0
  constraints (13):
    c: Coincident(g0,g1)
    c: Coincident(g1,g2)
    c: Coincident(g2,g3)
    c: Coincident(g3,g0)
    c: Horizontal(g1)
    c: Horizontal(g3)
    c: Vertical(g0)
    c: Vertical(g2)
    c: Symmetric(g1,g0,g4)
    c: DistanceX(g1,g1) = 9.5
    c: DistanceY(g2,g2) = 4
    c: PointOnObject(g1,g-3)
    c: PointOnObject(g4,g-2)
FEATURE [PartDesign::Pocket] Pocket123
  BaseFeature = -> Pocket122
  Length = 5
  Length2 = 5
  Midplane = true
  Placement = pos=(0,0,0) rot=(1,0,0;1.5708rad)
  Profile = -> Sketch324
  Type = 1
FEATURE [Sketcher::SketchObject] Sketch325  label="ISO 2904"
  FullyConstrained = true
  MapMode = 5
  Placement = pos=(0,0,0) rot=(1,0,0;1.5708rad)
  Support = -> [XZ_Plane326]
  sketch-geometry (8):
    g0: LineSegment StartX=6.04904 StartY=0.75 StartZ=0 EndX=3.25 EndY=0 EndZ=0
    g1: LineSegment StartX=3.25 StartY=0 StartZ=0 EndX=6.04904 EndY=-0.75 EndZ=0
    g2: LineSegment StartX=6.04904 StartY=-0.75 StartZ=0 EndX=3.25 EndY=-1.5 EndZ=0
    g3: LineSegment StartX=3.25 StartY=-1.5 StartZ=0 EndX=6.04904 EndY=-2.25 EndZ=0
    g4: LineSegment StartX=3.25 StartY=0 StartZ=0 EndX=3.25 EndY=-1.5 EndZ=0
    g5: LineSegment StartX=3.25 StartY=-1.5 StartZ=0 EndX=4.15 EndY=-1.25885 EndZ=0
    g6: LineSegment StartX=4.15 StartY=-1.25885 StartZ=0 EndX=4.15 EndY=-0.241154 EndZ=0
    g7: LineSegment StartX=4.15 StartY=-0.241154 StartZ=0 EndX=3.25 EndY=0 EndZ=0
  constraints (23):
    c: PointOnObject(g0,g-1)
    c: Coincident(g0,g1)
    c: Coincident(g1,g2)
    c: Coincident(g2,g3)
    c: Vertical(g1,g0)
    c: Vertical(g0,g3)
    c: Vertical(g2,g0)
    c: Parallel(g0,g2)
    c: Parallel(g1,g3)
    c: Angle(g3,g2) = 0.523599
    c: Angle(g0,g-1) = 2.87979
    c: Coincident(g0,g4)
    c: Coincident(g4,g2)
    c: Coincident(g4,g5)
    c: PointOnObject(g5,g2)
    c: Coincident(g5,g6)
    c: PointOnObject(g6,g1)
    c: Vertical(g6)
    c: Coincident(g6,g7)
    c: Coincident(g7,g4)
    c: DistanceX(g4) = 3.25
    c: DistanceX(g6) = 4.15
    c: DistanceY(g3,g1) = 1.5
FEATURE [Sketcher::SketchObject] Sketch327
  FullyConstrained = true
  MapMode = 5
  Placement = pos=(0,0,0) rot=(1,0,0;1.5708rad)
  Support = -> [XZ_Plane327]
  sketch-geometry (8):
    g0: LineSegment StartX=6.04904 StartY=0.75 StartZ=0 EndX=3.25 EndY=-1e-16 EndZ=0
    g1: LineSegment StartX=3.25 StartY=-1e-16 StartZ=0 EndX=6.04904 EndY=-0.75 EndZ=0
    g2: LineSegment StartX=6.04904 StartY=-0.75 StartZ=0 EndX=3.25 EndY=-1.5 EndZ=0
    g3: LineSegment StartX=3.25 StartY=-1.5 StartZ=0 EndX=6.04904 EndY=-2.25 EndZ=0
    g4: LineSegment StartX=3.25 StartY=-1e-16 StartZ=0 EndX=3.25 EndY=-1.5 EndZ=0
    g5: LineSegment StartX=3.25 StartY=-1.5 StartZ=0 EndX=4.15 EndY=-1.25885 EndZ=0
    g6: LineSegment StartX=4.15 StartY=-1.25885 StartZ=0 EndX=4.15 EndY=-0.241154 EndZ=0
    g7: LineSegment StartX=4.15 StartY=-0.241154 StartZ=0 EndX=3.25 EndY=-1e-16 EndZ=0
  constraints (23):
    c: PointOnObject(g0,g-1)
    c: Coincident(g0,g1)
    c: Coincident(g1,g2)
    c: Coincident(g2,g3)
    c: Vertical(g3,g1)
    c: Vertical(g1,g0)
    c: Vertical(g0,g2)
    c: Parallel(g3,g1)
    c: Parallel(g2,g0)
    c: Angle(g3,g2) = 0.523599
    c: Angle(g0,g-1) = 2.87979
    c: Coincident(g0,g4)
    c: Coincident(g4,g2)
    c: Coincident(g4,g5)
    c: PointOnObject(g5,g2)
    c: Coincident(g5,g6)
    c: PointOnObject(g6,g1)
    c: Coincident(g6,g7)
    c: Coincident(g7,g4)
    c: Vertical(g6)
    c: DistanceX(g4) = 3.25
    c: DistanceX(g6) = 4.15
    c: DistanceY(g3,g1) = 1.5
FEATURE [Sketcher::SketchObject] Sketch331
  FullyConstrained = false
  MapMode = 5
  Support = -> [XY_Plane329]
  sketch-geometry (7):
    g0: LineSegment StartX=1.45322 StartY=-2.69828 StartZ=0 EndX=3.06339 EndY=-0.0906102 EndZ=0
    g1: LineSegment StartX=3.06339 StartY=-0.0906102 StartZ=0 EndX=1.61017 EndY=2.60767 EndZ=0
    g2: LineSegment StartX=1.61017 StartY=2.60767 StartZ=0 EndX=-1.45322 EndY=2.69828 EndZ=0
    g3: LineSegment StartX=-1.45322 StartY=2.69828 StartZ=0 EndX=-3.06339 EndY=0.0906102 EndZ=0
    g4: LineSegment StartX=-3.06339 StartY=0.0906102 StartZ=0 EndX=-1.61017 EndY=-2.60767 EndZ=0
    g5: LineSegment StartX=-1.61017 StartY=-2.60767 StartZ=0 EndX=1.45322 EndY=-2.69828 EndZ=0
    g6: Circle CenterX=0 CenterY=0 CenterZ=0 NormalX=0 NormalY=0 NormalZ=1 AngleXU=0 Radius=3.06473
  constraints (14):
    c: Coincident(g0,g1)
    c: Coincident(g1,g2)
    c: Coincident(g2,g3)
    c: Coincident(g3,g4)
    c: Coincident(g4,g5)
    c: Coincident(g5,g0)
    c: Equal(g0, g1-g5) x5
    c: PointOnObject(g0,g6)
    c: PointOnObject(g1,g6)
    c: PointOnObject(g2,g6)
    c: PointOnObject(g3,g6)
    c: PointOnObject(g4,g6)
    c: PointOnObject(g5,g6)
    c: Coincident(g6,g-1)
FEATURE [PartDesign::Pad] Pad154
  Direction = (0,0,1)
  Length = 4
  Length2 = 10
  Profile = -> Sketch331
  Refine = true
  Type = 0
FEATURE [Sketcher::SketchObject] Sketch332
  FullyConstrained = false
  MapMode = 5
  Support = -> [XY_Plane330]
  sketch-geometry (7):
    g0: LineSegment StartX=1.45322 StartY=-2.69828 StartZ=0 EndX=3.06339 EndY=-0.0906102 EndZ=0
    g1: LineSegment StartX=3.06339 StartY=-0.0906102 StartZ=0 EndX=1.61017 EndY=2.60767 EndZ=0
    g2: LineSegment StartX=1.61017 StartY=2.60767 StartZ=0 EndX=-1.45322 EndY=2.69828 EndZ=0
    g3: LineSegment StartX=-1.45322 StartY=2.69828 StartZ=0 EndX=-3.06339 EndY=0.0906102 EndZ=0
    g4: LineSegment StartX=-3.06339 StartY=0.0906102 StartZ=0 EndX=-1.61017 EndY=-2.60767 EndZ=0
    g5: LineSegment StartX=-1.61017 StartY=-2.60767 StartZ=0 EndX=1.45322 EndY=-2.69828 EndZ=0
    g6: Circle CenterX=0 CenterY=0 CenterZ=0 NormalX=0 NormalY=0 NormalZ=1 AngleXU=0 Radius=3.06473
  constraints (14):
    c: Coincident(g0,g1)
    c: Coincident(g1,g2)
    c: Coincident(g2,g3)
    c: Coincident(g3,g4)
    c: Coincident(g4,g5)
    c: Coincident(g5,g0)
    c: Equal(g0, g1-g5) x5
    c: PointOnObject(g0,g6)
    c: PointOnObject(g1,g6)
    c: PointOnObject(g2,g6)
    c: PointOnObject(g3,g6)
    c: PointOnObject(g4,g6)
    c: PointOnObject(g5,g6)
    c: Coincident(g6,g-1)
FEATURE [PartDesign::Pad] Pad155
  Direction = (0,0,1)
  Length = 4
  Length2 = 10
  Profile = -> Sketch332
  Refine = true
  Type = 0
FEATURE [PartDesign::Body] Body236
  Group = -> [Sketch332,Pad155]
  Origin = -> Origin336
  Placement = pos=(0,-8,-6.97) rot=(0,0,1;0rad)
  Tip = -> Pad155
FEATURE [Sketcher::SketchObject] Sketch333
  FullyConstrained = false
  MapMode = 5
  Support = -> [XY_Plane331]
  sketch-geometry (7):
    g0: LineSegment StartX=1.45322 StartY=-2.69828 StartZ=0 EndX=3.06339 EndY=-0.0906102 EndZ=0
    g1: LineSegment StartX=3.06339 StartY=-0.0906102 StartZ=0 EndX=1.61017 EndY=2.60767 EndZ=0
    g2: LineSegment StartX=1.61017 StartY=2.60767 StartZ=0 EndX=-1.45322 EndY=2.69828 EndZ=0
    g3: LineSegment StartX=-1.45322 StartY=2.69828 StartZ=0 EndX=-3.06339 EndY=0.0906102 EndZ=0
    g4: LineSegment StartX=-3.06339 StartY=0.0906102 StartZ=0 EndX=-1.61017 EndY=-2.60767 EndZ=0
    g5: LineSegment StartX=-1.61017 StartY=-2.60767 StartZ=0 EndX=1.45322 EndY=-2.69828 EndZ=0
    g6: Circle CenterX=0 CenterY=0 CenterZ=0 NormalX=0 NormalY=0 NormalZ=1 AngleXU=0 Radius=3.06473
  constraints (14):
    c: Coincident(g0,g1)
    c: Coincident(g1,g2)
    c: Coincident(g2,g3)
    c: Coincident(g3,g4)
    c: Coincident(g4,g5)
    c: Coincident(g5,g0)
    c: Equal(g0, g1-g5) x5
    c: PointOnObject(g0,g6)
    c: PointOnObject(g1,g6)
    c: PointOnObject(g2,g6)
    c: PointOnObject(g3,g6)
    c: PointOnObject(g4,g6)
    c: PointOnObject(g5,g6)
    c: Coincident(g6,g-1)
FEATURE [PartDesign::Pad] Pad156
  Direction = (0,0,1)
  Length = 4
  Length2 = 10
  Profile = -> Sketch333
  Refine = true
  Type = 0
FEATURE [PartDesign::Body] Body237
  Group = -> [Sketch333,Pad156]
  Origin = -> Origin337
  Placement = pos=(-0.04,8,-6.97) rot=(0,0,1;0rad)
  Tip = -> Pad156
FEATURE [Sketcher::SketchObject] Sketch334
  FullyConstrained = false
  MapMode = 5
  Support = -> [XY_Plane332]
  sketch-geometry (7):
    g0: LineSegment StartX=1.45322 StartY=-2.69828 StartZ=0 EndX=3.06339 EndY=-0.0906102 EndZ=0
    g1: LineSegment StartX=3.06339 StartY=-0.0906102 StartZ=0 EndX=1.61017 EndY=2.60767 EndZ=0
    g2: LineSegment StartX=1.61017 StartY=2.60767 StartZ=0 EndX=-1.45322 EndY=2.69828 EndZ=0
    g3: LineSegment StartX=-1.45322 StartY=2.69828 StartZ=0 EndX=-3.06339 EndY=0.0906102 EndZ=0
    g4: LineSegment StartX=-3.06339 StartY=0.0906102 StartZ=0 EndX=-1.61017 EndY=-2.60767 EndZ=0
    g5: LineSegment StartX=-1.61017 StartY=-2.60767 StartZ=0 EndX=1.45322 EndY=-2.69828 EndZ=0
    g6: Circle CenterX=0 CenterY=0 CenterZ=0 NormalX=0 NormalY=0 NormalZ=1 AngleXU=0 Radius=3.06473
  constraints (14):
    c: Coincident(g0,g1)
    c: Coincident(g1,g2)
    c: Coincident(g2,g3)
    c: Coincident(g3,g4)
    c: Coincident(g4,g5)
    c: Coincident(g5,g0)
    c: Equal(g0, g1-g5) x5
    c: PointOnObject(g0,g6)
    c: PointOnObject(g1,g6)
    c: PointOnObject(g2,g6)
    c: PointOnObject(g3,g6)
    c: PointOnObject(g4,g6)
    c: PointOnObject(g5,g6)
    c: Coincident(g6,g-1)
FEATURE [PartDesign::Pad] Pad157
  Direction = (0,0,1)
  Length = 4
  Length2 = 10
  Profile = -> Sketch334
  Refine = true
  Type = 0
FEATURE [PartDesign::Body] Body238
  Group = -> [Sketch334,Pad157]
  Origin = -> Origin338
  Placement = pos=(-8,-0.06,-6.97) rot=(0,0,1;0rad)
  Tip = -> Pad157
FEATURE [PartDesign::SubtractiveHelix] SubtractiveHelix
  Angle = 0
  Axis = (0,2e-16,1)
  Base = (0,0,0)
  BaseFeature = -> Pocket121
  HasBeenEdited = true
  Height = 20
  LeftHanded = false
  Mode = 0
  Outside = false
  Pitch = 8
  Placement = pos=(0,0,0) rot=(1,0,0;1.5708rad)
  Profile = -> Sketch325
  ReferenceAxis = -> Sketch325 [V_Axis]
  Turns = 3
FEATURE [PartDesign::PolarPattern] PolarPattern027
  Angle = 360
  Axis = -> Sketch325 [V_Axis]
  BaseFeature = -> SubtractiveHelix
  Occurrences = 3
  Originals = -> [SubtractiveHelix]
  Placement = pos=(0,0,0) rot=(1,0,0;1.5708rad)
FEATURE [Sketcher::SketchObject] Sketch326
  ExternalGeometry = -> [PolarPattern027]
  FullyConstrained = true
  MapMode = 5
  Placement = pos=(0,0,0) rot=(1,0,0;1.5708rad)
  Support = -> [XZ_Plane326]
  sketch-geometry (6):
    g0: LineSegment StartX=-4.25 StartY=0 StartZ=0 EndX=-3.25 EndY=0 EndZ=0
    g1: LineSegment StartX=-3.25 StartY=0 StartZ=0 EndX=-3.25 EndY=1 EndZ=0
    g2: LineSegment StartX=-3.25 StartY=1 StartZ=0 EndX=-4.25 EndY=0 EndZ=0
    g3: LineSegment StartX=-4.25 StartY=15 StartZ=0 EndX=-3.25 EndY=14 EndZ=0
    g4: LineSegment StartX=-3.25 StartY=14 StartZ=0 EndX=-3.25 EndY=15 EndZ=0
    g5: LineSegment StartX=-3.25 StartY=15 StartZ=0 EndX=-4.25 EndY=15 EndZ=0
  constraints (18):
    c: PointOnObject(g0,g-1)
    c: PointOnObject(g0,g-1)
    c: Coincident(g0,g1)
    c: Vertical(g1)
    c: Coincident(g1,g2)
    c: Coincident(g2,g0)
    c: PointOnObject(g3,g-3)
    c: Coincident(g3,g4)
    c: Vertical(g4)
    c: Coincident(g4,g5)
    c: Horizontal(g5)
    c: Coincident(g5,g3)
    c: Equal(g4,g5)
    c: Equal(g5,g1)
    c: Equal(g1,g0)
    c: DistanceX(g0,g0) = 1
    c: DistanceX(g0) = -3.25
    c: Vertical(g1,g3)
FEATURE [PartDesign::Groove] Groove006
  Angle = 360
  Axis = (0,2e-16,1)
  Base = (0,0,0)
  BaseFeature = -> PolarPattern027
  Placement = pos=(0,0,0) rot=(1,0,0;1.5708rad)
  Profile = -> Sketch326
  ReferenceAxis = -> Sketch326 [V_Axis]
  Reversed = true
FEATURE [Sketcher::SketchObject] Sketch329
  ExternalGeometry = -> [Groove006]
  FullyConstrained = false
  MapMode = 5
  Support = -> [XY_Plane326]
  sketch-geometry (22):
    g0: ArcOfCircle CenterX=0 CenterY=1.8e-15 CenterZ=0 NormalX=0 NormalY=0 NormalZ=1 AngleXU=0 Radius=12 StartAngle=6.12177 EndAngle=8.69593
    g1: Circle CenterX=0 CenterY=8 CenterZ=0 NormalX=0 NormalY=0 NormalZ=1 AngleXU=0 Radius=1.95
    g2: Circle CenterX=8 CenterY=4.4e-15 CenterZ=0 NormalX=0 NormalY=0 NormalZ=1 AngleXU=0 Radius=1.95
    g3: Circle CenterX=-8 CenterY=0 CenterZ=0 NormalX=0 NormalY=0 NormalZ=1 AngleXU=0 Radius=1.95
    g4: Circle CenterX=0 CenterY=-8 CenterZ=0 NormalX=0 NormalY=0 NormalZ=1 AngleXU=0 Radius=1.95
    g5: GeomPoint X=0 Y=1.8e-15 Z=0
    g6: GeomPoint X=0 Y=-25 Z=0
    g7: ArcOfCircle CenterX=0 CenterY=-25 CenterZ=0 NormalX=0 NormalY=0 NormalZ=1 AngleXU=0 Radius=7.5 StartAngle=3.3289 EndAngle=5.4508
    g8: Circle CenterX=0 CenterY=-25 CenterZ=0 NormalX=0 NormalY=0 NormalZ=1 AngleXU=0 Radius=4
    g9: LineSegment StartX=11.844 StartY=-1.92855 StartZ=0 EndX=8.25015 EndY=-24 EndZ=0
    g10: LineSegment StartX=-10.8555 StartY=-8.00001 StartZ=0 EndX=-7.36882 EndY=-26.3966 EndZ=0
    g11: LineSegment StartX=-25 StartY=7.99214 StartZ=0 EndX=-8.9513 EndY=7.99214 EndZ=0
    g12: LineSegment StartX=-25 StartY=-8 StartZ=0 EndX=-25 EndY=7.99214 EndZ=0
    g13: GeomPoint X=0 Y=12 Z=0
    g14: GeomPoint X=0 Y=-11 Z=0
    g15: LineSegment StartX=20 StartY=-30.5465 StartZ=0 EndX=5.04838 EndY=-30.5465 EndZ=0
    g16: LineSegment StartX=8.25015 StartY=-24 StartZ=0 EndX=20 EndY=-24 EndZ=0
    g17: LineSegment StartX=20 StartY=-24 StartZ=0 EndX=20 EndY=-30.5465 EndZ=0
    g18: GeomPoint X=1.59796e-10 Y=-29 Z=0
    g19: GeomPoint X=0 Y=-21 Z=0
    g20: LineSegment StartX=-10.8555 StartY=-8.00001 StartZ=0 EndX=-25 EndY=-8 EndZ=0
    g21: Circle CenterX=0 CenterY=1.8e-15 CenterZ=0 NormalX=0 NormalY=0 NormalZ=1 AngleXU=0 Radius=3.24154
  constraints (42):
    c: Coincident(g0,g-3)
    c: Coincident(g1,g-4)
    c: Coincident(g2,g-6)
    c: Coincident(g3,g-7)
    c: Coincident(g4,g-5)
    c: Equal(g1,g2)
    c: Equal(g2,g4)
    c: Equal(g4,g3)
    c: Diameter(g2) = 3.9
    c: Coincident(g5,g0)
    c: PointOnObject(g6,g-2)
    c: DistanceY(g6,g0) = 25
    c: Coincident(g7,g6)
    c: Coincident(g8,g7)
    c: Diameter(g8) = 8
    c: Diameter(g7) = 15
    c: Diameter(g-3) = 22
    c: Diameter(g0) = 24
    c: Tangent(g0,g9) = 1.5708
    c: Tangent(g7,g10) = -1.5708
    c: Coincident(g20,g12)
    c: Coincident(g12,g11)
    c: Horizontal(g11)
    c: Vertical(g12)
    c: PointOnObject(g13,g0)
    c: DistanceX(g13,g-1) = 0
    c: PointOnObject(g14,g-3)
    c: DistanceX(g11,g1) = 25
    c: Coincident(g16,g17)
    c: Coincident(g17,g15)
    c: Horizontal(g15)
    c: Horizontal(g16)
    c: Vertical(g17)
    c: PointOnObject(g18,g8)
    c: PointOnObject(g19,g8)
    c: DistanceX(g19,g-1) = 0
    c: DistanceX(g18,g15) = 20
    c: Coincident(g10,g20)
    c: Coincident(g0,g11)
    c: Coincident(g16,g9)
    c: Coincident(g15,g7)
    c: Coincident(g21,g0)
FEATURE [PartDesign::Pad] Pad151
  BaseFeature = -> Groove006
  Direction = (0,0,1)
  Length = 3
  Length2 = 10
  Placement = pos=(0,0,0) rot=(1,0,0;1.5708rad)
  Profile = -> Sketch329
  Refine = true
  Reversed = true
  Type = 0
  UseCustomVector = true
FEATURE [PartDesign::Fillet] Fillet178
  Base = -> Pad151 [Edge115]
  BaseFeature = -> Pad151
  Placement = pos=(0,0,0) rot=(1,0,0;1.5708rad)
  Radius = 1
  Refine = true
  SupportTransform = false
FEATURE [PartDesign::Fillet] Fillet179
  Base = -> Fillet178 [Edge19,Edge15]
  BaseFeature = -> Fillet178
  Placement = pos=(0,0,0) rot=(1,0,0;1.5708rad)
  Radius = 2
  Refine = true
  SupportTransform = false
FEATURE [PartDesign::Fillet] Fillet180
  Base = -> Fillet179 [Edge39]
  BaseFeature = -> Fillet179
  Placement = pos=(0,0,0) rot=(1,0,0;1.5708rad)
  Radius = 1
  Refine = true
  SupportTransform = false
FEATURE [PartDesign::Fillet] Fillet181
  Base = -> Fillet180 [Edge28,Edge24]
  BaseFeature = -> Fillet180
  Placement = pos=(0,0,0) rot=(1,0,0;1.5708rad)
  Radius = 2
  Refine = true
  SupportTransform = false
FEATURE [PartDesign::Fillet] Fillet182
  Base = -> Fillet181 [Edge34]
  BaseFeature = -> Fillet181
  Placement = pos=(0,0,0) rot=(1,0,0;1.5708rad)
  Radius = 1
  Refine = true
  SupportTransform = false
FEATURE [PartDesign::Pad] Pad152
  BaseFeature = -> Fillet182
  Direction = (0,0,1)
  Length = 15
  Length2 = 10
  Midplane = true
  Placement = pos=(0,0,0) rot=(1,0,0;1.5708rad)
  Refine = true
  Type = 0
FEATURE [Sketcher::SketchObject] Sketch330
  ExternalGeometry = -> [Pad152]
  FullyConstrained = true
  MapMode = 5
  Support = -> [XY_Plane326]
  sketch-geometry (4):
    g0: Circle CenterX=0 CenterY=8 CenterZ=0 NormalX=0 NormalY=0 NormalZ=1 AngleXU=0 Radius=2.25
    g1: Circle CenterX=8 CenterY=0 CenterZ=0 NormalX=0 NormalY=0 NormalZ=1 AngleXU=0 Radius=2.25
    g2: Circle CenterX=-8 CenterY=4.6e-15 CenterZ=0 NormalX=0 NormalY=0 NormalZ=1 AngleXU=0 Radius=2.25
    g3: Circle CenterX=0 CenterY=-8 CenterZ=0 NormalX=0 NormalY=0 NormalZ=1 AngleXU=0 Radius=2.25
  constraints (8):
    c: Coincident(g0,g-3)
    c: Coincident(g1,g-4)
    c: Coincident(g2,g-5)
    c: Coincident(g3,g-6)
    c: Diameter(g0) = 4.5
    c: Equal(g1,g2)
    c: Equal(g1,g3)
    c: Diameter(g1) = 4.5
FEATURE [PartDesign::Pad] Pad153
  BaseFeature = -> Pad152
  Direction = (0,0,1)
  Length = 8
  Length2 = 10
  Offset = 5
  Placement = pos=(0,0,0) rot=(1,0,0;1.5708rad)
  Profile = -> Sketch330
  Refine = true
  Type = 0
FEATURE [PartDesign::Body] Body232  label="Bottom"
  Group = -> [Sketch318,Revolution053,Sketch319,Pocket119,Chamfer020,PolarPattern026,Sketch320,Pocket120,Sketch321,Pocket121,Sketch325,SubtractiveHelix,PolarPattern027,Sketch326,Groove006,Sketch329,Pad151,Fillet178,Fillet179,Fillet180,Fillet181,Fillet182,Pad152,Sketch330,Pad153]
  Origin = -> Origin332
  Tip = -> Pad153
FEATURE [PartDesign::ShapeBinder] ReferencePad002
  Support = -> [Pad153]
  TraceSupport = false
FEATURE [PartDesign::Body] Body235
  Group = -> [Sketch331,Pad154,ReferencePad002]
  Origin = -> Origin335
  Placement = pos=(7.96,-0.06,-6.97) rot=(0,0,1;0rad)
  Tip = -> Pad154
FEATURE [PartDesign::SubtractiveHelix] SubtractiveHelix001
  Angle = 0
  Axis = (0,2e-16,1)
  Base = (0,0,0)
  BaseFeature = -> Pocket123
  HasBeenEdited = true
  Height = 30
  LeftHanded = false
  Mode = 0
  Outside = false
  Pitch = 8
  Placement = pos=(0,0,0) rot=(1,0,0;1.5708rad)
  Profile = -> Sketch327
  ReferenceAxis = -> Sketch327 [V_Axis]
  Turns = 3
FEATURE [PartDesign::PolarPattern] PolarPattern028
  Angle = 360
  Axis = -> Sketch327 [V_Axis]
  BaseFeature = -> SubtractiveHelix001
  Occurrences = 3
  Originals = -> [SubtractiveHelix001]
  Placement = pos=(0,0,0) rot=(1,0,0;1.5708rad)
FEATURE [Sketcher::SketchObject] Sketch328
  ExternalGeometry = -> [PolarPattern028]
  FullyConstrained = true
  MapMode = 5
  Placement = pos=(0,0,0) rot=(1,0,0;1.5708rad)
  Support = -> [XZ_Plane327]
  sketch-geometry (6):
    g0: LineSegment StartX=-4.25 StartY=26 StartZ=0 EndX=-3.25 EndY=26 EndZ=0
    g1: LineSegment StartX=-3.25 StartY=26 StartZ=0 EndX=-3.25 EndY=25 EndZ=0
    g2: LineSegment StartX=-3.25 StartY=25 StartZ=0 EndX=-4.25 EndY=26 EndZ=0
    g3: LineSegment StartX=-4.25 StartY=15 StartZ=0 EndX=-3.25 EndY=15 EndZ=0
    g4: LineSegment StartX=-3.25 StartY=15 StartZ=0 EndX=-3.25 EndY=16 EndZ=0
    g5: LineSegment StartX=-3.25 StartY=16 StartZ=0 EndX=-4.25 EndY=15 EndZ=0
  constraints (18):
    c: PointOnObject(g0,g-3)
    c: PointOnObject(g0,g-3)
    c: Coincident(g0,g1)
    c: Coincident(g1,g2)
    c: Coincident(g2,g0)
    c: PointOnObject(g3,g-4)
    c: PointOnObject(g3,g-4)
    c: Coincident(g3,g4)
    c: Vertical(g4)
    c: Coincident(g4,g5)
    c: Coincident(g5,g3)
    c: Vertical(g4,g1)
    c: Vertical(g1)
    c: Equal(g0,g1)
    c: Equal(g1,g3)
    c: Equal(g3,g4)
    c: DistanceX(g3,g3) = 1
    c: DistanceX(g3) = -3.25
FEATURE [PartDesign::Groove] Groove007
  Angle = 360
  Axis = (0,2e-16,1)
  Base = (0,0,0)
  BaseFeature = -> PolarPattern028
  Placement = pos=(0,0,0) rot=(1,0,0;1.5708rad)
  Profile = -> Sketch328
  ReferenceAxis = -> Sketch328 [V_Axis]
  Reversed = true
FEATURE [PartDesign::Body] Body233  label="Top"
  Group = -> [Sketch322,Revolution054,Sketch323,Pocket122,Sketch324,Pocket123,Sketch327,SubtractiveHelix001,PolarPattern028,Sketch328,Groove007]
  Origin = -> Origin333
  Tip = -> Groove007
FEATURE [App::Part] Part099  label="T8 antibacklash nut"
  Group = -> [Body232,Body233,Body234]
  Origin = -> Origin331
FEATURE [App::LinkGroup] LinkGroup017
  ElementList = -> [Body235,Body236,Body237,Body238]
  LinkMode = 0
FEATURE [App::LinkGroup] LinkGroup018  label="SoporteSensor"
  ElementList = -> [LinkGroup017,Part099]
  LinkMode = 0
  Placement = pos=(192.75,119.723,105.027) rot=(0.57735,-0.57735,-0.57735;2.0944rad)
FEATURE [Part::Cylinder] Cylinder  label="sensor"
  Angle = 360
  AttacherType = Attacher::AttachEngine3D
  Height = 22
  Placement = pos=(194,145,105) rot=(-1,0,0;1.5708rad)
  Radius = 8
FEATURE [App::LinkGroup] LinkGroup019  label="sensorSoporte"
  ElementList = -> [Cylinder,LinkGroup018]
  LinkMode = 0
  Placement = pos=(0,0.299999,0) rot=(0,0,1;0rad)
FEATURE [Sketcher::SketchObject] Sketch335
  FullyConstrained = false
  MapMode = 5
  Placement = pos=(0,0,0) rot=(0.57735,0.57735,0.57735;2.0944rad)
  Support = -> [YZ_Plane334]
  sketch-geometry (8):
    g0: LineSegment StartX=2.8963 StartY=-2.75889 StartZ=0 EndX=3.83742 EndY=1.12882 EndZ=0
    g1: LineSegment StartX=3.83742 StartY=1.12882 StartZ=0 EndX=0.941117 EndY=3.88771 EndZ=0
    g2: LineSegment StartX=0.941117 StartY=3.88771 StartZ=0 EndX=-2.8963 EndY=2.75889 EndZ=0
    g3: LineSegment StartX=-2.8963 StartY=2.75889 StartZ=0 EndX=-3.83742 EndY=-1.12882 EndZ=0
    g4: LineSegment StartX=-3.83742 StartY=-1.12882 StartZ=0 EndX=-0.941117 EndY=-3.88771 EndZ=0
    g5: LineSegment StartX=-0.941117 StartY=-3.88771 StartZ=0 EndX=2.8963 EndY=-2.75889 EndZ=0
    g6: Circle CenterX=0 CenterY=0 CenterZ=0 NormalX=0 NormalY=0 NormalZ=1 AngleXU=0 Radius=4
    g7: Circle CenterX=0 CenterY=0 CenterZ=0 NormalX=0 NormalY=0 NormalZ=1 AngleXU=0 Radius=2.5
  constraints (17):
    c: Coincident(g0,g1)
    c: Coincident(g1,g2)
    c: Coincident(g2,g3)
    c: Coincident(g3,g4)
    c: Coincident(g4,g5)
    c: Coincident(g5,g0)
    c: Equal(g0, g1-g5) x5
    c: PointOnObject(g0,g6)
    c: PointOnObject(g1,g6)
    c: PointOnObject(g2,g6)
    c: PointOnObject(g3,g6)
    c: PointOnObject(g4,g6)
    c: PointOnObject(g5,g6)
    c: Coincident(g6,g-1)
    c: Coincident(g7,g6)
    c: Radius(g7) = 2.5
    c: Radius(g6) = 4
FEATURE [PartDesign::Pad] Pad158
  Direction = (1,-2e-16,3e-16)
  Length = 3
  Length2 = 10
  Placement = pos=(0,0,0) rot=(0.57735,0.57735,0.57735;2.0944rad)
  Profile = -> Sketch335
  Type = 0
FEATURE [PartDesign::Pad] Pad159
  BaseFeature = -> Pad158
  Direction = (1,-2e-16,6e-16)
  Length = 15
  Length2 = 10
  Placement = pos=(0,0,0) rot=(0.57735,0.57735,0.57735;2.0944rad)
  Profile = -> Pad158 [Edge20]
  Type = 0
FEATURE [PartDesign::Body] Body239
  Group = -> [Sketch335,Pad158,Pad159]
  Origin = -> Origin340
  Tip = -> Pad159
FEATURE [App::Part] Part100  label="tornillo M5-15-013"
  Group = -> [Body239]
  Origin = -> Origin339
  Placement = pos=(31,10,26) rot=(0,1,0;1.5708rad)
FEATURE [Sketcher::SketchObject] Sketch336
  FullyConstrained = false
  MapMode = 5
  Placement = pos=(0,0,0) rot=(0.57735,0.57735,0.57735;2.0944rad)
  Support = -> [YZ_Plane336]
  sketch-geometry (8):
    g0: LineSegment StartX=2.8963 StartY=-2.75889 StartZ=0 EndX=3.83742 EndY=1.12882 EndZ=0
    g1: LineSegment StartX=3.83742 StartY=1.12882 StartZ=0 EndX=0.941117 EndY=3.88771 EndZ=0
    g2: LineSegment StartX=0.941117 StartY=3.88771 StartZ=0 EndX=-2.8963 EndY=2.75889 EndZ=0
    g3: LineSegment StartX=-2.8963 StartY=2.75889 StartZ=0 EndX=-3.83742 EndY=-1.12882 EndZ=0
    g4: LineSegment StartX=-3.83742 StartY=-1.12882 StartZ=0 EndX=-0.941117 EndY=-3.88771 EndZ=0
    g5: LineSegment StartX=-0.941117 StartY=-3.88771 StartZ=0 EndX=2.8963 EndY=-2.75889 EndZ=0
    g6: Circle CenterX=0 CenterY=0 CenterZ=0 NormalX=0 NormalY=0 NormalZ=1 AngleXU=0 Radius=4
    g7: Circle CenterX=0 CenterY=0 CenterZ=0 NormalX=0 NormalY=0 NormalZ=1 AngleXU=0 Radius=2.5
  constraints (17):
    c: Coincident(g0,g1)
    c: Coincident(g1,g2)
    c: Coincident(g2,g3)
    c: Coincident(g3,g4)
    c: Coincident(g4,g5)
    c: Coincident(g5,g0)
    c: Equal(g0, g1-g5) x5
    c: PointOnObject(g0,g6)
    c: PointOnObject(g1,g6)
    c: PointOnObject(g2,g6)
    c: PointOnObject(g3,g6)
    c: PointOnObject(g4,g6)
    c: PointOnObject(g5,g6)
    c: Coincident(g6,g-1)
    c: Coincident(g7,g6)
    c: Radius(g7) = 2.5
    c: Radius(g6) = 4
FEATURE [PartDesign::Pad] Pad160
  Direction = (1,-2e-16,3e-16)
  Length = 3
  Length2 = 10
  Placement = pos=(0,0,0) rot=(0.57735,0.57735,0.57735;2.0944rad)
  Profile = -> Sketch336
  Type = 0
FEATURE [PartDesign::Pad] Pad161
  BaseFeature = -> Pad160
  Direction = (1,-2e-16,6e-16)
  Length = 15
  Length2 = 10
  Placement = pos=(0,0,0) rot=(0.57735,0.57735,0.57735;2.0944rad)
  Profile = -> Pad160 [Edge20]
  Type = 0
FEATURE [PartDesign::Body] Body240
  Group = -> [Sketch336,Pad160,Pad161]
  Origin = -> Origin342
  Tip = -> Pad161
FEATURE [App::Part] Part101  label="tornillo M5-15-014"
  Group = -> [Body240]
  Origin = -> Origin341
  Placement = pos=(26,10,33) rot=(0,1,0;3.14159rad)
FEATURE [Sketcher::SketchObject] Sketch337
  FullyConstrained = false
  MapMode = 5
  Placement = pos=(0,0,0) rot=(0.57735,0.57735,0.57735;2.0944rad)
  Support = -> [YZ_Plane337]
  sketch-geometry (8):
    g0: LineSegment StartX=2.8963 StartY=-2.75889 StartZ=0 EndX=3.83742 EndY=1.12882 EndZ=0
    g1: LineSegment StartX=3.83742 StartY=1.12882 StartZ=0 EndX=0.941117 EndY=3.88771 EndZ=0
    g2: LineSegment StartX=0.941117 StartY=3.88771 StartZ=0 EndX=-2.8963 EndY=2.75889 EndZ=0
    g3: LineSegment StartX=-2.8963 StartY=2.75889 StartZ=0 EndX=-3.83742 EndY=-1.12882 EndZ=0
    g4: LineSegment StartX=-3.83742 StartY=-1.12882 StartZ=0 EndX=-0.941117 EndY=-3.88771 EndZ=0
    g5: LineSegment StartX=-0.941117 StartY=-3.88771 StartZ=0 EndX=2.8963 EndY=-2.75889 EndZ=0
    g6: Circle CenterX=0 CenterY=0 CenterZ=0 NormalX=0 NormalY=0 NormalZ=1 AngleXU=0 Radius=4
    g7: Circle CenterX=0 CenterY=0 CenterZ=0 NormalX=0 NormalY=0 NormalZ=1 AngleXU=0 Radius=2.5
  constraints (17):
    c: Coincident(g0,g1)
    c: Coincident(g1,g2)
    c: Coincident(g2,g3)
    c: Coincident(g3,g4)
    c: Coincident(g4,g5)
    c: Coincident(g5,g0)
    c: Equal(g0, g1-g5) x5
    c: PointOnObject(g0,g6)
    c: PointOnObject(g1,g6)
    c: PointOnObject(g2,g6)
    c: PointOnObject(g3,g6)
    c: PointOnObject(g4,g6)
    c: PointOnObject(g5,g6)
    c: Coincident(g6,g-1)
    c: Coincident(g7,g6)
    c: Radius(g7) = 2.5
    c: Radius(g6) = 4
FEATURE [PartDesign::Pad] Pad162
  Direction = (1,-2e-16,3e-16)
  Length = 3
  Length2 = 10
  Placement = pos=(0,0,0) rot=(0.57735,0.57735,0.57735;2.0944rad)
  Profile = -> Sketch337
  Type = 0
FEATURE [PartDesign::Pad] Pad163
  BaseFeature = -> Pad162
  Direction = (1,-2e-16,6e-16)
  Length = 15
  Length2 = 10
  Placement = pos=(0,0,0) rot=(0.57735,0.57735,0.57735;2.0944rad)
  Profile = -> Pad162 [Edge20]
  Type = 0
FEATURE [PartDesign::Body] Body241
  Group = -> [Sketch337,Pad162,Pad163]
  Origin = -> Origin344
  Tip = -> Pad163
FEATURE [App::Part] Part102  label="tornillo M5-15-015"
  Group = -> [Body241]
  Origin = -> Origin343
  Placement = pos=(26,10,159) rot=(0,1,0;3.14159rad)
FEATURE [Sketcher::SketchObject] Sketch338
  FullyConstrained = false
  MapMode = 5
  Placement = pos=(0,0,0) rot=(0.57735,0.57735,0.57735;2.0944rad)
  Support = -> [YZ_Plane339]
  sketch-geometry (8):
    g0: LineSegment StartX=2.8963 StartY=-2.75889 StartZ=0 EndX=3.83742 EndY=1.12882 EndZ=0
    g1: LineSegment StartX=3.83742 StartY=1.12882 StartZ=0 EndX=0.941117 EndY=3.88771 EndZ=0
    g2: LineSegment StartX=0.941117 StartY=3.88771 StartZ=0 EndX=-2.8963 EndY=2.75889 EndZ=0
    g3: LineSegment StartX=-2.8963 StartY=2.75889 StartZ=0 EndX=-3.83742 EndY=-1.12882 EndZ=0
    g4: LineSegment StartX=-3.83742 StartY=-1.12882 StartZ=0 EndX=-0.941117 EndY=-3.88771 EndZ=0
    g5: LineSegment StartX=-0.941117 StartY=-3.88771 StartZ=0 EndX=2.8963 EndY=-2.75889 EndZ=0
    g6: Circle CenterX=0 CenterY=0 CenterZ=0 NormalX=0 NormalY=0 NormalZ=1 AngleXU=0 Radius=4
    g7: Circle CenterX=0 CenterY=0 CenterZ=0 NormalX=0 NormalY=0 NormalZ=1 AngleXU=0 Radius=2.5
  constraints (17):
    c: Coincident(g0,g1)
    c: Coincident(g1,g2)
    c: Coincident(g2,g3)
    c: Coincident(g3,g4)
    c: Coincident(g4,g5)
    c: Coincident(g5,g0)
    c: Equal(g0, g1-g5) x5
    c: PointOnObject(g0,g6)
    c: PointOnObject(g1,g6)
    c: PointOnObject(g2,g6)
    c: PointOnObject(g3,g6)
    c: PointOnObject(g4,g6)
    c: PointOnObject(g5,g6)
    c: Coincident(g6,g-1)
    c: Coincident(g7,g6)
    c: Radius(g7) = 2.5
    c: Radius(g6) = 4
FEATURE [PartDesign::Pad] Pad164
  Direction = (1,-2e-16,3e-16)
  Length = 3
  Length2 = 10
  Placement = pos=(0,0,0) rot=(0.57735,0.57735,0.57735;2.0944rad)
  Profile = -> Sketch338
  Type = 0
FEATURE [PartDesign::Pad] Pad165
  BaseFeature = -> Pad164
  Direction = (1,-2e-16,6e-16)
  Length = 15
  Length2 = 10
  Placement = pos=(0,0,0) rot=(0.57735,0.57735,0.57735;2.0944rad)
  Profile = -> Pad164 [Edge20]
  Type = 0
FEATURE [PartDesign::Body] Body242
  Group = -> [Sketch338,Pad164,Pad165]
  Origin = -> Origin346
  Tip = -> Pad165
FEATURE [App::Part] Part103  label="tornillo M5-15-016"
  Group = -> [Body242]
  Origin = -> Origin345
  Placement = pos=(28.2334,9.96532,164.125) rot=(0.44435,-0.754393,0.483161;1.89214rad)
FEATURE [Sketcher::SketchObject] Sketch339
  FullyConstrained = false
  MapMode = 5
  Placement = pos=(0,0,0) rot=(0.57735,0.57735,0.57735;2.0944rad)
  Support = -> [YZ_Plane342]
  sketch-geometry (8):
    g0: LineSegment StartX=2.8963 StartY=-2.75889 StartZ=0 EndX=3.83742 EndY=1.12882 EndZ=0
    g1: LineSegment StartX=3.83742 StartY=1.12882 StartZ=0 EndX=0.941117 EndY=3.88771 EndZ=0
    g2: LineSegment StartX=0.941117 StartY=3.88771 StartZ=0 EndX=-2.8963 EndY=2.75889 EndZ=0
    g3: LineSegment StartX=-2.8963 StartY=2.75889 StartZ=0 EndX=-3.83742 EndY=-1.12882 EndZ=0
    g4: LineSegment StartX=-3.83742 StartY=-1.12882 StartZ=0 EndX=-0.941117 EndY=-3.88771 EndZ=0
    g5: LineSegment StartX=-0.941117 StartY=-3.88771 StartZ=0 EndX=2.8963 EndY=-2.75889 EndZ=0
    g6: Circle CenterX=0 CenterY=0 CenterZ=0 NormalX=0 NormalY=0 NormalZ=1 AngleXU=0 Radius=4
    g7: Circle CenterX=0 CenterY=0 CenterZ=0 NormalX=0 NormalY=0 NormalZ=1 AngleXU=0 Radius=2.5
  constraints (17):
    c: Coincident(g0,g1)
    c: Coincident(g1,g2)
    c: Coincident(g2,g3)
    c: Coincident(g3,g4)
    c: Coincident(g4,g5)
    c: Coincident(g5,g0)
    c: Equal(g0, g1-g5) x5
    c: PointOnObject(g0,g6)
    c: PointOnObject(g1,g6)
    c: PointOnObject(g2,g6)
    c: PointOnObject(g3,g6)
    c: PointOnObject(g4,g6)
    c: PointOnObject(g5,g6)
    c: Coincident(g6,g-1)
    c: Coincident(g7,g6)
    c: Radius(g7) = 2.5
    c: Radius(g6) = 4
FEATURE [PartDesign::Pad] Pad167
  Direction = (1,-2e-16,3e-16)
  Length = 3
  Length2 = 10
  Placement = pos=(0,0,0) rot=(0.57735,0.57735,0.57735;2.0944rad)
  Profile = -> Sketch339
  Type = 0
FEATURE [PartDesign::Pad] Pad168
  BaseFeature = -> Pad167
  Direction = (1,-2e-16,6e-16)
  Length = 15
  Length2 = 10
  Placement = pos=(0,0,0) rot=(0.57735,0.57735,0.57735;2.0944rad)
  Profile = -> Pad167 [Edge20]
  Type = 0
FEATURE [PartDesign::Body] Body243
  Group = -> [Sketch339,Pad167,Pad168]
  Origin = -> Origin350
  Tip = -> Pad168
FEATURE [App::Part] Part104  label="tornillo M5-15-017"
  Group = -> [Body243]
  Origin = -> Origin348
  Placement = pos=(31,10,26) rot=(0,1,0;1.5708rad)
FEATURE [Sketcher::SketchObject] Sketch340
  FullyConstrained = false
  MapMode = 5
  Placement = pos=(0,0,0) rot=(0.57735,0.57735,0.57735;2.0944rad)
  Support = -> [YZ_Plane343]
  sketch-geometry (8):
    g0: LineSegment StartX=2.8963 StartY=-2.75889 StartZ=0 EndX=3.83742 EndY=1.12882 EndZ=0
    g1: LineSegment StartX=3.83742 StartY=1.12882 StartZ=0 EndX=0.941117 EndY=3.88771 EndZ=0
    g2: LineSegment StartX=0.941117 StartY=3.88771 StartZ=0 EndX=-2.8963 EndY=2.75889 EndZ=0
    g3: LineSegment StartX=-2.8963 StartY=2.75889 StartZ=0 EndX=-3.83742 EndY=-1.12882 EndZ=0
    g4: LineSegment StartX=-3.83742 StartY=-1.12882 StartZ=0 EndX=-0.941117 EndY=-3.88771 EndZ=0
    g5: LineSegment StartX=-0.941117 StartY=-3.88771 StartZ=0 EndX=2.8963 EndY=-2.75889 EndZ=0
    g6: Circle CenterX=0 CenterY=0 CenterZ=0 NormalX=0 NormalY=0 NormalZ=1 AngleXU=0 Radius=4
    g7: Circle CenterX=0 CenterY=0 CenterZ=0 NormalX=0 NormalY=0 NormalZ=1 AngleXU=0 Radius=2.5
  constraints (17):
    c: Coincident(g0,g1)
    c: Coincident(g1,g2)
    c: Coincident(g2,g3)
    c: Coincident(g3,g4)
    c: Coincident(g4,g5)
    c: Coincident(g5,g0)
    c: Equal(g0, g1-g5) x5
    c: PointOnObject(g0,g6)
    c: PointOnObject(g1,g6)
    c: PointOnObject(g2,g6)
    c: PointOnObject(g3,g6)
    c: PointOnObject(g4,g6)
    c: PointOnObject(g5,g6)
    c: Coincident(g6,g-1)
    c: Coincident(g7,g6)
    c: Radius(g7) = 2.5
    c: Radius(g6) = 4
FEATURE [PartDesign::Pad] Pad166
  Direction = (1,-2e-16,3e-16)
  Length = 3
  Length2 = 10
  Placement = pos=(0,0,0) rot=(0.57735,0.57735,0.57735;2.0944rad)
  Profile = -> Sketch340
  Type = 0
FEATURE [PartDesign::Pad] Pad170
  BaseFeature = -> Pad166
  Direction = (1,-2e-16,6e-16)
  Length = 15
  Length2 = 10
  Placement = pos=(0,0,0) rot=(0.57735,0.57735,0.57735;2.0944rad)
  Profile = -> Pad166 [Edge20]
  Type = 0
FEATURE [PartDesign::Body] Body244
  Group = -> [Sketch340,Pad166,Pad170]
  Origin = -> Origin349
  Tip = -> Pad170
FEATURE [App::Part] Part105  label="tornillo M5-15-018"
  Group = -> [Body244]
  Origin = -> Origin347
  Placement = pos=(26,10,33) rot=(0,1,0;3.14159rad)
FEATURE [Sketcher::SketchObject] Sketch341
  FullyConstrained = false
  MapMode = 5
  Placement = pos=(0,0,0) rot=(0.57735,0.57735,0.57735;2.0944rad)
  Support = -> [YZ_Plane344]
  sketch-geometry (8):
    g0: LineSegment StartX=2.8963 StartY=-2.75889 StartZ=0 EndX=3.83742 EndY=1.12882 EndZ=0
    g1: LineSegment StartX=3.83742 StartY=1.12882 StartZ=0 EndX=0.941117 EndY=3.88771 EndZ=0
    g2: LineSegment StartX=0.941117 StartY=3.88771 StartZ=0 EndX=-2.8963 EndY=2.75889 EndZ=0
    g3: LineSegment StartX=-2.8963 StartY=2.75889 StartZ=0 EndX=-3.83742 EndY=-1.12882 EndZ=0
    g4: LineSegment StartX=-3.83742 StartY=-1.12882 StartZ=0 EndX=-0.941117 EndY=-3.88771 EndZ=0
    g5: LineSegment StartX=-0.941117 StartY=-3.88771 StartZ=0 EndX=2.8963 EndY=-2.75889 EndZ=0
    g6: Circle CenterX=0 CenterY=0 CenterZ=0 NormalX=0 NormalY=0 NormalZ=1 AngleXU=0 Radius=4
    g7: Circle CenterX=0 CenterY=0 CenterZ=0 NormalX=0 NormalY=0 NormalZ=1 AngleXU=0 Radius=2.5
  constraints (17):
    c: Coincident(g0,g1)
    c: Coincident(g1,g2)
    c: Coincident(g2,g3)
    c: Coincident(g3,g4)
    c: Coincident(g4,g5)
    c: Coincident(g5,g0)
    c: Equal(g0, g1-g5) x5
    c: PointOnObject(g0,g6)
    c: PointOnObject(g1,g6)
    c: PointOnObject(g2,g6)
    c: PointOnObject(g3,g6)
    c: PointOnObject(g4,g6)
    c: PointOnObject(g5,g6)
    c: Coincident(g6,g-1)
    c: Coincident(g7,g6)
    c: Radius(g7) = 2.5
    c: Radius(g6) = 4
FEATURE [PartDesign::Pad] Pad169
  Direction = (1,-2e-16,3e-16)
  Length = 3
  Length2 = 10
  Placement = pos=(0,0,0) rot=(0.57735,0.57735,0.57735;2.0944rad)
  Profile = -> Sketch341
  Type = 0
FEATURE [PartDesign::Pad] Pad171
  BaseFeature = -> Pad169
  Direction = (1,-2e-16,6e-16)
  Length = 15
  Length2 = 10
  Placement = pos=(0,0,0) rot=(0.57735,0.57735,0.57735;2.0944rad)
  Profile = -> Pad169 [Edge20]
  Type = 0
FEATURE [PartDesign::Body] Body245
  Group = -> [Sketch341,Pad169,Pad171]
  Origin = -> Origin352
  Tip = -> Pad171
FEATURE [App::Part] Part107  label="tornillo M5-15-020"
  Group = -> [Body245]
  Origin = -> Origin351
  Placement = pos=(26,10,159) rot=(0,1,0;3.14159rad)
FEATURE [Sketcher::SketchObject] Sketch342
  FullyConstrained = false
  MapMode = 5
  Placement = pos=(0,0,0) rot=(0.57735,0.57735,0.57735;2.0944rad)
  Support = -> [YZ_Plane347]
  sketch-geometry (8):
    g0: LineSegment StartX=2.8963 StartY=-2.75889 StartZ=0 EndX=3.83742 EndY=1.12882 EndZ=0
    g1: LineSegment StartX=3.83742 StartY=1.12882 StartZ=0 EndX=0.941117 EndY=3.88771 EndZ=0
    g2: LineSegment StartX=0.941117 StartY=3.88771 StartZ=0 EndX=-2.8963 EndY=2.75889 EndZ=0
    g3: LineSegment StartX=-2.8963 StartY=2.75889 StartZ=0 EndX=-3.83742 EndY=-1.12882 EndZ=0
    g4: LineSegment StartX=-3.83742 StartY=-1.12882 StartZ=0 EndX=-0.941117 EndY=-3.88771 EndZ=0
    g5: LineSegment StartX=-0.941117 StartY=-3.88771 StartZ=0 EndX=2.8963 EndY=-2.75889 EndZ=0
    g6: Circle CenterX=0 CenterY=0 CenterZ=0 NormalX=0 NormalY=0 NormalZ=1 AngleXU=0 Radius=4
    g7: Circle CenterX=0 CenterY=0 CenterZ=0 NormalX=0 NormalY=0 NormalZ=1 AngleXU=0 Radius=2.5
  constraints (17):
    c: Coincident(g0,g1)
    c: Coincident(g1,g2)
    c: Coincident(g2,g3)
    c: Coincident(g3,g4)
    c: Coincident(g4,g5)
    c: Coincident(g5,g0)
    c: Equal(g0, g1-g5) x5
    c: PointOnObject(g0,g6)
    c: PointOnObject(g1,g6)
    c: PointOnObject(g2,g6)
    c: PointOnObject(g3,g6)
    c: PointOnObject(g4,g6)
    c: PointOnObject(g5,g6)
    c: Coincident(g6,g-1)
    c: Coincident(g7,g6)
    c: Radius(g7) = 2.5
    c: Radius(g6) = 4
FEATURE [PartDesign::Pad] Pad173
  Direction = (1,-2e-16,3e-16)
  Length = 3
  Length2 = 10
  Placement = pos=(0,0,0) rot=(0.57735,0.57735,0.57735;2.0944rad)
  Profile = -> Sketch342
  Type = 0
FEATURE [PartDesign::Pad] Pad172
  BaseFeature = -> Pad173
  Direction = (1,-2e-16,6e-16)
  Length = 15
  Length2 = 10
  Placement = pos=(0,0,0) rot=(0.57735,0.57735,0.57735;2.0944rad)
  Profile = -> Pad173 [Edge20]
  Type = 0
FEATURE [PartDesign::Body] Body246
  Group = -> [Sketch342,Pad173,Pad172]
  Origin = -> Origin354
  Tip = -> Pad172
FEATURE [App::Part] Part106  label="tornillo M5-15-019"
  Group = -> [Body246]
  Origin = -> Origin353
  Placement = pos=(28.2334,9.96532,164.125) rot=(0.44435,-0.754393,0.483161;1.89214rad)
FEATURE [App::LinkGroup] LinkGroup020
  ElementList = -> [Part104,Part105,Part106,Part107]
  LinkMode = 0
  Placement = pos=(339.888,20.1907,1.52588e-05) rot=(0,0,1;3.14159rad)
FEATURE [App::LinkGroup] LinkGroup021
  ElementList = -> [Part100,Part101,Part102,Part103,LinkGroup020]
  LinkMode = 0
FEATURE [Sketcher::SketchObject] Sketch343
  FullyConstrained = false
  MapMode = 5
  Placement = pos=(0,0,0) rot=(0.57735,0.57735,0.57735;2.0944rad)
  Support = -> [YZ_Plane350]
  sketch-geometry (8):
    g0: LineSegment StartX=2.8963 StartY=-2.75889 StartZ=0 EndX=3.83742 EndY=1.12882 EndZ=0
    g1: LineSegment StartX=3.83742 StartY=1.12882 StartZ=0 EndX=0.941117 EndY=3.88771 EndZ=0
    g2: LineSegment StartX=0.941117 StartY=3.88771 StartZ=0 EndX=-2.8963 EndY=2.75889 EndZ=0
    g3: LineSegment StartX=-2.8963 StartY=2.75889 StartZ=0 EndX=-3.83742 EndY=-1.12882 EndZ=0
    g4: LineSegment StartX=-3.83742 StartY=-1.12882 StartZ=0 EndX=-0.941117 EndY=-3.88771 EndZ=0
    g5: LineSegment StartX=-0.941117 StartY=-3.88771 StartZ=0 EndX=2.8963 EndY=-2.75889 EndZ=0
    g6: Circle CenterX=0 CenterY=0 CenterZ=0 NormalX=0 NormalY=0 NormalZ=1 AngleXU=0 Radius=4
    g7: Circle CenterX=0 CenterY=0 CenterZ=0 NormalX=0 NormalY=0 NormalZ=1 AngleXU=0 Radius=2.5
  constraints (17):
    c: Coincident(g0,g1)
    c: Coincident(g1,g2)
    c: Coincident(g2,g3)
    c: Coincident(g3,g4)
    c: Coincident(g4,g5)
    c: Coincident(g5,g0)
    c: Equal(g0, g1-g5) x5
    c: PointOnObject(g0,g6)
    c: PointOnObject(g1,g6)
    c: PointOnObject(g2,g6)
    c: PointOnObject(g3,g6)
    c: PointOnObject(g4,g6)
    c: PointOnObject(g5,g6)
    c: Coincident(g6,g-1)
    c: Coincident(g7,g6)
    c: Radius(g7) = 2.5
    c: Radius(g6) = 4
FEATURE [PartDesign::Pad] Pad175
  Direction = (1,-2e-16,3e-16)
  Length = 3
  Length2 = 10
  Placement = pos=(0,0,0) rot=(0.57735,0.57735,0.57735;2.0944rad)
  Profile = -> Sketch343
  Type = 0
FEATURE [PartDesign::Pad] Pad176
  BaseFeature = -> Pad175
  Direction = (1,-2e-16,6e-16)
  Length = 15
  Length2 = 10
  Placement = pos=(0,0,0) rot=(0.57735,0.57735,0.57735;2.0944rad)
  Profile = -> Pad175 [Edge20]
  Type = 0
FEATURE [PartDesign::Body] Body247
  Group = -> [Sketch343,Pad175,Pad176]
  Origin = -> Origin359
  Tip = -> Pad176
FEATURE [App::Part] Part108  label="tornillo M5-15-021"
  Group = -> [Body247]
  Origin = -> Origin357
  Placement = pos=(31,10,26) rot=(0,1,0;1.5708rad)
FEATURE [Sketcher::SketchObject] Sketch344
  FullyConstrained = false
  MapMode = 5
  Placement = pos=(0,0,0) rot=(0.57735,0.57735,0.57735;2.0944rad)
  Support = -> [YZ_Plane351]
  sketch-geometry (8):
    g0: LineSegment StartX=2.8963 StartY=-2.75889 StartZ=0 EndX=3.83742 EndY=1.12882 EndZ=0
    g1: LineSegment StartX=3.83742 StartY=1.12882 StartZ=0 EndX=0.941117 EndY=3.88771 EndZ=0
    g2: LineSegment StartX=0.941117 StartY=3.88771 StartZ=0 EndX=-2.8963 EndY=2.75889 EndZ=0
    g3: LineSegment StartX=-2.8963 StartY=2.75889 StartZ=0 EndX=-3.83742 EndY=-1.12882 EndZ=0
    g4: LineSegment StartX=-3.83742 StartY=-1.12882 StartZ=0 EndX=-0.941117 EndY=-3.88771 EndZ=0
    g5: LineSegment StartX=-0.941117 StartY=-3.88771 StartZ=0 EndX=2.8963 EndY=-2.75889 EndZ=0
    g6: Circle CenterX=0 CenterY=0 CenterZ=0 NormalX=0 NormalY=0 NormalZ=1 AngleXU=0 Radius=4
    g7: Circle CenterX=0 CenterY=0 CenterZ=0 NormalX=0 NormalY=0 NormalZ=1 AngleXU=0 Radius=2.5
  constraints (17):
    c: Coincident(g0,g1)
    c: Coincident(g1,g2)
    c: Coincident(g2,g3)
    c: Coincident(g3,g4)
    c: Coincident(g4,g5)
    c: Coincident(g5,g0)
    c: Equal(g0, g1-g5) x5
    c: PointOnObject(g0,g6)
    c: PointOnObject(g1,g6)
    c: PointOnObject(g2,g6)
    c: PointOnObject(g3,g6)
    c: PointOnObject(g4,g6)
    c: PointOnObject(g5,g6)
    c: Coincident(g6,g-1)
    c: Coincident(g7,g6)
    c: Radius(g7) = 2.5
    c: Radius(g6) = 4
FEATURE [PartDesign::Pad] Pad174
  Direction = (1,-2e-16,3e-16)
  Length = 3
  Length2 = 10
  Placement = pos=(0,0,0) rot=(0.57735,0.57735,0.57735;2.0944rad)
  Profile = -> Sketch344
  Type = 0
FEATURE [PartDesign::Pad] Pad178
  BaseFeature = -> Pad174
  Direction = (1,-2e-16,6e-16)
  Length = 15
  Length2 = 10
  Placement = pos=(0,0,0) rot=(0.57735,0.57735,0.57735;2.0944rad)
  Profile = -> Pad174 [Edge20]
  Type = 0
FEATURE [PartDesign::Body] Body248
  Group = -> [Sketch344,Pad174,Pad178]
  Origin = -> Origin358
  Tip = -> Pad178
FEATURE [App::Part] Part109  label="tornillo M5-15-022"
  Group = -> [Body248]
  Origin = -> Origin356
  Placement = pos=(26,10,33) rot=(0,1,0;3.14159rad)
FEATURE [Sketcher::SketchObject] Sketch345
  FullyConstrained = false
  MapMode = 5
  Placement = pos=(0,0,0) rot=(0.57735,0.57735,0.57735;2.0944rad)
  Support = -> [YZ_Plane363]
  sketch-geometry (8):
    g0: LineSegment StartX=2.8963 StartY=-2.75889 StartZ=0 EndX=3.83742 EndY=1.12882 EndZ=0
    g1: LineSegment StartX=3.83742 StartY=1.12882 StartZ=0 EndX=0.941117 EndY=3.88771 EndZ=0
    g2: LineSegment StartX=0.941117 StartY=3.88771 StartZ=0 EndX=-2.8963 EndY=2.75889 EndZ=0
    g3: LineSegment StartX=-2.8963 StartY=2.75889 StartZ=0 EndX=-3.83742 EndY=-1.12882 EndZ=0
    g4: LineSegment StartX=-3.83742 StartY=-1.12882 StartZ=0 EndX=-0.941117 EndY=-3.88771 EndZ=0
    g5: LineSegment StartX=-0.941117 StartY=-3.88771 StartZ=0 EndX=2.8963 EndY=-2.75889 EndZ=0
    g6: Circle CenterX=0 CenterY=0 CenterZ=0 NormalX=0 NormalY=0 NormalZ=1 AngleXU=0 Radius=4
    g7: Circle CenterX=0 CenterY=0 CenterZ=0 NormalX=0 NormalY=0 NormalZ=1 AngleXU=0 Radius=2.5
  constraints (17):
    c: Coincident(g0,g1)
    c: Coincident(g1,g2)
    c: Coincident(g2,g3)
    c: Coincident(g3,g4)
    c: Coincident(g4,g5)
    c: Coincident(g5,g0)
    c: Equal(g0, g1-g5) x5
    c: PointOnObject(g0,g6)
    c: PointOnObject(g1,g6)
    c: PointOnObject(g2,g6)
    c: PointOnObject(g3,g6)
    c: PointOnObject(g4,g6)
    c: PointOnObject(g5,g6)
    c: Coincident(g6,g-1)
    c: Coincident(g7,g6)
    c: Radius(g7) = 2.5
    c: Radius(g6) = 4
FEATURE [PartDesign::Pad] Pad180
  Direction = (1,-2e-16,3e-16)
  Length = 3
  Length2 = 10
  Placement = pos=(0,0,0) rot=(0.57735,0.57735,0.57735;2.0944rad)
  Profile = -> Sketch345
  Type = 0
FEATURE [Sketcher::SketchObject] Sketch346
  FullyConstrained = false
  MapMode = 5
  Placement = pos=(0,0,0) rot=(0.57735,0.57735,0.57735;2.0944rad)
  Support = -> [YZ_Plane352]
  sketch-geometry (8):
    g0: LineSegment StartX=2.8963 StartY=-2.75889 StartZ=0 EndX=3.83742 EndY=1.12882 EndZ=0
    g1: LineSegment StartX=3.83742 StartY=1.12882 StartZ=0 EndX=0.941117 EndY=3.88771 EndZ=0
    g2: LineSegment StartX=0.941117 StartY=3.88771 StartZ=0 EndX=-2.8963 EndY=2.75889 EndZ=0
    g3: LineSegment StartX=-2.8963 StartY=2.75889 StartZ=0 EndX=-3.83742 EndY=-1.12882 EndZ=0
    g4: LineSegment StartX=-3.83742 StartY=-1.12882 StartZ=0 EndX=-0.941117 EndY=-3.88771 EndZ=0
    g5: LineSegment StartX=-0.941117 StartY=-3.88771 StartZ=0 EndX=2.8963 EndY=-2.75889 EndZ=0
    g6: Circle CenterX=0 CenterY=0 CenterZ=0 NormalX=0 NormalY=0 NormalZ=1 AngleXU=0 Radius=4
    g7: Circle CenterX=0 CenterY=0 CenterZ=0 NormalX=0 NormalY=0 NormalZ=1 AngleXU=0 Radius=2.5
  constraints (17):
    c: Coincident(g0,g1)
    c: Coincident(g1,g2)
    c: Coincident(g2,g3)
    c: Coincident(g3,g4)
    c: Coincident(g4,g5)
    c: Coincident(g5,g0)
    c: Equal(g0, g1-g5) x5
    c: PointOnObject(g0,g6)
    c: PointOnObject(g1,g6)
    c: PointOnObject(g2,g6)
    c: PointOnObject(g3,g6)
    c: PointOnObject(g4,g6)
    c: PointOnObject(g5,g6)
    c: Coincident(g6,g-1)
    c: Coincident(g7,g6)
    c: Radius(g7) = 2.5
    c: Radius(g6) = 4
FEATURE [PartDesign::Pad] Pad177
  Direction = (1,-2e-16,3e-16)
  Length = 3
  Length2 = 10
  Placement = pos=(0,0,0) rot=(0.57735,0.57735,0.57735;2.0944rad)
  Profile = -> Sketch346
  Type = 0
FEATURE [PartDesign::Pad] Pad181
  BaseFeature = -> Pad177
  Direction = (1,-2e-16,6e-16)
  Length = 15
  Length2 = 10
  Placement = pos=(0,0,0) rot=(0.57735,0.57735,0.57735;2.0944rad)
  Profile = -> Pad177 [Edge20]
  Type = 0
FEATURE [PartDesign::Body] Body249
  Group = -> [Sketch346,Pad177,Pad181]
  Origin = -> Origin361
  Tip = -> Pad181
FEATURE [App::Part] Part111  label="tornillo M5-15-024"
  Group = -> [Body249]
  Origin = -> Origin360
  Placement = pos=(26,10,159) rot=(0,1,0;3.14159rad)
FEATURE [Sketcher::SketchObject] Sketch347
  FullyConstrained = false
  MapMode = 5
  Placement = pos=(0,0,0) rot=(0.57735,0.57735,0.57735;2.0944rad)
  Support = -> [YZ_Plane361]
  sketch-geometry (8):
    g0: LineSegment StartX=2.8963 StartY=-2.75889 StartZ=0 EndX=3.83742 EndY=1.12882 EndZ=0
    g1: LineSegment StartX=3.83742 StartY=1.12882 StartZ=0 EndX=0.941117 EndY=3.88771 EndZ=0
    g2: LineSegment StartX=0.941117 StartY=3.88771 StartZ=0 EndX=-2.8963 EndY=2.75889 EndZ=0
    g3: LineSegment StartX=-2.8963 StartY=2.75889 StartZ=0 EndX=-3.83742 EndY=-1.12882 EndZ=0
    g4: LineSegment StartX=-3.83742 StartY=-1.12882 StartZ=0 EndX=-0.941117 EndY=-3.88771 EndZ=0
    g5: LineSegment StartX=-0.941117 StartY=-3.88771 StartZ=0 EndX=2.8963 EndY=-2.75889 EndZ=0
    g6: Circle CenterX=0 CenterY=0 CenterZ=0 NormalX=0 NormalY=0 NormalZ=1 AngleXU=0 Radius=4
    g7: Circle CenterX=0 CenterY=0 CenterZ=0 NormalX=0 NormalY=0 NormalZ=1 AngleXU=0 Radius=2.5
  constraints (17):
    c: Coincident(g0,g1)
    c: Coincident(g1,g2)
    c: Coincident(g2,g3)
    c: Coincident(g3,g4)
    c: Coincident(g4,g5)
    c: Coincident(g5,g0)
    c: Equal(g0, g1-g5) x5
    c: PointOnObject(g0,g6)
    c: PointOnObject(g1,g6)
    c: PointOnObject(g2,g6)
    c: PointOnObject(g3,g6)
    c: PointOnObject(g4,g6)
    c: PointOnObject(g5,g6)
    c: Coincident(g6,g-1)
    c: Coincident(g7,g6)
    c: Radius(g7) = 2.5
    c: Radius(g6) = 4
FEATURE [PartDesign::Pad] Pad179
  Direction = (1,-2e-16,3e-16)
  Length = 3
  Length2 = 10
  Placement = pos=(0,0,0) rot=(0.57735,0.57735,0.57735;2.0944rad)
  Profile = -> Sketch347
  Type = 0
FEATURE [Sketcher::SketchObject] Sketch348
  FullyConstrained = false
  MapMode = 5
  Placement = pos=(0,0,0) rot=(0.57735,0.57735,0.57735;2.0944rad)
  Support = -> [YZ_Plane355]
  sketch-geometry (8):
    g0: LineSegment StartX=2.8963 StartY=-2.75889 StartZ=0 EndX=3.83742 EndY=1.12882 EndZ=0
    g1: LineSegment StartX=3.83742 StartY=1.12882 StartZ=0 EndX=0.941117 EndY=3.88771 EndZ=0
    g2: LineSegment StartX=0.941117 StartY=3.88771 StartZ=0 EndX=-2.8963 EndY=2.75889 EndZ=0
    g3: LineSegment StartX=-2.8963 StartY=2.75889 StartZ=0 EndX=-3.83742 EndY=-1.12882 EndZ=0
    g4: LineSegment StartX=-3.83742 StartY=-1.12882 StartZ=0 EndX=-0.941117 EndY=-3.88771 EndZ=0
    g5: LineSegment StartX=-0.941117 StartY=-3.88771 StartZ=0 EndX=2.8963 EndY=-2.75889 EndZ=0
    g6: Circle CenterX=0 CenterY=0 CenterZ=0 NormalX=0 NormalY=0 NormalZ=1 AngleXU=0 Radius=4
    g7: Circle CenterX=0 CenterY=0 CenterZ=0 NormalX=0 NormalY=0 NormalZ=1 AngleXU=0 Radius=2.5
  constraints (17):
    c: Coincident(g0,g1)
    c: Coincident(g1,g2)
    c: Coincident(g2,g3)
    c: Coincident(g3,g4)
    c: Coincident(g4,g5)
    c: Coincident(g5,g0)
    c: Equal(g0, g1-g5) x5
    c: PointOnObject(g0,g6)
    c: PointOnObject(g1,g6)
    c: PointOnObject(g2,g6)
    c: PointOnObject(g3,g6)
    c: PointOnObject(g4,g6)
    c: PointOnObject(g5,g6)
    c: Coincident(g6,g-1)
    c: Coincident(g7,g6)
    c: Radius(g7) = 2.5
    c: Radius(g6) = 4
FEATURE [PartDesign::Pad] Pad184
  Direction = (1,-2e-16,3e-16)
  Length = 3
  Length2 = 10
  Placement = pos=(0,0,0) rot=(0.57735,0.57735,0.57735;2.0944rad)
  Profile = -> Sketch348
  Type = 0
FEATURE [PartDesign::Pad] Pad183
  BaseFeature = -> Pad184
  Direction = (1,-2e-16,6e-16)
  Length = 15
  Length2 = 10
  Placement = pos=(0,0,0) rot=(0.57735,0.57735,0.57735;2.0944rad)
  Profile = -> Pad184 [Edge20]
  Type = 0
FEATURE [PartDesign::Body] Body253
  Group = -> [Sketch348,Pad184,Pad183]
  Origin = -> Origin363
  Tip = -> Pad183
FEATURE [App::Part] Part110  label="tornillo M5-15-023"
  Group = -> [Body253]
  Origin = -> Origin362
  Placement = pos=(28.2334,9.96532,164.125) rot=(0.44435,-0.754393,0.483161;1.89214rad)
FEATURE [PartDesign::Pad] Pad185
  BaseFeature = -> Pad180
  Direction = (1,-2e-16,6e-16)
  Length = 15
  Length2 = 10
  Placement = pos=(0,0,0) rot=(0.57735,0.57735,0.57735;2.0944rad)
  Profile = -> Pad180 [Edge20]
  Type = 0
FEATURE [PartDesign::Body] Body250
  Group = -> [Sketch345,Pad180,Pad185]
  Origin = -> Origin365
  Tip = -> Pad185
FEATURE [App::Part] Part113  label="tornillo M5-15-026"
  Group = -> [Body250]
  Origin = -> Origin367
  Placement = pos=(31,10,26) rot=(0,1,0;1.5708rad)
FEATURE [PartDesign::Pad] Pad186
  BaseFeature = -> Pad179
  Direction = (1,-2e-16,6e-16)
  Length = 15
  Length2 = 10
  Placement = pos=(0,0,0) rot=(0.57735,0.57735,0.57735;2.0944rad)
  Profile = -> Pad179 [Edge20]
  Type = 0
FEATURE [PartDesign::Body] Body251
  Group = -> [Sketch347,Pad179,Pad186]
  Origin = -> Origin366
  Tip = -> Pad186
FEATURE [App::Part] Part112  label="tornillo M5-15-025"
  Group = -> [Body251]
  Origin = -> Origin355
  Placement = pos=(26,10,33) rot=(0,1,0;3.14159rad)
FEATURE [Sketcher::SketchObject] Sketch349
  FullyConstrained = false
  MapMode = 5
  Placement = pos=(0,0,0) rot=(0.57735,0.57735,0.57735;2.0944rad)
  Support = -> [YZ_Plane358]
  sketch-geometry (8):
    g0: LineSegment StartX=2.8963 StartY=-2.75889 StartZ=0 EndX=3.83742 EndY=1.12882 EndZ=0
    g1: LineSegment StartX=3.83742 StartY=1.12882 StartZ=0 EndX=0.941117 EndY=3.88771 EndZ=0
    g2: LineSegment StartX=0.941117 StartY=3.88771 StartZ=0 EndX=-2.8963 EndY=2.75889 EndZ=0
    g3: LineSegment StartX=-2.8963 StartY=2.75889 StartZ=0 EndX=-3.83742 EndY=-1.12882 EndZ=0
    g4: LineSegment StartX=-3.83742 StartY=-1.12882 StartZ=0 EndX=-0.941117 EndY=-3.88771 EndZ=0
    g5: LineSegment StartX=-0.941117 StartY=-3.88771 StartZ=0 EndX=2.8963 EndY=-2.75889 EndZ=0
    g6: Circle CenterX=0 CenterY=0 CenterZ=0 NormalX=0 NormalY=0 NormalZ=1 AngleXU=0 Radius=4
    g7: Circle CenterX=0 CenterY=0 CenterZ=0 NormalX=0 NormalY=0 NormalZ=1 AngleXU=0 Radius=2.5
  constraints (17):
    c: Coincident(g0,g1)
    c: Coincident(g1,g2)
    c: Coincident(g2,g3)
    c: Coincident(g3,g4)
    c: Coincident(g4,g5)
    c: Coincident(g5,g0)
    c: Equal(g0, g1-g5) x5
    c: PointOnObject(g0,g6)
    c: PointOnObject(g1,g6)
    c: PointOnObject(g2,g6)
    c: PointOnObject(g3,g6)
    c: PointOnObject(g4,g6)
    c: PointOnObject(g5,g6)
    c: Coincident(g6,g-1)
    c: Coincident(g7,g6)
    c: Radius(g7) = 2.5
    c: Radius(g6) = 4
FEATURE [PartDesign::Pad] Pad182
  Direction = (1,-2e-16,3e-16)
  Length = 3
  Length2 = 10
  Placement = pos=(0,0,0) rot=(0.57735,0.57735,0.57735;2.0944rad)
  Profile = -> Sketch349
  Type = 0
FEATURE [PartDesign::Pad] Pad187
  BaseFeature = -> Pad182
  Direction = (1,-2e-16,6e-16)
  Length = 15
  Length2 = 10
  Placement = pos=(0,0,0) rot=(0.57735,0.57735,0.57735;2.0944rad)
  Profile = -> Pad182 [Edge20]
  Type = 0
FEATURE [PartDesign::Body] Body252
  Group = -> [Sketch349,Pad182,Pad187]
  Origin = -> Origin369
  Tip = -> Pad187
FEATURE [App::Part] Part115  label="tornillo M5-15-028"
  Group = -> [Body252]
  Origin = -> Origin368
  Placement = pos=(26,10,159) rot=(0,1,0;3.14159rad)
FEATURE [Sketcher::SketchObject] Sketch350
  FullyConstrained = false
  MapMode = 5
  Placement = pos=(0,0,0) rot=(0.57735,0.57735,0.57735;2.0944rad)
  Support = -> [YZ_Plane356]
  sketch-geometry (8):
    g0: LineSegment StartX=2.8963 StartY=-2.75889 StartZ=0 EndX=3.83742 EndY=1.12882 EndZ=0
    g1: LineSegment StartX=3.83742 StartY=1.12882 StartZ=0 EndX=0.941117 EndY=3.88771 EndZ=0
    g2: LineSegment StartX=0.941117 StartY=3.88771 StartZ=0 EndX=-2.8963 EndY=2.75889 EndZ=0
    g3: LineSegment StartX=-2.8963 StartY=2.75889 StartZ=0 EndX=-3.83742 EndY=-1.12882 EndZ=0
    g4: LineSegment StartX=-3.83742 StartY=-1.12882 StartZ=0 EndX=-0.941117 EndY=-3.88771 EndZ=0
    g5: LineSegment StartX=-0.941117 StartY=-3.88771 StartZ=0 EndX=2.8963 EndY=-2.75889 EndZ=0
    g6: Circle CenterX=0 CenterY=0 CenterZ=0 NormalX=0 NormalY=0 NormalZ=1 AngleXU=0 Radius=4
    g7: Circle CenterX=0 CenterY=0 CenterZ=0 NormalX=0 NormalY=0 NormalZ=1 AngleXU=0 Radius=2.5
  constraints (17):
    c: Coincident(g0,g1)
    c: Coincident(g1,g2)
    c: Coincident(g2,g3)
    c: Coincident(g3,g4)
    c: Coincident(g4,g5)
    c: Coincident(g5,g0)
    c: Equal(g0, g1-g5) x5
    c: PointOnObject(g0,g6)
    c: PointOnObject(g1,g6)
    c: PointOnObject(g2,g6)
    c: PointOnObject(g3,g6)
    c: PointOnObject(g4,g6)
    c: PointOnObject(g5,g6)
    c: Coincident(g6,g-1)
    c: Coincident(g7,g6)
    c: Radius(g7) = 2.5
    c: Radius(g6) = 4
FEATURE [PartDesign::Pad] Pad189
  Direction = (1,-2e-16,3e-16)
  Length = 3
  Length2 = 10
  Placement = pos=(0,0,0) rot=(0.57735,0.57735,0.57735;2.0944rad)
  Profile = -> Sketch350
  Type = 0
FEATURE [PartDesign::Pad] Pad188
  BaseFeature = -> Pad189
  Direction = (1,-2e-16,6e-16)
  Length = 15
  Length2 = 10
  Placement = pos=(0,0,0) rot=(0.57735,0.57735,0.57735;2.0944rad)
  Profile = -> Pad189 [Edge20]
  Type = 0
FEATURE [PartDesign::Body] Body254
  Group = -> [Sketch350,Pad189,Pad188]
  Origin = -> Origin370
  Tip = -> Pad188
FEATURE [App::Part] Part114  label="tornillo M5-15-027"
  Group = -> [Body254]
  Origin = -> Origin364
  Placement = pos=(28.2334,9.96532,164.125) rot=(0.44435,-0.754393,0.483161;1.89214rad)
FEATURE [App::LinkGroup] LinkGroup022
  ElementList = -> [Part113,Part112,Part114,Part115]
  LinkMode = 0
  Placement = pos=(339.888,20.1907,1.52588e-05) rot=(0,0,1;3.14159rad)
FEATURE [App::LinkGroup] LinkGroup023
  ElementList = -> [Part108,Part109,Part111,Part110,LinkGroup022]
  LinkMode = 0
  Placement = pos=(-1.52588e-05,319,-7.62939e-06) rot=(0,0,1;0rad)
FEATURE [Sketcher::SketchObject] Sketch351
  FullyConstrained = false
  MapMode = 5
  Placement = pos=(0,0,0) rot=(0.57735,0.57735,0.57735;2.0944rad)
  Support = -> [YZ_Plane366]
  sketch-geometry (8):
    g0: LineSegment StartX=2.8963 StartY=-2.75889 StartZ=0 EndX=3.83742 EndY=1.12882 EndZ=0
    g1: LineSegment StartX=3.83742 StartY=1.12882 StartZ=0 EndX=0.941117 EndY=3.88771 EndZ=0
    g2: LineSegment StartX=0.941117 StartY=3.88771 StartZ=0 EndX=-2.8963 EndY=2.75889 EndZ=0
    g3: LineSegment StartX=-2.8963 StartY=2.75889 StartZ=0 EndX=-3.83742 EndY=-1.12882 EndZ=0
    g4: LineSegment StartX=-3.83742 StartY=-1.12882 StartZ=0 EndX=-0.941117 EndY=-3.88771 EndZ=0
    g5: LineSegment StartX=-0.941117 StartY=-3.88771 StartZ=0 EndX=2.8963 EndY=-2.75889 EndZ=0
    g6: Circle CenterX=0 CenterY=0 CenterZ=0 NormalX=0 NormalY=0 NormalZ=1 AngleXU=0 Radius=4
    g7: Circle CenterX=0 CenterY=0 CenterZ=0 NormalX=0 NormalY=0 NormalZ=1 AngleXU=0 Radius=2.5
  constraints (17):
    c: Coincident(g0,g1)
    c: Coincident(g1,g2)
    c: Coincident(g2,g3)
    c: Coincident(g3,g4)
    c: Coincident(g4,g5)
    c: Coincident(g5,g0)
    c: Equal(g0, g1-g5) x5
    c: PointOnObject(g0,g6)
    c: PointOnObject(g1,g6)
    c: PointOnObject(g2,g6)
    c: PointOnObject(g3,g6)
    c: PointOnObject(g4,g6)
    c: PointOnObject(g5,g6)
    c: Coincident(g6,g-1)
    c: Coincident(g7,g6)
    c: Radius(g7) = 2.5
    c: Radius(g6) = 4
FEATURE [PartDesign::Pad] Pad190
  Direction = (1,-2e-16,3e-16)
  Length = 3
  Length2 = 10
  Placement = pos=(0,0,0) rot=(0.57735,0.57735,0.57735;2.0944rad)
  Profile = -> Sketch351
  Type = 0
FEATURE [PartDesign::Pad] Pad191
  BaseFeature = -> Pad190
  Direction = (1,-2e-16,6e-16)
  Length = 15
  Length2 = 10
  Placement = pos=(0,0,0) rot=(0.57735,0.57735,0.57735;2.0944rad)
  Profile = -> Pad190 [Edge20]
  Type = 0
FEATURE [PartDesign::Body] Body255
  Group = -> [Sketch351,Pad190,Pad191]
  Origin = -> Origin372
  Tip = -> Pad191
FEATURE [App::Part] Part116  label="tornillo M5-15-029"
  Group = -> [Body255]
  Origin = -> Origin371
  Placement = pos=(327,28,57) rot=(0.707107,-0.707107,0;3.14159rad)
FEATURE [Sketcher::SketchObject] Sketch352
  FullyConstrained = false
  MapMode = 5
  Placement = pos=(0,0,0) rot=(0.57735,0.57735,0.57735;2.0944rad)
  Support = -> [YZ_Plane367]
  sketch-geometry (8):
    g0: LineSegment StartX=2.8963 StartY=-2.75889 StartZ=0 EndX=3.83742 EndY=1.12882 EndZ=0
    g1: LineSegment StartX=3.83742 StartY=1.12882 StartZ=0 EndX=0.941117 EndY=3.88771 EndZ=0
    g2: LineSegment StartX=0.941117 StartY=3.88771 StartZ=0 EndX=-2.8963 EndY=2.75889 EndZ=0
    g3: LineSegment StartX=-2.8963 StartY=2.75889 StartZ=0 EndX=-3.83742 EndY=-1.12882 EndZ=0
    g4: LineSegment StartX=-3.83742 StartY=-1.12882 StartZ=0 EndX=-0.941117 EndY=-3.88771 EndZ=0
    g5: LineSegment StartX=-0.941117 StartY=-3.88771 StartZ=0 EndX=2.8963 EndY=-2.75889 EndZ=0
    g6: Circle CenterX=0 CenterY=0 CenterZ=0 NormalX=0 NormalY=0 NormalZ=1 AngleXU=0 Radius=4
    g7: Circle CenterX=0 CenterY=0 CenterZ=0 NormalX=0 NormalY=0 NormalZ=1 AngleXU=0 Radius=2.5
  constraints (17):
    c: Coincident(g0,g1)
    c: Coincident(g1,g2)
    c: Coincident(g2,g3)
    c: Coincident(g3,g4)
    c: Coincident(g4,g5)
    c: Coincident(g5,g0)
    c: Equal(g0, g1-g5) x5
    c: PointOnObject(g0,g6)
    c: PointOnObject(g1,g6)
    c: PointOnObject(g2,g6)
    c: PointOnObject(g3,g6)
    c: PointOnObject(g4,g6)
    c: PointOnObject(g5,g6)
    c: Coincident(g6,g-1)
    c: Coincident(g7,g6)
    c: Radius(g7) = 2.5
    c: Radius(g6) = 4
FEATURE [PartDesign::Pad] Pad192
  Direction = (1,-2e-16,3e-16)
  Length = 3
  Length2 = 10
  Placement = pos=(0,0,0) rot=(0.57735,0.57735,0.57735;2.0944rad)
  Profile = -> Sketch352
  Type = 0
FEATURE [PartDesign::Pad] Pad193
  BaseFeature = -> Pad192
  Direction = (1,-2e-16,6e-16)
  Length = 15
  Length2 = 10
  Placement = pos=(0,0,0) rot=(0.57735,0.57735,0.57735;2.0944rad)
  Profile = -> Pad192 [Edge20]
  Type = 0
FEATURE [PartDesign::Body] Body256
  Group = -> [Sketch352,Pad192,Pad193]
  Origin = -> Origin374
  Tip = -> Pad193
FEATURE [App::Part] Part117  label="tornillo M5-15-030"
  Group = -> [Body256]
  Origin = -> Origin373
  Placement = pos=(328,31,64) rot=(-0.57735,0.57735,-0.57735;4.18879rad)
FEATURE [App::LinkGroup] LinkGroup024
  ElementList = -> [Part116,Part117]
  LinkMode = 0
FEATURE [Sketcher::SketchObject] Sketch353
  FullyConstrained = false
  MapMode = 5
  Placement = pos=(0,0,0) rot=(0.57735,0.57735,0.57735;2.0944rad)
  Support = -> [YZ_Plane370]
  sketch-geometry (8):
    g0: LineSegment StartX=2.8963 StartY=-2.75889 StartZ=0 EndX=3.83742 EndY=1.12882 EndZ=0
    g1: LineSegment StartX=3.83742 StartY=1.12882 StartZ=0 EndX=0.941117 EndY=3.88771 EndZ=0
    g2: LineSegment StartX=0.941117 StartY=3.88771 StartZ=0 EndX=-2.8963 EndY=2.75889 EndZ=0
    g3: LineSegment StartX=-2.8963 StartY=2.75889 StartZ=0 EndX=-3.83742 EndY=-1.12882 EndZ=0
    g4: LineSegment StartX=-3.83742 StartY=-1.12882 StartZ=0 EndX=-0.941117 EndY=-3.88771 EndZ=0
    g5: LineSegment StartX=-0.941117 StartY=-3.88771 StartZ=0 EndX=2.8963 EndY=-2.75889 EndZ=0
    g6: Circle CenterX=0 CenterY=0 CenterZ=0 NormalX=0 NormalY=0 NormalZ=1 AngleXU=0 Radius=4
    g7: Circle CenterX=0 CenterY=0 CenterZ=0 NormalX=0 NormalY=0 NormalZ=1 AngleXU=0 Radius=2.5
  constraints (17):
    c: Coincident(g0,g1)
    c: Coincident(g1,g2)
    c: Coincident(g2,g3)
    c: Coincident(g3,g4)
    c: Coincident(g4,g5)
    c: Coincident(g5,g0)
    c: Equal(g0, g1-g5) x5
    c: PointOnObject(g0,g6)
    c: PointOnObject(g1,g6)
    c: PointOnObject(g2,g6)
    c: PointOnObject(g3,g6)
    c: PointOnObject(g4,g6)
    c: PointOnObject(g5,g6)
    c: Coincident(g6,g-1)
    c: Coincident(g7,g6)
    c: Radius(g7) = 2.5
    c: Radius(g6) = 4
FEATURE [PartDesign::Pad] Pad195
  Direction = (1,-2e-16,3e-16)
  Length = 3
  Length2 = 10
  Placement = pos=(0,0,0) rot=(0.57735,0.57735,0.57735;2.0944rad)
  Profile = -> Sketch353
  Type = 0
FEATURE [PartDesign::Pad] Pad196
  BaseFeature = -> Pad195
  Direction = (1,-2e-16,6e-16)
  Length = 15
  Length2 = 10
  Placement = pos=(0,0,0) rot=(0.57735,0.57735,0.57735;2.0944rad)
  Profile = -> Pad195 [Edge20]
  Type = 0
FEATURE [PartDesign::Body] Body258
  Group = -> [Sketch353,Pad195,Pad196]
  Origin = -> Origin378
  Tip = -> Pad196
FEATURE [App::Part] Part118  label="tornillo M5-15-031"
  Group = -> [Body258]
  Origin = -> Origin375
  Placement = pos=(327,28,57) rot=(0.707107,-0.707107,0;3.14159rad)
FEATURE [Sketcher::SketchObject] Sketch354
  FullyConstrained = false
  MapMode = 5
  Placement = pos=(0,0,0) rot=(0.57735,0.57735,0.57735;2.0944rad)
  Support = -> [YZ_Plane369]
  sketch-geometry (8):
    g0: LineSegment StartX=2.8963 StartY=-2.75889 StartZ=0 EndX=3.83742 EndY=1.12882 EndZ=0
    g1: LineSegment StartX=3.83742 StartY=1.12882 StartZ=0 EndX=0.941117 EndY=3.88771 EndZ=0
    g2: LineSegment StartX=0.941117 StartY=3.88771 StartZ=0 EndX=-2.8963 EndY=2.75889 EndZ=0
    g3: LineSegment StartX=-2.8963 StartY=2.75889 StartZ=0 EndX=-3.83742 EndY=-1.12882 EndZ=0
    g4: LineSegment StartX=-3.83742 StartY=-1.12882 StartZ=0 EndX=-0.941117 EndY=-3.88771 EndZ=0
    g5: LineSegment StartX=-0.941117 StartY=-3.88771 StartZ=0 EndX=2.8963 EndY=-2.75889 EndZ=0
    g6: Circle CenterX=0 CenterY=0 CenterZ=0 NormalX=0 NormalY=0 NormalZ=1 AngleXU=0 Radius=4
    g7: Circle CenterX=0 CenterY=0 CenterZ=0 NormalX=0 NormalY=0 NormalZ=1 AngleXU=0 Radius=2.5
  constraints (17):
    c: Coincident(g0,g1)
    c: Coincident(g1,g2)
    c: Coincident(g2,g3)
    c: Coincident(g3,g4)
    c: Coincident(g4,g5)
    c: Coincident(g5,g0)
    c: Equal(g0, g1-g5) x5
    c: PointOnObject(g0,g6)
    c: PointOnObject(g1,g6)
    c: PointOnObject(g2,g6)
    c: PointOnObject(g3,g6)
    c: PointOnObject(g4,g6)
    c: PointOnObject(g5,g6)
    c: Coincident(g6,g-1)
    c: Coincident(g7,g6)
    c: Radius(g7) = 2.5
    c: Radius(g6) = 4
FEATURE [PartDesign::Pad] Pad197
  Direction = (1,-2e-16,3e-16)
  Length = 3
  Length2 = 10
  Placement = pos=(0,0,0) rot=(0.57735,0.57735,0.57735;2.0944rad)
  Profile = -> Sketch354
  Type = 0
FEATURE [PartDesign::Pad] Pad194
  BaseFeature = -> Pad197
  Direction = (1,-2e-16,6e-16)
  Length = 15
  Length2 = 10
  Placement = pos=(0,0,0) rot=(0.57735,0.57735,0.57735;2.0944rad)
  Profile = -> Pad197 [Edge20]
  Type = 0
FEATURE [PartDesign::Body] Body257
  Group = -> [Sketch354,Pad197,Pad194]
  Origin = -> Origin377
  Tip = -> Pad194
FEATURE [App::Part] Part119  label="tornillo M5-15-032"
  Group = -> [Body257]
  Origin = -> Origin376
  Placement = pos=(328,31,64) rot=(-0.57735,0.57735,-0.57735;4.18879rad)
FEATURE [App::LinkGroup] LinkGroup025
  ElementList = -> [Part118,Part119]
  LinkMode = 0
  Placement = pos=(658,341.888,-7.62939e-06) rot=(0,0,1;3.14159rad)
FEATURE [Sketcher::SketchObject] Sketch355
  FullyConstrained = false
  MapMode = 5
  Placement = pos=(0,0,0) rot=(0.57735,0.57735,0.57735;2.0944rad)
  Support = -> [YZ_Plane374]
  sketch-geometry (8):
    g0: LineSegment StartX=2.8963 StartY=-2.75889 StartZ=0 EndX=3.83742 EndY=1.12882 EndZ=0
    g1: LineSegment StartX=3.83742 StartY=1.12882 StartZ=0 EndX=0.941117 EndY=3.88771 EndZ=0
    g2: LineSegment StartX=0.941117 StartY=3.88771 StartZ=0 EndX=-2.8963 EndY=2.75889 EndZ=0
    g3: LineSegment StartX=-2.8963 StartY=2.75889 StartZ=0 EndX=-3.83742 EndY=-1.12882 EndZ=0
    g4: LineSegment StartX=-3.83742 StartY=-1.12882 StartZ=0 EndX=-0.941117 EndY=-3.88771 EndZ=0
    g5: LineSegment StartX=-0.941117 StartY=-3.88771 StartZ=0 EndX=2.8963 EndY=-2.75889 EndZ=0
    g6: Circle CenterX=0 CenterY=0 CenterZ=0 NormalX=0 NormalY=0 NormalZ=1 AngleXU=0 Radius=4
    g7: Circle CenterX=0 CenterY=0 CenterZ=0 NormalX=0 NormalY=0 NormalZ=1 AngleXU=0 Radius=2.5
  constraints (17):
    c: Coincident(g0,g1)
    c: Coincident(g1,g2)
    c: Coincident(g2,g3)
    c: Coincident(g3,g4)
    c: Coincident(g4,g5)
    c: Coincident(g5,g0)
    c: Equal(g0, g1-g5) x5
    c: PointOnObject(g0,g6)
    c: PointOnObject(g1,g6)
    c: PointOnObject(g2,g6)
    c: PointOnObject(g3,g6)
    c: PointOnObject(g4,g6)
    c: PointOnObject(g5,g6)
    c: Coincident(g6,g-1)
    c: Coincident(g7,g6)
    c: Radius(g7) = 2.5
    c: Radius(g6) = 4
FEATURE [PartDesign::Pad] Pad198
  Direction = (1,-2e-16,3e-16)
  Length = 3
  Length2 = 10
  Placement = pos=(0,0,0) rot=(0.57735,0.57735,0.57735;2.0944rad)
  Profile = -> Sketch355
  Type = 0
FEATURE [PartDesign::Pad] Pad199
  BaseFeature = -> Pad198
  Direction = (1,-2e-16,6e-16)
  Length = 15
  Length2 = 10
  Placement = pos=(0,0,0) rot=(0.57735,0.57735,0.57735;2.0944rad)
  Profile = -> Pad198 [Edge20]
  Type = 0
FEATURE [PartDesign::Body] Body259
  Group = -> [Sketch355,Pad198,Pad199]
  Origin = -> Origin380
  Tip = -> Pad199
FEATURE [App::Part] Part120  label="tornillo M5-15-033"
  Group = -> [Body259]
  Origin = -> Origin379
  Placement = pos=(357,108,88) rot=(0,1,0;1.5708rad)
FEATURE [Sketcher::SketchObject] Sketch356
  FullyConstrained = false
  MapMode = 5
  Placement = pos=(0,0,0) rot=(0.57735,0.57735,0.57735;2.0944rad)
  Support = -> [YZ_Plane375]
  sketch-geometry (8):
    g0: LineSegment StartX=2.8963 StartY=-2.75889 StartZ=0 EndX=3.83742 EndY=1.12882 EndZ=0
    g1: LineSegment StartX=3.83742 StartY=1.12882 StartZ=0 EndX=0.941117 EndY=3.88771 EndZ=0
    g2: LineSegment StartX=0.941117 StartY=3.88771 StartZ=0 EndX=-2.8963 EndY=2.75889 EndZ=0
    g3: LineSegment StartX=-2.8963 StartY=2.75889 StartZ=0 EndX=-3.83742 EndY=-1.12882 EndZ=0
    g4: LineSegment StartX=-3.83742 StartY=-1.12882 StartZ=0 EndX=-0.941117 EndY=-3.88771 EndZ=0
    g5: LineSegment StartX=-0.941117 StartY=-3.88771 StartZ=0 EndX=2.8963 EndY=-2.75889 EndZ=0
    g6: Circle CenterX=0 CenterY=0 CenterZ=0 NormalX=0 NormalY=0 NormalZ=1 AngleXU=0 Radius=4
    g7: Circle CenterX=0 CenterY=0 CenterZ=0 NormalX=0 NormalY=0 NormalZ=1 AngleXU=0 Radius=2.5
  constraints (17):
    c: Coincident(g0,g1)
    c: Coincident(g1,g2)
    c: Coincident(g2,g3)
    c: Coincident(g3,g4)
    c: Coincident(g4,g5)
    c: Coincident(g5,g0)
    c: Equal(g0, g1-g5) x5
    c: PointOnObject(g0,g6)
    c: PointOnObject(g1,g6)
    c: PointOnObject(g2,g6)
    c: PointOnObject(g3,g6)
    c: PointOnObject(g4,g6)
    c: PointOnObject(g5,g6)
    c: Coincident(g6,g-1)
    c: Coincident(g7,g6)
    c: Radius(g7) = 2.5
    c: Radius(g6) = 4
FEATURE [PartDesign::Pad] Pad200
  Direction = (1,-2e-16,3e-16)
  Length = 3
  Length2 = 10
  Placement = pos=(0,0,0) rot=(0.57735,0.57735,0.57735;2.0944rad)
  Profile = -> Sketch356
  Type = 0
FEATURE [PartDesign::Pad] Pad201
  BaseFeature = -> Pad200
  Direction = (1,-2e-16,6e-16)
  Length = 15
  Length2 = 10
  Placement = pos=(0,0,0) rot=(0.57735,0.57735,0.57735;2.0944rad)
  Profile = -> Pad200 [Edge20]
  Type = 0
FEATURE [PartDesign::Body] Body260
  Group = -> [Sketch356,Pad200,Pad201]
  Origin = -> Origin382
  Tip = -> Pad201
FEATURE [App::Part] Part121  label="tornillo M5-15-034"
  Group = -> [Body260]
  Origin = -> Origin381
  Placement = pos=(379,108,88) rot=(0,1,0;1.5708rad)
FEATURE [Sketcher::SketchObject] Sketch357
  FullyConstrained = false
  MapMode = 5
  Placement = pos=(0,0,0) rot=(0.57735,0.57735,0.57735;2.0944rad)
  Support = -> [YZ_Plane380]
  sketch-geometry (8):
    g0: LineSegment StartX=2.8963 StartY=-2.75889 StartZ=0 EndX=3.83742 EndY=1.12882 EndZ=0
    g1: LineSegment StartX=3.83742 StartY=1.12882 StartZ=0 EndX=0.941117 EndY=3.88771 EndZ=0
    g2: LineSegment StartX=0.941117 StartY=3.88771 StartZ=0 EndX=-2.8963 EndY=2.75889 EndZ=0
    g3: LineSegment StartX=-2.8963 StartY=2.75889 StartZ=0 EndX=-3.83742 EndY=-1.12882 EndZ=0
    g4: LineSegment StartX=-3.83742 StartY=-1.12882 StartZ=0 EndX=-0.941117 EndY=-3.88771 EndZ=0
    g5: LineSegment StartX=-0.941117 StartY=-3.88771 StartZ=0 EndX=2.8963 EndY=-2.75889 EndZ=0
    g6: Circle CenterX=0 CenterY=0 CenterZ=0 NormalX=0 NormalY=0 NormalZ=1 AngleXU=0 Radius=4
    g7: Circle CenterX=0 CenterY=0 CenterZ=0 NormalX=0 NormalY=0 NormalZ=1 AngleXU=0 Radius=2.5
  constraints (17):
    c: Coincident(g0,g1)
    c: Coincident(g1,g2)
    c: Coincident(g2,g3)
    c: Coincident(g3,g4)
    c: Coincident(g4,g5)
    c: Coincident(g5,g0)
    c: Equal(g0, g1-g5) x5
    c: PointOnObject(g0,g6)
    c: PointOnObject(g1,g6)
    c: PointOnObject(g2,g6)
    c: PointOnObject(g3,g6)
    c: PointOnObject(g4,g6)
    c: PointOnObject(g5,g6)
    c: Coincident(g6,g-1)
    c: Coincident(g7,g6)
    c: Radius(g7) = 2.5
    c: Radius(g6) = 4
FEATURE [PartDesign::Pad] Pad202
  Direction = (1,-2e-16,3e-16)
  Length = 3
  Length2 = 10
  Placement = pos=(0,0,0) rot=(0.57735,0.57735,0.57735;2.0944rad)
  Profile = -> Sketch357
  Type = 0
FEATURE [Sketcher::SketchObject] Sketch358
  FullyConstrained = false
  MapMode = 5
  Placement = pos=(0,0,0) rot=(0.57735,0.57735,0.57735;2.0944rad)
  Support = -> [YZ_Plane378]
  sketch-geometry (8):
    g0: LineSegment StartX=2.8963 StartY=-2.75889 StartZ=0 EndX=3.83742 EndY=1.12882 EndZ=0
    g1: LineSegment StartX=3.83742 StartY=1.12882 StartZ=0 EndX=0.941117 EndY=3.88771 EndZ=0
    g2: LineSegment StartX=0.941117 StartY=3.88771 StartZ=0 EndX=-2.8963 EndY=2.75889 EndZ=0
    g3: LineSegment StartX=-2.8963 StartY=2.75889 StartZ=0 EndX=-3.83742 EndY=-1.12882 EndZ=0
    g4: LineSegment StartX=-3.83742 StartY=-1.12882 StartZ=0 EndX=-0.941117 EndY=-3.88771 EndZ=0
    g5: LineSegment StartX=-0.941117 StartY=-3.88771 StartZ=0 EndX=2.8963 EndY=-2.75889 EndZ=0
    g6: Circle CenterX=0 CenterY=0 CenterZ=0 NormalX=0 NormalY=0 NormalZ=1 AngleXU=0 Radius=4
    g7: Circle CenterX=0 CenterY=0 CenterZ=0 NormalX=0 NormalY=0 NormalZ=1 AngleXU=0 Radius=2.5
  constraints (17):
    c: Coincident(g0,g1)
    c: Coincident(g1,g2)
    c: Coincident(g2,g3)
    c: Coincident(g3,g4)
    c: Coincident(g4,g5)
    c: Coincident(g5,g0)
    c: Equal(g0, g1-g5) x5
    c: PointOnObject(g0,g6)
    c: PointOnObject(g1,g6)
    c: PointOnObject(g2,g6)
    c: PointOnObject(g3,g6)
    c: PointOnObject(g4,g6)
    c: PointOnObject(g5,g6)
    c: Coincident(g6,g-1)
    c: Coincident(g7,g6)
    c: Radius(g7) = 2.5
    c: Radius(g6) = 4
FEATURE [PartDesign::Pad] Pad203
  Direction = (1,-2e-16,3e-16)
  Length = 3
  Length2 = 10
  Placement = pos=(0,0,0) rot=(0.57735,0.57735,0.57735;2.0944rad)
  Profile = -> Sketch358
  Type = 0
FEATURE [PartDesign::Pad] Pad204
  BaseFeature = -> Pad203
  Direction = (1,-2e-16,6e-16)
  Length = 15
  Length2 = 10
  Placement = pos=(0,0,0) rot=(0.57735,0.57735,0.57735;2.0944rad)
  Profile = -> Pad203 [Edge20]
  Type = 0
FEATURE [PartDesign::Body] Body262
  Group = -> [Sketch358,Pad203,Pad204]
  Origin = -> Origin385
  Tip = -> Pad204
FEATURE [App::Part] Part122  label="tornillo M5-15-035"
  Group = -> [Body262]
  Origin = -> Origin383
  Placement = pos=(357,108,88) rot=(0,1,0;1.5708rad)
FEATURE [PartDesign::Pad] Pad205
  BaseFeature = -> Pad202
  Direction = (1,-2e-16,6e-16)
  Length = 15
  Length2 = 10
  Placement = pos=(0,0,0) rot=(0.57735,0.57735,0.57735;2.0944rad)
  Profile = -> Pad202 [Edge20]
  Type = 0
FEATURE [PartDesign::Body] Body261
  Group = -> [Sketch357,Pad202,Pad205]
  Origin = -> Origin384
  Tip = -> Pad205
FEATURE [App::Part] Part123  label="tornillo M5-15-036"
  Group = -> [Body261]
  Origin = -> Origin386
  Placement = pos=(379,108,88) rot=(0,1,0;1.5708rad)
FEATURE [App::LinkGroup] LinkGroup026
  ElementList = -> [Part122,Part123]
  LinkMode = 0
  Placement = pos=(0,25,0) rot=(0,0,1;0rad)
FEATURE [App::LinkGroup] LinkGroup027
  ElementList = -> [Part120,Part121,LinkGroup026]
  LinkMode = 0
FEATURE [Sketcher::SketchObject] Sketch359
  FullyConstrained = false
  MapMode = 5
  Placement = pos=(0,0,0) rot=(0.57735,0.57735,0.57735;2.0944rad)
  Support = -> [YZ_Plane383]
  sketch-geometry (8):
    g0: LineSegment StartX=2.8963 StartY=-2.75889 StartZ=0 EndX=3.83742 EndY=1.12882 EndZ=0
    g1: LineSegment StartX=3.83742 StartY=1.12882 StartZ=0 EndX=0.941117 EndY=3.88771 EndZ=0
    g2: LineSegment StartX=0.941117 StartY=3.88771 StartZ=0 EndX=-2.8963 EndY=2.75889 EndZ=0
    g3: LineSegment StartX=-2.8963 StartY=2.75889 StartZ=0 EndX=-3.83742 EndY=-1.12882 EndZ=0
    g4: LineSegment StartX=-3.83742 StartY=-1.12882 StartZ=0 EndX=-0.941117 EndY=-3.88771 EndZ=0
    g5: LineSegment StartX=-0.941117 StartY=-3.88771 StartZ=0 EndX=2.8963 EndY=-2.75889 EndZ=0
    g6: Circle CenterX=0 CenterY=0 CenterZ=0 NormalX=0 NormalY=0 NormalZ=1 AngleXU=0 Radius=4
    g7: Circle CenterX=0 CenterY=0 CenterZ=0 NormalX=0 NormalY=0 NormalZ=1 AngleXU=0 Radius=2.5
  constraints (17):
    c: Coincident(g0,g1)
    c: Coincident(g1,g2)
    c: Coincident(g2,g3)
    c: Coincident(g3,g4)
    c: Coincident(g4,g5)
    c: Coincident(g5,g0)
    c: Equal(g0, g1-g5) x5
    c: PointOnObject(g0,g6)
    c: PointOnObject(g1,g6)
    c: PointOnObject(g2,g6)
    c: PointOnObject(g3,g6)
    c: PointOnObject(g4,g6)
    c: PointOnObject(g5,g6)
    c: Coincident(g6,g-1)
    c: Coincident(g7,g6)
    c: Radius(g7) = 2.5
    c: Radius(g6) = 4
FEATURE [PartDesign::Pad] Pad208
  Direction = (1,-2e-16,3e-16)
  Length = 3
  Length2 = 10
  Placement = pos=(0,0,0) rot=(0.57735,0.57735,0.57735;2.0944rad)
  Profile = -> Sketch359
  Type = 0
FEATURE [Sketcher::SketchObject] Sketch360
  FullyConstrained = false
  MapMode = 5
  Placement = pos=(0,0,0) rot=(0.57735,0.57735,0.57735;2.0944rad)
  Support = -> [YZ_Plane386]
  sketch-geometry (8):
    g0: LineSegment StartX=2.8963 StartY=-2.75889 StartZ=0 EndX=3.83742 EndY=1.12882 EndZ=0
    g1: LineSegment StartX=3.83742 StartY=1.12882 StartZ=0 EndX=0.941117 EndY=3.88771 EndZ=0
    g2: LineSegment StartX=0.941117 StartY=3.88771 StartZ=0 EndX=-2.8963 EndY=2.75889 EndZ=0
    g3: LineSegment StartX=-2.8963 StartY=2.75889 StartZ=0 EndX=-3.83742 EndY=-1.12882 EndZ=0
    g4: LineSegment StartX=-3.83742 StartY=-1.12882 StartZ=0 EndX=-0.941117 EndY=-3.88771 EndZ=0
    g5: LineSegment StartX=-0.941117 StartY=-3.88771 StartZ=0 EndX=2.8963 EndY=-2.75889 EndZ=0
    g6: Circle CenterX=0 CenterY=0 CenterZ=0 NormalX=0 NormalY=0 NormalZ=1 AngleXU=0 Radius=4
    g7: Circle CenterX=0 CenterY=0 CenterZ=0 NormalX=0 NormalY=0 NormalZ=1 AngleXU=0 Radius=2.5
  constraints (17):
    c: Coincident(g0,g1)
    c: Coincident(g1,g2)
    c: Coincident(g2,g3)
    c: Coincident(g3,g4)
    c: Coincident(g4,g5)
    c: Coincident(g5,g0)
    c: Equal(g0, g1-g5) x5
    c: PointOnObject(g0,g6)
    c: PointOnObject(g1,g6)
    c: PointOnObject(g2,g6)
    c: PointOnObject(g3,g6)
    c: PointOnObject(g4,g6)
    c: PointOnObject(g5,g6)
    c: Coincident(g6,g-1)
    c: Coincident(g7,g6)
    c: Radius(g7) = 2.5
    c: Radius(g6) = 4
FEATURE [PartDesign::Pad] Pad206
  Direction = (1,-2e-16,3e-16)
  Length = 3
  Length2 = 10
  Placement = pos=(0,0,0) rot=(0.57735,0.57735,0.57735;2.0944rad)
  Profile = -> Sketch360
  Type = 0
FEATURE [Sketcher::SketchObject] Sketch361
  FullyConstrained = false
  MapMode = 5
  Placement = pos=(0,0,0) rot=(0.57735,0.57735,0.57735;2.0944rad)
  Support = -> [YZ_Plane388]
  sketch-geometry (8):
    g0: LineSegment StartX=2.8963 StartY=-2.75889 StartZ=0 EndX=3.83742 EndY=1.12882 EndZ=0
    g1: LineSegment StartX=3.83742 StartY=1.12882 StartZ=0 EndX=0.941117 EndY=3.88771 EndZ=0
    g2: LineSegment StartX=0.941117 StartY=3.88771 StartZ=0 EndX=-2.8963 EndY=2.75889 EndZ=0
    g3: LineSegment StartX=-2.8963 StartY=2.75889 StartZ=0 EndX=-3.83742 EndY=-1.12882 EndZ=0
    g4: LineSegment StartX=-3.83742 StartY=-1.12882 StartZ=0 EndX=-0.941117 EndY=-3.88771 EndZ=0
    g5: LineSegment StartX=-0.941117 StartY=-3.88771 StartZ=0 EndX=2.8963 EndY=-2.75889 EndZ=0
    g6: Circle CenterX=0 CenterY=0 CenterZ=0 NormalX=0 NormalY=0 NormalZ=1 AngleXU=0 Radius=4
    g7: Circle CenterX=0 CenterY=0 CenterZ=0 NormalX=0 NormalY=0 NormalZ=1 AngleXU=0 Radius=2.5
  constraints (17):
    c: Coincident(g0,g1)
    c: Coincident(g1,g2)
    c: Coincident(g2,g3)
    c: Coincident(g3,g4)
    c: Coincident(g4,g5)
    c: Coincident(g5,g0)
    c: Equal(g0, g1-g5) x5
    c: PointOnObject(g0,g6)
    c: PointOnObject(g1,g6)
    c: PointOnObject(g2,g6)
    c: PointOnObject(g3,g6)
    c: PointOnObject(g4,g6)
    c: PointOnObject(g5,g6)
    c: Coincident(g6,g-1)
    c: Coincident(g7,g6)
    c: Radius(g7) = 2.5
    c: Radius(g6) = 4
FEATURE [PartDesign::Pad] Pad210
  Direction = (1,-2e-16,3e-16)
  Length = 3
  Length2 = 10
  Placement = pos=(0,0,0) rot=(0.57735,0.57735,0.57735;2.0944rad)
  Profile = -> Sketch361
  Type = 0
FEATURE [PartDesign::Pad] Pad207
  BaseFeature = -> Pad210
  Direction = (1,-2e-16,6e-16)
  Length = 15
  Length2 = 10
  Placement = pos=(0,0,0) rot=(0.57735,0.57735,0.57735;2.0944rad)
  Profile = -> Pad210 [Edge20]
  Type = 0
FEATURE [Sketcher::SketchObject] Sketch362
  FullyConstrained = false
  MapMode = 5
  Placement = pos=(0,0,0) rot=(0.57735,0.57735,0.57735;2.0944rad)
  Support = -> [YZ_Plane382]
  sketch-geometry (8):
    g0: LineSegment StartX=2.8963 StartY=-2.75889 StartZ=0 EndX=3.83742 EndY=1.12882 EndZ=0
    g1: LineSegment StartX=3.83742 StartY=1.12882 StartZ=0 EndX=0.941117 EndY=3.88771 EndZ=0
    g2: LineSegment StartX=0.941117 StartY=3.88771 StartZ=0 EndX=-2.8963 EndY=2.75889 EndZ=0
    g3: LineSegment StartX=-2.8963 StartY=2.75889 StartZ=0 EndX=-3.83742 EndY=-1.12882 EndZ=0
    g4: LineSegment StartX=-3.83742 StartY=-1.12882 StartZ=0 EndX=-0.941117 EndY=-3.88771 EndZ=0
    g5: LineSegment StartX=-0.941117 StartY=-3.88771 StartZ=0 EndX=2.8963 EndY=-2.75889 EndZ=0
    g6: Circle CenterX=0 CenterY=0 CenterZ=0 NormalX=0 NormalY=0 NormalZ=1 AngleXU=0 Radius=4
    g7: Circle CenterX=0 CenterY=0 CenterZ=0 NormalX=0 NormalY=0 NormalZ=1 AngleXU=0 Radius=2.5
  constraints (17):
    c: Coincident(g0,g1)
    c: Coincident(g1,g2)
    c: Coincident(g2,g3)
    c: Coincident(g3,g4)
    c: Coincident(g4,g5)
    c: Coincident(g5,g0)
    c: Equal(g0, g1-g5) x5
    c: PointOnObject(g0,g6)
    c: PointOnObject(g1,g6)
    c: PointOnObject(g2,g6)
    c: PointOnObject(g3,g6)
    c: PointOnObject(g4,g6)
    c: PointOnObject(g5,g6)
    c: Coincident(g6,g-1)
    c: Coincident(g7,g6)
    c: Radius(g7) = 2.5
    c: Radius(g6) = 4
FEATURE [PartDesign::Pad] Pad209
  Direction = (1,-2e-16,3e-16)
  Length = 3
  Length2 = 10
  Placement = pos=(0,0,0) rot=(0.57735,0.57735,0.57735;2.0944rad)
  Profile = -> Sketch362
  Type = 0
FEATURE [PartDesign::Body] Body263
  Group = -> [Sketch361,Pad210,Pad207]
  Origin = -> Origin391
  Tip = -> Pad207
FEATURE [PartDesign::Pad] Pad211
  BaseFeature = -> Pad209
  Direction = (1,-2e-16,6e-16)
  Length = 15
  Length2 = 10
  Placement = pos=(0,0,0) rot=(0.57735,0.57735,0.57735;2.0944rad)
  Profile = -> Pad209 [Edge20]
  Type = 0
FEATURE [PartDesign::Body] Body265
  Group = -> [Sketch362,Pad209,Pad211]
  Origin = -> Origin393
  Tip = -> Pad211
FEATURE [App::Part] Part124  label="tornillo M5-15-037"
  Group = -> [Body265]
  Origin = -> Origin387
  Placement = pos=(357,108,88) rot=(0,1,0;1.5708rad)
FEATURE [PartDesign::Pad] Pad212
  BaseFeature = -> Pad208
  Direction = (1,-2e-16,6e-16)
  Length = 15
  Length2 = 10
  Placement = pos=(0,0,0) rot=(0.57735,0.57735,0.57735;2.0944rad)
  Profile = -> Pad208 [Edge20]
  Type = 0
FEATURE [PartDesign::Body] Body266
  Group = -> [Sketch359,Pad208,Pad212]
  Origin = -> Origin390
  Tip = -> Pad212
FEATURE [App::Part] Part125  label="tornillo M5-15-038"
  Group = -> [Body266]
  Origin = -> Origin392
  Placement = pos=(379,108,88) rot=(0,1,0;1.5708rad)
FEATURE [App::Part] Part127  label="tornillo M5-15-040"
  Group = -> [Body263]
  Origin = -> Origin389
  Placement = pos=(357,108,88) rot=(0,1,0;1.5708rad)
FEATURE [App::LinkGroup] LinkGroup028
  ElementList = -> [Part127,Part125]
  LinkMode = 0
  Placement = pos=(0,25,0) rot=(0,0,1;0rad)
FEATURE [PartDesign::Pad] Pad213
  BaseFeature = -> Pad206
  Direction = (1,-2e-16,6e-16)
  Length = 15
  Length2 = 10
  Placement = pos=(0,0,0) rot=(0.57735,0.57735,0.57735;2.0944rad)
  Profile = -> Pad206 [Edge20]
  Type = 0
FEATURE [PartDesign::Body] Body264
  Group = -> [Sketch360,Pad206,Pad213]
  Origin = -> Origin388
  Tip = -> Pad213
FEATURE [App::Part] Part126  label="tornillo M5-15-039"
  Group = -> [Body264]
  Origin = -> Origin394
  Placement = pos=(379,108,88) rot=(0,1,0;1.5708rad)
FEATURE [App::LinkGroup] LinkGroup029
  ElementList = -> [Part124,Part126,LinkGroup028]
  LinkMode = 0
  Placement = pos=(-3.05176e-05,126,-7.62939e-06) rot=(0,0,1;0rad)
FEATURE [Sketcher::SketchObject] Sketch363
  FullyConstrained = false
  MapMode = 5
  Placement = pos=(0,0,0) rot=(0.57735,0.57735,0.57735;2.0944rad)
  Support = -> [YZ_Plane389]
  sketch-geometry (8):
    g0: LineSegment StartX=2.8963 StartY=-2.75889 StartZ=0 EndX=3.83742 EndY=1.12882 EndZ=0
    g1: LineSegment StartX=3.83742 StartY=1.12882 StartZ=0 EndX=0.941117 EndY=3.88771 EndZ=0
    g2: LineSegment StartX=0.941117 StartY=3.88771 StartZ=0 EndX=-2.8963 EndY=2.75889 EndZ=0
    g3: LineSegment StartX=-2.8963 StartY=2.75889 StartZ=0 EndX=-3.83742 EndY=-1.12882 EndZ=0
    g4: LineSegment StartX=-3.83742 StartY=-1.12882 StartZ=0 EndX=-0.941117 EndY=-3.88771 EndZ=0
    g5: LineSegment StartX=-0.941117 StartY=-3.88771 StartZ=0 EndX=2.8963 EndY=-2.75889 EndZ=0
    g6: Circle CenterX=0 CenterY=0 CenterZ=0 NormalX=0 NormalY=0 NormalZ=1 AngleXU=0 Radius=4
    g7: Circle CenterX=0 CenterY=0 CenterZ=0 NormalX=0 NormalY=0 NormalZ=1 AngleXU=0 Radius=2.5
  constraints (17):
    c: Coincident(g0,g1)
    c: Coincident(g1,g2)
    c: Coincident(g2,g3)
    c: Coincident(g3,g4)
    c: Coincident(g4,g5)
    c: Coincident(g5,g0)
    c: Equal(g0, g1-g5) x5
    c: PointOnObject(g0,g6)
    c: PointOnObject(g1,g6)
    c: PointOnObject(g2,g6)
    c: PointOnObject(g3,g6)
    c: PointOnObject(g4,g6)
    c: PointOnObject(g5,g6)
    c: Coincident(g6,g-1)
    c: Coincident(g7,g6)
    c: Radius(g7) = 2.5
    c: Radius(g6) = 4
FEATURE [PartDesign::Pad] Pad214
  Direction = (1,-2e-16,3e-16)
  Length = 3
  Length2 = 10
  Placement = pos=(0,0,0) rot=(0.57735,0.57735,0.57735;2.0944rad)
  Profile = -> Sketch363
  Type = 0
FEATURE [PartDesign::Pad] Pad215
  BaseFeature = -> Pad214
  Direction = (1,-2e-16,6e-16)
  Length = 15
  Length2 = 10
  Placement = pos=(0,0,0) rot=(0.57735,0.57735,0.57735;2.0944rad)
  Profile = -> Pad214 [Edge20]
  Type = 0
FEATURE [PartDesign::Body] Body267
  Group = -> [Sketch363,Pad214,Pad215]
  Origin = -> Origin395
  Tip = -> Pad215
FEATURE [App::Part] Part128  label="tornillo M5-15-041"
  Group = -> [Body267]
  Origin = -> Origin396
  Placement = pos=(345,10,70) rot=(0,1,0;3.14159rad)
FEATURE [Sketcher::SketchObject] Sketch364
  FullyConstrained = false
  MapMode = 5
  Placement = pos=(0,0,0) rot=(0.57735,0.57735,0.57735;2.0944rad)
  Support = -> [YZ_Plane391]
  sketch-geometry (8):
    g0: LineSegment StartX=2.8963 StartY=-2.75889 StartZ=0 EndX=3.83742 EndY=1.12882 EndZ=0
    g1: LineSegment StartX=3.83742 StartY=1.12882 StartZ=0 EndX=0.941117 EndY=3.88771 EndZ=0
    g2: LineSegment StartX=0.941117 StartY=3.88771 StartZ=0 EndX=-2.8963 EndY=2.75889 EndZ=0
    g3: LineSegment StartX=-2.8963 StartY=2.75889 StartZ=0 EndX=-3.83742 EndY=-1.12882 EndZ=0
    g4: LineSegment StartX=-3.83742 StartY=-1.12882 StartZ=0 EndX=-0.941117 EndY=-3.88771 EndZ=0
    g5: LineSegment StartX=-0.941117 StartY=-3.88771 StartZ=0 EndX=2.8963 EndY=-2.75889 EndZ=0
    g6: Circle CenterX=0 CenterY=0 CenterZ=0 NormalX=0 NormalY=0 NormalZ=1 AngleXU=0 Radius=4
    g7: Circle CenterX=0 CenterY=0 CenterZ=0 NormalX=0 NormalY=0 NormalZ=1 AngleXU=0 Radius=2.5
  constraints (17):
    c: Coincident(g0,g1)
    c: Coincident(g1,g2)
    c: Coincident(g2,g3)
    c: Coincident(g3,g4)
    c: Coincident(g4,g5)
    c: Coincident(g5,g0)
    c: Equal(g0, g1-g5) x5
    c: PointOnObject(g0,g6)
    c: PointOnObject(g1,g6)
    c: PointOnObject(g2,g6)
    c: PointOnObject(g3,g6)
    c: PointOnObject(g4,g6)
    c: PointOnObject(g5,g6)
    c: Coincident(g6,g-1)
    c: Coincident(g7,g6)
    c: Radius(g7) = 2.5
    c: Radius(g6) = 4
FEATURE [PartDesign::Pad] Pad217
  Direction = (1,-2e-16,3e-16)
  Length = 3
  Length2 = 10
  Placement = pos=(0,0,0) rot=(0.57735,0.57735,0.57735;2.0944rad)
  Profile = -> Sketch364
  Type = 0
FEATURE [PartDesign::Pad] Pad216
  BaseFeature = -> Pad217
  Direction = (1,-2e-16,6e-16)
  Length = 15
  Length2 = 10
  Placement = pos=(0,0,0) rot=(0.57735,0.57735,0.57735;2.0944rad)
  Profile = -> Pad217 [Edge20]
  Type = 0
FEATURE [PartDesign::Body] Body268
  Group = -> [Sketch364,Pad217,Pad216]
  Origin = -> Origin398
  Tip = -> Pad216
FEATURE [App::Part] Part129  label="tornillo M5-15-042"
  Group = -> [Body268]
  Origin = -> Origin397
  Placement = pos=(345,330,70) rot=(0,1,0;3.14159rad)
FEATURE [Sketcher::SketchObject] Sketch365
  FullyConstrained = false
  MapMode = 5
  Placement = pos=(0,0,0) rot=(0.57735,0.57735,0.57735;2.0944rad)
  Support = -> [YZ_Plane393]
  sketch-geometry (4):
    g0: ArcOfCircle CenterX=0 CenterY=0 CenterZ=0 NormalX=0 NormalY=0 NormalZ=1 AngleXU=0 Radius=59.8228 StartAngle=1.62097 EndAngle=7.80381
    g1: LineSegment StartX=3 StartY=59.7476 StartZ=0 EndX=3 EndY=55.9928 EndZ=0
    g2: LineSegment StartX=3 StartY=55.9928 StartZ=0 EndX=-3 EndY=55.9928 EndZ=0
    g3: LineSegment StartX=-3 StartY=55.9928 StartZ=0 EndX=-3 EndY=59.7476 EndZ=0
  constraints (10):
    c: Coincident(g0,g-1)
    c: Coincident(g1,g2)
    c: Coincident(g2,g3)
    c: Horizontal(g2)
    c: Vertical(g1)
    c: Vertical(g3)
    c: DistanceX(g0,g1) = 3
    c: DistanceX(g2,g0) = 3
    c: Coincident(g1,g0)
    c: Coincident(g3,g0)
FEATURE [PartDesign::Pad] Pad218
  Direction = (1,1,1)
  Length = 8
  Length2 = 100
  Placement = pos=(0,0,0) rot=(0.57735,0.57735,0.57735;2.0944rad)
  Profile = -> Sketch365
  Type = 0
FEATURE [PartDesign::Body] Body269  label="ruedaCuatro"
  Group = -> [Sketch365,Pad218]
  Origin = -> Origin399
  Placement = pos=(121,246,105) rot=(0,0,1;0rad)
  Tip = -> Pad218
FEATURE [Sketcher::SketchObject] Sketch367
  FullyConstrained = false
  MapMode = 5
  Placement = pos=(0,0,0) rot=(0.57735,0.57735,0.57735;2.0944rad)
  Support = -> [YZ_Plane395]
  sketch-geometry (2):
    g0: ArcOfCircle CenterX=0 CenterY=0 CenterZ=0 NormalX=0 NormalY=0 NormalZ=1 AngleXU=0 Radius=59.853 StartAngle=2.93973 EndAngle=6.48504
    g1: LineSegment StartX=-58.6378 StartY=12 StartZ=0 EndX=58.6378 EndY=12 EndZ=0
  constraints (3):
    c: Coincident(g0,g-1)
    c: Coincident(g1,g0)
    c: Coincident(g1,g0)
FEATURE [PartDesign::Pad] Pad220
  Direction = (1,1,1)
  Length = 8
  Length2 = 100
  Placement = pos=(0,0,0) rot=(0.57735,0.57735,0.57735;2.0944rad)
  Profile = -> Sketch367
  Type = 0
FEATURE [PartDesign::Body] Body271  label="ruedaCinco"
  Group = -> [Sketch367,Pad220]
  Origin = -> Origin401
  Placement = pos=(257,245,106) rot=(0,0,1;0rad)
  Tip = -> Pad220
FEATURE [Sketcher::SketchObject] Sketch368
  FullyConstrained = false
  MapMode = 5
  Placement = pos=(0,0,0) rot=(0.57735,0.57735,0.57735;2.0944rad)
  Support = -> [YZ_Plane397]
  sketch-geometry (8):
    g0: LineSegment StartX=2.8963 StartY=-2.75889 StartZ=0 EndX=3.83742 EndY=1.12882 EndZ=0
    g1: LineSegment StartX=3.83742 StartY=1.12882 StartZ=0 EndX=0.941117 EndY=3.88771 EndZ=0
    g2: LineSegment StartX=0.941117 StartY=3.88771 StartZ=0 EndX=-2.8963 EndY=2.75889 EndZ=0
    g3: LineSegment StartX=-2.8963 StartY=2.75889 StartZ=0 EndX=-3.83742 EndY=-1.12882 EndZ=0
    g4: LineSegment StartX=-3.83742 StartY=-1.12882 StartZ=0 EndX=-0.941117 EndY=-3.88771 EndZ=0
    g5: LineSegment StartX=-0.941117 StartY=-3.88771 StartZ=0 EndX=2.8963 EndY=-2.75889 EndZ=0
    g6: Circle CenterX=0 CenterY=0 CenterZ=0 NormalX=0 NormalY=0 NormalZ=1 AngleXU=0 Radius=4
    g7: Circle CenterX=0 CenterY=0 CenterZ=0 NormalX=0 NormalY=0 NormalZ=1 AngleXU=0 Radius=2.5
  constraints (17):
    c: Coincident(g0,g1)
    c: Coincident(g1,g2)
    c: Coincident(g2,g3)
    c: Coincident(g3,g4)
    c: Coincident(g4,g5)
    c: Coincident(g5,g0)
    c: Equal(g0, g1-g5) x5
    c: PointOnObject(g0,g6)
    c: PointOnObject(g1,g6)
    c: PointOnObject(g2,g6)
    c: PointOnObject(g3,g6)
    c: PointOnObject(g4,g6)
    c: PointOnObject(g5,g6)
    c: Coincident(g6,g-1)
    c: Coincident(g7,g6)
    c: Radius(g7) = 2.5
    c: Radius(g6) = 4
FEATURE [PartDesign::Pad] Pad221
  Direction = (1,-2e-16,3e-16)
  Length = 3
  Length2 = 10
  Placement = pos=(0,0,0) rot=(0.57735,0.57735,0.57735;2.0944rad)
  Profile = -> Sketch368
  Type = 0
FEATURE [PartDesign::Pad] Pad222
  BaseFeature = -> Pad221
  Direction = (1,-2e-16,6e-16)
  Length = 15
  Length2 = 10
  Placement = pos=(0,0,0) rot=(0.57735,0.57735,0.57735;2.0944rad)
  Profile = -> Pad221 [Edge20]
  Type = 0
FEATURE [PartDesign::Body] Body272
  Group = -> [Sketch368,Pad221,Pad222]
  Origin = -> Origin403
  Tip = -> Pad222
FEATURE [App::Part] Part130  label="tornillo M5-15-043"
  Group = -> [Body272]
  Origin = -> Origin402
  Placement = pos=(327,28,57) rot=(0.707107,-0.707107,0;3.14159rad)
FEATURE [Sketcher::SketchObject] Sketch369
  FullyConstrained = false
  MapMode = 5
  Placement = pos=(0,0,0) rot=(0.57735,0.57735,0.57735;2.0944rad)
  Support = -> [YZ_Plane398]
  sketch-geometry (8):
    g0: LineSegment StartX=2.8963 StartY=-2.75889 StartZ=0 EndX=3.83742 EndY=1.12882 EndZ=0
    g1: LineSegment StartX=3.83742 StartY=1.12882 StartZ=0 EndX=0.941117 EndY=3.88771 EndZ=0
    g2: LineSegment StartX=0.941117 StartY=3.88771 StartZ=0 EndX=-2.8963 EndY=2.75889 EndZ=0
    g3: LineSegment StartX=-2.8963 StartY=2.75889 StartZ=0 EndX=-3.83742 EndY=-1.12882 EndZ=0
    g4: LineSegment StartX=-3.83742 StartY=-1.12882 StartZ=0 EndX=-0.941117 EndY=-3.88771 EndZ=0
    g5: LineSegment StartX=-0.941117 StartY=-3.88771 StartZ=0 EndX=2.8963 EndY=-2.75889 EndZ=0
    g6: Circle CenterX=0 CenterY=0 CenterZ=0 NormalX=0 NormalY=0 NormalZ=1 AngleXU=0 Radius=4
    g7: Circle CenterX=0 CenterY=0 CenterZ=0 NormalX=0 NormalY=0 NormalZ=1 AngleXU=0 Radius=2.5
  constraints (17):
    c: Coincident(g0,g1)
    c: Coincident(g1,g2)
    c: Coincident(g2,g3)
    c: Coincident(g3,g4)
    c: Coincident(g4,g5)
    c: Coincident(g5,g0)
    c: Equal(g0, g1-g5) x5
    c: PointOnObject(g0,g6)
    c: PointOnObject(g1,g6)
    c: PointOnObject(g2,g6)
    c: PointOnObject(g3,g6)
    c: PointOnObject(g4,g6)
    c: PointOnObject(g5,g6)
    c: Coincident(g6,g-1)
    c: Coincident(g7,g6)
    c: Radius(g7) = 2.5
    c: Radius(g6) = 4
FEATURE [PartDesign::Pad] Pad223
  Direction = (1,-2e-16,3e-16)
  Length = 3
  Length2 = 10
  Placement = pos=(0,0,0) rot=(0.57735,0.57735,0.57735;2.0944rad)
  Profile = -> Sketch369
  Type = 0
FEATURE [PartDesign::Pad] Pad224
  BaseFeature = -> Pad223
  Direction = (1,-2e-16,6e-16)
  Length = 15
  Length2 = 10
  Placement = pos=(0,0,0) rot=(0.57735,0.57735,0.57735;2.0944rad)
  Profile = -> Pad223 [Edge20]
  Type = 0
FEATURE [PartDesign::Body] Body273
  Group = -> [Sketch369,Pad223,Pad224]
  Origin = -> Origin405
  Tip = -> Pad224
FEATURE [App::Part] Part131  label="tornillo M5-15-044"
  Group = -> [Body273]
  Origin = -> Origin404
  Placement = pos=(328,31,64) rot=(-0.57735,0.57735,-0.57735;4.18879rad)
FEATURE [App::LinkGroup] LinkGroup030
  ElementList = -> [Part130,Part131]
  LinkMode = 0
  Placement = pos=(-317,1.00006,-1.52588e-05) rot=(0,0,1;0rad)
FEATURE [Sketcher::SketchObject] Sketch370
  FullyConstrained = false
  MapMode = 5
  Placement = pos=(0,0,0) rot=(0.57735,0.57735,0.57735;2.0944rad)
  Support = -> [YZ_Plane402]
  sketch-geometry (8):
    g0: LineSegment StartX=2.8963 StartY=-2.75889 StartZ=0 EndX=3.83742 EndY=1.12882 EndZ=0
    g1: LineSegment StartX=3.83742 StartY=1.12882 StartZ=0 EndX=0.941117 EndY=3.88771 EndZ=0
    g2: LineSegment StartX=0.941117 StartY=3.88771 StartZ=0 EndX=-2.8963 EndY=2.75889 EndZ=0
    g3: LineSegment StartX=-2.8963 StartY=2.75889 StartZ=0 EndX=-3.83742 EndY=-1.12882 EndZ=0
    g4: LineSegment StartX=-3.83742 StartY=-1.12882 StartZ=0 EndX=-0.941117 EndY=-3.88771 EndZ=0
    g5: LineSegment StartX=-0.941117 StartY=-3.88771 StartZ=0 EndX=2.8963 EndY=-2.75889 EndZ=0
    g6: Circle CenterX=0 CenterY=0 CenterZ=0 NormalX=0 NormalY=0 NormalZ=1 AngleXU=0 Radius=4
    g7: Circle CenterX=0 CenterY=0 CenterZ=0 NormalX=0 NormalY=0 NormalZ=1 AngleXU=0 Radius=2.5
  constraints (17):
    c: Coincident(g0,g1)
    c: Coincident(g1,g2)
    c: Coincident(g2,g3)
    c: Coincident(g3,g4)
    c: Coincident(g4,g5)
    c: Coincident(g5,g0)
    c: Equal(g0, g1-g5) x5
    c: PointOnObject(g0,g6)
    c: PointOnObject(g1,g6)
    c: PointOnObject(g2,g6)
    c: PointOnObject(g3,g6)
    c: PointOnObject(g4,g6)
    c: PointOnObject(g5,g6)
    c: Coincident(g6,g-1)
    c: Coincident(g7,g6)
    c: Radius(g7) = 2.5
    c: Radius(g6) = 4
FEATURE [Sketcher::SketchObject] Sketch371
  FullyConstrained = false
  MapMode = 5
  Placement = pos=(0,0,0) rot=(0.57735,0.57735,0.57735;2.0944rad)
  Support = -> [YZ_Plane400]
  sketch-geometry (8):
    g0: LineSegment StartX=2.8963 StartY=-2.75889 StartZ=0 EndX=3.83742 EndY=1.12882 EndZ=0
    g1: LineSegment StartX=3.83742 StartY=1.12882 StartZ=0 EndX=0.941117 EndY=3.88771 EndZ=0
    g2: LineSegment StartX=0.941117 StartY=3.88771 StartZ=0 EndX=-2.8963 EndY=2.75889 EndZ=0
    g3: LineSegment StartX=-2.8963 StartY=2.75889 StartZ=0 EndX=-3.83742 EndY=-1.12882 EndZ=0
    g4: LineSegment StartX=-3.83742 StartY=-1.12882 StartZ=0 EndX=-0.941117 EndY=-3.88771 EndZ=0
    g5: LineSegment StartX=-0.941117 StartY=-3.88771 StartZ=0 EndX=2.8963 EndY=-2.75889 EndZ=0
    g6: Circle CenterX=0 CenterY=0 CenterZ=0 NormalX=0 NormalY=0 NormalZ=1 AngleXU=0 Radius=4
    g7: Circle CenterX=0 CenterY=0 CenterZ=0 NormalX=0 NormalY=0 NormalZ=1 AngleXU=0 Radius=2.5
  constraints (17):
    c: Coincident(g0,g1)
    c: Coincident(g1,g2)
    c: Coincident(g2,g3)
    c: Coincident(g3,g4)
    c: Coincident(g4,g5)
    c: Coincident(g5,g0)
    c: Equal(g0, g1-g5) x5
    c: PointOnObject(g0,g6)
    c: PointOnObject(g1,g6)
    c: PointOnObject(g2,g6)
    c: PointOnObject(g3,g6)
    c: PointOnObject(g4,g6)
    c: PointOnObject(g5,g6)
    c: Coincident(g6,g-1)
    c: Coincident(g7,g6)
    c: Radius(g7) = 2.5
    c: Radius(g6) = 4
FEATURE [PartDesign::Pad] Pad226
  Direction = (1,-2e-16,3e-16)
  Length = 3
  Length2 = 10
  Placement = pos=(0,0,0) rot=(0.57735,0.57735,0.57735;2.0944rad)
  Profile = -> Sketch370
  Type = 0
FEATURE [PartDesign::Pad] Pad227
  Direction = (1,-2e-16,3e-16)
  Length = 3
  Length2 = 10
  Placement = pos=(0,0,0) rot=(0.57735,0.57735,0.57735;2.0944rad)
  Profile = -> Sketch371
  Type = 0
FEATURE [PartDesign::Pad] Pad225
  BaseFeature = -> Pad227
  Direction = (1,-2e-16,6e-16)
  Length = 15
  Length2 = 10
  Placement = pos=(0,0,0) rot=(0.57735,0.57735,0.57735;2.0944rad)
  Profile = -> Pad227 [Edge20]
  Type = 0
FEATURE [PartDesign::Body] Body274
  Group = -> [Sketch371,Pad227,Pad225]
  Origin = -> Origin406
  Tip = -> Pad225
FEATURE [App::Part] Part132  label="tornillo M5-15-045"
  Group = -> [Body274]
  Origin = -> Origin409
  Placement = pos=(327,28,57) rot=(0.707107,-0.707107,0;3.14159rad)
FEATURE [PartDesign::Pad] Pad228
  BaseFeature = -> Pad226
  Direction = (1,-2e-16,6e-16)
  Length = 15
  Length2 = 10
  Placement = pos=(0,0,0) rot=(0.57735,0.57735,0.57735;2.0944rad)
  Profile = -> Pad226 [Edge20]
  Type = 0
FEATURE [PartDesign::Body] Body275
  Group = -> [Sketch370,Pad226,Pad228]
  Origin = -> Origin408
  Tip = -> Pad228
FEATURE [App::Part] Part133  label="tornillo M5-15-046"
  Group = -> [Body275]
  Origin = -> Origin407
  Placement = pos=(328,31,64) rot=(-0.57735,0.57735,-0.57735;4.18879rad)
FEATURE [App::LinkGroup] LinkGroup031
  ElementList = -> [Part132,Part133]
  LinkMode = 0
  Placement = pos=(319.16,425.532,-1.52588e-05) rot=(0,0,1;3.40339rad)
